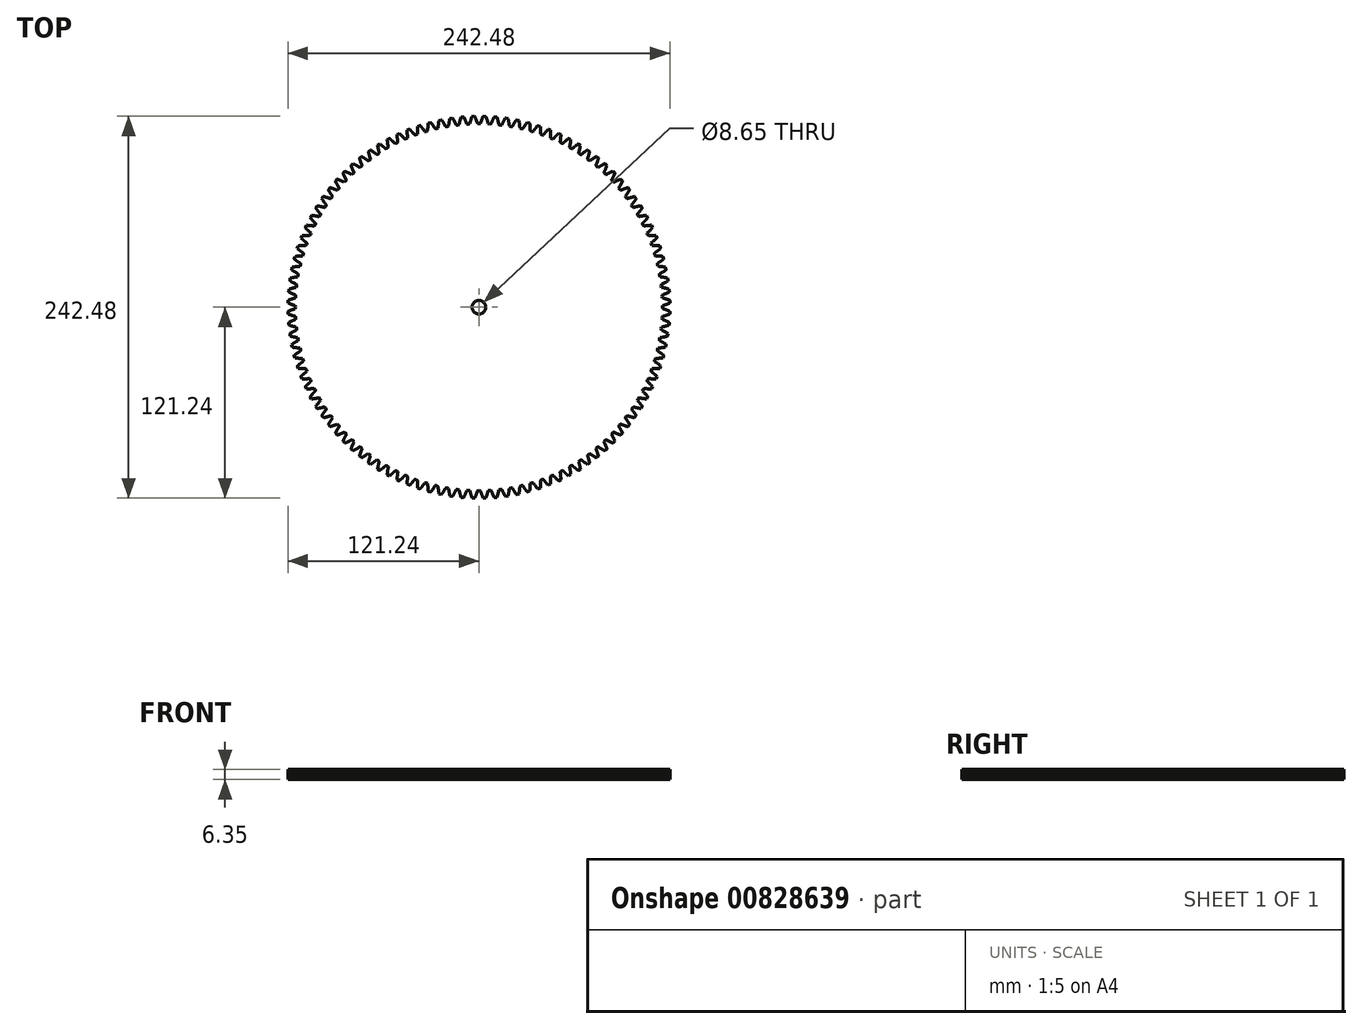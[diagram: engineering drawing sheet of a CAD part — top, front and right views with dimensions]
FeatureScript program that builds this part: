
annotation { "Feature Type Name" : "Feature", "Feature Type Description" : "" }
export const myFeature = defineFeature(function(context is Context, id is Id, definition is map)
    precondition{}
    {
        {
            var Q0;
            Q0=qCreatedBy(makeId("Top.planeOp"),FACE);
            var sketch = newSketch(context, id + "F0", { "sketchPlane" : qUnion([Q0])});
            skLineSegment(sketch, "E0", {"start": v(116.53, 0) * mm, "end": v(116.7, 0.97) * mm});
            skLineSegment(sketch, "E1", {"start": v(116.7, 0.97) * mm, "end": v(116.9, 1.03) * mm});
            skLineSegment(sketch, "E2", {"start": v(116.9, 1.03) * mm, "end": v(117.01, 1.06) * mm});
            skLineSegment(sketch, "E3", {"start": v(117.01, 1.06) * mm, "end": v(117.22, 1.13) * mm});
            skLineSegment(sketch, "E4", {"start": v(117.22, 1.13) * mm, "end": v(117.33, 1.17) * mm});
            skLineSegment(sketch, "E5", {"start": v(117.33, 1.17) * mm, "end": v(117.44, 1.2) * mm});
            skLineSegment(sketch, "E6", {"start": v(117.44, 1.2) * mm, "end": v(117.55, 1.24) * mm});
            skLineSegment(sketch, "E7", {"start": v(117.55, 1.24) * mm, "end": v(117.66, 1.28) * mm});
            skLineSegment(sketch, "E8", {"start": v(117.66, 1.28) * mm, "end": v(117.78, 1.31) * mm});
            skLineSegment(sketch, "E9", {"start": v(117.78, 1.31) * mm, "end": v(117.89, 1.35) * mm});
            skLineSegment(sketch, "E10", {"start": v(117.89, 1.35) * mm, "end": v(118, 1.4) * mm});
            skLineSegment(sketch, "E11", {"start": v(118, 1.4) * mm, "end": v(118.12, 1.43) * mm});
            skLineSegment(sketch, "E12", {"start": v(118.12, 1.43) * mm, "end": v(118.23, 1.47) * mm});
            skLineSegment(sketch, "E13", {"start": v(118.23, 1.47) * mm, "end": v(118.35, 1.52) * mm});
            skLineSegment(sketch, "E14", {"start": v(118.35, 1.52) * mm, "end": v(118.59, 1.6) * mm});
            skLineSegment(sketch, "E15", {"start": v(118.59, 1.6) * mm, "end": v(118.7, 1.65) * mm});
            skLineSegment(sketch, "E16", {"start": v(118.7, 1.65) * mm, "end": v(118.95, 1.74) * mm});
            skLineSegment(sketch, "E17", {"start": v(118.95, 1.74) * mm, "end": v(119.07, 1.78) * mm});
            skLineSegment(sketch, "E18", {"start": v(119.07, 1.78) * mm, "end": v(119.32, 1.88) * mm});
            skLineSegment(sketch, "E19", {"start": v(119.32, 1.88) * mm, "end": v(119.45, 1.93) * mm});
            skLineSegment(sketch, "E20", {"start": v(119.45, 1.93) * mm, "end": v(119.57, 1.98) * mm});
            skLineSegment(sketch, "E21", {"start": v(119.57, 1.98) * mm, "end": v(119.7, 2.03) * mm});
            skLineSegment(sketch, "E22", {"start": v(119.7, 2.03) * mm, "end": v(119.96, 2.13) * mm});
            skLineSegment(sketch, "E23", {"start": v(119.96, 2.13) * mm, "end": v(120.09, 2.19) * mm});
            skLineSegment(sketch, "E24", {"start": v(120.09, 2.19) * mm, "end": v(120.22, 2.24) * mm});
            skLineSegment(sketch, "E25", {"start": v(120.22, 2.24) * mm, "end": v(120.48, 2.35) * mm});
            skLineSegment(sketch, "E26", {"start": v(120.48, 2.35) * mm, "end": v(120.62, 2.4) * mm});
            skLineSegment(sketch, "E27", {"start": v(120.62, 2.4) * mm, "end": v(120.75, 2.47) * mm});
            skLineSegment(sketch, "E28", {"start": v(120.75, 2.47) * mm, "end": v(120.89, 2.52) * mm});
            skLineSegment(sketch, "E29", {"start": v(120.89, 2.52) * mm, "end": v(121.02, 2.58) * mm});
            skLineSegment(sketch, "E30", {"start": v(121.02, 2.58) * mm, "end": v(121.16, 2.64) * mm});
            skLineSegment(sketch, "E31", {"start": v(121.16, 2.64) * mm, "end": v(121.24, 2.7) * mm});
            skLineSegment(sketch, "E32", {"start": v(121.24, 2.7) * mm, "end": v(121.19, 4.36) * mm});
            skLineSegment(sketch, "E33", {"start": v(121.19, 4.36) * mm, "end": v(121.1, 4.42) * mm});
            skLineSegment(sketch, "E34", {"start": v(121.1, 4.42) * mm, "end": v(120.97, 4.47) * mm});
            skLineSegment(sketch, "E35", {"start": v(120.97, 4.47) * mm, "end": v(120.83, 4.52) * mm});
            skLineSegment(sketch, "E36", {"start": v(120.83, 4.52) * mm, "end": v(120.69, 4.57) * mm});
            skLineSegment(sketch, "E37", {"start": v(120.69, 4.57) * mm, "end": v(120.55, 4.62) * mm});
            skLineSegment(sketch, "E38", {"start": v(120.55, 4.62) * mm, "end": v(120.28, 4.72) * mm});
            skLineSegment(sketch, "E39", {"start": v(120.28, 4.72) * mm, "end": v(120.15, 4.77) * mm});
            skLineSegment(sketch, "E40", {"start": v(120.15, 4.77) * mm, "end": v(120.01, 4.81) * mm});
            skLineSegment(sketch, "E41", {"start": v(120.01, 4.81) * mm, "end": v(119.75, 4.9) * mm});
            skLineSegment(sketch, "E42", {"start": v(119.75, 4.9) * mm, "end": v(119.61, 4.95) * mm});
            skLineSegment(sketch, "E43", {"start": v(119.61, 4.95) * mm, "end": v(119.48, 5) * mm});
            skLineSegment(sketch, "E44", {"start": v(119.48, 5) * mm, "end": v(119.36, 5.03) * mm});
            skLineSegment(sketch, "E45", {"start": v(119.36, 5.03) * mm, "end": v(119.1, 5.12) * mm});
            skLineSegment(sketch, "E46", {"start": v(119.1, 5.12) * mm, "end": v(118.97, 5.16) * mm});
            skLineSegment(sketch, "E47", {"start": v(118.97, 5.16) * mm, "end": v(118.85, 5.2) * mm});
            skLineSegment(sketch, "E48", {"start": v(118.85, 5.2) * mm, "end": v(118.6, 5.27) * mm});
            skLineSegment(sketch, "E49", {"start": v(118.6, 5.27) * mm, "end": v(118.48, 5.3) * mm});
            skLineSegment(sketch, "E50", {"start": v(118.48, 5.3) * mm, "end": v(118.36, 5.35) * mm});
            skLineSegment(sketch, "E51", {"start": v(118.36, 5.35) * mm, "end": v(118.24, 5.38) * mm});
            skLineSegment(sketch, "E52", {"start": v(118.24, 5.38) * mm, "end": v(118.12, 5.42) * mm});
            skLineSegment(sketch, "E53", {"start": v(118.12, 5.42) * mm, "end": v(118, 5.45) * mm});
            skLineSegment(sketch, "E54", {"start": v(118, 5.45) * mm, "end": v(117.88, 5.48) * mm});
            skLineSegment(sketch, "E55", {"start": v(117.88, 5.48) * mm, "end": v(117.77, 5.52) * mm});
            skLineSegment(sketch, "E56", {"start": v(117.77, 5.52) * mm, "end": v(117.65, 5.55) * mm});
            skLineSegment(sketch, "E57", {"start": v(117.65, 5.55) * mm, "end": v(117.54, 5.58) * mm});
            skLineSegment(sketch, "E58", {"start": v(117.54, 5.58) * mm, "end": v(117.42, 5.61) * mm});
            skLineSegment(sketch, "E59", {"start": v(117.42, 5.61) * mm, "end": v(117.31, 5.64) * mm});
            skLineSegment(sketch, "E60", {"start": v(117.31, 5.64) * mm, "end": v(117.1, 5.7) * mm});
            skLineSegment(sketch, "E61", {"start": v(117.1, 5.7) * mm, "end": v(116.98, 5.73) * mm});
            skLineSegment(sketch, "E62", {"start": v(116.98, 5.73) * mm, "end": v(116.87, 5.76) * mm});
            skLineSegment(sketch, "E63", {"start": v(116.87, 5.76) * mm, "end": v(116.66, 5.8) * mm});
            skLineSegment(sketch, "E64", {"start": v(116.66, 5.8) * mm, "end": v(116.56, 5.83) * mm});
            skLineSegment(sketch, "E65", {"start": v(116.56, 5.83) * mm, "end": v(116.33, 6.78) * mm});
            skLineSegment(sketch, "E66", {"start": v(116.33, 6.78) * mm, "end": v(116.45, 7.75) * mm});
            skLineSegment(sketch, "E67", {"start": v(116.45, 7.75) * mm, "end": v(116.55, 7.79) * mm});
            skLineSegment(sketch, "E68", {"start": v(116.55, 7.79) * mm, "end": v(116.65, 7.83) * mm});
            skLineSegment(sketch, "E69", {"start": v(116.65, 7.83) * mm, "end": v(116.75, 7.86) * mm});
            skLineSegment(sketch, "E70", {"start": v(116.75, 7.86) * mm, "end": v(116.86, 7.9) * mm});
            skLineSegment(sketch, "E71", {"start": v(116.86, 7.9) * mm, "end": v(116.96, 7.95) * mm});
            skLineSegment(sketch, "E72", {"start": v(116.96, 7.95) * mm, "end": v(117.17, 8.03) * mm});
            skLineSegment(sketch, "E73", {"start": v(117.17, 8.03) * mm, "end": v(117.28, 8.07) * mm});
            skLineSegment(sketch, "E74", {"start": v(117.28, 8.07) * mm, "end": v(117.39, 8.12) * mm});
            skLineSegment(sketch, "E75", {"start": v(117.39, 8.12) * mm, "end": v(117.5, 8.16) * mm});
            skLineSegment(sketch, "E76", {"start": v(117.5, 8.16) * mm, "end": v(117.61, 8.2) * mm});
            skLineSegment(sketch, "E77", {"start": v(117.61, 8.2) * mm, "end": v(117.72, 8.25) * mm});
            skLineSegment(sketch, "E78", {"start": v(117.72, 8.25) * mm, "end": v(117.95, 8.35) * mm});
            skLineSegment(sketch, "E79", {"start": v(117.95, 8.35) * mm, "end": v(118.06, 8.4) * mm});
            skLineSegment(sketch, "E80", {"start": v(118.06, 8.4) * mm, "end": v(118.3, 8.5) * mm});
            skLineSegment(sketch, "E81", {"start": v(118.3, 8.5) * mm, "end": v(118.41, 8.55) * mm});
            skLineSegment(sketch, "E82", {"start": v(118.41, 8.55) * mm, "end": v(118.65, 8.65) * mm});
            skLineSegment(sketch, "E83", {"start": v(118.65, 8.65) * mm, "end": v(118.77, 8.7) * mm});
            skLineSegment(sketch, "E84", {"start": v(118.77, 8.7) * mm, "end": v(118.89, 8.76) * mm});
            skLineSegment(sketch, "E85", {"start": v(118.89, 8.76) * mm, "end": v(119.01, 8.81) * mm});
            skLineSegment(sketch, "E86", {"start": v(119.01, 8.81) * mm, "end": v(119.13, 8.87) * mm});
            skLineSegment(sketch, "E87", {"start": v(119.13, 8.87) * mm, "end": v(119.26, 8.93) * mm});
            skLineSegment(sketch, "E88", {"start": v(119.26, 8.93) * mm, "end": v(119.38, 8.99) * mm});
            skLineSegment(sketch, "E89", {"start": v(119.38, 8.99) * mm, "end": v(119.5, 9.04) * mm});
            skLineSegment(sketch, "E90", {"start": v(119.5, 9.04) * mm, "end": v(119.63, 9.1) * mm});
            skLineSegment(sketch, "E91", {"start": v(119.63, 9.1) * mm, "end": v(119.76, 9.17) * mm});
            skLineSegment(sketch, "E92", {"start": v(119.76, 9.17) * mm, "end": v(119.89, 9.23) * mm});
            skLineSegment(sketch, "E93", {"start": v(119.89, 9.23) * mm, "end": v(120.01, 9.29) * mm});
            skLineSegment(sketch, "E94", {"start": v(120.01, 9.29) * mm, "end": v(120.14, 9.35) * mm});
            skLineSegment(sketch, "E95", {"start": v(120.14, 9.35) * mm, "end": v(120.27, 9.42) * mm});
            skLineSegment(sketch, "E96", {"start": v(120.27, 9.42) * mm, "end": v(120.4, 9.48) * mm});
            skLineSegment(sketch, "E97", {"start": v(120.4, 9.48) * mm, "end": v(120.54, 9.55) * mm});
            skLineSegment(sketch, "E98", {"start": v(120.54, 9.55) * mm, "end": v(120.67, 9.62) * mm});
            skLineSegment(sketch, "E99", {"start": v(120.67, 9.62) * mm, "end": v(120.8, 9.68) * mm});
            skLineSegment(sketch, "E100", {"start": v(120.8, 9.68) * mm, "end": v(120.87, 9.75) * mm});
            skLineSegment(sketch, "E101", {"start": v(120.87, 9.75) * mm, "end": v(120.73, 11.4) * mm});
            skLineSegment(sketch, "E102", {"start": v(120.73, 11.4) * mm, "end": v(120.65, 11.45) * mm});
            skLineSegment(sketch, "E103", {"start": v(120.65, 11.45) * mm, "end": v(120.5, 11.5) * mm});
            skLineSegment(sketch, "E104", {"start": v(120.5, 11.5) * mm, "end": v(120.22, 11.58) * mm});
            skLineSegment(sketch, "E105", {"start": v(120.22, 11.58) * mm, "end": v(120.08, 11.62) * mm});
            skLineSegment(sketch, "E106", {"start": v(120.08, 11.62) * mm, "end": v(119.94, 11.66) * mm});
            skLineSegment(sketch, "E107", {"start": v(119.94, 11.66) * mm, "end": v(119.66, 11.74) * mm});
            skLineSegment(sketch, "E108", {"start": v(119.66, 11.74) * mm, "end": v(119.53, 11.78) * mm});
            skLineSegment(sketch, "E109", {"start": v(119.53, 11.78) * mm, "end": v(119.26, 11.86) * mm});
            skLineSegment(sketch, "E110", {"start": v(119.26, 11.86) * mm, "end": v(119.12, 11.9) * mm});
            skLineSegment(sketch, "E111", {"start": v(119.12, 11.9) * mm, "end": v(119, 11.93) * mm});
            skLineSegment(sketch, "E112", {"start": v(119, 11.93) * mm, "end": v(118.86, 11.97) * mm});
            skLineSegment(sketch, "E113", {"start": v(118.86, 11.97) * mm, "end": v(118.73, 12) * mm});
            skLineSegment(sketch, "E114", {"start": v(118.73, 12) * mm, "end": v(118.6, 12.03) * mm});
            skLineSegment(sketch, "E115", {"start": v(118.6, 12.03) * mm, "end": v(118.47, 12.06) * mm});
            skLineSegment(sketch, "E116", {"start": v(118.47, 12.06) * mm, "end": v(118.35, 12.1) * mm});
            skLineSegment(sketch, "E117", {"start": v(118.35, 12.1) * mm, "end": v(118.22, 12.13) * mm});
            skLineSegment(sketch, "E118", {"start": v(118.22, 12.13) * mm, "end": v(118.1, 12.16) * mm});
            skLineSegment(sketch, "E119", {"start": v(118.1, 12.16) * mm, "end": v(117.97, 12.19) * mm});
            skLineSegment(sketch, "E120", {"start": v(117.97, 12.19) * mm, "end": v(117.85, 12.22) * mm});
            skLineSegment(sketch, "E121", {"start": v(117.85, 12.22) * mm, "end": v(117.72, 12.25) * mm});
            skLineSegment(sketch, "E122", {"start": v(117.72, 12.25) * mm, "end": v(117.6, 12.28) * mm});
            skLineSegment(sketch, "E123", {"start": v(117.6, 12.28) * mm, "end": v(117.48, 12.3) * mm});
            skLineSegment(sketch, "E124", {"start": v(117.48, 12.3) * mm, "end": v(117.37, 12.33) * mm});
            skLineSegment(sketch, "E125", {"start": v(117.37, 12.33) * mm, "end": v(117.25, 12.36) * mm});
            skLineSegment(sketch, "E126", {"start": v(117.25, 12.36) * mm, "end": v(117.13, 12.38) * mm});
            skLineSegment(sketch, "E127", {"start": v(117.13, 12.38) * mm, "end": v(117.01, 12.4) * mm});
            skLineSegment(sketch, "E128", {"start": v(117.01, 12.4) * mm, "end": v(116.9, 12.43) * mm});
            skLineSegment(sketch, "E129", {"start": v(116.9, 12.43) * mm, "end": v(116.79, 12.45) * mm});
            skLineSegment(sketch, "E130", {"start": v(116.79, 12.45) * mm, "end": v(116.67, 12.48) * mm});
            skLineSegment(sketch, "E131", {"start": v(116.67, 12.48) * mm, "end": v(116.56, 12.5) * mm});
            skLineSegment(sketch, "E132", {"start": v(116.56, 12.5) * mm, "end": v(116.45, 12.52) * mm});
            skLineSegment(sketch, "E133", {"start": v(116.45, 12.52) * mm, "end": v(116.23, 12.56) * mm});
            skLineSegment(sketch, "E134", {"start": v(116.23, 12.56) * mm, "end": v(116.13, 12.58) * mm});
            skLineSegment(sketch, "E135", {"start": v(116.13, 12.58) * mm, "end": v(116.02, 12.6) * mm});
            skLineSegment(sketch, "E136", {"start": v(116.02, 12.6) * mm, "end": v(115.74, 13.53) * mm});
            skLineSegment(sketch, "E137", {"start": v(115.74, 13.53) * mm, "end": v(115.8, 14.5) * mm});
            skLineSegment(sketch, "E138", {"start": v(115.8, 14.5) * mm, "end": v(116, 14.6) * mm});
            skLineSegment(sketch, "E139", {"start": v(116, 14.6) * mm, "end": v(116.1, 14.64) * mm});
            skLineSegment(sketch, "E140", {"start": v(116.1, 14.64) * mm, "end": v(116.2, 14.69) * mm});
            skLineSegment(sketch, "E141", {"start": v(116.2, 14.69) * mm, "end": v(116.3, 14.73) * mm});
            skLineSegment(sketch, "E142", {"start": v(116.3, 14.73) * mm, "end": v(116.4, 14.78) * mm});
            skLineSegment(sketch, "E143", {"start": v(116.4, 14.78) * mm, "end": v(116.5, 14.83) * mm});
            skLineSegment(sketch, "E144", {"start": v(116.5, 14.83) * mm, "end": v(116.61, 14.88) * mm});
            skLineSegment(sketch, "E145", {"start": v(116.61, 14.88) * mm, "end": v(116.72, 14.93) * mm});
            skLineSegment(sketch, "E146", {"start": v(116.72, 14.93) * mm, "end": v(116.83, 14.98) * mm});
            skLineSegment(sketch, "E147", {"start": v(116.83, 14.98) * mm, "end": v(116.94, 15.03) * mm});
            skLineSegment(sketch, "E148", {"start": v(116.94, 15.03) * mm, "end": v(117.04, 15.08) * mm});
            skLineSegment(sketch, "E149", {"start": v(117.04, 15.08) * mm, "end": v(117.26, 15.2) * mm});
            skLineSegment(sketch, "E150", {"start": v(117.26, 15.2) * mm, "end": v(117.37, 15.25) * mm});
            skLineSegment(sketch, "E151", {"start": v(117.37, 15.25) * mm, "end": v(117.49, 15.3) * mm});
            skLineSegment(sketch, "E152", {"start": v(117.49, 15.3) * mm, "end": v(117.6, 15.36) * mm});
            skLineSegment(sketch, "E153", {"start": v(117.6, 15.36) * mm, "end": v(117.83, 15.47) * mm});
            skLineSegment(sketch, "E154", {"start": v(117.83, 15.47) * mm, "end": v(117.94, 15.53) * mm});
            skLineSegment(sketch, "E155", {"start": v(117.94, 15.53) * mm, "end": v(118.18, 15.66) * mm});
            skLineSegment(sketch, "E156", {"start": v(118.18, 15.66) * mm, "end": v(118.3, 15.72) * mm});
            skLineSegment(sketch, "E157", {"start": v(118.3, 15.72) * mm, "end": v(118.41, 15.78) * mm});
            skLineSegment(sketch, "E158", {"start": v(118.41, 15.78) * mm, "end": v(118.65, 15.91) * mm});
            skLineSegment(sketch, "E159", {"start": v(118.65, 15.91) * mm, "end": v(118.78, 15.98) * mm});
            skLineSegment(sketch, "E160", {"start": v(118.78, 15.98) * mm, "end": v(118.9, 16.04) * mm});
            skLineSegment(sketch, "E161", {"start": v(118.9, 16.04) * mm, "end": v(119.02, 16.11) * mm});
            skLineSegment(sketch, "E162", {"start": v(119.02, 16.11) * mm, "end": v(119.15, 16.18) * mm});
            skLineSegment(sketch, "E163", {"start": v(119.15, 16.18) * mm, "end": v(119.27, 16.25) * mm});
            skLineSegment(sketch, "E164", {"start": v(119.27, 16.25) * mm, "end": v(119.52, 16.4) * mm});
            skLineSegment(sketch, "E165", {"start": v(119.52, 16.4) * mm, "end": v(119.65, 16.47) * mm});
            skLineSegment(sketch, "E166", {"start": v(119.65, 16.47) * mm, "end": v(119.78, 16.54) * mm});
            skLineSegment(sketch, "E167", {"start": v(119.78, 16.54) * mm, "end": v(119.9, 16.62) * mm});
            skLineSegment(sketch, "E168", {"start": v(119.9, 16.62) * mm, "end": v(120.03, 16.7) * mm});
            skLineSegment(sketch, "E169", {"start": v(120.03, 16.7) * mm, "end": v(120.1, 16.76) * mm});
            skLineSegment(sketch, "E170", {"start": v(120.1, 16.76) * mm, "end": v(119.86, 18.4) * mm});
            skLineSegment(sketch, "E171", {"start": v(119.86, 18.4) * mm, "end": v(119.78, 18.45) * mm});
            skLineSegment(sketch, "E172", {"start": v(119.78, 18.45) * mm, "end": v(119.63, 18.48) * mm});
            skLineSegment(sketch, "E173", {"start": v(119.63, 18.48) * mm, "end": v(119.49, 18.52) * mm});
            skLineSegment(sketch, "E174", {"start": v(119.49, 18.52) * mm, "end": v(119.34, 18.55) * mm});
            skLineSegment(sketch, "E175", {"start": v(119.34, 18.55) * mm, "end": v(119.2, 18.59) * mm});
            skLineSegment(sketch, "E176", {"start": v(119.2, 18.59) * mm, "end": v(119.06, 18.62) * mm});
            skLineSegment(sketch, "E177", {"start": v(119.06, 18.62) * mm, "end": v(118.92, 18.65) * mm});
            skLineSegment(sketch, "E178", {"start": v(118.92, 18.65) * mm, "end": v(118.78, 18.68) * mm});
            skLineSegment(sketch, "E179", {"start": v(118.78, 18.68) * mm, "end": v(118.64, 18.71) * mm});
            skLineSegment(sketch, "E180", {"start": v(118.64, 18.71) * mm, "end": v(118.5, 18.74) * mm});
            skLineSegment(sketch, "E181", {"start": v(118.5, 18.74) * mm, "end": v(118.37, 18.77) * mm});
            skLineSegment(sketch, "E182", {"start": v(118.37, 18.77) * mm, "end": v(118.23, 18.8) * mm});
            skLineSegment(sketch, "E183", {"start": v(118.23, 18.8) * mm, "end": v(117.96, 18.86) * mm});
            skLineSegment(sketch, "E184", {"start": v(117.96, 18.86) * mm, "end": v(117.83, 18.88) * mm});
            skLineSegment(sketch, "E185", {"start": v(117.83, 18.88) * mm, "end": v(117.7, 18.9) * mm});
            skLineSegment(sketch, "E186", {"start": v(117.7, 18.9) * mm, "end": v(117.44, 18.96) * mm});
            skLineSegment(sketch, "E187", {"start": v(117.44, 18.96) * mm, "end": v(117.31, 18.98) * mm});
            skLineSegment(sketch, "E188", {"start": v(117.31, 18.98) * mm, "end": v(117.19, 19) * mm});
            skLineSegment(sketch, "E189", {"start": v(117.19, 19) * mm, "end": v(117.06, 19.03) * mm});
            skLineSegment(sketch, "E190", {"start": v(117.06, 19.03) * mm, "end": v(116.81, 19.07) * mm});
            skLineSegment(sketch, "E191", {"start": v(116.81, 19.07) * mm, "end": v(116.7, 19.1) * mm});
            skLineSegment(sketch, "E192", {"start": v(116.7, 19.1) * mm, "end": v(116.57, 19.11) * mm});
            skLineSegment(sketch, "E193", {"start": v(116.57, 19.11) * mm, "end": v(116.33, 19.15) * mm});
            skLineSegment(sketch, "E194", {"start": v(116.33, 19.15) * mm, "end": v(116.1, 19.19) * mm});
            skLineSegment(sketch, "E195", {"start": v(116.1, 19.19) * mm, "end": v(115.98, 19.2) * mm});
            skLineSegment(sketch, "E196", {"start": v(115.98, 19.2) * mm, "end": v(115.86, 19.22) * mm});
            skLineSegment(sketch, "E197", {"start": v(115.86, 19.22) * mm, "end": v(115.64, 19.26) * mm});
            skLineSegment(sketch, "E198", {"start": v(115.64, 19.26) * mm, "end": v(115.53, 19.27) * mm});
            skLineSegment(sketch, "E199", {"start": v(115.53, 19.27) * mm, "end": v(115.42, 19.28) * mm});
            skLineSegment(sketch, "E200", {"start": v(115.42, 19.28) * mm, "end": v(115.3, 19.3) * mm});
            skLineSegment(sketch, "E201", {"start": v(115.3, 19.3) * mm, "end": v(115.2, 19.31) * mm});
            skLineSegment(sketch, "E202", {"start": v(115.2, 19.31) * mm, "end": v(115.1, 19.33) * mm});
            skLineSegment(sketch, "E203", {"start": v(115.1, 19.33) * mm, "end": v(114.76, 20.24) * mm});
            skLineSegment(sketch, "E204", {"start": v(114.76, 20.24) * mm, "end": v(114.76, 21.22) * mm});
            skLineSegment(sketch, "E205", {"start": v(114.76, 21.22) * mm, "end": v(114.85, 21.26) * mm});
            skLineSegment(sketch, "E206", {"start": v(114.85, 21.26) * mm, "end": v(114.95, 21.31) * mm});
            skLineSegment(sketch, "E207", {"start": v(114.95, 21.31) * mm, "end": v(115.05, 21.37) * mm});
            skLineSegment(sketch, "E208", {"start": v(115.05, 21.37) * mm, "end": v(115.15, 21.42) * mm});
            skLineSegment(sketch, "E209", {"start": v(115.15, 21.42) * mm, "end": v(115.25, 21.47) * mm});
            skLineSegment(sketch, "E210", {"start": v(115.25, 21.47) * mm, "end": v(115.35, 21.52) * mm});
            skLineSegment(sketch, "E211", {"start": v(115.35, 21.52) * mm, "end": v(115.45, 21.58) * mm});
            skLineSegment(sketch, "E212", {"start": v(115.45, 21.58) * mm, "end": v(115.55, 21.63) * mm});
            skLineSegment(sketch, "E213", {"start": v(115.55, 21.63) * mm, "end": v(115.76, 21.75) * mm});
            skLineSegment(sketch, "E214", {"start": v(115.76, 21.75) * mm, "end": v(115.86, 21.8) * mm});
            skLineSegment(sketch, "E215", {"start": v(115.86, 21.8) * mm, "end": v(115.97, 21.86) * mm});
            skLineSegment(sketch, "E216", {"start": v(115.97, 21.86) * mm, "end": v(116.07, 21.92) * mm});
            skLineSegment(sketch, "E217", {"start": v(116.07, 21.92) * mm, "end": v(116.18, 21.98) * mm});
            skLineSegment(sketch, "E218", {"start": v(116.18, 21.98) * mm, "end": v(116.4, 22.1) * mm});
            skLineSegment(sketch, "E219", {"start": v(116.4, 22.1) * mm, "end": v(116.5, 22.17) * mm});
            skLineSegment(sketch, "E220", {"start": v(116.5, 22.17) * mm, "end": v(116.62, 22.23) * mm});
            skLineSegment(sketch, "E221", {"start": v(116.62, 22.23) * mm, "end": v(116.73, 22.3) * mm});
            skLineSegment(sketch, "E222", {"start": v(116.73, 22.3) * mm, "end": v(116.84, 22.37) * mm});
            skLineSegment(sketch, "E223", {"start": v(116.84, 22.37) * mm, "end": v(117.07, 22.5) * mm});
            skLineSegment(sketch, "E224", {"start": v(117.07, 22.5) * mm, "end": v(117.18, 22.57) * mm});
            skLineSegment(sketch, "E225", {"start": v(117.18, 22.57) * mm, "end": v(117.3, 22.64) * mm});
            skLineSegment(sketch, "E226", {"start": v(117.3, 22.64) * mm, "end": v(117.53, 22.78) * mm});
            skLineSegment(sketch, "E227", {"start": v(117.53, 22.78) * mm, "end": v(117.65, 22.86) * mm});
            skLineSegment(sketch, "E228", {"start": v(117.65, 22.86) * mm, "end": v(117.76, 22.93) * mm});
            skLineSegment(sketch, "E229", {"start": v(117.76, 22.93) * mm, "end": v(117.88, 23) * mm});
            skLineSegment(sketch, "E230", {"start": v(117.88, 23) * mm, "end": v(118, 23.08) * mm});
            skLineSegment(sketch, "E231", {"start": v(118, 23.08) * mm, "end": v(118.25, 23.24) * mm});
            skLineSegment(sketch, "E232", {"start": v(118.25, 23.24) * mm, "end": v(118.37, 23.32) * mm});
            skLineSegment(sketch, "E233", {"start": v(118.37, 23.32) * mm, "end": v(118.49, 23.4) * mm});
            skLineSegment(sketch, "E234", {"start": v(118.49, 23.4) * mm, "end": v(118.61, 23.48) * mm});
            skLineSegment(sketch, "E235", {"start": v(118.61, 23.48) * mm, "end": v(118.74, 23.56) * mm});
            skLineSegment(sketch, "E236", {"start": v(118.74, 23.56) * mm, "end": v(118.86, 23.64) * mm});
            skLineSegment(sketch, "E237", {"start": v(118.86, 23.64) * mm, "end": v(118.93, 23.72) * mm});
            skLineSegment(sketch, "E238", {"start": v(118.93, 23.72) * mm, "end": v(118.59, 25.34) * mm});
            skLineSegment(sketch, "E239", {"start": v(118.59, 25.34) * mm, "end": v(118.5, 25.38) * mm});
            skLineSegment(sketch, "E240", {"start": v(118.5, 25.38) * mm, "end": v(118.35, 25.4) * mm});
            skLineSegment(sketch, "E241", {"start": v(118.35, 25.4) * mm, "end": v(118.2, 25.44) * mm});
            skLineSegment(sketch, "E242", {"start": v(118.2, 25.44) * mm, "end": v(118.06, 25.46) * mm});
            skLineSegment(sketch, "E243", {"start": v(118.06, 25.46) * mm, "end": v(117.92, 25.49) * mm});
            skLineSegment(sketch, "E244", {"start": v(117.92, 25.49) * mm, "end": v(117.78, 25.51) * mm});
            skLineSegment(sketch, "E245", {"start": v(117.78, 25.51) * mm, "end": v(117.5, 25.56) * mm});
            skLineSegment(sketch, "E246", {"start": v(117.5, 25.56) * mm, "end": v(117.35, 25.58) * mm});
            skLineSegment(sketch, "E247", {"start": v(117.35, 25.58) * mm, "end": v(117.21, 25.6) * mm});
            skLineSegment(sketch, "E248", {"start": v(117.21, 25.6) * mm, "end": v(117.08, 25.62) * mm});
            skLineSegment(sketch, "E249", {"start": v(117.08, 25.62) * mm, "end": v(116.94, 25.64) * mm});
            skLineSegment(sketch, "E250", {"start": v(116.94, 25.64) * mm, "end": v(116.8, 25.66) * mm});
            skLineSegment(sketch, "E251", {"start": v(116.8, 25.66) * mm, "end": v(116.54, 25.7) * mm});
            skLineSegment(sketch, "E252", {"start": v(116.54, 25.7) * mm, "end": v(116.4, 25.72) * mm});
            skLineSegment(sketch, "E253", {"start": v(116.4, 25.72) * mm, "end": v(116.27, 25.74) * mm});
            skLineSegment(sketch, "E254", {"start": v(116.27, 25.74) * mm, "end": v(116.14, 25.75) * mm});
            skLineSegment(sketch, "E255", {"start": v(116.14, 25.75) * mm, "end": v(116.01, 25.77) * mm});
            skLineSegment(sketch, "E256", {"start": v(116.01, 25.77) * mm, "end": v(115.88, 25.79) * mm});
            skLineSegment(sketch, "E257", {"start": v(115.88, 25.79) * mm, "end": v(115.63, 25.82) * mm});
            skLineSegment(sketch, "E258", {"start": v(115.63, 25.82) * mm, "end": v(115.38, 25.85) * mm});
            skLineSegment(sketch, "E259", {"start": v(115.38, 25.85) * mm, "end": v(115.26, 25.86) * mm});
            skLineSegment(sketch, "E260", {"start": v(115.26, 25.86) * mm, "end": v(115.02, 25.88) * mm});
            skLineSegment(sketch, "E261", {"start": v(115.02, 25.88) * mm, "end": v(114.9, 25.9) * mm});
            skLineSegment(sketch, "E262", {"start": v(114.9, 25.9) * mm, "end": v(114.67, 25.92) * mm});
            skLineSegment(sketch, "E263", {"start": v(114.67, 25.92) * mm, "end": v(114.55, 25.93) * mm});
            skLineSegment(sketch, "E264", {"start": v(114.55, 25.93) * mm, "end": v(114.44, 25.94) * mm});
            skLineSegment(sketch, "E265", {"start": v(114.44, 25.94) * mm, "end": v(114.21, 25.96) * mm});
            skLineSegment(sketch, "E266", {"start": v(114.21, 25.96) * mm, "end": v(114.1, 25.96) * mm});
            skLineSegment(sketch, "E267", {"start": v(114.1, 25.96) * mm, "end": v(113.99, 25.97) * mm});
            skLineSegment(sketch, "E268", {"start": v(113.99, 25.97) * mm, "end": v(113.88, 25.98) * mm});
            skLineSegment(sketch, "E269", {"start": v(113.88, 25.98) * mm, "end": v(113.77, 25.99) * mm});
            skLineSegment(sketch, "E270", {"start": v(113.77, 25.99) * mm, "end": v(113.38, 26.88) * mm});
            skLineSegment(sketch, "E271", {"start": v(113.38, 26.88) * mm, "end": v(113.33, 27.85) * mm});
            skLineSegment(sketch, "E272", {"start": v(113.33, 27.85) * mm, "end": v(113.42, 27.9) * mm});
            skLineSegment(sketch, "E273", {"start": v(113.42, 27.9) * mm, "end": v(113.52, 27.96) * mm});
            skLineSegment(sketch, "E274", {"start": v(113.52, 27.96) * mm, "end": v(113.61, 28.02) * mm});
            skLineSegment(sketch, "E275", {"start": v(113.61, 28.02) * mm, "end": v(113.7, 28.08) * mm});
            skLineSegment(sketch, "E276", {"start": v(113.7, 28.08) * mm, "end": v(113.8, 28.13) * mm});
            skLineSegment(sketch, "E277", {"start": v(113.8, 28.13) * mm, "end": v(113.9, 28.2) * mm});
            skLineSegment(sketch, "E278", {"start": v(113.9, 28.2) * mm, "end": v(114.1, 28.31) * mm});
            skLineSegment(sketch, "E279", {"start": v(114.1, 28.31) * mm, "end": v(114.2, 28.38) * mm});
            skLineSegment(sketch, "E280", {"start": v(114.2, 28.38) * mm, "end": v(114.3, 28.44) * mm});
            skLineSegment(sketch, "E281", {"start": v(114.3, 28.44) * mm, "end": v(114.4, 28.5) * mm});
            skLineSegment(sketch, "E282", {"start": v(114.4, 28.5) * mm, "end": v(114.5, 28.57) * mm});
            skLineSegment(sketch, "E283", {"start": v(114.5, 28.57) * mm, "end": v(114.6, 28.63) * mm});
            skLineSegment(sketch, "E284", {"start": v(114.6, 28.63) * mm, "end": v(114.7, 28.7) * mm});
            skLineSegment(sketch, "E285", {"start": v(114.7, 28.7) * mm, "end": v(114.81, 28.77) * mm});
            skLineSegment(sketch, "E286", {"start": v(114.81, 28.77) * mm, "end": v(114.92, 28.84) * mm});
            skLineSegment(sketch, "E287", {"start": v(114.92, 28.84) * mm, "end": v(115.13, 28.98) * mm});
            skLineSegment(sketch, "E288", {"start": v(115.13, 28.98) * mm, "end": v(115.24, 29.05) * mm});
            skLineSegment(sketch, "E289", {"start": v(115.24, 29.05) * mm, "end": v(115.34, 29.12) * mm});
            skLineSegment(sketch, "E290", {"start": v(115.34, 29.12) * mm, "end": v(115.45, 29.2) * mm});
            skLineSegment(sketch, "E291", {"start": v(115.45, 29.2) * mm, "end": v(115.56, 29.27) * mm});
            skLineSegment(sketch, "E292", {"start": v(115.56, 29.27) * mm, "end": v(115.67, 29.35) * mm});
            skLineSegment(sketch, "E293", {"start": v(115.67, 29.35) * mm, "end": v(115.78, 29.42) * mm});
            skLineSegment(sketch, "E294", {"start": v(115.78, 29.42) * mm, "end": v(115.9, 29.5) * mm});
            skLineSegment(sketch, "E295", {"start": v(115.9, 29.5) * mm, "end": v(116, 29.58) * mm});
            skLineSegment(sketch, "E296", {"start": v(116, 29.58) * mm, "end": v(116.12, 29.66) * mm});
            skLineSegment(sketch, "E297", {"start": v(116.12, 29.66) * mm, "end": v(116.23, 29.74) * mm});
            skLineSegment(sketch, "E298", {"start": v(116.23, 29.74) * mm, "end": v(116.35, 29.82) * mm});
            skLineSegment(sketch, "E299", {"start": v(116.35, 29.82) * mm, "end": v(116.46, 29.9) * mm});
            skLineSegment(sketch, "E300", {"start": v(116.46, 29.9) * mm, "end": v(116.58, 29.99) * mm});
            skLineSegment(sketch, "E301", {"start": v(116.58, 29.99) * mm, "end": v(116.7, 30.07) * mm});
            skLineSegment(sketch, "E302", {"start": v(116.7, 30.07) * mm, "end": v(116.93, 30.25) * mm});
            skLineSegment(sketch, "E303", {"start": v(116.93, 30.25) * mm, "end": v(117.05, 30.33) * mm});
            skLineSegment(sketch, "E304", {"start": v(117.05, 30.33) * mm, "end": v(117.16, 30.42) * mm});
            skLineSegment(sketch, "E305", {"start": v(117.16, 30.42) * mm, "end": v(117.28, 30.51) * mm});
            skLineSegment(sketch, "E306", {"start": v(117.28, 30.51) * mm, "end": v(117.35, 30.6) * mm});
            skLineSegment(sketch, "E307", {"start": v(117.35, 30.6) * mm, "end": v(116.92, 32.2) * mm});
            skLineSegment(sketch, "E308", {"start": v(116.92, 32.2) * mm, "end": v(116.83, 32.23) * mm});
            skLineSegment(sketch, "E309", {"start": v(116.83, 32.23) * mm, "end": v(116.68, 32.25) * mm});
            skLineSegment(sketch, "E310", {"start": v(116.68, 32.25) * mm, "end": v(116.38, 32.28) * mm});
            skLineSegment(sketch, "E311", {"start": v(116.38, 32.28) * mm, "end": v(116.24, 32.3) * mm});
            skLineSegment(sketch, "E312", {"start": v(116.24, 32.3) * mm, "end": v(116.1, 32.32) * mm});
            skLineSegment(sketch, "E313", {"start": v(116.1, 32.32) * mm, "end": v(115.95, 32.33) * mm});
            skLineSegment(sketch, "E314", {"start": v(115.95, 32.33) * mm, "end": v(115.8, 32.35) * mm});
            skLineSegment(sketch, "E315", {"start": v(115.8, 32.35) * mm, "end": v(115.67, 32.36) * mm});
            skLineSegment(sketch, "E316", {"start": v(115.67, 32.36) * mm, "end": v(115.53, 32.37) * mm});
            skLineSegment(sketch, "E317", {"start": v(115.53, 32.37) * mm, "end": v(115.39, 32.39) * mm});
            skLineSegment(sketch, "E318", {"start": v(115.39, 32.39) * mm, "end": v(115.25, 32.4) * mm});
            skLineSegment(sketch, "E319", {"start": v(115.25, 32.4) * mm, "end": v(115.11, 32.41) * mm});
            skLineSegment(sketch, "E320", {"start": v(115.11, 32.41) * mm, "end": v(114.98, 32.42) * mm});
            skLineSegment(sketch, "E321", {"start": v(114.98, 32.42) * mm, "end": v(114.84, 32.43) * mm});
            skLineSegment(sketch, "E322", {"start": v(114.84, 32.43) * mm, "end": v(114.71, 32.44) * mm});
            skLineSegment(sketch, "E323", {"start": v(114.71, 32.44) * mm, "end": v(114.58, 32.45) * mm});
            skLineSegment(sketch, "E324", {"start": v(114.58, 32.45) * mm, "end": v(114.45, 32.46) * mm});
            skLineSegment(sketch, "E325", {"start": v(114.45, 32.46) * mm, "end": v(114.32, 32.47) * mm});
            skLineSegment(sketch, "E326", {"start": v(114.32, 32.47) * mm, "end": v(114.19, 32.48) * mm});
            skLineSegment(sketch, "E327", {"start": v(114.19, 32.48) * mm, "end": v(114.06, 32.5) * mm});
            skLineSegment(sketch, "E328", {"start": v(114.06, 32.5) * mm, "end": v(113.94, 32.5) * mm});
            skLineSegment(sketch, "E329", {"start": v(113.94, 32.5) * mm, "end": v(113.8, 32.5) * mm});
            skLineSegment(sketch, "E330", {"start": v(113.8, 32.5) * mm, "end": v(113.69, 32.51) * mm});
            skLineSegment(sketch, "E331", {"start": v(113.69, 32.51) * mm, "end": v(113.56, 32.52) * mm});
            skLineSegment(sketch, "E332", {"start": v(113.56, 32.52) * mm, "end": v(113.32, 32.53) * mm});
            skLineSegment(sketch, "E333", {"start": v(113.32, 32.53) * mm, "end": v(113.2, 32.53) * mm});
            skLineSegment(sketch, "E334", {"start": v(113.2, 32.53) * mm, "end": v(113.08, 32.54) * mm});
            skLineSegment(sketch, "E335", {"start": v(113.08, 32.54) * mm, "end": v(112.96, 32.54) * mm});
            skLineSegment(sketch, "E336", {"start": v(112.96, 32.54) * mm, "end": v(112.85, 32.54) * mm});
            skLineSegment(sketch, "E337", {"start": v(112.85, 32.54) * mm, "end": v(112.62, 32.55) * mm});
            skLineSegment(sketch, "E338", {"start": v(112.62, 32.55) * mm, "end": v(112.5, 32.55) * mm});
            skLineSegment(sketch, "E339", {"start": v(112.5, 32.55) * mm, "end": v(112.4, 32.55) * mm});
            skLineSegment(sketch, "E340", {"start": v(112.4, 32.55) * mm, "end": v(112.29, 32.55) * mm});
            skLineSegment(sketch, "E341", {"start": v(112.29, 32.55) * mm, "end": v(112.18, 32.56) * mm});
            skLineSegment(sketch, "E342", {"start": v(112.18, 32.56) * mm, "end": v(112.07, 32.56) * mm});
            skLineSegment(sketch, "E343", {"start": v(112.07, 32.56) * mm, "end": v(111.63, 33.43) * mm});
            skLineSegment(sketch, "E344", {"start": v(111.63, 33.43) * mm, "end": v(111.52, 34.4) * mm});
            skLineSegment(sketch, "E345", {"start": v(111.52, 34.4) * mm, "end": v(111.6, 34.46) * mm});
            skLineSegment(sketch, "E346", {"start": v(111.6, 34.46) * mm, "end": v(111.7, 34.52) * mm});
            skLineSegment(sketch, "E347", {"start": v(111.7, 34.52) * mm, "end": v(111.8, 34.58) * mm});
            skLineSegment(sketch, "E348", {"start": v(111.8, 34.58) * mm, "end": v(111.88, 34.64) * mm});
            skLineSegment(sketch, "E349", {"start": v(111.88, 34.64) * mm, "end": v(111.98, 34.7) * mm});
            skLineSegment(sketch, "E350", {"start": v(111.98, 34.7) * mm, "end": v(112.07, 34.77) * mm});
            skLineSegment(sketch, "E351", {"start": v(112.07, 34.77) * mm, "end": v(112.16, 34.83) * mm});
            skLineSegment(sketch, "E352", {"start": v(112.16, 34.83) * mm, "end": v(112.26, 34.9) * mm});
            skLineSegment(sketch, "E353", {"start": v(112.26, 34.9) * mm, "end": v(112.45, 35.04) * mm});
            skLineSegment(sketch, "E354", {"start": v(112.45, 35.04) * mm, "end": v(112.65, 35.18) * mm});
            skLineSegment(sketch, "E355", {"start": v(112.65, 35.18) * mm, "end": v(112.74, 35.25) * mm});
            skLineSegment(sketch, "E356", {"start": v(112.74, 35.25) * mm, "end": v(112.84, 35.32) * mm});
            skLineSegment(sketch, "E357", {"start": v(112.84, 35.32) * mm, "end": v(112.94, 35.4) * mm});
            skLineSegment(sketch, "E358", {"start": v(112.94, 35.4) * mm, "end": v(113.04, 35.47) * mm});
            skLineSegment(sketch, "E359", {"start": v(113.04, 35.47) * mm, "end": v(113.15, 35.55) * mm});
            skLineSegment(sketch, "E360", {"start": v(113.15, 35.55) * mm, "end": v(113.25, 35.62) * mm});
            skLineSegment(sketch, "E361", {"start": v(113.25, 35.62) * mm, "end": v(113.35, 35.7) * mm});
            skLineSegment(sketch, "E362", {"start": v(113.35, 35.7) * mm, "end": v(113.45, 35.78) * mm});
            skLineSegment(sketch, "E363", {"start": v(113.45, 35.78) * mm, "end": v(113.66, 35.94) * mm});
            skLineSegment(sketch, "E364", {"start": v(113.66, 35.94) * mm, "end": v(113.88, 36.1) * mm});
            skLineSegment(sketch, "E365", {"start": v(113.88, 36.1) * mm, "end": v(113.98, 36.19) * mm});
            skLineSegment(sketch, "E366", {"start": v(113.98, 36.19) * mm, "end": v(114.09, 36.27) * mm});
            skLineSegment(sketch, "E367", {"start": v(114.09, 36.27) * mm, "end": v(114.2, 36.36) * mm});
            skLineSegment(sketch, "E368", {"start": v(114.2, 36.36) * mm, "end": v(114.42, 36.54) * mm});
            skLineSegment(sketch, "E369", {"start": v(114.42, 36.54) * mm, "end": v(114.64, 36.71) * mm});
            skLineSegment(sketch, "E370", {"start": v(114.64, 36.71) * mm, "end": v(114.86, 36.9) * mm});
            skLineSegment(sketch, "E371", {"start": v(114.86, 36.9) * mm, "end": v(114.97, 37) * mm});
            skLineSegment(sketch, "E372", {"start": v(114.97, 37) * mm, "end": v(115.08, 37.09) * mm});
            skLineSegment(sketch, "E373", {"start": v(115.08, 37.09) * mm, "end": v(115.2, 37.18) * mm});
            skLineSegment(sketch, "E374", {"start": v(115.2, 37.18) * mm, "end": v(115.31, 37.28) * mm});
            skLineSegment(sketch, "E375", {"start": v(115.31, 37.28) * mm, "end": v(115.37, 37.36) * mm});
            skLineSegment(sketch, "E376", {"start": v(115.37, 37.36) * mm, "end": v(114.85, 38.94) * mm});
            skLineSegment(sketch, "E377", {"start": v(114.85, 38.94) * mm, "end": v(114.75, 38.97) * mm});
            skLineSegment(sketch, "E378", {"start": v(114.75, 38.97) * mm, "end": v(114.6, 38.98) * mm});
            skLineSegment(sketch, "E379", {"start": v(114.6, 38.98) * mm, "end": v(114.46, 38.99) * mm});
            skLineSegment(sketch, "E380", {"start": v(114.46, 38.99) * mm, "end": v(114.3, 39) * mm});
            skLineSegment(sketch, "E381", {"start": v(114.3, 39) * mm, "end": v(114.16, 39) * mm});
            skLineSegment(sketch, "E382", {"start": v(114.16, 39) * mm, "end": v(113.87, 39.02) * mm});
            skLineSegment(sketch, "E383", {"start": v(113.87, 39.02) * mm, "end": v(113.73, 39.02) * mm});
            skLineSegment(sketch, "E384", {"start": v(113.73, 39.02) * mm, "end": v(113.59, 39.03) * mm});
            skLineSegment(sketch, "E385", {"start": v(113.59, 39.03) * mm, "end": v(113.45, 39.04) * mm});
            skLineSegment(sketch, "E386", {"start": v(113.45, 39.04) * mm, "end": v(113.3, 39.04) * mm});
            skLineSegment(sketch, "E387", {"start": v(113.3, 39.04) * mm, "end": v(113.03, 39.05) * mm});
            skLineSegment(sketch, "E388", {"start": v(113.03, 39.05) * mm, "end": v(112.9, 39.05) * mm});
            skLineSegment(sketch, "E389", {"start": v(112.9, 39.05) * mm, "end": v(112.76, 39.06) * mm});
            skLineSegment(sketch, "E390", {"start": v(112.76, 39.06) * mm, "end": v(112.63, 39.06) * mm});
            skLineSegment(sketch, "E391", {"start": v(112.63, 39.06) * mm, "end": v(112.5, 39.06) * mm});
            skLineSegment(sketch, "E392", {"start": v(112.5, 39.06) * mm, "end": v(112.37, 39.06) * mm});
            skLineSegment(sketch, "E393", {"start": v(112.37, 39.06) * mm, "end": v(112.24, 39.06) * mm});
            skLineSegment(sketch, "E394", {"start": v(112.24, 39.06) * mm, "end": v(112.1, 39.07) * mm});
            skLineSegment(sketch, "E395", {"start": v(112.1, 39.07) * mm, "end": v(111.6, 39.07) * mm});
            skLineSegment(sketch, "E396", {"start": v(111.6, 39.07) * mm, "end": v(111.36, 39.06) * mm});
            skLineSegment(sketch, "E397", {"start": v(111.36, 39.06) * mm, "end": v(111.24, 39.06) * mm});
            skLineSegment(sketch, "E398", {"start": v(111.24, 39.06) * mm, "end": v(111.12, 39.06) * mm});
            skLineSegment(sketch, "E399", {"start": v(111.12, 39.06) * mm, "end": v(111, 39.06) * mm});
            skLineSegment(sketch, "E400", {"start": v(111, 39.06) * mm, "end": v(110.88, 39.05) * mm});
            skLineSegment(sketch, "E401", {"start": v(110.88, 39.05) * mm, "end": v(110.77, 39.05) * mm});
            skLineSegment(sketch, "E402", {"start": v(110.77, 39.05) * mm, "end": v(110.65, 39.05) * mm});
            skLineSegment(sketch, "E403", {"start": v(110.65, 39.05) * mm, "end": v(110.43, 39.04) * mm});
            skLineSegment(sketch, "E404", {"start": v(110.43, 39.04) * mm, "end": v(110.31, 39.03) * mm});
            skLineSegment(sketch, "E405", {"start": v(110.31, 39.03) * mm, "end": v(110.2, 39.03) * mm});
            skLineSegment(sketch, "E406", {"start": v(110.2, 39.03) * mm, "end": v(110.1, 39.02) * mm});
            skLineSegment(sketch, "E407", {"start": v(110.1, 39.02) * mm, "end": v(109.99, 39.02) * mm});
            skLineSegment(sketch, "E408", {"start": v(109.99, 39.02) * mm, "end": v(109.5, 39.86) * mm});
            skLineSegment(sketch, "E409", {"start": v(109.5, 39.86) * mm, "end": v(109.33, 40.82) * mm});
            skLineSegment(sketch, "E410", {"start": v(109.33, 40.82) * mm, "end": v(109.6, 41.02) * mm});
            skLineSegment(sketch, "E411", {"start": v(109.6, 41.02) * mm, "end": v(109.68, 41.09) * mm});
            skLineSegment(sketch, "E412", {"start": v(109.68, 41.09) * mm, "end": v(109.86, 41.23) * mm});
            skLineSegment(sketch, "E413", {"start": v(109.86, 41.23) * mm, "end": v(109.95, 41.3) * mm});
            skLineSegment(sketch, "E414", {"start": v(109.95, 41.3) * mm, "end": v(110.04, 41.37) * mm});
            skLineSegment(sketch, "E415", {"start": v(110.04, 41.37) * mm, "end": v(110.13, 41.44) * mm});
            skLineSegment(sketch, "E416", {"start": v(110.13, 41.44) * mm, "end": v(110.22, 41.52) * mm});
            skLineSegment(sketch, "E417", {"start": v(110.22, 41.52) * mm, "end": v(110.32, 41.6) * mm});
            skLineSegment(sketch, "E418", {"start": v(110.32, 41.6) * mm, "end": v(110.41, 41.67) * mm});
            skLineSegment(sketch, "E419", {"start": v(110.41, 41.67) * mm, "end": v(110.5, 41.74) * mm});
            skLineSegment(sketch, "E420", {"start": v(110.5, 41.74) * mm, "end": v(110.6, 41.82) * mm});
            skLineSegment(sketch, "E421", {"start": v(110.6, 41.82) * mm, "end": v(110.7, 41.9) * mm});
            skLineSegment(sketch, "E422", {"start": v(110.7, 41.9) * mm, "end": v(110.89, 42.06) * mm});
            skLineSegment(sketch, "E423", {"start": v(110.89, 42.06) * mm, "end": v(111.08, 42.23) * mm});
            skLineSegment(sketch, "E424", {"start": v(111.08, 42.23) * mm, "end": v(111.28, 42.4) * mm});
            skLineSegment(sketch, "E425", {"start": v(111.28, 42.4) * mm, "end": v(111.38, 42.49) * mm});
            skLineSegment(sketch, "E426", {"start": v(111.38, 42.49) * mm, "end": v(111.48, 42.58) * mm});
            skLineSegment(sketch, "E427", {"start": v(111.48, 42.58) * mm, "end": v(111.58, 42.67) * mm});
            skLineSegment(sketch, "E428", {"start": v(111.58, 42.67) * mm, "end": v(111.68, 42.75) * mm});
            skLineSegment(sketch, "E429", {"start": v(111.68, 42.75) * mm, "end": v(111.79, 42.85) * mm});
            skLineSegment(sketch, "E430", {"start": v(111.79, 42.85) * mm, "end": v(111.89, 42.94) * mm});
            skLineSegment(sketch, "E431", {"start": v(111.89, 42.94) * mm, "end": v(112, 43.03) * mm});
            skLineSegment(sketch, "E432", {"start": v(112, 43.03) * mm, "end": v(112.2, 43.22) * mm});
            skLineSegment(sketch, "E433", {"start": v(112.2, 43.22) * mm, "end": v(112.3, 43.32) * mm});
            skLineSegment(sketch, "E434", {"start": v(112.3, 43.32) * mm, "end": v(112.41, 43.42) * mm});
            skLineSegment(sketch, "E435", {"start": v(112.41, 43.42) * mm, "end": v(112.52, 43.52) * mm});
            skLineSegment(sketch, "E436", {"start": v(112.52, 43.52) * mm, "end": v(112.63, 43.62) * mm});
            skLineSegment(sketch, "E437", {"start": v(112.63, 43.62) * mm, "end": v(112.84, 43.82) * mm});
            skLineSegment(sketch, "E438", {"start": v(112.84, 43.82) * mm, "end": v(112.95, 43.92) * mm});
            skLineSegment(sketch, "E439", {"start": v(112.95, 43.92) * mm, "end": v(113, 44) * mm});
            skLineSegment(sketch, "E440", {"start": v(113, 44) * mm, "end": v(112.39, 45.55) * mm});
            skLineSegment(sketch, "E441", {"start": v(112.39, 45.55) * mm, "end": v(112.3, 45.57) * mm});
            skLineSegment(sketch, "E442", {"start": v(112.3, 45.57) * mm, "end": v(112, 45.58) * mm});
            skLineSegment(sketch, "E443", {"start": v(112, 45.58) * mm, "end": v(111.7, 45.58) * mm});
            skLineSegment(sketch, "E444", {"start": v(111.7, 45.58) * mm, "end": v(111.41, 45.57) * mm});
            skLineSegment(sketch, "E445", {"start": v(111.41, 45.57) * mm, "end": v(111.27, 45.57) * mm});
            skLineSegment(sketch, "E446", {"start": v(111.27, 45.57) * mm, "end": v(110.85, 45.56) * mm});
            skLineSegment(sketch, "E447", {"start": v(110.85, 45.56) * mm, "end": v(110.7, 45.56) * mm});
            skLineSegment(sketch, "E448", {"start": v(110.7, 45.56) * mm, "end": v(110.44, 45.55) * mm});
            skLineSegment(sketch, "E449", {"start": v(110.44, 45.55) * mm, "end": v(110.3, 45.55) * mm});
            skLineSegment(sketch, "E450", {"start": v(110.3, 45.55) * mm, "end": v(110.17, 45.54) * mm});
            skLineSegment(sketch, "E451", {"start": v(110.17, 45.54) * mm, "end": v(110.03, 45.54) * mm});
            skLineSegment(sketch, "E452", {"start": v(110.03, 45.54) * mm, "end": v(109.9, 45.53) * mm});
            skLineSegment(sketch, "E453", {"start": v(109.9, 45.53) * mm, "end": v(109.77, 45.52) * mm});
            skLineSegment(sketch, "E454", {"start": v(109.77, 45.52) * mm, "end": v(109.52, 45.51) * mm});
            skLineSegment(sketch, "E455", {"start": v(109.52, 45.51) * mm, "end": v(109.4, 45.5) * mm});
            skLineSegment(sketch, "E456", {"start": v(109.4, 45.5) * mm, "end": v(109.27, 45.5) * mm});
            skLineSegment(sketch, "E457", {"start": v(109.27, 45.5) * mm, "end": v(109.14, 45.49) * mm});
            skLineSegment(sketch, "E458", {"start": v(109.14, 45.49) * mm, "end": v(109.02, 45.48) * mm});
            skLineSegment(sketch, "E459", {"start": v(109.02, 45.48) * mm, "end": v(108.9, 45.47) * mm});
            skLineSegment(sketch, "E460", {"start": v(108.9, 45.47) * mm, "end": v(108.66, 45.45) * mm});
            skLineSegment(sketch, "E461", {"start": v(108.66, 45.45) * mm, "end": v(108.54, 45.44) * mm});
            skLineSegment(sketch, "E462", {"start": v(108.54, 45.44) * mm, "end": v(108.42, 45.43) * mm});
            skLineSegment(sketch, "E463", {"start": v(108.42, 45.43) * mm, "end": v(108.3, 45.42) * mm});
            skLineSegment(sketch, "E464", {"start": v(108.3, 45.42) * mm, "end": v(108.2, 45.41) * mm});
            skLineSegment(sketch, "E465", {"start": v(108.2, 45.41) * mm, "end": v(107.97, 45.4) * mm});
            skLineSegment(sketch, "E466", {"start": v(107.97, 45.4) * mm, "end": v(107.75, 45.37) * mm});
            skLineSegment(sketch, "E467", {"start": v(107.75, 45.37) * mm, "end": v(107.64, 45.36) * mm});
            skLineSegment(sketch, "E468", {"start": v(107.64, 45.36) * mm, "end": v(107.53, 45.35) * mm});
            skLineSegment(sketch, "E469", {"start": v(107.53, 45.35) * mm, "end": v(107, 46.16) * mm});
            skLineSegment(sketch, "E470", {"start": v(107, 46.16) * mm, "end": v(106.77, 47.1) * mm});
            skLineSegment(sketch, "E471", {"start": v(106.77, 47.1) * mm, "end": v(106.85, 47.18) * mm});
            skLineSegment(sketch, "E472", {"start": v(106.85, 47.18) * mm, "end": v(106.94, 47.25) * mm});
            skLineSegment(sketch, "E473", {"start": v(106.94, 47.25) * mm, "end": v(107.02, 47.32) * mm});
            skLineSegment(sketch, "E474", {"start": v(107.02, 47.32) * mm, "end": v(107.1, 47.4) * mm});
            skLineSegment(sketch, "E475", {"start": v(107.1, 47.4) * mm, "end": v(107.19, 47.47) * mm});
            skLineSegment(sketch, "E476", {"start": v(107.19, 47.47) * mm, "end": v(107.27, 47.54) * mm});
            skLineSegment(sketch, "E477", {"start": v(107.27, 47.54) * mm, "end": v(107.36, 47.62) * mm});
            skLineSegment(sketch, "E478", {"start": v(107.36, 47.62) * mm, "end": v(107.45, 47.7) * mm});
            skLineSegment(sketch, "E479", {"start": v(107.45, 47.7) * mm, "end": v(107.54, 47.78) * mm});
            skLineSegment(sketch, "E480", {"start": v(107.54, 47.78) * mm, "end": v(107.71, 47.94) * mm});
            skLineSegment(sketch, "E481", {"start": v(107.71, 47.94) * mm, "end": v(107.8, 48.02) * mm});
            skLineSegment(sketch, "E482", {"start": v(107.8, 48.02) * mm, "end": v(107.89, 48.1) * mm});
            skLineSegment(sketch, "E483", {"start": v(107.89, 48.1) * mm, "end": v(107.98, 48.18) * mm});
            skLineSegment(sketch, "E484", {"start": v(107.98, 48.18) * mm, "end": v(108.16, 48.35) * mm});
            skLineSegment(sketch, "E485", {"start": v(108.16, 48.35) * mm, "end": v(108.25, 48.44) * mm});
            skLineSegment(sketch, "E486", {"start": v(108.25, 48.44) * mm, "end": v(108.35, 48.53) * mm});
            skLineSegment(sketch, "E487", {"start": v(108.35, 48.53) * mm, "end": v(108.53, 48.7) * mm});
            skLineSegment(sketch, "E488", {"start": v(108.53, 48.7) * mm, "end": v(108.63, 48.8) * mm});
            skLineSegment(sketch, "E489", {"start": v(108.63, 48.8) * mm, "end": v(108.91, 49.08) * mm});
            skLineSegment(sketch, "E490", {"start": v(108.91, 49.08) * mm, "end": v(109, 49.18) * mm});
            skLineSegment(sketch, "E491", {"start": v(109, 49.18) * mm, "end": v(109.1, 49.27) * mm});
            skLineSegment(sketch, "E492", {"start": v(109.1, 49.27) * mm, "end": v(109.2, 49.37) * mm});
            skLineSegment(sketch, "E493", {"start": v(109.2, 49.37) * mm, "end": v(109.3, 49.47) * mm});
            skLineSegment(sketch, "E494", {"start": v(109.3, 49.47) * mm, "end": v(109.4, 49.57) * mm});
            skLineSegment(sketch, "E495", {"start": v(109.4, 49.57) * mm, "end": v(109.5, 49.67) * mm});
            skLineSegment(sketch, "E496", {"start": v(109.5, 49.67) * mm, "end": v(109.6, 49.78) * mm});
            skLineSegment(sketch, "E497", {"start": v(109.6, 49.78) * mm, "end": v(109.7, 49.88) * mm});
            skLineSegment(sketch, "E498", {"start": v(109.7, 49.88) * mm, "end": v(109.9, 50.1) * mm});
            skLineSegment(sketch, "E499", {"start": v(109.9, 50.1) * mm, "end": v(110, 50.2) * mm});
            skLineSegment(sketch, "E500", {"start": v(110, 50.2) * mm, "end": v(110.2, 50.42) * mm});
            skLineSegment(sketch, "E501", {"start": v(110.2, 50.42) * mm, "end": v(110.25, 50.5) * mm});
            skLineSegment(sketch, "E502", {"start": v(110.25, 50.5) * mm, "end": v(109.55, 52) * mm});
            skLineSegment(sketch, "E503", {"start": v(109.55, 52) * mm, "end": v(109.45, 52.03) * mm});
            skLineSegment(sketch, "E504", {"start": v(109.45, 52.03) * mm, "end": v(109.3, 52.02) * mm});
            skLineSegment(sketch, "E505", {"start": v(109.3, 52.02) * mm, "end": v(109.16, 52.01) * mm});
            skLineSegment(sketch, "E506", {"start": v(109.16, 52.01) * mm, "end": v(109, 52) * mm});
            skLineSegment(sketch, "E507", {"start": v(109, 52) * mm, "end": v(108.86, 52) * mm});
            skLineSegment(sketch, "E508", {"start": v(108.86, 52) * mm, "end": v(108.57, 51.97) * mm});
            skLineSegment(sketch, "E509", {"start": v(108.57, 51.97) * mm, "end": v(108.43, 51.96) * mm});
            skLineSegment(sketch, "E510", {"start": v(108.43, 51.96) * mm, "end": v(108.29, 51.95) * mm});
            skLineSegment(sketch, "E511", {"start": v(108.29, 51.95) * mm, "end": v(108.01, 51.93) * mm});
            skLineSegment(sketch, "E512", {"start": v(108.01, 51.93) * mm, "end": v(107.87, 51.92) * mm});
            skLineSegment(sketch, "E513", {"start": v(107.87, 51.92) * mm, "end": v(107.74, 51.9) * mm});
            skLineSegment(sketch, "E514", {"start": v(107.74, 51.9) * mm, "end": v(107.6, 51.9) * mm});
            skLineSegment(sketch, "E515", {"start": v(107.6, 51.9) * mm, "end": v(107.47, 51.88) * mm});
            skLineSegment(sketch, "E516", {"start": v(107.47, 51.88) * mm, "end": v(107.2, 51.86) * mm});
            skLineSegment(sketch, "E517", {"start": v(107.2, 51.86) * mm, "end": v(107.07, 51.84) * mm});
            skLineSegment(sketch, "E518", {"start": v(107.07, 51.84) * mm, "end": v(106.94, 51.83) * mm});
            skLineSegment(sketch, "E519", {"start": v(106.94, 51.83) * mm, "end": v(106.81, 51.82) * mm});
            skLineSegment(sketch, "E520", {"start": v(106.81, 51.82) * mm, "end": v(106.69, 51.8) * mm});
            skLineSegment(sketch, "E521", {"start": v(106.69, 51.8) * mm, "end": v(106.56, 51.79) * mm});
            skLineSegment(sketch, "E522", {"start": v(106.56, 51.79) * mm, "end": v(106.31, 51.76) * mm});
            skLineSegment(sketch, "E523", {"start": v(106.31, 51.76) * mm, "end": v(106.07, 51.73) * mm});
            skLineSegment(sketch, "E524", {"start": v(106.07, 51.73) * mm, "end": v(105.95, 51.71) * mm});
            skLineSegment(sketch, "E525", {"start": v(105.95, 51.71) * mm, "end": v(105.83, 51.7) * mm});
            skLineSegment(sketch, "E526", {"start": v(105.83, 51.7) * mm, "end": v(105.71, 51.68) * mm});
            skLineSegment(sketch, "E527", {"start": v(105.71, 51.68) * mm, "end": v(105.6, 51.66) * mm});
            skLineSegment(sketch, "E528", {"start": v(105.6, 51.66) * mm, "end": v(105.48, 51.64) * mm});
            skLineSegment(sketch, "E529", {"start": v(105.48, 51.64) * mm, "end": v(105.26, 51.61) * mm});
            skLineSegment(sketch, "E530", {"start": v(105.26, 51.61) * mm, "end": v(105.04, 51.58) * mm});
            skLineSegment(sketch, "E531", {"start": v(105.04, 51.58) * mm, "end": v(104.93, 51.56) * mm});
            skLineSegment(sketch, "E532", {"start": v(104.93, 51.56) * mm, "end": v(104.82, 51.54) * mm});
            skLineSegment(sketch, "E533", {"start": v(104.82, 51.54) * mm, "end": v(104.71, 51.52) * mm});
            skLineSegment(sketch, "E534", {"start": v(104.71, 51.52) * mm, "end": v(104.13, 52.3) * mm});
            skLineSegment(sketch, "E535", {"start": v(104.13, 52.3) * mm, "end": v(103.85, 53.24) * mm});
            skLineSegment(sketch, "E536", {"start": v(103.85, 53.24) * mm, "end": v(103.93, 53.31) * mm});
            skLineSegment(sketch, "E537", {"start": v(103.93, 53.31) * mm, "end": v(104, 53.39) * mm});
            skLineSegment(sketch, "E538", {"start": v(104, 53.39) * mm, "end": v(104.09, 53.46) * mm});
            skLineSegment(sketch, "E539", {"start": v(104.09, 53.46) * mm, "end": v(104.17, 53.54) * mm});
            skLineSegment(sketch, "E540", {"start": v(104.17, 53.54) * mm, "end": v(104.25, 53.62) * mm});
            skLineSegment(sketch, "E541", {"start": v(104.25, 53.62) * mm, "end": v(104.33, 53.7) * mm});
            skLineSegment(sketch, "E542", {"start": v(104.33, 53.7) * mm, "end": v(104.41, 53.78) * mm});
            skLineSegment(sketch, "E543", {"start": v(104.41, 53.78) * mm, "end": v(104.5, 53.87) * mm});
            skLineSegment(sketch, "E544", {"start": v(104.5, 53.87) * mm, "end": v(104.58, 53.95) * mm});
            skLineSegment(sketch, "E545", {"start": v(104.58, 53.95) * mm, "end": v(104.66, 54.03) * mm});
            skLineSegment(sketch, "E546", {"start": v(104.66, 54.03) * mm, "end": v(104.74, 54.12) * mm});
            skLineSegment(sketch, "E547", {"start": v(104.74, 54.12) * mm, "end": v(104.83, 54.2) * mm});
            skLineSegment(sketch, "E548", {"start": v(104.83, 54.2) * mm, "end": v(104.91, 54.3) * mm});
            skLineSegment(sketch, "E549", {"start": v(104.91, 54.3) * mm, "end": v(105, 54.38) * mm});
            skLineSegment(sketch, "E550", {"start": v(105, 54.38) * mm, "end": v(105.08, 54.47) * mm});
            skLineSegment(sketch, "E551", {"start": v(105.08, 54.47) * mm, "end": v(105.17, 54.56) * mm});
            skLineSegment(sketch, "E552", {"start": v(105.17, 54.56) * mm, "end": v(105.25, 54.65) * mm});
            skLineSegment(sketch, "E553", {"start": v(105.25, 54.65) * mm, "end": v(105.34, 54.75) * mm});
            skLineSegment(sketch, "E554", {"start": v(105.34, 54.75) * mm, "end": v(105.43, 54.84) * mm});
            skLineSegment(sketch, "E555", {"start": v(105.43, 54.84) * mm, "end": v(105.52, 54.94) * mm});
            skLineSegment(sketch, "E556", {"start": v(105.52, 54.94) * mm, "end": v(105.6, 55.03) * mm});
            skLineSegment(sketch, "E557", {"start": v(105.6, 55.03) * mm, "end": v(105.7, 55.13) * mm});
            skLineSegment(sketch, "E558", {"start": v(105.7, 55.13) * mm, "end": v(105.78, 55.23) * mm});
            skLineSegment(sketch, "E559", {"start": v(105.78, 55.23) * mm, "end": v(105.88, 55.33) * mm});
            skLineSegment(sketch, "E560", {"start": v(105.88, 55.33) * mm, "end": v(105.97, 55.43) * mm});
            skLineSegment(sketch, "E561", {"start": v(105.97, 55.43) * mm, "end": v(106.06, 55.53) * mm});
            skLineSegment(sketch, "E562", {"start": v(106.06, 55.53) * mm, "end": v(106.15, 55.64) * mm});
            skLineSegment(sketch, "E563", {"start": v(106.15, 55.64) * mm, "end": v(106.24, 55.74) * mm});
            skLineSegment(sketch, "E564", {"start": v(106.24, 55.74) * mm, "end": v(106.33, 55.85) * mm});
            skLineSegment(sketch, "E565", {"start": v(106.33, 55.85) * mm, "end": v(106.43, 55.96) * mm});
            skLineSegment(sketch, "E566", {"start": v(106.43, 55.96) * mm, "end": v(106.52, 56.06) * mm});
            skLineSegment(sketch, "E567", {"start": v(106.52, 56.06) * mm, "end": v(106.7, 56.28) * mm});
            skLineSegment(sketch, "E568", {"start": v(106.7, 56.28) * mm, "end": v(106.8, 56.4) * mm});
            skLineSegment(sketch, "E569", {"start": v(106.8, 56.4) * mm, "end": v(106.9, 56.5) * mm});
            skLineSegment(sketch, "E570", {"start": v(106.9, 56.5) * mm, "end": v(107, 56.62) * mm});
            skLineSegment(sketch, "E571", {"start": v(107, 56.62) * mm, "end": v(107.09, 56.74) * mm});
            skLineSegment(sketch, "E572", {"start": v(107.09, 56.74) * mm, "end": v(107.13, 56.83) * mm});
            skLineSegment(sketch, "E573", {"start": v(107.13, 56.83) * mm, "end": v(106.34, 58.29) * mm});
            skLineSegment(sketch, "E574", {"start": v(106.34, 58.29) * mm, "end": v(106.24, 58.3) * mm});
            skLineSegment(sketch, "E575", {"start": v(106.24, 58.3) * mm, "end": v(106.1, 58.29) * mm});
            skLineSegment(sketch, "E576", {"start": v(106.1, 58.29) * mm, "end": v(105.8, 58.25) * mm});
            skLineSegment(sketch, "E577", {"start": v(105.8, 58.25) * mm, "end": v(105.51, 58.22) * mm});
            skLineSegment(sketch, "E578", {"start": v(105.51, 58.22) * mm, "end": v(105.37, 58.2) * mm});
            skLineSegment(sketch, "E579", {"start": v(105.37, 58.2) * mm, "end": v(105.23, 58.18) * mm});
            skLineSegment(sketch, "E580", {"start": v(105.23, 58.18) * mm, "end": v(105.09, 58.16) * mm});
            skLineSegment(sketch, "E581", {"start": v(105.09, 58.16) * mm, "end": v(104.95, 58.14) * mm});
            skLineSegment(sketch, "E582", {"start": v(104.95, 58.14) * mm, "end": v(104.8, 58.12) * mm});
            skLineSegment(sketch, "E583", {"start": v(104.8, 58.12) * mm, "end": v(104.67, 58.1) * mm});
            skLineSegment(sketch, "E584", {"start": v(104.67, 58.1) * mm, "end": v(104.54, 58.08) * mm});
            skLineSegment(sketch, "E585", {"start": v(104.54, 58.08) * mm, "end": v(104.4, 58.07) * mm});
            skLineSegment(sketch, "E586", {"start": v(104.4, 58.07) * mm, "end": v(104.27, 58.04) * mm});
            skLineSegment(sketch, "E587", {"start": v(104.27, 58.04) * mm, "end": v(104.14, 58.02) * mm});
            skLineSegment(sketch, "E588", {"start": v(104.14, 58.02) * mm, "end": v(104, 58) * mm});
            skLineSegment(sketch, "E589", {"start": v(104, 58) * mm, "end": v(103.88, 57.98) * mm});
            skLineSegment(sketch, "E590", {"start": v(103.88, 57.98) * mm, "end": v(103.75, 57.96) * mm});
            skLineSegment(sketch, "E591", {"start": v(103.75, 57.96) * mm, "end": v(103.62, 57.94) * mm});
            skLineSegment(sketch, "E592", {"start": v(103.62, 57.94) * mm, "end": v(103.37, 57.9) * mm});
            skLineSegment(sketch, "E593", {"start": v(103.37, 57.9) * mm, "end": v(103.25, 57.87) * mm});
            skLineSegment(sketch, "E594", {"start": v(103.25, 57.87) * mm, "end": v(103, 57.83) * mm});
            skLineSegment(sketch, "E595", {"start": v(103, 57.83) * mm, "end": v(102.88, 57.8) * mm});
            skLineSegment(sketch, "E596", {"start": v(102.88, 57.8) * mm, "end": v(102.76, 57.78) * mm});
            skLineSegment(sketch, "E597", {"start": v(102.76, 57.78) * mm, "end": v(102.65, 57.76) * mm});
            skLineSegment(sketch, "E598", {"start": v(102.65, 57.76) * mm, "end": v(102.53, 57.74) * mm});
            skLineSegment(sketch, "E599", {"start": v(102.53, 57.74) * mm, "end": v(102.42, 57.72) * mm});
            skLineSegment(sketch, "E600", {"start": v(102.42, 57.72) * mm, "end": v(102.19, 57.67) * mm});
            skLineSegment(sketch, "E601", {"start": v(102.19, 57.67) * mm, "end": v(102.08, 57.64) * mm});
            skLineSegment(sketch, "E602", {"start": v(102.08, 57.64) * mm, "end": v(101.97, 57.62) * mm});
            skLineSegment(sketch, "E603", {"start": v(101.97, 57.62) * mm, "end": v(101.86, 57.6) * mm});
            skLineSegment(sketch, "E604", {"start": v(101.86, 57.6) * mm, "end": v(101.75, 57.57) * mm});
            skLineSegment(sketch, "E605", {"start": v(101.75, 57.57) * mm, "end": v(101.65, 57.55) * mm});
            skLineSegment(sketch, "E606", {"start": v(101.65, 57.55) * mm, "end": v(101.54, 57.52) * mm});
            skLineSegment(sketch, "E607", {"start": v(101.54, 57.52) * mm, "end": v(100.91, 58.27) * mm});
            skLineSegment(sketch, "E608", {"start": v(100.91, 58.27) * mm, "end": v(100.58, 59.19) * mm});
            skLineSegment(sketch, "E609", {"start": v(100.58, 59.19) * mm, "end": v(100.65, 59.27) * mm});
            skLineSegment(sketch, "E610", {"start": v(100.65, 59.27) * mm, "end": v(100.73, 59.35) * mm});
            skLineSegment(sketch, "E611", {"start": v(100.73, 59.35) * mm, "end": v(100.88, 59.5) * mm});
            skLineSegment(sketch, "E612", {"start": v(100.88, 59.5) * mm, "end": v(101.03, 59.68) * mm});
            skLineSegment(sketch, "E613", {"start": v(101.03, 59.68) * mm, "end": v(101.1, 59.76) * mm});
            skLineSegment(sketch, "E614", {"start": v(101.1, 59.76) * mm, "end": v(101.18, 59.85) * mm});
            skLineSegment(sketch, "E615", {"start": v(101.18, 59.85) * mm, "end": v(101.26, 59.94) * mm});
            skLineSegment(sketch, "E616", {"start": v(101.26, 59.94) * mm, "end": v(101.42, 60.12) * mm});
            skLineSegment(sketch, "E617", {"start": v(101.42, 60.12) * mm, "end": v(101.5, 60.2) * mm});
            skLineSegment(sketch, "E618", {"start": v(101.5, 60.2) * mm, "end": v(101.58, 60.3) * mm});
            skLineSegment(sketch, "E619", {"start": v(101.58, 60.3) * mm, "end": v(101.66, 60.4) * mm});
            skLineSegment(sketch, "E620", {"start": v(101.66, 60.4) * mm, "end": v(101.74, 60.49) * mm});
            skLineSegment(sketch, "E621", {"start": v(101.74, 60.49) * mm, "end": v(101.9, 60.68) * mm});
            skLineSegment(sketch, "E622", {"start": v(101.9, 60.68) * mm, "end": v(101.98, 60.78) * mm});
            skLineSegment(sketch, "E623", {"start": v(101.98, 60.78) * mm, "end": v(102.23, 61.08) * mm});
            skLineSegment(sketch, "E624", {"start": v(102.23, 61.08) * mm, "end": v(102.31, 61.18) * mm});
            skLineSegment(sketch, "E625", {"start": v(102.31, 61.18) * mm, "end": v(102.48, 61.4) * mm});
            skLineSegment(sketch, "E626", {"start": v(102.48, 61.4) * mm, "end": v(102.56, 61.5) * mm});
            skLineSegment(sketch, "E627", {"start": v(102.56, 61.5) * mm, "end": v(102.65, 61.6) * mm});
            skLineSegment(sketch, "E628", {"start": v(102.65, 61.6) * mm, "end": v(102.73, 61.72) * mm});
            skLineSegment(sketch, "E629", {"start": v(102.73, 61.72) * mm, "end": v(102.82, 61.83) * mm});
            skLineSegment(sketch, "E630", {"start": v(102.82, 61.83) * mm, "end": v(102.9, 61.94) * mm});
            skLineSegment(sketch, "E631", {"start": v(102.9, 61.94) * mm, "end": v(103, 62.05) * mm});
            skLineSegment(sketch, "E632", {"start": v(103, 62.05) * mm, "end": v(103.17, 62.28) * mm});
            skLineSegment(sketch, "E633", {"start": v(103.17, 62.28) * mm, "end": v(103.25, 62.4) * mm});
            skLineSegment(sketch, "E634", {"start": v(103.25, 62.4) * mm, "end": v(103.34, 62.51) * mm});
            skLineSegment(sketch, "E635", {"start": v(103.34, 62.51) * mm, "end": v(103.43, 62.63) * mm});
            skLineSegment(sketch, "E636", {"start": v(103.43, 62.63) * mm, "end": v(103.52, 62.75) * mm});
            skLineSegment(sketch, "E637", {"start": v(103.52, 62.75) * mm, "end": v(103.6, 62.87) * mm});
            skLineSegment(sketch, "E638", {"start": v(103.6, 62.87) * mm, "end": v(103.64, 62.96) * mm});
            skLineSegment(sketch, "E639", {"start": v(103.64, 62.96) * mm, "end": v(102.77, 64.37) * mm});
            skLineSegment(sketch, "E640", {"start": v(102.77, 64.37) * mm, "end": v(102.67, 64.38) * mm});
            skLineSegment(sketch, "E641", {"start": v(102.67, 64.38) * mm, "end": v(102.53, 64.36) * mm});
            skLineSegment(sketch, "E642", {"start": v(102.53, 64.36) * mm, "end": v(102.38, 64.33) * mm});
            skLineSegment(sketch, "E643", {"start": v(102.38, 64.33) * mm, "end": v(102.23, 64.3) * mm});
            skLineSegment(sketch, "E644", {"start": v(102.23, 64.3) * mm, "end": v(102.1, 64.28) * mm});
            skLineSegment(sketch, "E645", {"start": v(102.1, 64.28) * mm, "end": v(101.95, 64.25) * mm});
            skLineSegment(sketch, "E646", {"start": v(101.95, 64.25) * mm, "end": v(101.8, 64.23) * mm});
            skLineSegment(sketch, "E647", {"start": v(101.8, 64.23) * mm, "end": v(101.67, 64.2) * mm});
            skLineSegment(sketch, "E648", {"start": v(101.67, 64.2) * mm, "end": v(101.53, 64.17) * mm});
            skLineSegment(sketch, "E649", {"start": v(101.53, 64.17) * mm, "end": v(101.39, 64.15) * mm});
            skLineSegment(sketch, "E650", {"start": v(101.39, 64.15) * mm, "end": v(101.25, 64.12) * mm});
            skLineSegment(sketch, "E651", {"start": v(101.25, 64.12) * mm, "end": v(100.98, 64.07) * mm});
            skLineSegment(sketch, "E652", {"start": v(100.98, 64.07) * mm, "end": v(100.85, 64.04) * mm});
            skLineSegment(sketch, "E653", {"start": v(100.85, 64.04) * mm, "end": v(100.72, 64) * mm});
            skLineSegment(sketch, "E654", {"start": v(100.72, 64) * mm, "end": v(100.59, 63.98) * mm});
            skLineSegment(sketch, "E655", {"start": v(100.59, 63.98) * mm, "end": v(100.46, 63.95) * mm});
            skLineSegment(sketch, "E656", {"start": v(100.46, 63.95) * mm, "end": v(100.33, 63.92) * mm});
            skLineSegment(sketch, "E657", {"start": v(100.33, 63.92) * mm, "end": v(100.2, 63.9) * mm});
            skLineSegment(sketch, "E658", {"start": v(100.2, 63.9) * mm, "end": v(100.08, 63.87) * mm});
            skLineSegment(sketch, "E659", {"start": v(100.08, 63.87) * mm, "end": v(99.83, 63.8) * mm});
            skLineSegment(sketch, "E660", {"start": v(99.83, 63.8) * mm, "end": v(99.7, 63.78) * mm});
            skLineSegment(sketch, "E661", {"start": v(99.7, 63.78) * mm, "end": v(99.59, 63.75) * mm});
            skLineSegment(sketch, "E662", {"start": v(99.59, 63.75) * mm, "end": v(99.47, 63.72) * mm});
            skLineSegment(sketch, "E663", {"start": v(99.47, 63.72) * mm, "end": v(99.35, 63.7) * mm});
            skLineSegment(sketch, "E664", {"start": v(99.35, 63.7) * mm, "end": v(99.23, 63.66) * mm});
            skLineSegment(sketch, "E665", {"start": v(99.23, 63.66) * mm, "end": v(99.12, 63.63) * mm});
            skLineSegment(sketch, "E666", {"start": v(99.12, 63.63) * mm, "end": v(98.89, 63.57) * mm});
            skLineSegment(sketch, "E667", {"start": v(98.89, 63.57) * mm, "end": v(98.78, 63.54) * mm});
            skLineSegment(sketch, "E668", {"start": v(98.78, 63.54) * mm, "end": v(98.66, 63.51) * mm});
            skLineSegment(sketch, "E669", {"start": v(98.66, 63.51) * mm, "end": v(98.45, 63.45) * mm});
            skLineSegment(sketch, "E670", {"start": v(98.45, 63.45) * mm, "end": v(98.34, 63.42) * mm});
            skLineSegment(sketch, "E671", {"start": v(98.34, 63.42) * mm, "end": v(98.23, 63.4) * mm});
            skLineSegment(sketch, "E672", {"start": v(98.23, 63.4) * mm, "end": v(98.13, 63.36) * mm});
            skLineSegment(sketch, "E673", {"start": v(98.13, 63.36) * mm, "end": v(98.02, 63.33) * mm});
            skLineSegment(sketch, "E674", {"start": v(98.02, 63.33) * mm, "end": v(97.35, 64.04) * mm});
            skLineSegment(sketch, "E675", {"start": v(97.35, 64.04) * mm, "end": v(96.97, 64.93) * mm});
            skLineSegment(sketch, "E676", {"start": v(96.97, 64.93) * mm, "end": v(97.04, 65.02) * mm});
            skLineSegment(sketch, "E677", {"start": v(97.04, 65.02) * mm, "end": v(97.1, 65.1) * mm});
            skLineSegment(sketch, "E678", {"start": v(97.1, 65.1) * mm, "end": v(97.18, 65.19) * mm});
            skLineSegment(sketch, "E679", {"start": v(97.18, 65.19) * mm, "end": v(97.32, 65.36) * mm});
            skLineSegment(sketch, "E680", {"start": v(97.32, 65.36) * mm, "end": v(97.39, 65.45) * mm});
            skLineSegment(sketch, "E681", {"start": v(97.39, 65.45) * mm, "end": v(97.46, 65.54) * mm});
            skLineSegment(sketch, "E682", {"start": v(97.46, 65.54) * mm, "end": v(97.53, 65.63) * mm});
            skLineSegment(sketch, "E683", {"start": v(97.53, 65.63) * mm, "end": v(97.6, 65.72) * mm});
            skLineSegment(sketch, "E684", {"start": v(97.6, 65.72) * mm, "end": v(97.68, 65.82) * mm});
            skLineSegment(sketch, "E685", {"start": v(97.68, 65.82) * mm, "end": v(97.82, 66) * mm});
            skLineSegment(sketch, "E686", {"start": v(97.82, 66) * mm, "end": v(97.9, 66.1) * mm});
            skLineSegment(sketch, "E687", {"start": v(97.9, 66.1) * mm, "end": v(98.05, 66.3) * mm});
            skLineSegment(sketch, "E688", {"start": v(98.05, 66.3) * mm, "end": v(98.12, 66.4) * mm});
            skLineSegment(sketch, "E689", {"start": v(98.12, 66.4) * mm, "end": v(98.2, 66.5) * mm});
            skLineSegment(sketch, "E690", {"start": v(98.2, 66.5) * mm, "end": v(98.27, 66.6) * mm});
            skLineSegment(sketch, "E691", {"start": v(98.27, 66.6) * mm, "end": v(98.35, 66.7) * mm});
            skLineSegment(sketch, "E692", {"start": v(98.35, 66.7) * mm, "end": v(98.43, 66.82) * mm});
            skLineSegment(sketch, "E693", {"start": v(98.43, 66.82) * mm, "end": v(98.5, 66.92) * mm});
            skLineSegment(sketch, "E694", {"start": v(98.5, 66.92) * mm, "end": v(98.58, 67.03) * mm});
            skLineSegment(sketch, "E695", {"start": v(98.58, 67.03) * mm, "end": v(98.66, 67.14) * mm});
            skLineSegment(sketch, "E696", {"start": v(98.66, 67.14) * mm, "end": v(98.81, 67.36) * mm});
            skLineSegment(sketch, "E697", {"start": v(98.81, 67.36) * mm, "end": v(98.97, 67.58) * mm});
            skLineSegment(sketch, "E698", {"start": v(98.97, 67.58) * mm, "end": v(99.05, 67.7) * mm});
            skLineSegment(sketch, "E699", {"start": v(99.05, 67.7) * mm, "end": v(99.13, 67.82) * mm});
            skLineSegment(sketch, "E700", {"start": v(99.13, 67.82) * mm, "end": v(99.21, 67.93) * mm});
            skLineSegment(sketch, "E701", {"start": v(99.21, 67.93) * mm, "end": v(99.3, 68.05) * mm});
            skLineSegment(sketch, "E702", {"start": v(99.3, 68.05) * mm, "end": v(99.45, 68.3) * mm});
            skLineSegment(sketch, "E703", {"start": v(99.45, 68.3) * mm, "end": v(99.53, 68.41) * mm});
            skLineSegment(sketch, "E704", {"start": v(99.53, 68.41) * mm, "end": v(99.7, 68.66) * mm});
            skLineSegment(sketch, "E705", {"start": v(99.7, 68.66) * mm, "end": v(99.78, 68.79) * mm});
            skLineSegment(sketch, "E706", {"start": v(99.78, 68.79) * mm, "end": v(99.8, 68.88) * mm});
            skLineSegment(sketch, "E707", {"start": v(99.8, 68.88) * mm, "end": v(98.85, 70.24) * mm});
            skLineSegment(sketch, "E708", {"start": v(98.85, 70.24) * mm, "end": v(98.76, 70.24) * mm});
            skLineSegment(sketch, "E709", {"start": v(98.76, 70.24) * mm, "end": v(98.61, 70.2) * mm});
            skLineSegment(sketch, "E710", {"start": v(98.61, 70.2) * mm, "end": v(98.47, 70.18) * mm});
            skLineSegment(sketch, "E711", {"start": v(98.47, 70.18) * mm, "end": v(98.18, 70.1) * mm});
            skLineSegment(sketch, "E712", {"start": v(98.18, 70.1) * mm, "end": v(98.04, 70.07) * mm});
            skLineSegment(sketch, "E713", {"start": v(98.04, 70.07) * mm, "end": v(97.9, 70.04) * mm});
            skLineSegment(sketch, "E714", {"start": v(97.9, 70.04) * mm, "end": v(97.62, 69.97) * mm});
            skLineSegment(sketch, "E715", {"start": v(97.62, 69.97) * mm, "end": v(97.49, 69.93) * mm});
            skLineSegment(sketch, "E716", {"start": v(97.49, 69.93) * mm, "end": v(97.35, 69.9) * mm});
            skLineSegment(sketch, "E717", {"start": v(97.35, 69.9) * mm, "end": v(97.22, 69.86) * mm});
            skLineSegment(sketch, "E718", {"start": v(97.22, 69.86) * mm, "end": v(97.09, 69.83) * mm});
            skLineSegment(sketch, "E719", {"start": v(97.09, 69.83) * mm, "end": v(96.82, 69.76) * mm});
            skLineSegment(sketch, "E720", {"start": v(96.82, 69.76) * mm, "end": v(96.7, 69.72) * mm});
            skLineSegment(sketch, "E721", {"start": v(96.7, 69.72) * mm, "end": v(96.57, 69.69) * mm});
            skLineSegment(sketch, "E722", {"start": v(96.57, 69.69) * mm, "end": v(96.44, 69.65) * mm});
            skLineSegment(sketch, "E723", {"start": v(96.44, 69.65) * mm, "end": v(96.32, 69.61) * mm});
            skLineSegment(sketch, "E724", {"start": v(96.32, 69.61) * mm, "end": v(96.2, 69.58) * mm});
            skLineSegment(sketch, "E725", {"start": v(96.2, 69.58) * mm, "end": v(96.07, 69.54) * mm});
            skLineSegment(sketch, "E726", {"start": v(96.07, 69.54) * mm, "end": v(95.95, 69.5) * mm});
            skLineSegment(sketch, "E727", {"start": v(95.95, 69.5) * mm, "end": v(95.83, 69.47) * mm});
            skLineSegment(sketch, "E728", {"start": v(95.83, 69.47) * mm, "end": v(95.71, 69.43) * mm});
            skLineSegment(sketch, "E729", {"start": v(95.71, 69.43) * mm, "end": v(95.6, 69.4) * mm});
            skLineSegment(sketch, "E730", {"start": v(95.6, 69.4) * mm, "end": v(95.48, 69.36) * mm});
            skLineSegment(sketch, "E731", {"start": v(95.48, 69.36) * mm, "end": v(95.36, 69.32) * mm});
            skLineSegment(sketch, "E732", {"start": v(95.36, 69.32) * mm, "end": v(95.25, 69.29) * mm});
            skLineSegment(sketch, "E733", {"start": v(95.25, 69.29) * mm, "end": v(95.13, 69.25) * mm});
            skLineSegment(sketch, "E734", {"start": v(95.13, 69.25) * mm, "end": v(95.02, 69.21) * mm});
            skLineSegment(sketch, "E735", {"start": v(95.02, 69.21) * mm, "end": v(94.91, 69.18) * mm});
            skLineSegment(sketch, "E736", {"start": v(94.91, 69.18) * mm, "end": v(94.8, 69.14) * mm});
            skLineSegment(sketch, "E737", {"start": v(94.8, 69.14) * mm, "end": v(94.7, 69.1) * mm});
            skLineSegment(sketch, "E738", {"start": v(94.7, 69.1) * mm, "end": v(94.59, 69.07) * mm});
            skLineSegment(sketch, "E739", {"start": v(94.59, 69.07) * mm, "end": v(94.49, 69.03) * mm});
            skLineSegment(sketch, "E740", {"start": v(94.49, 69.03) * mm, "end": v(94.38, 69) * mm});
            skLineSegment(sketch, "E741", {"start": v(94.38, 69) * mm, "end": v(94.28, 68.96) * mm});
            skLineSegment(sketch, "E742", {"start": v(94.28, 68.96) * mm, "end": v(94.18, 68.92) * mm});
            skLineSegment(sketch, "E743", {"start": v(94.18, 68.92) * mm, "end": v(93.47, 69.59) * mm});
            skLineSegment(sketch, "E744", {"start": v(93.47, 69.59) * mm, "end": v(93.03, 70.46) * mm});
            skLineSegment(sketch, "E745", {"start": v(93.03, 70.46) * mm, "end": v(93.1, 70.55) * mm});
            skLineSegment(sketch, "E746", {"start": v(93.1, 70.55) * mm, "end": v(93.16, 70.64) * mm});
            skLineSegment(sketch, "E747", {"start": v(93.16, 70.64) * mm, "end": v(93.22, 70.73) * mm});
            skLineSegment(sketch, "E748", {"start": v(93.22, 70.73) * mm, "end": v(93.29, 70.82) * mm});
            skLineSegment(sketch, "E749", {"start": v(93.29, 70.82) * mm, "end": v(93.35, 70.9) * mm});
            skLineSegment(sketch, "E750", {"start": v(93.35, 70.9) * mm, "end": v(93.42, 71) * mm});
            skLineSegment(sketch, "E751", {"start": v(93.42, 71) * mm, "end": v(93.48, 71.1) * mm});
            skLineSegment(sketch, "E752", {"start": v(93.48, 71.1) * mm, "end": v(93.55, 71.2) * mm});
            skLineSegment(sketch, "E753", {"start": v(93.55, 71.2) * mm, "end": v(93.62, 71.29) * mm});
            skLineSegment(sketch, "E754", {"start": v(93.62, 71.29) * mm, "end": v(93.75, 71.48) * mm});
            skLineSegment(sketch, "E755", {"start": v(93.75, 71.48) * mm, "end": v(93.82, 71.58) * mm});
            skLineSegment(sketch, "E756", {"start": v(93.82, 71.58) * mm, "end": v(93.9, 71.68) * mm});
            skLineSegment(sketch, "E757", {"start": v(93.9, 71.68) * mm, "end": v(93.96, 71.79) * mm});
            skLineSegment(sketch, "E758", {"start": v(93.96, 71.79) * mm, "end": v(94.03, 71.89) * mm});
            skLineSegment(sketch, "E759", {"start": v(94.03, 71.89) * mm, "end": v(94.1, 72) * mm});
            skLineSegment(sketch, "E760", {"start": v(94.1, 72) * mm, "end": v(94.17, 72.1) * mm});
            skLineSegment(sketch, "E761", {"start": v(94.17, 72.1) * mm, "end": v(94.23, 72.2) * mm});
            skLineSegment(sketch, "E762", {"start": v(94.23, 72.2) * mm, "end": v(94.3, 72.32) * mm});
            skLineSegment(sketch, "E763", {"start": v(94.3, 72.32) * mm, "end": v(94.45, 72.54) * mm});
            skLineSegment(sketch, "E764", {"start": v(94.45, 72.54) * mm, "end": v(94.52, 72.65) * mm});
            skLineSegment(sketch, "E765", {"start": v(94.52, 72.65) * mm, "end": v(94.59, 72.76) * mm});
            skLineSegment(sketch, "E766", {"start": v(94.59, 72.76) * mm, "end": v(94.66, 72.87) * mm});
            skLineSegment(sketch, "E767", {"start": v(94.66, 72.87) * mm, "end": v(94.73, 73) * mm});
            skLineSegment(sketch, "E768", {"start": v(94.73, 73) * mm, "end": v(94.8, 73.1) * mm});
            skLineSegment(sketch, "E769", {"start": v(94.8, 73.1) * mm, "end": v(94.88, 73.22) * mm});
            skLineSegment(sketch, "E770", {"start": v(94.88, 73.22) * mm, "end": v(94.95, 73.34) * mm});
            skLineSegment(sketch, "E771", {"start": v(94.95, 73.34) * mm, "end": v(95.02, 73.46) * mm});
            skLineSegment(sketch, "E772", {"start": v(95.02, 73.46) * mm, "end": v(95.1, 73.59) * mm});
            skLineSegment(sketch, "E773", {"start": v(95.1, 73.59) * mm, "end": v(95.24, 73.83) * mm});
            skLineSegment(sketch, "E774", {"start": v(95.24, 73.83) * mm, "end": v(95.31, 73.96) * mm});
            skLineSegment(sketch, "E775", {"start": v(95.31, 73.96) * mm, "end": v(95.39, 74.09) * mm});
            skLineSegment(sketch, "E776", {"start": v(95.39, 74.09) * mm, "end": v(95.46, 74.21) * mm});
            skLineSegment(sketch, "E777", {"start": v(95.46, 74.21) * mm, "end": v(95.53, 74.34) * mm});
            skLineSegment(sketch, "E778", {"start": v(95.53, 74.34) * mm, "end": v(95.6, 74.47) * mm});
            skLineSegment(sketch, "E779", {"start": v(95.6, 74.47) * mm, "end": v(95.63, 74.57) * mm});
            skLineSegment(sketch, "E780", {"start": v(95.63, 74.57) * mm, "end": v(94.6, 75.87) * mm});
            skLineSegment(sketch, "E781", {"start": v(94.6, 75.87) * mm, "end": v(94.5, 75.87) * mm});
            skLineSegment(sketch, "E782", {"start": v(94.5, 75.87) * mm, "end": v(94.36, 75.82) * mm});
            skLineSegment(sketch, "E783", {"start": v(94.36, 75.82) * mm, "end": v(94.22, 75.78) * mm});
            skLineSegment(sketch, "E784", {"start": v(94.22, 75.78) * mm, "end": v(94.08, 75.74) * mm});
            skLineSegment(sketch, "E785", {"start": v(94.08, 75.74) * mm, "end": v(93.8, 75.65) * mm});
            skLineSegment(sketch, "E786", {"start": v(93.8, 75.65) * mm, "end": v(93.66, 75.61) * mm});
            skLineSegment(sketch, "E787", {"start": v(93.66, 75.61) * mm, "end": v(93.52, 75.57) * mm});
            skLineSegment(sketch, "E788", {"start": v(93.52, 75.57) * mm, "end": v(93.39, 75.53) * mm});
            skLineSegment(sketch, "E789", {"start": v(93.39, 75.53) * mm, "end": v(93.12, 75.44) * mm});
            skLineSegment(sketch, "E790", {"start": v(93.12, 75.44) * mm, "end": v(92.86, 75.36) * mm});
            skLineSegment(sketch, "E791", {"start": v(92.86, 75.36) * mm, "end": v(92.73, 75.31) * mm});
            skLineSegment(sketch, "E792", {"start": v(92.73, 75.31) * mm, "end": v(92.6, 75.27) * mm});
            skLineSegment(sketch, "E793", {"start": v(92.6, 75.27) * mm, "end": v(92.48, 75.23) * mm});
            skLineSegment(sketch, "E794", {"start": v(92.48, 75.23) * mm, "end": v(92.35, 75.18) * mm});
            skLineSegment(sketch, "E795", {"start": v(92.35, 75.18) * mm, "end": v(92.23, 75.14) * mm});
            skLineSegment(sketch, "E796", {"start": v(92.23, 75.14) * mm, "end": v(91.98, 75.05) * mm});
            skLineSegment(sketch, "E797", {"start": v(91.98, 75.05) * mm, "end": v(91.86, 75) * mm});
            skLineSegment(sketch, "E798", {"start": v(91.86, 75) * mm, "end": v(91.63, 74.92) * mm});
            skLineSegment(sketch, "E799", {"start": v(91.63, 74.92) * mm, "end": v(91.51, 74.88) * mm});
            skLineSegment(sketch, "E800", {"start": v(91.51, 74.88) * mm, "end": v(91.4, 74.84) * mm});
            skLineSegment(sketch, "E801", {"start": v(91.4, 74.84) * mm, "end": v(91.28, 74.8) * mm});
            skLineSegment(sketch, "E802", {"start": v(91.28, 74.8) * mm, "end": v(91.17, 74.75) * mm});
            skLineSegment(sketch, "E803", {"start": v(91.17, 74.75) * mm, "end": v(91.06, 74.7) * mm});
            skLineSegment(sketch, "E804", {"start": v(91.06, 74.7) * mm, "end": v(90.84, 74.62) * mm});
            skLineSegment(sketch, "E805", {"start": v(90.84, 74.62) * mm, "end": v(90.73, 74.58) * mm});
            skLineSegment(sketch, "E806", {"start": v(90.73, 74.58) * mm, "end": v(90.52, 74.5) * mm});
            skLineSegment(sketch, "E807", {"start": v(90.52, 74.5) * mm, "end": v(90.41, 74.45) * mm});
            skLineSegment(sketch, "E808", {"start": v(90.41, 74.45) * mm, "end": v(90.31, 74.41) * mm});
            skLineSegment(sketch, "E809", {"start": v(90.31, 74.41) * mm, "end": v(90.2, 74.37) * mm});
            skLineSegment(sketch, "E810", {"start": v(90.2, 74.37) * mm, "end": v(90.1, 74.32) * mm});
            skLineSegment(sketch, "E811", {"start": v(90.1, 74.32) * mm, "end": v(90, 74.28) * mm});
            skLineSegment(sketch, "E812", {"start": v(90, 74.28) * mm, "end": v(89.26, 74.9) * mm});
            skLineSegment(sketch, "E813", {"start": v(89.26, 74.9) * mm, "end": v(88.78, 75.75) * mm});
            skLineSegment(sketch, "E814", {"start": v(88.78, 75.75) * mm, "end": v(88.84, 75.84) * mm});
            skLineSegment(sketch, "E815", {"start": v(88.84, 75.84) * mm, "end": v(88.9, 75.93) * mm});
            skLineSegment(sketch, "E816", {"start": v(88.9, 75.93) * mm, "end": v(88.95, 76.03) * mm});
            skLineSegment(sketch, "E817", {"start": v(88.95, 76.03) * mm, "end": v(89.01, 76.12) * mm});
            skLineSegment(sketch, "E818", {"start": v(89.01, 76.12) * mm, "end": v(89.07, 76.22) * mm});
            skLineSegment(sketch, "E819", {"start": v(89.07, 76.22) * mm, "end": v(89.13, 76.31) * mm});
            skLineSegment(sketch, "E820", {"start": v(89.13, 76.31) * mm, "end": v(89.2, 76.41) * mm});
            skLineSegment(sketch, "E821", {"start": v(89.2, 76.41) * mm, "end": v(89.31, 76.6) * mm});
            skLineSegment(sketch, "E822", {"start": v(89.31, 76.6) * mm, "end": v(89.44, 76.81) * mm});
            skLineSegment(sketch, "E823", {"start": v(89.44, 76.81) * mm, "end": v(89.5, 76.92) * mm});
            skLineSegment(sketch, "E824", {"start": v(89.5, 76.92) * mm, "end": v(89.56, 77.02) * mm});
            skLineSegment(sketch, "E825", {"start": v(89.56, 77.02) * mm, "end": v(89.62, 77.13) * mm});
            skLineSegment(sketch, "E826", {"start": v(89.62, 77.13) * mm, "end": v(89.69, 77.24) * mm});
            skLineSegment(sketch, "E827", {"start": v(89.69, 77.24) * mm, "end": v(89.75, 77.34) * mm});
            skLineSegment(sketch, "E828", {"start": v(89.75, 77.34) * mm, "end": v(89.88, 77.56) * mm});
            skLineSegment(sketch, "E829", {"start": v(89.88, 77.56) * mm, "end": v(89.94, 77.68) * mm});
            skLineSegment(sketch, "E830", {"start": v(89.94, 77.68) * mm, "end": v(90, 77.8) * mm});
            skLineSegment(sketch, "E831", {"start": v(90, 77.8) * mm, "end": v(90.07, 77.9) * mm});
            skLineSegment(sketch, "E832", {"start": v(90.07, 77.9) * mm, "end": v(90.13, 78.02) * mm});
            skLineSegment(sketch, "E833", {"start": v(90.13, 78.02) * mm, "end": v(90.2, 78.14) * mm});
            skLineSegment(sketch, "E834", {"start": v(90.2, 78.14) * mm, "end": v(90.33, 78.37) * mm});
            skLineSegment(sketch, "E835", {"start": v(90.33, 78.37) * mm, "end": v(90.4, 78.5) * mm});
            skLineSegment(sketch, "E836", {"start": v(90.4, 78.5) * mm, "end": v(90.46, 78.62) * mm});
            skLineSegment(sketch, "E837", {"start": v(90.46, 78.62) * mm, "end": v(90.59, 78.87) * mm});
            skLineSegment(sketch, "E838", {"start": v(90.59, 78.87) * mm, "end": v(90.65, 79) * mm});
            skLineSegment(sketch, "E839", {"start": v(90.65, 79) * mm, "end": v(90.72, 79.12) * mm});
            skLineSegment(sketch, "E840", {"start": v(90.72, 79.12) * mm, "end": v(90.78, 79.25) * mm});
            skLineSegment(sketch, "E841", {"start": v(90.78, 79.25) * mm, "end": v(90.92, 79.5) * mm});
            skLineSegment(sketch, "E842", {"start": v(90.92, 79.5) * mm, "end": v(90.98, 79.64) * mm});
            skLineSegment(sketch, "E843", {"start": v(90.98, 79.64) * mm, "end": v(91.11, 79.9) * mm});
            skLineSegment(sketch, "E844", {"start": v(91.11, 79.9) * mm, "end": v(91.14, 80) * mm});
            skLineSegment(sketch, "E845", {"start": v(91.14, 80) * mm, "end": v(90.03, 81.24) * mm});
            skLineSegment(sketch, "E846", {"start": v(90.03, 81.24) * mm, "end": v(89.94, 81.23) * mm});
            skLineSegment(sketch, "E847", {"start": v(89.94, 81.23) * mm, "end": v(89.8, 81.18) * mm});
            skLineSegment(sketch, "E848", {"start": v(89.8, 81.18) * mm, "end": v(89.65, 81.13) * mm});
            skLineSegment(sketch, "E849", {"start": v(89.65, 81.13) * mm, "end": v(89.51, 81.08) * mm});
            skLineSegment(sketch, "E850", {"start": v(89.51, 81.08) * mm, "end": v(89.38, 81.03) * mm});
            skLineSegment(sketch, "E851", {"start": v(89.38, 81.03) * mm, "end": v(89.24, 80.98) * mm});
            skLineSegment(sketch, "E852", {"start": v(89.24, 80.98) * mm, "end": v(89.1, 80.93) * mm});
            skLineSegment(sketch, "E853", {"start": v(89.1, 80.93) * mm, "end": v(88.97, 80.88) * mm});
            skLineSegment(sketch, "E854", {"start": v(88.97, 80.88) * mm, "end": v(88.84, 80.83) * mm});
            skLineSegment(sketch, "E855", {"start": v(88.84, 80.83) * mm, "end": v(88.7, 80.78) * mm});
            skLineSegment(sketch, "E856", {"start": v(88.7, 80.78) * mm, "end": v(88.58, 80.73) * mm});
            skLineSegment(sketch, "E857", {"start": v(88.58, 80.73) * mm, "end": v(88.45, 80.68) * mm});
            skLineSegment(sketch, "E858", {"start": v(88.45, 80.68) * mm, "end": v(88.32, 80.63) * mm});
            skLineSegment(sketch, "E859", {"start": v(88.32, 80.63) * mm, "end": v(88.2, 80.58) * mm});
            skLineSegment(sketch, "E860", {"start": v(88.2, 80.58) * mm, "end": v(88.07, 80.53) * mm});
            skLineSegment(sketch, "E861", {"start": v(88.07, 80.53) * mm, "end": v(87.95, 80.48) * mm});
            skLineSegment(sketch, "E862", {"start": v(87.95, 80.48) * mm, "end": v(87.83, 80.43) * mm});
            skLineSegment(sketch, "E863", {"start": v(87.83, 80.43) * mm, "end": v(87.7, 80.37) * mm});
            skLineSegment(sketch, "E864", {"start": v(87.7, 80.37) * mm, "end": v(87.58, 80.32) * mm});
            skLineSegment(sketch, "E865", {"start": v(87.58, 80.32) * mm, "end": v(87.47, 80.27) * mm});
            skLineSegment(sketch, "E866", {"start": v(87.47, 80.27) * mm, "end": v(87.35, 80.22) * mm});
            skLineSegment(sketch, "E867", {"start": v(87.35, 80.22) * mm, "end": v(87.23, 80.17) * mm});
            skLineSegment(sketch, "E868", {"start": v(87.23, 80.17) * mm, "end": v(87.12, 80.12) * mm});
            skLineSegment(sketch, "E869", {"start": v(87.12, 80.12) * mm, "end": v(87, 80.07) * mm});
            skLineSegment(sketch, "E870", {"start": v(87, 80.07) * mm, "end": v(86.89, 80.02) * mm});
            skLineSegment(sketch, "E871", {"start": v(86.89, 80.02) * mm, "end": v(86.67, 79.92) * mm});
            skLineSegment(sketch, "E872", {"start": v(86.67, 79.92) * mm, "end": v(86.56, 79.88) * mm});
            skLineSegment(sketch, "E873", {"start": v(86.56, 79.88) * mm, "end": v(86.35, 79.78) * mm});
            skLineSegment(sketch, "E874", {"start": v(86.35, 79.78) * mm, "end": v(86.24, 79.73) * mm});
            skLineSegment(sketch, "E875", {"start": v(86.24, 79.73) * mm, "end": v(86.14, 79.68) * mm});
            skLineSegment(sketch, "E876", {"start": v(86.14, 79.68) * mm, "end": v(85.93, 79.58) * mm});
            skLineSegment(sketch, "E877", {"start": v(85.93, 79.58) * mm, "end": v(85.83, 79.53) * mm});
            skLineSegment(sketch, "E878", {"start": v(85.83, 79.53) * mm, "end": v(85.73, 79.49) * mm});
            skLineSegment(sketch, "E879", {"start": v(85.73, 79.49) * mm, "end": v(85.63, 79.44) * mm});
            skLineSegment(sketch, "E880", {"start": v(85.63, 79.44) * mm, "end": v(85.54, 79.4) * mm});
            skLineSegment(sketch, "E881", {"start": v(85.54, 79.4) * mm, "end": v(84.75, 79.97) * mm});
            skLineSegment(sketch, "E882", {"start": v(84.75, 79.97) * mm, "end": v(84.22, 80.79) * mm});
            skLineSegment(sketch, "E883", {"start": v(84.22, 80.79) * mm, "end": v(84.27, 80.88) * mm});
            skLineSegment(sketch, "E884", {"start": v(84.27, 80.88) * mm, "end": v(84.33, 80.97) * mm});
            skLineSegment(sketch, "E885", {"start": v(84.33, 80.97) * mm, "end": v(84.38, 81.07) * mm});
            skLineSegment(sketch, "E886", {"start": v(84.38, 81.07) * mm, "end": v(84.44, 81.17) * mm});
            skLineSegment(sketch, "E887", {"start": v(84.44, 81.17) * mm, "end": v(84.5, 81.27) * mm});
            skLineSegment(sketch, "E888", {"start": v(84.5, 81.27) * mm, "end": v(84.54, 81.37) * mm});
            skLineSegment(sketch, "E889", {"start": v(84.54, 81.37) * mm, "end": v(84.65, 81.57) * mm});
            skLineSegment(sketch, "E890", {"start": v(84.65, 81.57) * mm, "end": v(84.7, 81.67) * mm});
            skLineSegment(sketch, "E891", {"start": v(84.7, 81.67) * mm, "end": v(84.76, 81.78) * mm});
            skLineSegment(sketch, "E892", {"start": v(84.76, 81.78) * mm, "end": v(84.82, 81.88) * mm});
            skLineSegment(sketch, "E893", {"start": v(84.82, 81.88) * mm, "end": v(84.88, 82) * mm});
            skLineSegment(sketch, "E894", {"start": v(84.88, 82) * mm, "end": v(84.99, 82.2) * mm});
            skLineSegment(sketch, "E895", {"start": v(84.99, 82.2) * mm, "end": v(85.04, 82.32) * mm});
            skLineSegment(sketch, "E896", {"start": v(85.04, 82.32) * mm, "end": v(85.1, 82.43) * mm});
            skLineSegment(sketch, "E897", {"start": v(85.1, 82.43) * mm, "end": v(85.16, 82.54) * mm});
            skLineSegment(sketch, "E898", {"start": v(85.16, 82.54) * mm, "end": v(85.22, 82.66) * mm});
            skLineSegment(sketch, "E899", {"start": v(85.22, 82.66) * mm, "end": v(85.27, 82.77) * mm});
            skLineSegment(sketch, "E900", {"start": v(85.27, 82.77) * mm, "end": v(85.33, 82.9) * mm});
            skLineSegment(sketch, "E901", {"start": v(85.33, 82.9) * mm, "end": v(85.39, 83.01) * mm});
            skLineSegment(sketch, "E902", {"start": v(85.39, 83.01) * mm, "end": v(85.44, 83.13) * mm});
            skLineSegment(sketch, "E903", {"start": v(85.44, 83.13) * mm, "end": v(85.5, 83.25) * mm});
            skLineSegment(sketch, "E904", {"start": v(85.5, 83.25) * mm, "end": v(85.56, 83.37) * mm});
            skLineSegment(sketch, "E905", {"start": v(85.56, 83.37) * mm, "end": v(85.62, 83.5) * mm});
            skLineSegment(sketch, "E906", {"start": v(85.62, 83.5) * mm, "end": v(85.73, 83.74) * mm});
            skLineSegment(sketch, "E907", {"start": v(85.73, 83.74) * mm, "end": v(85.8, 83.87) * mm});
            skLineSegment(sketch, "E908", {"start": v(85.8, 83.87) * mm, "end": v(85.85, 84) * mm});
            skLineSegment(sketch, "E909", {"start": v(85.85, 84) * mm, "end": v(85.9, 84.13) * mm});
            skLineSegment(sketch, "E910", {"start": v(85.9, 84.13) * mm, "end": v(85.96, 84.26) * mm});
            skLineSegment(sketch, "E911", {"start": v(85.96, 84.26) * mm, "end": v(86.08, 84.52) * mm});
            skLineSegment(sketch, "E912", {"start": v(86.08, 84.52) * mm, "end": v(86.14, 84.66) * mm});
            skLineSegment(sketch, "E913", {"start": v(86.14, 84.66) * mm, "end": v(86.2, 84.8) * mm});
            skLineSegment(sketch, "E914", {"start": v(86.2, 84.8) * mm, "end": v(86.26, 84.93) * mm});
            skLineSegment(sketch, "E915", {"start": v(86.26, 84.93) * mm, "end": v(86.31, 85.07) * mm});
            skLineSegment(sketch, "E916", {"start": v(86.31, 85.07) * mm, "end": v(86.33, 85.17) * mm});
            skLineSegment(sketch, "E917", {"start": v(86.33, 85.17) * mm, "end": v(85.16, 86.34) * mm});
            skLineSegment(sketch, "E918", {"start": v(85.16, 86.34) * mm, "end": v(85.06, 86.32) * mm});
            skLineSegment(sketch, "E919", {"start": v(85.06, 86.32) * mm, "end": v(84.92, 86.27) * mm});
            skLineSegment(sketch, "E920", {"start": v(84.92, 86.27) * mm, "end": v(84.78, 86.2) * mm});
            skLineSegment(sketch, "E921", {"start": v(84.78, 86.2) * mm, "end": v(84.65, 86.15) * mm});
            skLineSegment(sketch, "E922", {"start": v(84.65, 86.15) * mm, "end": v(84.51, 86.1) * mm});
            skLineSegment(sketch, "E923", {"start": v(84.51, 86.1) * mm, "end": v(84.38, 86.03) * mm});
            skLineSegment(sketch, "E924", {"start": v(84.38, 86.03) * mm, "end": v(84.25, 85.97) * mm});
            skLineSegment(sketch, "E925", {"start": v(84.25, 85.97) * mm, "end": v(84.12, 85.92) * mm});
            skLineSegment(sketch, "E926", {"start": v(84.12, 85.92) * mm, "end": v(83.99, 85.86) * mm});
            skLineSegment(sketch, "E927", {"start": v(83.99, 85.86) * mm, "end": v(83.86, 85.8) * mm});
            skLineSegment(sketch, "E928", {"start": v(83.86, 85.8) * mm, "end": v(83.73, 85.74) * mm});
            skLineSegment(sketch, "E929", {"start": v(83.73, 85.74) * mm, "end": v(83.6, 85.68) * mm});
            skLineSegment(sketch, "E930", {"start": v(83.6, 85.68) * mm, "end": v(83.36, 85.57) * mm});
            skLineSegment(sketch, "E931", {"start": v(83.36, 85.57) * mm, "end": v(83.24, 85.51) * mm});
            skLineSegment(sketch, "E932", {"start": v(83.24, 85.51) * mm, "end": v(83.12, 85.45) * mm});
            skLineSegment(sketch, "E933", {"start": v(83.12, 85.45) * mm, "end": v(82.88, 85.34) * mm});
            skLineSegment(sketch, "E934", {"start": v(82.88, 85.34) * mm, "end": v(82.76, 85.28) * mm});
            skLineSegment(sketch, "E935", {"start": v(82.76, 85.28) * mm, "end": v(82.65, 85.22) * mm});
            skLineSegment(sketch, "E936", {"start": v(82.65, 85.22) * mm, "end": v(82.53, 85.17) * mm});
            skLineSegment(sketch, "E937", {"start": v(82.53, 85.17) * mm, "end": v(82.42, 85.11) * mm});
            skLineSegment(sketch, "E938", {"start": v(82.42, 85.11) * mm, "end": v(82.31, 85.05) * mm});
            skLineSegment(sketch, "E939", {"start": v(82.31, 85.05) * mm, "end": v(82.09, 84.94) * mm});
            skLineSegment(sketch, "E940", {"start": v(82.09, 84.94) * mm, "end": v(81.98, 84.89) * mm});
            skLineSegment(sketch, "E941", {"start": v(81.98, 84.89) * mm, "end": v(81.87, 84.83) * mm});
            skLineSegment(sketch, "E942", {"start": v(81.87, 84.83) * mm, "end": v(81.77, 84.77) * mm});
            skLineSegment(sketch, "E943", {"start": v(81.77, 84.77) * mm, "end": v(81.66, 84.72) * mm});
            skLineSegment(sketch, "E944", {"start": v(81.66, 84.72) * mm, "end": v(81.56, 84.66) * mm});
            skLineSegment(sketch, "E945", {"start": v(81.56, 84.66) * mm, "end": v(81.46, 84.6) * mm});
            skLineSegment(sketch, "E946", {"start": v(81.46, 84.6) * mm, "end": v(81.26, 84.5) * mm});
            skLineSegment(sketch, "E947", {"start": v(81.26, 84.5) * mm, "end": v(81.06, 84.4) * mm});
            skLineSegment(sketch, "E948", {"start": v(81.06, 84.4) * mm, "end": v(80.97, 84.34) * mm});
            skLineSegment(sketch, "E949", {"start": v(80.97, 84.34) * mm, "end": v(80.87, 84.28) * mm});
            skLineSegment(sketch, "E950", {"start": v(80.87, 84.28) * mm, "end": v(80.78, 84.23) * mm});
            skLineSegment(sketch, "E951", {"start": v(80.78, 84.23) * mm, "end": v(79.96, 84.76) * mm});
            skLineSegment(sketch, "E952", {"start": v(79.96, 84.76) * mm, "end": v(79.38, 85.55) * mm});
            skLineSegment(sketch, "E953", {"start": v(79.38, 85.55) * mm, "end": v(79.43, 85.64) * mm});
            skLineSegment(sketch, "E954", {"start": v(79.43, 85.64) * mm, "end": v(79.48, 85.74) * mm});
            skLineSegment(sketch, "E955", {"start": v(79.48, 85.74) * mm, "end": v(79.53, 85.84) * mm});
            skLineSegment(sketch, "E956", {"start": v(79.53, 85.84) * mm, "end": v(79.62, 86.04) * mm});
            skLineSegment(sketch, "E957", {"start": v(79.62, 86.04) * mm, "end": v(79.67, 86.15) * mm});
            skLineSegment(sketch, "E958", {"start": v(79.67, 86.15) * mm, "end": v(79.72, 86.25) * mm});
            skLineSegment(sketch, "E959", {"start": v(79.72, 86.25) * mm, "end": v(79.77, 86.35) * mm});
            skLineSegment(sketch, "E960", {"start": v(79.77, 86.35) * mm, "end": v(79.82, 86.46) * mm});
            skLineSegment(sketch, "E961", {"start": v(79.82, 86.46) * mm, "end": v(79.87, 86.57) * mm});
            skLineSegment(sketch, "E962", {"start": v(79.87, 86.57) * mm, "end": v(79.92, 86.68) * mm});
            skLineSegment(sketch, "E963", {"start": v(79.92, 86.68) * mm, "end": v(79.96, 86.79) * mm});
            skLineSegment(sketch, "E964", {"start": v(79.96, 86.79) * mm, "end": v(80.01, 86.9) * mm});
            skLineSegment(sketch, "E965", {"start": v(80.01, 86.9) * mm, "end": v(80.07, 87.01) * mm});
            skLineSegment(sketch, "E966", {"start": v(80.07, 87.01) * mm, "end": v(80.12, 87.13) * mm});
            skLineSegment(sketch, "E967", {"start": v(80.12, 87.13) * mm, "end": v(80.21, 87.36) * mm});
            skLineSegment(sketch, "E968", {"start": v(80.21, 87.36) * mm, "end": v(80.27, 87.47) * mm});
            skLineSegment(sketch, "E969", {"start": v(80.27, 87.47) * mm, "end": v(80.31, 87.6) * mm});
            skLineSegment(sketch, "E970", {"start": v(80.31, 87.6) * mm, "end": v(80.36, 87.71) * mm});
            skLineSegment(sketch, "E971", {"start": v(80.36, 87.71) * mm, "end": v(80.42, 87.83) * mm});
            skLineSegment(sketch, "E972", {"start": v(80.42, 87.83) * mm, "end": v(80.47, 87.96) * mm});
            skLineSegment(sketch, "E973", {"start": v(80.47, 87.96) * mm, "end": v(80.52, 88.08) * mm});
            skLineSegment(sketch, "E974", {"start": v(80.52, 88.08) * mm, "end": v(80.57, 88.2) * mm});
            skLineSegment(sketch, "E975", {"start": v(80.57, 88.2) * mm, "end": v(80.62, 88.33) * mm});
            skLineSegment(sketch, "E976", {"start": v(80.62, 88.33) * mm, "end": v(80.72, 88.59) * mm});
            skLineSegment(sketch, "E977", {"start": v(80.72, 88.59) * mm, "end": v(80.77, 88.72) * mm});
            skLineSegment(sketch, "E978", {"start": v(80.77, 88.72) * mm, "end": v(80.82, 88.85) * mm});
            skLineSegment(sketch, "E979", {"start": v(80.82, 88.85) * mm, "end": v(80.87, 88.98) * mm});
            skLineSegment(sketch, "E980", {"start": v(80.87, 88.98) * mm, "end": v(80.92, 89.11) * mm});
            skLineSegment(sketch, "E981", {"start": v(80.92, 89.11) * mm, "end": v(80.97, 89.25) * mm});
            skLineSegment(sketch, "E982", {"start": v(80.97, 89.25) * mm, "end": v(81.02, 89.39) * mm});
            skLineSegment(sketch, "E983", {"start": v(81.02, 89.39) * mm, "end": v(81.12, 89.66) * mm});
            skLineSegment(sketch, "E984", {"start": v(81.12, 89.66) * mm, "end": v(81.22, 89.94) * mm});
            skLineSegment(sketch, "E985", {"start": v(81.22, 89.94) * mm, "end": v(81.23, 90.04) * mm});
            skLineSegment(sketch, "E986", {"start": v(81.23, 90.04) * mm, "end": v(80, 91.14) * mm});
            skLineSegment(sketch, "E987", {"start": v(80, 91.14) * mm, "end": v(79.9, 91.12) * mm});
            skLineSegment(sketch, "E988", {"start": v(79.9, 91.12) * mm, "end": v(79.76, 91.06) * mm});
            skLineSegment(sketch, "E989", {"start": v(79.76, 91.06) * mm, "end": v(79.63, 91) * mm});
            skLineSegment(sketch, "E990", {"start": v(79.63, 91) * mm, "end": v(79.5, 90.92) * mm});
            skLineSegment(sketch, "E991", {"start": v(79.5, 90.92) * mm, "end": v(79.37, 90.86) * mm});
            skLineSegment(sketch, "E992", {"start": v(79.37, 90.86) * mm, "end": v(79.24, 90.8) * mm});
            skLineSegment(sketch, "E993", {"start": v(79.24, 90.8) * mm, "end": v(79.1, 90.73) * mm});
            skLineSegment(sketch, "E994", {"start": v(79.1, 90.73) * mm, "end": v(78.98, 90.66) * mm});
            skLineSegment(sketch, "E995", {"start": v(78.98, 90.66) * mm, "end": v(78.86, 90.6) * mm});
            skLineSegment(sketch, "E996", {"start": v(78.86, 90.6) * mm, "end": v(78.73, 90.53) * mm});
            skLineSegment(sketch, "E997", {"start": v(78.73, 90.53) * mm, "end": v(78.6, 90.47) * mm});
            skLineSegment(sketch, "E998", {"start": v(78.6, 90.47) * mm, "end": v(78.49, 90.4) * mm});
            skLineSegment(sketch, "E999", {"start": v(78.49, 90.4) * mm, "end": v(78.37, 90.33) * mm});
            skLineSegment(sketch, "E1000", {"start": v(78.37, 90.33) * mm, "end": v(78.24, 90.27) * mm});
            skLineSegment(sketch, "E1001", {"start": v(78.24, 90.27) * mm, "end": v(78.13, 90.2) * mm});
            skLineSegment(sketch, "E1002", {"start": v(78.13, 90.2) * mm, "end": v(78.01, 90.14) * mm});
            skLineSegment(sketch, "E1003", {"start": v(78.01, 90.14) * mm, "end": v(77.9, 90.08) * mm});
            skLineSegment(sketch, "E1004", {"start": v(77.9, 90.08) * mm, "end": v(77.78, 90.01) * mm});
            skLineSegment(sketch, "E1005", {"start": v(77.78, 90.01) * mm, "end": v(77.67, 89.95) * mm});
            skLineSegment(sketch, "E1006", {"start": v(77.67, 89.95) * mm, "end": v(77.44, 89.82) * mm});
            skLineSegment(sketch, "E1007", {"start": v(77.44, 89.82) * mm, "end": v(77.33, 89.76) * mm});
            skLineSegment(sketch, "E1008", {"start": v(77.33, 89.76) * mm, "end": v(77.23, 89.7) * mm});
            skLineSegment(sketch, "E1009", {"start": v(77.23, 89.7) * mm, "end": v(77.12, 89.63) * mm});
            skLineSegment(sketch, "E1010", {"start": v(77.12, 89.63) * mm, "end": v(77.01, 89.57) * mm});
            skLineSegment(sketch, "E1011", {"start": v(77.01, 89.57) * mm, "end": v(76.9, 89.5) * mm});
            skLineSegment(sketch, "E1012", {"start": v(76.9, 89.5) * mm, "end": v(76.8, 89.45) * mm});
            skLineSegment(sketch, "E1013", {"start": v(76.8, 89.45) * mm, "end": v(76.6, 89.32) * mm});
            skLineSegment(sketch, "E1014", {"start": v(76.6, 89.32) * mm, "end": v(76.4, 89.2) * mm});
            skLineSegment(sketch, "E1015", {"start": v(76.4, 89.2) * mm, "end": v(76.3, 89.14) * mm});
            skLineSegment(sketch, "E1016", {"start": v(76.3, 89.14) * mm, "end": v(76.2, 89.08) * mm});
            skLineSegment(sketch, "E1017", {"start": v(76.2, 89.08) * mm, "end": v(76.11, 89.02) * mm});
            skLineSegment(sketch, "E1018", {"start": v(76.11, 89.02) * mm, "end": v(76.02, 88.96) * mm});
            skLineSegment(sketch, "E1019", {"start": v(76.02, 88.96) * mm, "end": v(75.92, 88.9) * mm});
            skLineSegment(sketch, "E1020", {"start": v(75.92, 88.9) * mm, "end": v(75.83, 88.84) * mm});
            skLineSegment(sketch, "E1021", {"start": v(75.83, 88.84) * mm, "end": v(75.74, 88.78) * mm});
            skLineSegment(sketch, "E1022", {"start": v(75.74, 88.78) * mm, "end": v(74.9, 89.27) * mm});
            skLineSegment(sketch, "E1023", {"start": v(74.9, 89.27) * mm, "end": v(74.27, 90.02) * mm});
            skLineSegment(sketch, "E1024", {"start": v(74.27, 90.02) * mm, "end": v(74.31, 90.12) * mm});
            skLineSegment(sketch, "E1025", {"start": v(74.31, 90.12) * mm, "end": v(74.36, 90.22) * mm});
            skLineSegment(sketch, "E1026", {"start": v(74.36, 90.22) * mm, "end": v(74.4, 90.32) * mm});
            skLineSegment(sketch, "E1027", {"start": v(74.4, 90.32) * mm, "end": v(74.48, 90.53) * mm});
            skLineSegment(sketch, "E1028", {"start": v(74.48, 90.53) * mm, "end": v(74.57, 90.74) * mm});
            skLineSegment(sketch, "E1029", {"start": v(74.57, 90.74) * mm, "end": v(74.61, 90.85) * mm});
            skLineSegment(sketch, "E1030", {"start": v(74.61, 90.85) * mm, "end": v(74.7, 91.07) * mm});
            skLineSegment(sketch, "E1031", {"start": v(74.7, 91.07) * mm, "end": v(74.74, 91.18) * mm});
            skLineSegment(sketch, "E1032", {"start": v(74.74, 91.18) * mm, "end": v(74.78, 91.3) * mm});
            skLineSegment(sketch, "E1033", {"start": v(74.78, 91.3) * mm, "end": v(74.83, 91.4) * mm});
            skLineSegment(sketch, "E1034", {"start": v(74.83, 91.4) * mm, "end": v(74.91, 91.64) * mm});
            skLineSegment(sketch, "E1035", {"start": v(74.91, 91.64) * mm, "end": v(74.96, 91.75) * mm});
            skLineSegment(sketch, "E1036", {"start": v(74.96, 91.75) * mm, "end": v(75, 91.87) * mm});
            skLineSegment(sketch, "E1037", {"start": v(75, 91.87) * mm, "end": v(75.04, 92) * mm});
            skLineSegment(sketch, "E1038", {"start": v(75.04, 92) * mm, "end": v(75.09, 92.11) * mm});
            skLineSegment(sketch, "E1039", {"start": v(75.09, 92.11) * mm, "end": v(75.13, 92.24) * mm});
            skLineSegment(sketch, "E1040", {"start": v(75.13, 92.24) * mm, "end": v(75.21, 92.49) * mm});
            skLineSegment(sketch, "E1041", {"start": v(75.21, 92.49) * mm, "end": v(75.26, 92.61) * mm});
            skLineSegment(sketch, "E1042", {"start": v(75.26, 92.61) * mm, "end": v(75.34, 92.87) * mm});
            skLineSegment(sketch, "E1043", {"start": v(75.34, 92.87) * mm, "end": v(75.39, 93) * mm});
            skLineSegment(sketch, "E1044", {"start": v(75.39, 93) * mm, "end": v(75.43, 93.13) * mm});
            skLineSegment(sketch, "E1045", {"start": v(75.43, 93.13) * mm, "end": v(75.52, 93.4) * mm});
            skLineSegment(sketch, "E1046", {"start": v(75.52, 93.4) * mm, "end": v(75.56, 93.53) * mm});
            skLineSegment(sketch, "E1047", {"start": v(75.56, 93.53) * mm, "end": v(75.6, 93.67) * mm});
            skLineSegment(sketch, "E1048", {"start": v(75.6, 93.67) * mm, "end": v(75.64, 93.8) * mm});
            skLineSegment(sketch, "E1049", {"start": v(75.64, 93.8) * mm, "end": v(75.69, 93.95) * mm});
            skLineSegment(sketch, "E1050", {"start": v(75.69, 93.95) * mm, "end": v(75.73, 94.09) * mm});
            skLineSegment(sketch, "E1051", {"start": v(75.73, 94.09) * mm, "end": v(75.77, 94.23) * mm});
            skLineSegment(sketch, "E1052", {"start": v(75.77, 94.23) * mm, "end": v(75.81, 94.37) * mm});
            skLineSegment(sketch, "E1053", {"start": v(75.81, 94.37) * mm, "end": v(75.86, 94.51) * mm});
            skLineSegment(sketch, "E1054", {"start": v(75.86, 94.51) * mm, "end": v(75.86, 94.61) * mm});
            skLineSegment(sketch, "E1055", {"start": v(75.86, 94.61) * mm, "end": v(74.56, 95.64) * mm});
            skLineSegment(sketch, "E1056", {"start": v(74.56, 95.64) * mm, "end": v(74.46, 95.62) * mm});
            skLineSegment(sketch, "E1057", {"start": v(74.46, 95.62) * mm, "end": v(74.33, 95.54) * mm});
            skLineSegment(sketch, "E1058", {"start": v(74.33, 95.54) * mm, "end": v(74.2, 95.47) * mm});
            skLineSegment(sketch, "E1059", {"start": v(74.2, 95.47) * mm, "end": v(74.08, 95.4) * mm});
            skLineSegment(sketch, "E1060", {"start": v(74.08, 95.4) * mm, "end": v(73.95, 95.32) * mm});
            skLineSegment(sketch, "E1061", {"start": v(73.95, 95.32) * mm, "end": v(73.82, 95.25) * mm});
            skLineSegment(sketch, "E1062", {"start": v(73.82, 95.25) * mm, "end": v(73.7, 95.17) * mm});
            skLineSegment(sketch, "E1063", {"start": v(73.7, 95.17) * mm, "end": v(73.58, 95.1) * mm});
            skLineSegment(sketch, "E1064", {"start": v(73.58, 95.1) * mm, "end": v(73.33, 94.96) * mm});
            skLineSegment(sketch, "E1065", {"start": v(73.33, 94.96) * mm, "end": v(73.22, 94.88) * mm});
            skLineSegment(sketch, "E1066", {"start": v(73.22, 94.88) * mm, "end": v(73.1, 94.81) * mm});
            skLineSegment(sketch, "E1067", {"start": v(73.1, 94.81) * mm, "end": v(72.98, 94.74) * mm});
            skLineSegment(sketch, "E1068", {"start": v(72.98, 94.74) * mm, "end": v(72.86, 94.67) * mm});
            skLineSegment(sketch, "E1069", {"start": v(72.86, 94.67) * mm, "end": v(72.75, 94.6) * mm});
            skLineSegment(sketch, "E1070", {"start": v(72.75, 94.6) * mm, "end": v(72.64, 94.53) * mm});
            skLineSegment(sketch, "E1071", {"start": v(72.64, 94.53) * mm, "end": v(72.52, 94.45) * mm});
            skLineSegment(sketch, "E1072", {"start": v(72.52, 94.45) * mm, "end": v(72.41, 94.38) * mm});
            skLineSegment(sketch, "E1073", {"start": v(72.41, 94.38) * mm, "end": v(72.2, 94.24) * mm});
            skLineSegment(sketch, "E1074", {"start": v(72.2, 94.24) * mm, "end": v(72.09, 94.17) * mm});
            skLineSegment(sketch, "E1075", {"start": v(72.09, 94.17) * mm, "end": v(71.98, 94.1) * mm});
            skLineSegment(sketch, "E1076", {"start": v(71.98, 94.1) * mm, "end": v(71.88, 94.03) * mm});
            skLineSegment(sketch, "E1077", {"start": v(71.88, 94.03) * mm, "end": v(71.67, 93.9) * mm});
            skLineSegment(sketch, "E1078", {"start": v(71.67, 93.9) * mm, "end": v(71.57, 93.83) * mm});
            skLineSegment(sketch, "E1079", {"start": v(71.57, 93.83) * mm, "end": v(71.47, 93.76) * mm});
            skLineSegment(sketch, "E1080", {"start": v(71.47, 93.76) * mm, "end": v(71.37, 93.7) * mm});
            skLineSegment(sketch, "E1081", {"start": v(71.37, 93.7) * mm, "end": v(71.28, 93.63) * mm});
            skLineSegment(sketch, "E1082", {"start": v(71.28, 93.63) * mm, "end": v(71.18, 93.56) * mm});
            skLineSegment(sketch, "E1083", {"start": v(71.18, 93.56) * mm, "end": v(71.08, 93.5) * mm});
            skLineSegment(sketch, "E1084", {"start": v(71.08, 93.5) * mm, "end": v(71, 93.43) * mm});
            skLineSegment(sketch, "E1085", {"start": v(71, 93.43) * mm, "end": v(70.9, 93.36) * mm});
            skLineSegment(sketch, "E1086", {"start": v(70.9, 93.36) * mm, "end": v(70.8, 93.3) * mm});
            skLineSegment(sketch, "E1087", {"start": v(70.8, 93.3) * mm, "end": v(70.63, 93.17) * mm});
            skLineSegment(sketch, "E1088", {"start": v(70.63, 93.17) * mm, "end": v(70.54, 93.1) * mm});
            skLineSegment(sketch, "E1089", {"start": v(70.54, 93.1) * mm, "end": v(70.45, 93.04) * mm});
            skLineSegment(sketch, "E1090", {"start": v(70.45, 93.04) * mm, "end": v(69.58, 93.47) * mm});
            skLineSegment(sketch, "E1091", {"start": v(69.58, 93.47) * mm, "end": v(68.91, 94.18) * mm});
            skLineSegment(sketch, "E1092", {"start": v(68.91, 94.18) * mm, "end": v(68.95, 94.29) * mm});
            skLineSegment(sketch, "E1093", {"start": v(68.95, 94.29) * mm, "end": v(69.02, 94.5) * mm});
            skLineSegment(sketch, "E1094", {"start": v(69.02, 94.5) * mm, "end": v(69.06, 94.6) * mm});
            skLineSegment(sketch, "E1095", {"start": v(69.06, 94.6) * mm, "end": v(69.1, 94.7) * mm});
            skLineSegment(sketch, "E1096", {"start": v(69.1, 94.7) * mm, "end": v(69.13, 94.81) * mm});
            skLineSegment(sketch, "E1097", {"start": v(69.13, 94.81) * mm, "end": v(69.17, 94.92) * mm});
            skLineSegment(sketch, "E1098", {"start": v(69.17, 94.92) * mm, "end": v(69.2, 95.03) * mm});
            skLineSegment(sketch, "E1099", {"start": v(69.2, 95.03) * mm, "end": v(69.24, 95.14) * mm});
            skLineSegment(sketch, "E1100", {"start": v(69.24, 95.14) * mm, "end": v(69.28, 95.26) * mm});
            skLineSegment(sketch, "E1101", {"start": v(69.28, 95.26) * mm, "end": v(69.31, 95.37) * mm});
            skLineSegment(sketch, "E1102", {"start": v(69.31, 95.37) * mm, "end": v(69.35, 95.48) * mm});
            skLineSegment(sketch, "E1103", {"start": v(69.35, 95.48) * mm, "end": v(69.39, 95.6) * mm});
            skLineSegment(sketch, "E1104", {"start": v(69.39, 95.6) * mm, "end": v(69.42, 95.72) * mm});
            skLineSegment(sketch, "E1105", {"start": v(69.42, 95.72) * mm, "end": v(69.46, 95.84) * mm});
            skLineSegment(sketch, "E1106", {"start": v(69.46, 95.84) * mm, "end": v(69.5, 95.96) * mm});
            skLineSegment(sketch, "E1107", {"start": v(69.5, 95.96) * mm, "end": v(69.53, 96.08) * mm});
            skLineSegment(sketch, "E1108", {"start": v(69.53, 96.08) * mm, "end": v(69.57, 96.2) * mm});
            skLineSegment(sketch, "E1109", {"start": v(69.57, 96.2) * mm, "end": v(69.6, 96.32) * mm});
            skLineSegment(sketch, "E1110", {"start": v(69.6, 96.32) * mm, "end": v(69.64, 96.45) * mm});
            skLineSegment(sketch, "E1111", {"start": v(69.64, 96.45) * mm, "end": v(69.68, 96.58) * mm});
            skLineSegment(sketch, "E1112", {"start": v(69.68, 96.58) * mm, "end": v(69.75, 96.83) * mm});
            skLineSegment(sketch, "E1113", {"start": v(69.75, 96.83) * mm, "end": v(69.78, 96.96) * mm});
            skLineSegment(sketch, "E1114", {"start": v(69.78, 96.96) * mm, "end": v(69.82, 97.1) * mm});
            skLineSegment(sketch, "E1115", {"start": v(69.82, 97.1) * mm, "end": v(69.85, 97.23) * mm});
            skLineSegment(sketch, "E1116", {"start": v(69.85, 97.23) * mm, "end": v(69.89, 97.36) * mm});
            skLineSegment(sketch, "E1117", {"start": v(69.89, 97.36) * mm, "end": v(69.92, 97.5) * mm});
            skLineSegment(sketch, "E1118", {"start": v(69.92, 97.5) * mm, "end": v(69.96, 97.63) * mm});
            skLineSegment(sketch, "E1119", {"start": v(69.96, 97.63) * mm, "end": v(70, 97.77) * mm});
            skLineSegment(sketch, "E1120", {"start": v(70, 97.77) * mm, "end": v(70.06, 98.05) * mm});
            skLineSegment(sketch, "E1121", {"start": v(70.06, 98.05) * mm, "end": v(70.1, 98.19) * mm});
            skLineSegment(sketch, "E1122", {"start": v(70.1, 98.19) * mm, "end": v(70.13, 98.33) * mm});
            skLineSegment(sketch, "E1123", {"start": v(70.13, 98.33) * mm, "end": v(70.16, 98.47) * mm});
            skLineSegment(sketch, "E1124", {"start": v(70.16, 98.47) * mm, "end": v(70.2, 98.62) * mm});
            skLineSegment(sketch, "E1125", {"start": v(70.2, 98.62) * mm, "end": v(70.23, 98.77) * mm});
            skLineSegment(sketch, "E1126", {"start": v(70.23, 98.77) * mm, "end": v(70.23, 98.86) * mm});
            skLineSegment(sketch, "E1127", {"start": v(70.23, 98.86) * mm, "end": v(68.87, 99.81) * mm});
            skLineSegment(sketch, "E1128", {"start": v(68.87, 99.81) * mm, "end": v(68.78, 99.78) * mm});
            skLineSegment(sketch, "E1129", {"start": v(68.78, 99.78) * mm, "end": v(68.65, 99.7) * mm});
            skLineSegment(sketch, "E1130", {"start": v(68.65, 99.7) * mm, "end": v(68.53, 99.62) * mm});
            skLineSegment(sketch, "E1131", {"start": v(68.53, 99.62) * mm, "end": v(68.4, 99.54) * mm});
            skLineSegment(sketch, "E1132", {"start": v(68.4, 99.54) * mm, "end": v(68.28, 99.46) * mm});
            skLineSegment(sketch, "E1133", {"start": v(68.28, 99.46) * mm, "end": v(68.16, 99.38) * mm});
            skLineSegment(sketch, "E1134", {"start": v(68.16, 99.38) * mm, "end": v(68.04, 99.3) * mm});
            skLineSegment(sketch, "E1135", {"start": v(68.04, 99.3) * mm, "end": v(67.92, 99.22) * mm});
            skLineSegment(sketch, "E1136", {"start": v(67.92, 99.22) * mm, "end": v(67.8, 99.14) * mm});
            skLineSegment(sketch, "E1137", {"start": v(67.8, 99.14) * mm, "end": v(67.69, 99.06) * mm});
            skLineSegment(sketch, "E1138", {"start": v(67.69, 99.06) * mm, "end": v(67.57, 98.98) * mm});
            skLineSegment(sketch, "E1139", {"start": v(67.57, 98.98) * mm, "end": v(67.35, 98.82) * mm});
            skLineSegment(sketch, "E1140", {"start": v(67.35, 98.82) * mm, "end": v(67.24, 98.74) * mm});
            skLineSegment(sketch, "E1141", {"start": v(67.24, 98.74) * mm, "end": v(67.13, 98.67) * mm});
            skLineSegment(sketch, "E1142", {"start": v(67.13, 98.67) * mm, "end": v(67.02, 98.59) * mm});
            skLineSegment(sketch, "E1143", {"start": v(67.02, 98.59) * mm, "end": v(66.91, 98.51) * mm});
            skLineSegment(sketch, "E1144", {"start": v(66.91, 98.51) * mm, "end": v(66.8, 98.43) * mm});
            skLineSegment(sketch, "E1145", {"start": v(66.8, 98.43) * mm, "end": v(66.7, 98.36) * mm});
            skLineSegment(sketch, "E1146", {"start": v(66.7, 98.36) * mm, "end": v(66.5, 98.2) * mm});
            skLineSegment(sketch, "E1147", {"start": v(66.5, 98.2) * mm, "end": v(66.3, 98.05) * mm});
            skLineSegment(sketch, "E1148", {"start": v(66.3, 98.05) * mm, "end": v(66.2, 97.98) * mm});
            skLineSegment(sketch, "E1149", {"start": v(66.2, 97.98) * mm, "end": v(66, 97.83) * mm});
            skLineSegment(sketch, "E1150", {"start": v(66, 97.83) * mm, "end": v(65.8, 97.68) * mm});
            skLineSegment(sketch, "E1151", {"start": v(65.8, 97.68) * mm, "end": v(65.71, 97.61) * mm});
            skLineSegment(sketch, "E1152", {"start": v(65.71, 97.61) * mm, "end": v(65.62, 97.54) * mm});
            skLineSegment(sketch, "E1153", {"start": v(65.62, 97.54) * mm, "end": v(65.53, 97.47) * mm});
            skLineSegment(sketch, "E1154", {"start": v(65.53, 97.47) * mm, "end": v(65.44, 97.4) * mm});
            skLineSegment(sketch, "E1155", {"start": v(65.44, 97.4) * mm, "end": v(65.35, 97.33) * mm});
            skLineSegment(sketch, "E1156", {"start": v(65.35, 97.33) * mm, "end": v(65.26, 97.26) * mm});
            skLineSegment(sketch, "E1157", {"start": v(65.26, 97.26) * mm, "end": v(65.18, 97.18) * mm});
            skLineSegment(sketch, "E1158", {"start": v(65.18, 97.18) * mm, "end": v(65.1, 97.11) * mm});
            skLineSegment(sketch, "E1159", {"start": v(65.1, 97.11) * mm, "end": v(65, 97.05) * mm});
            skLineSegment(sketch, "E1160", {"start": v(65, 97.05) * mm, "end": v(64.92, 96.98) * mm});
            skLineSegment(sketch, "E1161", {"start": v(64.92, 96.98) * mm, "end": v(64.03, 97.36) * mm});
            skLineSegment(sketch, "E1162", {"start": v(64.03, 97.36) * mm, "end": v(63.32, 98.03) * mm});
            skLineSegment(sketch, "E1163", {"start": v(63.32, 98.03) * mm, "end": v(63.35, 98.13) * mm});
            skLineSegment(sketch, "E1164", {"start": v(63.35, 98.13) * mm, "end": v(63.38, 98.24) * mm});
            skLineSegment(sketch, "E1165", {"start": v(63.38, 98.24) * mm, "end": v(63.41, 98.35) * mm});
            skLineSegment(sketch, "E1166", {"start": v(63.41, 98.35) * mm, "end": v(63.44, 98.45) * mm});
            skLineSegment(sketch, "E1167", {"start": v(63.44, 98.45) * mm, "end": v(63.47, 98.56) * mm});
            skLineSegment(sketch, "E1168", {"start": v(63.47, 98.56) * mm, "end": v(63.53, 98.78) * mm});
            skLineSegment(sketch, "E1169", {"start": v(63.53, 98.78) * mm, "end": v(63.56, 98.9) * mm});
            skLineSegment(sketch, "E1170", {"start": v(63.56, 98.9) * mm, "end": v(63.62, 99.12) * mm});
            skLineSegment(sketch, "E1171", {"start": v(63.62, 99.12) * mm, "end": v(63.65, 99.24) * mm});
            skLineSegment(sketch, "E1172", {"start": v(63.65, 99.24) * mm, "end": v(63.68, 99.36) * mm});
            skLineSegment(sketch, "E1173", {"start": v(63.68, 99.36) * mm, "end": v(63.74, 99.6) * mm});
            skLineSegment(sketch, "E1174", {"start": v(63.74, 99.6) * mm, "end": v(63.77, 99.71) * mm});
            skLineSegment(sketch, "E1175", {"start": v(63.77, 99.71) * mm, "end": v(63.8, 99.83) * mm});
            skLineSegment(sketch, "E1176", {"start": v(63.8, 99.83) * mm, "end": v(63.86, 100.08) * mm});
            skLineSegment(sketch, "E1177", {"start": v(63.86, 100.08) * mm, "end": v(63.88, 100.2) * mm});
            skLineSegment(sketch, "E1178", {"start": v(63.88, 100.2) * mm, "end": v(63.91, 100.33) * mm});
            skLineSegment(sketch, "E1179", {"start": v(63.91, 100.33) * mm, "end": v(63.94, 100.46) * mm});
            skLineSegment(sketch, "E1180", {"start": v(63.94, 100.46) * mm, "end": v(63.97, 100.6) * mm});
            skLineSegment(sketch, "E1181", {"start": v(63.97, 100.6) * mm, "end": v(64, 100.72) * mm});
            skLineSegment(sketch, "E1182", {"start": v(64, 100.72) * mm, "end": v(64.03, 100.86) * mm});
            skLineSegment(sketch, "E1183", {"start": v(64.03, 100.86) * mm, "end": v(64.05, 100.99) * mm});
            skLineSegment(sketch, "E1184", {"start": v(64.05, 100.99) * mm, "end": v(64.1, 101.26) * mm});
            skLineSegment(sketch, "E1185", {"start": v(64.1, 101.26) * mm, "end": v(64.14, 101.4) * mm});
            skLineSegment(sketch, "E1186", {"start": v(64.14, 101.4) * mm, "end": v(64.16, 101.53) * mm});
            skLineSegment(sketch, "E1187", {"start": v(64.16, 101.53) * mm, "end": v(64.19, 101.67) * mm});
            skLineSegment(sketch, "E1188", {"start": v(64.19, 101.67) * mm, "end": v(64.22, 101.81) * mm});
            skLineSegment(sketch, "E1189", {"start": v(64.22, 101.81) * mm, "end": v(64.24, 101.95) * mm});
            skLineSegment(sketch, "E1190", {"start": v(64.24, 101.95) * mm, "end": v(64.27, 102.1) * mm});
            skLineSegment(sketch, "E1191", {"start": v(64.27, 102.1) * mm, "end": v(64.3, 102.24) * mm});
            skLineSegment(sketch, "E1192", {"start": v(64.3, 102.24) * mm, "end": v(64.32, 102.39) * mm});
            skLineSegment(sketch, "E1193", {"start": v(64.32, 102.39) * mm, "end": v(64.34, 102.53) * mm});
            skLineSegment(sketch, "E1194", {"start": v(64.34, 102.53) * mm, "end": v(64.37, 102.68) * mm});
            skLineSegment(sketch, "E1195", {"start": v(64.37, 102.68) * mm, "end": v(64.36, 102.78) * mm});
            skLineSegment(sketch, "E1196", {"start": v(64.36, 102.78) * mm, "end": v(62.95, 103.65) * mm});
            skLineSegment(sketch, "E1197", {"start": v(62.95, 103.65) * mm, "end": v(62.86, 103.61) * mm});
            skLineSegment(sketch, "E1198", {"start": v(62.86, 103.61) * mm, "end": v(62.74, 103.53) * mm});
            skLineSegment(sketch, "E1199", {"start": v(62.74, 103.53) * mm, "end": v(62.62, 103.44) * mm});
            skLineSegment(sketch, "E1200", {"start": v(62.62, 103.44) * mm, "end": v(62.5, 103.35) * mm});
            skLineSegment(sketch, "E1201", {"start": v(62.5, 103.35) * mm, "end": v(62.38, 103.26) * mm});
            skLineSegment(sketch, "E1202", {"start": v(62.38, 103.26) * mm, "end": v(62.27, 103.17) * mm});
            skLineSegment(sketch, "E1203", {"start": v(62.27, 103.17) * mm, "end": v(62.04, 103) * mm});
            skLineSegment(sketch, "E1204", {"start": v(62.04, 103) * mm, "end": v(61.93, 102.91) * mm});
            skLineSegment(sketch, "E1205", {"start": v(61.93, 102.91) * mm, "end": v(61.81, 102.83) * mm});
            skLineSegment(sketch, "E1206", {"start": v(61.81, 102.83) * mm, "end": v(61.7, 102.74) * mm});
            skLineSegment(sketch, "E1207", {"start": v(61.7, 102.74) * mm, "end": v(61.6, 102.66) * mm});
            skLineSegment(sketch, "E1208", {"start": v(61.6, 102.66) * mm, "end": v(61.49, 102.57) * mm});
            skLineSegment(sketch, "E1209", {"start": v(61.49, 102.57) * mm, "end": v(61.28, 102.4) * mm});
            skLineSegment(sketch, "E1210", {"start": v(61.28, 102.4) * mm, "end": v(61.17, 102.32) * mm});
            skLineSegment(sketch, "E1211", {"start": v(61.17, 102.32) * mm, "end": v(61.07, 102.24) * mm});
            skLineSegment(sketch, "E1212", {"start": v(61.07, 102.24) * mm, "end": v(60.97, 102.15) * mm});
            skLineSegment(sketch, "E1213", {"start": v(60.97, 102.15) * mm, "end": v(60.87, 102.07) * mm});
            skLineSegment(sketch, "E1214", {"start": v(60.87, 102.07) * mm, "end": v(60.77, 101.99) * mm});
            skLineSegment(sketch, "E1215", {"start": v(60.77, 101.99) * mm, "end": v(60.67, 101.9) * mm});
            skLineSegment(sketch, "E1216", {"start": v(60.67, 101.9) * mm, "end": v(60.48, 101.74) * mm});
            skLineSegment(sketch, "E1217", {"start": v(60.48, 101.74) * mm, "end": v(60.38, 101.66) * mm});
            skLineSegment(sketch, "E1218", {"start": v(60.38, 101.66) * mm, "end": v(60.29, 101.58) * mm});
            skLineSegment(sketch, "E1219", {"start": v(60.29, 101.58) * mm, "end": v(60.2, 101.5) * mm});
            skLineSegment(sketch, "E1220", {"start": v(60.2, 101.5) * mm, "end": v(60.1, 101.43) * mm});
            skLineSegment(sketch, "E1221", {"start": v(60.1, 101.43) * mm, "end": v(59.93, 101.27) * mm});
            skLineSegment(sketch, "E1222", {"start": v(59.93, 101.27) * mm, "end": v(59.84, 101.2) * mm});
            skLineSegment(sketch, "E1223", {"start": v(59.84, 101.2) * mm, "end": v(59.75, 101.11) * mm});
            skLineSegment(sketch, "E1224", {"start": v(59.75, 101.11) * mm, "end": v(59.66, 101.04) * mm});
            skLineSegment(sketch, "E1225", {"start": v(59.66, 101.04) * mm, "end": v(59.5, 100.89) * mm});
            skLineSegment(sketch, "E1226", {"start": v(59.5, 100.89) * mm, "end": v(59.33, 100.74) * mm});
            skLineSegment(sketch, "E1227", {"start": v(59.33, 100.74) * mm, "end": v(59.25, 100.66) * mm});
            skLineSegment(sketch, "E1228", {"start": v(59.25, 100.66) * mm, "end": v(59.17, 100.59) * mm});
            skLineSegment(sketch, "E1229", {"start": v(59.17, 100.59) * mm, "end": v(58.26, 100.92) * mm});
            skLineSegment(sketch, "E1230", {"start": v(58.26, 100.92) * mm, "end": v(57.51, 101.55) * mm});
            skLineSegment(sketch, "E1231", {"start": v(57.51, 101.55) * mm, "end": v(57.54, 101.65) * mm});
            skLineSegment(sketch, "E1232", {"start": v(57.54, 101.65) * mm, "end": v(57.56, 101.76) * mm});
            skLineSegment(sketch, "E1233", {"start": v(57.56, 101.76) * mm, "end": v(57.59, 101.87) * mm});
            skLineSegment(sketch, "E1234", {"start": v(57.59, 101.87) * mm, "end": v(57.6, 101.97) * mm});
            skLineSegment(sketch, "E1235", {"start": v(57.6, 101.97) * mm, "end": v(57.63, 102.09) * mm});
            skLineSegment(sketch, "E1236", {"start": v(57.63, 102.09) * mm, "end": v(57.66, 102.2) * mm});
            skLineSegment(sketch, "E1237", {"start": v(57.66, 102.2) * mm, "end": v(57.68, 102.3) * mm});
            skLineSegment(sketch, "E1238", {"start": v(57.68, 102.3) * mm, "end": v(57.7, 102.42) * mm});
            skLineSegment(sketch, "E1239", {"start": v(57.7, 102.42) * mm, "end": v(57.73, 102.54) * mm});
            skLineSegment(sketch, "E1240", {"start": v(57.73, 102.54) * mm, "end": v(57.75, 102.65) * mm});
            skLineSegment(sketch, "E1241", {"start": v(57.75, 102.65) * mm, "end": v(57.77, 102.77) * mm});
            skLineSegment(sketch, "E1242", {"start": v(57.77, 102.77) * mm, "end": v(57.8, 102.89) * mm});
            skLineSegment(sketch, "E1243", {"start": v(57.8, 102.89) * mm, "end": v(57.82, 103) * mm});
            skLineSegment(sketch, "E1244", {"start": v(57.82, 103) * mm, "end": v(57.84, 103.13) * mm});
            skLineSegment(sketch, "E1245", {"start": v(57.84, 103.13) * mm, "end": v(57.86, 103.25) * mm});
            skLineSegment(sketch, "E1246", {"start": v(57.86, 103.25) * mm, "end": v(57.9, 103.5) * mm});
            skLineSegment(sketch, "E1247", {"start": v(57.9, 103.5) * mm, "end": v(57.93, 103.63) * mm});
            skLineSegment(sketch, "E1248", {"start": v(57.93, 103.63) * mm, "end": v(57.95, 103.75) * mm});
            skLineSegment(sketch, "E1249", {"start": v(57.95, 103.75) * mm, "end": v(57.97, 103.88) * mm});
            skLineSegment(sketch, "E1250", {"start": v(57.97, 103.88) * mm, "end": v(58, 104.01) * mm});
            skLineSegment(sketch, "E1251", {"start": v(58, 104.01) * mm, "end": v(58.01, 104.14) * mm});
            skLineSegment(sketch, "E1252", {"start": v(58.01, 104.14) * mm, "end": v(58.05, 104.4) * mm});
            skLineSegment(sketch, "E1253", {"start": v(58.05, 104.4) * mm, "end": v(58.1, 104.68) * mm});
            skLineSegment(sketch, "E1254", {"start": v(58.1, 104.68) * mm, "end": v(58.11, 104.81) * mm});
            skLineSegment(sketch, "E1255", {"start": v(58.11, 104.81) * mm, "end": v(58.13, 104.95) * mm});
            skLineSegment(sketch, "E1256", {"start": v(58.13, 104.95) * mm, "end": v(58.15, 105.1) * mm});
            skLineSegment(sketch, "E1257", {"start": v(58.15, 105.1) * mm, "end": v(58.17, 105.23) * mm});
            skLineSegment(sketch, "E1258", {"start": v(58.17, 105.23) * mm, "end": v(58.19, 105.37) * mm});
            skLineSegment(sketch, "E1259", {"start": v(58.19, 105.37) * mm, "end": v(58.22, 105.66) * mm});
            skLineSegment(sketch, "E1260", {"start": v(58.22, 105.66) * mm, "end": v(58.24, 105.8) * mm});
            skLineSegment(sketch, "E1261", {"start": v(58.24, 105.8) * mm, "end": v(58.26, 105.95) * mm});
            skLineSegment(sketch, "E1262", {"start": v(58.26, 105.95) * mm, "end": v(58.27, 106.1) * mm});
            skLineSegment(sketch, "E1263", {"start": v(58.27, 106.1) * mm, "end": v(58.3, 106.25) * mm});
            skLineSegment(sketch, "E1264", {"start": v(58.3, 106.25) * mm, "end": v(58.28, 106.35) * mm});
            skLineSegment(sketch, "E1265", {"start": v(58.28, 106.35) * mm, "end": v(56.82, 107.13) * mm});
            skLineSegment(sketch, "E1266", {"start": v(56.82, 107.13) * mm, "end": v(56.73, 107.1) * mm});
            skLineSegment(sketch, "E1267", {"start": v(56.73, 107.1) * mm, "end": v(56.61, 107) * mm});
            skLineSegment(sketch, "E1268", {"start": v(56.61, 107) * mm, "end": v(56.5, 106.9) * mm});
            skLineSegment(sketch, "E1269", {"start": v(56.5, 106.9) * mm, "end": v(56.39, 106.8) * mm});
            skLineSegment(sketch, "E1270", {"start": v(56.39, 106.8) * mm, "end": v(56.27, 106.71) * mm});
            skLineSegment(sketch, "E1271", {"start": v(56.27, 106.71) * mm, "end": v(56.16, 106.62) * mm});
            skLineSegment(sketch, "E1272", {"start": v(56.16, 106.62) * mm, "end": v(55.94, 106.43) * mm});
            skLineSegment(sketch, "E1273", {"start": v(55.94, 106.43) * mm, "end": v(55.84, 106.34) * mm});
            skLineSegment(sketch, "E1274", {"start": v(55.84, 106.34) * mm, "end": v(55.73, 106.25) * mm});
            skLineSegment(sketch, "E1275", {"start": v(55.73, 106.25) * mm, "end": v(55.63, 106.15) * mm});
            skLineSegment(sketch, "E1276", {"start": v(55.63, 106.15) * mm, "end": v(55.52, 106.06) * mm});
            skLineSegment(sketch, "E1277", {"start": v(55.52, 106.06) * mm, "end": v(55.32, 105.88) * mm});
            skLineSegment(sketch, "E1278", {"start": v(55.32, 105.88) * mm, "end": v(55.22, 105.8) * mm});
            skLineSegment(sketch, "E1279", {"start": v(55.22, 105.8) * mm, "end": v(55.02, 105.61) * mm});
            skLineSegment(sketch, "E1280", {"start": v(55.02, 105.61) * mm, "end": v(54.92, 105.52) * mm});
            skLineSegment(sketch, "E1281", {"start": v(54.92, 105.52) * mm, "end": v(54.73, 105.35) * mm});
            skLineSegment(sketch, "E1282", {"start": v(54.73, 105.35) * mm, "end": v(54.64, 105.26) * mm});
            skLineSegment(sketch, "E1283", {"start": v(54.64, 105.26) * mm, "end": v(54.55, 105.17) * mm});
            skLineSegment(sketch, "E1284", {"start": v(54.55, 105.17) * mm, "end": v(54.46, 105.09) * mm});
            skLineSegment(sketch, "E1285", {"start": v(54.46, 105.09) * mm, "end": v(54.28, 104.92) * mm});
            skLineSegment(sketch, "E1286", {"start": v(54.28, 104.92) * mm, "end": v(54.2, 104.83) * mm});
            skLineSegment(sketch, "E1287", {"start": v(54.2, 104.83) * mm, "end": v(54.1, 104.75) * mm});
            skLineSegment(sketch, "E1288", {"start": v(54.1, 104.75) * mm, "end": v(54.02, 104.67) * mm});
            skLineSegment(sketch, "E1289", {"start": v(54.02, 104.67) * mm, "end": v(53.94, 104.58) * mm});
            skLineSegment(sketch, "E1290", {"start": v(53.94, 104.58) * mm, "end": v(53.85, 104.5) * mm});
            skLineSegment(sketch, "E1291", {"start": v(53.85, 104.5) * mm, "end": v(53.69, 104.34) * mm});
            skLineSegment(sketch, "E1292", {"start": v(53.69, 104.34) * mm, "end": v(53.61, 104.25) * mm});
            skLineSegment(sketch, "E1293", {"start": v(53.61, 104.25) * mm, "end": v(53.45, 104.1) * mm});
            skLineSegment(sketch, "E1294", {"start": v(53.45, 104.1) * mm, "end": v(53.38, 104.02) * mm});
            skLineSegment(sketch, "E1295", {"start": v(53.38, 104.02) * mm, "end": v(53.3, 103.94) * mm});
            skLineSegment(sketch, "E1296", {"start": v(53.3, 103.94) * mm, "end": v(53.23, 103.86) * mm});
            skLineSegment(sketch, "E1297", {"start": v(53.23, 103.86) * mm, "end": v(52.3, 104.14) * mm});
            skLineSegment(sketch, "E1298", {"start": v(52.3, 104.14) * mm, "end": v(51.51, 104.72) * mm});
            skLineSegment(sketch, "E1299", {"start": v(51.51, 104.72) * mm, "end": v(51.53, 104.83) * mm});
            skLineSegment(sketch, "E1300", {"start": v(51.53, 104.83) * mm, "end": v(51.55, 104.93) * mm});
            skLineSegment(sketch, "E1301", {"start": v(51.55, 104.93) * mm, "end": v(51.56, 105.04) * mm});
            skLineSegment(sketch, "E1302", {"start": v(51.56, 105.04) * mm, "end": v(51.58, 105.15) * mm});
            skLineSegment(sketch, "E1303", {"start": v(51.58, 105.15) * mm, "end": v(51.6, 105.26) * mm});
            skLineSegment(sketch, "E1304", {"start": v(51.6, 105.26) * mm, "end": v(51.62, 105.38) * mm});
            skLineSegment(sketch, "E1305", {"start": v(51.62, 105.38) * mm, "end": v(51.63, 105.49) * mm});
            skLineSegment(sketch, "E1306", {"start": v(51.63, 105.49) * mm, "end": v(51.67, 105.72) * mm});
            skLineSegment(sketch, "E1307", {"start": v(51.67, 105.72) * mm, "end": v(51.68, 105.84) * mm});
            skLineSegment(sketch, "E1308", {"start": v(51.68, 105.84) * mm, "end": v(51.7, 105.96) * mm});
            skLineSegment(sketch, "E1309", {"start": v(51.7, 105.96) * mm, "end": v(51.72, 106.08) * mm});
            skLineSegment(sketch, "E1310", {"start": v(51.72, 106.08) * mm, "end": v(51.75, 106.32) * mm});
            skLineSegment(sketch, "E1311", {"start": v(51.75, 106.32) * mm, "end": v(51.78, 106.57) * mm});
            skLineSegment(sketch, "E1312", {"start": v(51.78, 106.57) * mm, "end": v(51.8, 106.7) * mm});
            skLineSegment(sketch, "E1313", {"start": v(51.8, 106.7) * mm, "end": v(51.83, 107.08) * mm});
            skLineSegment(sketch, "E1314", {"start": v(51.83, 107.08) * mm, "end": v(51.85, 107.2) * mm});
            skLineSegment(sketch, "E1315", {"start": v(51.85, 107.2) * mm, "end": v(51.86, 107.34) * mm});
            skLineSegment(sketch, "E1316", {"start": v(51.86, 107.34) * mm, "end": v(51.87, 107.47) * mm});
            skLineSegment(sketch, "E1317", {"start": v(51.87, 107.47) * mm, "end": v(51.9, 107.74) * mm});
            skLineSegment(sketch, "E1318", {"start": v(51.9, 107.74) * mm, "end": v(51.9, 107.88) * mm});
            skLineSegment(sketch, "E1319", {"start": v(51.9, 107.88) * mm, "end": v(51.92, 108.02) * mm});
            skLineSegment(sketch, "E1320", {"start": v(51.92, 108.02) * mm, "end": v(51.93, 108.16) * mm});
            skLineSegment(sketch, "E1321", {"start": v(51.93, 108.16) * mm, "end": v(51.94, 108.3) * mm});
            skLineSegment(sketch, "E1322", {"start": v(51.94, 108.3) * mm, "end": v(51.95, 108.44) * mm});
            skLineSegment(sketch, "E1323", {"start": v(51.95, 108.44) * mm, "end": v(51.97, 108.72) * mm});
            skLineSegment(sketch, "E1324", {"start": v(51.97, 108.72) * mm, "end": v(51.98, 108.87) * mm});
            skLineSegment(sketch, "E1325", {"start": v(51.98, 108.87) * mm, "end": v(51.99, 109.01) * mm});
            skLineSegment(sketch, "E1326", {"start": v(51.99, 109.01) * mm, "end": v(52, 109.16) * mm});
            skLineSegment(sketch, "E1327", {"start": v(52, 109.16) * mm, "end": v(52, 109.3) * mm});
            skLineSegment(sketch, "E1328", {"start": v(52, 109.3) * mm, "end": v(52.01, 109.46) * mm});
            skLineSegment(sketch, "E1329", {"start": v(52.01, 109.46) * mm, "end": v(52, 109.56) * mm});
            skLineSegment(sketch, "E1330", {"start": v(52, 109.56) * mm, "end": v(50.49, 110.26) * mm});
            skLineSegment(sketch, "E1331", {"start": v(50.49, 110.26) * mm, "end": v(50.4, 110.2) * mm});
            skLineSegment(sketch, "E1332", {"start": v(50.4, 110.2) * mm, "end": v(50.19, 110) * mm});
            skLineSegment(sketch, "E1333", {"start": v(50.19, 110) * mm, "end": v(50.08, 109.9) * mm});
            skLineSegment(sketch, "E1334", {"start": v(50.08, 109.9) * mm, "end": v(49.97, 109.8) * mm});
            skLineSegment(sketch, "E1335", {"start": v(49.97, 109.8) * mm, "end": v(49.76, 109.6) * mm});
            skLineSegment(sketch, "E1336", {"start": v(49.76, 109.6) * mm, "end": v(49.66, 109.5) * mm});
            skLineSegment(sketch, "E1337", {"start": v(49.66, 109.5) * mm, "end": v(49.56, 109.4) * mm});
            skLineSegment(sketch, "E1338", {"start": v(49.56, 109.4) * mm, "end": v(49.46, 109.3) * mm});
            skLineSegment(sketch, "E1339", {"start": v(49.46, 109.3) * mm, "end": v(49.36, 109.2) * mm});
            skLineSegment(sketch, "E1340", {"start": v(49.36, 109.2) * mm, "end": v(49.26, 109.11) * mm});
            skLineSegment(sketch, "E1341", {"start": v(49.26, 109.11) * mm, "end": v(49.16, 109.02) * mm});
            skLineSegment(sketch, "E1342", {"start": v(49.16, 109.02) * mm, "end": v(49.07, 108.92) * mm});
            skLineSegment(sketch, "E1343", {"start": v(49.07, 108.92) * mm, "end": v(48.97, 108.82) * mm});
            skLineSegment(sketch, "E1344", {"start": v(48.97, 108.82) * mm, "end": v(48.88, 108.73) * mm});
            skLineSegment(sketch, "E1345", {"start": v(48.88, 108.73) * mm, "end": v(48.7, 108.54) * mm});
            skLineSegment(sketch, "E1346", {"start": v(48.7, 108.54) * mm, "end": v(48.6, 108.45) * mm});
            skLineSegment(sketch, "E1347", {"start": v(48.6, 108.45) * mm, "end": v(48.52, 108.35) * mm});
            skLineSegment(sketch, "E1348", {"start": v(48.52, 108.35) * mm, "end": v(48.43, 108.26) * mm});
            skLineSegment(sketch, "E1349", {"start": v(48.43, 108.26) * mm, "end": v(48.34, 108.17) * mm});
            skLineSegment(sketch, "E1350", {"start": v(48.34, 108.17) * mm, "end": v(48.17, 107.99) * mm});
            skLineSegment(sketch, "E1351", {"start": v(48.17, 107.99) * mm, "end": v(48.09, 107.9) * mm});
            skLineSegment(sketch, "E1352", {"start": v(48.09, 107.9) * mm, "end": v(48, 107.8) * mm});
            skLineSegment(sketch, "E1353", {"start": v(48, 107.8) * mm, "end": v(47.92, 107.72) * mm});
            skLineSegment(sketch, "E1354", {"start": v(47.92, 107.72) * mm, "end": v(47.84, 107.63) * mm});
            skLineSegment(sketch, "E1355", {"start": v(47.84, 107.63) * mm, "end": v(47.76, 107.54) * mm});
            skLineSegment(sketch, "E1356", {"start": v(47.76, 107.54) * mm, "end": v(47.69, 107.45) * mm});
            skLineSegment(sketch, "E1357", {"start": v(47.69, 107.45) * mm, "end": v(47.6, 107.37) * mm});
            skLineSegment(sketch, "E1358", {"start": v(47.6, 107.37) * mm, "end": v(47.46, 107.2) * mm});
            skLineSegment(sketch, "E1359", {"start": v(47.46, 107.2) * mm, "end": v(47.38, 107.11) * mm});
            skLineSegment(sketch, "E1360", {"start": v(47.38, 107.11) * mm, "end": v(47.3, 107.03) * mm});
            skLineSegment(sketch, "E1361", {"start": v(47.3, 107.03) * mm, "end": v(47.24, 106.94) * mm});
            skLineSegment(sketch, "E1362", {"start": v(47.24, 106.94) * mm, "end": v(47.1, 106.78) * mm});
            skLineSegment(sketch, "E1363", {"start": v(47.1, 106.78) * mm, "end": v(46.15, 107) * mm});
            skLineSegment(sketch, "E1364", {"start": v(46.15, 107) * mm, "end": v(45.34, 107.54) * mm});
            skLineSegment(sketch, "E1365", {"start": v(45.34, 107.54) * mm, "end": v(45.35, 107.64) * mm});
            skLineSegment(sketch, "E1366", {"start": v(45.35, 107.64) * mm, "end": v(45.36, 107.75) * mm});
            skLineSegment(sketch, "E1367", {"start": v(45.36, 107.75) * mm, "end": v(45.37, 107.86) * mm});
            skLineSegment(sketch, "E1368", {"start": v(45.37, 107.86) * mm, "end": v(45.38, 107.97) * mm});
            skLineSegment(sketch, "E1369", {"start": v(45.38, 107.97) * mm, "end": v(45.4, 108.09) * mm});
            skLineSegment(sketch, "E1370", {"start": v(45.4, 108.09) * mm, "end": v(45.41, 108.31) * mm});
            skLineSegment(sketch, "E1371", {"start": v(45.41, 108.31) * mm, "end": v(45.42, 108.43) * mm});
            skLineSegment(sketch, "E1372", {"start": v(45.42, 108.43) * mm, "end": v(45.43, 108.55) * mm});
            skLineSegment(sketch, "E1373", {"start": v(45.43, 108.55) * mm, "end": v(45.44, 108.66) * mm});
            skLineSegment(sketch, "E1374", {"start": v(45.44, 108.66) * mm, "end": v(45.45, 108.78) * mm});
            skLineSegment(sketch, "E1375", {"start": v(45.45, 108.78) * mm, "end": v(45.46, 108.9) * mm});
            skLineSegment(sketch, "E1376", {"start": v(45.46, 108.9) * mm, "end": v(45.47, 109.02) * mm});
            skLineSegment(sketch, "E1377", {"start": v(45.47, 109.02) * mm, "end": v(45.48, 109.15) * mm});
            skLineSegment(sketch, "E1378", {"start": v(45.48, 109.15) * mm, "end": v(45.49, 109.27) * mm});
            skLineSegment(sketch, "E1379", {"start": v(45.49, 109.27) * mm, "end": v(45.5, 109.4) * mm});
            skLineSegment(sketch, "E1380", {"start": v(45.5, 109.4) * mm, "end": v(45.5, 109.65) * mm});
            skLineSegment(sketch, "E1381", {"start": v(45.5, 109.65) * mm, "end": v(45.52, 109.9) * mm});
            skLineSegment(sketch, "E1382", {"start": v(45.52, 109.9) * mm, "end": v(45.52, 110.04) * mm});
            skLineSegment(sketch, "E1383", {"start": v(45.52, 110.04) * mm, "end": v(45.53, 110.17) * mm});
            skLineSegment(sketch, "E1384", {"start": v(45.53, 110.17) * mm, "end": v(45.53, 110.3) * mm});
            skLineSegment(sketch, "E1385", {"start": v(45.53, 110.3) * mm, "end": v(45.54, 110.44) * mm});
            skLineSegment(sketch, "E1386", {"start": v(45.54, 110.44) * mm, "end": v(45.54, 110.58) * mm});
            skLineSegment(sketch, "E1387", {"start": v(45.54, 110.58) * mm, "end": v(45.55, 110.71) * mm});
            skLineSegment(sketch, "E1388", {"start": v(45.55, 110.71) * mm, "end": v(45.55, 110.85) * mm});
            skLineSegment(sketch, "E1389", {"start": v(45.55, 110.85) * mm, "end": v(45.55, 111) * mm});
            skLineSegment(sketch, "E1390", {"start": v(45.55, 111) * mm, "end": v(45.56, 111.13) * mm});
            skLineSegment(sketch, "E1391", {"start": v(45.56, 111.13) * mm, "end": v(45.56, 111.27) * mm});
            skLineSegment(sketch, "E1392", {"start": v(45.56, 111.27) * mm, "end": v(45.56, 111.56) * mm});
            skLineSegment(sketch, "E1393", {"start": v(45.56, 111.56) * mm, "end": v(45.56, 111.7) * mm});
            skLineSegment(sketch, "E1394", {"start": v(45.56, 111.7) * mm, "end": v(45.56, 112) * mm});
            skLineSegment(sketch, "E1395", {"start": v(45.56, 112) * mm, "end": v(45.56, 112.15) * mm});
            skLineSegment(sketch, "E1396", {"start": v(45.56, 112.15) * mm, "end": v(45.56, 112.3) * mm});
            skLineSegment(sketch, "E1397", {"start": v(45.56, 112.3) * mm, "end": v(45.54, 112.4) * mm});
            skLineSegment(sketch, "E1398", {"start": v(45.54, 112.4) * mm, "end": v(44, 113) * mm});
            skLineSegment(sketch, "E1399", {"start": v(44, 113) * mm, "end": v(43.91, 112.96) * mm});
            skLineSegment(sketch, "E1400", {"start": v(43.91, 112.96) * mm, "end": v(43.8, 112.85) * mm});
            skLineSegment(sketch, "E1401", {"start": v(43.8, 112.85) * mm, "end": v(43.6, 112.63) * mm});
            skLineSegment(sketch, "E1402", {"start": v(43.6, 112.63) * mm, "end": v(43.5, 112.52) * mm});
            skLineSegment(sketch, "E1403", {"start": v(43.5, 112.52) * mm, "end": v(43.4, 112.42) * mm});
            skLineSegment(sketch, "E1404", {"start": v(43.4, 112.42) * mm, "end": v(43.3, 112.31) * mm});
            skLineSegment(sketch, "E1405", {"start": v(43.3, 112.31) * mm, "end": v(43.2, 112.2) * mm});
            skLineSegment(sketch, "E1406", {"start": v(43.2, 112.2) * mm, "end": v(43.11, 112.1) * mm});
            skLineSegment(sketch, "E1407", {"start": v(43.11, 112.1) * mm, "end": v(43.02, 112) * mm});
            skLineSegment(sketch, "E1408", {"start": v(43.02, 112) * mm, "end": v(42.93, 111.9) * mm});
            skLineSegment(sketch, "E1409", {"start": v(42.93, 111.9) * mm, "end": v(42.83, 111.8) * mm});
            skLineSegment(sketch, "E1410", {"start": v(42.83, 111.8) * mm, "end": v(42.74, 111.7) * mm});
            skLineSegment(sketch, "E1411", {"start": v(42.74, 111.7) * mm, "end": v(42.65, 111.59) * mm});
            skLineSegment(sketch, "E1412", {"start": v(42.65, 111.59) * mm, "end": v(42.56, 111.49) * mm});
            skLineSegment(sketch, "E1413", {"start": v(42.56, 111.49) * mm, "end": v(42.48, 111.39) * mm});
            skLineSegment(sketch, "E1414", {"start": v(42.48, 111.39) * mm, "end": v(42.39, 111.29) * mm});
            skLineSegment(sketch, "E1415", {"start": v(42.39, 111.29) * mm, "end": v(42.3, 111.19) * mm});
            skLineSegment(sketch, "E1416", {"start": v(42.3, 111.19) * mm, "end": v(42.22, 111.09) * mm});
            skLineSegment(sketch, "E1417", {"start": v(42.22, 111.09) * mm, "end": v(42.14, 110.99) * mm});
            skLineSegment(sketch, "E1418", {"start": v(42.14, 110.99) * mm, "end": v(42.05, 110.9) * mm});
            skLineSegment(sketch, "E1419", {"start": v(42.05, 110.9) * mm, "end": v(41.97, 110.8) * mm});
            skLineSegment(sketch, "E1420", {"start": v(41.97, 110.8) * mm, "end": v(41.9, 110.7) * mm});
            skLineSegment(sketch, "E1421", {"start": v(41.9, 110.7) * mm, "end": v(41.81, 110.6) * mm});
            skLineSegment(sketch, "E1422", {"start": v(41.81, 110.6) * mm, "end": v(41.73, 110.5) * mm});
            skLineSegment(sketch, "E1423", {"start": v(41.73, 110.5) * mm, "end": v(41.66, 110.41) * mm});
            skLineSegment(sketch, "E1424", {"start": v(41.66, 110.41) * mm, "end": v(41.58, 110.32) * mm});
            skLineSegment(sketch, "E1425", {"start": v(41.58, 110.32) * mm, "end": v(41.5, 110.23) * mm});
            skLineSegment(sketch, "E1426", {"start": v(41.5, 110.23) * mm, "end": v(41.36, 110.04) * mm});
            skLineSegment(sketch, "E1427", {"start": v(41.36, 110.04) * mm, "end": v(41.28, 109.95) * mm});
            skLineSegment(sketch, "E1428", {"start": v(41.28, 109.95) * mm, "end": v(41.14, 109.77) * mm});
            skLineSegment(sketch, "E1429", {"start": v(41.14, 109.77) * mm, "end": v(41.08, 109.68) * mm});
            skLineSegment(sketch, "E1430", {"start": v(41.08, 109.68) * mm, "end": v(41, 109.6) * mm});
            skLineSegment(sketch, "E1431", {"start": v(41, 109.6) * mm, "end": v(40.87, 109.42) * mm});
            skLineSegment(sketch, "E1432", {"start": v(40.87, 109.42) * mm, "end": v(40.8, 109.34) * mm});
            skLineSegment(sketch, "E1433", {"start": v(40.8, 109.34) * mm, "end": v(39.85, 109.5) * mm});
            skLineSegment(sketch, "E1434", {"start": v(39.85, 109.5) * mm, "end": v(39, 110) * mm});
            skLineSegment(sketch, "E1435", {"start": v(39, 110) * mm, "end": v(39.01, 110.1) * mm});
            skLineSegment(sketch, "E1436", {"start": v(39.01, 110.1) * mm, "end": v(39.02, 110.2) * mm});
            skLineSegment(sketch, "E1437", {"start": v(39.02, 110.2) * mm, "end": v(39.02, 110.32) * mm});
            skLineSegment(sketch, "E1438", {"start": v(39.02, 110.32) * mm, "end": v(39.03, 110.43) * mm});
            skLineSegment(sketch, "E1439", {"start": v(39.03, 110.43) * mm, "end": v(39.03, 110.66) * mm});
            skLineSegment(sketch, "E1440", {"start": v(39.03, 110.66) * mm, "end": v(39.04, 110.77) * mm});
            skLineSegment(sketch, "E1441", {"start": v(39.04, 110.77) * mm, "end": v(39.04, 110.89) * mm});
            skLineSegment(sketch, "E1442", {"start": v(39.04, 110.89) * mm, "end": v(39.04, 111) * mm});
            skLineSegment(sketch, "E1443", {"start": v(39.04, 111) * mm, "end": v(39.05, 111.12) * mm});
            skLineSegment(sketch, "E1444", {"start": v(39.05, 111.12) * mm, "end": v(39.05, 111.24) * mm});
            skLineSegment(sketch, "E1445", {"start": v(39.05, 111.24) * mm, "end": v(39.05, 111.36) * mm});
            skLineSegment(sketch, "E1446", {"start": v(39.05, 111.36) * mm, "end": v(39.05, 111.6) * mm});
            skLineSegment(sketch, "E1447", {"start": v(39.05, 111.6) * mm, "end": v(39.05, 112.11) * mm});
            skLineSegment(sketch, "E1448", {"start": v(39.05, 112.11) * mm, "end": v(39.05, 112.24) * mm});
            skLineSegment(sketch, "E1449", {"start": v(39.05, 112.24) * mm, "end": v(39.05, 112.5) * mm});
            skLineSegment(sketch, "E1450", {"start": v(39.05, 112.5) * mm, "end": v(39.05, 112.63) * mm});
            skLineSegment(sketch, "E1451", {"start": v(39.05, 112.63) * mm, "end": v(39.04, 112.77) * mm});
            skLineSegment(sketch, "E1452", {"start": v(39.04, 112.77) * mm, "end": v(39.04, 112.9) * mm});
            skLineSegment(sketch, "E1453", {"start": v(39.04, 112.9) * mm, "end": v(39.04, 113.04) * mm});
            skLineSegment(sketch, "E1454", {"start": v(39.04, 113.04) * mm, "end": v(39.03, 113.31) * mm});
            skLineSegment(sketch, "E1455", {"start": v(39.03, 113.31) * mm, "end": v(39.02, 113.45) * mm});
            skLineSegment(sketch, "E1456", {"start": v(39.02, 113.45) * mm, "end": v(39.02, 113.6) * mm});
            skLineSegment(sketch, "E1457", {"start": v(39.02, 113.6) * mm, "end": v(39.01, 113.73) * mm});
            skLineSegment(sketch, "E1458", {"start": v(39.01, 113.73) * mm, "end": v(39, 113.88) * mm});
            skLineSegment(sketch, "E1459", {"start": v(39, 113.88) * mm, "end": v(39, 114.02) * mm});
            skLineSegment(sketch, "E1460", {"start": v(39, 114.02) * mm, "end": v(39, 114.17) * mm});
            skLineSegment(sketch, "E1461", {"start": v(39, 114.17) * mm, "end": v(38.98, 114.31) * mm});
            skLineSegment(sketch, "E1462", {"start": v(38.98, 114.31) * mm, "end": v(38.97, 114.46) * mm});
            skLineSegment(sketch, "E1463", {"start": v(38.97, 114.46) * mm, "end": v(38.96, 114.6) * mm});
            skLineSegment(sketch, "E1464", {"start": v(38.96, 114.6) * mm, "end": v(38.95, 114.76) * mm});
            skLineSegment(sketch, "E1465", {"start": v(38.95, 114.76) * mm, "end": v(38.92, 114.85) * mm});
            skLineSegment(sketch, "E1466", {"start": v(38.92, 114.85) * mm, "end": v(37.35, 115.37) * mm});
            skLineSegment(sketch, "E1467", {"start": v(37.35, 115.37) * mm, "end": v(37.27, 115.32) * mm});
            skLineSegment(sketch, "E1468", {"start": v(37.27, 115.32) * mm, "end": v(37.08, 115.09) * mm});
            skLineSegment(sketch, "E1469", {"start": v(37.08, 115.09) * mm, "end": v(36.98, 114.98) * mm});
            skLineSegment(sketch, "E1470", {"start": v(36.98, 114.98) * mm, "end": v(36.89, 114.86) * mm});
            skLineSegment(sketch, "E1471", {"start": v(36.89, 114.86) * mm, "end": v(36.7, 114.64) * mm});
            skLineSegment(sketch, "E1472", {"start": v(36.7, 114.64) * mm, "end": v(36.52, 114.42) * mm});
            skLineSegment(sketch, "E1473", {"start": v(36.52, 114.42) * mm, "end": v(36.35, 114.2) * mm});
            skLineSegment(sketch, "E1474", {"start": v(36.35, 114.2) * mm, "end": v(36.26, 114.1) * mm});
            skLineSegment(sketch, "E1475", {"start": v(36.26, 114.1) * mm, "end": v(36.18, 113.99) * mm});
            skLineSegment(sketch, "E1476", {"start": v(36.18, 113.99) * mm, "end": v(36.1, 113.88) * mm});
            skLineSegment(sketch, "E1477", {"start": v(36.1, 113.88) * mm, "end": v(35.93, 113.67) * mm});
            skLineSegment(sketch, "E1478", {"start": v(35.93, 113.67) * mm, "end": v(35.77, 113.46) * mm});
            skLineSegment(sketch, "E1479", {"start": v(35.77, 113.46) * mm, "end": v(35.69, 113.35) * mm});
            skLineSegment(sketch, "E1480", {"start": v(35.69, 113.35) * mm, "end": v(35.6, 113.25) * mm});
            skLineSegment(sketch, "E1481", {"start": v(35.6, 113.25) * mm, "end": v(35.53, 113.15) * mm});
            skLineSegment(sketch, "E1482", {"start": v(35.53, 113.15) * mm, "end": v(35.46, 113.05) * mm});
            skLineSegment(sketch, "E1483", {"start": v(35.46, 113.05) * mm, "end": v(35.38, 112.95) * mm});
            skLineSegment(sketch, "E1484", {"start": v(35.38, 112.95) * mm, "end": v(35.3, 112.85) * mm});
            skLineSegment(sketch, "E1485", {"start": v(35.3, 112.85) * mm, "end": v(35.24, 112.75) * mm});
            skLineSegment(sketch, "E1486", {"start": v(35.24, 112.75) * mm, "end": v(35.16, 112.65) * mm});
            skLineSegment(sketch, "E1487", {"start": v(35.16, 112.65) * mm, "end": v(35.1, 112.55) * mm});
            skLineSegment(sketch, "E1488", {"start": v(35.1, 112.55) * mm, "end": v(35.02, 112.45) * mm});
            skLineSegment(sketch, "E1489", {"start": v(35.02, 112.45) * mm, "end": v(34.89, 112.26) * mm});
            skLineSegment(sketch, "E1490", {"start": v(34.89, 112.26) * mm, "end": v(34.82, 112.17) * mm});
            skLineSegment(sketch, "E1491", {"start": v(34.82, 112.17) * mm, "end": v(34.7, 111.98) * mm});
            skLineSegment(sketch, "E1492", {"start": v(34.7, 111.98) * mm, "end": v(34.63, 111.89) * mm});
            skLineSegment(sketch, "E1493", {"start": v(34.63, 111.89) * mm, "end": v(34.57, 111.8) * mm});
            skLineSegment(sketch, "E1494", {"start": v(34.57, 111.8) * mm, "end": v(34.5, 111.7) * mm});
            skLineSegment(sketch, "E1495", {"start": v(34.5, 111.7) * mm, "end": v(34.44, 111.61) * mm});
            skLineSegment(sketch, "E1496", {"start": v(34.44, 111.61) * mm, "end": v(34.38, 111.52) * mm});
            skLineSegment(sketch, "E1497", {"start": v(34.38, 111.52) * mm, "end": v(33.41, 111.63) * mm});
            skLineSegment(sketch, "E1498", {"start": v(33.41, 111.63) * mm, "end": v(32.55, 112.07) * mm});
            skLineSegment(sketch, "E1499", {"start": v(32.55, 112.07) * mm, "end": v(32.54, 112.3) * mm});
            skLineSegment(sketch, "E1500", {"start": v(32.54, 112.3) * mm, "end": v(32.54, 112.51) * mm});
            skLineSegment(sketch, "E1501", {"start": v(32.54, 112.51) * mm, "end": v(32.54, 112.62) * mm});
            skLineSegment(sketch, "E1502", {"start": v(32.54, 112.62) * mm, "end": v(32.53, 112.85) * mm});
            skLineSegment(sketch, "E1503", {"start": v(32.53, 112.85) * mm, "end": v(32.53, 112.97) * mm});
            skLineSegment(sketch, "E1504", {"start": v(32.53, 112.97) * mm, "end": v(32.52, 113.09) * mm});
            skLineSegment(sketch, "E1505", {"start": v(32.52, 113.09) * mm, "end": v(32.52, 113.2) * mm});
            skLineSegment(sketch, "E1506", {"start": v(32.52, 113.2) * mm, "end": v(32.51, 113.32) * mm});
            skLineSegment(sketch, "E1507", {"start": v(32.51, 113.32) * mm, "end": v(32.5, 113.44) * mm});
            skLineSegment(sketch, "E1508", {"start": v(32.5, 113.44) * mm, "end": v(32.5, 113.69) * mm});
            skLineSegment(sketch, "E1509", {"start": v(32.5, 113.69) * mm, "end": v(32.5, 113.81) * mm});
            skLineSegment(sketch, "E1510", {"start": v(32.5, 113.81) * mm, "end": v(32.48, 113.94) * mm});
            skLineSegment(sketch, "E1511", {"start": v(32.48, 113.94) * mm, "end": v(32.48, 114.06) * mm});
            skLineSegment(sketch, "E1512", {"start": v(32.48, 114.06) * mm, "end": v(32.47, 114.2) * mm});
            skLineSegment(sketch, "E1513", {"start": v(32.47, 114.2) * mm, "end": v(32.46, 114.32) * mm});
            skLineSegment(sketch, "E1514", {"start": v(32.46, 114.32) * mm, "end": v(32.45, 114.45) * mm});
            skLineSegment(sketch, "E1515", {"start": v(32.45, 114.45) * mm, "end": v(32.44, 114.58) * mm});
            skLineSegment(sketch, "E1516", {"start": v(32.44, 114.58) * mm, "end": v(32.43, 114.71) * mm});
            skLineSegment(sketch, "E1517", {"start": v(32.43, 114.71) * mm, "end": v(32.41, 114.98) * mm});
            skLineSegment(sketch, "E1518", {"start": v(32.41, 114.98) * mm, "end": v(32.4, 115.12) * mm});
            skLineSegment(sketch, "E1519", {"start": v(32.4, 115.12) * mm, "end": v(32.39, 115.25) * mm});
            skLineSegment(sketch, "E1520", {"start": v(32.39, 115.25) * mm, "end": v(32.37, 115.4) * mm});
            skLineSegment(sketch, "E1521", {"start": v(32.37, 115.4) * mm, "end": v(32.36, 115.53) * mm});
            skLineSegment(sketch, "E1522", {"start": v(32.36, 115.53) * mm, "end": v(32.33, 115.81) * mm});
            skLineSegment(sketch, "E1523", {"start": v(32.33, 115.81) * mm, "end": v(32.32, 115.95) * mm});
            skLineSegment(sketch, "E1524", {"start": v(32.32, 115.95) * mm, "end": v(32.3, 116.1) * mm});
            skLineSegment(sketch, "E1525", {"start": v(32.3, 116.1) * mm, "end": v(32.29, 116.24) * mm});
            skLineSegment(sketch, "E1526", {"start": v(32.29, 116.24) * mm, "end": v(32.25, 116.53) * mm});
            skLineSegment(sketch, "E1527", {"start": v(32.25, 116.53) * mm, "end": v(32.24, 116.68) * mm});
            skLineSegment(sketch, "E1528", {"start": v(32.24, 116.68) * mm, "end": v(32.22, 116.83) * mm});
            skLineSegment(sketch, "E1529", {"start": v(32.22, 116.83) * mm, "end": v(32.18, 116.92) * mm});
            skLineSegment(sketch, "E1530", {"start": v(32.18, 116.92) * mm, "end": v(30.58, 117.35) * mm});
            skLineSegment(sketch, "E1531", {"start": v(30.58, 117.35) * mm, "end": v(30.5, 117.29) * mm});
            skLineSegment(sketch, "E1532", {"start": v(30.5, 117.29) * mm, "end": v(30.41, 117.17) * mm});
            skLineSegment(sketch, "E1533", {"start": v(30.41, 117.17) * mm, "end": v(30.32, 117.05) * mm});
            skLineSegment(sketch, "E1534", {"start": v(30.32, 117.05) * mm, "end": v(30.23, 116.93) * mm});
            skLineSegment(sketch, "E1535", {"start": v(30.23, 116.93) * mm, "end": v(30.15, 116.81) * mm});
            skLineSegment(sketch, "E1536", {"start": v(30.15, 116.81) * mm, "end": v(30.06, 116.7) * mm});
            skLineSegment(sketch, "E1537", {"start": v(30.06, 116.7) * mm, "end": v(29.98, 116.58) * mm});
            skLineSegment(sketch, "E1538", {"start": v(29.98, 116.58) * mm, "end": v(29.9, 116.47) * mm});
            skLineSegment(sketch, "E1539", {"start": v(29.9, 116.47) * mm, "end": v(29.8, 116.35) * mm});
            skLineSegment(sketch, "E1540", {"start": v(29.8, 116.35) * mm, "end": v(29.73, 116.23) * mm});
            skLineSegment(sketch, "E1541", {"start": v(29.73, 116.23) * mm, "end": v(29.65, 116.12) * mm});
            skLineSegment(sketch, "E1542", {"start": v(29.65, 116.12) * mm, "end": v(29.57, 116) * mm});
            skLineSegment(sketch, "E1543", {"start": v(29.57, 116) * mm, "end": v(29.49, 115.9) * mm});
            skLineSegment(sketch, "E1544", {"start": v(29.49, 115.9) * mm, "end": v(29.33, 115.67) * mm});
            skLineSegment(sketch, "E1545", {"start": v(29.33, 115.67) * mm, "end": v(29.26, 115.56) * mm});
            skLineSegment(sketch, "E1546", {"start": v(29.26, 115.56) * mm, "end": v(29.1, 115.35) * mm});
            skLineSegment(sketch, "E1547", {"start": v(29.1, 115.35) * mm, "end": v(28.96, 115.13) * mm});
            skLineSegment(sketch, "E1548", {"start": v(28.96, 115.13) * mm, "end": v(28.82, 114.92) * mm});
            skLineSegment(sketch, "E1549", {"start": v(28.82, 114.92) * mm, "end": v(28.76, 114.81) * mm});
            skLineSegment(sketch, "E1550", {"start": v(28.76, 114.81) * mm, "end": v(28.69, 114.7) * mm});
            skLineSegment(sketch, "E1551", {"start": v(28.69, 114.7) * mm, "end": v(28.62, 114.6) * mm});
            skLineSegment(sketch, "E1552", {"start": v(28.62, 114.6) * mm, "end": v(28.56, 114.5) * mm});
            skLineSegment(sketch, "E1553", {"start": v(28.56, 114.5) * mm, "end": v(28.5, 114.4) * mm});
            skLineSegment(sketch, "E1554", {"start": v(28.5, 114.4) * mm, "end": v(28.36, 114.2) * mm});
            skLineSegment(sketch, "E1555", {"start": v(28.36, 114.2) * mm, "end": v(28.3, 114.1) * mm});
            skLineSegment(sketch, "E1556", {"start": v(28.3, 114.1) * mm, "end": v(28.24, 114) * mm});
            skLineSegment(sketch, "E1557", {"start": v(28.24, 114) * mm, "end": v(28.18, 113.9) * mm});
            skLineSegment(sketch, "E1558", {"start": v(28.18, 113.9) * mm, "end": v(28.12, 113.8) * mm});
            skLineSegment(sketch, "E1559", {"start": v(28.12, 113.8) * mm, "end": v(28.06, 113.71) * mm});
            skLineSegment(sketch, "E1560", {"start": v(28.06, 113.71) * mm, "end": v(28, 113.62) * mm});
            skLineSegment(sketch, "E1561", {"start": v(28, 113.62) * mm, "end": v(27.95, 113.52) * mm});
            skLineSegment(sketch, "E1562", {"start": v(27.95, 113.52) * mm, "end": v(27.9, 113.43) * mm});
            skLineSegment(sketch, "E1563", {"start": v(27.9, 113.43) * mm, "end": v(27.84, 113.33) * mm});
            skLineSegment(sketch, "E1564", {"start": v(27.84, 113.33) * mm, "end": v(26.87, 113.39) * mm});
            skLineSegment(sketch, "E1565", {"start": v(26.87, 113.39) * mm, "end": v(25.97, 113.78) * mm});
            skLineSegment(sketch, "E1566", {"start": v(25.97, 113.78) * mm, "end": v(25.97, 113.88) * mm});
            skLineSegment(sketch, "E1567", {"start": v(25.97, 113.88) * mm, "end": v(25.96, 114) * mm});
            skLineSegment(sketch, "E1568", {"start": v(25.96, 114) * mm, "end": v(25.95, 114.1) * mm});
            skLineSegment(sketch, "E1569", {"start": v(25.95, 114.1) * mm, "end": v(25.94, 114.21) * mm});
            skLineSegment(sketch, "E1570", {"start": v(25.94, 114.21) * mm, "end": v(25.93, 114.33) * mm});
            skLineSegment(sketch, "E1571", {"start": v(25.93, 114.33) * mm, "end": v(25.92, 114.44) * mm});
            skLineSegment(sketch, "E1572", {"start": v(25.92, 114.44) * mm, "end": v(25.91, 114.55) * mm});
            skLineSegment(sketch, "E1573", {"start": v(25.91, 114.55) * mm, "end": v(25.9, 114.67) * mm});
            skLineSegment(sketch, "E1574", {"start": v(25.9, 114.67) * mm, "end": v(25.88, 114.9) * mm});
            skLineSegment(sketch, "E1575", {"start": v(25.88, 114.9) * mm, "end": v(25.87, 115.02) * mm});
            skLineSegment(sketch, "E1576", {"start": v(25.87, 115.02) * mm, "end": v(25.86, 115.14) * mm});
            skLineSegment(sketch, "E1577", {"start": v(25.86, 115.14) * mm, "end": v(25.85, 115.26) * mm});
            skLineSegment(sketch, "E1578", {"start": v(25.85, 115.26) * mm, "end": v(25.83, 115.39) * mm});
            skLineSegment(sketch, "E1579", {"start": v(25.83, 115.39) * mm, "end": v(25.82, 115.51) * mm});
            skLineSegment(sketch, "E1580", {"start": v(25.82, 115.51) * mm, "end": v(25.8, 115.63) * mm});
            skLineSegment(sketch, "E1581", {"start": v(25.8, 115.63) * mm, "end": v(25.79, 115.76) * mm});
            skLineSegment(sketch, "E1582", {"start": v(25.79, 115.76) * mm, "end": v(25.77, 115.89) * mm});
            skLineSegment(sketch, "E1583", {"start": v(25.77, 115.89) * mm, "end": v(25.74, 116.14) * mm});
            skLineSegment(sketch, "E1584", {"start": v(25.74, 116.14) * mm, "end": v(25.73, 116.27) * mm});
            skLineSegment(sketch, "E1585", {"start": v(25.73, 116.27) * mm, "end": v(25.7, 116.4) * mm});
            skLineSegment(sketch, "E1586", {"start": v(25.7, 116.4) * mm, "end": v(25.69, 116.54) * mm});
            skLineSegment(sketch, "E1587", {"start": v(25.69, 116.54) * mm, "end": v(25.65, 116.8) * mm});
            skLineSegment(sketch, "E1588", {"start": v(25.65, 116.8) * mm, "end": v(25.6, 117.08) * mm});
            skLineSegment(sketch, "E1589", {"start": v(25.6, 117.08) * mm, "end": v(25.59, 117.22) * mm});
            skLineSegment(sketch, "E1590", {"start": v(25.59, 117.22) * mm, "end": v(25.54, 117.5) * mm});
            skLineSegment(sketch, "E1591", {"start": v(25.54, 117.5) * mm, "end": v(25.5, 117.78) * mm});
            skLineSegment(sketch, "E1592", {"start": v(25.5, 117.78) * mm, "end": v(25.45, 118.06) * mm});
            skLineSegment(sketch, "E1593", {"start": v(25.45, 118.06) * mm, "end": v(25.4, 118.36) * mm});
            skLineSegment(sketch, "E1594", {"start": v(25.4, 118.36) * mm, "end": v(25.37, 118.5) * mm});
            skLineSegment(sketch, "E1595", {"start": v(25.37, 118.5) * mm, "end": v(25.33, 118.6) * mm});
            skLineSegment(sketch, "E1596", {"start": v(25.33, 118.6) * mm, "end": v(23.7, 118.93) * mm});
            skLineSegment(sketch, "E1597", {"start": v(23.7, 118.93) * mm, "end": v(23.63, 118.86) * mm});
            skLineSegment(sketch, "E1598", {"start": v(23.63, 118.86) * mm, "end": v(23.55, 118.74) * mm});
            skLineSegment(sketch, "E1599", {"start": v(23.55, 118.74) * mm, "end": v(23.47, 118.61) * mm});
            skLineSegment(sketch, "E1600", {"start": v(23.47, 118.61) * mm, "end": v(23.3, 118.37) * mm});
            skLineSegment(sketch, "E1601", {"start": v(23.3, 118.37) * mm, "end": v(23.22, 118.25) * mm});
            skLineSegment(sketch, "E1602", {"start": v(23.22, 118.25) * mm, "end": v(23.15, 118.13) * mm});
            skLineSegment(sketch, "E1603", {"start": v(23.15, 118.13) * mm, "end": v(23.07, 118) * mm});
            skLineSegment(sketch, "E1604", {"start": v(23.07, 118) * mm, "end": v(23, 117.89) * mm});
            skLineSegment(sketch, "E1605", {"start": v(23, 117.89) * mm, "end": v(22.84, 117.65) * mm});
            skLineSegment(sketch, "E1606", {"start": v(22.84, 117.65) * mm, "end": v(22.77, 117.53) * mm});
            skLineSegment(sketch, "E1607", {"start": v(22.77, 117.53) * mm, "end": v(22.7, 117.42) * mm});
            skLineSegment(sketch, "E1608", {"start": v(22.7, 117.42) * mm, "end": v(22.63, 117.3) * mm});
            skLineSegment(sketch, "E1609", {"start": v(22.63, 117.3) * mm, "end": v(22.56, 117.18) * mm});
            skLineSegment(sketch, "E1610", {"start": v(22.56, 117.18) * mm, "end": v(22.49, 117.07) * mm});
            skLineSegment(sketch, "E1611", {"start": v(22.49, 117.07) * mm, "end": v(22.35, 116.84) * mm});
            skLineSegment(sketch, "E1612", {"start": v(22.35, 116.84) * mm, "end": v(22.22, 116.62) * mm});
            skLineSegment(sketch, "E1613", {"start": v(22.22, 116.62) * mm, "end": v(22.1, 116.4) * mm});
            skLineSegment(sketch, "E1614", {"start": v(22.1, 116.4) * mm, "end": v(22.03, 116.3) * mm});
            skLineSegment(sketch, "E1615", {"start": v(22.03, 116.3) * mm, "end": v(21.9, 116.08) * mm});
            skLineSegment(sketch, "E1616", {"start": v(21.9, 116.08) * mm, "end": v(21.85, 115.97) * mm});
            skLineSegment(sketch, "E1617", {"start": v(21.85, 115.97) * mm, "end": v(21.73, 115.76) * mm});
            skLineSegment(sketch, "E1618", {"start": v(21.73, 115.76) * mm, "end": v(21.68, 115.66) * mm});
            skLineSegment(sketch, "E1619", {"start": v(21.68, 115.66) * mm, "end": v(21.62, 115.55) * mm});
            skLineSegment(sketch, "E1620", {"start": v(21.62, 115.55) * mm, "end": v(21.51, 115.35) * mm});
            skLineSegment(sketch, "E1621", {"start": v(21.51, 115.35) * mm, "end": v(21.46, 115.25) * mm});
            skLineSegment(sketch, "E1622", {"start": v(21.46, 115.25) * mm, "end": v(21.35, 115.05) * mm});
            skLineSegment(sketch, "E1623", {"start": v(21.35, 115.05) * mm, "end": v(21.3, 114.95) * mm});
            skLineSegment(sketch, "E1624", {"start": v(21.3, 114.95) * mm, "end": v(21.2, 114.76) * mm});
            skLineSegment(sketch, "E1625", {"start": v(21.2, 114.76) * mm, "end": v(20.23, 114.76) * mm});
            skLineSegment(sketch, "E1626", {"start": v(20.23, 114.76) * mm, "end": v(19.31, 115.1) * mm});
            skLineSegment(sketch, "E1627", {"start": v(19.31, 115.1) * mm, "end": v(19.3, 115.2) * mm});
            skLineSegment(sketch, "E1628", {"start": v(19.3, 115.2) * mm, "end": v(19.29, 115.3) * mm});
            skLineSegment(sketch, "E1629", {"start": v(19.29, 115.3) * mm, "end": v(19.26, 115.53) * mm});
            skLineSegment(sketch, "E1630", {"start": v(19.26, 115.53) * mm, "end": v(19.23, 115.75) * mm});
            skLineSegment(sketch, "E1631", {"start": v(19.23, 115.75) * mm, "end": v(19.2, 115.98) * mm});
            skLineSegment(sketch, "E1632", {"start": v(19.2, 115.98) * mm, "end": v(19.18, 116.1) * mm});
            skLineSegment(sketch, "E1633", {"start": v(19.18, 116.1) * mm, "end": v(19.16, 116.21) * mm});
            skLineSegment(sketch, "E1634", {"start": v(19.16, 116.21) * mm, "end": v(19.14, 116.33) * mm});
            skLineSegment(sketch, "E1635", {"start": v(19.14, 116.33) * mm, "end": v(19.12, 116.45) * mm});
            skLineSegment(sketch, "E1636", {"start": v(19.12, 116.45) * mm, "end": v(19.08, 116.7) * mm});
            skLineSegment(sketch, "E1637", {"start": v(19.08, 116.7) * mm, "end": v(19.04, 116.94) * mm});
            skLineSegment(sketch, "E1638", {"start": v(19.04, 116.94) * mm, "end": v(19.02, 117.06) * mm});
            skLineSegment(sketch, "E1639", {"start": v(19.02, 117.06) * mm, "end": v(19, 117.19) * mm});
            skLineSegment(sketch, "E1640", {"start": v(19, 117.19) * mm, "end": v(18.97, 117.32) * mm});
            skLineSegment(sketch, "E1641", {"start": v(18.97, 117.32) * mm, "end": v(18.95, 117.44) * mm});
            skLineSegment(sketch, "E1642", {"start": v(18.95, 117.44) * mm, "end": v(18.92, 117.57) * mm});
            skLineSegment(sketch, "E1643", {"start": v(18.92, 117.57) * mm, "end": v(18.9, 117.7) * mm});
            skLineSegment(sketch, "E1644", {"start": v(18.9, 117.7) * mm, "end": v(18.87, 117.83) * mm});
            skLineSegment(sketch, "E1645", {"start": v(18.87, 117.83) * mm, "end": v(18.84, 117.97) * mm});
            skLineSegment(sketch, "E1646", {"start": v(18.84, 117.97) * mm, "end": v(18.82, 118.1) * mm});
            skLineSegment(sketch, "E1647", {"start": v(18.82, 118.1) * mm, "end": v(18.79, 118.23) * mm});
            skLineSegment(sketch, "E1648", {"start": v(18.79, 118.23) * mm, "end": v(18.76, 118.37) * mm});
            skLineSegment(sketch, "E1649", {"start": v(18.76, 118.37) * mm, "end": v(18.73, 118.5) * mm});
            skLineSegment(sketch, "E1650", {"start": v(18.73, 118.5) * mm, "end": v(18.7, 118.64) * mm});
            skLineSegment(sketch, "E1651", {"start": v(18.7, 118.64) * mm, "end": v(18.67, 118.78) * mm});
            skLineSegment(sketch, "E1652", {"start": v(18.67, 118.78) * mm, "end": v(18.64, 118.92) * mm});
            skLineSegment(sketch, "E1653", {"start": v(18.64, 118.92) * mm, "end": v(18.6, 119.06) * mm});
            skLineSegment(sketch, "E1654", {"start": v(18.6, 119.06) * mm, "end": v(18.54, 119.35) * mm});
            skLineSegment(sketch, "E1655", {"start": v(18.54, 119.35) * mm, "end": v(18.5, 119.49) * mm});
            skLineSegment(sketch, "E1656", {"start": v(18.5, 119.49) * mm, "end": v(18.47, 119.63) * mm});
            skLineSegment(sketch, "E1657", {"start": v(18.47, 119.63) * mm, "end": v(18.44, 119.78) * mm});
            skLineSegment(sketch, "E1658", {"start": v(18.44, 119.78) * mm, "end": v(18.39, 119.86) * mm});
            skLineSegment(sketch, "E1659", {"start": v(18.39, 119.86) * mm, "end": v(16.75, 120.1) * mm});
            skLineSegment(sketch, "E1660", {"start": v(16.75, 120.1) * mm, "end": v(16.68, 120.04) * mm});
            skLineSegment(sketch, "E1661", {"start": v(16.68, 120.04) * mm, "end": v(16.6, 119.9) * mm});
            skLineSegment(sketch, "E1662", {"start": v(16.6, 119.9) * mm, "end": v(16.45, 119.65) * mm});
            skLineSegment(sketch, "E1663", {"start": v(16.45, 119.65) * mm, "end": v(16.38, 119.52) * mm});
            skLineSegment(sketch, "E1664", {"start": v(16.38, 119.52) * mm, "end": v(16.3, 119.4) * mm});
            skLineSegment(sketch, "E1665", {"start": v(16.3, 119.4) * mm, "end": v(16.24, 119.27) * mm});
            skLineSegment(sketch, "E1666", {"start": v(16.24, 119.27) * mm, "end": v(16.17, 119.15) * mm});
            skLineSegment(sketch, "E1667", {"start": v(16.17, 119.15) * mm, "end": v(16.03, 118.9) * mm});
            skLineSegment(sketch, "E1668", {"start": v(16.03, 118.9) * mm, "end": v(15.9, 118.66) * mm});
            skLineSegment(sketch, "E1669", {"start": v(15.9, 118.66) * mm, "end": v(15.83, 118.54) * mm});
            skLineSegment(sketch, "E1670", {"start": v(15.83, 118.54) * mm, "end": v(15.77, 118.42) * mm});
            skLineSegment(sketch, "E1671", {"start": v(15.77, 118.42) * mm, "end": v(15.7, 118.3) * mm});
            skLineSegment(sketch, "E1672", {"start": v(15.7, 118.3) * mm, "end": v(15.64, 118.18) * mm});
            skLineSegment(sketch, "E1673", {"start": v(15.64, 118.18) * mm, "end": v(15.58, 118.06) * mm});
            skLineSegment(sketch, "E1674", {"start": v(15.58, 118.06) * mm, "end": v(15.52, 117.94) * mm});
            skLineSegment(sketch, "E1675", {"start": v(15.52, 117.94) * mm, "end": v(15.46, 117.83) * mm});
            skLineSegment(sketch, "E1676", {"start": v(15.46, 117.83) * mm, "end": v(15.4, 117.71) * mm});
            skLineSegment(sketch, "E1677", {"start": v(15.4, 117.71) * mm, "end": v(15.34, 117.6) * mm});
            skLineSegment(sketch, "E1678", {"start": v(15.34, 117.6) * mm, "end": v(15.29, 117.49) * mm});
            skLineSegment(sketch, "E1679", {"start": v(15.29, 117.49) * mm, "end": v(15.23, 117.38) * mm});
            skLineSegment(sketch, "E1680", {"start": v(15.23, 117.38) * mm, "end": v(15.18, 117.26) * mm});
            skLineSegment(sketch, "E1681", {"start": v(15.18, 117.26) * mm, "end": v(15.12, 117.15) * mm});
            skLineSegment(sketch, "E1682", {"start": v(15.12, 117.15) * mm, "end": v(15.07, 117.05) * mm});
            skLineSegment(sketch, "E1683", {"start": v(15.07, 117.05) * mm, "end": v(15.02, 116.94) * mm});
            skLineSegment(sketch, "E1684", {"start": v(15.02, 116.94) * mm, "end": v(14.91, 116.72) * mm});
            skLineSegment(sketch, "E1685", {"start": v(14.91, 116.72) * mm, "end": v(14.87, 116.62) * mm});
            skLineSegment(sketch, "E1686", {"start": v(14.87, 116.62) * mm, "end": v(14.82, 116.51) * mm});
            skLineSegment(sketch, "E1687", {"start": v(14.82, 116.51) * mm, "end": v(14.77, 116.4) * mm});
            skLineSegment(sketch, "E1688", {"start": v(14.77, 116.4) * mm, "end": v(14.72, 116.3) * mm});
            skLineSegment(sketch, "E1689", {"start": v(14.72, 116.3) * mm, "end": v(14.67, 116.2) * mm});
            skLineSegment(sketch, "E1690", {"start": v(14.67, 116.2) * mm, "end": v(14.63, 116.1) * mm});
            skLineSegment(sketch, "E1691", {"start": v(14.63, 116.1) * mm, "end": v(14.58, 116) * mm});
            skLineSegment(sketch, "E1692", {"start": v(14.58, 116) * mm, "end": v(14.5, 115.8) * mm});
            skLineSegment(sketch, "E1693", {"start": v(14.5, 115.8) * mm, "end": v(13.52, 115.74) * mm});
            skLineSegment(sketch, "E1694", {"start": v(13.52, 115.74) * mm, "end": v(12.59, 116.02) * mm});
            skLineSegment(sketch, "E1695", {"start": v(12.59, 116.02) * mm, "end": v(12.55, 116.23) * mm});
            skLineSegment(sketch, "E1696", {"start": v(12.55, 116.23) * mm, "end": v(12.53, 116.34) * mm});
            skLineSegment(sketch, "E1697", {"start": v(12.53, 116.34) * mm, "end": v(12.5, 116.45) * mm});
            skLineSegment(sketch, "E1698", {"start": v(12.5, 116.45) * mm, "end": v(12.49, 116.56) * mm});
            skLineSegment(sketch, "E1699", {"start": v(12.49, 116.56) * mm, "end": v(12.46, 116.67) * mm});
            skLineSegment(sketch, "E1700", {"start": v(12.46, 116.67) * mm, "end": v(12.44, 116.79) * mm});
            skLineSegment(sketch, "E1701", {"start": v(12.44, 116.79) * mm, "end": v(12.42, 116.9) * mm});
            skLineSegment(sketch, "E1702", {"start": v(12.42, 116.9) * mm, "end": v(12.4, 117.02) * mm});
            skLineSegment(sketch, "E1703", {"start": v(12.4, 117.02) * mm, "end": v(12.37, 117.13) * mm});
            skLineSegment(sketch, "E1704", {"start": v(12.37, 117.13) * mm, "end": v(12.32, 117.37) * mm});
            skLineSegment(sketch, "E1705", {"start": v(12.32, 117.37) * mm, "end": v(12.29, 117.48) * mm});
            skLineSegment(sketch, "E1706", {"start": v(12.29, 117.48) * mm, "end": v(12.26, 117.6) * mm});
            skLineSegment(sketch, "E1707", {"start": v(12.26, 117.6) * mm, "end": v(12.23, 117.73) * mm});
            skLineSegment(sketch, "E1708", {"start": v(12.23, 117.73) * mm, "end": v(12.18, 117.97) * mm});
            skLineSegment(sketch, "E1709", {"start": v(12.18, 117.97) * mm, "end": v(12.15, 118.1) * mm});
            skLineSegment(sketch, "E1710", {"start": v(12.15, 118.1) * mm, "end": v(12.12, 118.22) * mm});
            skLineSegment(sketch, "E1711", {"start": v(12.12, 118.22) * mm, "end": v(12.05, 118.47) * mm});
            skLineSegment(sketch, "E1712", {"start": v(12.05, 118.47) * mm, "end": v(12.02, 118.6) * mm});
            skLineSegment(sketch, "E1713", {"start": v(12.02, 118.6) * mm, "end": v(11.99, 118.73) * mm});
            skLineSegment(sketch, "E1714", {"start": v(11.99, 118.73) * mm, "end": v(11.92, 119) * mm});
            skLineSegment(sketch, "E1715", {"start": v(11.92, 119) * mm, "end": v(11.88, 119.13) * mm});
            skLineSegment(sketch, "E1716", {"start": v(11.88, 119.13) * mm, "end": v(11.85, 119.26) * mm});
            skLineSegment(sketch, "E1717", {"start": v(11.85, 119.26) * mm, "end": v(11.8, 119.4) * mm});
            skLineSegment(sketch, "E1718", {"start": v(11.8, 119.4) * mm, "end": v(11.77, 119.53) * mm});
            skLineSegment(sketch, "E1719", {"start": v(11.77, 119.53) * mm, "end": v(11.73, 119.67) * mm});
            skLineSegment(sketch, "E1720", {"start": v(11.73, 119.67) * mm, "end": v(11.7, 119.8) * mm});
            skLineSegment(sketch, "E1721", {"start": v(11.7, 119.8) * mm, "end": v(11.65, 119.94) * mm});
            skLineSegment(sketch, "E1722", {"start": v(11.65, 119.94) * mm, "end": v(11.61, 120.08) * mm});
            skLineSegment(sketch, "E1723", {"start": v(11.61, 120.08) * mm, "end": v(11.57, 120.22) * mm});
            skLineSegment(sketch, "E1724", {"start": v(11.57, 120.22) * mm, "end": v(11.53, 120.36) * mm});
            skLineSegment(sketch, "E1725", {"start": v(11.53, 120.36) * mm, "end": v(11.48, 120.5) * mm});
            skLineSegment(sketch, "E1726", {"start": v(11.48, 120.5) * mm, "end": v(11.44, 120.65) * mm});
            skLineSegment(sketch, "E1727", {"start": v(11.44, 120.65) * mm, "end": v(11.39, 120.73) * mm});
            skLineSegment(sketch, "E1728", {"start": v(11.39, 120.73) * mm, "end": v(9.74, 120.88) * mm});
            skLineSegment(sketch, "E1729", {"start": v(9.74, 120.88) * mm, "end": v(9.67, 120.8) * mm});
            skLineSegment(sketch, "E1730", {"start": v(9.67, 120.8) * mm, "end": v(9.6, 120.67) * mm});
            skLineSegment(sketch, "E1731", {"start": v(9.6, 120.67) * mm, "end": v(9.54, 120.54) * mm});
            skLineSegment(sketch, "E1732", {"start": v(9.54, 120.54) * mm, "end": v(9.47, 120.4) * mm});
            skLineSegment(sketch, "E1733", {"start": v(9.47, 120.4) * mm, "end": v(9.4, 120.27) * mm});
            skLineSegment(sketch, "E1734", {"start": v(9.4, 120.27) * mm, "end": v(9.34, 120.14) * mm});
            skLineSegment(sketch, "E1735", {"start": v(9.34, 120.14) * mm, "end": v(9.28, 120.01) * mm});
            skLineSegment(sketch, "E1736", {"start": v(9.28, 120.01) * mm, "end": v(9.15, 119.76) * mm});
            skLineSegment(sketch, "E1737", {"start": v(9.15, 119.76) * mm, "end": v(9.1, 119.63) * mm});
            skLineSegment(sketch, "E1738", {"start": v(9.1, 119.63) * mm, "end": v(9.03, 119.5) * mm});
            skLineSegment(sketch, "E1739", {"start": v(9.03, 119.5) * mm, "end": v(8.97, 119.38) * mm});
            skLineSegment(sketch, "E1740", {"start": v(8.97, 119.38) * mm, "end": v(8.86, 119.13) * mm});
            skLineSegment(sketch, "E1741", {"start": v(8.86, 119.13) * mm, "end": v(8.8, 119.01) * mm});
            skLineSegment(sketch, "E1742", {"start": v(8.8, 119.01) * mm, "end": v(8.74, 118.89) * mm});
            skLineSegment(sketch, "E1743", {"start": v(8.74, 118.89) * mm, "end": v(8.58, 118.53) * mm});
            skLineSegment(sketch, "E1744", {"start": v(8.58, 118.53) * mm, "end": v(8.43, 118.18) * mm});
            skLineSegment(sketch, "E1745", {"start": v(8.43, 118.18) * mm, "end": v(8.38, 118.06) * mm});
            skLineSegment(sketch, "E1746", {"start": v(8.38, 118.06) * mm, "end": v(8.28, 117.83) * mm});
            skLineSegment(sketch, "E1747", {"start": v(8.28, 117.83) * mm, "end": v(8.24, 117.72) * mm});
            skLineSegment(sketch, "E1748", {"start": v(8.24, 117.72) * mm, "end": v(8.2, 117.61) * mm});
            skLineSegment(sketch, "E1749", {"start": v(8.2, 117.61) * mm, "end": v(8.15, 117.5) * mm});
            skLineSegment(sketch, "E1750", {"start": v(8.15, 117.5) * mm, "end": v(8.1, 117.4) * mm});
            skLineSegment(sketch, "E1751", {"start": v(8.1, 117.4) * mm, "end": v(8.06, 117.28) * mm});
            skLineSegment(sketch, "E1752", {"start": v(8.06, 117.28) * mm, "end": v(7.97, 117.07) * mm});
            skLineSegment(sketch, "E1753", {"start": v(7.97, 117.07) * mm, "end": v(7.93, 116.96) * mm});
            skLineSegment(sketch, "E1754", {"start": v(7.93, 116.96) * mm, "end": v(7.9, 116.86) * mm});
            skLineSegment(sketch, "E1755", {"start": v(7.9, 116.86) * mm, "end": v(7.81, 116.65) * mm});
            skLineSegment(sketch, "E1756", {"start": v(7.81, 116.65) * mm, "end": v(7.77, 116.55) * mm});
            skLineSegment(sketch, "E1757", {"start": v(7.77, 116.55) * mm, "end": v(7.74, 116.45) * mm});
            skLineSegment(sketch, "E1758", {"start": v(7.74, 116.45) * mm, "end": v(6.77, 116.33) * mm});
            skLineSegment(sketch, "E1759", {"start": v(6.77, 116.33) * mm, "end": v(5.82, 116.56) * mm});
            skLineSegment(sketch, "E1760", {"start": v(5.82, 116.56) * mm, "end": v(5.8, 116.66) * mm});
            skLineSegment(sketch, "E1761", {"start": v(5.8, 116.66) * mm, "end": v(5.77, 116.77) * mm});
            skLineSegment(sketch, "E1762", {"start": v(5.77, 116.77) * mm, "end": v(5.71, 116.98) * mm});
            skLineSegment(sketch, "E1763", {"start": v(5.71, 116.98) * mm, "end": v(5.69, 117.1) * mm});
            skLineSegment(sketch, "E1764", {"start": v(5.69, 117.1) * mm, "end": v(5.66, 117.2) * mm});
            skLineSegment(sketch, "E1765", {"start": v(5.66, 117.2) * mm, "end": v(5.63, 117.31) * mm});
            skLineSegment(sketch, "E1766", {"start": v(5.63, 117.31) * mm, "end": v(5.6, 117.43) * mm});
            skLineSegment(sketch, "E1767", {"start": v(5.6, 117.43) * mm, "end": v(5.57, 117.54) * mm});
            skLineSegment(sketch, "E1768", {"start": v(5.57, 117.54) * mm, "end": v(5.5, 117.77) * mm});
            skLineSegment(sketch, "E1769", {"start": v(5.5, 117.77) * mm, "end": v(5.44, 118) * mm});
            skLineSegment(sketch, "E1770", {"start": v(5.44, 118) * mm, "end": v(5.4, 118.12) * mm});
            skLineSegment(sketch, "E1771", {"start": v(5.4, 118.12) * mm, "end": v(5.37, 118.24) * mm});
            skLineSegment(sketch, "E1772", {"start": v(5.37, 118.24) * mm, "end": v(5.33, 118.36) * mm});
            skLineSegment(sketch, "E1773", {"start": v(5.33, 118.36) * mm, "end": v(5.3, 118.48) * mm});
            skLineSegment(sketch, "E1774", {"start": v(5.3, 118.48) * mm, "end": v(5.22, 118.72) * mm});
            skLineSegment(sketch, "E1775", {"start": v(5.22, 118.72) * mm, "end": v(5.18, 118.85) * mm});
            skLineSegment(sketch, "E1776", {"start": v(5.18, 118.85) * mm, "end": v(5.14, 118.97) * mm});
            skLineSegment(sketch, "E1777", {"start": v(5.14, 118.97) * mm, "end": v(5.1, 119.1) * mm});
            skLineSegment(sketch, "E1778", {"start": v(5.1, 119.1) * mm, "end": v(5.06, 119.23) * mm});
            skLineSegment(sketch, "E1779", {"start": v(5.06, 119.23) * mm, "end": v(5.02, 119.36) * mm});
            skLineSegment(sketch, "E1780", {"start": v(5.02, 119.36) * mm, "end": v(4.93, 119.61) * mm});
            skLineSegment(sketch, "E1781", {"start": v(4.93, 119.61) * mm, "end": v(4.9, 119.75) * mm});
            skLineSegment(sketch, "E1782", {"start": v(4.9, 119.75) * mm, "end": v(4.85, 119.88) * mm});
            skLineSegment(sketch, "E1783", {"start": v(4.85, 119.88) * mm, "end": v(4.75, 120.15) * mm});
            skLineSegment(sketch, "E1784", {"start": v(4.75, 120.15) * mm, "end": v(4.66, 120.42) * mm});
            skLineSegment(sketch, "E1785", {"start": v(4.66, 120.42) * mm, "end": v(4.6, 120.55) * mm});
            skLineSegment(sketch, "E1786", {"start": v(4.6, 120.55) * mm, "end": v(4.56, 120.7) * mm});
            skLineSegment(sketch, "E1787", {"start": v(4.56, 120.7) * mm, "end": v(4.5, 120.83) * mm});
            skLineSegment(sketch, "E1788", {"start": v(4.5, 120.83) * mm, "end": v(4.46, 120.97) * mm});
            skLineSegment(sketch, "E1789", {"start": v(4.46, 120.97) * mm, "end": v(4.4, 121.1) * mm});
            skLineSegment(sketch, "E1790", {"start": v(4.4, 121.1) * mm, "end": v(4.35, 121.19) * mm});
            skLineSegment(sketch, "E1791", {"start": v(4.35, 121.19) * mm, "end": v(2.7, 121.24) * mm});
            skLineSegment(sketch, "E1792", {"start": v(2.7, 121.24) * mm, "end": v(2.63, 121.16) * mm});
            skLineSegment(sketch, "E1793", {"start": v(2.63, 121.16) * mm, "end": v(2.57, 121.02) * mm});
            skLineSegment(sketch, "E1794", {"start": v(2.57, 121.02) * mm, "end": v(2.51, 120.89) * mm});
            skLineSegment(sketch, "E1795", {"start": v(2.51, 120.89) * mm, "end": v(2.4, 120.62) * mm});
            skLineSegment(sketch, "E1796", {"start": v(2.4, 120.62) * mm, "end": v(2.34, 120.48) * mm});
            skLineSegment(sketch, "E1797", {"start": v(2.34, 120.48) * mm, "end": v(2.28, 120.35) * mm});
            skLineSegment(sketch, "E1798", {"start": v(2.28, 120.35) * mm, "end": v(2.23, 120.22) * mm});
            skLineSegment(sketch, "E1799", {"start": v(2.23, 120.22) * mm, "end": v(2.17, 120.09) * mm});
            skLineSegment(sketch, "E1800", {"start": v(2.17, 120.09) * mm, "end": v(2.12, 119.96) * mm});
            skLineSegment(sketch, "E1801", {"start": v(2.12, 119.96) * mm, "end": v(2.07, 119.83) * mm});
            skLineSegment(sketch, "E1802", {"start": v(2.07, 119.83) * mm, "end": v(1.96, 119.57) * mm});
            skLineSegment(sketch, "E1803", {"start": v(1.96, 119.57) * mm, "end": v(1.87, 119.32) * mm});
            skLineSegment(sketch, "E1804", {"start": v(1.87, 119.32) * mm, "end": v(1.82, 119.2) * mm});
            skLineSegment(sketch, "E1805", {"start": v(1.82, 119.2) * mm, "end": v(1.77, 119.07) * mm});
            skLineSegment(sketch, "E1806", {"start": v(1.77, 119.07) * mm, "end": v(1.72, 118.95) * mm});
            skLineSegment(sketch, "E1807", {"start": v(1.72, 118.95) * mm, "end": v(1.63, 118.7) * mm});
            skLineSegment(sketch, "E1808", {"start": v(1.63, 118.7) * mm, "end": v(1.59, 118.59) * mm});
            skLineSegment(sketch, "E1809", {"start": v(1.59, 118.59) * mm, "end": v(1.54, 118.47) * mm});
            skLineSegment(sketch, "E1810", {"start": v(1.54, 118.47) * mm, "end": v(1.5, 118.35) * mm});
            skLineSegment(sketch, "E1811", {"start": v(1.5, 118.35) * mm, "end": v(1.46, 118.23) * mm});
            skLineSegment(sketch, "E1812", {"start": v(1.46, 118.23) * mm, "end": v(1.42, 118.12) * mm});
            skLineSegment(sketch, "E1813", {"start": v(1.42, 118.12) * mm, "end": v(1.34, 117.89) * mm});
            skLineSegment(sketch, "E1814", {"start": v(1.34, 117.89) * mm, "end": v(1.3, 117.78) * mm});
            skLineSegment(sketch, "E1815", {"start": v(1.3, 117.78) * mm, "end": v(1.26, 117.66) * mm});
            skLineSegment(sketch, "E1816", {"start": v(1.26, 117.66) * mm, "end": v(1.23, 117.55) * mm});
            skLineSegment(sketch, "E1817", {"start": v(1.23, 117.55) * mm, "end": v(1.19, 117.44) * mm});
            skLineSegment(sketch, "E1818", {"start": v(1.19, 117.44) * mm, "end": v(1.12, 117.22) * mm});
            skLineSegment(sketch, "E1819", {"start": v(1.12, 117.22) * mm, "end": v(1.08, 117.12) * mm});
            skLineSegment(sketch, "E1820", {"start": v(1.08, 117.12) * mm, "end": v(1.02, 116.9) * mm});
            skLineSegment(sketch, "E1821", {"start": v(1.02, 116.9) * mm, "end": v(0.98, 116.8) * mm});
            skLineSegment(sketch, "E1822", {"start": v(0.98, 116.8) * mm, "end": v(0.95, 116.7) * mm});
            skLineSegment(sketch, "E1823", {"start": v(0.95, 116.7) * mm, "end": v(0, 116.53) * mm});
            skLineSegment(sketch, "E1824", {"start": v(0, 116.53) * mm, "end": v(-0.97, 116.7) * mm});
            skLineSegment(sketch, "E1825", {"start": v(-0.97, 116.7) * mm, "end": v(-1.03, 116.9) * mm});
            skLineSegment(sketch, "E1826", {"start": v(-1.03, 116.9) * mm, "end": v(-1.06, 117.01) * mm});
            skLineSegment(sketch, "E1827", {"start": v(-1.06, 117.01) * mm, "end": v(-1.13, 117.22) * mm});
            skLineSegment(sketch, "E1828", {"start": v(-1.13, 117.22) * mm, "end": v(-1.17, 117.33) * mm});
            skLineSegment(sketch, "E1829", {"start": v(-1.17, 117.33) * mm, "end": v(-1.2, 117.44) * mm});
            skLineSegment(sketch, "E1830", {"start": v(-1.2, 117.44) * mm, "end": v(-1.24, 117.55) * mm});
            skLineSegment(sketch, "E1831", {"start": v(-1.24, 117.55) * mm, "end": v(-1.28, 117.66) * mm});
            skLineSegment(sketch, "E1832", {"start": v(-1.28, 117.66) * mm, "end": v(-1.31, 117.78) * mm});
            skLineSegment(sketch, "E1833", {"start": v(-1.31, 117.78) * mm, "end": v(-1.35, 117.89) * mm});
            skLineSegment(sketch, "E1834", {"start": v(-1.35, 117.89) * mm, "end": v(-1.4, 118) * mm});
            skLineSegment(sketch, "E1835", {"start": v(-1.4, 118) * mm, "end": v(-1.43, 118.12) * mm});
            skLineSegment(sketch, "E1836", {"start": v(-1.43, 118.12) * mm, "end": v(-1.47, 118.23) * mm});
            skLineSegment(sketch, "E1837", {"start": v(-1.47, 118.23) * mm, "end": v(-1.52, 118.35) * mm});
            skLineSegment(sketch, "E1838", {"start": v(-1.52, 118.35) * mm, "end": v(-1.6, 118.59) * mm});
            skLineSegment(sketch, "E1839", {"start": v(-1.6, 118.59) * mm, "end": v(-1.65, 118.7) * mm});
            skLineSegment(sketch, "E1840", {"start": v(-1.65, 118.7) * mm, "end": v(-1.74, 118.95) * mm});
            skLineSegment(sketch, "E1841", {"start": v(-1.74, 118.95) * mm, "end": v(-1.78, 119.07) * mm});
            skLineSegment(sketch, "E1842", {"start": v(-1.78, 119.07) * mm, "end": v(-1.88, 119.32) * mm});
            skLineSegment(sketch, "E1843", {"start": v(-1.88, 119.32) * mm, "end": v(-1.93, 119.45) * mm});
            skLineSegment(sketch, "E1844", {"start": v(-1.93, 119.45) * mm, "end": v(-1.98, 119.57) * mm});
            skLineSegment(sketch, "E1845", {"start": v(-1.98, 119.57) * mm, "end": v(-2.03, 119.7) * mm});
            skLineSegment(sketch, "E1846", {"start": v(-2.03, 119.7) * mm, "end": v(-2.13, 119.96) * mm});
            skLineSegment(sketch, "E1847", {"start": v(-2.13, 119.96) * mm, "end": v(-2.19, 120.09) * mm});
            skLineSegment(sketch, "E1848", {"start": v(-2.19, 120.09) * mm, "end": v(-2.24, 120.22) * mm});
            skLineSegment(sketch, "E1849", {"start": v(-2.24, 120.22) * mm, "end": v(-2.35, 120.48) * mm});
            skLineSegment(sketch, "E1850", {"start": v(-2.35, 120.48) * mm, "end": v(-2.4, 120.62) * mm});
            skLineSegment(sketch, "E1851", {"start": v(-2.4, 120.62) * mm, "end": v(-2.47, 120.75) * mm});
            skLineSegment(sketch, "E1852", {"start": v(-2.47, 120.75) * mm, "end": v(-2.52, 120.89) * mm});
            skLineSegment(sketch, "E1853", {"start": v(-2.52, 120.89) * mm, "end": v(-2.58, 121.02) * mm});
            skLineSegment(sketch, "E1854", {"start": v(-2.58, 121.02) * mm, "end": v(-2.64, 121.16) * mm});
            skLineSegment(sketch, "E1855", {"start": v(-2.64, 121.16) * mm, "end": v(-2.7, 121.24) * mm});
            skLineSegment(sketch, "E1856", {"start": v(-2.7, 121.24) * mm, "end": v(-4.36, 121.19) * mm});
            skLineSegment(sketch, "E1857", {"start": v(-4.36, 121.19) * mm, "end": v(-4.42, 121.1) * mm});
            skLineSegment(sketch, "E1858", {"start": v(-4.42, 121.1) * mm, "end": v(-4.47, 120.97) * mm});
            skLineSegment(sketch, "E1859", {"start": v(-4.47, 120.97) * mm, "end": v(-4.52, 120.83) * mm});
            skLineSegment(sketch, "E1860", {"start": v(-4.52, 120.83) * mm, "end": v(-4.57, 120.69) * mm});
            skLineSegment(sketch, "E1861", {"start": v(-4.57, 120.69) * mm, "end": v(-4.62, 120.55) * mm});
            skLineSegment(sketch, "E1862", {"start": v(-4.62, 120.55) * mm, "end": v(-4.72, 120.28) * mm});
            skLineSegment(sketch, "E1863", {"start": v(-4.72, 120.28) * mm, "end": v(-4.77, 120.15) * mm});
            skLineSegment(sketch, "E1864", {"start": v(-4.77, 120.15) * mm, "end": v(-4.81, 120.01) * mm});
            skLineSegment(sketch, "E1865", {"start": v(-4.81, 120.01) * mm, "end": v(-4.9, 119.75) * mm});
            skLineSegment(sketch, "E1866", {"start": v(-4.9, 119.75) * mm, "end": v(-4.95, 119.61) * mm});
            skLineSegment(sketch, "E1867", {"start": v(-4.95, 119.61) * mm, "end": v(-5, 119.48) * mm});
            skLineSegment(sketch, "E1868", {"start": v(-5, 119.48) * mm, "end": v(-5.03, 119.36) * mm});
            skLineSegment(sketch, "E1869", {"start": v(-5.03, 119.36) * mm, "end": v(-5.12, 119.1) * mm});
            skLineSegment(sketch, "E1870", {"start": v(-5.12, 119.1) * mm, "end": v(-5.16, 118.97) * mm});
            skLineSegment(sketch, "E1871", {"start": v(-5.16, 118.97) * mm, "end": v(-5.2, 118.85) * mm});
            skLineSegment(sketch, "E1872", {"start": v(-5.2, 118.85) * mm, "end": v(-5.27, 118.6) * mm});
            skLineSegment(sketch, "E1873", {"start": v(-5.27, 118.6) * mm, "end": v(-5.3, 118.48) * mm});
            skLineSegment(sketch, "E1874", {"start": v(-5.3, 118.48) * mm, "end": v(-5.35, 118.36) * mm});
            skLineSegment(sketch, "E1875", {"start": v(-5.35, 118.36) * mm, "end": v(-5.38, 118.24) * mm});
            skLineSegment(sketch, "E1876", {"start": v(-5.38, 118.24) * mm, "end": v(-5.42, 118.12) * mm});
            skLineSegment(sketch, "E1877", {"start": v(-5.42, 118.12) * mm, "end": v(-5.45, 118) * mm});
            skLineSegment(sketch, "E1878", {"start": v(-5.45, 118) * mm, "end": v(-5.48, 117.88) * mm});
            skLineSegment(sketch, "E1879", {"start": v(-5.48, 117.88) * mm, "end": v(-5.52, 117.77) * mm});
            skLineSegment(sketch, "E1880", {"start": v(-5.52, 117.77) * mm, "end": v(-5.55, 117.65) * mm});
            skLineSegment(sketch, "E1881", {"start": v(-5.55, 117.65) * mm, "end": v(-5.58, 117.54) * mm});
            skLineSegment(sketch, "E1882", {"start": v(-5.58, 117.54) * mm, "end": v(-5.61, 117.42) * mm});
            skLineSegment(sketch, "E1883", {"start": v(-5.61, 117.42) * mm, "end": v(-5.64, 117.31) * mm});
            skLineSegment(sketch, "E1884", {"start": v(-5.64, 117.31) * mm, "end": v(-5.7, 117.1) * mm});
            skLineSegment(sketch, "E1885", {"start": v(-5.7, 117.1) * mm, "end": v(-5.73, 116.98) * mm});
            skLineSegment(sketch, "E1886", {"start": v(-5.73, 116.98) * mm, "end": v(-5.76, 116.87) * mm});
            skLineSegment(sketch, "E1887", {"start": v(-5.76, 116.87) * mm, "end": v(-5.8, 116.66) * mm});
            skLineSegment(sketch, "E1888", {"start": v(-5.8, 116.66) * mm, "end": v(-5.83, 116.56) * mm});
            skLineSegment(sketch, "E1889", {"start": v(-5.83, 116.56) * mm, "end": v(-6.78, 116.33) * mm});
            skLineSegment(sketch, "E1890", {"start": v(-6.78, 116.33) * mm, "end": v(-7.75, 116.45) * mm});
            skLineSegment(sketch, "E1891", {"start": v(-7.75, 116.45) * mm, "end": v(-7.79, 116.55) * mm});
            skLineSegment(sketch, "E1892", {"start": v(-7.79, 116.55) * mm, "end": v(-7.83, 116.65) * mm});
            skLineSegment(sketch, "E1893", {"start": v(-7.83, 116.65) * mm, "end": v(-7.86, 116.75) * mm});
            skLineSegment(sketch, "E1894", {"start": v(-7.86, 116.75) * mm, "end": v(-7.9, 116.86) * mm});
            skLineSegment(sketch, "E1895", {"start": v(-7.9, 116.86) * mm, "end": v(-7.95, 116.96) * mm});
            skLineSegment(sketch, "E1896", {"start": v(-7.95, 116.96) * mm, "end": v(-8.03, 117.17) * mm});
            skLineSegment(sketch, "E1897", {"start": v(-8.03, 117.17) * mm, "end": v(-8.07, 117.28) * mm});
            skLineSegment(sketch, "E1898", {"start": v(-8.07, 117.28) * mm, "end": v(-8.12, 117.39) * mm});
            skLineSegment(sketch, "E1899", {"start": v(-8.12, 117.39) * mm, "end": v(-8.16, 117.5) * mm});
            skLineSegment(sketch, "E1900", {"start": v(-8.16, 117.5) * mm, "end": v(-8.2, 117.61) * mm});
            skLineSegment(sketch, "E1901", {"start": v(-8.2, 117.61) * mm, "end": v(-8.25, 117.72) * mm});
            skLineSegment(sketch, "E1902", {"start": v(-8.25, 117.72) * mm, "end": v(-8.35, 117.95) * mm});
            skLineSegment(sketch, "E1903", {"start": v(-8.35, 117.95) * mm, "end": v(-8.4, 118.06) * mm});
            skLineSegment(sketch, "E1904", {"start": v(-8.4, 118.06) * mm, "end": v(-8.5, 118.3) * mm});
            skLineSegment(sketch, "E1905", {"start": v(-8.5, 118.3) * mm, "end": v(-8.55, 118.41) * mm});
            skLineSegment(sketch, "E1906", {"start": v(-8.55, 118.41) * mm, "end": v(-8.65, 118.65) * mm});
            skLineSegment(sketch, "E1907", {"start": v(-8.65, 118.65) * mm, "end": v(-8.7, 118.77) * mm});
            skLineSegment(sketch, "E1908", {"start": v(-8.7, 118.77) * mm, "end": v(-8.76, 118.89) * mm});
            skLineSegment(sketch, "E1909", {"start": v(-8.76, 118.89) * mm, "end": v(-8.81, 119.01) * mm});
            skLineSegment(sketch, "E1910", {"start": v(-8.81, 119.01) * mm, "end": v(-8.87, 119.13) * mm});
            skLineSegment(sketch, "E1911", {"start": v(-8.87, 119.13) * mm, "end": v(-8.93, 119.26) * mm});
            skLineSegment(sketch, "E1912", {"start": v(-8.93, 119.26) * mm, "end": v(-8.98, 119.38) * mm});
            skLineSegment(sketch, "E1913", {"start": v(-8.98, 119.38) * mm, "end": v(-9.04, 119.5) * mm});
            skLineSegment(sketch, "E1914", {"start": v(-9.04, 119.5) * mm, "end": v(-9.1, 119.63) * mm});
            skLineSegment(sketch, "E1915", {"start": v(-9.1, 119.63) * mm, "end": v(-9.17, 119.76) * mm});
            skLineSegment(sketch, "E1916", {"start": v(-9.17, 119.76) * mm, "end": v(-9.23, 119.89) * mm});
            skLineSegment(sketch, "E1917", {"start": v(-9.23, 119.89) * mm, "end": v(-9.29, 120.01) * mm});
            skLineSegment(sketch, "E1918", {"start": v(-9.29, 120.01) * mm, "end": v(-9.35, 120.14) * mm});
            skLineSegment(sketch, "E1919", {"start": v(-9.35, 120.14) * mm, "end": v(-9.42, 120.27) * mm});
            skLineSegment(sketch, "E1920", {"start": v(-9.42, 120.27) * mm, "end": v(-9.48, 120.4) * mm});
            skLineSegment(sketch, "E1921", {"start": v(-9.48, 120.4) * mm, "end": v(-9.55, 120.54) * mm});
            skLineSegment(sketch, "E1922", {"start": v(-9.55, 120.54) * mm, "end": v(-9.62, 120.67) * mm});
            skLineSegment(sketch, "E1923", {"start": v(-9.62, 120.67) * mm, "end": v(-9.68, 120.8) * mm});
            skLineSegment(sketch, "E1924", {"start": v(-9.68, 120.8) * mm, "end": v(-9.75, 120.87) * mm});
            skLineSegment(sketch, "E1925", {"start": v(-9.75, 120.87) * mm, "end": v(-11.4, 120.73) * mm});
            skLineSegment(sketch, "E1926", {"start": v(-11.4, 120.73) * mm, "end": v(-11.45, 120.65) * mm});
            skLineSegment(sketch, "E1927", {"start": v(-11.45, 120.65) * mm, "end": v(-11.5, 120.5) * mm});
            skLineSegment(sketch, "E1928", {"start": v(-11.5, 120.5) * mm, "end": v(-11.58, 120.22) * mm});
            skLineSegment(sketch, "E1929", {"start": v(-11.58, 120.22) * mm, "end": v(-11.62, 120.08) * mm});
            skLineSegment(sketch, "E1930", {"start": v(-11.62, 120.08) * mm, "end": v(-11.66, 119.94) * mm});
            skLineSegment(sketch, "E1931", {"start": v(-11.66, 119.94) * mm, "end": v(-11.74, 119.66) * mm});
            skLineSegment(sketch, "E1932", {"start": v(-11.74, 119.66) * mm, "end": v(-11.78, 119.53) * mm});
            skLineSegment(sketch, "E1933", {"start": v(-11.78, 119.53) * mm, "end": v(-11.86, 119.26) * mm});
            skLineSegment(sketch, "E1934", {"start": v(-11.86, 119.26) * mm, "end": v(-11.9, 119.12) * mm});
            skLineSegment(sketch, "E1935", {"start": v(-11.9, 119.12) * mm, "end": v(-11.93, 119) * mm});
            skLineSegment(sketch, "E1936", {"start": v(-11.93, 119) * mm, "end": v(-11.97, 118.86) * mm});
            skLineSegment(sketch, "E1937", {"start": v(-11.97, 118.86) * mm, "end": v(-12, 118.73) * mm});
            skLineSegment(sketch, "E1938", {"start": v(-12, 118.73) * mm, "end": v(-12.03, 118.6) * mm});
            skLineSegment(sketch, "E1939", {"start": v(-12.03, 118.6) * mm, "end": v(-12.06, 118.47) * mm});
            skLineSegment(sketch, "E1940", {"start": v(-12.06, 118.47) * mm, "end": v(-12.1, 118.35) * mm});
            skLineSegment(sketch, "E1941", {"start": v(-12.1, 118.35) * mm, "end": v(-12.13, 118.22) * mm});
            skLineSegment(sketch, "E1942", {"start": v(-12.13, 118.22) * mm, "end": v(-12.16, 118.1) * mm});
            skLineSegment(sketch, "E1943", {"start": v(-12.16, 118.1) * mm, "end": v(-12.19, 117.97) * mm});
            skLineSegment(sketch, "E1944", {"start": v(-12.19, 117.97) * mm, "end": v(-12.22, 117.85) * mm});
            skLineSegment(sketch, "E1945", {"start": v(-12.22, 117.85) * mm, "end": v(-12.25, 117.72) * mm});
            skLineSegment(sketch, "E1946", {"start": v(-12.25, 117.72) * mm, "end": v(-12.28, 117.6) * mm});
            skLineSegment(sketch, "E1947", {"start": v(-12.28, 117.6) * mm, "end": v(-12.3, 117.48) * mm});
            skLineSegment(sketch, "E1948", {"start": v(-12.3, 117.48) * mm, "end": v(-12.33, 117.37) * mm});
            skLineSegment(sketch, "E1949", {"start": v(-12.33, 117.37) * mm, "end": v(-12.36, 117.25) * mm});
            skLineSegment(sketch, "E1950", {"start": v(-12.36, 117.25) * mm, "end": v(-12.38, 117.13) * mm});
            skLineSegment(sketch, "E1951", {"start": v(-12.38, 117.13) * mm, "end": v(-12.4, 117.01) * mm});
            skLineSegment(sketch, "E1952", {"start": v(-12.4, 117.01) * mm, "end": v(-12.43, 116.9) * mm});
            skLineSegment(sketch, "E1953", {"start": v(-12.43, 116.9) * mm, "end": v(-12.45, 116.79) * mm});
            skLineSegment(sketch, "E1954", {"start": v(-12.45, 116.79) * mm, "end": v(-12.48, 116.67) * mm});
            skLineSegment(sketch, "E1955", {"start": v(-12.48, 116.67) * mm, "end": v(-12.5, 116.56) * mm});
            skLineSegment(sketch, "E1956", {"start": v(-12.5, 116.56) * mm, "end": v(-12.52, 116.45) * mm});
            skLineSegment(sketch, "E1957", {"start": v(-12.52, 116.45) * mm, "end": v(-12.56, 116.23) * mm});
            skLineSegment(sketch, "E1958", {"start": v(-12.56, 116.23) * mm, "end": v(-12.58, 116.13) * mm});
            skLineSegment(sketch, "E1959", {"start": v(-12.58, 116.13) * mm, "end": v(-12.6, 116.02) * mm});
            skLineSegment(sketch, "E1960", {"start": v(-12.6, 116.02) * mm, "end": v(-13.53, 115.74) * mm});
            skLineSegment(sketch, "E1961", {"start": v(-13.53, 115.74) * mm, "end": v(-14.5, 115.8) * mm});
            skLineSegment(sketch, "E1962", {"start": v(-14.5, 115.8) * mm, "end": v(-14.6, 116) * mm});
            skLineSegment(sketch, "E1963", {"start": v(-14.6, 116) * mm, "end": v(-14.64, 116.1) * mm});
            skLineSegment(sketch, "E1964", {"start": v(-14.64, 116.1) * mm, "end": v(-14.69, 116.2) * mm});
            skLineSegment(sketch, "E1965", {"start": v(-14.69, 116.2) * mm, "end": v(-14.73, 116.3) * mm});
            skLineSegment(sketch, "E1966", {"start": v(-14.73, 116.3) * mm, "end": v(-14.78, 116.4) * mm});
            skLineSegment(sketch, "E1967", {"start": v(-14.78, 116.4) * mm, "end": v(-14.83, 116.5) * mm});
            skLineSegment(sketch, "E1968", {"start": v(-14.83, 116.5) * mm, "end": v(-14.88, 116.61) * mm});
            skLineSegment(sketch, "E1969", {"start": v(-14.88, 116.61) * mm, "end": v(-14.93, 116.72) * mm});
            skLineSegment(sketch, "E1970", {"start": v(-14.93, 116.72) * mm, "end": v(-14.98, 116.83) * mm});
            skLineSegment(sketch, "E1971", {"start": v(-14.98, 116.83) * mm, "end": v(-15.03, 116.94) * mm});
            skLineSegment(sketch, "E1972", {"start": v(-15.03, 116.94) * mm, "end": v(-15.08, 117.04) * mm});
            skLineSegment(sketch, "E1973", {"start": v(-15.08, 117.04) * mm, "end": v(-15.2, 117.26) * mm});
            skLineSegment(sketch, "E1974", {"start": v(-15.2, 117.26) * mm, "end": v(-15.25, 117.37) * mm});
            skLineSegment(sketch, "E1975", {"start": v(-15.25, 117.37) * mm, "end": v(-15.3, 117.49) * mm});
            skLineSegment(sketch, "E1976", {"start": v(-15.3, 117.49) * mm, "end": v(-15.36, 117.6) * mm});
            skLineSegment(sketch, "E1977", {"start": v(-15.36, 117.6) * mm, "end": v(-15.47, 117.83) * mm});
            skLineSegment(sketch, "E1978", {"start": v(-15.47, 117.83) * mm, "end": v(-15.53, 117.94) * mm});
            skLineSegment(sketch, "E1979", {"start": v(-15.53, 117.94) * mm, "end": v(-15.66, 118.18) * mm});
            skLineSegment(sketch, "E1980", {"start": v(-15.66, 118.18) * mm, "end": v(-15.72, 118.3) * mm});
            skLineSegment(sketch, "E1981", {"start": v(-15.72, 118.3) * mm, "end": v(-15.78, 118.41) * mm});
            skLineSegment(sketch, "E1982", {"start": v(-15.78, 118.41) * mm, "end": v(-15.91, 118.65) * mm});
            skLineSegment(sketch, "E1983", {"start": v(-15.91, 118.65) * mm, "end": v(-15.98, 118.78) * mm});
            skLineSegment(sketch, "E1984", {"start": v(-15.98, 118.78) * mm, "end": v(-16.04, 118.9) * mm});
            skLineSegment(sketch, "E1985", {"start": v(-16.04, 118.9) * mm, "end": v(-16.11, 119.02) * mm});
            skLineSegment(sketch, "E1986", {"start": v(-16.11, 119.02) * mm, "end": v(-16.18, 119.15) * mm});
            skLineSegment(sketch, "E1987", {"start": v(-16.18, 119.15) * mm, "end": v(-16.25, 119.27) * mm});
            skLineSegment(sketch, "E1988", {"start": v(-16.25, 119.27) * mm, "end": v(-16.4, 119.52) * mm});
            skLineSegment(sketch, "E1989", {"start": v(-16.4, 119.52) * mm, "end": v(-16.47, 119.65) * mm});
            skLineSegment(sketch, "E1990", {"start": v(-16.47, 119.65) * mm, "end": v(-16.54, 119.78) * mm});
            skLineSegment(sketch, "E1991", {"start": v(-16.54, 119.78) * mm, "end": v(-16.62, 119.9) * mm});
            skLineSegment(sketch, "E1992", {"start": v(-16.62, 119.9) * mm, "end": v(-16.7, 120.03) * mm});
            skLineSegment(sketch, "E1993", {"start": v(-16.7, 120.03) * mm, "end": v(-16.76, 120.1) * mm});
            skLineSegment(sketch, "E1994", {"start": v(-16.76, 120.1) * mm, "end": v(-18.4, 119.86) * mm});
            skLineSegment(sketch, "E1995", {"start": v(-18.4, 119.86) * mm, "end": v(-18.45, 119.78) * mm});
            skLineSegment(sketch, "E1996", {"start": v(-18.45, 119.78) * mm, "end": v(-18.48, 119.63) * mm});
            skLineSegment(sketch, "E1997", {"start": v(-18.48, 119.63) * mm, "end": v(-18.52, 119.49) * mm});
            skLineSegment(sketch, "E1998", {"start": v(-18.52, 119.49) * mm, "end": v(-18.55, 119.34) * mm});
            skLineSegment(sketch, "E1999", {"start": v(-18.55, 119.34) * mm, "end": v(-18.59, 119.2) * mm});
            skLineSegment(sketch, "E2000", {"start": v(-18.59, 119.2) * mm, "end": v(-18.62, 119.06) * mm});
            skLineSegment(sketch, "E2001", {"start": v(-18.62, 119.06) * mm, "end": v(-18.65, 118.92) * mm});
            skLineSegment(sketch, "E2002", {"start": v(-18.65, 118.92) * mm, "end": v(-18.68, 118.78) * mm});
            skLineSegment(sketch, "E2003", {"start": v(-18.68, 118.78) * mm, "end": v(-18.71, 118.64) * mm});
            skLineSegment(sketch, "E2004", {"start": v(-18.71, 118.64) * mm, "end": v(-18.74, 118.5) * mm});
            skLineSegment(sketch, "E2005", {"start": v(-18.74, 118.5) * mm, "end": v(-18.77, 118.37) * mm});
            skLineSegment(sketch, "E2006", {"start": v(-18.77, 118.37) * mm, "end": v(-18.8, 118.23) * mm});
            skLineSegment(sketch, "E2007", {"start": v(-18.8, 118.23) * mm, "end": v(-18.86, 117.96) * mm});
            skLineSegment(sketch, "E2008", {"start": v(-18.86, 117.96) * mm, "end": v(-18.88, 117.83) * mm});
            skLineSegment(sketch, "E2009", {"start": v(-18.88, 117.83) * mm, "end": v(-18.9, 117.7) * mm});
            skLineSegment(sketch, "E2010", {"start": v(-18.9, 117.7) * mm, "end": v(-18.96, 117.44) * mm});
            skLineSegment(sketch, "E2011", {"start": v(-18.96, 117.44) * mm, "end": v(-18.98, 117.31) * mm});
            skLineSegment(sketch, "E2012", {"start": v(-18.98, 117.31) * mm, "end": v(-19, 117.19) * mm});
            skLineSegment(sketch, "E2013", {"start": v(-19, 117.19) * mm, "end": v(-19.03, 117.06) * mm});
            skLineSegment(sketch, "E2014", {"start": v(-19.03, 117.06) * mm, "end": v(-19.07, 116.81) * mm});
            skLineSegment(sketch, "E2015", {"start": v(-19.07, 116.81) * mm, "end": v(-19.1, 116.7) * mm});
            skLineSegment(sketch, "E2016", {"start": v(-19.1, 116.7) * mm, "end": v(-19.11, 116.57) * mm});
            skLineSegment(sketch, "E2017", {"start": v(-19.11, 116.57) * mm, "end": v(-19.15, 116.33) * mm});
            skLineSegment(sketch, "E2018", {"start": v(-19.15, 116.33) * mm, "end": v(-19.19, 116.1) * mm});
            skLineSegment(sketch, "E2019", {"start": v(-19.19, 116.1) * mm, "end": v(-19.2, 115.98) * mm});
            skLineSegment(sketch, "E2020", {"start": v(-19.2, 115.98) * mm, "end": v(-19.22, 115.86) * mm});
            skLineSegment(sketch, "E2021", {"start": v(-19.22, 115.86) * mm, "end": v(-19.26, 115.64) * mm});
            skLineSegment(sketch, "E2022", {"start": v(-19.26, 115.64) * mm, "end": v(-19.27, 115.53) * mm});
            skLineSegment(sketch, "E2023", {"start": v(-19.27, 115.53) * mm, "end": v(-19.28, 115.42) * mm});
            skLineSegment(sketch, "E2024", {"start": v(-19.28, 115.42) * mm, "end": v(-19.3, 115.3) * mm});
            skLineSegment(sketch, "E2025", {"start": v(-19.3, 115.3) * mm, "end": v(-19.31, 115.2) * mm});
            skLineSegment(sketch, "E2026", {"start": v(-19.31, 115.2) * mm, "end": v(-19.33, 115.1) * mm});
            skLineSegment(sketch, "E2027", {"start": v(-19.33, 115.1) * mm, "end": v(-20.24, 114.76) * mm});
            skLineSegment(sketch, "E2028", {"start": v(-20.24, 114.76) * mm, "end": v(-21.22, 114.76) * mm});
            skLineSegment(sketch, "E2029", {"start": v(-21.22, 114.76) * mm, "end": v(-21.26, 114.85) * mm});
            skLineSegment(sketch, "E2030", {"start": v(-21.26, 114.85) * mm, "end": v(-21.31, 114.95) * mm});
            skLineSegment(sketch, "E2031", {"start": v(-21.31, 114.95) * mm, "end": v(-21.36, 115.05) * mm});
            skLineSegment(sketch, "E2032", {"start": v(-21.36, 115.05) * mm, "end": v(-21.42, 115.15) * mm});
            skLineSegment(sketch, "E2033", {"start": v(-21.42, 115.15) * mm, "end": v(-21.47, 115.25) * mm});
            skLineSegment(sketch, "E2034", {"start": v(-21.47, 115.25) * mm, "end": v(-21.52, 115.35) * mm});
            skLineSegment(sketch, "E2035", {"start": v(-21.52, 115.35) * mm, "end": v(-21.58, 115.45) * mm});
            skLineSegment(sketch, "E2036", {"start": v(-21.58, 115.45) * mm, "end": v(-21.63, 115.55) * mm});
            skLineSegment(sketch, "E2037", {"start": v(-21.63, 115.55) * mm, "end": v(-21.75, 115.76) * mm});
            skLineSegment(sketch, "E2038", {"start": v(-21.75, 115.76) * mm, "end": v(-21.8, 115.86) * mm});
            skLineSegment(sketch, "E2039", {"start": v(-21.8, 115.86) * mm, "end": v(-21.86, 115.97) * mm});
            skLineSegment(sketch, "E2040", {"start": v(-21.86, 115.97) * mm, "end": v(-21.92, 116.07) * mm});
            skLineSegment(sketch, "E2041", {"start": v(-21.92, 116.07) * mm, "end": v(-21.98, 116.18) * mm});
            skLineSegment(sketch, "E2042", {"start": v(-21.98, 116.18) * mm, "end": v(-22.1, 116.4) * mm});
            skLineSegment(sketch, "E2043", {"start": v(-22.1, 116.4) * mm, "end": v(-22.17, 116.5) * mm});
            skLineSegment(sketch, "E2044", {"start": v(-22.17, 116.5) * mm, "end": v(-22.23, 116.62) * mm});
            skLineSegment(sketch, "E2045", {"start": v(-22.23, 116.62) * mm, "end": v(-22.3, 116.73) * mm});
            skLineSegment(sketch, "E2046", {"start": v(-22.3, 116.73) * mm, "end": v(-22.37, 116.84) * mm});
            skLineSegment(sketch, "E2047", {"start": v(-22.37, 116.84) * mm, "end": v(-22.5, 117.07) * mm});
            skLineSegment(sketch, "E2048", {"start": v(-22.5, 117.07) * mm, "end": v(-22.57, 117.18) * mm});
            skLineSegment(sketch, "E2049", {"start": v(-22.57, 117.18) * mm, "end": v(-22.64, 117.3) * mm});
            skLineSegment(sketch, "E2050", {"start": v(-22.64, 117.3) * mm, "end": v(-22.78, 117.53) * mm});
            skLineSegment(sketch, "E2051", {"start": v(-22.78, 117.53) * mm, "end": v(-22.86, 117.65) * mm});
            skLineSegment(sketch, "E2052", {"start": v(-22.86, 117.65) * mm, "end": v(-22.93, 117.76) * mm});
            skLineSegment(sketch, "E2053", {"start": v(-22.93, 117.76) * mm, "end": v(-23, 117.88) * mm});
            skLineSegment(sketch, "E2054", {"start": v(-23, 117.88) * mm, "end": v(-23.08, 118) * mm});
            skLineSegment(sketch, "E2055", {"start": v(-23.08, 118) * mm, "end": v(-23.24, 118.25) * mm});
            skLineSegment(sketch, "E2056", {"start": v(-23.24, 118.25) * mm, "end": v(-23.32, 118.37) * mm});
            skLineSegment(sketch, "E2057", {"start": v(-23.32, 118.37) * mm, "end": v(-23.4, 118.49) * mm});
            skLineSegment(sketch, "E2058", {"start": v(-23.4, 118.49) * mm, "end": v(-23.48, 118.61) * mm});
            skLineSegment(sketch, "E2059", {"start": v(-23.48, 118.61) * mm, "end": v(-23.56, 118.74) * mm});
            skLineSegment(sketch, "E2060", {"start": v(-23.56, 118.74) * mm, "end": v(-23.64, 118.86) * mm});
            skLineSegment(sketch, "E2061", {"start": v(-23.64, 118.86) * mm, "end": v(-23.72, 118.93) * mm});
            skLineSegment(sketch, "E2062", {"start": v(-23.72, 118.93) * mm, "end": v(-25.34, 118.59) * mm});
            skLineSegment(sketch, "E2063", {"start": v(-25.34, 118.59) * mm, "end": v(-25.38, 118.5) * mm});
            skLineSegment(sketch, "E2064", {"start": v(-25.38, 118.5) * mm, "end": v(-25.4, 118.35) * mm});
            skLineSegment(sketch, "E2065", {"start": v(-25.4, 118.35) * mm, "end": v(-25.44, 118.2) * mm});
            skLineSegment(sketch, "E2066", {"start": v(-25.44, 118.2) * mm, "end": v(-25.46, 118.06) * mm});
            skLineSegment(sketch, "E2067", {"start": v(-25.46, 118.06) * mm, "end": v(-25.49, 117.92) * mm});
            skLineSegment(sketch, "E2068", {"start": v(-25.49, 117.92) * mm, "end": v(-25.5, 117.78) * mm});
            skLineSegment(sketch, "E2069", {"start": v(-25.5, 117.78) * mm, "end": v(-25.56, 117.5) * mm});
            skLineSegment(sketch, "E2070", {"start": v(-25.56, 117.5) * mm, "end": v(-25.58, 117.35) * mm});
            skLineSegment(sketch, "E2071", {"start": v(-25.58, 117.35) * mm, "end": v(-25.6, 117.21) * mm});
            skLineSegment(sketch, "E2072", {"start": v(-25.6, 117.21) * mm, "end": v(-25.62, 117.08) * mm});
            skLineSegment(sketch, "E2073", {"start": v(-25.62, 117.08) * mm, "end": v(-25.64, 116.94) * mm});
            skLineSegment(sketch, "E2074", {"start": v(-25.64, 116.94) * mm, "end": v(-25.66, 116.8) * mm});
            skLineSegment(sketch, "E2075", {"start": v(-25.66, 116.8) * mm, "end": v(-25.7, 116.54) * mm});
            skLineSegment(sketch, "E2076", {"start": v(-25.7, 116.54) * mm, "end": v(-25.72, 116.4) * mm});
            skLineSegment(sketch, "E2077", {"start": v(-25.72, 116.4) * mm, "end": v(-25.74, 116.27) * mm});
            skLineSegment(sketch, "E2078", {"start": v(-25.74, 116.27) * mm, "end": v(-25.75, 116.14) * mm});
            skLineSegment(sketch, "E2079", {"start": v(-25.75, 116.14) * mm, "end": v(-25.77, 116.01) * mm});
            skLineSegment(sketch, "E2080", {"start": v(-25.77, 116.01) * mm, "end": v(-25.79, 115.88) * mm});
            skLineSegment(sketch, "E2081", {"start": v(-25.79, 115.88) * mm, "end": v(-25.82, 115.63) * mm});
            skLineSegment(sketch, "E2082", {"start": v(-25.82, 115.63) * mm, "end": v(-25.85, 115.38) * mm});
            skLineSegment(sketch, "E2083", {"start": v(-25.85, 115.38) * mm, "end": v(-25.86, 115.26) * mm});
            skLineSegment(sketch, "E2084", {"start": v(-25.86, 115.26) * mm, "end": v(-25.88, 115.02) * mm});
            skLineSegment(sketch, "E2085", {"start": v(-25.88, 115.02) * mm, "end": v(-25.9, 114.9) * mm});
            skLineSegment(sketch, "E2086", {"start": v(-25.9, 114.9) * mm, "end": v(-25.92, 114.67) * mm});
            skLineSegment(sketch, "E2087", {"start": v(-25.92, 114.67) * mm, "end": v(-25.93, 114.55) * mm});
            skLineSegment(sketch, "E2088", {"start": v(-25.93, 114.55) * mm, "end": v(-25.94, 114.44) * mm});
            skLineSegment(sketch, "E2089", {"start": v(-25.94, 114.44) * mm, "end": v(-25.96, 114.21) * mm});
            skLineSegment(sketch, "E2090", {"start": v(-25.96, 114.21) * mm, "end": v(-25.96, 114.1) * mm});
            skLineSegment(sketch, "E2091", {"start": v(-25.96, 114.1) * mm, "end": v(-25.97, 113.99) * mm});
            skLineSegment(sketch, "E2092", {"start": v(-25.97, 113.99) * mm, "end": v(-25.98, 113.88) * mm});
            skLineSegment(sketch, "E2093", {"start": v(-25.98, 113.88) * mm, "end": v(-25.99, 113.77) * mm});
            skLineSegment(sketch, "E2094", {"start": v(-25.99, 113.77) * mm, "end": v(-26.88, 113.38) * mm});
            skLineSegment(sketch, "E2095", {"start": v(-26.88, 113.38) * mm, "end": v(-27.85, 113.33) * mm});
            skLineSegment(sketch, "E2096", {"start": v(-27.85, 113.33) * mm, "end": v(-27.9, 113.42) * mm});
            skLineSegment(sketch, "E2097", {"start": v(-27.9, 113.42) * mm, "end": v(-27.96, 113.52) * mm});
            skLineSegment(sketch, "E2098", {"start": v(-27.96, 113.52) * mm, "end": v(-28.02, 113.61) * mm});
            skLineSegment(sketch, "E2099", {"start": v(-28.02, 113.61) * mm, "end": v(-28.08, 113.7) * mm});
            skLineSegment(sketch, "E2100", {"start": v(-28.08, 113.7) * mm, "end": v(-28.13, 113.8) * mm});
            skLineSegment(sketch, "E2101", {"start": v(-28.13, 113.8) * mm, "end": v(-28.2, 113.9) * mm});
            skLineSegment(sketch, "E2102", {"start": v(-28.2, 113.9) * mm, "end": v(-28.31, 114.1) * mm});
            skLineSegment(sketch, "E2103", {"start": v(-28.31, 114.1) * mm, "end": v(-28.38, 114.2) * mm});
            skLineSegment(sketch, "E2104", {"start": v(-28.38, 114.2) * mm, "end": v(-28.44, 114.3) * mm});
            skLineSegment(sketch, "E2105", {"start": v(-28.44, 114.3) * mm, "end": v(-28.5, 114.4) * mm});
            skLineSegment(sketch, "E2106", {"start": v(-28.5, 114.4) * mm, "end": v(-28.57, 114.5) * mm});
            skLineSegment(sketch, "E2107", {"start": v(-28.57, 114.5) * mm, "end": v(-28.63, 114.6) * mm});
            skLineSegment(sketch, "E2108", {"start": v(-28.63, 114.6) * mm, "end": v(-28.7, 114.7) * mm});
            skLineSegment(sketch, "E2109", {"start": v(-28.7, 114.7) * mm, "end": v(-28.77, 114.81) * mm});
            skLineSegment(sketch, "E2110", {"start": v(-28.77, 114.81) * mm, "end": v(-28.84, 114.92) * mm});
            skLineSegment(sketch, "E2111", {"start": v(-28.84, 114.92) * mm, "end": v(-28.98, 115.13) * mm});
            skLineSegment(sketch, "E2112", {"start": v(-28.98, 115.13) * mm, "end": v(-29.05, 115.24) * mm});
            skLineSegment(sketch, "E2113", {"start": v(-29.05, 115.24) * mm, "end": v(-29.12, 115.34) * mm});
            skLineSegment(sketch, "E2114", {"start": v(-29.12, 115.34) * mm, "end": v(-29.2, 115.45) * mm});
            skLineSegment(sketch, "E2115", {"start": v(-29.2, 115.45) * mm, "end": v(-29.27, 115.56) * mm});
            skLineSegment(sketch, "E2116", {"start": v(-29.27, 115.56) * mm, "end": v(-29.35, 115.67) * mm});
            skLineSegment(sketch, "E2117", {"start": v(-29.35, 115.67) * mm, "end": v(-29.42, 115.78) * mm});
            skLineSegment(sketch, "E2118", {"start": v(-29.42, 115.78) * mm, "end": v(-29.5, 115.9) * mm});
            skLineSegment(sketch, "E2119", {"start": v(-29.5, 115.9) * mm, "end": v(-29.58, 116) * mm});
            skLineSegment(sketch, "E2120", {"start": v(-29.58, 116) * mm, "end": v(-29.66, 116.12) * mm});
            skLineSegment(sketch, "E2121", {"start": v(-29.66, 116.12) * mm, "end": v(-29.74, 116.23) * mm});
            skLineSegment(sketch, "E2122", {"start": v(-29.74, 116.23) * mm, "end": v(-29.82, 116.35) * mm});
            skLineSegment(sketch, "E2123", {"start": v(-29.82, 116.35) * mm, "end": v(-29.9, 116.46) * mm});
            skLineSegment(sketch, "E2124", {"start": v(-29.9, 116.46) * mm, "end": v(-29.99, 116.58) * mm});
            skLineSegment(sketch, "E2125", {"start": v(-29.99, 116.58) * mm, "end": v(-30.07, 116.7) * mm});
            skLineSegment(sketch, "E2126", {"start": v(-30.07, 116.7) * mm, "end": v(-30.25, 116.93) * mm});
            skLineSegment(sketch, "E2127", {"start": v(-30.25, 116.93) * mm, "end": v(-30.33, 117.05) * mm});
            skLineSegment(sketch, "E2128", {"start": v(-30.33, 117.05) * mm, "end": v(-30.42, 117.16) * mm});
            skLineSegment(sketch, "E2129", {"start": v(-30.42, 117.16) * mm, "end": v(-30.51, 117.28) * mm});
            skLineSegment(sketch, "E2130", {"start": v(-30.51, 117.28) * mm, "end": v(-30.6, 117.35) * mm});
            skLineSegment(sketch, "E2131", {"start": v(-30.6, 117.35) * mm, "end": v(-32.2, 116.92) * mm});
            skLineSegment(sketch, "E2132", {"start": v(-32.2, 116.92) * mm, "end": v(-32.23, 116.83) * mm});
            skLineSegment(sketch, "E2133", {"start": v(-32.23, 116.83) * mm, "end": v(-32.25, 116.68) * mm});
            skLineSegment(sketch, "E2134", {"start": v(-32.25, 116.68) * mm, "end": v(-32.28, 116.38) * mm});
            skLineSegment(sketch, "E2135", {"start": v(-32.28, 116.38) * mm, "end": v(-32.3, 116.24) * mm});
            skLineSegment(sketch, "E2136", {"start": v(-32.3, 116.24) * mm, "end": v(-32.32, 116.1) * mm});
            skLineSegment(sketch, "E2137", {"start": v(-32.32, 116.1) * mm, "end": v(-32.33, 115.95) * mm});
            skLineSegment(sketch, "E2138", {"start": v(-32.33, 115.95) * mm, "end": v(-32.35, 115.8) * mm});
            skLineSegment(sketch, "E2139", {"start": v(-32.35, 115.8) * mm, "end": v(-32.36, 115.67) * mm});
            skLineSegment(sketch, "E2140", {"start": v(-32.36, 115.67) * mm, "end": v(-32.37, 115.53) * mm});
            skLineSegment(sketch, "E2141", {"start": v(-32.37, 115.53) * mm, "end": v(-32.39, 115.39) * mm});
            skLineSegment(sketch, "E2142", {"start": v(-32.39, 115.39) * mm, "end": v(-32.4, 115.25) * mm});
            skLineSegment(sketch, "E2143", {"start": v(-32.4, 115.25) * mm, "end": v(-32.41, 115.11) * mm});
            skLineSegment(sketch, "E2144", {"start": v(-32.41, 115.11) * mm, "end": v(-32.42, 114.98) * mm});
            skLineSegment(sketch, "E2145", {"start": v(-32.42, 114.98) * mm, "end": v(-32.43, 114.84) * mm});
            skLineSegment(sketch, "E2146", {"start": v(-32.43, 114.84) * mm, "end": v(-32.44, 114.71) * mm});
            skLineSegment(sketch, "E2147", {"start": v(-32.44, 114.71) * mm, "end": v(-32.45, 114.58) * mm});
            skLineSegment(sketch, "E2148", {"start": v(-32.45, 114.58) * mm, "end": v(-32.46, 114.45) * mm});
            skLineSegment(sketch, "E2149", {"start": v(-32.46, 114.45) * mm, "end": v(-32.47, 114.32) * mm});
            skLineSegment(sketch, "E2150", {"start": v(-32.47, 114.32) * mm, "end": v(-32.48, 114.19) * mm});
            skLineSegment(sketch, "E2151", {"start": v(-32.48, 114.19) * mm, "end": v(-32.5, 114.06) * mm});
            skLineSegment(sketch, "E2152", {"start": v(-32.5, 114.06) * mm, "end": v(-32.5, 113.94) * mm});
            skLineSegment(sketch, "E2153", {"start": v(-32.5, 113.94) * mm, "end": v(-32.5, 113.8) * mm});
            skLineSegment(sketch, "E2154", {"start": v(-32.5, 113.8) * mm, "end": v(-32.51, 113.69) * mm});
            skLineSegment(sketch, "E2155", {"start": v(-32.51, 113.69) * mm, "end": v(-32.52, 113.56) * mm});
            skLineSegment(sketch, "E2156", {"start": v(-32.52, 113.56) * mm, "end": v(-32.53, 113.32) * mm});
            skLineSegment(sketch, "E2157", {"start": v(-32.53, 113.32) * mm, "end": v(-32.53, 113.2) * mm});
            skLineSegment(sketch, "E2158", {"start": v(-32.53, 113.2) * mm, "end": v(-32.54, 113.08) * mm});
            skLineSegment(sketch, "E2159", {"start": v(-32.54, 113.08) * mm, "end": v(-32.54, 112.96) * mm});
            skLineSegment(sketch, "E2160", {"start": v(-32.54, 112.96) * mm, "end": v(-32.54, 112.85) * mm});
            skLineSegment(sketch, "E2161", {"start": v(-32.54, 112.85) * mm, "end": v(-32.55, 112.62) * mm});
            skLineSegment(sketch, "E2162", {"start": v(-32.55, 112.62) * mm, "end": v(-32.55, 112.5) * mm});
            skLineSegment(sketch, "E2163", {"start": v(-32.55, 112.5) * mm, "end": v(-32.55, 112.4) * mm});
            skLineSegment(sketch, "E2164", {"start": v(-32.55, 112.4) * mm, "end": v(-32.55, 112.29) * mm});
            skLineSegment(sketch, "E2165", {"start": v(-32.55, 112.29) * mm, "end": v(-32.56, 112.18) * mm});
            skLineSegment(sketch, "E2166", {"start": v(-32.56, 112.18) * mm, "end": v(-32.56, 112.07) * mm});
            skLineSegment(sketch, "E2167", {"start": v(-32.56, 112.07) * mm, "end": v(-33.43, 111.63) * mm});
            skLineSegment(sketch, "E2168", {"start": v(-33.43, 111.63) * mm, "end": v(-34.4, 111.52) * mm});
            skLineSegment(sketch, "E2169", {"start": v(-34.4, 111.52) * mm, "end": v(-34.46, 111.6) * mm});
            skLineSegment(sketch, "E2170", {"start": v(-34.46, 111.6) * mm, "end": v(-34.52, 111.7) * mm});
            skLineSegment(sketch, "E2171", {"start": v(-34.52, 111.7) * mm, "end": v(-34.58, 111.8) * mm});
            skLineSegment(sketch, "E2172", {"start": v(-34.58, 111.8) * mm, "end": v(-34.64, 111.88) * mm});
            skLineSegment(sketch, "E2173", {"start": v(-34.64, 111.88) * mm, "end": v(-34.7, 111.98) * mm});
            skLineSegment(sketch, "E2174", {"start": v(-34.7, 111.98) * mm, "end": v(-34.77, 112.07) * mm});
            skLineSegment(sketch, "E2175", {"start": v(-34.77, 112.07) * mm, "end": v(-34.83, 112.16) * mm});
            skLineSegment(sketch, "E2176", {"start": v(-34.83, 112.16) * mm, "end": v(-34.9, 112.26) * mm});
            skLineSegment(sketch, "E2177", {"start": v(-34.9, 112.26) * mm, "end": v(-35.04, 112.45) * mm});
            skLineSegment(sketch, "E2178", {"start": v(-35.04, 112.45) * mm, "end": v(-35.18, 112.65) * mm});
            skLineSegment(sketch, "E2179", {"start": v(-35.18, 112.65) * mm, "end": v(-35.25, 112.74) * mm});
            skLineSegment(sketch, "E2180", {"start": v(-35.25, 112.74) * mm, "end": v(-35.32, 112.84) * mm});
            skLineSegment(sketch, "E2181", {"start": v(-35.32, 112.84) * mm, "end": v(-35.4, 112.94) * mm});
            skLineSegment(sketch, "E2182", {"start": v(-35.4, 112.94) * mm, "end": v(-35.47, 113.04) * mm});
            skLineSegment(sketch, "E2183", {"start": v(-35.47, 113.04) * mm, "end": v(-35.55, 113.15) * mm});
            skLineSegment(sketch, "E2184", {"start": v(-35.55, 113.15) * mm, "end": v(-35.62, 113.25) * mm});
            skLineSegment(sketch, "E2185", {"start": v(-35.62, 113.25) * mm, "end": v(-35.7, 113.35) * mm});
            skLineSegment(sketch, "E2186", {"start": v(-35.7, 113.35) * mm, "end": v(-35.78, 113.45) * mm});
            skLineSegment(sketch, "E2187", {"start": v(-35.78, 113.45) * mm, "end": v(-35.94, 113.66) * mm});
            skLineSegment(sketch, "E2188", {"start": v(-35.94, 113.66) * mm, "end": v(-36.1, 113.88) * mm});
            skLineSegment(sketch, "E2189", {"start": v(-36.1, 113.88) * mm, "end": v(-36.19, 113.98) * mm});
            skLineSegment(sketch, "E2190", {"start": v(-36.19, 113.98) * mm, "end": v(-36.27, 114.09) * mm});
            skLineSegment(sketch, "E2191", {"start": v(-36.27, 114.09) * mm, "end": v(-36.36, 114.2) * mm});
            skLineSegment(sketch, "E2192", {"start": v(-36.36, 114.2) * mm, "end": v(-36.54, 114.42) * mm});
            skLineSegment(sketch, "E2193", {"start": v(-36.54, 114.42) * mm, "end": v(-36.71, 114.64) * mm});
            skLineSegment(sketch, "E2194", {"start": v(-36.71, 114.64) * mm, "end": v(-36.9, 114.86) * mm});
            skLineSegment(sketch, "E2195", {"start": v(-36.9, 114.86) * mm, "end": v(-37, 114.97) * mm});
            skLineSegment(sketch, "E2196", {"start": v(-37, 114.97) * mm, "end": v(-37.09, 115.08) * mm});
            skLineSegment(sketch, "E2197", {"start": v(-37.09, 115.08) * mm, "end": v(-37.18, 115.2) * mm});
            skLineSegment(sketch, "E2198", {"start": v(-37.18, 115.2) * mm, "end": v(-37.28, 115.31) * mm});
            skLineSegment(sketch, "E2199", {"start": v(-37.28, 115.31) * mm, "end": v(-37.36, 115.37) * mm});
            skLineSegment(sketch, "E2200", {"start": v(-37.36, 115.37) * mm, "end": v(-38.94, 114.85) * mm});
            skLineSegment(sketch, "E2201", {"start": v(-38.94, 114.85) * mm, "end": v(-38.97, 114.75) * mm});
            skLineSegment(sketch, "E2202", {"start": v(-38.97, 114.75) * mm, "end": v(-38.98, 114.6) * mm});
            skLineSegment(sketch, "E2203", {"start": v(-38.98, 114.6) * mm, "end": v(-38.99, 114.46) * mm});
            skLineSegment(sketch, "E2204", {"start": v(-38.99, 114.46) * mm, "end": v(-39, 114.3) * mm});
            skLineSegment(sketch, "E2205", {"start": v(-39, 114.3) * mm, "end": v(-39, 114.16) * mm});
            skLineSegment(sketch, "E2206", {"start": v(-39, 114.16) * mm, "end": v(-39.02, 113.87) * mm});
            skLineSegment(sketch, "E2207", {"start": v(-39.02, 113.87) * mm, "end": v(-39.02, 113.73) * mm});
            skLineSegment(sketch, "E2208", {"start": v(-39.02, 113.73) * mm, "end": v(-39.03, 113.59) * mm});
            skLineSegment(sketch, "E2209", {"start": v(-39.03, 113.59) * mm, "end": v(-39.04, 113.45) * mm});
            skLineSegment(sketch, "E2210", {"start": v(-39.04, 113.45) * mm, "end": v(-39.04, 113.3) * mm});
            skLineSegment(sketch, "E2211", {"start": v(-39.04, 113.3) * mm, "end": v(-39.05, 113.03) * mm});
            skLineSegment(sketch, "E2212", {"start": v(-39.05, 113.03) * mm, "end": v(-39.05, 112.9) * mm});
            skLineSegment(sketch, "E2213", {"start": v(-39.05, 112.9) * mm, "end": v(-39.06, 112.76) * mm});
            skLineSegment(sketch, "E2214", {"start": v(-39.06, 112.76) * mm, "end": v(-39.06, 112.63) * mm});
            skLineSegment(sketch, "E2215", {"start": v(-39.06, 112.63) * mm, "end": v(-39.06, 112.5) * mm});
            skLineSegment(sketch, "E2216", {"start": v(-39.06, 112.5) * mm, "end": v(-39.06, 112.37) * mm});
            skLineSegment(sketch, "E2217", {"start": v(-39.06, 112.37) * mm, "end": v(-39.06, 112.24) * mm});
            skLineSegment(sketch, "E2218", {"start": v(-39.06, 112.24) * mm, "end": v(-39.07, 112.1) * mm});
            skLineSegment(sketch, "E2219", {"start": v(-39.07, 112.1) * mm, "end": v(-39.07, 111.6) * mm});
            skLineSegment(sketch, "E2220", {"start": v(-39.07, 111.6) * mm, "end": v(-39.06, 111.36) * mm});
            skLineSegment(sketch, "E2221", {"start": v(-39.06, 111.36) * mm, "end": v(-39.06, 111.24) * mm});
            skLineSegment(sketch, "E2222", {"start": v(-39.06, 111.24) * mm, "end": v(-39.06, 111.12) * mm});
            skLineSegment(sketch, "E2223", {"start": v(-39.06, 111.12) * mm, "end": v(-39.06, 111) * mm});
            skLineSegment(sketch, "E2224", {"start": v(-39.06, 111) * mm, "end": v(-39.05, 110.88) * mm});
            skLineSegment(sketch, "E2225", {"start": v(-39.05, 110.88) * mm, "end": v(-39.05, 110.77) * mm});
            skLineSegment(sketch, "E2226", {"start": v(-39.05, 110.77) * mm, "end": v(-39.05, 110.65) * mm});
            skLineSegment(sketch, "E2227", {"start": v(-39.05, 110.65) * mm, "end": v(-39.04, 110.43) * mm});
            skLineSegment(sketch, "E2228", {"start": v(-39.04, 110.43) * mm, "end": v(-39.03, 110.31) * mm});
            skLineSegment(sketch, "E2229", {"start": v(-39.03, 110.31) * mm, "end": v(-39.03, 110.2) * mm});
            skLineSegment(sketch, "E2230", {"start": v(-39.03, 110.2) * mm, "end": v(-39.02, 110.1) * mm});
            skLineSegment(sketch, "E2231", {"start": v(-39.02, 110.1) * mm, "end": v(-39.02, 109.99) * mm});
            skLineSegment(sketch, "E2232", {"start": v(-39.02, 109.99) * mm, "end": v(-39.86, 109.5) * mm});
            skLineSegment(sketch, "E2233", {"start": v(-39.86, 109.5) * mm, "end": v(-40.82, 109.33) * mm});
            skLineSegment(sketch, "E2234", {"start": v(-40.82, 109.33) * mm, "end": v(-41.02, 109.6) * mm});
            skLineSegment(sketch, "E2235", {"start": v(-41.02, 109.6) * mm, "end": v(-41.09, 109.68) * mm});
            skLineSegment(sketch, "E2236", {"start": v(-41.09, 109.68) * mm, "end": v(-41.23, 109.86) * mm});
            skLineSegment(sketch, "E2237", {"start": v(-41.23, 109.86) * mm, "end": v(-41.3, 109.95) * mm});
            skLineSegment(sketch, "E2238", {"start": v(-41.3, 109.95) * mm, "end": v(-41.37, 110.04) * mm});
            skLineSegment(sketch, "E2239", {"start": v(-41.37, 110.04) * mm, "end": v(-41.44, 110.13) * mm});
            skLineSegment(sketch, "E2240", {"start": v(-41.44, 110.13) * mm, "end": v(-41.52, 110.22) * mm});
            skLineSegment(sketch, "E2241", {"start": v(-41.52, 110.22) * mm, "end": v(-41.6, 110.32) * mm});
            skLineSegment(sketch, "E2242", {"start": v(-41.6, 110.32) * mm, "end": v(-41.67, 110.41) * mm});
            skLineSegment(sketch, "E2243", {"start": v(-41.67, 110.41) * mm, "end": v(-41.74, 110.5) * mm});
            skLineSegment(sketch, "E2244", {"start": v(-41.74, 110.5) * mm, "end": v(-41.82, 110.6) * mm});
            skLineSegment(sketch, "E2245", {"start": v(-41.82, 110.6) * mm, "end": v(-41.9, 110.7) * mm});
            skLineSegment(sketch, "E2246", {"start": v(-41.9, 110.7) * mm, "end": v(-42.06, 110.89) * mm});
            skLineSegment(sketch, "E2247", {"start": v(-42.06, 110.89) * mm, "end": v(-42.23, 111.08) * mm});
            skLineSegment(sketch, "E2248", {"start": v(-42.23, 111.08) * mm, "end": v(-42.4, 111.28) * mm});
            skLineSegment(sketch, "E2249", {"start": v(-42.4, 111.28) * mm, "end": v(-42.49, 111.38) * mm});
            skLineSegment(sketch, "E2250", {"start": v(-42.49, 111.38) * mm, "end": v(-42.58, 111.48) * mm});
            skLineSegment(sketch, "E2251", {"start": v(-42.58, 111.48) * mm, "end": v(-42.67, 111.58) * mm});
            skLineSegment(sketch, "E2252", {"start": v(-42.67, 111.58) * mm, "end": v(-42.75, 111.68) * mm});
            skLineSegment(sketch, "E2253", {"start": v(-42.75, 111.68) * mm, "end": v(-42.85, 111.79) * mm});
            skLineSegment(sketch, "E2254", {"start": v(-42.85, 111.79) * mm, "end": v(-42.94, 111.89) * mm});
            skLineSegment(sketch, "E2255", {"start": v(-42.94, 111.89) * mm, "end": v(-43.03, 112) * mm});
            skLineSegment(sketch, "E2256", {"start": v(-43.03, 112) * mm, "end": v(-43.22, 112.2) * mm});
            skLineSegment(sketch, "E2257", {"start": v(-43.22, 112.2) * mm, "end": v(-43.32, 112.3) * mm});
            skLineSegment(sketch, "E2258", {"start": v(-43.32, 112.3) * mm, "end": v(-43.42, 112.41) * mm});
            skLineSegment(sketch, "E2259", {"start": v(-43.42, 112.41) * mm, "end": v(-43.52, 112.52) * mm});
            skLineSegment(sketch, "E2260", {"start": v(-43.52, 112.52) * mm, "end": v(-43.62, 112.63) * mm});
            skLineSegment(sketch, "E2261", {"start": v(-43.62, 112.63) * mm, "end": v(-43.82, 112.84) * mm});
            skLineSegment(sketch, "E2262", {"start": v(-43.82, 112.84) * mm, "end": v(-43.92, 112.95) * mm});
            skLineSegment(sketch, "E2263", {"start": v(-43.92, 112.95) * mm, "end": v(-44, 113) * mm});
            skLineSegment(sketch, "E2264", {"start": v(-44, 113) * mm, "end": v(-45.55, 112.39) * mm});
            skLineSegment(sketch, "E2265", {"start": v(-45.55, 112.39) * mm, "end": v(-45.57, 112.3) * mm});
            skLineSegment(sketch, "E2266", {"start": v(-45.57, 112.3) * mm, "end": v(-45.58, 112) * mm});
            skLineSegment(sketch, "E2267", {"start": v(-45.58, 112) * mm, "end": v(-45.58, 111.7) * mm});
            skLineSegment(sketch, "E2268", {"start": v(-45.58, 111.7) * mm, "end": v(-45.57, 111.41) * mm});
            skLineSegment(sketch, "E2269", {"start": v(-45.57, 111.41) * mm, "end": v(-45.57, 111.27) * mm});
            skLineSegment(sketch, "E2270", {"start": v(-45.57, 111.27) * mm, "end": v(-45.56, 110.85) * mm});
            skLineSegment(sketch, "E2271", {"start": v(-45.56, 110.85) * mm, "end": v(-45.56, 110.7) * mm});
            skLineSegment(sketch, "E2272", {"start": v(-45.56, 110.7) * mm, "end": v(-45.55, 110.44) * mm});
            skLineSegment(sketch, "E2273", {"start": v(-45.55, 110.44) * mm, "end": v(-45.55, 110.3) * mm});
            skLineSegment(sketch, "E2274", {"start": v(-45.55, 110.3) * mm, "end": v(-45.54, 110.17) * mm});
            skLineSegment(sketch, "E2275", {"start": v(-45.54, 110.17) * mm, "end": v(-45.54, 110.03) * mm});
            skLineSegment(sketch, "E2276", {"start": v(-45.54, 110.03) * mm, "end": v(-45.53, 109.9) * mm});
            skLineSegment(sketch, "E2277", {"start": v(-45.53, 109.9) * mm, "end": v(-45.52, 109.77) * mm});
            skLineSegment(sketch, "E2278", {"start": v(-45.52, 109.77) * mm, "end": v(-45.51, 109.52) * mm});
            skLineSegment(sketch, "E2279", {"start": v(-45.51, 109.52) * mm, "end": v(-45.5, 109.4) * mm});
            skLineSegment(sketch, "E2280", {"start": v(-45.5, 109.4) * mm, "end": v(-45.5, 109.27) * mm});
            skLineSegment(sketch, "E2281", {"start": v(-45.5, 109.27) * mm, "end": v(-45.49, 109.14) * mm});
            skLineSegment(sketch, "E2282", {"start": v(-45.49, 109.14) * mm, "end": v(-45.48, 109.02) * mm});
            skLineSegment(sketch, "E2283", {"start": v(-45.48, 109.02) * mm, "end": v(-45.47, 108.9) * mm});
            skLineSegment(sketch, "E2284", {"start": v(-45.47, 108.9) * mm, "end": v(-45.45, 108.66) * mm});
            skLineSegment(sketch, "E2285", {"start": v(-45.45, 108.66) * mm, "end": v(-45.44, 108.54) * mm});
            skLineSegment(sketch, "E2286", {"start": v(-45.44, 108.54) * mm, "end": v(-45.43, 108.42) * mm});
            skLineSegment(sketch, "E2287", {"start": v(-45.43, 108.42) * mm, "end": v(-45.42, 108.3) * mm});
            skLineSegment(sketch, "E2288", {"start": v(-45.42, 108.3) * mm, "end": v(-45.41, 108.2) * mm});
            skLineSegment(sketch, "E2289", {"start": v(-45.41, 108.2) * mm, "end": v(-45.4, 107.97) * mm});
            skLineSegment(sketch, "E2290", {"start": v(-45.4, 107.97) * mm, "end": v(-45.37, 107.75) * mm});
            skLineSegment(sketch, "E2291", {"start": v(-45.37, 107.75) * mm, "end": v(-45.36, 107.64) * mm});
            skLineSegment(sketch, "E2292", {"start": v(-45.36, 107.64) * mm, "end": v(-45.35, 107.53) * mm});
            skLineSegment(sketch, "E2293", {"start": v(-45.35, 107.53) * mm, "end": v(-46.16, 107) * mm});
            skLineSegment(sketch, "E2294", {"start": v(-46.16, 107) * mm, "end": v(-47.1, 106.77) * mm});
            skLineSegment(sketch, "E2295", {"start": v(-47.1, 106.77) * mm, "end": v(-47.18, 106.85) * mm});
            skLineSegment(sketch, "E2296", {"start": v(-47.18, 106.85) * mm, "end": v(-47.25, 106.94) * mm});
            skLineSegment(sketch, "E2297", {"start": v(-47.25, 106.94) * mm, "end": v(-47.32, 107.02) * mm});
            skLineSegment(sketch, "E2298", {"start": v(-47.32, 107.02) * mm, "end": v(-47.4, 107.1) * mm});
            skLineSegment(sketch, "E2299", {"start": v(-47.4, 107.1) * mm, "end": v(-47.47, 107.19) * mm});
            skLineSegment(sketch, "E2300", {"start": v(-47.47, 107.19) * mm, "end": v(-47.54, 107.27) * mm});
            skLineSegment(sketch, "E2301", {"start": v(-47.54, 107.27) * mm, "end": v(-47.62, 107.36) * mm});
            skLineSegment(sketch, "E2302", {"start": v(-47.62, 107.36) * mm, "end": v(-47.7, 107.45) * mm});
            skLineSegment(sketch, "E2303", {"start": v(-47.7, 107.45) * mm, "end": v(-47.78, 107.54) * mm});
            skLineSegment(sketch, "E2304", {"start": v(-47.78, 107.54) * mm, "end": v(-47.94, 107.71) * mm});
            skLineSegment(sketch, "E2305", {"start": v(-47.94, 107.71) * mm, "end": v(-48.02, 107.8) * mm});
            skLineSegment(sketch, "E2306", {"start": v(-48.02, 107.8) * mm, "end": v(-48.1, 107.89) * mm});
            skLineSegment(sketch, "E2307", {"start": v(-48.1, 107.89) * mm, "end": v(-48.18, 107.98) * mm});
            skLineSegment(sketch, "E2308", {"start": v(-48.18, 107.98) * mm, "end": v(-48.35, 108.16) * mm});
            skLineSegment(sketch, "E2309", {"start": v(-48.35, 108.16) * mm, "end": v(-48.44, 108.25) * mm});
            skLineSegment(sketch, "E2310", {"start": v(-48.44, 108.25) * mm, "end": v(-48.53, 108.35) * mm});
            skLineSegment(sketch, "E2311", {"start": v(-48.53, 108.35) * mm, "end": v(-48.7, 108.53) * mm});
            skLineSegment(sketch, "E2312", {"start": v(-48.7, 108.53) * mm, "end": v(-48.8, 108.63) * mm});
            skLineSegment(sketch, "E2313", {"start": v(-48.8, 108.63) * mm, "end": v(-49.08, 108.91) * mm});
            skLineSegment(sketch, "E2314", {"start": v(-49.08, 108.91) * mm, "end": v(-49.18, 109) * mm});
            skLineSegment(sketch, "E2315", {"start": v(-49.18, 109) * mm, "end": v(-49.27, 109.1) * mm});
            skLineSegment(sketch, "E2316", {"start": v(-49.27, 109.1) * mm, "end": v(-49.37, 109.2) * mm});
            skLineSegment(sketch, "E2317", {"start": v(-49.37, 109.2) * mm, "end": v(-49.47, 109.3) * mm});
            skLineSegment(sketch, "E2318", {"start": v(-49.47, 109.3) * mm, "end": v(-49.57, 109.4) * mm});
            skLineSegment(sketch, "E2319", {"start": v(-49.57, 109.4) * mm, "end": v(-49.67, 109.5) * mm});
            skLineSegment(sketch, "E2320", {"start": v(-49.67, 109.5) * mm, "end": v(-49.78, 109.6) * mm});
            skLineSegment(sketch, "E2321", {"start": v(-49.78, 109.6) * mm, "end": v(-49.88, 109.7) * mm});
            skLineSegment(sketch, "E2322", {"start": v(-49.88, 109.7) * mm, "end": v(-50.1, 109.9) * mm});
            skLineSegment(sketch, "E2323", {"start": v(-50.1, 109.9) * mm, "end": v(-50.2, 110) * mm});
            skLineSegment(sketch, "E2324", {"start": v(-50.2, 110) * mm, "end": v(-50.42, 110.2) * mm});
            skLineSegment(sketch, "E2325", {"start": v(-50.42, 110.2) * mm, "end": v(-50.5, 110.25) * mm});
            skLineSegment(sketch, "E2326", {"start": v(-50.5, 110.25) * mm, "end": v(-52, 109.55) * mm});
            skLineSegment(sketch, "E2327", {"start": v(-52, 109.55) * mm, "end": v(-52.03, 109.45) * mm});
            skLineSegment(sketch, "E2328", {"start": v(-52.03, 109.45) * mm, "end": v(-52.02, 109.3) * mm});
            skLineSegment(sketch, "E2329", {"start": v(-52.02, 109.3) * mm, "end": v(-52.01, 109.16) * mm});
            skLineSegment(sketch, "E2330", {"start": v(-52.01, 109.16) * mm, "end": v(-52, 109) * mm});
            skLineSegment(sketch, "E2331", {"start": v(-52, 109) * mm, "end": v(-52, 108.86) * mm});
            skLineSegment(sketch, "E2332", {"start": v(-52, 108.86) * mm, "end": v(-51.97, 108.57) * mm});
            skLineSegment(sketch, "E2333", {"start": v(-51.97, 108.57) * mm, "end": v(-51.96, 108.43) * mm});
            skLineSegment(sketch, "E2334", {"start": v(-51.96, 108.43) * mm, "end": v(-51.95, 108.29) * mm});
            skLineSegment(sketch, "E2335", {"start": v(-51.95, 108.29) * mm, "end": v(-51.93, 108.01) * mm});
            skLineSegment(sketch, "E2336", {"start": v(-51.93, 108.01) * mm, "end": v(-51.92, 107.87) * mm});
            skLineSegment(sketch, "E2337", {"start": v(-51.92, 107.87) * mm, "end": v(-51.9, 107.74) * mm});
            skLineSegment(sketch, "E2338", {"start": v(-51.9, 107.74) * mm, "end": v(-51.9, 107.6) * mm});
            skLineSegment(sketch, "E2339", {"start": v(-51.9, 107.6) * mm, "end": v(-51.88, 107.47) * mm});
            skLineSegment(sketch, "E2340", {"start": v(-51.88, 107.47) * mm, "end": v(-51.86, 107.2) * mm});
            skLineSegment(sketch, "E2341", {"start": v(-51.86, 107.2) * mm, "end": v(-51.84, 107.07) * mm});
            skLineSegment(sketch, "E2342", {"start": v(-51.84, 107.07) * mm, "end": v(-51.83, 106.94) * mm});
            skLineSegment(sketch, "E2343", {"start": v(-51.83, 106.94) * mm, "end": v(-51.82, 106.81) * mm});
            skLineSegment(sketch, "E2344", {"start": v(-51.82, 106.81) * mm, "end": v(-51.8, 106.69) * mm});
            skLineSegment(sketch, "E2345", {"start": v(-51.8, 106.69) * mm, "end": v(-51.79, 106.56) * mm});
            skLineSegment(sketch, "E2346", {"start": v(-51.79, 106.56) * mm, "end": v(-51.76, 106.31) * mm});
            skLineSegment(sketch, "E2347", {"start": v(-51.76, 106.31) * mm, "end": v(-51.73, 106.07) * mm});
            skLineSegment(sketch, "E2348", {"start": v(-51.73, 106.07) * mm, "end": v(-51.71, 105.95) * mm});
            skLineSegment(sketch, "E2349", {"start": v(-51.71, 105.95) * mm, "end": v(-51.7, 105.83) * mm});
            skLineSegment(sketch, "E2350", {"start": v(-51.7, 105.83) * mm, "end": v(-51.68, 105.71) * mm});
            skLineSegment(sketch, "E2351", {"start": v(-51.68, 105.71) * mm, "end": v(-51.66, 105.6) * mm});
            skLineSegment(sketch, "E2352", {"start": v(-51.66, 105.6) * mm, "end": v(-51.64, 105.48) * mm});
            skLineSegment(sketch, "E2353", {"start": v(-51.64, 105.48) * mm, "end": v(-51.61, 105.26) * mm});
            skLineSegment(sketch, "E2354", {"start": v(-51.61, 105.26) * mm, "end": v(-51.58, 105.04) * mm});
            skLineSegment(sketch, "E2355", {"start": v(-51.58, 105.04) * mm, "end": v(-51.56, 104.93) * mm});
            skLineSegment(sketch, "E2356", {"start": v(-51.56, 104.93) * mm, "end": v(-51.54, 104.82) * mm});
            skLineSegment(sketch, "E2357", {"start": v(-51.54, 104.82) * mm, "end": v(-51.52, 104.71) * mm});
            skLineSegment(sketch, "E2358", {"start": v(-51.52, 104.71) * mm, "end": v(-52.3, 104.13) * mm});
            skLineSegment(sketch, "E2359", {"start": v(-52.3, 104.13) * mm, "end": v(-53.24, 103.85) * mm});
            skLineSegment(sketch, "E2360", {"start": v(-53.24, 103.85) * mm, "end": v(-53.31, 103.93) * mm});
            skLineSegment(sketch, "E2361", {"start": v(-53.31, 103.93) * mm, "end": v(-53.39, 104) * mm});
            skLineSegment(sketch, "E2362", {"start": v(-53.39, 104) * mm, "end": v(-53.46, 104.09) * mm});
            skLineSegment(sketch, "E2363", {"start": v(-53.46, 104.09) * mm, "end": v(-53.54, 104.17) * mm});
            skLineSegment(sketch, "E2364", {"start": v(-53.54, 104.17) * mm, "end": v(-53.62, 104.25) * mm});
            skLineSegment(sketch, "E2365", {"start": v(-53.62, 104.25) * mm, "end": v(-53.7, 104.33) * mm});
            skLineSegment(sketch, "E2366", {"start": v(-53.7, 104.33) * mm, "end": v(-53.78, 104.41) * mm});
            skLineSegment(sketch, "E2367", {"start": v(-53.78, 104.41) * mm, "end": v(-53.86, 104.5) * mm});
            skLineSegment(sketch, "E2368", {"start": v(-53.86, 104.5) * mm, "end": v(-53.95, 104.58) * mm});
            skLineSegment(sketch, "E2369", {"start": v(-53.95, 104.58) * mm, "end": v(-54.03, 104.66) * mm});
            skLineSegment(sketch, "E2370", {"start": v(-54.03, 104.66) * mm, "end": v(-54.12, 104.74) * mm});
            skLineSegment(sketch, "E2371", {"start": v(-54.12, 104.74) * mm, "end": v(-54.2, 104.83) * mm});
            skLineSegment(sketch, "E2372", {"start": v(-54.2, 104.83) * mm, "end": v(-54.3, 104.91) * mm});
            skLineSegment(sketch, "E2373", {"start": v(-54.3, 104.91) * mm, "end": v(-54.38, 105) * mm});
            skLineSegment(sketch, "E2374", {"start": v(-54.38, 105) * mm, "end": v(-54.47, 105.08) * mm});
            skLineSegment(sketch, "E2375", {"start": v(-54.47, 105.08) * mm, "end": v(-54.56, 105.17) * mm});
            skLineSegment(sketch, "E2376", {"start": v(-54.56, 105.17) * mm, "end": v(-54.65, 105.25) * mm});
            skLineSegment(sketch, "E2377", {"start": v(-54.65, 105.25) * mm, "end": v(-54.75, 105.34) * mm});
            skLineSegment(sketch, "E2378", {"start": v(-54.75, 105.34) * mm, "end": v(-54.84, 105.43) * mm});
            skLineSegment(sketch, "E2379", {"start": v(-54.84, 105.43) * mm, "end": v(-54.94, 105.52) * mm});
            skLineSegment(sketch, "E2380", {"start": v(-54.94, 105.52) * mm, "end": v(-55.03, 105.6) * mm});
            skLineSegment(sketch, "E2381", {"start": v(-55.03, 105.6) * mm, "end": v(-55.13, 105.7) * mm});
            skLineSegment(sketch, "E2382", {"start": v(-55.13, 105.7) * mm, "end": v(-55.23, 105.78) * mm});
            skLineSegment(sketch, "E2383", {"start": v(-55.23, 105.78) * mm, "end": v(-55.33, 105.88) * mm});
            skLineSegment(sketch, "E2384", {"start": v(-55.33, 105.88) * mm, "end": v(-55.43, 105.97) * mm});
            skLineSegment(sketch, "E2385", {"start": v(-55.43, 105.97) * mm, "end": v(-55.53, 106.06) * mm});
            skLineSegment(sketch, "E2386", {"start": v(-55.53, 106.06) * mm, "end": v(-55.64, 106.15) * mm});
            skLineSegment(sketch, "E2387", {"start": v(-55.64, 106.15) * mm, "end": v(-55.74, 106.24) * mm});
            skLineSegment(sketch, "E2388", {"start": v(-55.74, 106.24) * mm, "end": v(-55.85, 106.33) * mm});
            skLineSegment(sketch, "E2389", {"start": v(-55.85, 106.33) * mm, "end": v(-55.96, 106.43) * mm});
            skLineSegment(sketch, "E2390", {"start": v(-55.96, 106.43) * mm, "end": v(-56.06, 106.52) * mm});
            skLineSegment(sketch, "E2391", {"start": v(-56.06, 106.52) * mm, "end": v(-56.28, 106.7) * mm});
            skLineSegment(sketch, "E2392", {"start": v(-56.28, 106.7) * mm, "end": v(-56.4, 106.8) * mm});
            skLineSegment(sketch, "E2393", {"start": v(-56.4, 106.8) * mm, "end": v(-56.5, 106.9) * mm});
            skLineSegment(sketch, "E2394", {"start": v(-56.5, 106.9) * mm, "end": v(-56.62, 107) * mm});
            skLineSegment(sketch, "E2395", {"start": v(-56.62, 107) * mm, "end": v(-56.74, 107.09) * mm});
            skLineSegment(sketch, "E2396", {"start": v(-56.74, 107.09) * mm, "end": v(-56.83, 107.13) * mm});
            skLineSegment(sketch, "E2397", {"start": v(-56.83, 107.13) * mm, "end": v(-58.29, 106.34) * mm});
            skLineSegment(sketch, "E2398", {"start": v(-58.29, 106.34) * mm, "end": v(-58.3, 106.24) * mm});
            skLineSegment(sketch, "E2399", {"start": v(-58.3, 106.24) * mm, "end": v(-58.29, 106.1) * mm});
            skLineSegment(sketch, "E2400", {"start": v(-58.29, 106.1) * mm, "end": v(-58.25, 105.8) * mm});
            skLineSegment(sketch, "E2401", {"start": v(-58.25, 105.8) * mm, "end": v(-58.22, 105.51) * mm});
            skLineSegment(sketch, "E2402", {"start": v(-58.22, 105.51) * mm, "end": v(-58.2, 105.37) * mm});
            skLineSegment(sketch, "E2403", {"start": v(-58.2, 105.37) * mm, "end": v(-58.18, 105.23) * mm});
            skLineSegment(sketch, "E2404", {"start": v(-58.18, 105.23) * mm, "end": v(-58.16, 105.09) * mm});
            skLineSegment(sketch, "E2405", {"start": v(-58.16, 105.09) * mm, "end": v(-58.14, 104.95) * mm});
            skLineSegment(sketch, "E2406", {"start": v(-58.14, 104.95) * mm, "end": v(-58.12, 104.8) * mm});
            skLineSegment(sketch, "E2407", {"start": v(-58.12, 104.8) * mm, "end": v(-58.1, 104.67) * mm});
            skLineSegment(sketch, "E2408", {"start": v(-58.1, 104.67) * mm, "end": v(-58.08, 104.54) * mm});
            skLineSegment(sketch, "E2409", {"start": v(-58.08, 104.54) * mm, "end": v(-58.07, 104.4) * mm});
            skLineSegment(sketch, "E2410", {"start": v(-58.07, 104.4) * mm, "end": v(-58.04, 104.27) * mm});
            skLineSegment(sketch, "E2411", {"start": v(-58.04, 104.27) * mm, "end": v(-58.02, 104.14) * mm});
            skLineSegment(sketch, "E2412", {"start": v(-58.02, 104.14) * mm, "end": v(-58, 104) * mm});
            skLineSegment(sketch, "E2413", {"start": v(-58, 104) * mm, "end": v(-57.98, 103.88) * mm});
            skLineSegment(sketch, "E2414", {"start": v(-57.98, 103.88) * mm, "end": v(-57.96, 103.75) * mm});
            skLineSegment(sketch, "E2415", {"start": v(-57.96, 103.75) * mm, "end": v(-57.94, 103.62) * mm});
            skLineSegment(sketch, "E2416", {"start": v(-57.94, 103.62) * mm, "end": v(-57.9, 103.37) * mm});
            skLineSegment(sketch, "E2417", {"start": v(-57.9, 103.37) * mm, "end": v(-57.87, 103.25) * mm});
            skLineSegment(sketch, "E2418", {"start": v(-57.87, 103.25) * mm, "end": v(-57.83, 103) * mm});
            skLineSegment(sketch, "E2419", {"start": v(-57.83, 103) * mm, "end": v(-57.8, 102.88) * mm});
            skLineSegment(sketch, "E2420", {"start": v(-57.8, 102.88) * mm, "end": v(-57.78, 102.76) * mm});
            skLineSegment(sketch, "E2421", {"start": v(-57.78, 102.76) * mm, "end": v(-57.76, 102.65) * mm});
            skLineSegment(sketch, "E2422", {"start": v(-57.76, 102.65) * mm, "end": v(-57.74, 102.53) * mm});
            skLineSegment(sketch, "E2423", {"start": v(-57.74, 102.53) * mm, "end": v(-57.72, 102.42) * mm});
            skLineSegment(sketch, "E2424", {"start": v(-57.72, 102.42) * mm, "end": v(-57.67, 102.19) * mm});
            skLineSegment(sketch, "E2425", {"start": v(-57.67, 102.19) * mm, "end": v(-57.64, 102.08) * mm});
            skLineSegment(sketch, "E2426", {"start": v(-57.64, 102.08) * mm, "end": v(-57.62, 101.97) * mm});
            skLineSegment(sketch, "E2427", {"start": v(-57.62, 101.97) * mm, "end": v(-57.6, 101.86) * mm});
            skLineSegment(sketch, "E2428", {"start": v(-57.6, 101.86) * mm, "end": v(-57.57, 101.75) * mm});
            skLineSegment(sketch, "E2429", {"start": v(-57.57, 101.75) * mm, "end": v(-57.55, 101.65) * mm});
            skLineSegment(sketch, "E2430", {"start": v(-57.55, 101.65) * mm, "end": v(-57.52, 101.54) * mm});
            skLineSegment(sketch, "E2431", {"start": v(-57.52, 101.54) * mm, "end": v(-58.27, 100.91) * mm});
            skLineSegment(sketch, "E2432", {"start": v(-58.27, 100.91) * mm, "end": v(-59.19, 100.58) * mm});
            skLineSegment(sketch, "E2433", {"start": v(-59.19, 100.58) * mm, "end": v(-59.27, 100.65) * mm});
            skLineSegment(sketch, "E2434", {"start": v(-59.27, 100.65) * mm, "end": v(-59.35, 100.73) * mm});
            skLineSegment(sketch, "E2435", {"start": v(-59.35, 100.73) * mm, "end": v(-59.5, 100.88) * mm});
            skLineSegment(sketch, "E2436", {"start": v(-59.5, 100.88) * mm, "end": v(-59.68, 101.03) * mm});
            skLineSegment(sketch, "E2437", {"start": v(-59.68, 101.03) * mm, "end": v(-59.76, 101.1) * mm});
            skLineSegment(sketch, "E2438", {"start": v(-59.76, 101.1) * mm, "end": v(-59.85, 101.18) * mm});
            skLineSegment(sketch, "E2439", {"start": v(-59.85, 101.18) * mm, "end": v(-59.94, 101.26) * mm});
            skLineSegment(sketch, "E2440", {"start": v(-59.94, 101.26) * mm, "end": v(-60.12, 101.42) * mm});
            skLineSegment(sketch, "E2441", {"start": v(-60.12, 101.42) * mm, "end": v(-60.2, 101.5) * mm});
            skLineSegment(sketch, "E2442", {"start": v(-60.2, 101.5) * mm, "end": v(-60.3, 101.58) * mm});
            skLineSegment(sketch, "E2443", {"start": v(-60.3, 101.58) * mm, "end": v(-60.4, 101.66) * mm});
            skLineSegment(sketch, "E2444", {"start": v(-60.4, 101.66) * mm, "end": v(-60.49, 101.74) * mm});
            skLineSegment(sketch, "E2445", {"start": v(-60.49, 101.74) * mm, "end": v(-60.68, 101.9) * mm});
            skLineSegment(sketch, "E2446", {"start": v(-60.68, 101.9) * mm, "end": v(-60.78, 101.98) * mm});
            skLineSegment(sketch, "E2447", {"start": v(-60.78, 101.98) * mm, "end": v(-61.08, 102.23) * mm});
            skLineSegment(sketch, "E2448", {"start": v(-61.08, 102.23) * mm, "end": v(-61.18, 102.31) * mm});
            skLineSegment(sketch, "E2449", {"start": v(-61.18, 102.31) * mm, "end": v(-61.4, 102.48) * mm});
            skLineSegment(sketch, "E2450", {"start": v(-61.4, 102.48) * mm, "end": v(-61.5, 102.56) * mm});
            skLineSegment(sketch, "E2451", {"start": v(-61.5, 102.56) * mm, "end": v(-61.6, 102.65) * mm});
            skLineSegment(sketch, "E2452", {"start": v(-61.6, 102.65) * mm, "end": v(-61.72, 102.73) * mm});
            skLineSegment(sketch, "E2453", {"start": v(-61.72, 102.73) * mm, "end": v(-61.83, 102.82) * mm});
            skLineSegment(sketch, "E2454", {"start": v(-61.83, 102.82) * mm, "end": v(-61.94, 102.9) * mm});
            skLineSegment(sketch, "E2455", {"start": v(-61.94, 102.9) * mm, "end": v(-62.05, 103) * mm});
            skLineSegment(sketch, "E2456", {"start": v(-62.05, 103) * mm, "end": v(-62.28, 103.17) * mm});
            skLineSegment(sketch, "E2457", {"start": v(-62.28, 103.17) * mm, "end": v(-62.4, 103.25) * mm});
            skLineSegment(sketch, "E2458", {"start": v(-62.4, 103.25) * mm, "end": v(-62.51, 103.34) * mm});
            skLineSegment(sketch, "E2459", {"start": v(-62.51, 103.34) * mm, "end": v(-62.63, 103.43) * mm});
            skLineSegment(sketch, "E2460", {"start": v(-62.63, 103.43) * mm, "end": v(-62.75, 103.52) * mm});
            skLineSegment(sketch, "E2461", {"start": v(-62.75, 103.52) * mm, "end": v(-62.87, 103.6) * mm});
            skLineSegment(sketch, "E2462", {"start": v(-62.87, 103.6) * mm, "end": v(-62.96, 103.64) * mm});
            skLineSegment(sketch, "E2463", {"start": v(-62.96, 103.64) * mm, "end": v(-64.37, 102.77) * mm});
            skLineSegment(sketch, "E2464", {"start": v(-64.37, 102.77) * mm, "end": v(-64.38, 102.67) * mm});
            skLineSegment(sketch, "E2465", {"start": v(-64.38, 102.67) * mm, "end": v(-64.36, 102.53) * mm});
            skLineSegment(sketch, "E2466", {"start": v(-64.36, 102.53) * mm, "end": v(-64.33, 102.38) * mm});
            skLineSegment(sketch, "E2467", {"start": v(-64.33, 102.38) * mm, "end": v(-64.3, 102.23) * mm});
            skLineSegment(sketch, "E2468", {"start": v(-64.3, 102.23) * mm, "end": v(-64.28, 102.1) * mm});
            skLineSegment(sketch, "E2469", {"start": v(-64.28, 102.1) * mm, "end": v(-64.25, 101.95) * mm});
            skLineSegment(sketch, "E2470", {"start": v(-64.25, 101.95) * mm, "end": v(-64.23, 101.8) * mm});
            skLineSegment(sketch, "E2471", {"start": v(-64.23, 101.8) * mm, "end": v(-64.2, 101.67) * mm});
            skLineSegment(sketch, "E2472", {"start": v(-64.2, 101.67) * mm, "end": v(-64.17, 101.53) * mm});
            skLineSegment(sketch, "E2473", {"start": v(-64.17, 101.53) * mm, "end": v(-64.15, 101.39) * mm});
            skLineSegment(sketch, "E2474", {"start": v(-64.15, 101.39) * mm, "end": v(-64.12, 101.25) * mm});
            skLineSegment(sketch, "E2475", {"start": v(-64.12, 101.25) * mm, "end": v(-64.07, 100.98) * mm});
            skLineSegment(sketch, "E2476", {"start": v(-64.07, 100.98) * mm, "end": v(-64.04, 100.85) * mm});
            skLineSegment(sketch, "E2477", {"start": v(-64.04, 100.85) * mm, "end": v(-64, 100.72) * mm});
            skLineSegment(sketch, "E2478", {"start": v(-64, 100.72) * mm, "end": v(-63.98, 100.59) * mm});
            skLineSegment(sketch, "E2479", {"start": v(-63.98, 100.59) * mm, "end": v(-63.95, 100.46) * mm});
            skLineSegment(sketch, "E2480", {"start": v(-63.95, 100.46) * mm, "end": v(-63.92, 100.33) * mm});
            skLineSegment(sketch, "E2481", {"start": v(-63.92, 100.33) * mm, "end": v(-63.9, 100.2) * mm});
            skLineSegment(sketch, "E2482", {"start": v(-63.9, 100.2) * mm, "end": v(-63.87, 100.08) * mm});
            skLineSegment(sketch, "E2483", {"start": v(-63.87, 100.08) * mm, "end": v(-63.8, 99.83) * mm});
            skLineSegment(sketch, "E2484", {"start": v(-63.8, 99.83) * mm, "end": v(-63.78, 99.7) * mm});
            skLineSegment(sketch, "E2485", {"start": v(-63.78, 99.7) * mm, "end": v(-63.75, 99.59) * mm});
            skLineSegment(sketch, "E2486", {"start": v(-63.75, 99.59) * mm, "end": v(-63.72, 99.47) * mm});
            skLineSegment(sketch, "E2487", {"start": v(-63.72, 99.47) * mm, "end": v(-63.7, 99.35) * mm});
            skLineSegment(sketch, "E2488", {"start": v(-63.7, 99.35) * mm, "end": v(-63.66, 99.23) * mm});
            skLineSegment(sketch, "E2489", {"start": v(-63.66, 99.23) * mm, "end": v(-63.63, 99.12) * mm});
            skLineSegment(sketch, "E2490", {"start": v(-63.63, 99.12) * mm, "end": v(-63.57, 98.89) * mm});
            skLineSegment(sketch, "E2491", {"start": v(-63.57, 98.89) * mm, "end": v(-63.54, 98.78) * mm});
            skLineSegment(sketch, "E2492", {"start": v(-63.54, 98.78) * mm, "end": v(-63.51, 98.66) * mm});
            skLineSegment(sketch, "E2493", {"start": v(-63.51, 98.66) * mm, "end": v(-63.45, 98.45) * mm});
            skLineSegment(sketch, "E2494", {"start": v(-63.45, 98.45) * mm, "end": v(-63.42, 98.34) * mm});
            skLineSegment(sketch, "E2495", {"start": v(-63.42, 98.34) * mm, "end": v(-63.4, 98.23) * mm});
            skLineSegment(sketch, "E2496", {"start": v(-63.4, 98.23) * mm, "end": v(-63.36, 98.13) * mm});
            skLineSegment(sketch, "E2497", {"start": v(-63.36, 98.13) * mm, "end": v(-63.33, 98.02) * mm});
            skLineSegment(sketch, "E2498", {"start": v(-63.33, 98.02) * mm, "end": v(-64.04, 97.35) * mm});
            skLineSegment(sketch, "E2499", {"start": v(-64.04, 97.35) * mm, "end": v(-64.93, 96.97) * mm});
            skLineSegment(sketch, "E2500", {"start": v(-64.93, 96.97) * mm, "end": v(-65.02, 97.04) * mm});
            skLineSegment(sketch, "E2501", {"start": v(-65.02, 97.04) * mm, "end": v(-65.1, 97.1) * mm});
            skLineSegment(sketch, "E2502", {"start": v(-65.1, 97.1) * mm, "end": v(-65.19, 97.18) * mm});
            skLineSegment(sketch, "E2503", {"start": v(-65.19, 97.18) * mm, "end": v(-65.36, 97.32) * mm});
            skLineSegment(sketch, "E2504", {"start": v(-65.36, 97.32) * mm, "end": v(-65.45, 97.39) * mm});
            skLineSegment(sketch, "E2505", {"start": v(-65.45, 97.39) * mm, "end": v(-65.54, 97.46) * mm});
            skLineSegment(sketch, "E2506", {"start": v(-65.54, 97.46) * mm, "end": v(-65.63, 97.53) * mm});
            skLineSegment(sketch, "E2507", {"start": v(-65.63, 97.53) * mm, "end": v(-65.72, 97.6) * mm});
            skLineSegment(sketch, "E2508", {"start": v(-65.72, 97.6) * mm, "end": v(-65.82, 97.68) * mm});
            skLineSegment(sketch, "E2509", {"start": v(-65.82, 97.68) * mm, "end": v(-66, 97.82) * mm});
            skLineSegment(sketch, "E2510", {"start": v(-66, 97.82) * mm, "end": v(-66.1, 97.9) * mm});
            skLineSegment(sketch, "E2511", {"start": v(-66.1, 97.9) * mm, "end": v(-66.3, 98.05) * mm});
            skLineSegment(sketch, "E2512", {"start": v(-66.3, 98.05) * mm, "end": v(-66.4, 98.12) * mm});
            skLineSegment(sketch, "E2513", {"start": v(-66.4, 98.12) * mm, "end": v(-66.5, 98.2) * mm});
            skLineSegment(sketch, "E2514", {"start": v(-66.5, 98.2) * mm, "end": v(-66.6, 98.27) * mm});
            skLineSegment(sketch, "E2515", {"start": v(-66.6, 98.27) * mm, "end": v(-66.7, 98.35) * mm});
            skLineSegment(sketch, "E2516", {"start": v(-66.7, 98.35) * mm, "end": v(-66.82, 98.43) * mm});
            skLineSegment(sketch, "E2517", {"start": v(-66.82, 98.43) * mm, "end": v(-66.92, 98.5) * mm});
            skLineSegment(sketch, "E2518", {"start": v(-66.92, 98.5) * mm, "end": v(-67.03, 98.58) * mm});
            skLineSegment(sketch, "E2519", {"start": v(-67.03, 98.58) * mm, "end": v(-67.14, 98.66) * mm});
            skLineSegment(sketch, "E2520", {"start": v(-67.14, 98.66) * mm, "end": v(-67.36, 98.81) * mm});
            skLineSegment(sketch, "E2521", {"start": v(-67.36, 98.81) * mm, "end": v(-67.58, 98.97) * mm});
            skLineSegment(sketch, "E2522", {"start": v(-67.58, 98.97) * mm, "end": v(-67.7, 99.05) * mm});
            skLineSegment(sketch, "E2523", {"start": v(-67.7, 99.05) * mm, "end": v(-67.82, 99.13) * mm});
            skLineSegment(sketch, "E2524", {"start": v(-67.82, 99.13) * mm, "end": v(-67.93, 99.21) * mm});
            skLineSegment(sketch, "E2525", {"start": v(-67.93, 99.21) * mm, "end": v(-68.05, 99.3) * mm});
            skLineSegment(sketch, "E2526", {"start": v(-68.05, 99.3) * mm, "end": v(-68.3, 99.45) * mm});
            skLineSegment(sketch, "E2527", {"start": v(-68.3, 99.45) * mm, "end": v(-68.41, 99.53) * mm});
            skLineSegment(sketch, "E2528", {"start": v(-68.41, 99.53) * mm, "end": v(-68.66, 99.7) * mm});
            skLineSegment(sketch, "E2529", {"start": v(-68.66, 99.7) * mm, "end": v(-68.79, 99.78) * mm});
            skLineSegment(sketch, "E2530", {"start": v(-68.79, 99.78) * mm, "end": v(-68.88, 99.8) * mm});
            skLineSegment(sketch, "E2531", {"start": v(-68.88, 99.8) * mm, "end": v(-70.24, 98.85) * mm});
            skLineSegment(sketch, "E2532", {"start": v(-70.24, 98.85) * mm, "end": v(-70.24, 98.76) * mm});
            skLineSegment(sketch, "E2533", {"start": v(-70.24, 98.76) * mm, "end": v(-70.2, 98.61) * mm});
            skLineSegment(sketch, "E2534", {"start": v(-70.2, 98.61) * mm, "end": v(-70.18, 98.47) * mm});
            skLineSegment(sketch, "E2535", {"start": v(-70.18, 98.47) * mm, "end": v(-70.1, 98.18) * mm});
            skLineSegment(sketch, "E2536", {"start": v(-70.1, 98.18) * mm, "end": v(-70.07, 98.04) * mm});
            skLineSegment(sketch, "E2537", {"start": v(-70.07, 98.04) * mm, "end": v(-70.04, 97.9) * mm});
            skLineSegment(sketch, "E2538", {"start": v(-70.04, 97.9) * mm, "end": v(-69.97, 97.62) * mm});
            skLineSegment(sketch, "E2539", {"start": v(-69.97, 97.62) * mm, "end": v(-69.93, 97.49) * mm});
            skLineSegment(sketch, "E2540", {"start": v(-69.93, 97.49) * mm, "end": v(-69.9, 97.35) * mm});
            skLineSegment(sketch, "E2541", {"start": v(-69.9, 97.35) * mm, "end": v(-69.86, 97.22) * mm});
            skLineSegment(sketch, "E2542", {"start": v(-69.86, 97.22) * mm, "end": v(-69.83, 97.09) * mm});
            skLineSegment(sketch, "E2543", {"start": v(-69.83, 97.09) * mm, "end": v(-69.76, 96.82) * mm});
            skLineSegment(sketch, "E2544", {"start": v(-69.76, 96.82) * mm, "end": v(-69.72, 96.7) * mm});
            skLineSegment(sketch, "E2545", {"start": v(-69.72, 96.7) * mm, "end": v(-69.69, 96.57) * mm});
            skLineSegment(sketch, "E2546", {"start": v(-69.69, 96.57) * mm, "end": v(-69.65, 96.44) * mm});
            skLineSegment(sketch, "E2547", {"start": v(-69.65, 96.44) * mm, "end": v(-69.61, 96.32) * mm});
            skLineSegment(sketch, "E2548", {"start": v(-69.61, 96.32) * mm, "end": v(-69.58, 96.2) * mm});
            skLineSegment(sketch, "E2549", {"start": v(-69.58, 96.2) * mm, "end": v(-69.54, 96.07) * mm});
            skLineSegment(sketch, "E2550", {"start": v(-69.54, 96.07) * mm, "end": v(-69.5, 95.95) * mm});
            skLineSegment(sketch, "E2551", {"start": v(-69.5, 95.95) * mm, "end": v(-69.47, 95.83) * mm});
            skLineSegment(sketch, "E2552", {"start": v(-69.47, 95.83) * mm, "end": v(-69.43, 95.71) * mm});
            skLineSegment(sketch, "E2553", {"start": v(-69.43, 95.71) * mm, "end": v(-69.4, 95.6) * mm});
            skLineSegment(sketch, "E2554", {"start": v(-69.4, 95.6) * mm, "end": v(-69.36, 95.48) * mm});
            skLineSegment(sketch, "E2555", {"start": v(-69.36, 95.48) * mm, "end": v(-69.32, 95.36) * mm});
            skLineSegment(sketch, "E2556", {"start": v(-69.32, 95.36) * mm, "end": v(-69.29, 95.25) * mm});
            skLineSegment(sketch, "E2557", {"start": v(-69.29, 95.25) * mm, "end": v(-69.25, 95.13) * mm});
            skLineSegment(sketch, "E2558", {"start": v(-69.25, 95.13) * mm, "end": v(-69.21, 95.02) * mm});
            skLineSegment(sketch, "E2559", {"start": v(-69.21, 95.02) * mm, "end": v(-69.18, 94.91) * mm});
            skLineSegment(sketch, "E2560", {"start": v(-69.18, 94.91) * mm, "end": v(-69.14, 94.8) * mm});
            skLineSegment(sketch, "E2561", {"start": v(-69.14, 94.8) * mm, "end": v(-69.1, 94.7) * mm});
            skLineSegment(sketch, "E2562", {"start": v(-69.1, 94.7) * mm, "end": v(-69.07, 94.59) * mm});
            skLineSegment(sketch, "E2563", {"start": v(-69.07, 94.59) * mm, "end": v(-69.03, 94.49) * mm});
            skLineSegment(sketch, "E2564", {"start": v(-69.03, 94.49) * mm, "end": v(-69, 94.38) * mm});
            skLineSegment(sketch, "E2565", {"start": v(-69, 94.38) * mm, "end": v(-68.96, 94.28) * mm});
            skLineSegment(sketch, "E2566", {"start": v(-68.96, 94.28) * mm, "end": v(-68.92, 94.18) * mm});
            skLineSegment(sketch, "E2567", {"start": v(-68.92, 94.18) * mm, "end": v(-69.59, 93.47) * mm});
            skLineSegment(sketch, "E2568", {"start": v(-69.59, 93.47) * mm, "end": v(-70.46, 93.03) * mm});
            skLineSegment(sketch, "E2569", {"start": v(-70.46, 93.03) * mm, "end": v(-70.55, 93.1) * mm});
            skLineSegment(sketch, "E2570", {"start": v(-70.55, 93.1) * mm, "end": v(-70.64, 93.16) * mm});
            skLineSegment(sketch, "E2571", {"start": v(-70.64, 93.16) * mm, "end": v(-70.73, 93.22) * mm});
            skLineSegment(sketch, "E2572", {"start": v(-70.73, 93.22) * mm, "end": v(-70.82, 93.29) * mm});
            skLineSegment(sketch, "E2573", {"start": v(-70.82, 93.29) * mm, "end": v(-70.9, 93.35) * mm});
            skLineSegment(sketch, "E2574", {"start": v(-70.9, 93.35) * mm, "end": v(-71, 93.42) * mm});
            skLineSegment(sketch, "E2575", {"start": v(-71, 93.42) * mm, "end": v(-71.1, 93.48) * mm});
            skLineSegment(sketch, "E2576", {"start": v(-71.1, 93.48) * mm, "end": v(-71.2, 93.55) * mm});
            skLineSegment(sketch, "E2577", {"start": v(-71.2, 93.55) * mm, "end": v(-71.29, 93.62) * mm});
            skLineSegment(sketch, "E2578", {"start": v(-71.29, 93.62) * mm, "end": v(-71.48, 93.75) * mm});
            skLineSegment(sketch, "E2579", {"start": v(-71.48, 93.75) * mm, "end": v(-71.58, 93.82) * mm});
            skLineSegment(sketch, "E2580", {"start": v(-71.58, 93.82) * mm, "end": v(-71.68, 93.9) * mm});
            skLineSegment(sketch, "E2581", {"start": v(-71.68, 93.9) * mm, "end": v(-71.79, 93.96) * mm});
            skLineSegment(sketch, "E2582", {"start": v(-71.79, 93.96) * mm, "end": v(-71.89, 94.03) * mm});
            skLineSegment(sketch, "E2583", {"start": v(-71.89, 94.03) * mm, "end": v(-72, 94.1) * mm});
            skLineSegment(sketch, "E2584", {"start": v(-72, 94.1) * mm, "end": v(-72.1, 94.17) * mm});
            skLineSegment(sketch, "E2585", {"start": v(-72.1, 94.17) * mm, "end": v(-72.2, 94.23) * mm});
            skLineSegment(sketch, "E2586", {"start": v(-72.2, 94.23) * mm, "end": v(-72.32, 94.3) * mm});
            skLineSegment(sketch, "E2587", {"start": v(-72.32, 94.3) * mm, "end": v(-72.54, 94.45) * mm});
            skLineSegment(sketch, "E2588", {"start": v(-72.54, 94.45) * mm, "end": v(-72.65, 94.52) * mm});
            skLineSegment(sketch, "E2589", {"start": v(-72.65, 94.52) * mm, "end": v(-72.76, 94.59) * mm});
            skLineSegment(sketch, "E2590", {"start": v(-72.76, 94.59) * mm, "end": v(-72.87, 94.66) * mm});
            skLineSegment(sketch, "E2591", {"start": v(-72.87, 94.66) * mm, "end": v(-73, 94.73) * mm});
            skLineSegment(sketch, "E2592", {"start": v(-73, 94.73) * mm, "end": v(-73.1, 94.8) * mm});
            skLineSegment(sketch, "E2593", {"start": v(-73.1, 94.8) * mm, "end": v(-73.22, 94.88) * mm});
            skLineSegment(sketch, "E2594", {"start": v(-73.22, 94.88) * mm, "end": v(-73.34, 94.95) * mm});
            skLineSegment(sketch, "E2595", {"start": v(-73.34, 94.95) * mm, "end": v(-73.46, 95.02) * mm});
            skLineSegment(sketch, "E2596", {"start": v(-73.46, 95.02) * mm, "end": v(-73.59, 95.1) * mm});
            skLineSegment(sketch, "E2597", {"start": v(-73.59, 95.1) * mm, "end": v(-73.83, 95.24) * mm});
            skLineSegment(sketch, "E2598", {"start": v(-73.83, 95.24) * mm, "end": v(-73.96, 95.31) * mm});
            skLineSegment(sketch, "E2599", {"start": v(-73.96, 95.31) * mm, "end": v(-74.09, 95.39) * mm});
            skLineSegment(sketch, "E2600", {"start": v(-74.09, 95.39) * mm, "end": v(-74.21, 95.46) * mm});
            skLineSegment(sketch, "E2601", {"start": v(-74.21, 95.46) * mm, "end": v(-74.34, 95.53) * mm});
            skLineSegment(sketch, "E2602", {"start": v(-74.34, 95.53) * mm, "end": v(-74.47, 95.6) * mm});
            skLineSegment(sketch, "E2603", {"start": v(-74.47, 95.6) * mm, "end": v(-74.57, 95.63) * mm});
            skLineSegment(sketch, "E2604", {"start": v(-74.57, 95.63) * mm, "end": v(-75.87, 94.6) * mm});
            skLineSegment(sketch, "E2605", {"start": v(-75.87, 94.6) * mm, "end": v(-75.87, 94.5) * mm});
            skLineSegment(sketch, "E2606", {"start": v(-75.87, 94.5) * mm, "end": v(-75.82, 94.36) * mm});
            skLineSegment(sketch, "E2607", {"start": v(-75.82, 94.36) * mm, "end": v(-75.78, 94.22) * mm});
            skLineSegment(sketch, "E2608", {"start": v(-75.78, 94.22) * mm, "end": v(-75.74, 94.08) * mm});
            skLineSegment(sketch, "E2609", {"start": v(-75.74, 94.08) * mm, "end": v(-75.65, 93.8) * mm});
            skLineSegment(sketch, "E2610", {"start": v(-75.65, 93.8) * mm, "end": v(-75.61, 93.66) * mm});
            skLineSegment(sketch, "E2611", {"start": v(-75.61, 93.66) * mm, "end": v(-75.57, 93.52) * mm});
            skLineSegment(sketch, "E2612", {"start": v(-75.57, 93.52) * mm, "end": v(-75.53, 93.39) * mm});
            skLineSegment(sketch, "E2613", {"start": v(-75.53, 93.39) * mm, "end": v(-75.44, 93.12) * mm});
            skLineSegment(sketch, "E2614", {"start": v(-75.44, 93.12) * mm, "end": v(-75.36, 92.86) * mm});
            skLineSegment(sketch, "E2615", {"start": v(-75.36, 92.86) * mm, "end": v(-75.31, 92.73) * mm});
            skLineSegment(sketch, "E2616", {"start": v(-75.31, 92.73) * mm, "end": v(-75.27, 92.6) * mm});
            skLineSegment(sketch, "E2617", {"start": v(-75.27, 92.6) * mm, "end": v(-75.23, 92.48) * mm});
            skLineSegment(sketch, "E2618", {"start": v(-75.23, 92.48) * mm, "end": v(-75.18, 92.35) * mm});
            skLineSegment(sketch, "E2619", {"start": v(-75.18, 92.35) * mm, "end": v(-75.14, 92.23) * mm});
            skLineSegment(sketch, "E2620", {"start": v(-75.14, 92.23) * mm, "end": v(-75.05, 91.98) * mm});
            skLineSegment(sketch, "E2621", {"start": v(-75.05, 91.98) * mm, "end": v(-75, 91.86) * mm});
            skLineSegment(sketch, "E2622", {"start": v(-75, 91.86) * mm, "end": v(-74.92, 91.63) * mm});
            skLineSegment(sketch, "E2623", {"start": v(-74.92, 91.63) * mm, "end": v(-74.88, 91.51) * mm});
            skLineSegment(sketch, "E2624", {"start": v(-74.88, 91.51) * mm, "end": v(-74.84, 91.4) * mm});
            skLineSegment(sketch, "E2625", {"start": v(-74.84, 91.4) * mm, "end": v(-74.8, 91.28) * mm});
            skLineSegment(sketch, "E2626", {"start": v(-74.8, 91.28) * mm, "end": v(-74.75, 91.17) * mm});
            skLineSegment(sketch, "E2627", {"start": v(-74.75, 91.17) * mm, "end": v(-74.7, 91.06) * mm});
            skLineSegment(sketch, "E2628", {"start": v(-74.7, 91.06) * mm, "end": v(-74.62, 90.84) * mm});
            skLineSegment(sketch, "E2629", {"start": v(-74.62, 90.84) * mm, "end": v(-74.58, 90.73) * mm});
            skLineSegment(sketch, "E2630", {"start": v(-74.58, 90.73) * mm, "end": v(-74.5, 90.52) * mm});
            skLineSegment(sketch, "E2631", {"start": v(-74.5, 90.52) * mm, "end": v(-74.45, 90.41) * mm});
            skLineSegment(sketch, "E2632", {"start": v(-74.45, 90.41) * mm, "end": v(-74.41, 90.31) * mm});
            skLineSegment(sketch, "E2633", {"start": v(-74.41, 90.31) * mm, "end": v(-74.37, 90.2) * mm});
            skLineSegment(sketch, "E2634", {"start": v(-74.37, 90.2) * mm, "end": v(-74.32, 90.1) * mm});
            skLineSegment(sketch, "E2635", {"start": v(-74.32, 90.1) * mm, "end": v(-74.28, 90) * mm});
            skLineSegment(sketch, "E2636", {"start": v(-74.28, 90) * mm, "end": v(-74.9, 89.26) * mm});
            skLineSegment(sketch, "E2637", {"start": v(-74.9, 89.26) * mm, "end": v(-75.75, 88.78) * mm});
            skLineSegment(sketch, "E2638", {"start": v(-75.75, 88.78) * mm, "end": v(-75.84, 88.84) * mm});
            skLineSegment(sketch, "E2639", {"start": v(-75.84, 88.84) * mm, "end": v(-75.93, 88.9) * mm});
            skLineSegment(sketch, "E2640", {"start": v(-75.93, 88.9) * mm, "end": v(-76.03, 88.95) * mm});
            skLineSegment(sketch, "E2641", {"start": v(-76.03, 88.95) * mm, "end": v(-76.12, 89.01) * mm});
            skLineSegment(sketch, "E2642", {"start": v(-76.12, 89.01) * mm, "end": v(-76.22, 89.07) * mm});
            skLineSegment(sketch, "E2643", {"start": v(-76.22, 89.07) * mm, "end": v(-76.31, 89.13) * mm});
            skLineSegment(sketch, "E2644", {"start": v(-76.31, 89.13) * mm, "end": v(-76.41, 89.2) * mm});
            skLineSegment(sketch, "E2645", {"start": v(-76.41, 89.2) * mm, "end": v(-76.6, 89.31) * mm});
            skLineSegment(sketch, "E2646", {"start": v(-76.6, 89.31) * mm, "end": v(-76.81, 89.44) * mm});
            skLineSegment(sketch, "E2647", {"start": v(-76.81, 89.44) * mm, "end": v(-76.92, 89.5) * mm});
            skLineSegment(sketch, "E2648", {"start": v(-76.92, 89.5) * mm, "end": v(-77.02, 89.56) * mm});
            skLineSegment(sketch, "E2649", {"start": v(-77.02, 89.56) * mm, "end": v(-77.13, 89.62) * mm});
            skLineSegment(sketch, "E2650", {"start": v(-77.13, 89.62) * mm, "end": v(-77.24, 89.69) * mm});
            skLineSegment(sketch, "E2651", {"start": v(-77.24, 89.69) * mm, "end": v(-77.34, 89.75) * mm});
            skLineSegment(sketch, "E2652", {"start": v(-77.34, 89.75) * mm, "end": v(-77.56, 89.88) * mm});
            skLineSegment(sketch, "E2653", {"start": v(-77.56, 89.88) * mm, "end": v(-77.68, 89.94) * mm});
            skLineSegment(sketch, "E2654", {"start": v(-77.68, 89.94) * mm, "end": v(-77.8, 90) * mm});
            skLineSegment(sketch, "E2655", {"start": v(-77.8, 90) * mm, "end": v(-77.9, 90.07) * mm});
            skLineSegment(sketch, "E2656", {"start": v(-77.9, 90.07) * mm, "end": v(-78.02, 90.13) * mm});
            skLineSegment(sketch, "E2657", {"start": v(-78.02, 90.13) * mm, "end": v(-78.14, 90.2) * mm});
            skLineSegment(sketch, "E2658", {"start": v(-78.14, 90.2) * mm, "end": v(-78.37, 90.33) * mm});
            skLineSegment(sketch, "E2659", {"start": v(-78.37, 90.33) * mm, "end": v(-78.5, 90.4) * mm});
            skLineSegment(sketch, "E2660", {"start": v(-78.5, 90.4) * mm, "end": v(-78.62, 90.46) * mm});
            skLineSegment(sketch, "E2661", {"start": v(-78.62, 90.46) * mm, "end": v(-78.87, 90.59) * mm});
            skLineSegment(sketch, "E2662", {"start": v(-78.87, 90.59) * mm, "end": v(-79, 90.65) * mm});
            skLineSegment(sketch, "E2663", {"start": v(-79, 90.65) * mm, "end": v(-79.12, 90.72) * mm});
            skLineSegment(sketch, "E2664", {"start": v(-79.12, 90.72) * mm, "end": v(-79.25, 90.78) * mm});
            skLineSegment(sketch, "E2665", {"start": v(-79.25, 90.78) * mm, "end": v(-79.5, 90.92) * mm});
            skLineSegment(sketch, "E2666", {"start": v(-79.5, 90.92) * mm, "end": v(-79.64, 90.98) * mm});
            skLineSegment(sketch, "E2667", {"start": v(-79.64, 90.98) * mm, "end": v(-79.9, 91.11) * mm});
            skLineSegment(sketch, "E2668", {"start": v(-79.9, 91.11) * mm, "end": v(-80, 91.14) * mm});
            skLineSegment(sketch, "E2669", {"start": v(-80, 91.14) * mm, "end": v(-81.24, 90.03) * mm});
            skLineSegment(sketch, "E2670", {"start": v(-81.24, 90.03) * mm, "end": v(-81.23, 89.94) * mm});
            skLineSegment(sketch, "E2671", {"start": v(-81.23, 89.94) * mm, "end": v(-81.18, 89.8) * mm});
            skLineSegment(sketch, "E2672", {"start": v(-81.18, 89.8) * mm, "end": v(-81.13, 89.65) * mm});
            skLineSegment(sketch, "E2673", {"start": v(-81.13, 89.65) * mm, "end": v(-81.08, 89.51) * mm});
            skLineSegment(sketch, "E2674", {"start": v(-81.08, 89.51) * mm, "end": v(-81.03, 89.38) * mm});
            skLineSegment(sketch, "E2675", {"start": v(-81.03, 89.38) * mm, "end": v(-80.98, 89.24) * mm});
            skLineSegment(sketch, "E2676", {"start": v(-80.98, 89.24) * mm, "end": v(-80.93, 89.1) * mm});
            skLineSegment(sketch, "E2677", {"start": v(-80.93, 89.1) * mm, "end": v(-80.88, 88.97) * mm});
            skLineSegment(sketch, "E2678", {"start": v(-80.88, 88.97) * mm, "end": v(-80.83, 88.84) * mm});
            skLineSegment(sketch, "E2679", {"start": v(-80.83, 88.84) * mm, "end": v(-80.78, 88.7) * mm});
            skLineSegment(sketch, "E2680", {"start": v(-80.78, 88.7) * mm, "end": v(-80.73, 88.58) * mm});
            skLineSegment(sketch, "E2681", {"start": v(-80.73, 88.58) * mm, "end": v(-80.68, 88.45) * mm});
            skLineSegment(sketch, "E2682", {"start": v(-80.68, 88.45) * mm, "end": v(-80.63, 88.32) * mm});
            skLineSegment(sketch, "E2683", {"start": v(-80.63, 88.32) * mm, "end": v(-80.58, 88.2) * mm});
            skLineSegment(sketch, "E2684", {"start": v(-80.58, 88.2) * mm, "end": v(-80.53, 88.07) * mm});
            skLineSegment(sketch, "E2685", {"start": v(-80.53, 88.07) * mm, "end": v(-80.48, 87.95) * mm});
            skLineSegment(sketch, "E2686", {"start": v(-80.48, 87.95) * mm, "end": v(-80.43, 87.83) * mm});
            skLineSegment(sketch, "E2687", {"start": v(-80.43, 87.83) * mm, "end": v(-80.37, 87.7) * mm});
            skLineSegment(sketch, "E2688", {"start": v(-80.37, 87.7) * mm, "end": v(-80.32, 87.58) * mm});
            skLineSegment(sketch, "E2689", {"start": v(-80.32, 87.58) * mm, "end": v(-80.27, 87.47) * mm});
            skLineSegment(sketch, "E2690", {"start": v(-80.27, 87.47) * mm, "end": v(-80.22, 87.35) * mm});
            skLineSegment(sketch, "E2691", {"start": v(-80.22, 87.35) * mm, "end": v(-80.17, 87.23) * mm});
            skLineSegment(sketch, "E2692", {"start": v(-80.17, 87.23) * mm, "end": v(-80.12, 87.12) * mm});
            skLineSegment(sketch, "E2693", {"start": v(-80.12, 87.12) * mm, "end": v(-80.07, 87) * mm});
            skLineSegment(sketch, "E2694", {"start": v(-80.07, 87) * mm, "end": v(-80.02, 86.89) * mm});
            skLineSegment(sketch, "E2695", {"start": v(-80.02, 86.89) * mm, "end": v(-79.92, 86.67) * mm});
            skLineSegment(sketch, "E2696", {"start": v(-79.92, 86.67) * mm, "end": v(-79.88, 86.56) * mm});
            skLineSegment(sketch, "E2697", {"start": v(-79.88, 86.56) * mm, "end": v(-79.78, 86.35) * mm});
            skLineSegment(sketch, "E2698", {"start": v(-79.78, 86.35) * mm, "end": v(-79.73, 86.24) * mm});
            skLineSegment(sketch, "E2699", {"start": v(-79.73, 86.24) * mm, "end": v(-79.68, 86.14) * mm});
            skLineSegment(sketch, "E2700", {"start": v(-79.68, 86.14) * mm, "end": v(-79.58, 85.93) * mm});
            skLineSegment(sketch, "E2701", {"start": v(-79.58, 85.93) * mm, "end": v(-79.53, 85.83) * mm});
            skLineSegment(sketch, "E2702", {"start": v(-79.53, 85.83) * mm, "end": v(-79.49, 85.73) * mm});
            skLineSegment(sketch, "E2703", {"start": v(-79.49, 85.73) * mm, "end": v(-79.44, 85.63) * mm});
            skLineSegment(sketch, "E2704", {"start": v(-79.44, 85.63) * mm, "end": v(-79.4, 85.54) * mm});
            skLineSegment(sketch, "E2705", {"start": v(-79.4, 85.54) * mm, "end": v(-79.97, 84.75) * mm});
            skLineSegment(sketch, "E2706", {"start": v(-79.97, 84.75) * mm, "end": v(-80.79, 84.22) * mm});
            skLineSegment(sketch, "E2707", {"start": v(-80.79, 84.22) * mm, "end": v(-80.88, 84.27) * mm});
            skLineSegment(sketch, "E2708", {"start": v(-80.88, 84.27) * mm, "end": v(-80.97, 84.33) * mm});
            skLineSegment(sketch, "E2709", {"start": v(-80.97, 84.33) * mm, "end": v(-81.07, 84.38) * mm});
            skLineSegment(sketch, "E2710", {"start": v(-81.07, 84.38) * mm, "end": v(-81.17, 84.44) * mm});
            skLineSegment(sketch, "E2711", {"start": v(-81.17, 84.44) * mm, "end": v(-81.27, 84.5) * mm});
            skLineSegment(sketch, "E2712", {"start": v(-81.27, 84.5) * mm, "end": v(-81.37, 84.54) * mm});
            skLineSegment(sketch, "E2713", {"start": v(-81.37, 84.54) * mm, "end": v(-81.57, 84.65) * mm});
            skLineSegment(sketch, "E2714", {"start": v(-81.57, 84.65) * mm, "end": v(-81.67, 84.7) * mm});
            skLineSegment(sketch, "E2715", {"start": v(-81.67, 84.7) * mm, "end": v(-81.78, 84.76) * mm});
            skLineSegment(sketch, "E2716", {"start": v(-81.78, 84.76) * mm, "end": v(-81.88, 84.82) * mm});
            skLineSegment(sketch, "E2717", {"start": v(-81.88, 84.82) * mm, "end": v(-82, 84.88) * mm});
            skLineSegment(sketch, "E2718", {"start": v(-82, 84.88) * mm, "end": v(-82.2, 84.99) * mm});
            skLineSegment(sketch, "E2719", {"start": v(-82.2, 84.99) * mm, "end": v(-82.32, 85.04) * mm});
            skLineSegment(sketch, "E2720", {"start": v(-82.32, 85.04) * mm, "end": v(-82.43, 85.1) * mm});
            skLineSegment(sketch, "E2721", {"start": v(-82.43, 85.1) * mm, "end": v(-82.54, 85.16) * mm});
            skLineSegment(sketch, "E2722", {"start": v(-82.54, 85.16) * mm, "end": v(-82.66, 85.22) * mm});
            skLineSegment(sketch, "E2723", {"start": v(-82.66, 85.22) * mm, "end": v(-82.77, 85.27) * mm});
            skLineSegment(sketch, "E2724", {"start": v(-82.77, 85.27) * mm, "end": v(-82.9, 85.33) * mm});
            skLineSegment(sketch, "E2725", {"start": v(-82.9, 85.33) * mm, "end": v(-83.01, 85.39) * mm});
            skLineSegment(sketch, "E2726", {"start": v(-83.01, 85.39) * mm, "end": v(-83.13, 85.44) * mm});
            skLineSegment(sketch, "E2727", {"start": v(-83.13, 85.44) * mm, "end": v(-83.25, 85.5) * mm});
            skLineSegment(sketch, "E2728", {"start": v(-83.25, 85.5) * mm, "end": v(-83.37, 85.56) * mm});
            skLineSegment(sketch, "E2729", {"start": v(-83.37, 85.56) * mm, "end": v(-83.5, 85.62) * mm});
            skLineSegment(sketch, "E2730", {"start": v(-83.5, 85.62) * mm, "end": v(-83.74, 85.73) * mm});
            skLineSegment(sketch, "E2731", {"start": v(-83.74, 85.73) * mm, "end": v(-83.87, 85.8) * mm});
            skLineSegment(sketch, "E2732", {"start": v(-83.87, 85.8) * mm, "end": v(-84, 85.85) * mm});
            skLineSegment(sketch, "E2733", {"start": v(-84, 85.85) * mm, "end": v(-84.13, 85.9) * mm});
            skLineSegment(sketch, "E2734", {"start": v(-84.13, 85.9) * mm, "end": v(-84.26, 85.96) * mm});
            skLineSegment(sketch, "E2735", {"start": v(-84.26, 85.96) * mm, "end": v(-84.52, 86.08) * mm});
            skLineSegment(sketch, "E2736", {"start": v(-84.52, 86.08) * mm, "end": v(-84.66, 86.14) * mm});
            skLineSegment(sketch, "E2737", {"start": v(-84.66, 86.14) * mm, "end": v(-84.8, 86.2) * mm});
            skLineSegment(sketch, "E2738", {"start": v(-84.8, 86.2) * mm, "end": v(-84.93, 86.26) * mm});
            skLineSegment(sketch, "E2739", {"start": v(-84.93, 86.26) * mm, "end": v(-85.07, 86.31) * mm});
            skLineSegment(sketch, "E2740", {"start": v(-85.07, 86.31) * mm, "end": v(-85.17, 86.33) * mm});
            skLineSegment(sketch, "E2741", {"start": v(-85.17, 86.33) * mm, "end": v(-86.34, 85.16) * mm});
            skLineSegment(sketch, "E2742", {"start": v(-86.34, 85.16) * mm, "end": v(-86.32, 85.06) * mm});
            skLineSegment(sketch, "E2743", {"start": v(-86.32, 85.06) * mm, "end": v(-86.27, 84.92) * mm});
            skLineSegment(sketch, "E2744", {"start": v(-86.27, 84.92) * mm, "end": v(-86.2, 84.78) * mm});
            skLineSegment(sketch, "E2745", {"start": v(-86.2, 84.78) * mm, "end": v(-86.15, 84.65) * mm});
            skLineSegment(sketch, "E2746", {"start": v(-86.15, 84.65) * mm, "end": v(-86.1, 84.51) * mm});
            skLineSegment(sketch, "E2747", {"start": v(-86.1, 84.51) * mm, "end": v(-86.03, 84.38) * mm});
            skLineSegment(sketch, "E2748", {"start": v(-86.03, 84.38) * mm, "end": v(-85.97, 84.25) * mm});
            skLineSegment(sketch, "E2749", {"start": v(-85.97, 84.25) * mm, "end": v(-85.92, 84.12) * mm});
            skLineSegment(sketch, "E2750", {"start": v(-85.92, 84.12) * mm, "end": v(-85.86, 83.99) * mm});
            skLineSegment(sketch, "E2751", {"start": v(-85.86, 83.99) * mm, "end": v(-85.8, 83.86) * mm});
            skLineSegment(sketch, "E2752", {"start": v(-85.8, 83.86) * mm, "end": v(-85.74, 83.73) * mm});
            skLineSegment(sketch, "E2753", {"start": v(-85.74, 83.73) * mm, "end": v(-85.68, 83.6) * mm});
            skLineSegment(sketch, "E2754", {"start": v(-85.68, 83.6) * mm, "end": v(-85.57, 83.36) * mm});
            skLineSegment(sketch, "E2755", {"start": v(-85.57, 83.36) * mm, "end": v(-85.51, 83.24) * mm});
            skLineSegment(sketch, "E2756", {"start": v(-85.51, 83.24) * mm, "end": v(-85.45, 83.12) * mm});
            skLineSegment(sketch, "E2757", {"start": v(-85.45, 83.12) * mm, "end": v(-85.34, 82.88) * mm});
            skLineSegment(sketch, "E2758", {"start": v(-85.34, 82.88) * mm, "end": v(-85.28, 82.76) * mm});
            skLineSegment(sketch, "E2759", {"start": v(-85.28, 82.76) * mm, "end": v(-85.22, 82.65) * mm});
            skLineSegment(sketch, "E2760", {"start": v(-85.22, 82.65) * mm, "end": v(-85.17, 82.53) * mm});
            skLineSegment(sketch, "E2761", {"start": v(-85.17, 82.53) * mm, "end": v(-85.11, 82.42) * mm});
            skLineSegment(sketch, "E2762", {"start": v(-85.11, 82.42) * mm, "end": v(-85.05, 82.31) * mm});
            skLineSegment(sketch, "E2763", {"start": v(-85.05, 82.31) * mm, "end": v(-84.94, 82.09) * mm});
            skLineSegment(sketch, "E2764", {"start": v(-84.94, 82.09) * mm, "end": v(-84.89, 81.98) * mm});
            skLineSegment(sketch, "E2765", {"start": v(-84.89, 81.98) * mm, "end": v(-84.83, 81.87) * mm});
            skLineSegment(sketch, "E2766", {"start": v(-84.83, 81.87) * mm, "end": v(-84.77, 81.77) * mm});
            skLineSegment(sketch, "E2767", {"start": v(-84.77, 81.77) * mm, "end": v(-84.72, 81.66) * mm});
            skLineSegment(sketch, "E2768", {"start": v(-84.72, 81.66) * mm, "end": v(-84.66, 81.56) * mm});
            skLineSegment(sketch, "E2769", {"start": v(-84.66, 81.56) * mm, "end": v(-84.6, 81.46) * mm});
            skLineSegment(sketch, "E2770", {"start": v(-84.6, 81.46) * mm, "end": v(-84.5, 81.26) * mm});
            skLineSegment(sketch, "E2771", {"start": v(-84.5, 81.26) * mm, "end": v(-84.4, 81.06) * mm});
            skLineSegment(sketch, "E2772", {"start": v(-84.4, 81.06) * mm, "end": v(-84.34, 80.97) * mm});
            skLineSegment(sketch, "E2773", {"start": v(-84.34, 80.97) * mm, "end": v(-84.28, 80.87) * mm});
            skLineSegment(sketch, "E2774", {"start": v(-84.28, 80.87) * mm, "end": v(-84.23, 80.78) * mm});
            skLineSegment(sketch, "E2775", {"start": v(-84.23, 80.78) * mm, "end": v(-84.76, 79.96) * mm});
            skLineSegment(sketch, "E2776", {"start": v(-84.76, 79.96) * mm, "end": v(-85.55, 79.38) * mm});
            skLineSegment(sketch, "E2777", {"start": v(-85.55, 79.38) * mm, "end": v(-85.64, 79.43) * mm});
            skLineSegment(sketch, "E2778", {"start": v(-85.64, 79.43) * mm, "end": v(-85.74, 79.48) * mm});
            skLineSegment(sketch, "E2779", {"start": v(-85.74, 79.48) * mm, "end": v(-85.84, 79.53) * mm});
            skLineSegment(sketch, "E2780", {"start": v(-85.84, 79.53) * mm, "end": v(-86.04, 79.62) * mm});
            skLineSegment(sketch, "E2781", {"start": v(-86.04, 79.62) * mm, "end": v(-86.15, 79.67) * mm});
            skLineSegment(sketch, "E2782", {"start": v(-86.15, 79.67) * mm, "end": v(-86.25, 79.72) * mm});
            skLineSegment(sketch, "E2783", {"start": v(-86.25, 79.72) * mm, "end": v(-86.35, 79.77) * mm});
            skLineSegment(sketch, "E2784", {"start": v(-86.35, 79.77) * mm, "end": v(-86.46, 79.82) * mm});
            skLineSegment(sketch, "E2785", {"start": v(-86.46, 79.82) * mm, "end": v(-86.57, 79.87) * mm});
            skLineSegment(sketch, "E2786", {"start": v(-86.57, 79.87) * mm, "end": v(-86.68, 79.92) * mm});
            skLineSegment(sketch, "E2787", {"start": v(-86.68, 79.92) * mm, "end": v(-86.79, 79.96) * mm});
            skLineSegment(sketch, "E2788", {"start": v(-86.79, 79.96) * mm, "end": v(-86.9, 80.01) * mm});
            skLineSegment(sketch, "E2789", {"start": v(-86.9, 80.01) * mm, "end": v(-87.01, 80.07) * mm});
            skLineSegment(sketch, "E2790", {"start": v(-87.01, 80.07) * mm, "end": v(-87.13, 80.12) * mm});
            skLineSegment(sketch, "E2791", {"start": v(-87.13, 80.12) * mm, "end": v(-87.36, 80.21) * mm});
            skLineSegment(sketch, "E2792", {"start": v(-87.36, 80.21) * mm, "end": v(-87.47, 80.27) * mm});
            skLineSegment(sketch, "E2793", {"start": v(-87.47, 80.27) * mm, "end": v(-87.6, 80.31) * mm});
            skLineSegment(sketch, "E2794", {"start": v(-87.6, 80.31) * mm, "end": v(-87.71, 80.36) * mm});
            skLineSegment(sketch, "E2795", {"start": v(-87.71, 80.36) * mm, "end": v(-87.83, 80.42) * mm});
            skLineSegment(sketch, "E2796", {"start": v(-87.83, 80.42) * mm, "end": v(-87.96, 80.47) * mm});
            skLineSegment(sketch, "E2797", {"start": v(-87.96, 80.47) * mm, "end": v(-88.08, 80.52) * mm});
            skLineSegment(sketch, "E2798", {"start": v(-88.08, 80.52) * mm, "end": v(-88.2, 80.57) * mm});
            skLineSegment(sketch, "E2799", {"start": v(-88.2, 80.57) * mm, "end": v(-88.33, 80.62) * mm});
            skLineSegment(sketch, "E2800", {"start": v(-88.33, 80.62) * mm, "end": v(-88.59, 80.72) * mm});
            skLineSegment(sketch, "E2801", {"start": v(-88.59, 80.72) * mm, "end": v(-88.72, 80.77) * mm});
            skLineSegment(sketch, "E2802", {"start": v(-88.72, 80.77) * mm, "end": v(-88.85, 80.82) * mm});
            skLineSegment(sketch, "E2803", {"start": v(-88.85, 80.82) * mm, "end": v(-88.98, 80.87) * mm});
            skLineSegment(sketch, "E2804", {"start": v(-88.98, 80.87) * mm, "end": v(-89.11, 80.92) * mm});
            skLineSegment(sketch, "E2805", {"start": v(-89.11, 80.92) * mm, "end": v(-89.25, 80.97) * mm});
            skLineSegment(sketch, "E2806", {"start": v(-89.25, 80.97) * mm, "end": v(-89.39, 81.02) * mm});
            skLineSegment(sketch, "E2807", {"start": v(-89.39, 81.02) * mm, "end": v(-89.66, 81.12) * mm});
            skLineSegment(sketch, "E2808", {"start": v(-89.66, 81.12) * mm, "end": v(-89.94, 81.22) * mm});
            skLineSegment(sketch, "E2809", {"start": v(-89.94, 81.22) * mm, "end": v(-90.04, 81.23) * mm});
            skLineSegment(sketch, "E2810", {"start": v(-90.04, 81.23) * mm, "end": v(-91.14, 80) * mm});
            skLineSegment(sketch, "E2811", {"start": v(-91.14, 80) * mm, "end": v(-91.12, 79.9) * mm});
            skLineSegment(sketch, "E2812", {"start": v(-91.12, 79.9) * mm, "end": v(-91.06, 79.76) * mm});
            skLineSegment(sketch, "E2813", {"start": v(-91.06, 79.76) * mm, "end": v(-91, 79.63) * mm});
            skLineSegment(sketch, "E2814", {"start": v(-91, 79.63) * mm, "end": v(-90.92, 79.5) * mm});
            skLineSegment(sketch, "E2815", {"start": v(-90.92, 79.5) * mm, "end": v(-90.86, 79.37) * mm});
            skLineSegment(sketch, "E2816", {"start": v(-90.86, 79.37) * mm, "end": v(-90.8, 79.24) * mm});
            skLineSegment(sketch, "E2817", {"start": v(-90.8, 79.24) * mm, "end": v(-90.73, 79.1) * mm});
            skLineSegment(sketch, "E2818", {"start": v(-90.73, 79.1) * mm, "end": v(-90.66, 78.98) * mm});
            skLineSegment(sketch, "E2819", {"start": v(-90.66, 78.98) * mm, "end": v(-90.6, 78.86) * mm});
            skLineSegment(sketch, "E2820", {"start": v(-90.6, 78.86) * mm, "end": v(-90.53, 78.73) * mm});
            skLineSegment(sketch, "E2821", {"start": v(-90.53, 78.73) * mm, "end": v(-90.47, 78.6) * mm});
            skLineSegment(sketch, "E2822", {"start": v(-90.47, 78.6) * mm, "end": v(-90.4, 78.49) * mm});
            skLineSegment(sketch, "E2823", {"start": v(-90.4, 78.49) * mm, "end": v(-90.33, 78.37) * mm});
            skLineSegment(sketch, "E2824", {"start": v(-90.33, 78.37) * mm, "end": v(-90.27, 78.24) * mm});
            skLineSegment(sketch, "E2825", {"start": v(-90.27, 78.24) * mm, "end": v(-90.2, 78.13) * mm});
            skLineSegment(sketch, "E2826", {"start": v(-90.2, 78.13) * mm, "end": v(-90.14, 78.01) * mm});
            skLineSegment(sketch, "E2827", {"start": v(-90.14, 78.01) * mm, "end": v(-90.08, 77.9) * mm});
            skLineSegment(sketch, "E2828", {"start": v(-90.08, 77.9) * mm, "end": v(-90.01, 77.78) * mm});
            skLineSegment(sketch, "E2829", {"start": v(-90.01, 77.78) * mm, "end": v(-89.95, 77.67) * mm});
            skLineSegment(sketch, "E2830", {"start": v(-89.95, 77.67) * mm, "end": v(-89.82, 77.44) * mm});
            skLineSegment(sketch, "E2831", {"start": v(-89.82, 77.44) * mm, "end": v(-89.76, 77.33) * mm});
            skLineSegment(sketch, "E2832", {"start": v(-89.76, 77.33) * mm, "end": v(-89.7, 77.23) * mm});
            skLineSegment(sketch, "E2833", {"start": v(-89.7, 77.23) * mm, "end": v(-89.63, 77.12) * mm});
            skLineSegment(sketch, "E2834", {"start": v(-89.63, 77.12) * mm, "end": v(-89.57, 77.01) * mm});
            skLineSegment(sketch, "E2835", {"start": v(-89.57, 77.01) * mm, "end": v(-89.5, 76.9) * mm});
            skLineSegment(sketch, "E2836", {"start": v(-89.5, 76.9) * mm, "end": v(-89.45, 76.8) * mm});
            skLineSegment(sketch, "E2837", {"start": v(-89.45, 76.8) * mm, "end": v(-89.32, 76.6) * mm});
            skLineSegment(sketch, "E2838", {"start": v(-89.32, 76.6) * mm, "end": v(-89.2, 76.4) * mm});
            skLineSegment(sketch, "E2839", {"start": v(-89.2, 76.4) * mm, "end": v(-89.14, 76.3) * mm});
            skLineSegment(sketch, "E2840", {"start": v(-89.14, 76.3) * mm, "end": v(-89.08, 76.2) * mm});
            skLineSegment(sketch, "E2841", {"start": v(-89.08, 76.2) * mm, "end": v(-89.02, 76.11) * mm});
            skLineSegment(sketch, "E2842", {"start": v(-89.02, 76.11) * mm, "end": v(-88.96, 76.02) * mm});
            skLineSegment(sketch, "E2843", {"start": v(-88.96, 76.02) * mm, "end": v(-88.9, 75.92) * mm});
            skLineSegment(sketch, "E2844", {"start": v(-88.9, 75.92) * mm, "end": v(-88.84, 75.83) * mm});
            skLineSegment(sketch, "E2845", {"start": v(-88.84, 75.83) * mm, "end": v(-88.78, 75.74) * mm});
            skLineSegment(sketch, "E2846", {"start": v(-88.78, 75.74) * mm, "end": v(-89.27, 74.9) * mm});
            skLineSegment(sketch, "E2847", {"start": v(-89.27, 74.9) * mm, "end": v(-90.02, 74.27) * mm});
            skLineSegment(sketch, "E2848", {"start": v(-90.02, 74.27) * mm, "end": v(-90.12, 74.31) * mm});
            skLineSegment(sketch, "E2849", {"start": v(-90.12, 74.31) * mm, "end": v(-90.22, 74.36) * mm});
            skLineSegment(sketch, "E2850", {"start": v(-90.22, 74.36) * mm, "end": v(-90.32, 74.4) * mm});
            skLineSegment(sketch, "E2851", {"start": v(-90.32, 74.4) * mm, "end": v(-90.53, 74.48) * mm});
            skLineSegment(sketch, "E2852", {"start": v(-90.53, 74.48) * mm, "end": v(-90.74, 74.57) * mm});
            skLineSegment(sketch, "E2853", {"start": v(-90.74, 74.57) * mm, "end": v(-90.85, 74.61) * mm});
            skLineSegment(sketch, "E2854", {"start": v(-90.85, 74.61) * mm, "end": v(-91.07, 74.7) * mm});
            skLineSegment(sketch, "E2855", {"start": v(-91.07, 74.7) * mm, "end": v(-91.18, 74.74) * mm});
            skLineSegment(sketch, "E2856", {"start": v(-91.18, 74.74) * mm, "end": v(-91.3, 74.78) * mm});
            skLineSegment(sketch, "E2857", {"start": v(-91.3, 74.78) * mm, "end": v(-91.4, 74.83) * mm});
            skLineSegment(sketch, "E2858", {"start": v(-91.4, 74.83) * mm, "end": v(-91.64, 74.91) * mm});
            skLineSegment(sketch, "E2859", {"start": v(-91.64, 74.91) * mm, "end": v(-91.75, 74.96) * mm});
            skLineSegment(sketch, "E2860", {"start": v(-91.75, 74.96) * mm, "end": v(-91.87, 75) * mm});
            skLineSegment(sketch, "E2861", {"start": v(-91.87, 75) * mm, "end": v(-92, 75.04) * mm});
            skLineSegment(sketch, "E2862", {"start": v(-92, 75.04) * mm, "end": v(-92.11, 75.09) * mm});
            skLineSegment(sketch, "E2863", {"start": v(-92.11, 75.09) * mm, "end": v(-92.24, 75.13) * mm});
            skLineSegment(sketch, "E2864", {"start": v(-92.24, 75.13) * mm, "end": v(-92.49, 75.21) * mm});
            skLineSegment(sketch, "E2865", {"start": v(-92.49, 75.21) * mm, "end": v(-92.61, 75.26) * mm});
            skLineSegment(sketch, "E2866", {"start": v(-92.61, 75.26) * mm, "end": v(-92.87, 75.34) * mm});
            skLineSegment(sketch, "E2867", {"start": v(-92.87, 75.34) * mm, "end": v(-93, 75.39) * mm});
            skLineSegment(sketch, "E2868", {"start": v(-93, 75.39) * mm, "end": v(-93.13, 75.43) * mm});
            skLineSegment(sketch, "E2869", {"start": v(-93.13, 75.43) * mm, "end": v(-93.4, 75.52) * mm});
            skLineSegment(sketch, "E2870", {"start": v(-93.4, 75.52) * mm, "end": v(-93.53, 75.56) * mm});
            skLineSegment(sketch, "E2871", {"start": v(-93.53, 75.56) * mm, "end": v(-93.67, 75.6) * mm});
            skLineSegment(sketch, "E2872", {"start": v(-93.67, 75.6) * mm, "end": v(-93.8, 75.64) * mm});
            skLineSegment(sketch, "E2873", {"start": v(-93.8, 75.64) * mm, "end": v(-93.95, 75.69) * mm});
            skLineSegment(sketch, "E2874", {"start": v(-93.95, 75.69) * mm, "end": v(-94.09, 75.73) * mm});
            skLineSegment(sketch, "E2875", {"start": v(-94.09, 75.73) * mm, "end": v(-94.23, 75.77) * mm});
            skLineSegment(sketch, "E2876", {"start": v(-94.23, 75.77) * mm, "end": v(-94.37, 75.81) * mm});
            skLineSegment(sketch, "E2877", {"start": v(-94.37, 75.81) * mm, "end": v(-94.51, 75.86) * mm});
            skLineSegment(sketch, "E2878", {"start": v(-94.51, 75.86) * mm, "end": v(-94.61, 75.86) * mm});
            skLineSegment(sketch, "E2879", {"start": v(-94.61, 75.86) * mm, "end": v(-95.64, 74.56) * mm});
            skLineSegment(sketch, "E2880", {"start": v(-95.64, 74.56) * mm, "end": v(-95.62, 74.46) * mm});
            skLineSegment(sketch, "E2881", {"start": v(-95.62, 74.46) * mm, "end": v(-95.54, 74.33) * mm});
            skLineSegment(sketch, "E2882", {"start": v(-95.54, 74.33) * mm, "end": v(-95.47, 74.2) * mm});
            skLineSegment(sketch, "E2883", {"start": v(-95.47, 74.2) * mm, "end": v(-95.4, 74.08) * mm});
            skLineSegment(sketch, "E2884", {"start": v(-95.4, 74.08) * mm, "end": v(-95.32, 73.95) * mm});
            skLineSegment(sketch, "E2885", {"start": v(-95.32, 73.95) * mm, "end": v(-95.25, 73.82) * mm});
            skLineSegment(sketch, "E2886", {"start": v(-95.25, 73.82) * mm, "end": v(-95.17, 73.7) * mm});
            skLineSegment(sketch, "E2887", {"start": v(-95.17, 73.7) * mm, "end": v(-95.1, 73.58) * mm});
            skLineSegment(sketch, "E2888", {"start": v(-95.1, 73.58) * mm, "end": v(-94.96, 73.33) * mm});
            skLineSegment(sketch, "E2889", {"start": v(-94.96, 73.33) * mm, "end": v(-94.88, 73.22) * mm});
            skLineSegment(sketch, "E2890", {"start": v(-94.88, 73.22) * mm, "end": v(-94.81, 73.1) * mm});
            skLineSegment(sketch, "E2891", {"start": v(-94.81, 73.1) * mm, "end": v(-94.74, 72.98) * mm});
            skLineSegment(sketch, "E2892", {"start": v(-94.74, 72.98) * mm, "end": v(-94.67, 72.86) * mm});
            skLineSegment(sketch, "E2893", {"start": v(-94.67, 72.86) * mm, "end": v(-94.6, 72.75) * mm});
            skLineSegment(sketch, "E2894", {"start": v(-94.6, 72.75) * mm, "end": v(-94.53, 72.64) * mm});
            skLineSegment(sketch, "E2895", {"start": v(-94.53, 72.64) * mm, "end": v(-94.45, 72.52) * mm});
            skLineSegment(sketch, "E2896", {"start": v(-94.45, 72.52) * mm, "end": v(-94.38, 72.41) * mm});
            skLineSegment(sketch, "E2897", {"start": v(-94.38, 72.41) * mm, "end": v(-94.24, 72.2) * mm});
            skLineSegment(sketch, "E2898", {"start": v(-94.24, 72.2) * mm, "end": v(-94.17, 72.09) * mm});
            skLineSegment(sketch, "E2899", {"start": v(-94.17, 72.09) * mm, "end": v(-94.1, 71.98) * mm});
            skLineSegment(sketch, "E2900", {"start": v(-94.1, 71.98) * mm, "end": v(-94.03, 71.88) * mm});
            skLineSegment(sketch, "E2901", {"start": v(-94.03, 71.88) * mm, "end": v(-93.9, 71.67) * mm});
            skLineSegment(sketch, "E2902", {"start": v(-93.9, 71.67) * mm, "end": v(-93.83, 71.57) * mm});
            skLineSegment(sketch, "E2903", {"start": v(-93.83, 71.57) * mm, "end": v(-93.76, 71.47) * mm});
            skLineSegment(sketch, "E2904", {"start": v(-93.76, 71.47) * mm, "end": v(-93.7, 71.37) * mm});
            skLineSegment(sketch, "E2905", {"start": v(-93.7, 71.37) * mm, "end": v(-93.63, 71.28) * mm});
            skLineSegment(sketch, "E2906", {"start": v(-93.63, 71.28) * mm, "end": v(-93.56, 71.18) * mm});
            skLineSegment(sketch, "E2907", {"start": v(-93.56, 71.18) * mm, "end": v(-93.5, 71.08) * mm});
            skLineSegment(sketch, "E2908", {"start": v(-93.5, 71.08) * mm, "end": v(-93.43, 71) * mm});
            skLineSegment(sketch, "E2909", {"start": v(-93.43, 71) * mm, "end": v(-93.36, 70.9) * mm});
            skLineSegment(sketch, "E2910", {"start": v(-93.36, 70.9) * mm, "end": v(-93.3, 70.8) * mm});
            skLineSegment(sketch, "E2911", {"start": v(-93.3, 70.8) * mm, "end": v(-93.17, 70.63) * mm});
            skLineSegment(sketch, "E2912", {"start": v(-93.17, 70.63) * mm, "end": v(-93.1, 70.54) * mm});
            skLineSegment(sketch, "E2913", {"start": v(-93.1, 70.54) * mm, "end": v(-93.04, 70.45) * mm});
            skLineSegment(sketch, "E2914", {"start": v(-93.04, 70.45) * mm, "end": v(-93.47, 69.58) * mm});
            skLineSegment(sketch, "E2915", {"start": v(-93.47, 69.58) * mm, "end": v(-94.18, 68.91) * mm});
            skLineSegment(sketch, "E2916", {"start": v(-94.18, 68.91) * mm, "end": v(-94.29, 68.95) * mm});
            skLineSegment(sketch, "E2917", {"start": v(-94.29, 68.95) * mm, "end": v(-94.5, 69.02) * mm});
            skLineSegment(sketch, "E2918", {"start": v(-94.5, 69.02) * mm, "end": v(-94.6, 69.06) * mm});
            skLineSegment(sketch, "E2919", {"start": v(-94.6, 69.06) * mm, "end": v(-94.7, 69.1) * mm});
            skLineSegment(sketch, "E2920", {"start": v(-94.7, 69.1) * mm, "end": v(-94.81, 69.13) * mm});
            skLineSegment(sketch, "E2921", {"start": v(-94.81, 69.13) * mm, "end": v(-94.92, 69.17) * mm});
            skLineSegment(sketch, "E2922", {"start": v(-94.92, 69.17) * mm, "end": v(-95.03, 69.2) * mm});
            skLineSegment(sketch, "E2923", {"start": v(-95.03, 69.2) * mm, "end": v(-95.14, 69.24) * mm});
            skLineSegment(sketch, "E2924", {"start": v(-95.14, 69.24) * mm, "end": v(-95.26, 69.28) * mm});
            skLineSegment(sketch, "E2925", {"start": v(-95.26, 69.28) * mm, "end": v(-95.37, 69.31) * mm});
            skLineSegment(sketch, "E2926", {"start": v(-95.37, 69.31) * mm, "end": v(-95.48, 69.35) * mm});
            skLineSegment(sketch, "E2927", {"start": v(-95.48, 69.35) * mm, "end": v(-95.6, 69.39) * mm});
            skLineSegment(sketch, "E2928", {"start": v(-95.6, 69.39) * mm, "end": v(-95.72, 69.42) * mm});
            skLineSegment(sketch, "E2929", {"start": v(-95.72, 69.42) * mm, "end": v(-95.84, 69.46) * mm});
            skLineSegment(sketch, "E2930", {"start": v(-95.84, 69.46) * mm, "end": v(-95.96, 69.5) * mm});
            skLineSegment(sketch, "E2931", {"start": v(-95.96, 69.5) * mm, "end": v(-96.08, 69.53) * mm});
            skLineSegment(sketch, "E2932", {"start": v(-96.08, 69.53) * mm, "end": v(-96.2, 69.57) * mm});
            skLineSegment(sketch, "E2933", {"start": v(-96.2, 69.57) * mm, "end": v(-96.32, 69.6) * mm});
            skLineSegment(sketch, "E2934", {"start": v(-96.32, 69.6) * mm, "end": v(-96.45, 69.64) * mm});
            skLineSegment(sketch, "E2935", {"start": v(-96.45, 69.64) * mm, "end": v(-96.58, 69.68) * mm});
            skLineSegment(sketch, "E2936", {"start": v(-96.58, 69.68) * mm, "end": v(-96.83, 69.75) * mm});
            skLineSegment(sketch, "E2937", {"start": v(-96.83, 69.75) * mm, "end": v(-96.96, 69.78) * mm});
            skLineSegment(sketch, "E2938", {"start": v(-96.96, 69.78) * mm, "end": v(-97.1, 69.82) * mm});
            skLineSegment(sketch, "E2939", {"start": v(-97.1, 69.82) * mm, "end": v(-97.23, 69.85) * mm});
            skLineSegment(sketch, "E2940", {"start": v(-97.23, 69.85) * mm, "end": v(-97.36, 69.89) * mm});
            skLineSegment(sketch, "E2941", {"start": v(-97.36, 69.89) * mm, "end": v(-97.5, 69.92) * mm});
            skLineSegment(sketch, "E2942", {"start": v(-97.5, 69.92) * mm, "end": v(-97.63, 69.96) * mm});
            skLineSegment(sketch, "E2943", {"start": v(-97.63, 69.96) * mm, "end": v(-97.77, 70) * mm});
            skLineSegment(sketch, "E2944", {"start": v(-97.77, 70) * mm, "end": v(-98.05, 70.06) * mm});
            skLineSegment(sketch, "E2945", {"start": v(-98.05, 70.06) * mm, "end": v(-98.19, 70.1) * mm});
            skLineSegment(sketch, "E2946", {"start": v(-98.19, 70.1) * mm, "end": v(-98.33, 70.13) * mm});
            skLineSegment(sketch, "E2947", {"start": v(-98.33, 70.13) * mm, "end": v(-98.47, 70.16) * mm});
            skLineSegment(sketch, "E2948", {"start": v(-98.47, 70.16) * mm, "end": v(-98.62, 70.2) * mm});
            skLineSegment(sketch, "E2949", {"start": v(-98.62, 70.2) * mm, "end": v(-98.77, 70.23) * mm});
            skLineSegment(sketch, "E2950", {"start": v(-98.77, 70.23) * mm, "end": v(-98.86, 70.23) * mm});
            skLineSegment(sketch, "E2951", {"start": v(-98.86, 70.23) * mm, "end": v(-99.81, 68.87) * mm});
            skLineSegment(sketch, "E2952", {"start": v(-99.81, 68.87) * mm, "end": v(-99.78, 68.78) * mm});
            skLineSegment(sketch, "E2953", {"start": v(-99.78, 68.78) * mm, "end": v(-99.7, 68.65) * mm});
            skLineSegment(sketch, "E2954", {"start": v(-99.7, 68.65) * mm, "end": v(-99.62, 68.53) * mm});
            skLineSegment(sketch, "E2955", {"start": v(-99.62, 68.53) * mm, "end": v(-99.54, 68.4) * mm});
            skLineSegment(sketch, "E2956", {"start": v(-99.54, 68.4) * mm, "end": v(-99.46, 68.28) * mm});
            skLineSegment(sketch, "E2957", {"start": v(-99.46, 68.28) * mm, "end": v(-99.38, 68.16) * mm});
            skLineSegment(sketch, "E2958", {"start": v(-99.38, 68.16) * mm, "end": v(-99.3, 68.04) * mm});
            skLineSegment(sketch, "E2959", {"start": v(-99.3, 68.04) * mm, "end": v(-99.22, 67.92) * mm});
            skLineSegment(sketch, "E2960", {"start": v(-99.22, 67.92) * mm, "end": v(-99.14, 67.8) * mm});
            skLineSegment(sketch, "E2961", {"start": v(-99.14, 67.8) * mm, "end": v(-99.06, 67.69) * mm});
            skLineSegment(sketch, "E2962", {"start": v(-99.06, 67.69) * mm, "end": v(-98.98, 67.57) * mm});
            skLineSegment(sketch, "E2963", {"start": v(-98.98, 67.57) * mm, "end": v(-98.82, 67.35) * mm});
            skLineSegment(sketch, "E2964", {"start": v(-98.82, 67.35) * mm, "end": v(-98.74, 67.24) * mm});
            skLineSegment(sketch, "E2965", {"start": v(-98.74, 67.24) * mm, "end": v(-98.67, 67.13) * mm});
            skLineSegment(sketch, "E2966", {"start": v(-98.67, 67.13) * mm, "end": v(-98.59, 67.02) * mm});
            skLineSegment(sketch, "E2967", {"start": v(-98.59, 67.02) * mm, "end": v(-98.51, 66.91) * mm});
            skLineSegment(sketch, "E2968", {"start": v(-98.51, 66.91) * mm, "end": v(-98.43, 66.8) * mm});
            skLineSegment(sketch, "E2969", {"start": v(-98.43, 66.8) * mm, "end": v(-98.36, 66.7) * mm});
            skLineSegment(sketch, "E2970", {"start": v(-98.36, 66.7) * mm, "end": v(-98.2, 66.5) * mm});
            skLineSegment(sketch, "E2971", {"start": v(-98.2, 66.5) * mm, "end": v(-98.05, 66.3) * mm});
            skLineSegment(sketch, "E2972", {"start": v(-98.05, 66.3) * mm, "end": v(-97.98, 66.2) * mm});
            skLineSegment(sketch, "E2973", {"start": v(-97.98, 66.2) * mm, "end": v(-97.83, 66) * mm});
            skLineSegment(sketch, "E2974", {"start": v(-97.83, 66) * mm, "end": v(-97.68, 65.8) * mm});
            skLineSegment(sketch, "E2975", {"start": v(-97.68, 65.8) * mm, "end": v(-97.61, 65.71) * mm});
            skLineSegment(sketch, "E2976", {"start": v(-97.61, 65.71) * mm, "end": v(-97.54, 65.62) * mm});
            skLineSegment(sketch, "E2977", {"start": v(-97.54, 65.62) * mm, "end": v(-97.47, 65.53) * mm});
            skLineSegment(sketch, "E2978", {"start": v(-97.47, 65.53) * mm, "end": v(-97.4, 65.44) * mm});
            skLineSegment(sketch, "E2979", {"start": v(-97.4, 65.44) * mm, "end": v(-97.33, 65.35) * mm});
            skLineSegment(sketch, "E2980", {"start": v(-97.33, 65.35) * mm, "end": v(-97.26, 65.26) * mm});
            skLineSegment(sketch, "E2981", {"start": v(-97.26, 65.26) * mm, "end": v(-97.18, 65.18) * mm});
            skLineSegment(sketch, "E2982", {"start": v(-97.18, 65.18) * mm, "end": v(-97.11, 65.1) * mm});
            skLineSegment(sketch, "E2983", {"start": v(-97.11, 65.1) * mm, "end": v(-97.05, 65) * mm});
            skLineSegment(sketch, "E2984", {"start": v(-97.05, 65) * mm, "end": v(-96.98, 64.92) * mm});
            skLineSegment(sketch, "E2985", {"start": v(-96.98, 64.92) * mm, "end": v(-97.36, 64.03) * mm});
            skLineSegment(sketch, "E2986", {"start": v(-97.36, 64.03) * mm, "end": v(-98.03, 63.32) * mm});
            skLineSegment(sketch, "E2987", {"start": v(-98.03, 63.32) * mm, "end": v(-98.13, 63.35) * mm});
            skLineSegment(sketch, "E2988", {"start": v(-98.13, 63.35) * mm, "end": v(-98.24, 63.38) * mm});
            skLineSegment(sketch, "E2989", {"start": v(-98.24, 63.38) * mm, "end": v(-98.35, 63.41) * mm});
            skLineSegment(sketch, "E2990", {"start": v(-98.35, 63.41) * mm, "end": v(-98.45, 63.44) * mm});
            skLineSegment(sketch, "E2991", {"start": v(-98.45, 63.44) * mm, "end": v(-98.56, 63.47) * mm});
            skLineSegment(sketch, "E2992", {"start": v(-98.56, 63.47) * mm, "end": v(-98.78, 63.53) * mm});
            skLineSegment(sketch, "E2993", {"start": v(-98.78, 63.53) * mm, "end": v(-98.9, 63.56) * mm});
            skLineSegment(sketch, "E2994", {"start": v(-98.9, 63.56) * mm, "end": v(-99.12, 63.62) * mm});
            skLineSegment(sketch, "E2995", {"start": v(-99.12, 63.62) * mm, "end": v(-99.24, 63.65) * mm});
            skLineSegment(sketch, "E2996", {"start": v(-99.24, 63.65) * mm, "end": v(-99.36, 63.68) * mm});
            skLineSegment(sketch, "E2997", {"start": v(-99.36, 63.68) * mm, "end": v(-99.6, 63.74) * mm});
            skLineSegment(sketch, "E2998", {"start": v(-99.6, 63.74) * mm, "end": v(-99.71, 63.77) * mm});
            skLineSegment(sketch, "E2999", {"start": v(-99.71, 63.77) * mm, "end": v(-99.83, 63.8) * mm});
            skLineSegment(sketch, "E3000", {"start": v(-99.83, 63.8) * mm, "end": v(-100.08, 63.86) * mm});
            skLineSegment(sketch, "E3001", {"start": v(-100.08, 63.86) * mm, "end": v(-100.2, 63.88) * mm});
            skLineSegment(sketch, "E3002", {"start": v(-100.2, 63.88) * mm, "end": v(-100.33, 63.91) * mm});
            skLineSegment(sketch, "E3003", {"start": v(-100.33, 63.91) * mm, "end": v(-100.46, 63.94) * mm});
            skLineSegment(sketch, "E3004", {"start": v(-100.46, 63.94) * mm, "end": v(-100.6, 63.97) * mm});
            skLineSegment(sketch, "E3005", {"start": v(-100.6, 63.97) * mm, "end": v(-100.72, 64) * mm});
            skLineSegment(sketch, "E3006", {"start": v(-100.72, 64) * mm, "end": v(-100.86, 64.03) * mm});
            skLineSegment(sketch, "E3007", {"start": v(-100.86, 64.03) * mm, "end": v(-100.99, 64.05) * mm});
            skLineSegment(sketch, "E3008", {"start": v(-100.99, 64.05) * mm, "end": v(-101.26, 64.1) * mm});
            skLineSegment(sketch, "E3009", {"start": v(-101.26, 64.1) * mm, "end": v(-101.4, 64.14) * mm});
            skLineSegment(sketch, "E3010", {"start": v(-101.4, 64.14) * mm, "end": v(-101.53, 64.16) * mm});
            skLineSegment(sketch, "E3011", {"start": v(-101.53, 64.16) * mm, "end": v(-101.67, 64.19) * mm});
            skLineSegment(sketch, "E3012", {"start": v(-101.67, 64.19) * mm, "end": v(-101.81, 64.22) * mm});
            skLineSegment(sketch, "E3013", {"start": v(-101.81, 64.22) * mm, "end": v(-101.95, 64.24) * mm});
            skLineSegment(sketch, "E3014", {"start": v(-101.95, 64.24) * mm, "end": v(-102.1, 64.27) * mm});
            skLineSegment(sketch, "E3015", {"start": v(-102.1, 64.27) * mm, "end": v(-102.24, 64.3) * mm});
            skLineSegment(sketch, "E3016", {"start": v(-102.24, 64.3) * mm, "end": v(-102.39, 64.32) * mm});
            skLineSegment(sketch, "E3017", {"start": v(-102.39, 64.32) * mm, "end": v(-102.53, 64.34) * mm});
            skLineSegment(sketch, "E3018", {"start": v(-102.53, 64.34) * mm, "end": v(-102.68, 64.37) * mm});
            skLineSegment(sketch, "E3019", {"start": v(-102.68, 64.37) * mm, "end": v(-102.78, 64.36) * mm});
            skLineSegment(sketch, "E3020", {"start": v(-102.78, 64.36) * mm, "end": v(-103.65, 62.95) * mm});
            skLineSegment(sketch, "E3021", {"start": v(-103.65, 62.95) * mm, "end": v(-103.61, 62.86) * mm});
            skLineSegment(sketch, "E3022", {"start": v(-103.61, 62.86) * mm, "end": v(-103.53, 62.74) * mm});
            skLineSegment(sketch, "E3023", {"start": v(-103.53, 62.74) * mm, "end": v(-103.44, 62.62) * mm});
            skLineSegment(sketch, "E3024", {"start": v(-103.44, 62.62) * mm, "end": v(-103.35, 62.5) * mm});
            skLineSegment(sketch, "E3025", {"start": v(-103.35, 62.5) * mm, "end": v(-103.26, 62.38) * mm});
            skLineSegment(sketch, "E3026", {"start": v(-103.26, 62.38) * mm, "end": v(-103.17, 62.27) * mm});
            skLineSegment(sketch, "E3027", {"start": v(-103.17, 62.27) * mm, "end": v(-103, 62.04) * mm});
            skLineSegment(sketch, "E3028", {"start": v(-103, 62.04) * mm, "end": v(-102.91, 61.93) * mm});
            skLineSegment(sketch, "E3029", {"start": v(-102.91, 61.93) * mm, "end": v(-102.83, 61.81) * mm});
            skLineSegment(sketch, "E3030", {"start": v(-102.83, 61.81) * mm, "end": v(-102.74, 61.7) * mm});
            skLineSegment(sketch, "E3031", {"start": v(-102.74, 61.7) * mm, "end": v(-102.66, 61.6) * mm});
            skLineSegment(sketch, "E3032", {"start": v(-102.66, 61.6) * mm, "end": v(-102.57, 61.49) * mm});
            skLineSegment(sketch, "E3033", {"start": v(-102.57, 61.49) * mm, "end": v(-102.4, 61.28) * mm});
            skLineSegment(sketch, "E3034", {"start": v(-102.4, 61.28) * mm, "end": v(-102.32, 61.17) * mm});
            skLineSegment(sketch, "E3035", {"start": v(-102.32, 61.17) * mm, "end": v(-102.24, 61.07) * mm});
            skLineSegment(sketch, "E3036", {"start": v(-102.24, 61.07) * mm, "end": v(-102.15, 60.97) * mm});
            skLineSegment(sketch, "E3037", {"start": v(-102.15, 60.97) * mm, "end": v(-102.07, 60.87) * mm});
            skLineSegment(sketch, "E3038", {"start": v(-102.07, 60.87) * mm, "end": v(-101.99, 60.77) * mm});
            skLineSegment(sketch, "E3039", {"start": v(-101.99, 60.77) * mm, "end": v(-101.9, 60.67) * mm});
            skLineSegment(sketch, "E3040", {"start": v(-101.9, 60.67) * mm, "end": v(-101.74, 60.48) * mm});
            skLineSegment(sketch, "E3041", {"start": v(-101.74, 60.48) * mm, "end": v(-101.66, 60.38) * mm});
            skLineSegment(sketch, "E3042", {"start": v(-101.66, 60.38) * mm, "end": v(-101.58, 60.29) * mm});
            skLineSegment(sketch, "E3043", {"start": v(-101.58, 60.29) * mm, "end": v(-101.5, 60.2) * mm});
            skLineSegment(sketch, "E3044", {"start": v(-101.5, 60.2) * mm, "end": v(-101.42, 60.1) * mm});
            skLineSegment(sketch, "E3045", {"start": v(-101.42, 60.1) * mm, "end": v(-101.27, 59.93) * mm});
            skLineSegment(sketch, "E3046", {"start": v(-101.27, 59.93) * mm, "end": v(-101.2, 59.84) * mm});
            skLineSegment(sketch, "E3047", {"start": v(-101.2, 59.84) * mm, "end": v(-101.11, 59.75) * mm});
            skLineSegment(sketch, "E3048", {"start": v(-101.11, 59.75) * mm, "end": v(-101.04, 59.66) * mm});
            skLineSegment(sketch, "E3049", {"start": v(-101.04, 59.66) * mm, "end": v(-100.88, 59.5) * mm});
            skLineSegment(sketch, "E3050", {"start": v(-100.88, 59.5) * mm, "end": v(-100.74, 59.33) * mm});
            skLineSegment(sketch, "E3051", {"start": v(-100.74, 59.33) * mm, "end": v(-100.66, 59.25) * mm});
            skLineSegment(sketch, "E3052", {"start": v(-100.66, 59.25) * mm, "end": v(-100.59, 59.17) * mm});
            skLineSegment(sketch, "E3053", {"start": v(-100.59, 59.17) * mm, "end": v(-100.92, 58.26) * mm});
            skLineSegment(sketch, "E3054", {"start": v(-100.92, 58.26) * mm, "end": v(-101.55, 57.51) * mm});
            skLineSegment(sketch, "E3055", {"start": v(-101.55, 57.51) * mm, "end": v(-101.65, 57.54) * mm});
            skLineSegment(sketch, "E3056", {"start": v(-101.65, 57.54) * mm, "end": v(-101.76, 57.56) * mm});
            skLineSegment(sketch, "E3057", {"start": v(-101.76, 57.56) * mm, "end": v(-101.87, 57.59) * mm});
            skLineSegment(sketch, "E3058", {"start": v(-101.87, 57.59) * mm, "end": v(-101.97, 57.6) * mm});
            skLineSegment(sketch, "E3059", {"start": v(-101.97, 57.6) * mm, "end": v(-102.09, 57.63) * mm});
            skLineSegment(sketch, "E3060", {"start": v(-102.09, 57.63) * mm, "end": v(-102.2, 57.66) * mm});
            skLineSegment(sketch, "E3061", {"start": v(-102.2, 57.66) * mm, "end": v(-102.3, 57.68) * mm});
            skLineSegment(sketch, "E3062", {"start": v(-102.3, 57.68) * mm, "end": v(-102.42, 57.7) * mm});
            skLineSegment(sketch, "E3063", {"start": v(-102.42, 57.7) * mm, "end": v(-102.54, 57.73) * mm});
            skLineSegment(sketch, "E3064", {"start": v(-102.54, 57.73) * mm, "end": v(-102.65, 57.75) * mm});
            skLineSegment(sketch, "E3065", {"start": v(-102.65, 57.75) * mm, "end": v(-102.77, 57.77) * mm});
            skLineSegment(sketch, "E3066", {"start": v(-102.77, 57.77) * mm, "end": v(-102.89, 57.8) * mm});
            skLineSegment(sketch, "E3067", {"start": v(-102.89, 57.8) * mm, "end": v(-103, 57.82) * mm});
            skLineSegment(sketch, "E3068", {"start": v(-103, 57.82) * mm, "end": v(-103.13, 57.84) * mm});
            skLineSegment(sketch, "E3069", {"start": v(-103.13, 57.84) * mm, "end": v(-103.25, 57.86) * mm});
            skLineSegment(sketch, "E3070", {"start": v(-103.25, 57.86) * mm, "end": v(-103.5, 57.9) * mm});
            skLineSegment(sketch, "E3071", {"start": v(-103.5, 57.9) * mm, "end": v(-103.63, 57.93) * mm});
            skLineSegment(sketch, "E3072", {"start": v(-103.63, 57.93) * mm, "end": v(-103.75, 57.95) * mm});
            skLineSegment(sketch, "E3073", {"start": v(-103.75, 57.95) * mm, "end": v(-103.88, 57.97) * mm});
            skLineSegment(sketch, "E3074", {"start": v(-103.88, 57.97) * mm, "end": v(-104.01, 58) * mm});
            skLineSegment(sketch, "E3075", {"start": v(-104.01, 58) * mm, "end": v(-104.14, 58.01) * mm});
            skLineSegment(sketch, "E3076", {"start": v(-104.14, 58.01) * mm, "end": v(-104.4, 58.05) * mm});
            skLineSegment(sketch, "E3077", {"start": v(-104.4, 58.05) * mm, "end": v(-104.68, 58.1) * mm});
            skLineSegment(sketch, "E3078", {"start": v(-104.68, 58.1) * mm, "end": v(-104.81, 58.11) * mm});
            skLineSegment(sketch, "E3079", {"start": v(-104.81, 58.11) * mm, "end": v(-104.95, 58.13) * mm});
            skLineSegment(sketch, "E3080", {"start": v(-104.95, 58.13) * mm, "end": v(-105.1, 58.15) * mm});
            skLineSegment(sketch, "E3081", {"start": v(-105.1, 58.15) * mm, "end": v(-105.23, 58.17) * mm});
            skLineSegment(sketch, "E3082", {"start": v(-105.23, 58.17) * mm, "end": v(-105.37, 58.19) * mm});
            skLineSegment(sketch, "E3083", {"start": v(-105.37, 58.19) * mm, "end": v(-105.66, 58.22) * mm});
            skLineSegment(sketch, "E3084", {"start": v(-105.66, 58.22) * mm, "end": v(-105.8, 58.24) * mm});
            skLineSegment(sketch, "E3085", {"start": v(-105.8, 58.24) * mm, "end": v(-105.95, 58.26) * mm});
            skLineSegment(sketch, "E3086", {"start": v(-105.95, 58.26) * mm, "end": v(-106.1, 58.27) * mm});
            skLineSegment(sketch, "E3087", {"start": v(-106.1, 58.27) * mm, "end": v(-106.25, 58.3) * mm});
            skLineSegment(sketch, "E3088", {"start": v(-106.25, 58.3) * mm, "end": v(-106.35, 58.28) * mm});
            skLineSegment(sketch, "E3089", {"start": v(-106.35, 58.28) * mm, "end": v(-107.13, 56.82) * mm});
            skLineSegment(sketch, "E3090", {"start": v(-107.13, 56.82) * mm, "end": v(-107.1, 56.73) * mm});
            skLineSegment(sketch, "E3091", {"start": v(-107.1, 56.73) * mm, "end": v(-107, 56.61) * mm});
            skLineSegment(sketch, "E3092", {"start": v(-107, 56.61) * mm, "end": v(-106.9, 56.5) * mm});
            skLineSegment(sketch, "E3093", {"start": v(-106.9, 56.5) * mm, "end": v(-106.8, 56.39) * mm});
            skLineSegment(sketch, "E3094", {"start": v(-106.8, 56.39) * mm, "end": v(-106.71, 56.27) * mm});
            skLineSegment(sketch, "E3095", {"start": v(-106.71, 56.27) * mm, "end": v(-106.62, 56.16) * mm});
            skLineSegment(sketch, "E3096", {"start": v(-106.62, 56.16) * mm, "end": v(-106.43, 55.94) * mm});
            skLineSegment(sketch, "E3097", {"start": v(-106.43, 55.94) * mm, "end": v(-106.34, 55.84) * mm});
            skLineSegment(sketch, "E3098", {"start": v(-106.34, 55.84) * mm, "end": v(-106.25, 55.73) * mm});
            skLineSegment(sketch, "E3099", {"start": v(-106.25, 55.73) * mm, "end": v(-106.15, 55.63) * mm});
            skLineSegment(sketch, "E3100", {"start": v(-106.15, 55.63) * mm, "end": v(-106.06, 55.52) * mm});
            skLineSegment(sketch, "E3101", {"start": v(-106.06, 55.52) * mm, "end": v(-105.88, 55.32) * mm});
            skLineSegment(sketch, "E3102", {"start": v(-105.88, 55.32) * mm, "end": v(-105.8, 55.22) * mm});
            skLineSegment(sketch, "E3103", {"start": v(-105.8, 55.22) * mm, "end": v(-105.61, 55.02) * mm});
            skLineSegment(sketch, "E3104", {"start": v(-105.61, 55.02) * mm, "end": v(-105.52, 54.92) * mm});
            skLineSegment(sketch, "E3105", {"start": v(-105.52, 54.92) * mm, "end": v(-105.35, 54.73) * mm});
            skLineSegment(sketch, "E3106", {"start": v(-105.35, 54.73) * mm, "end": v(-105.26, 54.64) * mm});
            skLineSegment(sketch, "E3107", {"start": v(-105.26, 54.64) * mm, "end": v(-105.17, 54.55) * mm});
            skLineSegment(sketch, "E3108", {"start": v(-105.17, 54.55) * mm, "end": v(-105.09, 54.46) * mm});
            skLineSegment(sketch, "E3109", {"start": v(-105.09, 54.46) * mm, "end": v(-104.92, 54.28) * mm});
            skLineSegment(sketch, "E3110", {"start": v(-104.92, 54.28) * mm, "end": v(-104.83, 54.2) * mm});
            skLineSegment(sketch, "E3111", {"start": v(-104.83, 54.2) * mm, "end": v(-104.75, 54.1) * mm});
            skLineSegment(sketch, "E3112", {"start": v(-104.75, 54.1) * mm, "end": v(-104.66, 54.02) * mm});
            skLineSegment(sketch, "E3113", {"start": v(-104.66, 54.02) * mm, "end": v(-104.58, 53.94) * mm});
            skLineSegment(sketch, "E3114", {"start": v(-104.58, 53.94) * mm, "end": v(-104.5, 53.85) * mm});
            skLineSegment(sketch, "E3115", {"start": v(-104.5, 53.85) * mm, "end": v(-104.34, 53.69) * mm});
            skLineSegment(sketch, "E3116", {"start": v(-104.34, 53.69) * mm, "end": v(-104.25, 53.61) * mm});
            skLineSegment(sketch, "E3117", {"start": v(-104.25, 53.61) * mm, "end": v(-104.1, 53.45) * mm});
            skLineSegment(sketch, "E3118", {"start": v(-104.1, 53.45) * mm, "end": v(-104.02, 53.38) * mm});
            skLineSegment(sketch, "E3119", {"start": v(-104.02, 53.38) * mm, "end": v(-103.94, 53.3) * mm});
            skLineSegment(sketch, "E3120", {"start": v(-103.94, 53.3) * mm, "end": v(-103.86, 53.23) * mm});
            skLineSegment(sketch, "E3121", {"start": v(-103.86, 53.23) * mm, "end": v(-104.14, 52.3) * mm});
            skLineSegment(sketch, "E3122", {"start": v(-104.14, 52.3) * mm, "end": v(-104.72, 51.51) * mm});
            skLineSegment(sketch, "E3123", {"start": v(-104.72, 51.51) * mm, "end": v(-104.83, 51.53) * mm});
            skLineSegment(sketch, "E3124", {"start": v(-104.83, 51.53) * mm, "end": v(-104.93, 51.55) * mm});
            skLineSegment(sketch, "E3125", {"start": v(-104.93, 51.55) * mm, "end": v(-105.04, 51.56) * mm});
            skLineSegment(sketch, "E3126", {"start": v(-105.04, 51.56) * mm, "end": v(-105.15, 51.58) * mm});
            skLineSegment(sketch, "E3127", {"start": v(-105.15, 51.58) * mm, "end": v(-105.26, 51.6) * mm});
            skLineSegment(sketch, "E3128", {"start": v(-105.26, 51.6) * mm, "end": v(-105.38, 51.62) * mm});
            skLineSegment(sketch, "E3129", {"start": v(-105.38, 51.62) * mm, "end": v(-105.49, 51.63) * mm});
            skLineSegment(sketch, "E3130", {"start": v(-105.49, 51.63) * mm, "end": v(-105.72, 51.67) * mm});
            skLineSegment(sketch, "E3131", {"start": v(-105.72, 51.67) * mm, "end": v(-105.84, 51.68) * mm});
            skLineSegment(sketch, "E3132", {"start": v(-105.84, 51.68) * mm, "end": v(-105.96, 51.7) * mm});
            skLineSegment(sketch, "E3133", {"start": v(-105.96, 51.7) * mm, "end": v(-106.08, 51.72) * mm});
            skLineSegment(sketch, "E3134", {"start": v(-106.08, 51.72) * mm, "end": v(-106.32, 51.75) * mm});
            skLineSegment(sketch, "E3135", {"start": v(-106.32, 51.75) * mm, "end": v(-106.57, 51.78) * mm});
            skLineSegment(sketch, "E3136", {"start": v(-106.57, 51.78) * mm, "end": v(-106.7, 51.8) * mm});
            skLineSegment(sketch, "E3137", {"start": v(-106.7, 51.8) * mm, "end": v(-107.08, 51.83) * mm});
            skLineSegment(sketch, "E3138", {"start": v(-107.08, 51.83) * mm, "end": v(-107.2, 51.85) * mm});
            skLineSegment(sketch, "E3139", {"start": v(-107.2, 51.85) * mm, "end": v(-107.34, 51.86) * mm});
            skLineSegment(sketch, "E3140", {"start": v(-107.34, 51.86) * mm, "end": v(-107.47, 51.87) * mm});
            skLineSegment(sketch, "E3141", {"start": v(-107.47, 51.87) * mm, "end": v(-107.74, 51.9) * mm});
            skLineSegment(sketch, "E3142", {"start": v(-107.74, 51.9) * mm, "end": v(-107.88, 51.9) * mm});
            skLineSegment(sketch, "E3143", {"start": v(-107.88, 51.9) * mm, "end": v(-108.02, 51.92) * mm});
            skLineSegment(sketch, "E3144", {"start": v(-108.02, 51.92) * mm, "end": v(-108.16, 51.93) * mm});
            skLineSegment(sketch, "E3145", {"start": v(-108.16, 51.93) * mm, "end": v(-108.3, 51.94) * mm});
            skLineSegment(sketch, "E3146", {"start": v(-108.3, 51.94) * mm, "end": v(-108.44, 51.95) * mm});
            skLineSegment(sketch, "E3147", {"start": v(-108.44, 51.95) * mm, "end": v(-108.72, 51.97) * mm});
            skLineSegment(sketch, "E3148", {"start": v(-108.72, 51.97) * mm, "end": v(-108.87, 51.98) * mm});
            skLineSegment(sketch, "E3149", {"start": v(-108.87, 51.98) * mm, "end": v(-109.01, 51.99) * mm});
            skLineSegment(sketch, "E3150", {"start": v(-109.01, 51.99) * mm, "end": v(-109.16, 52) * mm});
            skLineSegment(sketch, "E3151", {"start": v(-109.16, 52) * mm, "end": v(-109.31, 52) * mm});
            skLineSegment(sketch, "E3152", {"start": v(-109.31, 52) * mm, "end": v(-109.46, 52.01) * mm});
            skLineSegment(sketch, "E3153", {"start": v(-109.46, 52.01) * mm, "end": v(-109.56, 52) * mm});
            skLineSegment(sketch, "E3154", {"start": v(-109.56, 52) * mm, "end": v(-110.26, 50.49) * mm});
            skLineSegment(sketch, "E3155", {"start": v(-110.26, 50.49) * mm, "end": v(-110.2, 50.4) * mm});
            skLineSegment(sketch, "E3156", {"start": v(-110.2, 50.4) * mm, "end": v(-110, 50.19) * mm});
            skLineSegment(sketch, "E3157", {"start": v(-110, 50.19) * mm, "end": v(-109.9, 50.08) * mm});
            skLineSegment(sketch, "E3158", {"start": v(-109.9, 50.08) * mm, "end": v(-109.8, 49.97) * mm});
            skLineSegment(sketch, "E3159", {"start": v(-109.8, 49.97) * mm, "end": v(-109.6, 49.76) * mm});
            skLineSegment(sketch, "E3160", {"start": v(-109.6, 49.76) * mm, "end": v(-109.5, 49.66) * mm});
            skLineSegment(sketch, "E3161", {"start": v(-109.5, 49.66) * mm, "end": v(-109.4, 49.56) * mm});
            skLineSegment(sketch, "E3162", {"start": v(-109.4, 49.56) * mm, "end": v(-109.3, 49.46) * mm});
            skLineSegment(sketch, "E3163", {"start": v(-109.3, 49.46) * mm, "end": v(-109.2, 49.36) * mm});
            skLineSegment(sketch, "E3164", {"start": v(-109.2, 49.36) * mm, "end": v(-109.11, 49.26) * mm});
            skLineSegment(sketch, "E3165", {"start": v(-109.11, 49.26) * mm, "end": v(-109.02, 49.16) * mm});
            skLineSegment(sketch, "E3166", {"start": v(-109.02, 49.16) * mm, "end": v(-108.92, 49.07) * mm});
            skLineSegment(sketch, "E3167", {"start": v(-108.92, 49.07) * mm, "end": v(-108.82, 48.97) * mm});
            skLineSegment(sketch, "E3168", {"start": v(-108.82, 48.97) * mm, "end": v(-108.73, 48.88) * mm});
            skLineSegment(sketch, "E3169", {"start": v(-108.73, 48.88) * mm, "end": v(-108.54, 48.7) * mm});
            skLineSegment(sketch, "E3170", {"start": v(-108.54, 48.7) * mm, "end": v(-108.45, 48.6) * mm});
            skLineSegment(sketch, "E3171", {"start": v(-108.45, 48.6) * mm, "end": v(-108.35, 48.52) * mm});
            skLineSegment(sketch, "E3172", {"start": v(-108.35, 48.52) * mm, "end": v(-108.26, 48.43) * mm});
            skLineSegment(sketch, "E3173", {"start": v(-108.26, 48.43) * mm, "end": v(-108.17, 48.34) * mm});
            skLineSegment(sketch, "E3174", {"start": v(-108.17, 48.34) * mm, "end": v(-107.99, 48.17) * mm});
            skLineSegment(sketch, "E3175", {"start": v(-107.99, 48.17) * mm, "end": v(-107.9, 48.09) * mm});
            skLineSegment(sketch, "E3176", {"start": v(-107.9, 48.09) * mm, "end": v(-107.8, 48) * mm});
            skLineSegment(sketch, "E3177", {"start": v(-107.8, 48) * mm, "end": v(-107.72, 47.92) * mm});
            skLineSegment(sketch, "E3178", {"start": v(-107.72, 47.92) * mm, "end": v(-107.63, 47.84) * mm});
            skLineSegment(sketch, "E3179", {"start": v(-107.63, 47.84) * mm, "end": v(-107.54, 47.76) * mm});
            skLineSegment(sketch, "E3180", {"start": v(-107.54, 47.76) * mm, "end": v(-107.45, 47.69) * mm});
            skLineSegment(sketch, "E3181", {"start": v(-107.45, 47.69) * mm, "end": v(-107.37, 47.6) * mm});
            skLineSegment(sketch, "E3182", {"start": v(-107.37, 47.6) * mm, "end": v(-107.2, 47.46) * mm});
            skLineSegment(sketch, "E3183", {"start": v(-107.2, 47.46) * mm, "end": v(-107.11, 47.38) * mm});
            skLineSegment(sketch, "E3184", {"start": v(-107.11, 47.38) * mm, "end": v(-107.03, 47.3) * mm});
            skLineSegment(sketch, "E3185", {"start": v(-107.03, 47.3) * mm, "end": v(-106.94, 47.24) * mm});
            skLineSegment(sketch, "E3186", {"start": v(-106.94, 47.24) * mm, "end": v(-106.78, 47.1) * mm});
            skLineSegment(sketch, "E3187", {"start": v(-106.78, 47.1) * mm, "end": v(-107, 46.15) * mm});
            skLineSegment(sketch, "E3188", {"start": v(-107, 46.15) * mm, "end": v(-107.54, 45.34) * mm});
            skLineSegment(sketch, "E3189", {"start": v(-107.54, 45.34) * mm, "end": v(-107.64, 45.35) * mm});
            skLineSegment(sketch, "E3190", {"start": v(-107.64, 45.35) * mm, "end": v(-107.75, 45.36) * mm});
            skLineSegment(sketch, "E3191", {"start": v(-107.75, 45.36) * mm, "end": v(-107.86, 45.37) * mm});
            skLineSegment(sketch, "E3192", {"start": v(-107.86, 45.37) * mm, "end": v(-107.97, 45.38) * mm});
            skLineSegment(sketch, "E3193", {"start": v(-107.97, 45.38) * mm, "end": v(-108.09, 45.4) * mm});
            skLineSegment(sketch, "E3194", {"start": v(-108.09, 45.4) * mm, "end": v(-108.31, 45.41) * mm});
            skLineSegment(sketch, "E3195", {"start": v(-108.31, 45.41) * mm, "end": v(-108.43, 45.42) * mm});
            skLineSegment(sketch, "E3196", {"start": v(-108.43, 45.42) * mm, "end": v(-108.55, 45.43) * mm});
            skLineSegment(sketch, "E3197", {"start": v(-108.55, 45.43) * mm, "end": v(-108.66, 45.44) * mm});
            skLineSegment(sketch, "E3198", {"start": v(-108.66, 45.44) * mm, "end": v(-108.78, 45.45) * mm});
            skLineSegment(sketch, "E3199", {"start": v(-108.78, 45.45) * mm, "end": v(-108.9, 45.46) * mm});
            skLineSegment(sketch, "E3200", {"start": v(-108.9, 45.46) * mm, "end": v(-109.02, 45.47) * mm});
            skLineSegment(sketch, "E3201", {"start": v(-109.02, 45.47) * mm, "end": v(-109.15, 45.48) * mm});
            skLineSegment(sketch, "E3202", {"start": v(-109.15, 45.48) * mm, "end": v(-109.27, 45.49) * mm});
            skLineSegment(sketch, "E3203", {"start": v(-109.27, 45.49) * mm, "end": v(-109.4, 45.5) * mm});
            skLineSegment(sketch, "E3204", {"start": v(-109.4, 45.5) * mm, "end": v(-109.65, 45.5) * mm});
            skLineSegment(sketch, "E3205", {"start": v(-109.65, 45.5) * mm, "end": v(-109.9, 45.52) * mm});
            skLineSegment(sketch, "E3206", {"start": v(-109.9, 45.52) * mm, "end": v(-110.04, 45.52) * mm});
            skLineSegment(sketch, "E3207", {"start": v(-110.04, 45.52) * mm, "end": v(-110.17, 45.53) * mm});
            skLineSegment(sketch, "E3208", {"start": v(-110.17, 45.53) * mm, "end": v(-110.3, 45.53) * mm});
            skLineSegment(sketch, "E3209", {"start": v(-110.3, 45.53) * mm, "end": v(-110.44, 45.54) * mm});
            skLineSegment(sketch, "E3210", {"start": v(-110.44, 45.54) * mm, "end": v(-110.58, 45.54) * mm});
            skLineSegment(sketch, "E3211", {"start": v(-110.58, 45.54) * mm, "end": v(-110.71, 45.55) * mm});
            skLineSegment(sketch, "E3212", {"start": v(-110.71, 45.55) * mm, "end": v(-110.85, 45.55) * mm});
            skLineSegment(sketch, "E3213", {"start": v(-110.85, 45.55) * mm, "end": v(-111, 45.55) * mm});
            skLineSegment(sketch, "E3214", {"start": v(-111, 45.55) * mm, "end": v(-111.13, 45.56) * mm});
            skLineSegment(sketch, "E3215", {"start": v(-111.13, 45.56) * mm, "end": v(-111.27, 45.56) * mm});
            skLineSegment(sketch, "E3216", {"start": v(-111.27, 45.56) * mm, "end": v(-111.56, 45.56) * mm});
            skLineSegment(sketch, "E3217", {"start": v(-111.56, 45.56) * mm, "end": v(-111.7, 45.56) * mm});
            skLineSegment(sketch, "E3218", {"start": v(-111.7, 45.56) * mm, "end": v(-112, 45.56) * mm});
            skLineSegment(sketch, "E3219", {"start": v(-112, 45.56) * mm, "end": v(-112.15, 45.56) * mm});
            skLineSegment(sketch, "E3220", {"start": v(-112.15, 45.56) * mm, "end": v(-112.3, 45.56) * mm});
            skLineSegment(sketch, "E3221", {"start": v(-112.3, 45.56) * mm, "end": v(-112.4, 45.54) * mm});
            skLineSegment(sketch, "E3222", {"start": v(-112.4, 45.54) * mm, "end": v(-113, 44) * mm});
            skLineSegment(sketch, "E3223", {"start": v(-113, 44) * mm, "end": v(-112.96, 43.91) * mm});
            skLineSegment(sketch, "E3224", {"start": v(-112.96, 43.91) * mm, "end": v(-112.85, 43.8) * mm});
            skLineSegment(sketch, "E3225", {"start": v(-112.85, 43.8) * mm, "end": v(-112.63, 43.6) * mm});
            skLineSegment(sketch, "E3226", {"start": v(-112.63, 43.6) * mm, "end": v(-112.52, 43.5) * mm});
            skLineSegment(sketch, "E3227", {"start": v(-112.52, 43.5) * mm, "end": v(-112.42, 43.4) * mm});
            skLineSegment(sketch, "E3228", {"start": v(-112.42, 43.4) * mm, "end": v(-112.31, 43.3) * mm});
            skLineSegment(sketch, "E3229", {"start": v(-112.31, 43.3) * mm, "end": v(-112.2, 43.2) * mm});
            skLineSegment(sketch, "E3230", {"start": v(-112.2, 43.2) * mm, "end": v(-112.1, 43.11) * mm});
            skLineSegment(sketch, "E3231", {"start": v(-112.1, 43.11) * mm, "end": v(-112, 43.02) * mm});
            skLineSegment(sketch, "E3232", {"start": v(-112, 43.02) * mm, "end": v(-111.9, 42.93) * mm});
            skLineSegment(sketch, "E3233", {"start": v(-111.9, 42.93) * mm, "end": v(-111.8, 42.83) * mm});
            skLineSegment(sketch, "E3234", {"start": v(-111.8, 42.83) * mm, "end": v(-111.69, 42.74) * mm});
            skLineSegment(sketch, "E3235", {"start": v(-111.69, 42.74) * mm, "end": v(-111.59, 42.65) * mm});
            skLineSegment(sketch, "E3236", {"start": v(-111.59, 42.65) * mm, "end": v(-111.49, 42.56) * mm});
            skLineSegment(sketch, "E3237", {"start": v(-111.49, 42.56) * mm, "end": v(-111.39, 42.48) * mm});
            skLineSegment(sketch, "E3238", {"start": v(-111.39, 42.48) * mm, "end": v(-111.29, 42.39) * mm});
            skLineSegment(sketch, "E3239", {"start": v(-111.29, 42.39) * mm, "end": v(-111.19, 42.3) * mm});
            skLineSegment(sketch, "E3240", {"start": v(-111.19, 42.3) * mm, "end": v(-111.09, 42.22) * mm});
            skLineSegment(sketch, "E3241", {"start": v(-111.09, 42.22) * mm, "end": v(-110.99, 42.14) * mm});
            skLineSegment(sketch, "E3242", {"start": v(-110.99, 42.14) * mm, "end": v(-110.9, 42.05) * mm});
            skLineSegment(sketch, "E3243", {"start": v(-110.9, 42.05) * mm, "end": v(-110.8, 41.97) * mm});
            skLineSegment(sketch, "E3244", {"start": v(-110.8, 41.97) * mm, "end": v(-110.7, 41.9) * mm});
            skLineSegment(sketch, "E3245", {"start": v(-110.7, 41.9) * mm, "end": v(-110.6, 41.81) * mm});
            skLineSegment(sketch, "E3246", {"start": v(-110.6, 41.81) * mm, "end": v(-110.5, 41.73) * mm});
            skLineSegment(sketch, "E3247", {"start": v(-110.5, 41.73) * mm, "end": v(-110.41, 41.66) * mm});
            skLineSegment(sketch, "E3248", {"start": v(-110.41, 41.66) * mm, "end": v(-110.32, 41.58) * mm});
            skLineSegment(sketch, "E3249", {"start": v(-110.32, 41.58) * mm, "end": v(-110.23, 41.5) * mm});
            skLineSegment(sketch, "E3250", {"start": v(-110.23, 41.5) * mm, "end": v(-110.04, 41.36) * mm});
            skLineSegment(sketch, "E3251", {"start": v(-110.04, 41.36) * mm, "end": v(-109.95, 41.28) * mm});
            skLineSegment(sketch, "E3252", {"start": v(-109.95, 41.28) * mm, "end": v(-109.77, 41.14) * mm});
            skLineSegment(sketch, "E3253", {"start": v(-109.77, 41.14) * mm, "end": v(-109.68, 41.08) * mm});
            skLineSegment(sketch, "E3254", {"start": v(-109.68, 41.08) * mm, "end": v(-109.6, 41) * mm});
            skLineSegment(sketch, "E3255", {"start": v(-109.6, 41) * mm, "end": v(-109.42, 40.87) * mm});
            skLineSegment(sketch, "E3256", {"start": v(-109.42, 40.87) * mm, "end": v(-109.33, 40.8) * mm});
            skLineSegment(sketch, "E3257", {"start": v(-109.33, 40.8) * mm, "end": v(-109.5, 39.85) * mm});
            skLineSegment(sketch, "E3258", {"start": v(-109.5, 39.85) * mm, "end": v(-110, 39) * mm});
            skLineSegment(sketch, "E3259", {"start": v(-110, 39) * mm, "end": v(-110.1, 39.01) * mm});
            skLineSegment(sketch, "E3260", {"start": v(-110.1, 39.01) * mm, "end": v(-110.2, 39.02) * mm});
            skLineSegment(sketch, "E3261", {"start": v(-110.2, 39.02) * mm, "end": v(-110.32, 39.02) * mm});
            skLineSegment(sketch, "E3262", {"start": v(-110.32, 39.02) * mm, "end": v(-110.43, 39.03) * mm});
            skLineSegment(sketch, "E3263", {"start": v(-110.43, 39.03) * mm, "end": v(-110.66, 39.03) * mm});
            skLineSegment(sketch, "E3264", {"start": v(-110.66, 39.03) * mm, "end": v(-110.77, 39.04) * mm});
            skLineSegment(sketch, "E3265", {"start": v(-110.77, 39.04) * mm, "end": v(-110.89, 39.04) * mm});
            skLineSegment(sketch, "E3266", {"start": v(-110.89, 39.04) * mm, "end": v(-111, 39.04) * mm});
            skLineSegment(sketch, "E3267", {"start": v(-111, 39.04) * mm, "end": v(-111.12, 39.05) * mm});
            skLineSegment(sketch, "E3268", {"start": v(-111.12, 39.05) * mm, "end": v(-111.24, 39.05) * mm});
            skLineSegment(sketch, "E3269", {"start": v(-111.24, 39.05) * mm, "end": v(-111.36, 39.05) * mm});
            skLineSegment(sketch, "E3270", {"start": v(-111.36, 39.05) * mm, "end": v(-111.6, 39.05) * mm});
            skLineSegment(sketch, "E3271", {"start": v(-111.6, 39.05) * mm, "end": v(-112.11, 39.05) * mm});
            skLineSegment(sketch, "E3272", {"start": v(-112.11, 39.05) * mm, "end": v(-112.24, 39.05) * mm});
            skLineSegment(sketch, "E3273", {"start": v(-112.24, 39.05) * mm, "end": v(-112.5, 39.05) * mm});
            skLineSegment(sketch, "E3274", {"start": v(-112.5, 39.05) * mm, "end": v(-112.63, 39.05) * mm});
            skLineSegment(sketch, "E3275", {"start": v(-112.63, 39.05) * mm, "end": v(-112.77, 39.04) * mm});
            skLineSegment(sketch, "E3276", {"start": v(-112.77, 39.04) * mm, "end": v(-112.9, 39.04) * mm});
            skLineSegment(sketch, "E3277", {"start": v(-112.9, 39.04) * mm, "end": v(-113.04, 39.04) * mm});
            skLineSegment(sketch, "E3278", {"start": v(-113.04, 39.04) * mm, "end": v(-113.31, 39.03) * mm});
            skLineSegment(sketch, "E3279", {"start": v(-113.31, 39.03) * mm, "end": v(-113.45, 39.02) * mm});
            skLineSegment(sketch, "E3280", {"start": v(-113.45, 39.02) * mm, "end": v(-113.6, 39.02) * mm});
            skLineSegment(sketch, "E3281", {"start": v(-113.6, 39.02) * mm, "end": v(-113.73, 39.01) * mm});
            skLineSegment(sketch, "E3282", {"start": v(-113.73, 39.01) * mm, "end": v(-113.88, 39) * mm});
            skLineSegment(sketch, "E3283", {"start": v(-113.88, 39) * mm, "end": v(-114.02, 39) * mm});
            skLineSegment(sketch, "E3284", {"start": v(-114.02, 39) * mm, "end": v(-114.17, 39) * mm});
            skLineSegment(sketch, "E3285", {"start": v(-114.17, 39) * mm, "end": v(-114.31, 38.98) * mm});
            skLineSegment(sketch, "E3286", {"start": v(-114.31, 38.98) * mm, "end": v(-114.46, 38.97) * mm});
            skLineSegment(sketch, "E3287", {"start": v(-114.46, 38.97) * mm, "end": v(-114.6, 38.96) * mm});
            skLineSegment(sketch, "E3288", {"start": v(-114.6, 38.96) * mm, "end": v(-114.76, 38.95) * mm});
            skLineSegment(sketch, "E3289", {"start": v(-114.76, 38.95) * mm, "end": v(-114.85, 38.92) * mm});
            skLineSegment(sketch, "E3290", {"start": v(-114.85, 38.92) * mm, "end": v(-115.37, 37.35) * mm});
            skLineSegment(sketch, "E3291", {"start": v(-115.37, 37.35) * mm, "end": v(-115.32, 37.27) * mm});
            skLineSegment(sketch, "E3292", {"start": v(-115.32, 37.27) * mm, "end": v(-115.09, 37.08) * mm});
            skLineSegment(sketch, "E3293", {"start": v(-115.09, 37.08) * mm, "end": v(-114.98, 36.98) * mm});
            skLineSegment(sketch, "E3294", {"start": v(-114.98, 36.98) * mm, "end": v(-114.86, 36.89) * mm});
            skLineSegment(sketch, "E3295", {"start": v(-114.86, 36.89) * mm, "end": v(-114.64, 36.7) * mm});
            skLineSegment(sketch, "E3296", {"start": v(-114.64, 36.7) * mm, "end": v(-114.42, 36.52) * mm});
            skLineSegment(sketch, "E3297", {"start": v(-114.42, 36.52) * mm, "end": v(-114.2, 36.35) * mm});
            skLineSegment(sketch, "E3298", {"start": v(-114.2, 36.35) * mm, "end": v(-114.1, 36.26) * mm});
            skLineSegment(sketch, "E3299", {"start": v(-114.1, 36.26) * mm, "end": v(-113.99, 36.18) * mm});
            skLineSegment(sketch, "E3300", {"start": v(-113.99, 36.18) * mm, "end": v(-113.88, 36.1) * mm});
            skLineSegment(sketch, "E3301", {"start": v(-113.88, 36.1) * mm, "end": v(-113.67, 35.93) * mm});
            skLineSegment(sketch, "E3302", {"start": v(-113.67, 35.93) * mm, "end": v(-113.46, 35.77) * mm});
            skLineSegment(sketch, "E3303", {"start": v(-113.46, 35.77) * mm, "end": v(-113.35, 35.69) * mm});
            skLineSegment(sketch, "E3304", {"start": v(-113.35, 35.69) * mm, "end": v(-113.25, 35.6) * mm});
            skLineSegment(sketch, "E3305", {"start": v(-113.25, 35.6) * mm, "end": v(-113.15, 35.53) * mm});
            skLineSegment(sketch, "E3306", {"start": v(-113.15, 35.53) * mm, "end": v(-113.05, 35.46) * mm});
            skLineSegment(sketch, "E3307", {"start": v(-113.05, 35.46) * mm, "end": v(-112.95, 35.38) * mm});
            skLineSegment(sketch, "E3308", {"start": v(-112.95, 35.38) * mm, "end": v(-112.85, 35.3) * mm});
            skLineSegment(sketch, "E3309", {"start": v(-112.85, 35.3) * mm, "end": v(-112.75, 35.24) * mm});
            skLineSegment(sketch, "E3310", {"start": v(-112.75, 35.24) * mm, "end": v(-112.65, 35.16) * mm});
            skLineSegment(sketch, "E3311", {"start": v(-112.65, 35.16) * mm, "end": v(-112.55, 35.1) * mm});
            skLineSegment(sketch, "E3312", {"start": v(-112.55, 35.1) * mm, "end": v(-112.45, 35.02) * mm});
            skLineSegment(sketch, "E3313", {"start": v(-112.45, 35.02) * mm, "end": v(-112.26, 34.89) * mm});
            skLineSegment(sketch, "E3314", {"start": v(-112.26, 34.89) * mm, "end": v(-112.17, 34.82) * mm});
            skLineSegment(sketch, "E3315", {"start": v(-112.17, 34.82) * mm, "end": v(-111.98, 34.7) * mm});
            skLineSegment(sketch, "E3316", {"start": v(-111.98, 34.7) * mm, "end": v(-111.89, 34.63) * mm});
            skLineSegment(sketch, "E3317", {"start": v(-111.89, 34.63) * mm, "end": v(-111.8, 34.57) * mm});
            skLineSegment(sketch, "E3318", {"start": v(-111.8, 34.57) * mm, "end": v(-111.7, 34.5) * mm});
            skLineSegment(sketch, "E3319", {"start": v(-111.7, 34.5) * mm, "end": v(-111.61, 34.44) * mm});
            skLineSegment(sketch, "E3320", {"start": v(-111.61, 34.44) * mm, "end": v(-111.52, 34.38) * mm});
            skLineSegment(sketch, "E3321", {"start": v(-111.52, 34.38) * mm, "end": v(-111.63, 33.41) * mm});
            skLineSegment(sketch, "E3322", {"start": v(-111.63, 33.41) * mm, "end": v(-112.07, 32.55) * mm});
            skLineSegment(sketch, "E3323", {"start": v(-112.07, 32.55) * mm, "end": v(-112.3, 32.54) * mm});
            skLineSegment(sketch, "E3324", {"start": v(-112.3, 32.54) * mm, "end": v(-112.51, 32.54) * mm});
            skLineSegment(sketch, "E3325", {"start": v(-112.51, 32.54) * mm, "end": v(-112.62, 32.54) * mm});
            skLineSegment(sketch, "E3326", {"start": v(-112.62, 32.54) * mm, "end": v(-112.85, 32.53) * mm});
            skLineSegment(sketch, "E3327", {"start": v(-112.85, 32.53) * mm, "end": v(-112.97, 32.53) * mm});
            skLineSegment(sketch, "E3328", {"start": v(-112.97, 32.53) * mm, "end": v(-113.09, 32.52) * mm});
            skLineSegment(sketch, "E3329", {"start": v(-113.09, 32.52) * mm, "end": v(-113.2, 32.52) * mm});
            skLineSegment(sketch, "E3330", {"start": v(-113.2, 32.52) * mm, "end": v(-113.32, 32.51) * mm});
            skLineSegment(sketch, "E3331", {"start": v(-113.32, 32.51) * mm, "end": v(-113.44, 32.5) * mm});
            skLineSegment(sketch, "E3332", {"start": v(-113.44, 32.5) * mm, "end": v(-113.69, 32.5) * mm});
            skLineSegment(sketch, "E3333", {"start": v(-113.69, 32.5) * mm, "end": v(-113.81, 32.5) * mm});
            skLineSegment(sketch, "E3334", {"start": v(-113.81, 32.5) * mm, "end": v(-113.94, 32.48) * mm});
            skLineSegment(sketch, "E3335", {"start": v(-113.94, 32.48) * mm, "end": v(-114.06, 32.48) * mm});
            skLineSegment(sketch, "E3336", {"start": v(-114.06, 32.48) * mm, "end": v(-114.2, 32.47) * mm});
            skLineSegment(sketch, "E3337", {"start": v(-114.2, 32.47) * mm, "end": v(-114.32, 32.46) * mm});
            skLineSegment(sketch, "E3338", {"start": v(-114.32, 32.46) * mm, "end": v(-114.45, 32.45) * mm});
            skLineSegment(sketch, "E3339", {"start": v(-114.45, 32.45) * mm, "end": v(-114.58, 32.44) * mm});
            skLineSegment(sketch, "E3340", {"start": v(-114.58, 32.44) * mm, "end": v(-114.71, 32.43) * mm});
            skLineSegment(sketch, "E3341", {"start": v(-114.71, 32.43) * mm, "end": v(-114.98, 32.41) * mm});
            skLineSegment(sketch, "E3342", {"start": v(-114.98, 32.41) * mm, "end": v(-115.12, 32.4) * mm});
            skLineSegment(sketch, "E3343", {"start": v(-115.12, 32.4) * mm, "end": v(-115.25, 32.39) * mm});
            skLineSegment(sketch, "E3344", {"start": v(-115.25, 32.39) * mm, "end": v(-115.4, 32.37) * mm});
            skLineSegment(sketch, "E3345", {"start": v(-115.4, 32.37) * mm, "end": v(-115.53, 32.36) * mm});
            skLineSegment(sketch, "E3346", {"start": v(-115.53, 32.36) * mm, "end": v(-115.81, 32.33) * mm});
            skLineSegment(sketch, "E3347", {"start": v(-115.81, 32.33) * mm, "end": v(-115.95, 32.32) * mm});
            skLineSegment(sketch, "E3348", {"start": v(-115.95, 32.32) * mm, "end": v(-116.1, 32.3) * mm});
            skLineSegment(sketch, "E3349", {"start": v(-116.1, 32.3) * mm, "end": v(-116.24, 32.29) * mm});
            skLineSegment(sketch, "E3350", {"start": v(-116.24, 32.29) * mm, "end": v(-116.53, 32.25) * mm});
            skLineSegment(sketch, "E3351", {"start": v(-116.53, 32.25) * mm, "end": v(-116.68, 32.24) * mm});
            skLineSegment(sketch, "E3352", {"start": v(-116.68, 32.24) * mm, "end": v(-116.83, 32.22) * mm});
            skLineSegment(sketch, "E3353", {"start": v(-116.83, 32.22) * mm, "end": v(-116.92, 32.18) * mm});
            skLineSegment(sketch, "E3354", {"start": v(-116.92, 32.18) * mm, "end": v(-117.35, 30.58) * mm});
            skLineSegment(sketch, "E3355", {"start": v(-117.35, 30.58) * mm, "end": v(-117.29, 30.5) * mm});
            skLineSegment(sketch, "E3356", {"start": v(-117.29, 30.5) * mm, "end": v(-117.17, 30.41) * mm});
            skLineSegment(sketch, "E3357", {"start": v(-117.17, 30.41) * mm, "end": v(-117.05, 30.32) * mm});
            skLineSegment(sketch, "E3358", {"start": v(-117.05, 30.32) * mm, "end": v(-116.93, 30.23) * mm});
            skLineSegment(sketch, "E3359", {"start": v(-116.93, 30.23) * mm, "end": v(-116.81, 30.15) * mm});
            skLineSegment(sketch, "E3360", {"start": v(-116.81, 30.15) * mm, "end": v(-116.7, 30.06) * mm});
            skLineSegment(sketch, "E3361", {"start": v(-116.7, 30.06) * mm, "end": v(-116.58, 29.98) * mm});
            skLineSegment(sketch, "E3362", {"start": v(-116.58, 29.98) * mm, "end": v(-116.46, 29.9) * mm});
            skLineSegment(sketch, "E3363", {"start": v(-116.46, 29.9) * mm, "end": v(-116.35, 29.8) * mm});
            skLineSegment(sketch, "E3364", {"start": v(-116.35, 29.8) * mm, "end": v(-116.23, 29.73) * mm});
            skLineSegment(sketch, "E3365", {"start": v(-116.23, 29.73) * mm, "end": v(-116.12, 29.65) * mm});
            skLineSegment(sketch, "E3366", {"start": v(-116.12, 29.65) * mm, "end": v(-116, 29.57) * mm});
            skLineSegment(sketch, "E3367", {"start": v(-116, 29.57) * mm, "end": v(-115.9, 29.49) * mm});
            skLineSegment(sketch, "E3368", {"start": v(-115.9, 29.49) * mm, "end": v(-115.67, 29.33) * mm});
            skLineSegment(sketch, "E3369", {"start": v(-115.67, 29.33) * mm, "end": v(-115.56, 29.26) * mm});
            skLineSegment(sketch, "E3370", {"start": v(-115.56, 29.26) * mm, "end": v(-115.35, 29.1) * mm});
            skLineSegment(sketch, "E3371", {"start": v(-115.35, 29.1) * mm, "end": v(-115.13, 28.96) * mm});
            skLineSegment(sketch, "E3372", {"start": v(-115.13, 28.96) * mm, "end": v(-114.92, 28.82) * mm});
            skLineSegment(sketch, "E3373", {"start": v(-114.92, 28.82) * mm, "end": v(-114.81, 28.76) * mm});
            skLineSegment(sketch, "E3374", {"start": v(-114.81, 28.76) * mm, "end": v(-114.7, 28.69) * mm});
            skLineSegment(sketch, "E3375", {"start": v(-114.7, 28.69) * mm, "end": v(-114.6, 28.62) * mm});
            skLineSegment(sketch, "E3376", {"start": v(-114.6, 28.62) * mm, "end": v(-114.5, 28.56) * mm});
            skLineSegment(sketch, "E3377", {"start": v(-114.5, 28.56) * mm, "end": v(-114.4, 28.5) * mm});
            skLineSegment(sketch, "E3378", {"start": v(-114.4, 28.5) * mm, "end": v(-114.2, 28.36) * mm});
            skLineSegment(sketch, "E3379", {"start": v(-114.2, 28.36) * mm, "end": v(-114.1, 28.3) * mm});
            skLineSegment(sketch, "E3380", {"start": v(-114.1, 28.3) * mm, "end": v(-114, 28.24) * mm});
            skLineSegment(sketch, "E3381", {"start": v(-114, 28.24) * mm, "end": v(-113.9, 28.18) * mm});
            skLineSegment(sketch, "E3382", {"start": v(-113.9, 28.18) * mm, "end": v(-113.8, 28.12) * mm});
            skLineSegment(sketch, "E3383", {"start": v(-113.8, 28.12) * mm, "end": v(-113.71, 28.06) * mm});
            skLineSegment(sketch, "E3384", {"start": v(-113.71, 28.06) * mm, "end": v(-113.62, 28) * mm});
            skLineSegment(sketch, "E3385", {"start": v(-113.62, 28) * mm, "end": v(-113.52, 27.95) * mm});
            skLineSegment(sketch, "E3386", {"start": v(-113.52, 27.95) * mm, "end": v(-113.43, 27.9) * mm});
            skLineSegment(sketch, "E3387", {"start": v(-113.43, 27.9) * mm, "end": v(-113.33, 27.84) * mm});
            skLineSegment(sketch, "E3388", {"start": v(-113.33, 27.84) * mm, "end": v(-113.39, 26.87) * mm});
            skLineSegment(sketch, "E3389", {"start": v(-113.39, 26.87) * mm, "end": v(-113.78, 25.97) * mm});
            skLineSegment(sketch, "E3390", {"start": v(-113.78, 25.97) * mm, "end": v(-113.88, 25.97) * mm});
            skLineSegment(sketch, "E3391", {"start": v(-113.88, 25.97) * mm, "end": v(-114, 25.96) * mm});
            skLineSegment(sketch, "E3392", {"start": v(-114, 25.96) * mm, "end": v(-114.1, 25.95) * mm});
            skLineSegment(sketch, "E3393", {"start": v(-114.1, 25.95) * mm, "end": v(-114.21, 25.94) * mm});
            skLineSegment(sketch, "E3394", {"start": v(-114.21, 25.94) * mm, "end": v(-114.33, 25.93) * mm});
            skLineSegment(sketch, "E3395", {"start": v(-114.33, 25.93) * mm, "end": v(-114.44, 25.92) * mm});
            skLineSegment(sketch, "E3396", {"start": v(-114.44, 25.92) * mm, "end": v(-114.55, 25.91) * mm});
            skLineSegment(sketch, "E3397", {"start": v(-114.55, 25.91) * mm, "end": v(-114.67, 25.9) * mm});
            skLineSegment(sketch, "E3398", {"start": v(-114.67, 25.9) * mm, "end": v(-114.9, 25.88) * mm});
            skLineSegment(sketch, "E3399", {"start": v(-114.9, 25.88) * mm, "end": v(-115.02, 25.87) * mm});
            skLineSegment(sketch, "E3400", {"start": v(-115.02, 25.87) * mm, "end": v(-115.14, 25.86) * mm});
            skLineSegment(sketch, "E3401", {"start": v(-115.14, 25.86) * mm, "end": v(-115.26, 25.85) * mm});
            skLineSegment(sketch, "E3402", {"start": v(-115.26, 25.85) * mm, "end": v(-115.39, 25.83) * mm});
            skLineSegment(sketch, "E3403", {"start": v(-115.39, 25.83) * mm, "end": v(-115.5, 25.82) * mm});
            skLineSegment(sketch, "E3404", {"start": v(-115.5, 25.82) * mm, "end": v(-115.63, 25.8) * mm});
            skLineSegment(sketch, "E3405", {"start": v(-115.63, 25.8) * mm, "end": v(-115.76, 25.79) * mm});
            skLineSegment(sketch, "E3406", {"start": v(-115.76, 25.79) * mm, "end": v(-115.89, 25.77) * mm});
            skLineSegment(sketch, "E3407", {"start": v(-115.89, 25.77) * mm, "end": v(-116.14, 25.74) * mm});
            skLineSegment(sketch, "E3408", {"start": v(-116.14, 25.74) * mm, "end": v(-116.27, 25.73) * mm});
            skLineSegment(sketch, "E3409", {"start": v(-116.27, 25.73) * mm, "end": v(-116.4, 25.7) * mm});
            skLineSegment(sketch, "E3410", {"start": v(-116.4, 25.7) * mm, "end": v(-116.54, 25.69) * mm});
            skLineSegment(sketch, "E3411", {"start": v(-116.54, 25.69) * mm, "end": v(-116.8, 25.65) * mm});
            skLineSegment(sketch, "E3412", {"start": v(-116.8, 25.65) * mm, "end": v(-117.08, 25.6) * mm});
            skLineSegment(sketch, "E3413", {"start": v(-117.08, 25.6) * mm, "end": v(-117.22, 25.59) * mm});
            skLineSegment(sketch, "E3414", {"start": v(-117.22, 25.59) * mm, "end": v(-117.5, 25.54) * mm});
            skLineSegment(sketch, "E3415", {"start": v(-117.5, 25.54) * mm, "end": v(-117.78, 25.5) * mm});
            skLineSegment(sketch, "E3416", {"start": v(-117.78, 25.5) * mm, "end": v(-118.06, 25.45) * mm});
            skLineSegment(sketch, "E3417", {"start": v(-118.06, 25.45) * mm, "end": v(-118.36, 25.4) * mm});
            skLineSegment(sketch, "E3418", {"start": v(-118.36, 25.4) * mm, "end": v(-118.5, 25.37) * mm});
            skLineSegment(sketch, "E3419", {"start": v(-118.5, 25.37) * mm, "end": v(-118.6, 25.33) * mm});
            skLineSegment(sketch, "E3420", {"start": v(-118.6, 25.33) * mm, "end": v(-118.93, 23.7) * mm});
            skLineSegment(sketch, "E3421", {"start": v(-118.93, 23.7) * mm, "end": v(-118.86, 23.63) * mm});
            skLineSegment(sketch, "E3422", {"start": v(-118.86, 23.63) * mm, "end": v(-118.74, 23.55) * mm});
            skLineSegment(sketch, "E3423", {"start": v(-118.74, 23.55) * mm, "end": v(-118.61, 23.47) * mm});
            skLineSegment(sketch, "E3424", {"start": v(-118.61, 23.47) * mm, "end": v(-118.37, 23.3) * mm});
            skLineSegment(sketch, "E3425", {"start": v(-118.37, 23.3) * mm, "end": v(-118.25, 23.22) * mm});
            skLineSegment(sketch, "E3426", {"start": v(-118.25, 23.22) * mm, "end": v(-118.13, 23.15) * mm});
            skLineSegment(sketch, "E3427", {"start": v(-118.13, 23.15) * mm, "end": v(-118, 23.07) * mm});
            skLineSegment(sketch, "E3428", {"start": v(-118, 23.07) * mm, "end": v(-117.89, 23) * mm});
            skLineSegment(sketch, "E3429", {"start": v(-117.89, 23) * mm, "end": v(-117.65, 22.84) * mm});
            skLineSegment(sketch, "E3430", {"start": v(-117.65, 22.84) * mm, "end": v(-117.53, 22.77) * mm});
            skLineSegment(sketch, "E3431", {"start": v(-117.53, 22.77) * mm, "end": v(-117.42, 22.7) * mm});
            skLineSegment(sketch, "E3432", {"start": v(-117.42, 22.7) * mm, "end": v(-117.3, 22.63) * mm});
            skLineSegment(sketch, "E3433", {"start": v(-117.3, 22.63) * mm, "end": v(-117.18, 22.56) * mm});
            skLineSegment(sketch, "E3434", {"start": v(-117.18, 22.56) * mm, "end": v(-117.07, 22.49) * mm});
            skLineSegment(sketch, "E3435", {"start": v(-117.07, 22.49) * mm, "end": v(-116.84, 22.35) * mm});
            skLineSegment(sketch, "E3436", {"start": v(-116.84, 22.35) * mm, "end": v(-116.62, 22.22) * mm});
            skLineSegment(sketch, "E3437", {"start": v(-116.62, 22.22) * mm, "end": v(-116.4, 22.1) * mm});
            skLineSegment(sketch, "E3438", {"start": v(-116.4, 22.1) * mm, "end": v(-116.3, 22.03) * mm});
            skLineSegment(sketch, "E3439", {"start": v(-116.3, 22.03) * mm, "end": v(-116.08, 21.9) * mm});
            skLineSegment(sketch, "E3440", {"start": v(-116.08, 21.9) * mm, "end": v(-115.97, 21.85) * mm});
            skLineSegment(sketch, "E3441", {"start": v(-115.97, 21.85) * mm, "end": v(-115.76, 21.73) * mm});
            skLineSegment(sketch, "E3442", {"start": v(-115.76, 21.73) * mm, "end": v(-115.66, 21.68) * mm});
            skLineSegment(sketch, "E3443", {"start": v(-115.66, 21.68) * mm, "end": v(-115.55, 21.62) * mm});
            skLineSegment(sketch, "E3444", {"start": v(-115.55, 21.62) * mm, "end": v(-115.35, 21.51) * mm});
            skLineSegment(sketch, "E3445", {"start": v(-115.35, 21.51) * mm, "end": v(-115.25, 21.46) * mm});
            skLineSegment(sketch, "E3446", {"start": v(-115.25, 21.46) * mm, "end": v(-115.05, 21.35) * mm});
            skLineSegment(sketch, "E3447", {"start": v(-115.05, 21.35) * mm, "end": v(-114.95, 21.3) * mm});
            skLineSegment(sketch, "E3448", {"start": v(-114.95, 21.3) * mm, "end": v(-114.76, 21.2) * mm});
            skLineSegment(sketch, "E3449", {"start": v(-114.76, 21.2) * mm, "end": v(-114.76, 20.23) * mm});
            skLineSegment(sketch, "E3450", {"start": v(-114.76, 20.23) * mm, "end": v(-115.1, 19.31) * mm});
            skLineSegment(sketch, "E3451", {"start": v(-115.1, 19.31) * mm, "end": v(-115.2, 19.3) * mm});
            skLineSegment(sketch, "E3452", {"start": v(-115.2, 19.3) * mm, "end": v(-115.3, 19.29) * mm});
            skLineSegment(sketch, "E3453", {"start": v(-115.3, 19.29) * mm, "end": v(-115.53, 19.26) * mm});
            skLineSegment(sketch, "E3454", {"start": v(-115.53, 19.26) * mm, "end": v(-115.75, 19.23) * mm});
            skLineSegment(sketch, "E3455", {"start": v(-115.75, 19.23) * mm, "end": v(-115.98, 19.2) * mm});
            skLineSegment(sketch, "E3456", {"start": v(-115.98, 19.2) * mm, "end": v(-116.1, 19.18) * mm});
            skLineSegment(sketch, "E3457", {"start": v(-116.1, 19.18) * mm, "end": v(-116.21, 19.16) * mm});
            skLineSegment(sketch, "E3458", {"start": v(-116.21, 19.16) * mm, "end": v(-116.33, 19.14) * mm});
            skLineSegment(sketch, "E3459", {"start": v(-116.33, 19.14) * mm, "end": v(-116.45, 19.12) * mm});
            skLineSegment(sketch, "E3460", {"start": v(-116.45, 19.12) * mm, "end": v(-116.7, 19.08) * mm});
            skLineSegment(sketch, "E3461", {"start": v(-116.7, 19.08) * mm, "end": v(-116.94, 19.04) * mm});
            skLineSegment(sketch, "E3462", {"start": v(-116.94, 19.04) * mm, "end": v(-117.06, 19.02) * mm});
            skLineSegment(sketch, "E3463", {"start": v(-117.06, 19.02) * mm, "end": v(-117.19, 19) * mm});
            skLineSegment(sketch, "E3464", {"start": v(-117.19, 19) * mm, "end": v(-117.32, 18.97) * mm});
            skLineSegment(sketch, "E3465", {"start": v(-117.32, 18.97) * mm, "end": v(-117.44, 18.95) * mm});
            skLineSegment(sketch, "E3466", {"start": v(-117.44, 18.95) * mm, "end": v(-117.57, 18.92) * mm});
            skLineSegment(sketch, "E3467", {"start": v(-117.57, 18.92) * mm, "end": v(-117.7, 18.9) * mm});
            skLineSegment(sketch, "E3468", {"start": v(-117.7, 18.9) * mm, "end": v(-117.83, 18.87) * mm});
            skLineSegment(sketch, "E3469", {"start": v(-117.83, 18.87) * mm, "end": v(-117.97, 18.84) * mm});
            skLineSegment(sketch, "E3470", {"start": v(-117.97, 18.84) * mm, "end": v(-118.1, 18.82) * mm});
            skLineSegment(sketch, "E3471", {"start": v(-118.1, 18.82) * mm, "end": v(-118.23, 18.79) * mm});
            skLineSegment(sketch, "E3472", {"start": v(-118.23, 18.79) * mm, "end": v(-118.37, 18.76) * mm});
            skLineSegment(sketch, "E3473", {"start": v(-118.37, 18.76) * mm, "end": v(-118.5, 18.73) * mm});
            skLineSegment(sketch, "E3474", {"start": v(-118.5, 18.73) * mm, "end": v(-118.64, 18.7) * mm});
            skLineSegment(sketch, "E3475", {"start": v(-118.64, 18.7) * mm, "end": v(-118.78, 18.67) * mm});
            skLineSegment(sketch, "E3476", {"start": v(-118.78, 18.67) * mm, "end": v(-118.92, 18.64) * mm});
            skLineSegment(sketch, "E3477", {"start": v(-118.92, 18.64) * mm, "end": v(-119.06, 18.6) * mm});
            skLineSegment(sketch, "E3478", {"start": v(-119.06, 18.6) * mm, "end": v(-119.34, 18.54) * mm});
            skLineSegment(sketch, "E3479", {"start": v(-119.34, 18.54) * mm, "end": v(-119.49, 18.5) * mm});
            skLineSegment(sketch, "E3480", {"start": v(-119.49, 18.5) * mm, "end": v(-119.63, 18.47) * mm});
            skLineSegment(sketch, "E3481", {"start": v(-119.63, 18.47) * mm, "end": v(-119.78, 18.44) * mm});
            skLineSegment(sketch, "E3482", {"start": v(-119.78, 18.44) * mm, "end": v(-119.86, 18.39) * mm});
            skLineSegment(sketch, "E3483", {"start": v(-119.86, 18.39) * mm, "end": v(-120.1, 16.75) * mm});
            skLineSegment(sketch, "E3484", {"start": v(-120.1, 16.75) * mm, "end": v(-120.04, 16.68) * mm});
            skLineSegment(sketch, "E3485", {"start": v(-120.04, 16.68) * mm, "end": v(-119.9, 16.6) * mm});
            skLineSegment(sketch, "E3486", {"start": v(-119.9, 16.6) * mm, "end": v(-119.65, 16.45) * mm});
            skLineSegment(sketch, "E3487", {"start": v(-119.65, 16.45) * mm, "end": v(-119.52, 16.38) * mm});
            skLineSegment(sketch, "E3488", {"start": v(-119.52, 16.38) * mm, "end": v(-119.4, 16.3) * mm});
            skLineSegment(sketch, "E3489", {"start": v(-119.4, 16.3) * mm, "end": v(-119.27, 16.24) * mm});
            skLineSegment(sketch, "E3490", {"start": v(-119.27, 16.24) * mm, "end": v(-119.15, 16.17) * mm});
            skLineSegment(sketch, "E3491", {"start": v(-119.15, 16.17) * mm, "end": v(-118.9, 16.03) * mm});
            skLineSegment(sketch, "E3492", {"start": v(-118.9, 16.03) * mm, "end": v(-118.66, 15.9) * mm});
            skLineSegment(sketch, "E3493", {"start": v(-118.66, 15.9) * mm, "end": v(-118.54, 15.83) * mm});
            skLineSegment(sketch, "E3494", {"start": v(-118.54, 15.83) * mm, "end": v(-118.42, 15.77) * mm});
            skLineSegment(sketch, "E3495", {"start": v(-118.42, 15.77) * mm, "end": v(-118.3, 15.7) * mm});
            skLineSegment(sketch, "E3496", {"start": v(-118.3, 15.7) * mm, "end": v(-118.18, 15.64) * mm});
            skLineSegment(sketch, "E3497", {"start": v(-118.18, 15.64) * mm, "end": v(-118.06, 15.58) * mm});
            skLineSegment(sketch, "E3498", {"start": v(-118.06, 15.58) * mm, "end": v(-117.94, 15.52) * mm});
            skLineSegment(sketch, "E3499", {"start": v(-117.94, 15.52) * mm, "end": v(-117.83, 15.46) * mm});
            skLineSegment(sketch, "E3500", {"start": v(-117.83, 15.46) * mm, "end": v(-117.71, 15.4) * mm});
            skLineSegment(sketch, "E3501", {"start": v(-117.71, 15.4) * mm, "end": v(-117.6, 15.34) * mm});
            skLineSegment(sketch, "E3502", {"start": v(-117.6, 15.34) * mm, "end": v(-117.49, 15.29) * mm});
            skLineSegment(sketch, "E3503", {"start": v(-117.49, 15.29) * mm, "end": v(-117.38, 15.23) * mm});
            skLineSegment(sketch, "E3504", {"start": v(-117.38, 15.23) * mm, "end": v(-117.26, 15.18) * mm});
            skLineSegment(sketch, "E3505", {"start": v(-117.26, 15.18) * mm, "end": v(-117.15, 15.12) * mm});
            skLineSegment(sketch, "E3506", {"start": v(-117.15, 15.12) * mm, "end": v(-117.05, 15.07) * mm});
            skLineSegment(sketch, "E3507", {"start": v(-117.05, 15.07) * mm, "end": v(-116.94, 15.02) * mm});
            skLineSegment(sketch, "E3508", {"start": v(-116.94, 15.02) * mm, "end": v(-116.72, 14.91) * mm});
            skLineSegment(sketch, "E3509", {"start": v(-116.72, 14.91) * mm, "end": v(-116.62, 14.87) * mm});
            skLineSegment(sketch, "E3510", {"start": v(-116.62, 14.87) * mm, "end": v(-116.51, 14.82) * mm});
            skLineSegment(sketch, "E3511", {"start": v(-116.51, 14.82) * mm, "end": v(-116.4, 14.77) * mm});
            skLineSegment(sketch, "E3512", {"start": v(-116.4, 14.77) * mm, "end": v(-116.3, 14.72) * mm});
            skLineSegment(sketch, "E3513", {"start": v(-116.3, 14.72) * mm, "end": v(-116.2, 14.67) * mm});
            skLineSegment(sketch, "E3514", {"start": v(-116.2, 14.67) * mm, "end": v(-116.1, 14.63) * mm});
            skLineSegment(sketch, "E3515", {"start": v(-116.1, 14.63) * mm, "end": v(-116, 14.58) * mm});
            skLineSegment(sketch, "E3516", {"start": v(-116, 14.58) * mm, "end": v(-115.8, 14.5) * mm});
            skLineSegment(sketch, "E3517", {"start": v(-115.8, 14.5) * mm, "end": v(-115.74, 13.52) * mm});
            skLineSegment(sketch, "E3518", {"start": v(-115.74, 13.52) * mm, "end": v(-116.02, 12.59) * mm});
            skLineSegment(sketch, "E3519", {"start": v(-116.02, 12.59) * mm, "end": v(-116.23, 12.55) * mm});
            skLineSegment(sketch, "E3520", {"start": v(-116.23, 12.55) * mm, "end": v(-116.34, 12.53) * mm});
            skLineSegment(sketch, "E3521", {"start": v(-116.34, 12.53) * mm, "end": v(-116.45, 12.5) * mm});
            skLineSegment(sketch, "E3522", {"start": v(-116.45, 12.5) * mm, "end": v(-116.56, 12.49) * mm});
            skLineSegment(sketch, "E3523", {"start": v(-116.56, 12.49) * mm, "end": v(-116.67, 12.46) * mm});
            skLineSegment(sketch, "E3524", {"start": v(-116.67, 12.46) * mm, "end": v(-116.79, 12.44) * mm});
            skLineSegment(sketch, "E3525", {"start": v(-116.79, 12.44) * mm, "end": v(-116.9, 12.42) * mm});
            skLineSegment(sketch, "E3526", {"start": v(-116.9, 12.42) * mm, "end": v(-117.02, 12.4) * mm});
            skLineSegment(sketch, "E3527", {"start": v(-117.02, 12.4) * mm, "end": v(-117.13, 12.37) * mm});
            skLineSegment(sketch, "E3528", {"start": v(-117.13, 12.37) * mm, "end": v(-117.37, 12.32) * mm});
            skLineSegment(sketch, "E3529", {"start": v(-117.37, 12.32) * mm, "end": v(-117.48, 12.29) * mm});
            skLineSegment(sketch, "E3530", {"start": v(-117.48, 12.29) * mm, "end": v(-117.6, 12.26) * mm});
            skLineSegment(sketch, "E3531", {"start": v(-117.6, 12.26) * mm, "end": v(-117.73, 12.23) * mm});
            skLineSegment(sketch, "E3532", {"start": v(-117.73, 12.23) * mm, "end": v(-117.97, 12.18) * mm});
            skLineSegment(sketch, "E3533", {"start": v(-117.97, 12.18) * mm, "end": v(-118.1, 12.15) * mm});
            skLineSegment(sketch, "E3534", {"start": v(-118.1, 12.15) * mm, "end": v(-118.22, 12.12) * mm});
            skLineSegment(sketch, "E3535", {"start": v(-118.22, 12.12) * mm, "end": v(-118.47, 12.05) * mm});
            skLineSegment(sketch, "E3536", {"start": v(-118.47, 12.05) * mm, "end": v(-118.6, 12.02) * mm});
            skLineSegment(sketch, "E3537", {"start": v(-118.6, 12.02) * mm, "end": v(-118.73, 11.99) * mm});
            skLineSegment(sketch, "E3538", {"start": v(-118.73, 11.99) * mm, "end": v(-119, 11.92) * mm});
            skLineSegment(sketch, "E3539", {"start": v(-119, 11.92) * mm, "end": v(-119.13, 11.88) * mm});
            skLineSegment(sketch, "E3540", {"start": v(-119.13, 11.88) * mm, "end": v(-119.26, 11.85) * mm});
            skLineSegment(sketch, "E3541", {"start": v(-119.26, 11.85) * mm, "end": v(-119.4, 11.8) * mm});
            skLineSegment(sketch, "E3542", {"start": v(-119.4, 11.8) * mm, "end": v(-119.53, 11.77) * mm});
            skLineSegment(sketch, "E3543", {"start": v(-119.53, 11.77) * mm, "end": v(-119.67, 11.73) * mm});
            skLineSegment(sketch, "E3544", {"start": v(-119.67, 11.73) * mm, "end": v(-119.8, 11.7) * mm});
            skLineSegment(sketch, "E3545", {"start": v(-119.8, 11.7) * mm, "end": v(-119.94, 11.65) * mm});
            skLineSegment(sketch, "E3546", {"start": v(-119.94, 11.65) * mm, "end": v(-120.08, 11.61) * mm});
            skLineSegment(sketch, "E3547", {"start": v(-120.08, 11.61) * mm, "end": v(-120.22, 11.57) * mm});
            skLineSegment(sketch, "E3548", {"start": v(-120.22, 11.57) * mm, "end": v(-120.36, 11.53) * mm});
            skLineSegment(sketch, "E3549", {"start": v(-120.36, 11.53) * mm, "end": v(-120.5, 11.48) * mm});
            skLineSegment(sketch, "E3550", {"start": v(-120.5, 11.48) * mm, "end": v(-120.65, 11.44) * mm});
            skLineSegment(sketch, "E3551", {"start": v(-120.65, 11.44) * mm, "end": v(-120.73, 11.39) * mm});
            skLineSegment(sketch, "E3552", {"start": v(-120.73, 11.39) * mm, "end": v(-120.88, 9.74) * mm});
            skLineSegment(sketch, "E3553", {"start": v(-120.88, 9.74) * mm, "end": v(-120.8, 9.67) * mm});
            skLineSegment(sketch, "E3554", {"start": v(-120.8, 9.67) * mm, "end": v(-120.67, 9.6) * mm});
            skLineSegment(sketch, "E3555", {"start": v(-120.67, 9.6) * mm, "end": v(-120.54, 9.54) * mm});
            skLineSegment(sketch, "E3556", {"start": v(-120.54, 9.54) * mm, "end": v(-120.4, 9.47) * mm});
            skLineSegment(sketch, "E3557", {"start": v(-120.4, 9.47) * mm, "end": v(-120.27, 9.4) * mm});
            skLineSegment(sketch, "E3558", {"start": v(-120.27, 9.4) * mm, "end": v(-120.14, 9.34) * mm});
            skLineSegment(sketch, "E3559", {"start": v(-120.14, 9.34) * mm, "end": v(-120.01, 9.28) * mm});
            skLineSegment(sketch, "E3560", {"start": v(-120.01, 9.28) * mm, "end": v(-119.76, 9.15) * mm});
            skLineSegment(sketch, "E3561", {"start": v(-119.76, 9.15) * mm, "end": v(-119.63, 9.1) * mm});
            skLineSegment(sketch, "E3562", {"start": v(-119.63, 9.1) * mm, "end": v(-119.5, 9.03) * mm});
            skLineSegment(sketch, "E3563", {"start": v(-119.5, 9.03) * mm, "end": v(-119.38, 8.97) * mm});
            skLineSegment(sketch, "E3564", {"start": v(-119.38, 8.97) * mm, "end": v(-119.13, 8.86) * mm});
            skLineSegment(sketch, "E3565", {"start": v(-119.13, 8.86) * mm, "end": v(-119.01, 8.8) * mm});
            skLineSegment(sketch, "E3566", {"start": v(-119.01, 8.8) * mm, "end": v(-118.89, 8.74) * mm});
            skLineSegment(sketch, "E3567", {"start": v(-118.89, 8.74) * mm, "end": v(-118.53, 8.58) * mm});
            skLineSegment(sketch, "E3568", {"start": v(-118.53, 8.58) * mm, "end": v(-118.18, 8.43) * mm});
            skLineSegment(sketch, "E3569", {"start": v(-118.18, 8.43) * mm, "end": v(-118.06, 8.38) * mm});
            skLineSegment(sketch, "E3570", {"start": v(-118.06, 8.38) * mm, "end": v(-117.83, 8.28) * mm});
            skLineSegment(sketch, "E3571", {"start": v(-117.83, 8.28) * mm, "end": v(-117.72, 8.24) * mm});
            skLineSegment(sketch, "E3572", {"start": v(-117.72, 8.24) * mm, "end": v(-117.61, 8.2) * mm});
            skLineSegment(sketch, "E3573", {"start": v(-117.61, 8.2) * mm, "end": v(-117.5, 8.15) * mm});
            skLineSegment(sketch, "E3574", {"start": v(-117.5, 8.15) * mm, "end": v(-117.4, 8.1) * mm});
            skLineSegment(sketch, "E3575", {"start": v(-117.4, 8.1) * mm, "end": v(-117.28, 8.06) * mm});
            skLineSegment(sketch, "E3576", {"start": v(-117.28, 8.06) * mm, "end": v(-117.07, 7.97) * mm});
            skLineSegment(sketch, "E3577", {"start": v(-117.07, 7.97) * mm, "end": v(-116.96, 7.93) * mm});
            skLineSegment(sketch, "E3578", {"start": v(-116.96, 7.93) * mm, "end": v(-116.86, 7.9) * mm});
            skLineSegment(sketch, "E3579", {"start": v(-116.86, 7.9) * mm, "end": v(-116.65, 7.81) * mm});
            skLineSegment(sketch, "E3580", {"start": v(-116.65, 7.81) * mm, "end": v(-116.55, 7.77) * mm});
            skLineSegment(sketch, "E3581", {"start": v(-116.55, 7.77) * mm, "end": v(-116.45, 7.74) * mm});
            skLineSegment(sketch, "E3582", {"start": v(-116.45, 7.74) * mm, "end": v(-116.33, 6.77) * mm});
            skLineSegment(sketch, "E3583", {"start": v(-116.33, 6.77) * mm, "end": v(-116.56, 5.82) * mm});
            skLineSegment(sketch, "E3584", {"start": v(-116.56, 5.82) * mm, "end": v(-116.66, 5.8) * mm});
            skLineSegment(sketch, "E3585", {"start": v(-116.66, 5.8) * mm, "end": v(-116.77, 5.77) * mm});
            skLineSegment(sketch, "E3586", {"start": v(-116.77, 5.77) * mm, "end": v(-116.98, 5.71) * mm});
            skLineSegment(sketch, "E3587", {"start": v(-116.98, 5.71) * mm, "end": v(-117.1, 5.69) * mm});
            skLineSegment(sketch, "E3588", {"start": v(-117.1, 5.69) * mm, "end": v(-117.2, 5.66) * mm});
            skLineSegment(sketch, "E3589", {"start": v(-117.2, 5.66) * mm, "end": v(-117.31, 5.63) * mm});
            skLineSegment(sketch, "E3590", {"start": v(-117.31, 5.63) * mm, "end": v(-117.43, 5.6) * mm});
            skLineSegment(sketch, "E3591", {"start": v(-117.43, 5.6) * mm, "end": v(-117.54, 5.57) * mm});
            skLineSegment(sketch, "E3592", {"start": v(-117.54, 5.57) * mm, "end": v(-117.77, 5.5) * mm});
            skLineSegment(sketch, "E3593", {"start": v(-117.77, 5.5) * mm, "end": v(-118, 5.44) * mm});
            skLineSegment(sketch, "E3594", {"start": v(-118, 5.44) * mm, "end": v(-118.12, 5.4) * mm});
            skLineSegment(sketch, "E3595", {"start": v(-118.12, 5.4) * mm, "end": v(-118.24, 5.37) * mm});
            skLineSegment(sketch, "E3596", {"start": v(-118.24, 5.37) * mm, "end": v(-118.36, 5.33) * mm});
            skLineSegment(sketch, "E3597", {"start": v(-118.36, 5.33) * mm, "end": v(-118.48, 5.3) * mm});
            skLineSegment(sketch, "E3598", {"start": v(-118.48, 5.3) * mm, "end": v(-118.72, 5.22) * mm});
            skLineSegment(sketch, "E3599", {"start": v(-118.72, 5.22) * mm, "end": v(-118.85, 5.18) * mm});
            skLineSegment(sketch, "E3600", {"start": v(-118.85, 5.18) * mm, "end": v(-118.97, 5.14) * mm});
            skLineSegment(sketch, "E3601", {"start": v(-118.97, 5.14) * mm, "end": v(-119.1, 5.1) * mm});
            skLineSegment(sketch, "E3602", {"start": v(-119.1, 5.1) * mm, "end": v(-119.23, 5.06) * mm});
            skLineSegment(sketch, "E3603", {"start": v(-119.23, 5.06) * mm, "end": v(-119.36, 5.02) * mm});
            skLineSegment(sketch, "E3604", {"start": v(-119.36, 5.02) * mm, "end": v(-119.62, 4.93) * mm});
            skLineSegment(sketch, "E3605", {"start": v(-119.62, 4.93) * mm, "end": v(-119.75, 4.9) * mm});
            skLineSegment(sketch, "E3606", {"start": v(-119.75, 4.9) * mm, "end": v(-119.88, 4.85) * mm});
            skLineSegment(sketch, "E3607", {"start": v(-119.88, 4.85) * mm, "end": v(-120.15, 4.75) * mm});
            skLineSegment(sketch, "E3608", {"start": v(-120.15, 4.75) * mm, "end": v(-120.42, 4.66) * mm});
            skLineSegment(sketch, "E3609", {"start": v(-120.42, 4.66) * mm, "end": v(-120.55, 4.6) * mm});
            skLineSegment(sketch, "E3610", {"start": v(-120.55, 4.6) * mm, "end": v(-120.7, 4.56) * mm});
            skLineSegment(sketch, "E3611", {"start": v(-120.7, 4.56) * mm, "end": v(-120.83, 4.5) * mm});
            skLineSegment(sketch, "E3612", {"start": v(-120.83, 4.5) * mm, "end": v(-120.97, 4.46) * mm});
            skLineSegment(sketch, "E3613", {"start": v(-120.97, 4.46) * mm, "end": v(-121.1, 4.4) * mm});
            skLineSegment(sketch, "E3614", {"start": v(-121.1, 4.4) * mm, "end": v(-121.19, 4.35) * mm});
            skLineSegment(sketch, "E3615", {"start": v(-121.19, 4.35) * mm, "end": v(-121.24, 2.7) * mm});
            skLineSegment(sketch, "E3616", {"start": v(-121.24, 2.7) * mm, "end": v(-121.16, 2.63) * mm});
            skLineSegment(sketch, "E3617", {"start": v(-121.16, 2.63) * mm, "end": v(-121.02, 2.57) * mm});
            skLineSegment(sketch, "E3618", {"start": v(-121.02, 2.57) * mm, "end": v(-120.89, 2.51) * mm});
            skLineSegment(sketch, "E3619", {"start": v(-120.89, 2.51) * mm, "end": v(-120.62, 2.4) * mm});
            skLineSegment(sketch, "E3620", {"start": v(-120.62, 2.4) * mm, "end": v(-120.48, 2.34) * mm});
            skLineSegment(sketch, "E3621", {"start": v(-120.48, 2.34) * mm, "end": v(-120.35, 2.28) * mm});
            skLineSegment(sketch, "E3622", {"start": v(-120.35, 2.28) * mm, "end": v(-120.22, 2.23) * mm});
            skLineSegment(sketch, "E3623", {"start": v(-120.22, 2.23) * mm, "end": v(-120.09, 2.17) * mm});
            skLineSegment(sketch, "E3624", {"start": v(-120.09, 2.17) * mm, "end": v(-119.96, 2.12) * mm});
            skLineSegment(sketch, "E3625", {"start": v(-119.96, 2.12) * mm, "end": v(-119.83, 2.07) * mm});
            skLineSegment(sketch, "E3626", {"start": v(-119.83, 2.07) * mm, "end": v(-119.57, 1.96) * mm});
            skLineSegment(sketch, "E3627", {"start": v(-119.57, 1.96) * mm, "end": v(-119.32, 1.87) * mm});
            skLineSegment(sketch, "E3628", {"start": v(-119.32, 1.87) * mm, "end": v(-119.2, 1.82) * mm});
            skLineSegment(sketch, "E3629", {"start": v(-119.2, 1.82) * mm, "end": v(-119.07, 1.77) * mm});
            skLineSegment(sketch, "E3630", {"start": v(-119.07, 1.77) * mm, "end": v(-118.95, 1.72) * mm});
            skLineSegment(sketch, "E3631", {"start": v(-118.95, 1.72) * mm, "end": v(-118.7, 1.63) * mm});
            skLineSegment(sketch, "E3632", {"start": v(-118.7, 1.63) * mm, "end": v(-118.59, 1.59) * mm});
            skLineSegment(sketch, "E3633", {"start": v(-118.59, 1.59) * mm, "end": v(-118.47, 1.54) * mm});
            skLineSegment(sketch, "E3634", {"start": v(-118.47, 1.54) * mm, "end": v(-118.35, 1.5) * mm});
            skLineSegment(sketch, "E3635", {"start": v(-118.35, 1.5) * mm, "end": v(-118.23, 1.46) * mm});
            skLineSegment(sketch, "E3636", {"start": v(-118.23, 1.46) * mm, "end": v(-118.12, 1.42) * mm});
            skLineSegment(sketch, "E3637", {"start": v(-118.12, 1.42) * mm, "end": v(-117.89, 1.34) * mm});
            skLineSegment(sketch, "E3638", {"start": v(-117.89, 1.34) * mm, "end": v(-117.78, 1.3) * mm});
            skLineSegment(sketch, "E3639", {"start": v(-117.78, 1.3) * mm, "end": v(-117.66, 1.26) * mm});
            skLineSegment(sketch, "E3640", {"start": v(-117.66, 1.26) * mm, "end": v(-117.55, 1.23) * mm});
            skLineSegment(sketch, "E3641", {"start": v(-117.55, 1.23) * mm, "end": v(-117.44, 1.19) * mm});
            skLineSegment(sketch, "E3642", {"start": v(-117.44, 1.19) * mm, "end": v(-117.22, 1.12) * mm});
            skLineSegment(sketch, "E3643", {"start": v(-117.22, 1.12) * mm, "end": v(-117.12, 1.08) * mm});
            skLineSegment(sketch, "E3644", {"start": v(-117.12, 1.08) * mm, "end": v(-116.9, 1.02) * mm});
            skLineSegment(sketch, "E3645", {"start": v(-116.9, 1.02) * mm, "end": v(-116.8, 0.98) * mm});
            skLineSegment(sketch, "E3646", {"start": v(-116.8, 0.98) * mm, "end": v(-116.7, 0.95) * mm});
            skLineSegment(sketch, "E3647", {"start": v(-116.7, 0.95) * mm, "end": v(-116.53, 0) * mm});
            skLineSegment(sketch, "E3648", {"start": v(-116.53, 0) * mm, "end": v(-116.7, -0.97) * mm});
            skLineSegment(sketch, "E3649", {"start": v(-116.7, -0.97) * mm, "end": v(-116.9, -1.03) * mm});
            skLineSegment(sketch, "E3650", {"start": v(-116.9, -1.03) * mm, "end": v(-117.01, -1.06) * mm});
            skLineSegment(sketch, "E3651", {"start": v(-117.01, -1.06) * mm, "end": v(-117.22, -1.13) * mm});
            skLineSegment(sketch, "E3652", {"start": v(-117.22, -1.13) * mm, "end": v(-117.33, -1.17) * mm});
            skLineSegment(sketch, "E3653", {"start": v(-117.33, -1.17) * mm, "end": v(-117.44, -1.2) * mm});
            skLineSegment(sketch, "E3654", {"start": v(-117.44, -1.2) * mm, "end": v(-117.55, -1.24) * mm});
            skLineSegment(sketch, "E3655", {"start": v(-117.55, -1.24) * mm, "end": v(-117.66, -1.28) * mm});
            skLineSegment(sketch, "E3656", {"start": v(-117.66, -1.28) * mm, "end": v(-117.78, -1.31) * mm});
            skLineSegment(sketch, "E3657", {"start": v(-117.78, -1.31) * mm, "end": v(-117.89, -1.35) * mm});
            skLineSegment(sketch, "E3658", {"start": v(-117.89, -1.35) * mm, "end": v(-118, -1.4) * mm});
            skLineSegment(sketch, "E3659", {"start": v(-118, -1.4) * mm, "end": v(-118.12, -1.43) * mm});
            skLineSegment(sketch, "E3660", {"start": v(-118.12, -1.43) * mm, "end": v(-118.23, -1.47) * mm});
            skLineSegment(sketch, "E3661", {"start": v(-118.23, -1.47) * mm, "end": v(-118.35, -1.52) * mm});
            skLineSegment(sketch, "E3662", {"start": v(-118.35, -1.52) * mm, "end": v(-118.59, -1.6) * mm});
            skLineSegment(sketch, "E3663", {"start": v(-118.59, -1.6) * mm, "end": v(-118.7, -1.65) * mm});
            skLineSegment(sketch, "E3664", {"start": v(-118.7, -1.65) * mm, "end": v(-118.95, -1.74) * mm});
            skLineSegment(sketch, "E3665", {"start": v(-118.95, -1.74) * mm, "end": v(-119.07, -1.78) * mm});
            skLineSegment(sketch, "E3666", {"start": v(-119.07, -1.78) * mm, "end": v(-119.32, -1.88) * mm});
            skLineSegment(sketch, "E3667", {"start": v(-119.32, -1.88) * mm, "end": v(-119.45, -1.93) * mm});
            skLineSegment(sketch, "E3668", {"start": v(-119.45, -1.93) * mm, "end": v(-119.57, -1.98) * mm});
            skLineSegment(sketch, "E3669", {"start": v(-119.57, -1.98) * mm, "end": v(-119.7, -2.03) * mm});
            skLineSegment(sketch, "E3670", {"start": v(-119.7, -2.03) * mm, "end": v(-119.96, -2.13) * mm});
            skLineSegment(sketch, "E3671", {"start": v(-119.96, -2.13) * mm, "end": v(-120.09, -2.19) * mm});
            skLineSegment(sketch, "E3672", {"start": v(-120.09, -2.19) * mm, "end": v(-120.22, -2.24) * mm});
            skLineSegment(sketch, "E3673", {"start": v(-120.22, -2.24) * mm, "end": v(-120.48, -2.35) * mm});
            skLineSegment(sketch, "E3674", {"start": v(-120.48, -2.35) * mm, "end": v(-120.62, -2.4) * mm});
            skLineSegment(sketch, "E3675", {"start": v(-120.62, -2.4) * mm, "end": v(-120.75, -2.47) * mm});
            skLineSegment(sketch, "E3676", {"start": v(-120.75, -2.47) * mm, "end": v(-120.89, -2.52) * mm});
            skLineSegment(sketch, "E3677", {"start": v(-120.89, -2.52) * mm, "end": v(-121.02, -2.58) * mm});
            skLineSegment(sketch, "E3678", {"start": v(-121.02, -2.58) * mm, "end": v(-121.16, -2.64) * mm});
            skLineSegment(sketch, "E3679", {"start": v(-121.16, -2.64) * mm, "end": v(-121.24, -2.7) * mm});
            skLineSegment(sketch, "E3680", {"start": v(-121.24, -2.7) * mm, "end": v(-121.19, -4.36) * mm});
            skLineSegment(sketch, "E3681", {"start": v(-121.19, -4.36) * mm, "end": v(-121.1, -4.42) * mm});
            skLineSegment(sketch, "E3682", {"start": v(-121.1, -4.42) * mm, "end": v(-120.97, -4.47) * mm});
            skLineSegment(sketch, "E3683", {"start": v(-120.97, -4.47) * mm, "end": v(-120.83, -4.52) * mm});
            skLineSegment(sketch, "E3684", {"start": v(-120.83, -4.52) * mm, "end": v(-120.69, -4.57) * mm});
            skLineSegment(sketch, "E3685", {"start": v(-120.69, -4.57) * mm, "end": v(-120.55, -4.62) * mm});
            skLineSegment(sketch, "E3686", {"start": v(-120.55, -4.62) * mm, "end": v(-120.28, -4.72) * mm});
            skLineSegment(sketch, "E3687", {"start": v(-120.28, -4.72) * mm, "end": v(-120.15, -4.77) * mm});
            skLineSegment(sketch, "E3688", {"start": v(-120.15, -4.77) * mm, "end": v(-120.01, -4.81) * mm});
            skLineSegment(sketch, "E3689", {"start": v(-120.01, -4.81) * mm, "end": v(-119.75, -4.9) * mm});
            skLineSegment(sketch, "E3690", {"start": v(-119.75, -4.9) * mm, "end": v(-119.62, -4.95) * mm});
            skLineSegment(sketch, "E3691", {"start": v(-119.62, -4.95) * mm, "end": v(-119.48, -5) * mm});
            skLineSegment(sketch, "E3692", {"start": v(-119.48, -5) * mm, "end": v(-119.36, -5.03) * mm});
            skLineSegment(sketch, "E3693", {"start": v(-119.36, -5.03) * mm, "end": v(-119.1, -5.12) * mm});
            skLineSegment(sketch, "E3694", {"start": v(-119.1, -5.12) * mm, "end": v(-118.97, -5.16) * mm});
            skLineSegment(sketch, "E3695", {"start": v(-118.97, -5.16) * mm, "end": v(-118.85, -5.2) * mm});
            skLineSegment(sketch, "E3696", {"start": v(-118.85, -5.2) * mm, "end": v(-118.6, -5.27) * mm});
            skLineSegment(sketch, "E3697", {"start": v(-118.6, -5.27) * mm, "end": v(-118.48, -5.3) * mm});
            skLineSegment(sketch, "E3698", {"start": v(-118.48, -5.3) * mm, "end": v(-118.36, -5.35) * mm});
            skLineSegment(sketch, "E3699", {"start": v(-118.36, -5.35) * mm, "end": v(-118.24, -5.38) * mm});
            skLineSegment(sketch, "E3700", {"start": v(-118.24, -5.38) * mm, "end": v(-118.12, -5.42) * mm});
            skLineSegment(sketch, "E3701", {"start": v(-118.12, -5.42) * mm, "end": v(-118, -5.45) * mm});
            skLineSegment(sketch, "E3702", {"start": v(-118, -5.45) * mm, "end": v(-117.88, -5.48) * mm});
            skLineSegment(sketch, "E3703", {"start": v(-117.88, -5.48) * mm, "end": v(-117.77, -5.52) * mm});
            skLineSegment(sketch, "E3704", {"start": v(-117.77, -5.52) * mm, "end": v(-117.65, -5.55) * mm});
            skLineSegment(sketch, "E3705", {"start": v(-117.65, -5.55) * mm, "end": v(-117.54, -5.58) * mm});
            skLineSegment(sketch, "E3706", {"start": v(-117.54, -5.58) * mm, "end": v(-117.42, -5.61) * mm});
            skLineSegment(sketch, "E3707", {"start": v(-117.42, -5.61) * mm, "end": v(-117.31, -5.64) * mm});
            skLineSegment(sketch, "E3708", {"start": v(-117.31, -5.64) * mm, "end": v(-117.1, -5.7) * mm});
            skLineSegment(sketch, "E3709", {"start": v(-117.1, -5.7) * mm, "end": v(-116.98, -5.73) * mm});
            skLineSegment(sketch, "E3710", {"start": v(-116.98, -5.73) * mm, "end": v(-116.87, -5.76) * mm});
            skLineSegment(sketch, "E3711", {"start": v(-116.87, -5.76) * mm, "end": v(-116.66, -5.8) * mm});
            skLineSegment(sketch, "E3712", {"start": v(-116.66, -5.8) * mm, "end": v(-116.56, -5.83) * mm});
            skLineSegment(sketch, "E3713", {"start": v(-116.56, -5.83) * mm, "end": v(-116.33, -6.78) * mm});
            skLineSegment(sketch, "E3714", {"start": v(-116.33, -6.78) * mm, "end": v(-116.45, -7.75) * mm});
            skLineSegment(sketch, "E3715", {"start": v(-116.45, -7.75) * mm, "end": v(-116.55, -7.79) * mm});
            skLineSegment(sketch, "E3716", {"start": v(-116.55, -7.79) * mm, "end": v(-116.65, -7.83) * mm});
            skLineSegment(sketch, "E3717", {"start": v(-116.65, -7.83) * mm, "end": v(-116.75, -7.86) * mm});
            skLineSegment(sketch, "E3718", {"start": v(-116.75, -7.86) * mm, "end": v(-116.86, -7.9) * mm});
            skLineSegment(sketch, "E3719", {"start": v(-116.86, -7.9) * mm, "end": v(-116.96, -7.95) * mm});
            skLineSegment(sketch, "E3720", {"start": v(-116.96, -7.95) * mm, "end": v(-117.17, -8.03) * mm});
            skLineSegment(sketch, "E3721", {"start": v(-117.17, -8.03) * mm, "end": v(-117.28, -8.07) * mm});
            skLineSegment(sketch, "E3722", {"start": v(-117.28, -8.07) * mm, "end": v(-117.39, -8.12) * mm});
            skLineSegment(sketch, "E3723", {"start": v(-117.39, -8.12) * mm, "end": v(-117.5, -8.16) * mm});
            skLineSegment(sketch, "E3724", {"start": v(-117.5, -8.16) * mm, "end": v(-117.61, -8.2) * mm});
            skLineSegment(sketch, "E3725", {"start": v(-117.61, -8.2) * mm, "end": v(-117.72, -8.25) * mm});
            skLineSegment(sketch, "E3726", {"start": v(-117.72, -8.25) * mm, "end": v(-117.95, -8.35) * mm});
            skLineSegment(sketch, "E3727", {"start": v(-117.95, -8.35) * mm, "end": v(-118.06, -8.4) * mm});
            skLineSegment(sketch, "E3728", {"start": v(-118.06, -8.4) * mm, "end": v(-118.3, -8.5) * mm});
            skLineSegment(sketch, "E3729", {"start": v(-118.3, -8.5) * mm, "end": v(-118.41, -8.55) * mm});
            skLineSegment(sketch, "E3730", {"start": v(-118.41, -8.55) * mm, "end": v(-118.65, -8.65) * mm});
            skLineSegment(sketch, "E3731", {"start": v(-118.65, -8.65) * mm, "end": v(-118.77, -8.7) * mm});
            skLineSegment(sketch, "E3732", {"start": v(-118.77, -8.7) * mm, "end": v(-118.89, -8.76) * mm});
            skLineSegment(sketch, "E3733", {"start": v(-118.89, -8.76) * mm, "end": v(-119.01, -8.81) * mm});
            skLineSegment(sketch, "E3734", {"start": v(-119.01, -8.81) * mm, "end": v(-119.13, -8.87) * mm});
            skLineSegment(sketch, "E3735", {"start": v(-119.13, -8.87) * mm, "end": v(-119.26, -8.93) * mm});
            skLineSegment(sketch, "E3736", {"start": v(-119.26, -8.93) * mm, "end": v(-119.38, -8.98) * mm});
            skLineSegment(sketch, "E3737", {"start": v(-119.38, -8.98) * mm, "end": v(-119.5, -9.04) * mm});
            skLineSegment(sketch, "E3738", {"start": v(-119.5, -9.04) * mm, "end": v(-119.63, -9.1) * mm});
            skLineSegment(sketch, "E3739", {"start": v(-119.63, -9.1) * mm, "end": v(-119.76, -9.17) * mm});
            skLineSegment(sketch, "E3740", {"start": v(-119.76, -9.17) * mm, "end": v(-119.89, -9.23) * mm});
            skLineSegment(sketch, "E3741", {"start": v(-119.89, -9.23) * mm, "end": v(-120.01, -9.29) * mm});
            skLineSegment(sketch, "E3742", {"start": v(-120.01, -9.29) * mm, "end": v(-120.14, -9.35) * mm});
            skLineSegment(sketch, "E3743", {"start": v(-120.14, -9.35) * mm, "end": v(-120.27, -9.42) * mm});
            skLineSegment(sketch, "E3744", {"start": v(-120.27, -9.42) * mm, "end": v(-120.4, -9.48) * mm});
            skLineSegment(sketch, "E3745", {"start": v(-120.4, -9.48) * mm, "end": v(-120.54, -9.55) * mm});
            skLineSegment(sketch, "E3746", {"start": v(-120.54, -9.55) * mm, "end": v(-120.67, -9.62) * mm});
            skLineSegment(sketch, "E3747", {"start": v(-120.67, -9.62) * mm, "end": v(-120.8, -9.68) * mm});
            skLineSegment(sketch, "E3748", {"start": v(-120.8, -9.68) * mm, "end": v(-120.87, -9.75) * mm});
            skLineSegment(sketch, "E3749", {"start": v(-120.87, -9.75) * mm, "end": v(-120.73, -11.4) * mm});
            skLineSegment(sketch, "E3750", {"start": v(-120.73, -11.4) * mm, "end": v(-120.65, -11.45) * mm});
            skLineSegment(sketch, "E3751", {"start": v(-120.65, -11.45) * mm, "end": v(-120.5, -11.5) * mm});
            skLineSegment(sketch, "E3752", {"start": v(-120.5, -11.5) * mm, "end": v(-120.22, -11.58) * mm});
            skLineSegment(sketch, "E3753", {"start": v(-120.22, -11.58) * mm, "end": v(-120.08, -11.62) * mm});
            skLineSegment(sketch, "E3754", {"start": v(-120.08, -11.62) * mm, "end": v(-119.94, -11.66) * mm});
            skLineSegment(sketch, "E3755", {"start": v(-119.94, -11.66) * mm, "end": v(-119.66, -11.74) * mm});
            skLineSegment(sketch, "E3756", {"start": v(-119.66, -11.74) * mm, "end": v(-119.53, -11.78) * mm});
            skLineSegment(sketch, "E3757", {"start": v(-119.53, -11.78) * mm, "end": v(-119.26, -11.86) * mm});
            skLineSegment(sketch, "E3758", {"start": v(-119.26, -11.86) * mm, "end": v(-119.12, -11.9) * mm});
            skLineSegment(sketch, "E3759", {"start": v(-119.12, -11.9) * mm, "end": v(-119, -11.93) * mm});
            skLineSegment(sketch, "E3760", {"start": v(-119, -11.93) * mm, "end": v(-118.86, -11.97) * mm});
            skLineSegment(sketch, "E3761", {"start": v(-118.86, -11.97) * mm, "end": v(-118.73, -12) * mm});
            skLineSegment(sketch, "E3762", {"start": v(-118.73, -12) * mm, "end": v(-118.6, -12.03) * mm});
            skLineSegment(sketch, "E3763", {"start": v(-118.6, -12.03) * mm, "end": v(-118.47, -12.06) * mm});
            skLineSegment(sketch, "E3764", {"start": v(-118.47, -12.06) * mm, "end": v(-118.35, -12.1) * mm});
            skLineSegment(sketch, "E3765", {"start": v(-118.35, -12.1) * mm, "end": v(-118.22, -12.13) * mm});
            skLineSegment(sketch, "E3766", {"start": v(-118.22, -12.13) * mm, "end": v(-118.1, -12.16) * mm});
            skLineSegment(sketch, "E3767", {"start": v(-118.1, -12.16) * mm, "end": v(-117.97, -12.19) * mm});
            skLineSegment(sketch, "E3768", {"start": v(-117.97, -12.19) * mm, "end": v(-117.85, -12.22) * mm});
            skLineSegment(sketch, "E3769", {"start": v(-117.85, -12.22) * mm, "end": v(-117.72, -12.25) * mm});
            skLineSegment(sketch, "E3770", {"start": v(-117.72, -12.25) * mm, "end": v(-117.6, -12.28) * mm});
            skLineSegment(sketch, "E3771", {"start": v(-117.6, -12.28) * mm, "end": v(-117.48, -12.3) * mm});
            skLineSegment(sketch, "E3772", {"start": v(-117.48, -12.3) * mm, "end": v(-117.36, -12.33) * mm});
            skLineSegment(sketch, "E3773", {"start": v(-117.36, -12.33) * mm, "end": v(-117.25, -12.36) * mm});
            skLineSegment(sketch, "E3774", {"start": v(-117.25, -12.36) * mm, "end": v(-117.13, -12.38) * mm});
            skLineSegment(sketch, "E3775", {"start": v(-117.13, -12.38) * mm, "end": v(-117.01, -12.4) * mm});
            skLineSegment(sketch, "E3776", {"start": v(-117.01, -12.4) * mm, "end": v(-116.9, -12.43) * mm});
            skLineSegment(sketch, "E3777", {"start": v(-116.9, -12.43) * mm, "end": v(-116.79, -12.45) * mm});
            skLineSegment(sketch, "E3778", {"start": v(-116.79, -12.45) * mm, "end": v(-116.67, -12.48) * mm});
            skLineSegment(sketch, "E3779", {"start": v(-116.67, -12.48) * mm, "end": v(-116.56, -12.5) * mm});
            skLineSegment(sketch, "E3780", {"start": v(-116.56, -12.5) * mm, "end": v(-116.45, -12.52) * mm});
            skLineSegment(sketch, "E3781", {"start": v(-116.45, -12.52) * mm, "end": v(-116.23, -12.56) * mm});
            skLineSegment(sketch, "E3782", {"start": v(-116.23, -12.56) * mm, "end": v(-116.13, -12.58) * mm});
            skLineSegment(sketch, "E3783", {"start": v(-116.13, -12.58) * mm, "end": v(-116.02, -12.6) * mm});
            skLineSegment(sketch, "E3784", {"start": v(-116.02, -12.6) * mm, "end": v(-115.74, -13.53) * mm});
            skLineSegment(sketch, "E3785", {"start": v(-115.74, -13.53) * mm, "end": v(-115.8, -14.5) * mm});
            skLineSegment(sketch, "E3786", {"start": v(-115.8, -14.5) * mm, "end": v(-116, -14.6) * mm});
            skLineSegment(sketch, "E3787", {"start": v(-116, -14.6) * mm, "end": v(-116.1, -14.64) * mm});
            skLineSegment(sketch, "E3788", {"start": v(-116.1, -14.64) * mm, "end": v(-116.2, -14.69) * mm});
            skLineSegment(sketch, "E3789", {"start": v(-116.2, -14.69) * mm, "end": v(-116.3, -14.73) * mm});
            skLineSegment(sketch, "E3790", {"start": v(-116.3, -14.73) * mm, "end": v(-116.4, -14.78) * mm});
            skLineSegment(sketch, "E3791", {"start": v(-116.4, -14.78) * mm, "end": v(-116.5, -14.83) * mm});
            skLineSegment(sketch, "E3792", {"start": v(-116.5, -14.83) * mm, "end": v(-116.61, -14.88) * mm});
            skLineSegment(sketch, "E3793", {"start": v(-116.61, -14.88) * mm, "end": v(-116.72, -14.93) * mm});
            skLineSegment(sketch, "E3794", {"start": v(-116.72, -14.93) * mm, "end": v(-116.83, -14.98) * mm});
            skLineSegment(sketch, "E3795", {"start": v(-116.83, -14.98) * mm, "end": v(-116.93, -15.03) * mm});
            skLineSegment(sketch, "E3796", {"start": v(-116.93, -15.03) * mm, "end": v(-117.04, -15.08) * mm});
            skLineSegment(sketch, "E3797", {"start": v(-117.04, -15.08) * mm, "end": v(-117.26, -15.2) * mm});
            skLineSegment(sketch, "E3798", {"start": v(-117.26, -15.2) * mm, "end": v(-117.37, -15.25) * mm});
            skLineSegment(sketch, "E3799", {"start": v(-117.37, -15.25) * mm, "end": v(-117.49, -15.3) * mm});
            skLineSegment(sketch, "E3800", {"start": v(-117.49, -15.3) * mm, "end": v(-117.6, -15.36) * mm});
            skLineSegment(sketch, "E3801", {"start": v(-117.6, -15.36) * mm, "end": v(-117.83, -15.47) * mm});
            skLineSegment(sketch, "E3802", {"start": v(-117.83, -15.47) * mm, "end": v(-117.94, -15.53) * mm});
            skLineSegment(sketch, "E3803", {"start": v(-117.94, -15.53) * mm, "end": v(-118.18, -15.66) * mm});
            skLineSegment(sketch, "E3804", {"start": v(-118.18, -15.66) * mm, "end": v(-118.3, -15.72) * mm});
            skLineSegment(sketch, "E3805", {"start": v(-118.3, -15.72) * mm, "end": v(-118.41, -15.78) * mm});
            skLineSegment(sketch, "E3806", {"start": v(-118.41, -15.78) * mm, "end": v(-118.65, -15.91) * mm});
            skLineSegment(sketch, "E3807", {"start": v(-118.65, -15.91) * mm, "end": v(-118.78, -15.98) * mm});
            skLineSegment(sketch, "E3808", {"start": v(-118.78, -15.98) * mm, "end": v(-118.9, -16.04) * mm});
            skLineSegment(sketch, "E3809", {"start": v(-118.9, -16.04) * mm, "end": v(-119.02, -16.11) * mm});
            skLineSegment(sketch, "E3810", {"start": v(-119.02, -16.11) * mm, "end": v(-119.15, -16.18) * mm});
            skLineSegment(sketch, "E3811", {"start": v(-119.15, -16.18) * mm, "end": v(-119.27, -16.25) * mm});
            skLineSegment(sketch, "E3812", {"start": v(-119.27, -16.25) * mm, "end": v(-119.52, -16.4) * mm});
            skLineSegment(sketch, "E3813", {"start": v(-119.52, -16.4) * mm, "end": v(-119.65, -16.47) * mm});
            skLineSegment(sketch, "E3814", {"start": v(-119.65, -16.47) * mm, "end": v(-119.78, -16.54) * mm});
            skLineSegment(sketch, "E3815", {"start": v(-119.78, -16.54) * mm, "end": v(-119.9, -16.62) * mm});
            skLineSegment(sketch, "E3816", {"start": v(-119.9, -16.62) * mm, "end": v(-120.03, -16.7) * mm});
            skLineSegment(sketch, "E3817", {"start": v(-120.03, -16.7) * mm, "end": v(-120.1, -16.76) * mm});
            skLineSegment(sketch, "E3818", {"start": v(-120.1, -16.76) * mm, "end": v(-119.86, -18.4) * mm});
            skLineSegment(sketch, "E3819", {"start": v(-119.86, -18.4) * mm, "end": v(-119.78, -18.45) * mm});
            skLineSegment(sketch, "E3820", {"start": v(-119.78, -18.45) * mm, "end": v(-119.63, -18.48) * mm});
            skLineSegment(sketch, "E3821", {"start": v(-119.63, -18.48) * mm, "end": v(-119.49, -18.52) * mm});
            skLineSegment(sketch, "E3822", {"start": v(-119.49, -18.52) * mm, "end": v(-119.34, -18.55) * mm});
            skLineSegment(sketch, "E3823", {"start": v(-119.34, -18.55) * mm, "end": v(-119.2, -18.59) * mm});
            skLineSegment(sketch, "E3824", {"start": v(-119.2, -18.59) * mm, "end": v(-119.06, -18.62) * mm});
            skLineSegment(sketch, "E3825", {"start": v(-119.06, -18.62) * mm, "end": v(-118.92, -18.65) * mm});
            skLineSegment(sketch, "E3826", {"start": v(-118.92, -18.65) * mm, "end": v(-118.78, -18.68) * mm});
            skLineSegment(sketch, "E3827", {"start": v(-118.78, -18.68) * mm, "end": v(-118.64, -18.71) * mm});
            skLineSegment(sketch, "E3828", {"start": v(-118.64, -18.71) * mm, "end": v(-118.5, -18.74) * mm});
            skLineSegment(sketch, "E3829", {"start": v(-118.5, -18.74) * mm, "end": v(-118.37, -18.77) * mm});
            skLineSegment(sketch, "E3830", {"start": v(-118.37, -18.77) * mm, "end": v(-118.23, -18.8) * mm});
            skLineSegment(sketch, "E3831", {"start": v(-118.23, -18.8) * mm, "end": v(-117.96, -18.86) * mm});
            skLineSegment(sketch, "E3832", {"start": v(-117.96, -18.86) * mm, "end": v(-117.83, -18.88) * mm});
            skLineSegment(sketch, "E3833", {"start": v(-117.83, -18.88) * mm, "end": v(-117.7, -18.9) * mm});
            skLineSegment(sketch, "E3834", {"start": v(-117.7, -18.9) * mm, "end": v(-117.44, -18.96) * mm});
            skLineSegment(sketch, "E3835", {"start": v(-117.44, -18.96) * mm, "end": v(-117.31, -18.98) * mm});
            skLineSegment(sketch, "E3836", {"start": v(-117.31, -18.98) * mm, "end": v(-117.19, -19) * mm});
            skLineSegment(sketch, "E3837", {"start": v(-117.19, -19) * mm, "end": v(-117.06, -19.03) * mm});
            skLineSegment(sketch, "E3838", {"start": v(-117.06, -19.03) * mm, "end": v(-116.81, -19.07) * mm});
            skLineSegment(sketch, "E3839", {"start": v(-116.81, -19.07) * mm, "end": v(-116.7, -19.1) * mm});
            skLineSegment(sketch, "E3840", {"start": v(-116.7, -19.1) * mm, "end": v(-116.57, -19.11) * mm});
            skLineSegment(sketch, "E3841", {"start": v(-116.57, -19.11) * mm, "end": v(-116.33, -19.15) * mm});
            skLineSegment(sketch, "E3842", {"start": v(-116.33, -19.15) * mm, "end": v(-116.1, -19.19) * mm});
            skLineSegment(sketch, "E3843", {"start": v(-116.1, -19.19) * mm, "end": v(-115.98, -19.2) * mm});
            skLineSegment(sketch, "E3844", {"start": v(-115.98, -19.2) * mm, "end": v(-115.86, -19.22) * mm});
            skLineSegment(sketch, "E3845", {"start": v(-115.86, -19.22) * mm, "end": v(-115.64, -19.26) * mm});
            skLineSegment(sketch, "E3846", {"start": v(-115.64, -19.26) * mm, "end": v(-115.53, -19.27) * mm});
            skLineSegment(sketch, "E3847", {"start": v(-115.53, -19.27) * mm, "end": v(-115.42, -19.28) * mm});
            skLineSegment(sketch, "E3848", {"start": v(-115.42, -19.28) * mm, "end": v(-115.3, -19.3) * mm});
            skLineSegment(sketch, "E3849", {"start": v(-115.3, -19.3) * mm, "end": v(-115.2, -19.31) * mm});
            skLineSegment(sketch, "E3850", {"start": v(-115.2, -19.31) * mm, "end": v(-115.1, -19.33) * mm});
            skLineSegment(sketch, "E3851", {"start": v(-115.1, -19.33) * mm, "end": v(-114.76, -20.24) * mm});
            skLineSegment(sketch, "E3852", {"start": v(-114.76, -20.24) * mm, "end": v(-114.76, -21.22) * mm});
            skLineSegment(sketch, "E3853", {"start": v(-114.76, -21.22) * mm, "end": v(-114.85, -21.26) * mm});
            skLineSegment(sketch, "E3854", {"start": v(-114.85, -21.26) * mm, "end": v(-114.95, -21.31) * mm});
            skLineSegment(sketch, "E3855", {"start": v(-114.95, -21.31) * mm, "end": v(-115.05, -21.36) * mm});
            skLineSegment(sketch, "E3856", {"start": v(-115.05, -21.36) * mm, "end": v(-115.15, -21.42) * mm});
            skLineSegment(sketch, "E3857", {"start": v(-115.15, -21.42) * mm, "end": v(-115.25, -21.47) * mm});
            skLineSegment(sketch, "E3858", {"start": v(-115.25, -21.47) * mm, "end": v(-115.35, -21.52) * mm});
            skLineSegment(sketch, "E3859", {"start": v(-115.35, -21.52) * mm, "end": v(-115.45, -21.58) * mm});
            skLineSegment(sketch, "E3860", {"start": v(-115.45, -21.58) * mm, "end": v(-115.55, -21.63) * mm});
            skLineSegment(sketch, "E3861", {"start": v(-115.55, -21.63) * mm, "end": v(-115.76, -21.75) * mm});
            skLineSegment(sketch, "E3862", {"start": v(-115.76, -21.75) * mm, "end": v(-115.86, -21.8) * mm});
            skLineSegment(sketch, "E3863", {"start": v(-115.86, -21.8) * mm, "end": v(-115.97, -21.86) * mm});
            skLineSegment(sketch, "E3864", {"start": v(-115.97, -21.86) * mm, "end": v(-116.07, -21.92) * mm});
            skLineSegment(sketch, "E3865", {"start": v(-116.07, -21.92) * mm, "end": v(-116.18, -21.98) * mm});
            skLineSegment(sketch, "E3866", {"start": v(-116.18, -21.98) * mm, "end": v(-116.4, -22.1) * mm});
            skLineSegment(sketch, "E3867", {"start": v(-116.4, -22.1) * mm, "end": v(-116.5, -22.17) * mm});
            skLineSegment(sketch, "E3868", {"start": v(-116.5, -22.17) * mm, "end": v(-116.62, -22.23) * mm});
            skLineSegment(sketch, "E3869", {"start": v(-116.62, -22.23) * mm, "end": v(-116.73, -22.3) * mm});
            skLineSegment(sketch, "E3870", {"start": v(-116.73, -22.3) * mm, "end": v(-116.84, -22.37) * mm});
            skLineSegment(sketch, "E3871", {"start": v(-116.84, -22.37) * mm, "end": v(-117.07, -22.5) * mm});
            skLineSegment(sketch, "E3872", {"start": v(-117.07, -22.5) * mm, "end": v(-117.18, -22.57) * mm});
            skLineSegment(sketch, "E3873", {"start": v(-117.18, -22.57) * mm, "end": v(-117.3, -22.64) * mm});
            skLineSegment(sketch, "E3874", {"start": v(-117.3, -22.64) * mm, "end": v(-117.53, -22.78) * mm});
            skLineSegment(sketch, "E3875", {"start": v(-117.53, -22.78) * mm, "end": v(-117.65, -22.86) * mm});
            skLineSegment(sketch, "E3876", {"start": v(-117.65, -22.86) * mm, "end": v(-117.76, -22.93) * mm});
            skLineSegment(sketch, "E3877", {"start": v(-117.76, -22.93) * mm, "end": v(-117.88, -23) * mm});
            skLineSegment(sketch, "E3878", {"start": v(-117.88, -23) * mm, "end": v(-118, -23.08) * mm});
            skLineSegment(sketch, "E3879", {"start": v(-118, -23.08) * mm, "end": v(-118.25, -23.24) * mm});
            skLineSegment(sketch, "E3880", {"start": v(-118.25, -23.24) * mm, "end": v(-118.37, -23.32) * mm});
            skLineSegment(sketch, "E3881", {"start": v(-118.37, -23.32) * mm, "end": v(-118.49, -23.4) * mm});
            skLineSegment(sketch, "E3882", {"start": v(-118.49, -23.4) * mm, "end": v(-118.61, -23.48) * mm});
            skLineSegment(sketch, "E3883", {"start": v(-118.61, -23.48) * mm, "end": v(-118.74, -23.56) * mm});
            skLineSegment(sketch, "E3884", {"start": v(-118.74, -23.56) * mm, "end": v(-118.86, -23.64) * mm});
            skLineSegment(sketch, "E3885", {"start": v(-118.86, -23.64) * mm, "end": v(-118.93, -23.72) * mm});
            skLineSegment(sketch, "E3886", {"start": v(-118.93, -23.72) * mm, "end": v(-118.59, -25.34) * mm});
            skLineSegment(sketch, "E3887", {"start": v(-118.59, -25.34) * mm, "end": v(-118.5, -25.38) * mm});
            skLineSegment(sketch, "E3888", {"start": v(-118.5, -25.38) * mm, "end": v(-118.35, -25.4) * mm});
            skLineSegment(sketch, "E3889", {"start": v(-118.35, -25.4) * mm, "end": v(-118.2, -25.44) * mm});
            skLineSegment(sketch, "E3890", {"start": v(-118.2, -25.44) * mm, "end": v(-118.06, -25.46) * mm});
            skLineSegment(sketch, "E3891", {"start": v(-118.06, -25.46) * mm, "end": v(-117.92, -25.49) * mm});
            skLineSegment(sketch, "E3892", {"start": v(-117.92, -25.49) * mm, "end": v(-117.78, -25.5) * mm});
            skLineSegment(sketch, "E3893", {"start": v(-117.78, -25.5) * mm, "end": v(-117.5, -25.56) * mm});
            skLineSegment(sketch, "E3894", {"start": v(-117.5, -25.56) * mm, "end": v(-117.35, -25.58) * mm});
            skLineSegment(sketch, "E3895", {"start": v(-117.35, -25.58) * mm, "end": v(-117.21, -25.6) * mm});
            skLineSegment(sketch, "E3896", {"start": v(-117.21, -25.6) * mm, "end": v(-117.08, -25.62) * mm});
            skLineSegment(sketch, "E3897", {"start": v(-117.08, -25.62) * mm, "end": v(-116.94, -25.64) * mm});
            skLineSegment(sketch, "E3898", {"start": v(-116.94, -25.64) * mm, "end": v(-116.8, -25.66) * mm});
            skLineSegment(sketch, "E3899", {"start": v(-116.8, -25.66) * mm, "end": v(-116.54, -25.7) * mm});
            skLineSegment(sketch, "E3900", {"start": v(-116.54, -25.7) * mm, "end": v(-116.4, -25.72) * mm});
            skLineSegment(sketch, "E3901", {"start": v(-116.4, -25.72) * mm, "end": v(-116.27, -25.74) * mm});
            skLineSegment(sketch, "E3902", {"start": v(-116.27, -25.74) * mm, "end": v(-116.14, -25.75) * mm});
            skLineSegment(sketch, "E3903", {"start": v(-116.14, -25.75) * mm, "end": v(-116.01, -25.77) * mm});
            skLineSegment(sketch, "E3904", {"start": v(-116.01, -25.77) * mm, "end": v(-115.88, -25.79) * mm});
            skLineSegment(sketch, "E3905", {"start": v(-115.88, -25.79) * mm, "end": v(-115.63, -25.82) * mm});
            skLineSegment(sketch, "E3906", {"start": v(-115.63, -25.82) * mm, "end": v(-115.38, -25.85) * mm});
            skLineSegment(sketch, "E3907", {"start": v(-115.38, -25.85) * mm, "end": v(-115.26, -25.86) * mm});
            skLineSegment(sketch, "E3908", {"start": v(-115.26, -25.86) * mm, "end": v(-115.02, -25.88) * mm});
            skLineSegment(sketch, "E3909", {"start": v(-115.02, -25.88) * mm, "end": v(-114.9, -25.9) * mm});
            skLineSegment(sketch, "E3910", {"start": v(-114.9, -25.9) * mm, "end": v(-114.67, -25.92) * mm});
            skLineSegment(sketch, "E3911", {"start": v(-114.67, -25.92) * mm, "end": v(-114.55, -25.93) * mm});
            skLineSegment(sketch, "E3912", {"start": v(-114.55, -25.93) * mm, "end": v(-114.44, -25.94) * mm});
            skLineSegment(sketch, "E3913", {"start": v(-114.44, -25.94) * mm, "end": v(-114.21, -25.96) * mm});
            skLineSegment(sketch, "E3914", {"start": v(-114.21, -25.96) * mm, "end": v(-114.1, -25.96) * mm});
            skLineSegment(sketch, "E3915", {"start": v(-114.1, -25.96) * mm, "end": v(-113.99, -25.97) * mm});
            skLineSegment(sketch, "E3916", {"start": v(-113.99, -25.97) * mm, "end": v(-113.88, -25.98) * mm});
            skLineSegment(sketch, "E3917", {"start": v(-113.88, -25.98) * mm, "end": v(-113.77, -25.99) * mm});
            skLineSegment(sketch, "E3918", {"start": v(-113.77, -25.99) * mm, "end": v(-113.38, -26.88) * mm});
            skLineSegment(sketch, "E3919", {"start": v(-113.38, -26.88) * mm, "end": v(-113.33, -27.85) * mm});
            skLineSegment(sketch, "E3920", {"start": v(-113.33, -27.85) * mm, "end": v(-113.42, -27.9) * mm});
            skLineSegment(sketch, "E3921", {"start": v(-113.42, -27.9) * mm, "end": v(-113.52, -27.96) * mm});
            skLineSegment(sketch, "E3922", {"start": v(-113.52, -27.96) * mm, "end": v(-113.61, -28.02) * mm});
            skLineSegment(sketch, "E3923", {"start": v(-113.61, -28.02) * mm, "end": v(-113.7, -28.08) * mm});
            skLineSegment(sketch, "E3924", {"start": v(-113.7, -28.08) * mm, "end": v(-113.8, -28.13) * mm});
            skLineSegment(sketch, "E3925", {"start": v(-113.8, -28.13) * mm, "end": v(-113.9, -28.2) * mm});
            skLineSegment(sketch, "E3926", {"start": v(-113.9, -28.2) * mm, "end": v(-114.1, -28.31) * mm});
            skLineSegment(sketch, "E3927", {"start": v(-114.1, -28.31) * mm, "end": v(-114.2, -28.38) * mm});
            skLineSegment(sketch, "E3928", {"start": v(-114.2, -28.38) * mm, "end": v(-114.3, -28.44) * mm});
            skLineSegment(sketch, "E3929", {"start": v(-114.3, -28.44) * mm, "end": v(-114.4, -28.5) * mm});
            skLineSegment(sketch, "E3930", {"start": v(-114.4, -28.5) * mm, "end": v(-114.5, -28.57) * mm});
            skLineSegment(sketch, "E3931", {"start": v(-114.5, -28.57) * mm, "end": v(-114.6, -28.63) * mm});
            skLineSegment(sketch, "E3932", {"start": v(-114.6, -28.63) * mm, "end": v(-114.7, -28.7) * mm});
            skLineSegment(sketch, "E3933", {"start": v(-114.7, -28.7) * mm, "end": v(-114.81, -28.77) * mm});
            skLineSegment(sketch, "E3934", {"start": v(-114.81, -28.77) * mm, "end": v(-114.92, -28.84) * mm});
            skLineSegment(sketch, "E3935", {"start": v(-114.92, -28.84) * mm, "end": v(-115.13, -28.98) * mm});
            skLineSegment(sketch, "E3936", {"start": v(-115.13, -28.98) * mm, "end": v(-115.24, -29.05) * mm});
            skLineSegment(sketch, "E3937", {"start": v(-115.24, -29.05) * mm, "end": v(-115.34, -29.12) * mm});
            skLineSegment(sketch, "E3938", {"start": v(-115.34, -29.12) * mm, "end": v(-115.45, -29.2) * mm});
            skLineSegment(sketch, "E3939", {"start": v(-115.45, -29.2) * mm, "end": v(-115.56, -29.27) * mm});
            skLineSegment(sketch, "E3940", {"start": v(-115.56, -29.27) * mm, "end": v(-115.67, -29.35) * mm});
            skLineSegment(sketch, "E3941", {"start": v(-115.67, -29.35) * mm, "end": v(-115.78, -29.42) * mm});
            skLineSegment(sketch, "E3942", {"start": v(-115.78, -29.42) * mm, "end": v(-115.9, -29.5) * mm});
            skLineSegment(sketch, "E3943", {"start": v(-115.9, -29.5) * mm, "end": v(-116, -29.58) * mm});
            skLineSegment(sketch, "E3944", {"start": v(-116, -29.58) * mm, "end": v(-116.12, -29.66) * mm});
            skLineSegment(sketch, "E3945", {"start": v(-116.12, -29.66) * mm, "end": v(-116.23, -29.74) * mm});
            skLineSegment(sketch, "E3946", {"start": v(-116.23, -29.74) * mm, "end": v(-116.35, -29.82) * mm});
            skLineSegment(sketch, "E3947", {"start": v(-116.35, -29.82) * mm, "end": v(-116.46, -29.9) * mm});
            skLineSegment(sketch, "E3948", {"start": v(-116.46, -29.9) * mm, "end": v(-116.58, -29.99) * mm});
            skLineSegment(sketch, "E3949", {"start": v(-116.58, -29.99) * mm, "end": v(-116.7, -30.07) * mm});
            skLineSegment(sketch, "E3950", {"start": v(-116.7, -30.07) * mm, "end": v(-116.93, -30.25) * mm});
            skLineSegment(sketch, "E3951", {"start": v(-116.93, -30.25) * mm, "end": v(-117.05, -30.33) * mm});
            skLineSegment(sketch, "E3952", {"start": v(-117.05, -30.33) * mm, "end": v(-117.16, -30.42) * mm});
            skLineSegment(sketch, "E3953", {"start": v(-117.16, -30.42) * mm, "end": v(-117.28, -30.51) * mm});
            skLineSegment(sketch, "E3954", {"start": v(-117.28, -30.51) * mm, "end": v(-117.35, -30.6) * mm});
            skLineSegment(sketch, "E3955", {"start": v(-117.35, -30.6) * mm, "end": v(-116.92, -32.2) * mm});
            skLineSegment(sketch, "E3956", {"start": v(-116.92, -32.2) * mm, "end": v(-116.83, -32.23) * mm});
            skLineSegment(sketch, "E3957", {"start": v(-116.83, -32.23) * mm, "end": v(-116.68, -32.25) * mm});
            skLineSegment(sketch, "E3958", {"start": v(-116.68, -32.25) * mm, "end": v(-116.38, -32.28) * mm});
            skLineSegment(sketch, "E3959", {"start": v(-116.38, -32.28) * mm, "end": v(-116.24, -32.3) * mm});
            skLineSegment(sketch, "E3960", {"start": v(-116.24, -32.3) * mm, "end": v(-116.1, -32.32) * mm});
            skLineSegment(sketch, "E3961", {"start": v(-116.1, -32.32) * mm, "end": v(-115.95, -32.33) * mm});
            skLineSegment(sketch, "E3962", {"start": v(-115.95, -32.33) * mm, "end": v(-115.8, -32.35) * mm});
            skLineSegment(sketch, "E3963", {"start": v(-115.8, -32.35) * mm, "end": v(-115.67, -32.36) * mm});
            skLineSegment(sketch, "E3964", {"start": v(-115.67, -32.36) * mm, "end": v(-115.53, -32.37) * mm});
            skLineSegment(sketch, "E3965", {"start": v(-115.53, -32.37) * mm, "end": v(-115.39, -32.39) * mm});
            skLineSegment(sketch, "E3966", {"start": v(-115.39, -32.39) * mm, "end": v(-115.25, -32.4) * mm});
            skLineSegment(sketch, "E3967", {"start": v(-115.25, -32.4) * mm, "end": v(-115.11, -32.41) * mm});
            skLineSegment(sketch, "E3968", {"start": v(-115.11, -32.41) * mm, "end": v(-114.98, -32.42) * mm});
            skLineSegment(sketch, "E3969", {"start": v(-114.98, -32.42) * mm, "end": v(-114.84, -32.43) * mm});
            skLineSegment(sketch, "E3970", {"start": v(-114.84, -32.43) * mm, "end": v(-114.71, -32.44) * mm});
            skLineSegment(sketch, "E3971", {"start": v(-114.71, -32.44) * mm, "end": v(-114.58, -32.45) * mm});
            skLineSegment(sketch, "E3972", {"start": v(-114.58, -32.45) * mm, "end": v(-114.45, -32.46) * mm});
            skLineSegment(sketch, "E3973", {"start": v(-114.45, -32.46) * mm, "end": v(-114.32, -32.47) * mm});
            skLineSegment(sketch, "E3974", {"start": v(-114.32, -32.47) * mm, "end": v(-114.19, -32.48) * mm});
            skLineSegment(sketch, "E3975", {"start": v(-114.19, -32.48) * mm, "end": v(-114.06, -32.5) * mm});
            skLineSegment(sketch, "E3976", {"start": v(-114.06, -32.5) * mm, "end": v(-113.93, -32.5) * mm});
            skLineSegment(sketch, "E3977", {"start": v(-113.93, -32.5) * mm, "end": v(-113.8, -32.5) * mm});
            skLineSegment(sketch, "E3978", {"start": v(-113.8, -32.5) * mm, "end": v(-113.69, -32.51) * mm});
            skLineSegment(sketch, "E3979", {"start": v(-113.69, -32.51) * mm, "end": v(-113.56, -32.52) * mm});
            skLineSegment(sketch, "E3980", {"start": v(-113.56, -32.52) * mm, "end": v(-113.32, -32.53) * mm});
            skLineSegment(sketch, "E3981", {"start": v(-113.32, -32.53) * mm, "end": v(-113.2, -32.53) * mm});
            skLineSegment(sketch, "E3982", {"start": v(-113.2, -32.53) * mm, "end": v(-113.08, -32.54) * mm});
            skLineSegment(sketch, "E3983", {"start": v(-113.08, -32.54) * mm, "end": v(-112.96, -32.54) * mm});
            skLineSegment(sketch, "E3984", {"start": v(-112.96, -32.54) * mm, "end": v(-112.85, -32.54) * mm});
            skLineSegment(sketch, "E3985", {"start": v(-112.85, -32.54) * mm, "end": v(-112.62, -32.55) * mm});
            skLineSegment(sketch, "E3986", {"start": v(-112.62, -32.55) * mm, "end": v(-112.5, -32.55) * mm});
            skLineSegment(sketch, "E3987", {"start": v(-112.5, -32.55) * mm, "end": v(-112.4, -32.55) * mm});
            skLineSegment(sketch, "E3988", {"start": v(-112.4, -32.55) * mm, "end": v(-112.29, -32.55) * mm});
            skLineSegment(sketch, "E3989", {"start": v(-112.29, -32.55) * mm, "end": v(-112.18, -32.56) * mm});
            skLineSegment(sketch, "E3990", {"start": v(-112.18, -32.56) * mm, "end": v(-112.07, -32.56) * mm});
            skLineSegment(sketch, "E3991", {"start": v(-112.07, -32.56) * mm, "end": v(-111.63, -33.43) * mm});
            skLineSegment(sketch, "E3992", {"start": v(-111.63, -33.43) * mm, "end": v(-111.52, -34.4) * mm});
            skLineSegment(sketch, "E3993", {"start": v(-111.52, -34.4) * mm, "end": v(-111.6, -34.46) * mm});
            skLineSegment(sketch, "E3994", {"start": v(-111.6, -34.46) * mm, "end": v(-111.7, -34.52) * mm});
            skLineSegment(sketch, "E3995", {"start": v(-111.7, -34.52) * mm, "end": v(-111.8, -34.58) * mm});
            skLineSegment(sketch, "E3996", {"start": v(-111.8, -34.58) * mm, "end": v(-111.88, -34.64) * mm});
            skLineSegment(sketch, "E3997", {"start": v(-111.88, -34.64) * mm, "end": v(-111.98, -34.7) * mm});
            skLineSegment(sketch, "E3998", {"start": v(-111.98, -34.7) * mm, "end": v(-112.07, -34.77) * mm});
            skLineSegment(sketch, "E3999", {"start": v(-112.07, -34.77) * mm, "end": v(-112.16, -34.83) * mm});
            skLineSegment(sketch, "E4000", {"start": v(-112.16, -34.83) * mm, "end": v(-112.26, -34.9) * mm});
            skLineSegment(sketch, "E4001", {"start": v(-112.26, -34.9) * mm, "end": v(-112.45, -35.04) * mm});
            skLineSegment(sketch, "E4002", {"start": v(-112.45, -35.04) * mm, "end": v(-112.65, -35.18) * mm});
            skLineSegment(sketch, "E4003", {"start": v(-112.65, -35.18) * mm, "end": v(-112.74, -35.25) * mm});
            skLineSegment(sketch, "E4004", {"start": v(-112.74, -35.25) * mm, "end": v(-112.84, -35.32) * mm});
            skLineSegment(sketch, "E4005", {"start": v(-112.84, -35.32) * mm, "end": v(-112.94, -35.4) * mm});
            skLineSegment(sketch, "E4006", {"start": v(-112.94, -35.4) * mm, "end": v(-113.04, -35.47) * mm});
            skLineSegment(sketch, "E4007", {"start": v(-113.04, -35.47) * mm, "end": v(-113.15, -35.55) * mm});
            skLineSegment(sketch, "E4008", {"start": v(-113.15, -35.55) * mm, "end": v(-113.25, -35.62) * mm});
            skLineSegment(sketch, "E4009", {"start": v(-113.25, -35.62) * mm, "end": v(-113.35, -35.7) * mm});
            skLineSegment(sketch, "E4010", {"start": v(-113.35, -35.7) * mm, "end": v(-113.45, -35.78) * mm});
            skLineSegment(sketch, "E4011", {"start": v(-113.45, -35.78) * mm, "end": v(-113.66, -35.94) * mm});
            skLineSegment(sketch, "E4012", {"start": v(-113.66, -35.94) * mm, "end": v(-113.88, -36.1) * mm});
            skLineSegment(sketch, "E4013", {"start": v(-113.88, -36.1) * mm, "end": v(-113.98, -36.19) * mm});
            skLineSegment(sketch, "E4014", {"start": v(-113.98, -36.19) * mm, "end": v(-114.09, -36.27) * mm});
            skLineSegment(sketch, "E4015", {"start": v(-114.09, -36.27) * mm, "end": v(-114.2, -36.36) * mm});
            skLineSegment(sketch, "E4016", {"start": v(-114.2, -36.36) * mm, "end": v(-114.42, -36.54) * mm});
            skLineSegment(sketch, "E4017", {"start": v(-114.42, -36.54) * mm, "end": v(-114.64, -36.71) * mm});
            skLineSegment(sketch, "E4018", {"start": v(-114.64, -36.71) * mm, "end": v(-114.86, -36.9) * mm});
            skLineSegment(sketch, "E4019", {"start": v(-114.86, -36.9) * mm, "end": v(-114.97, -37) * mm});
            skLineSegment(sketch, "E4020", {"start": v(-114.97, -37) * mm, "end": v(-115.08, -37.09) * mm});
            skLineSegment(sketch, "E4021", {"start": v(-115.08, -37.09) * mm, "end": v(-115.2, -37.18) * mm});
            skLineSegment(sketch, "E4022", {"start": v(-115.2, -37.18) * mm, "end": v(-115.31, -37.28) * mm});
            skLineSegment(sketch, "E4023", {"start": v(-115.31, -37.28) * mm, "end": v(-115.37, -37.36) * mm});
            skLineSegment(sketch, "E4024", {"start": v(-115.37, -37.36) * mm, "end": v(-114.85, -38.94) * mm});
            skLineSegment(sketch, "E4025", {"start": v(-114.85, -38.94) * mm, "end": v(-114.75, -38.97) * mm});
            skLineSegment(sketch, "E4026", {"start": v(-114.75, -38.97) * mm, "end": v(-114.6, -38.98) * mm});
            skLineSegment(sketch, "E4027", {"start": v(-114.6, -38.98) * mm, "end": v(-114.46, -38.99) * mm});
            skLineSegment(sketch, "E4028", {"start": v(-114.46, -38.99) * mm, "end": v(-114.3, -39) * mm});
            skLineSegment(sketch, "E4029", {"start": v(-114.3, -39) * mm, "end": v(-114.16, -39) * mm});
            skLineSegment(sketch, "E4030", {"start": v(-114.16, -39) * mm, "end": v(-113.87, -39.02) * mm});
            skLineSegment(sketch, "E4031", {"start": v(-113.87, -39.02) * mm, "end": v(-113.73, -39.02) * mm});
            skLineSegment(sketch, "E4032", {"start": v(-113.73, -39.02) * mm, "end": v(-113.59, -39.03) * mm});
            skLineSegment(sketch, "E4033", {"start": v(-113.59, -39.03) * mm, "end": v(-113.45, -39.04) * mm});
            skLineSegment(sketch, "E4034", {"start": v(-113.45, -39.04) * mm, "end": v(-113.3, -39.04) * mm});
            skLineSegment(sketch, "E4035", {"start": v(-113.3, -39.04) * mm, "end": v(-113.03, -39.05) * mm});
            skLineSegment(sketch, "E4036", {"start": v(-113.03, -39.05) * mm, "end": v(-112.9, -39.05) * mm});
            skLineSegment(sketch, "E4037", {"start": v(-112.9, -39.05) * mm, "end": v(-112.76, -39.06) * mm});
            skLineSegment(sketch, "E4038", {"start": v(-112.76, -39.06) * mm, "end": v(-112.63, -39.06) * mm});
            skLineSegment(sketch, "E4039", {"start": v(-112.63, -39.06) * mm, "end": v(-112.5, -39.06) * mm});
            skLineSegment(sketch, "E4040", {"start": v(-112.5, -39.06) * mm, "end": v(-112.37, -39.06) * mm});
            skLineSegment(sketch, "E4041", {"start": v(-112.37, -39.06) * mm, "end": v(-112.24, -39.06) * mm});
            skLineSegment(sketch, "E4042", {"start": v(-112.24, -39.06) * mm, "end": v(-112.1, -39.07) * mm});
            skLineSegment(sketch, "E4043", {"start": v(-112.1, -39.07) * mm, "end": v(-111.6, -39.07) * mm});
            skLineSegment(sketch, "E4044", {"start": v(-111.6, -39.07) * mm, "end": v(-111.36, -39.06) * mm});
            skLineSegment(sketch, "E4045", {"start": v(-111.36, -39.06) * mm, "end": v(-111.24, -39.06) * mm});
            skLineSegment(sketch, "E4046", {"start": v(-111.24, -39.06) * mm, "end": v(-111.12, -39.06) * mm});
            skLineSegment(sketch, "E4047", {"start": v(-111.12, -39.06) * mm, "end": v(-111, -39.06) * mm});
            skLineSegment(sketch, "E4048", {"start": v(-111, -39.06) * mm, "end": v(-110.88, -39.05) * mm});
            skLineSegment(sketch, "E4049", {"start": v(-110.88, -39.05) * mm, "end": v(-110.77, -39.05) * mm});
            skLineSegment(sketch, "E4050", {"start": v(-110.77, -39.05) * mm, "end": v(-110.65, -39.05) * mm});
            skLineSegment(sketch, "E4051", {"start": v(-110.65, -39.05) * mm, "end": v(-110.42, -39.04) * mm});
            skLineSegment(sketch, "E4052", {"start": v(-110.42, -39.04) * mm, "end": v(-110.31, -39.03) * mm});
            skLineSegment(sketch, "E4053", {"start": v(-110.31, -39.03) * mm, "end": v(-110.2, -39.03) * mm});
            skLineSegment(sketch, "E4054", {"start": v(-110.2, -39.03) * mm, "end": v(-110.1, -39.02) * mm});
            skLineSegment(sketch, "E4055", {"start": v(-110.1, -39.02) * mm, "end": v(-109.99, -39.02) * mm});
            skLineSegment(sketch, "E4056", {"start": v(-109.99, -39.02) * mm, "end": v(-109.5, -39.86) * mm});
            skLineSegment(sketch, "E4057", {"start": v(-109.5, -39.86) * mm, "end": v(-109.33, -40.82) * mm});
            skLineSegment(sketch, "E4058", {"start": v(-109.33, -40.82) * mm, "end": v(-109.6, -41.02) * mm});
            skLineSegment(sketch, "E4059", {"start": v(-109.6, -41.02) * mm, "end": v(-109.68, -41.09) * mm});
            skLineSegment(sketch, "E4060", {"start": v(-109.68, -41.09) * mm, "end": v(-109.86, -41.23) * mm});
            skLineSegment(sketch, "E4061", {"start": v(-109.86, -41.23) * mm, "end": v(-109.95, -41.3) * mm});
            skLineSegment(sketch, "E4062", {"start": v(-109.95, -41.3) * mm, "end": v(-110.04, -41.37) * mm});
            skLineSegment(sketch, "E4063", {"start": v(-110.04, -41.37) * mm, "end": v(-110.13, -41.44) * mm});
            skLineSegment(sketch, "E4064", {"start": v(-110.13, -41.44) * mm, "end": v(-110.22, -41.52) * mm});
            skLineSegment(sketch, "E4065", {"start": v(-110.22, -41.52) * mm, "end": v(-110.32, -41.6) * mm});
            skLineSegment(sketch, "E4066", {"start": v(-110.32, -41.6) * mm, "end": v(-110.4, -41.67) * mm});
            skLineSegment(sketch, "E4067", {"start": v(-110.4, -41.67) * mm, "end": v(-110.5, -41.74) * mm});
            skLineSegment(sketch, "E4068", {"start": v(-110.5, -41.74) * mm, "end": v(-110.6, -41.82) * mm});
            skLineSegment(sketch, "E4069", {"start": v(-110.6, -41.82) * mm, "end": v(-110.7, -41.9) * mm});
            skLineSegment(sketch, "E4070", {"start": v(-110.7, -41.9) * mm, "end": v(-110.89, -42.06) * mm});
            skLineSegment(sketch, "E4071", {"start": v(-110.89, -42.06) * mm, "end": v(-111.08, -42.23) * mm});
            skLineSegment(sketch, "E4072", {"start": v(-111.08, -42.23) * mm, "end": v(-111.28, -42.4) * mm});
            skLineSegment(sketch, "E4073", {"start": v(-111.28, -42.4) * mm, "end": v(-111.38, -42.49) * mm});
            skLineSegment(sketch, "E4074", {"start": v(-111.38, -42.49) * mm, "end": v(-111.48, -42.58) * mm});
            skLineSegment(sketch, "E4075", {"start": v(-111.48, -42.58) * mm, "end": v(-111.58, -42.67) * mm});
            skLineSegment(sketch, "E4076", {"start": v(-111.58, -42.67) * mm, "end": v(-111.68, -42.75) * mm});
            skLineSegment(sketch, "E4077", {"start": v(-111.68, -42.75) * mm, "end": v(-111.79, -42.85) * mm});
            skLineSegment(sketch, "E4078", {"start": v(-111.79, -42.85) * mm, "end": v(-111.89, -42.94) * mm});
            skLineSegment(sketch, "E4079", {"start": v(-111.89, -42.94) * mm, "end": v(-112, -43.03) * mm});
            skLineSegment(sketch, "E4080", {"start": v(-112, -43.03) * mm, "end": v(-112.2, -43.22) * mm});
            skLineSegment(sketch, "E4081", {"start": v(-112.2, -43.22) * mm, "end": v(-112.3, -43.32) * mm});
            skLineSegment(sketch, "E4082", {"start": v(-112.3, -43.32) * mm, "end": v(-112.41, -43.42) * mm});
            skLineSegment(sketch, "E4083", {"start": v(-112.41, -43.42) * mm, "end": v(-112.52, -43.52) * mm});
            skLineSegment(sketch, "E4084", {"start": v(-112.52, -43.52) * mm, "end": v(-112.63, -43.62) * mm});
            skLineSegment(sketch, "E4085", {"start": v(-112.63, -43.62) * mm, "end": v(-112.84, -43.82) * mm});
            skLineSegment(sketch, "E4086", {"start": v(-112.84, -43.82) * mm, "end": v(-112.95, -43.92) * mm});
            skLineSegment(sketch, "E4087", {"start": v(-112.95, -43.92) * mm, "end": v(-113, -44) * mm});
            skLineSegment(sketch, "E4088", {"start": v(-113, -44) * mm, "end": v(-112.39, -45.55) * mm});
            skLineSegment(sketch, "E4089", {"start": v(-112.39, -45.55) * mm, "end": v(-112.3, -45.57) * mm});
            skLineSegment(sketch, "E4090", {"start": v(-112.3, -45.57) * mm, "end": v(-112, -45.58) * mm});
            skLineSegment(sketch, "E4091", {"start": v(-112, -45.58) * mm, "end": v(-111.7, -45.58) * mm});
            skLineSegment(sketch, "E4092", {"start": v(-111.7, -45.58) * mm, "end": v(-111.41, -45.57) * mm});
            skLineSegment(sketch, "E4093", {"start": v(-111.41, -45.57) * mm, "end": v(-111.27, -45.57) * mm});
            skLineSegment(sketch, "E4094", {"start": v(-111.27, -45.57) * mm, "end": v(-110.85, -45.56) * mm});
            skLineSegment(sketch, "E4095", {"start": v(-110.85, -45.56) * mm, "end": v(-110.7, -45.56) * mm});
            skLineSegment(sketch, "E4096", {"start": v(-110.7, -45.56) * mm, "end": v(-110.44, -45.55) * mm});
            skLineSegment(sketch, "E4097", {"start": v(-110.44, -45.55) * mm, "end": v(-110.3, -45.55) * mm});
            skLineSegment(sketch, "E4098", {"start": v(-110.3, -45.55) * mm, "end": v(-110.17, -45.54) * mm});
            skLineSegment(sketch, "E4099", {"start": v(-110.17, -45.54) * mm, "end": v(-110.03, -45.54) * mm});
            skLineSegment(sketch, "E4100", {"start": v(-110.03, -45.54) * mm, "end": v(-109.9, -45.53) * mm});
            skLineSegment(sketch, "E4101", {"start": v(-109.9, -45.53) * mm, "end": v(-109.77, -45.52) * mm});
            skLineSegment(sketch, "E4102", {"start": v(-109.77, -45.52) * mm, "end": v(-109.52, -45.51) * mm});
            skLineSegment(sketch, "E4103", {"start": v(-109.52, -45.51) * mm, "end": v(-109.4, -45.5) * mm});
            skLineSegment(sketch, "E4104", {"start": v(-109.4, -45.5) * mm, "end": v(-109.27, -45.5) * mm});
            skLineSegment(sketch, "E4105", {"start": v(-109.27, -45.5) * mm, "end": v(-109.14, -45.49) * mm});
            skLineSegment(sketch, "E4106", {"start": v(-109.14, -45.49) * mm, "end": v(-109.02, -45.48) * mm});
            skLineSegment(sketch, "E4107", {"start": v(-109.02, -45.48) * mm, "end": v(-108.9, -45.47) * mm});
            skLineSegment(sketch, "E4108", {"start": v(-108.9, -45.47) * mm, "end": v(-108.66, -45.45) * mm});
            skLineSegment(sketch, "E4109", {"start": v(-108.66, -45.45) * mm, "end": v(-108.54, -45.44) * mm});
            skLineSegment(sketch, "E4110", {"start": v(-108.54, -45.44) * mm, "end": v(-108.42, -45.43) * mm});
            skLineSegment(sketch, "E4111", {"start": v(-108.42, -45.43) * mm, "end": v(-108.3, -45.42) * mm});
            skLineSegment(sketch, "E4112", {"start": v(-108.3, -45.42) * mm, "end": v(-108.2, -45.41) * mm});
            skLineSegment(sketch, "E4113", {"start": v(-108.2, -45.41) * mm, "end": v(-107.97, -45.4) * mm});
            skLineSegment(sketch, "E4114", {"start": v(-107.97, -45.4) * mm, "end": v(-107.75, -45.37) * mm});
            skLineSegment(sketch, "E4115", {"start": v(-107.75, -45.37) * mm, "end": v(-107.64, -45.36) * mm});
            skLineSegment(sketch, "E4116", {"start": v(-107.64, -45.36) * mm, "end": v(-107.53, -45.35) * mm});
            skLineSegment(sketch, "E4117", {"start": v(-107.53, -45.35) * mm, "end": v(-107, -46.16) * mm});
            skLineSegment(sketch, "E4118", {"start": v(-107, -46.16) * mm, "end": v(-106.77, -47.1) * mm});
            skLineSegment(sketch, "E4119", {"start": v(-106.77, -47.1) * mm, "end": v(-106.85, -47.18) * mm});
            skLineSegment(sketch, "E4120", {"start": v(-106.85, -47.18) * mm, "end": v(-106.94, -47.25) * mm});
            skLineSegment(sketch, "E4121", {"start": v(-106.94, -47.25) * mm, "end": v(-107.02, -47.32) * mm});
            skLineSegment(sketch, "E4122", {"start": v(-107.02, -47.32) * mm, "end": v(-107.1, -47.4) * mm});
            skLineSegment(sketch, "E4123", {"start": v(-107.1, -47.4) * mm, "end": v(-107.19, -47.47) * mm});
            skLineSegment(sketch, "E4124", {"start": v(-107.19, -47.47) * mm, "end": v(-107.27, -47.54) * mm});
            skLineSegment(sketch, "E4125", {"start": v(-107.27, -47.54) * mm, "end": v(-107.36, -47.62) * mm});
            skLineSegment(sketch, "E4126", {"start": v(-107.36, -47.62) * mm, "end": v(-107.45, -47.7) * mm});
            skLineSegment(sketch, "E4127", {"start": v(-107.45, -47.7) * mm, "end": v(-107.54, -47.78) * mm});
            skLineSegment(sketch, "E4128", {"start": v(-107.54, -47.78) * mm, "end": v(-107.71, -47.94) * mm});
            skLineSegment(sketch, "E4129", {"start": v(-107.71, -47.94) * mm, "end": v(-107.8, -48.02) * mm});
            skLineSegment(sketch, "E4130", {"start": v(-107.8, -48.02) * mm, "end": v(-107.89, -48.1) * mm});
            skLineSegment(sketch, "E4131", {"start": v(-107.89, -48.1) * mm, "end": v(-107.98, -48.18) * mm});
            skLineSegment(sketch, "E4132", {"start": v(-107.98, -48.18) * mm, "end": v(-108.16, -48.35) * mm});
            skLineSegment(sketch, "E4133", {"start": v(-108.16, -48.35) * mm, "end": v(-108.25, -48.44) * mm});
            skLineSegment(sketch, "E4134", {"start": v(-108.25, -48.44) * mm, "end": v(-108.35, -48.53) * mm});
            skLineSegment(sketch, "E4135", {"start": v(-108.35, -48.53) * mm, "end": v(-108.53, -48.7) * mm});
            skLineSegment(sketch, "E4136", {"start": v(-108.53, -48.7) * mm, "end": v(-108.63, -48.8) * mm});
            skLineSegment(sketch, "E4137", {"start": v(-108.63, -48.8) * mm, "end": v(-108.91, -49.08) * mm});
            skLineSegment(sketch, "E4138", {"start": v(-108.91, -49.08) * mm, "end": v(-109, -49.18) * mm});
            skLineSegment(sketch, "E4139", {"start": v(-109, -49.18) * mm, "end": v(-109.1, -49.27) * mm});
            skLineSegment(sketch, "E4140", {"start": v(-109.1, -49.27) * mm, "end": v(-109.2, -49.37) * mm});
            skLineSegment(sketch, "E4141", {"start": v(-109.2, -49.37) * mm, "end": v(-109.3, -49.47) * mm});
            skLineSegment(sketch, "E4142", {"start": v(-109.3, -49.47) * mm, "end": v(-109.4, -49.57) * mm});
            skLineSegment(sketch, "E4143", {"start": v(-109.4, -49.57) * mm, "end": v(-109.5, -49.67) * mm});
            skLineSegment(sketch, "E4144", {"start": v(-109.5, -49.67) * mm, "end": v(-109.6, -49.78) * mm});
            skLineSegment(sketch, "E4145", {"start": v(-109.6, -49.78) * mm, "end": v(-109.7, -49.88) * mm});
            skLineSegment(sketch, "E4146", {"start": v(-109.7, -49.88) * mm, "end": v(-109.9, -50.1) * mm});
            skLineSegment(sketch, "E4147", {"start": v(-109.9, -50.1) * mm, "end": v(-110, -50.2) * mm});
            skLineSegment(sketch, "E4148", {"start": v(-110, -50.2) * mm, "end": v(-110.2, -50.42) * mm});
            skLineSegment(sketch, "E4149", {"start": v(-110.2, -50.42) * mm, "end": v(-110.25, -50.5) * mm});
            skLineSegment(sketch, "E4150", {"start": v(-110.25, -50.5) * mm, "end": v(-109.55, -52) * mm});
            skLineSegment(sketch, "E4151", {"start": v(-109.55, -52) * mm, "end": v(-109.45, -52.03) * mm});
            skLineSegment(sketch, "E4152", {"start": v(-109.45, -52.03) * mm, "end": v(-109.3, -52.02) * mm});
            skLineSegment(sketch, "E4153", {"start": v(-109.3, -52.02) * mm, "end": v(-109.16, -52.01) * mm});
            skLineSegment(sketch, "E4154", {"start": v(-109.16, -52.01) * mm, "end": v(-109, -52) * mm});
            skLineSegment(sketch, "E4155", {"start": v(-109, -52) * mm, "end": v(-108.86, -52) * mm});
            skLineSegment(sketch, "E4156", {"start": v(-108.86, -52) * mm, "end": v(-108.57, -51.97) * mm});
            skLineSegment(sketch, "E4157", {"start": v(-108.57, -51.97) * mm, "end": v(-108.43, -51.96) * mm});
            skLineSegment(sketch, "E4158", {"start": v(-108.43, -51.96) * mm, "end": v(-108.29, -51.95) * mm});
            skLineSegment(sketch, "E4159", {"start": v(-108.29, -51.95) * mm, "end": v(-108.01, -51.93) * mm});
            skLineSegment(sketch, "E4160", {"start": v(-108.01, -51.93) * mm, "end": v(-107.87, -51.92) * mm});
            skLineSegment(sketch, "E4161", {"start": v(-107.87, -51.92) * mm, "end": v(-107.74, -51.9) * mm});
            skLineSegment(sketch, "E4162", {"start": v(-107.74, -51.9) * mm, "end": v(-107.6, -51.9) * mm});
            skLineSegment(sketch, "E4163", {"start": v(-107.6, -51.9) * mm, "end": v(-107.47, -51.88) * mm});
            skLineSegment(sketch, "E4164", {"start": v(-107.47, -51.88) * mm, "end": v(-107.2, -51.86) * mm});
            skLineSegment(sketch, "E4165", {"start": v(-107.2, -51.86) * mm, "end": v(-107.07, -51.84) * mm});
            skLineSegment(sketch, "E4166", {"start": v(-107.07, -51.84) * mm, "end": v(-106.94, -51.83) * mm});
            skLineSegment(sketch, "E4167", {"start": v(-106.94, -51.83) * mm, "end": v(-106.81, -51.82) * mm});
            skLineSegment(sketch, "E4168", {"start": v(-106.81, -51.82) * mm, "end": v(-106.69, -51.8) * mm});
            skLineSegment(sketch, "E4169", {"start": v(-106.69, -51.8) * mm, "end": v(-106.56, -51.79) * mm});
            skLineSegment(sketch, "E4170", {"start": v(-106.56, -51.79) * mm, "end": v(-106.31, -51.76) * mm});
            skLineSegment(sketch, "E4171", {"start": v(-106.31, -51.76) * mm, "end": v(-106.07, -51.73) * mm});
            skLineSegment(sketch, "E4172", {"start": v(-106.07, -51.73) * mm, "end": v(-105.95, -51.71) * mm});
            skLineSegment(sketch, "E4173", {"start": v(-105.95, -51.71) * mm, "end": v(-105.83, -51.7) * mm});
            skLineSegment(sketch, "E4174", {"start": v(-105.83, -51.7) * mm, "end": v(-105.71, -51.68) * mm});
            skLineSegment(sketch, "E4175", {"start": v(-105.71, -51.68) * mm, "end": v(-105.6, -51.66) * mm});
            skLineSegment(sketch, "E4176", {"start": v(-105.6, -51.66) * mm, "end": v(-105.48, -51.64) * mm});
            skLineSegment(sketch, "E4177", {"start": v(-105.48, -51.64) * mm, "end": v(-105.26, -51.61) * mm});
            skLineSegment(sketch, "E4178", {"start": v(-105.26, -51.61) * mm, "end": v(-105.04, -51.58) * mm});
            skLineSegment(sketch, "E4179", {"start": v(-105.04, -51.58) * mm, "end": v(-104.93, -51.56) * mm});
            skLineSegment(sketch, "E4180", {"start": v(-104.93, -51.56) * mm, "end": v(-104.82, -51.54) * mm});
            skLineSegment(sketch, "E4181", {"start": v(-104.82, -51.54) * mm, "end": v(-104.71, -51.52) * mm});
            skLineSegment(sketch, "E4182", {"start": v(-104.71, -51.52) * mm, "end": v(-104.13, -52.3) * mm});
            skLineSegment(sketch, "E4183", {"start": v(-104.13, -52.3) * mm, "end": v(-103.85, -53.24) * mm});
            skLineSegment(sketch, "E4184", {"start": v(-103.85, -53.24) * mm, "end": v(-103.93, -53.31) * mm});
            skLineSegment(sketch, "E4185", {"start": v(-103.93, -53.31) * mm, "end": v(-104, -53.39) * mm});
            skLineSegment(sketch, "E4186", {"start": v(-104, -53.39) * mm, "end": v(-104.09, -53.46) * mm});
            skLineSegment(sketch, "E4187", {"start": v(-104.09, -53.46) * mm, "end": v(-104.17, -53.54) * mm});
            skLineSegment(sketch, "E4188", {"start": v(-104.17, -53.54) * mm, "end": v(-104.25, -53.62) * mm});
            skLineSegment(sketch, "E4189", {"start": v(-104.25, -53.62) * mm, "end": v(-104.33, -53.7) * mm});
            skLineSegment(sketch, "E4190", {"start": v(-104.33, -53.7) * mm, "end": v(-104.41, -53.78) * mm});
            skLineSegment(sketch, "E4191", {"start": v(-104.41, -53.78) * mm, "end": v(-104.5, -53.86) * mm});
            skLineSegment(sketch, "E4192", {"start": v(-104.5, -53.86) * mm, "end": v(-104.58, -53.95) * mm});
            skLineSegment(sketch, "E4193", {"start": v(-104.58, -53.95) * mm, "end": v(-104.66, -54.03) * mm});
            skLineSegment(sketch, "E4194", {"start": v(-104.66, -54.03) * mm, "end": v(-104.74, -54.12) * mm});
            skLineSegment(sketch, "E4195", {"start": v(-104.74, -54.12) * mm, "end": v(-104.83, -54.2) * mm});
            skLineSegment(sketch, "E4196", {"start": v(-104.83, -54.2) * mm, "end": v(-104.91, -54.3) * mm});
            skLineSegment(sketch, "E4197", {"start": v(-104.91, -54.3) * mm, "end": v(-105, -54.38) * mm});
            skLineSegment(sketch, "E4198", {"start": v(-105, -54.38) * mm, "end": v(-105.08, -54.47) * mm});
            skLineSegment(sketch, "E4199", {"start": v(-105.08, -54.47) * mm, "end": v(-105.17, -54.56) * mm});
            skLineSegment(sketch, "E4200", {"start": v(-105.17, -54.56) * mm, "end": v(-105.25, -54.65) * mm});
            skLineSegment(sketch, "E4201", {"start": v(-105.25, -54.65) * mm, "end": v(-105.34, -54.75) * mm});
            skLineSegment(sketch, "E4202", {"start": v(-105.34, -54.75) * mm, "end": v(-105.43, -54.84) * mm});
            skLineSegment(sketch, "E4203", {"start": v(-105.43, -54.84) * mm, "end": v(-105.52, -54.94) * mm});
            skLineSegment(sketch, "E4204", {"start": v(-105.52, -54.94) * mm, "end": v(-105.6, -55.03) * mm});
            skLineSegment(sketch, "E4205", {"start": v(-105.6, -55.03) * mm, "end": v(-105.7, -55.13) * mm});
            skLineSegment(sketch, "E4206", {"start": v(-105.7, -55.13) * mm, "end": v(-105.79, -55.23) * mm});
            skLineSegment(sketch, "E4207", {"start": v(-105.79, -55.23) * mm, "end": v(-105.88, -55.33) * mm});
            skLineSegment(sketch, "E4208", {"start": v(-105.88, -55.33) * mm, "end": v(-105.97, -55.43) * mm});
            skLineSegment(sketch, "E4209", {"start": v(-105.97, -55.43) * mm, "end": v(-106.06, -55.53) * mm});
            skLineSegment(sketch, "E4210", {"start": v(-106.06, -55.53) * mm, "end": v(-106.15, -55.64) * mm});
            skLineSegment(sketch, "E4211", {"start": v(-106.15, -55.64) * mm, "end": v(-106.24, -55.74) * mm});
            skLineSegment(sketch, "E4212", {"start": v(-106.24, -55.74) * mm, "end": v(-106.33, -55.85) * mm});
            skLineSegment(sketch, "E4213", {"start": v(-106.33, -55.85) * mm, "end": v(-106.43, -55.96) * mm});
            skLineSegment(sketch, "E4214", {"start": v(-106.43, -55.96) * mm, "end": v(-106.52, -56.06) * mm});
            skLineSegment(sketch, "E4215", {"start": v(-106.52, -56.06) * mm, "end": v(-106.7, -56.28) * mm});
            skLineSegment(sketch, "E4216", {"start": v(-106.7, -56.28) * mm, "end": v(-106.8, -56.4) * mm});
            skLineSegment(sketch, "E4217", {"start": v(-106.8, -56.4) * mm, "end": v(-106.9, -56.5) * mm});
            skLineSegment(sketch, "E4218", {"start": v(-106.9, -56.5) * mm, "end": v(-107, -56.62) * mm});
            skLineSegment(sketch, "E4219", {"start": v(-107, -56.62) * mm, "end": v(-107.09, -56.74) * mm});
            skLineSegment(sketch, "E4220", {"start": v(-107.09, -56.74) * mm, "end": v(-107.13, -56.83) * mm});
            skLineSegment(sketch, "E4221", {"start": v(-107.13, -56.83) * mm, "end": v(-106.34, -58.29) * mm});
            skLineSegment(sketch, "E4222", {"start": v(-106.34, -58.29) * mm, "end": v(-106.24, -58.3) * mm});
            skLineSegment(sketch, "E4223", {"start": v(-106.24, -58.3) * mm, "end": v(-106.1, -58.29) * mm});
            skLineSegment(sketch, "E4224", {"start": v(-106.1, -58.29) * mm, "end": v(-105.8, -58.25) * mm});
            skLineSegment(sketch, "E4225", {"start": v(-105.8, -58.25) * mm, "end": v(-105.51, -58.22) * mm});
            skLineSegment(sketch, "E4226", {"start": v(-105.51, -58.22) * mm, "end": v(-105.37, -58.2) * mm});
            skLineSegment(sketch, "E4227", {"start": v(-105.37, -58.2) * mm, "end": v(-105.23, -58.18) * mm});
            skLineSegment(sketch, "E4228", {"start": v(-105.23, -58.18) * mm, "end": v(-105.09, -58.16) * mm});
            skLineSegment(sketch, "E4229", {"start": v(-105.09, -58.16) * mm, "end": v(-104.95, -58.14) * mm});
            skLineSegment(sketch, "E4230", {"start": v(-104.95, -58.14) * mm, "end": v(-104.8, -58.12) * mm});
            skLineSegment(sketch, "E4231", {"start": v(-104.8, -58.12) * mm, "end": v(-104.67, -58.1) * mm});
            skLineSegment(sketch, "E4232", {"start": v(-104.67, -58.1) * mm, "end": v(-104.54, -58.08) * mm});
            skLineSegment(sketch, "E4233", {"start": v(-104.54, -58.08) * mm, "end": v(-104.4, -58.07) * mm});
            skLineSegment(sketch, "E4234", {"start": v(-104.4, -58.07) * mm, "end": v(-104.27, -58.04) * mm});
            skLineSegment(sketch, "E4235", {"start": v(-104.27, -58.04) * mm, "end": v(-104.14, -58.02) * mm});
            skLineSegment(sketch, "E4236", {"start": v(-104.14, -58.02) * mm, "end": v(-104, -58) * mm});
            skLineSegment(sketch, "E4237", {"start": v(-104, -58) * mm, "end": v(-103.88, -57.98) * mm});
            skLineSegment(sketch, "E4238", {"start": v(-103.88, -57.98) * mm, "end": v(-103.75, -57.96) * mm});
            skLineSegment(sketch, "E4239", {"start": v(-103.75, -57.96) * mm, "end": v(-103.62, -57.94) * mm});
            skLineSegment(sketch, "E4240", {"start": v(-103.62, -57.94) * mm, "end": v(-103.37, -57.9) * mm});
            skLineSegment(sketch, "E4241", {"start": v(-103.37, -57.9) * mm, "end": v(-103.25, -57.87) * mm});
            skLineSegment(sketch, "E4242", {"start": v(-103.25, -57.87) * mm, "end": v(-103, -57.83) * mm});
            skLineSegment(sketch, "E4243", {"start": v(-103, -57.83) * mm, "end": v(-102.88, -57.8) * mm});
            skLineSegment(sketch, "E4244", {"start": v(-102.88, -57.8) * mm, "end": v(-102.76, -57.78) * mm});
            skLineSegment(sketch, "E4245", {"start": v(-102.76, -57.78) * mm, "end": v(-102.65, -57.76) * mm});
            skLineSegment(sketch, "E4246", {"start": v(-102.65, -57.76) * mm, "end": v(-102.53, -57.74) * mm});
            skLineSegment(sketch, "E4247", {"start": v(-102.53, -57.74) * mm, "end": v(-102.42, -57.72) * mm});
            skLineSegment(sketch, "E4248", {"start": v(-102.42, -57.72) * mm, "end": v(-102.19, -57.67) * mm});
            skLineSegment(sketch, "E4249", {"start": v(-102.19, -57.67) * mm, "end": v(-102.08, -57.64) * mm});
            skLineSegment(sketch, "E4250", {"start": v(-102.08, -57.64) * mm, "end": v(-101.97, -57.62) * mm});
            skLineSegment(sketch, "E4251", {"start": v(-101.97, -57.62) * mm, "end": v(-101.86, -57.6) * mm});
            skLineSegment(sketch, "E4252", {"start": v(-101.86, -57.6) * mm, "end": v(-101.75, -57.57) * mm});
            skLineSegment(sketch, "E4253", {"start": v(-101.75, -57.57) * mm, "end": v(-101.65, -57.55) * mm});
            skLineSegment(sketch, "E4254", {"start": v(-101.65, -57.55) * mm, "end": v(-101.54, -57.52) * mm});
            skLineSegment(sketch, "E4255", {"start": v(-101.54, -57.52) * mm, "end": v(-100.91, -58.27) * mm});
            skLineSegment(sketch, "E4256", {"start": v(-100.91, -58.27) * mm, "end": v(-100.58, -59.19) * mm});
            skLineSegment(sketch, "E4257", {"start": v(-100.58, -59.19) * mm, "end": v(-100.65, -59.27) * mm});
            skLineSegment(sketch, "E4258", {"start": v(-100.65, -59.27) * mm, "end": v(-100.73, -59.35) * mm});
            skLineSegment(sketch, "E4259", {"start": v(-100.73, -59.35) * mm, "end": v(-100.88, -59.5) * mm});
            skLineSegment(sketch, "E4260", {"start": v(-100.88, -59.5) * mm, "end": v(-101.03, -59.68) * mm});
            skLineSegment(sketch, "E4261", {"start": v(-101.03, -59.68) * mm, "end": v(-101.1, -59.76) * mm});
            skLineSegment(sketch, "E4262", {"start": v(-101.1, -59.76) * mm, "end": v(-101.18, -59.85) * mm});
            skLineSegment(sketch, "E4263", {"start": v(-101.18, -59.85) * mm, "end": v(-101.26, -59.94) * mm});
            skLineSegment(sketch, "E4264", {"start": v(-101.26, -59.94) * mm, "end": v(-101.42, -60.12) * mm});
            skLineSegment(sketch, "E4265", {"start": v(-101.42, -60.12) * mm, "end": v(-101.5, -60.2) * mm});
            skLineSegment(sketch, "E4266", {"start": v(-101.5, -60.2) * mm, "end": v(-101.58, -60.3) * mm});
            skLineSegment(sketch, "E4267", {"start": v(-101.58, -60.3) * mm, "end": v(-101.66, -60.4) * mm});
            skLineSegment(sketch, "E4268", {"start": v(-101.66, -60.4) * mm, "end": v(-101.74, -60.49) * mm});
            skLineSegment(sketch, "E4269", {"start": v(-101.74, -60.49) * mm, "end": v(-101.9, -60.68) * mm});
            skLineSegment(sketch, "E4270", {"start": v(-101.9, -60.68) * mm, "end": v(-101.98, -60.78) * mm});
            skLineSegment(sketch, "E4271", {"start": v(-101.98, -60.78) * mm, "end": v(-102.23, -61.08) * mm});
            skLineSegment(sketch, "E4272", {"start": v(-102.23, -61.08) * mm, "end": v(-102.31, -61.18) * mm});
            skLineSegment(sketch, "E4273", {"start": v(-102.31, -61.18) * mm, "end": v(-102.48, -61.4) * mm});
            skLineSegment(sketch, "E4274", {"start": v(-102.48, -61.4) * mm, "end": v(-102.56, -61.5) * mm});
            skLineSegment(sketch, "E4275", {"start": v(-102.56, -61.5) * mm, "end": v(-102.65, -61.6) * mm});
            skLineSegment(sketch, "E4276", {"start": v(-102.65, -61.6) * mm, "end": v(-102.73, -61.72) * mm});
            skLineSegment(sketch, "E4277", {"start": v(-102.73, -61.72) * mm, "end": v(-102.82, -61.83) * mm});
            skLineSegment(sketch, "E4278", {"start": v(-102.82, -61.83) * mm, "end": v(-102.9, -61.94) * mm});
            skLineSegment(sketch, "E4279", {"start": v(-102.9, -61.94) * mm, "end": v(-103, -62.05) * mm});
            skLineSegment(sketch, "E4280", {"start": v(-103, -62.05) * mm, "end": v(-103.17, -62.28) * mm});
            skLineSegment(sketch, "E4281", {"start": v(-103.17, -62.28) * mm, "end": v(-103.25, -62.4) * mm});
            skLineSegment(sketch, "E4282", {"start": v(-103.25, -62.4) * mm, "end": v(-103.34, -62.51) * mm});
            skLineSegment(sketch, "E4283", {"start": v(-103.34, -62.51) * mm, "end": v(-103.43, -62.63) * mm});
            skLineSegment(sketch, "E4284", {"start": v(-103.43, -62.63) * mm, "end": v(-103.52, -62.75) * mm});
            skLineSegment(sketch, "E4285", {"start": v(-103.52, -62.75) * mm, "end": v(-103.6, -62.87) * mm});
            skLineSegment(sketch, "E4286", {"start": v(-103.6, -62.87) * mm, "end": v(-103.64, -62.96) * mm});
            skLineSegment(sketch, "E4287", {"start": v(-103.64, -62.96) * mm, "end": v(-102.77, -64.37) * mm});
            skLineSegment(sketch, "E4288", {"start": v(-102.77, -64.37) * mm, "end": v(-102.67, -64.38) * mm});
            skLineSegment(sketch, "E4289", {"start": v(-102.67, -64.38) * mm, "end": v(-102.53, -64.36) * mm});
            skLineSegment(sketch, "E4290", {"start": v(-102.53, -64.36) * mm, "end": v(-102.38, -64.33) * mm});
            skLineSegment(sketch, "E4291", {"start": v(-102.38, -64.33) * mm, "end": v(-102.23, -64.3) * mm});
            skLineSegment(sketch, "E4292", {"start": v(-102.23, -64.3) * mm, "end": v(-102.1, -64.28) * mm});
            skLineSegment(sketch, "E4293", {"start": v(-102.1, -64.28) * mm, "end": v(-101.95, -64.25) * mm});
            skLineSegment(sketch, "E4294", {"start": v(-101.95, -64.25) * mm, "end": v(-101.8, -64.23) * mm});
            skLineSegment(sketch, "E4295", {"start": v(-101.8, -64.23) * mm, "end": v(-101.66, -64.2) * mm});
            skLineSegment(sketch, "E4296", {"start": v(-101.66, -64.2) * mm, "end": v(-101.53, -64.17) * mm});
            skLineSegment(sketch, "E4297", {"start": v(-101.53, -64.17) * mm, "end": v(-101.39, -64.15) * mm});
            skLineSegment(sketch, "E4298", {"start": v(-101.39, -64.15) * mm, "end": v(-101.25, -64.12) * mm});
            skLineSegment(sketch, "E4299", {"start": v(-101.25, -64.12) * mm, "end": v(-100.98, -64.07) * mm});
            skLineSegment(sketch, "E4300", {"start": v(-100.98, -64.07) * mm, "end": v(-100.85, -64.04) * mm});
            skLineSegment(sketch, "E4301", {"start": v(-100.85, -64.04) * mm, "end": v(-100.72, -64) * mm});
            skLineSegment(sketch, "E4302", {"start": v(-100.72, -64) * mm, "end": v(-100.59, -63.98) * mm});
            skLineSegment(sketch, "E4303", {"start": v(-100.59, -63.98) * mm, "end": v(-100.46, -63.95) * mm});
            skLineSegment(sketch, "E4304", {"start": v(-100.46, -63.95) * mm, "end": v(-100.33, -63.92) * mm});
            skLineSegment(sketch, "E4305", {"start": v(-100.33, -63.92) * mm, "end": v(-100.2, -63.9) * mm});
            skLineSegment(sketch, "E4306", {"start": v(-100.2, -63.9) * mm, "end": v(-100.08, -63.87) * mm});
            skLineSegment(sketch, "E4307", {"start": v(-100.08, -63.87) * mm, "end": v(-99.83, -63.8) * mm});
            skLineSegment(sketch, "E4308", {"start": v(-99.83, -63.8) * mm, "end": v(-99.7, -63.78) * mm});
            skLineSegment(sketch, "E4309", {"start": v(-99.7, -63.78) * mm, "end": v(-99.59, -63.75) * mm});
            skLineSegment(sketch, "E4310", {"start": v(-99.59, -63.75) * mm, "end": v(-99.47, -63.72) * mm});
            skLineSegment(sketch, "E4311", {"start": v(-99.47, -63.72) * mm, "end": v(-99.35, -63.7) * mm});
            skLineSegment(sketch, "E4312", {"start": v(-99.35, -63.7) * mm, "end": v(-99.23, -63.66) * mm});
            skLineSegment(sketch, "E4313", {"start": v(-99.23, -63.66) * mm, "end": v(-99.12, -63.63) * mm});
            skLineSegment(sketch, "E4314", {"start": v(-99.12, -63.63) * mm, "end": v(-98.89, -63.57) * mm});
            skLineSegment(sketch, "E4315", {"start": v(-98.89, -63.57) * mm, "end": v(-98.78, -63.54) * mm});
            skLineSegment(sketch, "E4316", {"start": v(-98.78, -63.54) * mm, "end": v(-98.66, -63.51) * mm});
            skLineSegment(sketch, "E4317", {"start": v(-98.66, -63.51) * mm, "end": v(-98.45, -63.45) * mm});
            skLineSegment(sketch, "E4318", {"start": v(-98.45, -63.45) * mm, "end": v(-98.34, -63.42) * mm});
            skLineSegment(sketch, "E4319", {"start": v(-98.34, -63.42) * mm, "end": v(-98.23, -63.4) * mm});
            skLineSegment(sketch, "E4320", {"start": v(-98.23, -63.4) * mm, "end": v(-98.13, -63.36) * mm});
            skLineSegment(sketch, "E4321", {"start": v(-98.13, -63.36) * mm, "end": v(-98.02, -63.33) * mm});
            skLineSegment(sketch, "E4322", {"start": v(-98.02, -63.33) * mm, "end": v(-97.35, -64.04) * mm});
            skLineSegment(sketch, "E4323", {"start": v(-97.35, -64.04) * mm, "end": v(-96.97, -64.93) * mm});
            skLineSegment(sketch, "E4324", {"start": v(-96.97, -64.93) * mm, "end": v(-97.04, -65.02) * mm});
            skLineSegment(sketch, "E4325", {"start": v(-97.04, -65.02) * mm, "end": v(-97.1, -65.1) * mm});
            skLineSegment(sketch, "E4326", {"start": v(-97.1, -65.1) * mm, "end": v(-97.18, -65.19) * mm});
            skLineSegment(sketch, "E4327", {"start": v(-97.18, -65.19) * mm, "end": v(-97.32, -65.36) * mm});
            skLineSegment(sketch, "E4328", {"start": v(-97.32, -65.36) * mm, "end": v(-97.39, -65.45) * mm});
            skLineSegment(sketch, "E4329", {"start": v(-97.39, -65.45) * mm, "end": v(-97.46, -65.54) * mm});
            skLineSegment(sketch, "E4330", {"start": v(-97.46, -65.54) * mm, "end": v(-97.53, -65.63) * mm});
            skLineSegment(sketch, "E4331", {"start": v(-97.53, -65.63) * mm, "end": v(-97.6, -65.72) * mm});
            skLineSegment(sketch, "E4332", {"start": v(-97.6, -65.72) * mm, "end": v(-97.68, -65.82) * mm});
            skLineSegment(sketch, "E4333", {"start": v(-97.68, -65.82) * mm, "end": v(-97.82, -66) * mm});
            skLineSegment(sketch, "E4334", {"start": v(-97.82, -66) * mm, "end": v(-97.9, -66.1) * mm});
            skLineSegment(sketch, "E4335", {"start": v(-97.9, -66.1) * mm, "end": v(-98.05, -66.3) * mm});
            skLineSegment(sketch, "E4336", {"start": v(-98.05, -66.3) * mm, "end": v(-98.12, -66.4) * mm});
            skLineSegment(sketch, "E4337", {"start": v(-98.12, -66.4) * mm, "end": v(-98.2, -66.5) * mm});
            skLineSegment(sketch, "E4338", {"start": v(-98.2, -66.5) * mm, "end": v(-98.27, -66.6) * mm});
            skLineSegment(sketch, "E4339", {"start": v(-98.27, -66.6) * mm, "end": v(-98.35, -66.7) * mm});
            skLineSegment(sketch, "E4340", {"start": v(-98.35, -66.7) * mm, "end": v(-98.43, -66.82) * mm});
            skLineSegment(sketch, "E4341", {"start": v(-98.43, -66.82) * mm, "end": v(-98.5, -66.92) * mm});
            skLineSegment(sketch, "E4342", {"start": v(-98.5, -66.92) * mm, "end": v(-98.58, -67.03) * mm});
            skLineSegment(sketch, "E4343", {"start": v(-98.58, -67.03) * mm, "end": v(-98.66, -67.14) * mm});
            skLineSegment(sketch, "E4344", {"start": v(-98.66, -67.14) * mm, "end": v(-98.81, -67.36) * mm});
            skLineSegment(sketch, "E4345", {"start": v(-98.81, -67.36) * mm, "end": v(-98.97, -67.58) * mm});
            skLineSegment(sketch, "E4346", {"start": v(-98.97, -67.58) * mm, "end": v(-99.05, -67.7) * mm});
            skLineSegment(sketch, "E4347", {"start": v(-99.05, -67.7) * mm, "end": v(-99.13, -67.82) * mm});
            skLineSegment(sketch, "E4348", {"start": v(-99.13, -67.82) * mm, "end": v(-99.21, -67.93) * mm});
            skLineSegment(sketch, "E4349", {"start": v(-99.21, -67.93) * mm, "end": v(-99.3, -68.05) * mm});
            skLineSegment(sketch, "E4350", {"start": v(-99.3, -68.05) * mm, "end": v(-99.45, -68.3) * mm});
            skLineSegment(sketch, "E4351", {"start": v(-99.45, -68.3) * mm, "end": v(-99.53, -68.41) * mm});
            skLineSegment(sketch, "E4352", {"start": v(-99.53, -68.41) * mm, "end": v(-99.7, -68.66) * mm});
            skLineSegment(sketch, "E4353", {"start": v(-99.7, -68.66) * mm, "end": v(-99.78, -68.79) * mm});
            skLineSegment(sketch, "E4354", {"start": v(-99.78, -68.79) * mm, "end": v(-99.8, -68.88) * mm});
            skLineSegment(sketch, "E4355", {"start": v(-99.8, -68.88) * mm, "end": v(-98.85, -70.24) * mm});
            skLineSegment(sketch, "E4356", {"start": v(-98.85, -70.24) * mm, "end": v(-98.76, -70.24) * mm});
            skLineSegment(sketch, "E4357", {"start": v(-98.76, -70.24) * mm, "end": v(-98.61, -70.2) * mm});
            skLineSegment(sketch, "E4358", {"start": v(-98.61, -70.2) * mm, "end": v(-98.47, -70.18) * mm});
            skLineSegment(sketch, "E4359", {"start": v(-98.47, -70.18) * mm, "end": v(-98.18, -70.1) * mm});
            skLineSegment(sketch, "E4360", {"start": v(-98.18, -70.1) * mm, "end": v(-98.04, -70.07) * mm});
            skLineSegment(sketch, "E4361", {"start": v(-98.04, -70.07) * mm, "end": v(-97.9, -70.04) * mm});
            skLineSegment(sketch, "E4362", {"start": v(-97.9, -70.04) * mm, "end": v(-97.62, -69.97) * mm});
            skLineSegment(sketch, "E4363", {"start": v(-97.62, -69.97) * mm, "end": v(-97.49, -69.93) * mm});
            skLineSegment(sketch, "E4364", {"start": v(-97.49, -69.93) * mm, "end": v(-97.35, -69.9) * mm});
            skLineSegment(sketch, "E4365", {"start": v(-97.35, -69.9) * mm, "end": v(-97.22, -69.86) * mm});
            skLineSegment(sketch, "E4366", {"start": v(-97.22, -69.86) * mm, "end": v(-97.09, -69.83) * mm});
            skLineSegment(sketch, "E4367", {"start": v(-97.09, -69.83) * mm, "end": v(-96.82, -69.76) * mm});
            skLineSegment(sketch, "E4368", {"start": v(-96.82, -69.76) * mm, "end": v(-96.7, -69.72) * mm});
            skLineSegment(sketch, "E4369", {"start": v(-96.7, -69.72) * mm, "end": v(-96.57, -69.69) * mm});
            skLineSegment(sketch, "E4370", {"start": v(-96.57, -69.69) * mm, "end": v(-96.44, -69.65) * mm});
            skLineSegment(sketch, "E4371", {"start": v(-96.44, -69.65) * mm, "end": v(-96.32, -69.61) * mm});
            skLineSegment(sketch, "E4372", {"start": v(-96.32, -69.61) * mm, "end": v(-96.2, -69.58) * mm});
            skLineSegment(sketch, "E4373", {"start": v(-96.2, -69.58) * mm, "end": v(-96.07, -69.54) * mm});
            skLineSegment(sketch, "E4374", {"start": v(-96.07, -69.54) * mm, "end": v(-95.95, -69.5) * mm});
            skLineSegment(sketch, "E4375", {"start": v(-95.95, -69.5) * mm, "end": v(-95.83, -69.47) * mm});
            skLineSegment(sketch, "E4376", {"start": v(-95.83, -69.47) * mm, "end": v(-95.71, -69.43) * mm});
            skLineSegment(sketch, "E4377", {"start": v(-95.71, -69.43) * mm, "end": v(-95.6, -69.4) * mm});
            skLineSegment(sketch, "E4378", {"start": v(-95.6, -69.4) * mm, "end": v(-95.48, -69.36) * mm});
            skLineSegment(sketch, "E4379", {"start": v(-95.48, -69.36) * mm, "end": v(-95.36, -69.32) * mm});
            skLineSegment(sketch, "E4380", {"start": v(-95.36, -69.32) * mm, "end": v(-95.25, -69.29) * mm});
            skLineSegment(sketch, "E4381", {"start": v(-95.25, -69.29) * mm, "end": v(-95.13, -69.25) * mm});
            skLineSegment(sketch, "E4382", {"start": v(-95.13, -69.25) * mm, "end": v(-95.02, -69.21) * mm});
            skLineSegment(sketch, "E4383", {"start": v(-95.02, -69.21) * mm, "end": v(-94.91, -69.18) * mm});
            skLineSegment(sketch, "E4384", {"start": v(-94.91, -69.18) * mm, "end": v(-94.8, -69.14) * mm});
            skLineSegment(sketch, "E4385", {"start": v(-94.8, -69.14) * mm, "end": v(-94.7, -69.1) * mm});
            skLineSegment(sketch, "E4386", {"start": v(-94.7, -69.1) * mm, "end": v(-94.59, -69.07) * mm});
            skLineSegment(sketch, "E4387", {"start": v(-94.59, -69.07) * mm, "end": v(-94.49, -69.03) * mm});
            skLineSegment(sketch, "E4388", {"start": v(-94.49, -69.03) * mm, "end": v(-94.38, -69) * mm});
            skLineSegment(sketch, "E4389", {"start": v(-94.38, -69) * mm, "end": v(-94.28, -68.96) * mm});
            skLineSegment(sketch, "E4390", {"start": v(-94.28, -68.96) * mm, "end": v(-94.18, -68.92) * mm});
            skLineSegment(sketch, "E4391", {"start": v(-94.18, -68.92) * mm, "end": v(-93.47, -69.59) * mm});
            skLineSegment(sketch, "E4392", {"start": v(-93.47, -69.59) * mm, "end": v(-93.03, -70.46) * mm});
            skLineSegment(sketch, "E4393", {"start": v(-93.03, -70.46) * mm, "end": v(-93.1, -70.55) * mm});
            skLineSegment(sketch, "E4394", {"start": v(-93.1, -70.55) * mm, "end": v(-93.16, -70.64) * mm});
            skLineSegment(sketch, "E4395", {"start": v(-93.16, -70.64) * mm, "end": v(-93.22, -70.73) * mm});
            skLineSegment(sketch, "E4396", {"start": v(-93.22, -70.73) * mm, "end": v(-93.29, -70.82) * mm});
            skLineSegment(sketch, "E4397", {"start": v(-93.29, -70.82) * mm, "end": v(-93.35, -70.9) * mm});
            skLineSegment(sketch, "E4398", {"start": v(-93.35, -70.9) * mm, "end": v(-93.42, -71) * mm});
            skLineSegment(sketch, "E4399", {"start": v(-93.42, -71) * mm, "end": v(-93.48, -71.1) * mm});
            skLineSegment(sketch, "E4400", {"start": v(-93.48, -71.1) * mm, "end": v(-93.55, -71.2) * mm});
            skLineSegment(sketch, "E4401", {"start": v(-93.55, -71.2) * mm, "end": v(-93.62, -71.29) * mm});
            skLineSegment(sketch, "E4402", {"start": v(-93.62, -71.29) * mm, "end": v(-93.75, -71.48) * mm});
            skLineSegment(sketch, "E4403", {"start": v(-93.75, -71.48) * mm, "end": v(-93.82, -71.58) * mm});
            skLineSegment(sketch, "E4404", {"start": v(-93.82, -71.58) * mm, "end": v(-93.89, -71.68) * mm});
            skLineSegment(sketch, "E4405", {"start": v(-93.89, -71.68) * mm, "end": v(-93.96, -71.79) * mm});
            skLineSegment(sketch, "E4406", {"start": v(-93.96, -71.79) * mm, "end": v(-94.03, -71.89) * mm});
            skLineSegment(sketch, "E4407", {"start": v(-94.03, -71.89) * mm, "end": v(-94.1, -72) * mm});
            skLineSegment(sketch, "E4408", {"start": v(-94.1, -72) * mm, "end": v(-94.17, -72.1) * mm});
            skLineSegment(sketch, "E4409", {"start": v(-94.17, -72.1) * mm, "end": v(-94.23, -72.2) * mm});
            skLineSegment(sketch, "E4410", {"start": v(-94.23, -72.2) * mm, "end": v(-94.3, -72.32) * mm});
            skLineSegment(sketch, "E4411", {"start": v(-94.3, -72.32) * mm, "end": v(-94.45, -72.54) * mm});
            skLineSegment(sketch, "E4412", {"start": v(-94.45, -72.54) * mm, "end": v(-94.52, -72.65) * mm});
            skLineSegment(sketch, "E4413", {"start": v(-94.52, -72.65) * mm, "end": v(-94.59, -72.76) * mm});
            skLineSegment(sketch, "E4414", {"start": v(-94.59, -72.76) * mm, "end": v(-94.66, -72.87) * mm});
            skLineSegment(sketch, "E4415", {"start": v(-94.66, -72.87) * mm, "end": v(-94.73, -73) * mm});
            skLineSegment(sketch, "E4416", {"start": v(-94.73, -73) * mm, "end": v(-94.8, -73.1) * mm});
            skLineSegment(sketch, "E4417", {"start": v(-94.8, -73.1) * mm, "end": v(-94.88, -73.22) * mm});
            skLineSegment(sketch, "E4418", {"start": v(-94.88, -73.22) * mm, "end": v(-94.95, -73.34) * mm});
            skLineSegment(sketch, "E4419", {"start": v(-94.95, -73.34) * mm, "end": v(-95.02, -73.46) * mm});
            skLineSegment(sketch, "E4420", {"start": v(-95.02, -73.46) * mm, "end": v(-95.1, -73.59) * mm});
            skLineSegment(sketch, "E4421", {"start": v(-95.1, -73.59) * mm, "end": v(-95.24, -73.83) * mm});
            skLineSegment(sketch, "E4422", {"start": v(-95.24, -73.83) * mm, "end": v(-95.31, -73.96) * mm});
            skLineSegment(sketch, "E4423", {"start": v(-95.31, -73.96) * mm, "end": v(-95.39, -74.09) * mm});
            skLineSegment(sketch, "E4424", {"start": v(-95.39, -74.09) * mm, "end": v(-95.46, -74.21) * mm});
            skLineSegment(sketch, "E4425", {"start": v(-95.46, -74.21) * mm, "end": v(-95.53, -74.34) * mm});
            skLineSegment(sketch, "E4426", {"start": v(-95.53, -74.34) * mm, "end": v(-95.6, -74.47) * mm});
            skLineSegment(sketch, "E4427", {"start": v(-95.6, -74.47) * mm, "end": v(-95.63, -74.57) * mm});
            skLineSegment(sketch, "E4428", {"start": v(-95.63, -74.57) * mm, "end": v(-94.6, -75.87) * mm});
            skLineSegment(sketch, "E4429", {"start": v(-94.6, -75.87) * mm, "end": v(-94.5, -75.87) * mm});
            skLineSegment(sketch, "E4430", {"start": v(-94.5, -75.87) * mm, "end": v(-94.36, -75.82) * mm});
            skLineSegment(sketch, "E4431", {"start": v(-94.36, -75.82) * mm, "end": v(-94.22, -75.78) * mm});
            skLineSegment(sketch, "E4432", {"start": v(-94.22, -75.78) * mm, "end": v(-94.08, -75.74) * mm});
            skLineSegment(sketch, "E4433", {"start": v(-94.08, -75.74) * mm, "end": v(-93.8, -75.65) * mm});
            skLineSegment(sketch, "E4434", {"start": v(-93.8, -75.65) * mm, "end": v(-93.66, -75.61) * mm});
            skLineSegment(sketch, "E4435", {"start": v(-93.66, -75.61) * mm, "end": v(-93.52, -75.57) * mm});
            skLineSegment(sketch, "E4436", {"start": v(-93.52, -75.57) * mm, "end": v(-93.39, -75.53) * mm});
            skLineSegment(sketch, "E4437", {"start": v(-93.39, -75.53) * mm, "end": v(-93.12, -75.44) * mm});
            skLineSegment(sketch, "E4438", {"start": v(-93.12, -75.44) * mm, "end": v(-92.86, -75.36) * mm});
            skLineSegment(sketch, "E4439", {"start": v(-92.86, -75.36) * mm, "end": v(-92.73, -75.31) * mm});
            skLineSegment(sketch, "E4440", {"start": v(-92.73, -75.31) * mm, "end": v(-92.6, -75.27) * mm});
            skLineSegment(sketch, "E4441", {"start": v(-92.6, -75.27) * mm, "end": v(-92.48, -75.23) * mm});
            skLineSegment(sketch, "E4442", {"start": v(-92.48, -75.23) * mm, "end": v(-92.35, -75.18) * mm});
            skLineSegment(sketch, "E4443", {"start": v(-92.35, -75.18) * mm, "end": v(-92.23, -75.14) * mm});
            skLineSegment(sketch, "E4444", {"start": v(-92.23, -75.14) * mm, "end": v(-91.98, -75.05) * mm});
            skLineSegment(sketch, "E4445", {"start": v(-91.98, -75.05) * mm, "end": v(-91.86, -75) * mm});
            skLineSegment(sketch, "E4446", {"start": v(-91.86, -75) * mm, "end": v(-91.63, -74.92) * mm});
            skLineSegment(sketch, "E4447", {"start": v(-91.63, -74.92) * mm, "end": v(-91.51, -74.88) * mm});
            skLineSegment(sketch, "E4448", {"start": v(-91.51, -74.88) * mm, "end": v(-91.4, -74.84) * mm});
            skLineSegment(sketch, "E4449", {"start": v(-91.4, -74.84) * mm, "end": v(-91.28, -74.8) * mm});
            skLineSegment(sketch, "E4450", {"start": v(-91.28, -74.8) * mm, "end": v(-91.17, -74.75) * mm});
            skLineSegment(sketch, "E4451", {"start": v(-91.17, -74.75) * mm, "end": v(-91.06, -74.7) * mm});
            skLineSegment(sketch, "E4452", {"start": v(-91.06, -74.7) * mm, "end": v(-90.84, -74.62) * mm});
            skLineSegment(sketch, "E4453", {"start": v(-90.84, -74.62) * mm, "end": v(-90.73, -74.58) * mm});
            skLineSegment(sketch, "E4454", {"start": v(-90.73, -74.58) * mm, "end": v(-90.52, -74.5) * mm});
            skLineSegment(sketch, "E4455", {"start": v(-90.52, -74.5) * mm, "end": v(-90.41, -74.45) * mm});
            skLineSegment(sketch, "E4456", {"start": v(-90.41, -74.45) * mm, "end": v(-90.31, -74.41) * mm});
            skLineSegment(sketch, "E4457", {"start": v(-90.31, -74.41) * mm, "end": v(-90.2, -74.37) * mm});
            skLineSegment(sketch, "E4458", {"start": v(-90.2, -74.37) * mm, "end": v(-90.1, -74.32) * mm});
            skLineSegment(sketch, "E4459", {"start": v(-90.1, -74.32) * mm, "end": v(-90, -74.28) * mm});
            skLineSegment(sketch, "E4460", {"start": v(-90, -74.28) * mm, "end": v(-89.26, -74.9) * mm});
            skLineSegment(sketch, "E4461", {"start": v(-89.26, -74.9) * mm, "end": v(-88.78, -75.75) * mm});
            skLineSegment(sketch, "E4462", {"start": v(-88.78, -75.75) * mm, "end": v(-88.84, -75.84) * mm});
            skLineSegment(sketch, "E4463", {"start": v(-88.84, -75.84) * mm, "end": v(-88.9, -75.93) * mm});
            skLineSegment(sketch, "E4464", {"start": v(-88.9, -75.93) * mm, "end": v(-88.95, -76.03) * mm});
            skLineSegment(sketch, "E4465", {"start": v(-88.95, -76.03) * mm, "end": v(-89.01, -76.12) * mm});
            skLineSegment(sketch, "E4466", {"start": v(-89.01, -76.12) * mm, "end": v(-89.07, -76.22) * mm});
            skLineSegment(sketch, "E4467", {"start": v(-89.07, -76.22) * mm, "end": v(-89.13, -76.31) * mm});
            skLineSegment(sketch, "E4468", {"start": v(-89.13, -76.31) * mm, "end": v(-89.2, -76.41) * mm});
            skLineSegment(sketch, "E4469", {"start": v(-89.2, -76.41) * mm, "end": v(-89.31, -76.6) * mm});
            skLineSegment(sketch, "E4470", {"start": v(-89.31, -76.6) * mm, "end": v(-89.44, -76.81) * mm});
            skLineSegment(sketch, "E4471", {"start": v(-89.44, -76.81) * mm, "end": v(-89.5, -76.92) * mm});
            skLineSegment(sketch, "E4472", {"start": v(-89.5, -76.92) * mm, "end": v(-89.56, -77.02) * mm});
            skLineSegment(sketch, "E4473", {"start": v(-89.56, -77.02) * mm, "end": v(-89.62, -77.13) * mm});
            skLineSegment(sketch, "E4474", {"start": v(-89.62, -77.13) * mm, "end": v(-89.69, -77.24) * mm});
            skLineSegment(sketch, "E4475", {"start": v(-89.69, -77.24) * mm, "end": v(-89.75, -77.34) * mm});
            skLineSegment(sketch, "E4476", {"start": v(-89.75, -77.34) * mm, "end": v(-89.88, -77.56) * mm});
            skLineSegment(sketch, "E4477", {"start": v(-89.88, -77.56) * mm, "end": v(-89.94, -77.68) * mm});
            skLineSegment(sketch, "E4478", {"start": v(-89.94, -77.68) * mm, "end": v(-90, -77.8) * mm});
            skLineSegment(sketch, "E4479", {"start": v(-90, -77.8) * mm, "end": v(-90.07, -77.9) * mm});
            skLineSegment(sketch, "E4480", {"start": v(-90.07, -77.9) * mm, "end": v(-90.13, -78.02) * mm});
            skLineSegment(sketch, "E4481", {"start": v(-90.13, -78.02) * mm, "end": v(-90.2, -78.14) * mm});
            skLineSegment(sketch, "E4482", {"start": v(-90.2, -78.14) * mm, "end": v(-90.33, -78.37) * mm});
            skLineSegment(sketch, "E4483", {"start": v(-90.33, -78.37) * mm, "end": v(-90.4, -78.5) * mm});
            skLineSegment(sketch, "E4484", {"start": v(-90.4, -78.5) * mm, "end": v(-90.46, -78.62) * mm});
            skLineSegment(sketch, "E4485", {"start": v(-90.46, -78.62) * mm, "end": v(-90.59, -78.87) * mm});
            skLineSegment(sketch, "E4486", {"start": v(-90.59, -78.87) * mm, "end": v(-90.65, -79) * mm});
            skLineSegment(sketch, "E4487", {"start": v(-90.65, -79) * mm, "end": v(-90.72, -79.12) * mm});
            skLineSegment(sketch, "E4488", {"start": v(-90.72, -79.12) * mm, "end": v(-90.78, -79.25) * mm});
            skLineSegment(sketch, "E4489", {"start": v(-90.78, -79.25) * mm, "end": v(-90.92, -79.5) * mm});
            skLineSegment(sketch, "E4490", {"start": v(-90.92, -79.5) * mm, "end": v(-90.98, -79.64) * mm});
            skLineSegment(sketch, "E4491", {"start": v(-90.98, -79.64) * mm, "end": v(-91.11, -79.9) * mm});
            skLineSegment(sketch, "E4492", {"start": v(-91.11, -79.9) * mm, "end": v(-91.14, -80) * mm});
            skLineSegment(sketch, "E4493", {"start": v(-91.14, -80) * mm, "end": v(-90.03, -81.24) * mm});
            skLineSegment(sketch, "E4494", {"start": v(-90.03, -81.24) * mm, "end": v(-89.93, -81.23) * mm});
            skLineSegment(sketch, "E4495", {"start": v(-89.93, -81.23) * mm, "end": v(-89.8, -81.18) * mm});
            skLineSegment(sketch, "E4496", {"start": v(-89.8, -81.18) * mm, "end": v(-89.65, -81.13) * mm});
            skLineSegment(sketch, "E4497", {"start": v(-89.65, -81.13) * mm, "end": v(-89.51, -81.08) * mm});
            skLineSegment(sketch, "E4498", {"start": v(-89.51, -81.08) * mm, "end": v(-89.38, -81.03) * mm});
            skLineSegment(sketch, "E4499", {"start": v(-89.38, -81.03) * mm, "end": v(-89.24, -80.98) * mm});
            skLineSegment(sketch, "E4500", {"start": v(-89.24, -80.98) * mm, "end": v(-89.1, -80.93) * mm});
            skLineSegment(sketch, "E4501", {"start": v(-89.1, -80.93) * mm, "end": v(-88.97, -80.88) * mm});
            skLineSegment(sketch, "E4502", {"start": v(-88.97, -80.88) * mm, "end": v(-88.84, -80.83) * mm});
            skLineSegment(sketch, "E4503", {"start": v(-88.84, -80.83) * mm, "end": v(-88.7, -80.78) * mm});
            skLineSegment(sketch, "E4504", {"start": v(-88.7, -80.78) * mm, "end": v(-88.58, -80.73) * mm});
            skLineSegment(sketch, "E4505", {"start": v(-88.58, -80.73) * mm, "end": v(-88.45, -80.68) * mm});
            skLineSegment(sketch, "E4506", {"start": v(-88.45, -80.68) * mm, "end": v(-88.32, -80.63) * mm});
            skLineSegment(sketch, "E4507", {"start": v(-88.32, -80.63) * mm, "end": v(-88.2, -80.58) * mm});
            skLineSegment(sketch, "E4508", {"start": v(-88.2, -80.58) * mm, "end": v(-88.07, -80.53) * mm});
            skLineSegment(sketch, "E4509", {"start": v(-88.07, -80.53) * mm, "end": v(-87.95, -80.48) * mm});
            skLineSegment(sketch, "E4510", {"start": v(-87.95, -80.48) * mm, "end": v(-87.83, -80.43) * mm});
            skLineSegment(sketch, "E4511", {"start": v(-87.83, -80.43) * mm, "end": v(-87.7, -80.37) * mm});
            skLineSegment(sketch, "E4512", {"start": v(-87.7, -80.37) * mm, "end": v(-87.58, -80.32) * mm});
            skLineSegment(sketch, "E4513", {"start": v(-87.58, -80.32) * mm, "end": v(-87.47, -80.27) * mm});
            skLineSegment(sketch, "E4514", {"start": v(-87.47, -80.27) * mm, "end": v(-87.35, -80.22) * mm});
            skLineSegment(sketch, "E4515", {"start": v(-87.35, -80.22) * mm, "end": v(-87.23, -80.17) * mm});
            skLineSegment(sketch, "E4516", {"start": v(-87.23, -80.17) * mm, "end": v(-87.12, -80.12) * mm});
            skLineSegment(sketch, "E4517", {"start": v(-87.12, -80.12) * mm, "end": v(-87, -80.07) * mm});
            skLineSegment(sketch, "E4518", {"start": v(-87, -80.07) * mm, "end": v(-86.89, -80.02) * mm});
            skLineSegment(sketch, "E4519", {"start": v(-86.89, -80.02) * mm, "end": v(-86.67, -79.92) * mm});
            skLineSegment(sketch, "E4520", {"start": v(-86.67, -79.92) * mm, "end": v(-86.56, -79.88) * mm});
            skLineSegment(sketch, "E4521", {"start": v(-86.56, -79.88) * mm, "end": v(-86.34, -79.78) * mm});
            skLineSegment(sketch, "E4522", {"start": v(-86.34, -79.78) * mm, "end": v(-86.24, -79.73) * mm});
            skLineSegment(sketch, "E4523", {"start": v(-86.24, -79.73) * mm, "end": v(-86.14, -79.68) * mm});
            skLineSegment(sketch, "E4524", {"start": v(-86.14, -79.68) * mm, "end": v(-85.93, -79.58) * mm});
            skLineSegment(sketch, "E4525", {"start": v(-85.93, -79.58) * mm, "end": v(-85.83, -79.53) * mm});
            skLineSegment(sketch, "E4526", {"start": v(-85.83, -79.53) * mm, "end": v(-85.73, -79.49) * mm});
            skLineSegment(sketch, "E4527", {"start": v(-85.73, -79.49) * mm, "end": v(-85.63, -79.44) * mm});
            skLineSegment(sketch, "E4528", {"start": v(-85.63, -79.44) * mm, "end": v(-85.54, -79.4) * mm});
            skLineSegment(sketch, "E4529", {"start": v(-85.54, -79.4) * mm, "end": v(-84.75, -79.97) * mm});
            skLineSegment(sketch, "E4530", {"start": v(-84.75, -79.97) * mm, "end": v(-84.22, -80.79) * mm});
            skLineSegment(sketch, "E4531", {"start": v(-84.22, -80.79) * mm, "end": v(-84.27, -80.88) * mm});
            skLineSegment(sketch, "E4532", {"start": v(-84.27, -80.88) * mm, "end": v(-84.33, -80.97) * mm});
            skLineSegment(sketch, "E4533", {"start": v(-84.33, -80.97) * mm, "end": v(-84.38, -81.07) * mm});
            skLineSegment(sketch, "E4534", {"start": v(-84.38, -81.07) * mm, "end": v(-84.44, -81.17) * mm});
            skLineSegment(sketch, "E4535", {"start": v(-84.44, -81.17) * mm, "end": v(-84.5, -81.27) * mm});
            skLineSegment(sketch, "E4536", {"start": v(-84.5, -81.27) * mm, "end": v(-84.54, -81.37) * mm});
            skLineSegment(sketch, "E4537", {"start": v(-84.54, -81.37) * mm, "end": v(-84.65, -81.57) * mm});
            skLineSegment(sketch, "E4538", {"start": v(-84.65, -81.57) * mm, "end": v(-84.7, -81.67) * mm});
            skLineSegment(sketch, "E4539", {"start": v(-84.7, -81.67) * mm, "end": v(-84.76, -81.78) * mm});
            skLineSegment(sketch, "E4540", {"start": v(-84.76, -81.78) * mm, "end": v(-84.82, -81.88) * mm});
            skLineSegment(sketch, "E4541", {"start": v(-84.82, -81.88) * mm, "end": v(-84.88, -82) * mm});
            skLineSegment(sketch, "E4542", {"start": v(-84.88, -82) * mm, "end": v(-84.99, -82.2) * mm});
            skLineSegment(sketch, "E4543", {"start": v(-84.99, -82.2) * mm, "end": v(-85.04, -82.32) * mm});
            skLineSegment(sketch, "E4544", {"start": v(-85.04, -82.32) * mm, "end": v(-85.1, -82.43) * mm});
            skLineSegment(sketch, "E4545", {"start": v(-85.1, -82.43) * mm, "end": v(-85.16, -82.54) * mm});
            skLineSegment(sketch, "E4546", {"start": v(-85.16, -82.54) * mm, "end": v(-85.22, -82.66) * mm});
            skLineSegment(sketch, "E4547", {"start": v(-85.22, -82.66) * mm, "end": v(-85.27, -82.77) * mm});
            skLineSegment(sketch, "E4548", {"start": v(-85.27, -82.77) * mm, "end": v(-85.33, -82.9) * mm});
            skLineSegment(sketch, "E4549", {"start": v(-85.33, -82.9) * mm, "end": v(-85.39, -83.01) * mm});
            skLineSegment(sketch, "E4550", {"start": v(-85.39, -83.01) * mm, "end": v(-85.44, -83.13) * mm});
            skLineSegment(sketch, "E4551", {"start": v(-85.44, -83.13) * mm, "end": v(-85.5, -83.25) * mm});
            skLineSegment(sketch, "E4552", {"start": v(-85.5, -83.25) * mm, "end": v(-85.56, -83.37) * mm});
            skLineSegment(sketch, "E4553", {"start": v(-85.56, -83.37) * mm, "end": v(-85.62, -83.5) * mm});
            skLineSegment(sketch, "E4554", {"start": v(-85.62, -83.5) * mm, "end": v(-85.73, -83.74) * mm});
            skLineSegment(sketch, "E4555", {"start": v(-85.73, -83.74) * mm, "end": v(-85.79, -83.87) * mm});
            skLineSegment(sketch, "E4556", {"start": v(-85.79, -83.87) * mm, "end": v(-85.85, -84) * mm});
            skLineSegment(sketch, "E4557", {"start": v(-85.85, -84) * mm, "end": v(-85.9, -84.13) * mm});
            skLineSegment(sketch, "E4558", {"start": v(-85.9, -84.13) * mm, "end": v(-85.96, -84.26) * mm});
            skLineSegment(sketch, "E4559", {"start": v(-85.96, -84.26) * mm, "end": v(-86.08, -84.52) * mm});
            skLineSegment(sketch, "E4560", {"start": v(-86.08, -84.52) * mm, "end": v(-86.14, -84.66) * mm});
            skLineSegment(sketch, "E4561", {"start": v(-86.14, -84.66) * mm, "end": v(-86.2, -84.8) * mm});
            skLineSegment(sketch, "E4562", {"start": v(-86.2, -84.8) * mm, "end": v(-86.26, -84.93) * mm});
            skLineSegment(sketch, "E4563", {"start": v(-86.26, -84.93) * mm, "end": v(-86.31, -85.07) * mm});
            skLineSegment(sketch, "E4564", {"start": v(-86.31, -85.07) * mm, "end": v(-86.33, -85.17) * mm});
            skLineSegment(sketch, "E4565", {"start": v(-86.33, -85.17) * mm, "end": v(-85.16, -86.34) * mm});
            skLineSegment(sketch, "E4566", {"start": v(-85.16, -86.34) * mm, "end": v(-85.06, -86.32) * mm});
            skLineSegment(sketch, "E4567", {"start": v(-85.06, -86.32) * mm, "end": v(-84.92, -86.27) * mm});
            skLineSegment(sketch, "E4568", {"start": v(-84.92, -86.27) * mm, "end": v(-84.78, -86.2) * mm});
            skLineSegment(sketch, "E4569", {"start": v(-84.78, -86.2) * mm, "end": v(-84.65, -86.15) * mm});
            skLineSegment(sketch, "E4570", {"start": v(-84.65, -86.15) * mm, "end": v(-84.51, -86.1) * mm});
            skLineSegment(sketch, "E4571", {"start": v(-84.51, -86.1) * mm, "end": v(-84.38, -86.03) * mm});
            skLineSegment(sketch, "E4572", {"start": v(-84.38, -86.03) * mm, "end": v(-84.25, -85.97) * mm});
            skLineSegment(sketch, "E4573", {"start": v(-84.25, -85.97) * mm, "end": v(-84.12, -85.92) * mm});
            skLineSegment(sketch, "E4574", {"start": v(-84.12, -85.92) * mm, "end": v(-83.99, -85.86) * mm});
            skLineSegment(sketch, "E4575", {"start": v(-83.99, -85.86) * mm, "end": v(-83.86, -85.8) * mm});
            skLineSegment(sketch, "E4576", {"start": v(-83.86, -85.8) * mm, "end": v(-83.73, -85.74) * mm});
            skLineSegment(sketch, "E4577", {"start": v(-83.73, -85.74) * mm, "end": v(-83.6, -85.68) * mm});
            skLineSegment(sketch, "E4578", {"start": v(-83.6, -85.68) * mm, "end": v(-83.36, -85.57) * mm});
            skLineSegment(sketch, "E4579", {"start": v(-83.36, -85.57) * mm, "end": v(-83.24, -85.51) * mm});
            skLineSegment(sketch, "E4580", {"start": v(-83.24, -85.51) * mm, "end": v(-83.12, -85.45) * mm});
            skLineSegment(sketch, "E4581", {"start": v(-83.12, -85.45) * mm, "end": v(-82.88, -85.34) * mm});
            skLineSegment(sketch, "E4582", {"start": v(-82.88, -85.34) * mm, "end": v(-82.76, -85.28) * mm});
            skLineSegment(sketch, "E4583", {"start": v(-82.76, -85.28) * mm, "end": v(-82.65, -85.22) * mm});
            skLineSegment(sketch, "E4584", {"start": v(-82.65, -85.22) * mm, "end": v(-82.53, -85.17) * mm});
            skLineSegment(sketch, "E4585", {"start": v(-82.53, -85.17) * mm, "end": v(-82.42, -85.11) * mm});
            skLineSegment(sketch, "E4586", {"start": v(-82.42, -85.11) * mm, "end": v(-82.31, -85.05) * mm});
            skLineSegment(sketch, "E4587", {"start": v(-82.31, -85.05) * mm, "end": v(-82.09, -84.94) * mm});
            skLineSegment(sketch, "E4588", {"start": v(-82.09, -84.94) * mm, "end": v(-81.98, -84.89) * mm});
            skLineSegment(sketch, "E4589", {"start": v(-81.98, -84.89) * mm, "end": v(-81.87, -84.83) * mm});
            skLineSegment(sketch, "E4590", {"start": v(-81.87, -84.83) * mm, "end": v(-81.77, -84.77) * mm});
            skLineSegment(sketch, "E4591", {"start": v(-81.77, -84.77) * mm, "end": v(-81.66, -84.72) * mm});
            skLineSegment(sketch, "E4592", {"start": v(-81.66, -84.72) * mm, "end": v(-81.56, -84.66) * mm});
            skLineSegment(sketch, "E4593", {"start": v(-81.56, -84.66) * mm, "end": v(-81.46, -84.6) * mm});
            skLineSegment(sketch, "E4594", {"start": v(-81.46, -84.6) * mm, "end": v(-81.26, -84.5) * mm});
            skLineSegment(sketch, "E4595", {"start": v(-81.26, -84.5) * mm, "end": v(-81.06, -84.4) * mm});
            skLineSegment(sketch, "E4596", {"start": v(-81.06, -84.4) * mm, "end": v(-80.97, -84.34) * mm});
            skLineSegment(sketch, "E4597", {"start": v(-80.97, -84.34) * mm, "end": v(-80.87, -84.28) * mm});
            skLineSegment(sketch, "E4598", {"start": v(-80.87, -84.28) * mm, "end": v(-80.78, -84.23) * mm});
            skLineSegment(sketch, "E4599", {"start": v(-80.78, -84.23) * mm, "end": v(-79.96, -84.76) * mm});
            skLineSegment(sketch, "E4600", {"start": v(-79.96, -84.76) * mm, "end": v(-79.38, -85.55) * mm});
            skLineSegment(sketch, "E4601", {"start": v(-79.38, -85.55) * mm, "end": v(-79.43, -85.64) * mm});
            skLineSegment(sketch, "E4602", {"start": v(-79.43, -85.64) * mm, "end": v(-79.48, -85.74) * mm});
            skLineSegment(sketch, "E4603", {"start": v(-79.48, -85.74) * mm, "end": v(-79.53, -85.84) * mm});
            skLineSegment(sketch, "E4604", {"start": v(-79.53, -85.84) * mm, "end": v(-79.62, -86.04) * mm});
            skLineSegment(sketch, "E4605", {"start": v(-79.62, -86.04) * mm, "end": v(-79.67, -86.15) * mm});
            skLineSegment(sketch, "E4606", {"start": v(-79.67, -86.15) * mm, "end": v(-79.72, -86.25) * mm});
            skLineSegment(sketch, "E4607", {"start": v(-79.72, -86.25) * mm, "end": v(-79.77, -86.35) * mm});
            skLineSegment(sketch, "E4608", {"start": v(-79.77, -86.35) * mm, "end": v(-79.82, -86.46) * mm});
            skLineSegment(sketch, "E4609", {"start": v(-79.82, -86.46) * mm, "end": v(-79.87, -86.57) * mm});
            skLineSegment(sketch, "E4610", {"start": v(-79.87, -86.57) * mm, "end": v(-79.92, -86.68) * mm});
            skLineSegment(sketch, "E4611", {"start": v(-79.92, -86.68) * mm, "end": v(-79.96, -86.79) * mm});
            skLineSegment(sketch, "E4612", {"start": v(-79.96, -86.79) * mm, "end": v(-80.01, -86.9) * mm});
            skLineSegment(sketch, "E4613", {"start": v(-80.01, -86.9) * mm, "end": v(-80.07, -87.01) * mm});
            skLineSegment(sketch, "E4614", {"start": v(-80.07, -87.01) * mm, "end": v(-80.12, -87.13) * mm});
            skLineSegment(sketch, "E4615", {"start": v(-80.12, -87.13) * mm, "end": v(-80.21, -87.36) * mm});
            skLineSegment(sketch, "E4616", {"start": v(-80.21, -87.36) * mm, "end": v(-80.26, -87.47) * mm});
            skLineSegment(sketch, "E4617", {"start": v(-80.26, -87.47) * mm, "end": v(-80.31, -87.6) * mm});
            skLineSegment(sketch, "E4618", {"start": v(-80.31, -87.6) * mm, "end": v(-80.36, -87.71) * mm});
            skLineSegment(sketch, "E4619", {"start": v(-80.36, -87.71) * mm, "end": v(-80.42, -87.83) * mm});
            skLineSegment(sketch, "E4620", {"start": v(-80.42, -87.83) * mm, "end": v(-80.47, -87.96) * mm});
            skLineSegment(sketch, "E4621", {"start": v(-80.47, -87.96) * mm, "end": v(-80.52, -88.08) * mm});
            skLineSegment(sketch, "E4622", {"start": v(-80.52, -88.08) * mm, "end": v(-80.57, -88.2) * mm});
            skLineSegment(sketch, "E4623", {"start": v(-80.57, -88.2) * mm, "end": v(-80.62, -88.33) * mm});
            skLineSegment(sketch, "E4624", {"start": v(-80.62, -88.33) * mm, "end": v(-80.72, -88.59) * mm});
            skLineSegment(sketch, "E4625", {"start": v(-80.72, -88.59) * mm, "end": v(-80.77, -88.72) * mm});
            skLineSegment(sketch, "E4626", {"start": v(-80.77, -88.72) * mm, "end": v(-80.82, -88.85) * mm});
            skLineSegment(sketch, "E4627", {"start": v(-80.82, -88.85) * mm, "end": v(-80.87, -88.98) * mm});
            skLineSegment(sketch, "E4628", {"start": v(-80.87, -88.98) * mm, "end": v(-80.92, -89.11) * mm});
            skLineSegment(sketch, "E4629", {"start": v(-80.92, -89.11) * mm, "end": v(-80.97, -89.25) * mm});
            skLineSegment(sketch, "E4630", {"start": v(-80.97, -89.25) * mm, "end": v(-81.02, -89.39) * mm});
            skLineSegment(sketch, "E4631", {"start": v(-81.02, -89.39) * mm, "end": v(-81.12, -89.66) * mm});
            skLineSegment(sketch, "E4632", {"start": v(-81.12, -89.66) * mm, "end": v(-81.22, -89.94) * mm});
            skLineSegment(sketch, "E4633", {"start": v(-81.22, -89.94) * mm, "end": v(-81.23, -90.04) * mm});
            skLineSegment(sketch, "E4634", {"start": v(-81.23, -90.04) * mm, "end": v(-80, -91.14) * mm});
            skLineSegment(sketch, "E4635", {"start": v(-80, -91.14) * mm, "end": v(-79.9, -91.12) * mm});
            skLineSegment(sketch, "E4636", {"start": v(-79.9, -91.12) * mm, "end": v(-79.76, -91.06) * mm});
            skLineSegment(sketch, "E4637", {"start": v(-79.76, -91.06) * mm, "end": v(-79.63, -91) * mm});
            skLineSegment(sketch, "E4638", {"start": v(-79.63, -91) * mm, "end": v(-79.5, -90.92) * mm});
            skLineSegment(sketch, "E4639", {"start": v(-79.5, -90.92) * mm, "end": v(-79.37, -90.86) * mm});
            skLineSegment(sketch, "E4640", {"start": v(-79.37, -90.86) * mm, "end": v(-79.24, -90.8) * mm});
            skLineSegment(sketch, "E4641", {"start": v(-79.24, -90.8) * mm, "end": v(-79.1, -90.73) * mm});
            skLineSegment(sketch, "E4642", {"start": v(-79.1, -90.73) * mm, "end": v(-78.98, -90.66) * mm});
            skLineSegment(sketch, "E4643", {"start": v(-78.98, -90.66) * mm, "end": v(-78.86, -90.6) * mm});
            skLineSegment(sketch, "E4644", {"start": v(-78.86, -90.6) * mm, "end": v(-78.73, -90.53) * mm});
            skLineSegment(sketch, "E4645", {"start": v(-78.73, -90.53) * mm, "end": v(-78.6, -90.47) * mm});
            skLineSegment(sketch, "E4646", {"start": v(-78.6, -90.47) * mm, "end": v(-78.49, -90.4) * mm});
            skLineSegment(sketch, "E4647", {"start": v(-78.49, -90.4) * mm, "end": v(-78.37, -90.33) * mm});
            skLineSegment(sketch, "E4648", {"start": v(-78.37, -90.33) * mm, "end": v(-78.24, -90.27) * mm});
            skLineSegment(sketch, "E4649", {"start": v(-78.24, -90.27) * mm, "end": v(-78.13, -90.2) * mm});
            skLineSegment(sketch, "E4650", {"start": v(-78.13, -90.2) * mm, "end": v(-78.01, -90.14) * mm});
            skLineSegment(sketch, "E4651", {"start": v(-78.01, -90.14) * mm, "end": v(-77.9, -90.08) * mm});
            skLineSegment(sketch, "E4652", {"start": v(-77.9, -90.08) * mm, "end": v(-77.78, -90.01) * mm});
            skLineSegment(sketch, "E4653", {"start": v(-77.78, -90.01) * mm, "end": v(-77.67, -89.95) * mm});
            skLineSegment(sketch, "E4654", {"start": v(-77.67, -89.95) * mm, "end": v(-77.44, -89.82) * mm});
            skLineSegment(sketch, "E4655", {"start": v(-77.44, -89.82) * mm, "end": v(-77.33, -89.76) * mm});
            skLineSegment(sketch, "E4656", {"start": v(-77.33, -89.76) * mm, "end": v(-77.23, -89.7) * mm});
            skLineSegment(sketch, "E4657", {"start": v(-77.23, -89.7) * mm, "end": v(-77.12, -89.63) * mm});
            skLineSegment(sketch, "E4658", {"start": v(-77.12, -89.63) * mm, "end": v(-77.01, -89.57) * mm});
            skLineSegment(sketch, "E4659", {"start": v(-77.01, -89.57) * mm, "end": v(-76.9, -89.5) * mm});
            skLineSegment(sketch, "E4660", {"start": v(-76.9, -89.5) * mm, "end": v(-76.8, -89.45) * mm});
            skLineSegment(sketch, "E4661", {"start": v(-76.8, -89.45) * mm, "end": v(-76.6, -89.32) * mm});
            skLineSegment(sketch, "E4662", {"start": v(-76.6, -89.32) * mm, "end": v(-76.4, -89.2) * mm});
            skLineSegment(sketch, "E4663", {"start": v(-76.4, -89.2) * mm, "end": v(-76.3, -89.14) * mm});
            skLineSegment(sketch, "E4664", {"start": v(-76.3, -89.14) * mm, "end": v(-76.2, -89.08) * mm});
            skLineSegment(sketch, "E4665", {"start": v(-76.2, -89.08) * mm, "end": v(-76.11, -89.02) * mm});
            skLineSegment(sketch, "E4666", {"start": v(-76.11, -89.02) * mm, "end": v(-76.02, -88.96) * mm});
            skLineSegment(sketch, "E4667", {"start": v(-76.02, -88.96) * mm, "end": v(-75.92, -88.9) * mm});
            skLineSegment(sketch, "E4668", {"start": v(-75.92, -88.9) * mm, "end": v(-75.83, -88.84) * mm});
            skLineSegment(sketch, "E4669", {"start": v(-75.83, -88.84) * mm, "end": v(-75.74, -88.78) * mm});
            skLineSegment(sketch, "E4670", {"start": v(-75.74, -88.78) * mm, "end": v(-74.9, -89.27) * mm});
            skLineSegment(sketch, "E4671", {"start": v(-74.9, -89.27) * mm, "end": v(-74.27, -90.02) * mm});
            skLineSegment(sketch, "E4672", {"start": v(-74.27, -90.02) * mm, "end": v(-74.31, -90.12) * mm});
            skLineSegment(sketch, "E4673", {"start": v(-74.31, -90.12) * mm, "end": v(-74.36, -90.22) * mm});
            skLineSegment(sketch, "E4674", {"start": v(-74.36, -90.22) * mm, "end": v(-74.4, -90.32) * mm});
            skLineSegment(sketch, "E4675", {"start": v(-74.4, -90.32) * mm, "end": v(-74.48, -90.53) * mm});
            skLineSegment(sketch, "E4676", {"start": v(-74.48, -90.53) * mm, "end": v(-74.57, -90.74) * mm});
            skLineSegment(sketch, "E4677", {"start": v(-74.57, -90.74) * mm, "end": v(-74.61, -90.85) * mm});
            skLineSegment(sketch, "E4678", {"start": v(-74.61, -90.85) * mm, "end": v(-74.7, -91.07) * mm});
            skLineSegment(sketch, "E4679", {"start": v(-74.7, -91.07) * mm, "end": v(-74.74, -91.18) * mm});
            skLineSegment(sketch, "E4680", {"start": v(-74.74, -91.18) * mm, "end": v(-74.78, -91.3) * mm});
            skLineSegment(sketch, "E4681", {"start": v(-74.78, -91.3) * mm, "end": v(-74.83, -91.4) * mm});
            skLineSegment(sketch, "E4682", {"start": v(-74.83, -91.4) * mm, "end": v(-74.91, -91.64) * mm});
            skLineSegment(sketch, "E4683", {"start": v(-74.91, -91.64) * mm, "end": v(-74.96, -91.75) * mm});
            skLineSegment(sketch, "E4684", {"start": v(-74.96, -91.75) * mm, "end": v(-75, -91.87) * mm});
            skLineSegment(sketch, "E4685", {"start": v(-75, -91.87) * mm, "end": v(-75.04, -92) * mm});
            skLineSegment(sketch, "E4686", {"start": v(-75.04, -92) * mm, "end": v(-75.09, -92.11) * mm});
            skLineSegment(sketch, "E4687", {"start": v(-75.09, -92.11) * mm, "end": v(-75.13, -92.24) * mm});
            skLineSegment(sketch, "E4688", {"start": v(-75.13, -92.24) * mm, "end": v(-75.21, -92.49) * mm});
            skLineSegment(sketch, "E4689", {"start": v(-75.21, -92.49) * mm, "end": v(-75.26, -92.61) * mm});
            skLineSegment(sketch, "E4690", {"start": v(-75.26, -92.61) * mm, "end": v(-75.34, -92.87) * mm});
            skLineSegment(sketch, "E4691", {"start": v(-75.34, -92.87) * mm, "end": v(-75.39, -93) * mm});
            skLineSegment(sketch, "E4692", {"start": v(-75.39, -93) * mm, "end": v(-75.43, -93.13) * mm});
            skLineSegment(sketch, "E4693", {"start": v(-75.43, -93.13) * mm, "end": v(-75.52, -93.4) * mm});
            skLineSegment(sketch, "E4694", {"start": v(-75.52, -93.4) * mm, "end": v(-75.56, -93.53) * mm});
            skLineSegment(sketch, "E4695", {"start": v(-75.56, -93.53) * mm, "end": v(-75.6, -93.67) * mm});
            skLineSegment(sketch, "E4696", {"start": v(-75.6, -93.67) * mm, "end": v(-75.64, -93.8) * mm});
            skLineSegment(sketch, "E4697", {"start": v(-75.64, -93.8) * mm, "end": v(-75.69, -93.95) * mm});
            skLineSegment(sketch, "E4698", {"start": v(-75.69, -93.95) * mm, "end": v(-75.73, -94.09) * mm});
            skLineSegment(sketch, "E4699", {"start": v(-75.73, -94.09) * mm, "end": v(-75.77, -94.23) * mm});
            skLineSegment(sketch, "E4700", {"start": v(-75.77, -94.23) * mm, "end": v(-75.81, -94.37) * mm});
            skLineSegment(sketch, "E4701", {"start": v(-75.81, -94.37) * mm, "end": v(-75.86, -94.51) * mm});
            skLineSegment(sketch, "E4702", {"start": v(-75.86, -94.51) * mm, "end": v(-75.86, -94.61) * mm});
            skLineSegment(sketch, "E4703", {"start": v(-75.86, -94.61) * mm, "end": v(-74.56, -95.64) * mm});
            skLineSegment(sketch, "E4704", {"start": v(-74.56, -95.64) * mm, "end": v(-74.46, -95.62) * mm});
            skLineSegment(sketch, "E4705", {"start": v(-74.46, -95.62) * mm, "end": v(-74.33, -95.54) * mm});
            skLineSegment(sketch, "E4706", {"start": v(-74.33, -95.54) * mm, "end": v(-74.2, -95.47) * mm});
            skLineSegment(sketch, "E4707", {"start": v(-74.2, -95.47) * mm, "end": v(-74.08, -95.4) * mm});
            skLineSegment(sketch, "E4708", {"start": v(-74.08, -95.4) * mm, "end": v(-73.95, -95.32) * mm});
            skLineSegment(sketch, "E4709", {"start": v(-73.95, -95.32) * mm, "end": v(-73.82, -95.25) * mm});
            skLineSegment(sketch, "E4710", {"start": v(-73.82, -95.25) * mm, "end": v(-73.7, -95.17) * mm});
            skLineSegment(sketch, "E4711", {"start": v(-73.7, -95.17) * mm, "end": v(-73.58, -95.1) * mm});
            skLineSegment(sketch, "E4712", {"start": v(-73.58, -95.1) * mm, "end": v(-73.33, -94.96) * mm});
            skLineSegment(sketch, "E4713", {"start": v(-73.33, -94.96) * mm, "end": v(-73.22, -94.88) * mm});
            skLineSegment(sketch, "E4714", {"start": v(-73.22, -94.88) * mm, "end": v(-73.1, -94.81) * mm});
            skLineSegment(sketch, "E4715", {"start": v(-73.1, -94.81) * mm, "end": v(-72.98, -94.74) * mm});
            skLineSegment(sketch, "E4716", {"start": v(-72.98, -94.74) * mm, "end": v(-72.86, -94.67) * mm});
            skLineSegment(sketch, "E4717", {"start": v(-72.86, -94.67) * mm, "end": v(-72.75, -94.6) * mm});
            skLineSegment(sketch, "E4718", {"start": v(-72.75, -94.6) * mm, "end": v(-72.64, -94.53) * mm});
            skLineSegment(sketch, "E4719", {"start": v(-72.64, -94.53) * mm, "end": v(-72.52, -94.45) * mm});
            skLineSegment(sketch, "E4720", {"start": v(-72.52, -94.45) * mm, "end": v(-72.41, -94.38) * mm});
            skLineSegment(sketch, "E4721", {"start": v(-72.41, -94.38) * mm, "end": v(-72.2, -94.24) * mm});
            skLineSegment(sketch, "E4722", {"start": v(-72.2, -94.24) * mm, "end": v(-72.09, -94.17) * mm});
            skLineSegment(sketch, "E4723", {"start": v(-72.09, -94.17) * mm, "end": v(-71.98, -94.1) * mm});
            skLineSegment(sketch, "E4724", {"start": v(-71.98, -94.1) * mm, "end": v(-71.88, -94.03) * mm});
            skLineSegment(sketch, "E4725", {"start": v(-71.88, -94.03) * mm, "end": v(-71.67, -93.9) * mm});
            skLineSegment(sketch, "E4726", {"start": v(-71.67, -93.9) * mm, "end": v(-71.57, -93.83) * mm});
            skLineSegment(sketch, "E4727", {"start": v(-71.57, -93.83) * mm, "end": v(-71.47, -93.76) * mm});
            skLineSegment(sketch, "E4728", {"start": v(-71.47, -93.76) * mm, "end": v(-71.37, -93.7) * mm});
            skLineSegment(sketch, "E4729", {"start": v(-71.37, -93.7) * mm, "end": v(-71.28, -93.63) * mm});
            skLineSegment(sketch, "E4730", {"start": v(-71.28, -93.63) * mm, "end": v(-71.18, -93.56) * mm});
            skLineSegment(sketch, "E4731", {"start": v(-71.18, -93.56) * mm, "end": v(-71.08, -93.5) * mm});
            skLineSegment(sketch, "E4732", {"start": v(-71.08, -93.5) * mm, "end": v(-71, -93.43) * mm});
            skLineSegment(sketch, "E4733", {"start": v(-71, -93.43) * mm, "end": v(-70.9, -93.36) * mm});
            skLineSegment(sketch, "E4734", {"start": v(-70.9, -93.36) * mm, "end": v(-70.8, -93.3) * mm});
            skLineSegment(sketch, "E4735", {"start": v(-70.8, -93.3) * mm, "end": v(-70.63, -93.17) * mm});
            skLineSegment(sketch, "E4736", {"start": v(-70.63, -93.17) * mm, "end": v(-70.54, -93.1) * mm});
            skLineSegment(sketch, "E4737", {"start": v(-70.54, -93.1) * mm, "end": v(-70.45, -93.04) * mm});
            skLineSegment(sketch, "E4738", {"start": v(-70.45, -93.04) * mm, "end": v(-69.58, -93.47) * mm});
            skLineSegment(sketch, "E4739", {"start": v(-69.58, -93.47) * mm, "end": v(-68.91, -94.18) * mm});
            skLineSegment(sketch, "E4740", {"start": v(-68.91, -94.18) * mm, "end": v(-68.95, -94.29) * mm});
            skLineSegment(sketch, "E4741", {"start": v(-68.95, -94.29) * mm, "end": v(-69.02, -94.5) * mm});
            skLineSegment(sketch, "E4742", {"start": v(-69.02, -94.5) * mm, "end": v(-69.06, -94.6) * mm});
            skLineSegment(sketch, "E4743", {"start": v(-69.06, -94.6) * mm, "end": v(-69.1, -94.7) * mm});
            skLineSegment(sketch, "E4744", {"start": v(-69.1, -94.7) * mm, "end": v(-69.13, -94.81) * mm});
            skLineSegment(sketch, "E4745", {"start": v(-69.13, -94.81) * mm, "end": v(-69.17, -94.92) * mm});
            skLineSegment(sketch, "E4746", {"start": v(-69.17, -94.92) * mm, "end": v(-69.2, -95.03) * mm});
            skLineSegment(sketch, "E4747", {"start": v(-69.2, -95.03) * mm, "end": v(-69.24, -95.14) * mm});
            skLineSegment(sketch, "E4748", {"start": v(-69.24, -95.14) * mm, "end": v(-69.28, -95.26) * mm});
            skLineSegment(sketch, "E4749", {"start": v(-69.28, -95.26) * mm, "end": v(-69.31, -95.37) * mm});
            skLineSegment(sketch, "E4750", {"start": v(-69.31, -95.37) * mm, "end": v(-69.35, -95.48) * mm});
            skLineSegment(sketch, "E4751", {"start": v(-69.35, -95.48) * mm, "end": v(-69.39, -95.6) * mm});
            skLineSegment(sketch, "E4752", {"start": v(-69.39, -95.6) * mm, "end": v(-69.42, -95.72) * mm});
            skLineSegment(sketch, "E4753", {"start": v(-69.42, -95.72) * mm, "end": v(-69.46, -95.84) * mm});
            skLineSegment(sketch, "E4754", {"start": v(-69.46, -95.84) * mm, "end": v(-69.5, -95.96) * mm});
            skLineSegment(sketch, "E4755", {"start": v(-69.5, -95.96) * mm, "end": v(-69.53, -96.08) * mm});
            skLineSegment(sketch, "E4756", {"start": v(-69.53, -96.08) * mm, "end": v(-69.57, -96.2) * mm});
            skLineSegment(sketch, "E4757", {"start": v(-69.57, -96.2) * mm, "end": v(-69.6, -96.32) * mm});
            skLineSegment(sketch, "E4758", {"start": v(-69.6, -96.32) * mm, "end": v(-69.64, -96.45) * mm});
            skLineSegment(sketch, "E4759", {"start": v(-69.64, -96.45) * mm, "end": v(-69.67, -96.58) * mm});
            skLineSegment(sketch, "E4760", {"start": v(-69.67, -96.58) * mm, "end": v(-69.75, -96.83) * mm});
            skLineSegment(sketch, "E4761", {"start": v(-69.75, -96.83) * mm, "end": v(-69.78, -96.96) * mm});
            skLineSegment(sketch, "E4762", {"start": v(-69.78, -96.96) * mm, "end": v(-69.82, -97.1) * mm});
            skLineSegment(sketch, "E4763", {"start": v(-69.82, -97.1) * mm, "end": v(-69.85, -97.23) * mm});
            skLineSegment(sketch, "E4764", {"start": v(-69.85, -97.23) * mm, "end": v(-69.89, -97.36) * mm});
            skLineSegment(sketch, "E4765", {"start": v(-69.89, -97.36) * mm, "end": v(-69.92, -97.5) * mm});
            skLineSegment(sketch, "E4766", {"start": v(-69.92, -97.5) * mm, "end": v(-69.96, -97.63) * mm});
            skLineSegment(sketch, "E4767", {"start": v(-69.96, -97.63) * mm, "end": v(-70, -97.77) * mm});
            skLineSegment(sketch, "E4768", {"start": v(-70, -97.77) * mm, "end": v(-70.06, -98.05) * mm});
            skLineSegment(sketch, "E4769", {"start": v(-70.06, -98.05) * mm, "end": v(-70.1, -98.19) * mm});
            skLineSegment(sketch, "E4770", {"start": v(-70.1, -98.19) * mm, "end": v(-70.13, -98.33) * mm});
            skLineSegment(sketch, "E4771", {"start": v(-70.13, -98.33) * mm, "end": v(-70.16, -98.47) * mm});
            skLineSegment(sketch, "E4772", {"start": v(-70.16, -98.47) * mm, "end": v(-70.2, -98.62) * mm});
            skLineSegment(sketch, "E4773", {"start": v(-70.2, -98.62) * mm, "end": v(-70.23, -98.77) * mm});
            skLineSegment(sketch, "E4774", {"start": v(-70.23, -98.77) * mm, "end": v(-70.23, -98.86) * mm});
            skLineSegment(sketch, "E4775", {"start": v(-70.23, -98.86) * mm, "end": v(-68.87, -99.81) * mm});
            skLineSegment(sketch, "E4776", {"start": v(-68.87, -99.81) * mm, "end": v(-68.78, -99.78) * mm});
            skLineSegment(sketch, "E4777", {"start": v(-68.78, -99.78) * mm, "end": v(-68.65, -99.7) * mm});
            skLineSegment(sketch, "E4778", {"start": v(-68.65, -99.7) * mm, "end": v(-68.53, -99.62) * mm});
            skLineSegment(sketch, "E4779", {"start": v(-68.53, -99.62) * mm, "end": v(-68.4, -99.54) * mm});
            skLineSegment(sketch, "E4780", {"start": v(-68.4, -99.54) * mm, "end": v(-68.28, -99.46) * mm});
            skLineSegment(sketch, "E4781", {"start": v(-68.28, -99.46) * mm, "end": v(-68.16, -99.38) * mm});
            skLineSegment(sketch, "E4782", {"start": v(-68.16, -99.38) * mm, "end": v(-68.04, -99.3) * mm});
            skLineSegment(sketch, "E4783", {"start": v(-68.04, -99.3) * mm, "end": v(-67.92, -99.22) * mm});
            skLineSegment(sketch, "E4784", {"start": v(-67.92, -99.22) * mm, "end": v(-67.8, -99.14) * mm});
            skLineSegment(sketch, "E4785", {"start": v(-67.8, -99.14) * mm, "end": v(-67.69, -99.06) * mm});
            skLineSegment(sketch, "E4786", {"start": v(-67.69, -99.06) * mm, "end": v(-67.57, -98.98) * mm});
            skLineSegment(sketch, "E4787", {"start": v(-67.57, -98.98) * mm, "end": v(-67.35, -98.82) * mm});
            skLineSegment(sketch, "E4788", {"start": v(-67.35, -98.82) * mm, "end": v(-67.24, -98.74) * mm});
            skLineSegment(sketch, "E4789", {"start": v(-67.24, -98.74) * mm, "end": v(-67.13, -98.67) * mm});
            skLineSegment(sketch, "E4790", {"start": v(-67.13, -98.67) * mm, "end": v(-67.02, -98.59) * mm});
            skLineSegment(sketch, "E4791", {"start": v(-67.02, -98.59) * mm, "end": v(-66.91, -98.51) * mm});
            skLineSegment(sketch, "E4792", {"start": v(-66.91, -98.51) * mm, "end": v(-66.8, -98.43) * mm});
            skLineSegment(sketch, "E4793", {"start": v(-66.8, -98.43) * mm, "end": v(-66.7, -98.36) * mm});
            skLineSegment(sketch, "E4794", {"start": v(-66.7, -98.36) * mm, "end": v(-66.5, -98.2) * mm});
            skLineSegment(sketch, "E4795", {"start": v(-66.5, -98.2) * mm, "end": v(-66.3, -98.05) * mm});
            skLineSegment(sketch, "E4796", {"start": v(-66.3, -98.05) * mm, "end": v(-66.2, -97.98) * mm});
            skLineSegment(sketch, "E4797", {"start": v(-66.2, -97.98) * mm, "end": v(-66, -97.83) * mm});
            skLineSegment(sketch, "E4798", {"start": v(-66, -97.83) * mm, "end": v(-65.8, -97.68) * mm});
            skLineSegment(sketch, "E4799", {"start": v(-65.8, -97.68) * mm, "end": v(-65.71, -97.61) * mm});
            skLineSegment(sketch, "E4800", {"start": v(-65.71, -97.61) * mm, "end": v(-65.62, -97.54) * mm});
            skLineSegment(sketch, "E4801", {"start": v(-65.62, -97.54) * mm, "end": v(-65.53, -97.47) * mm});
            skLineSegment(sketch, "E4802", {"start": v(-65.53, -97.47) * mm, "end": v(-65.44, -97.4) * mm});
            skLineSegment(sketch, "E4803", {"start": v(-65.44, -97.4) * mm, "end": v(-65.35, -97.33) * mm});
            skLineSegment(sketch, "E4804", {"start": v(-65.35, -97.33) * mm, "end": v(-65.26, -97.26) * mm});
            skLineSegment(sketch, "E4805", {"start": v(-65.26, -97.26) * mm, "end": v(-65.18, -97.18) * mm});
            skLineSegment(sketch, "E4806", {"start": v(-65.18, -97.18) * mm, "end": v(-65.1, -97.11) * mm});
            skLineSegment(sketch, "E4807", {"start": v(-65.1, -97.11) * mm, "end": v(-65, -97.05) * mm});
            skLineSegment(sketch, "E4808", {"start": v(-65, -97.05) * mm, "end": v(-64.92, -96.98) * mm});
            skLineSegment(sketch, "E4809", {"start": v(-64.92, -96.98) * mm, "end": v(-64.03, -97.36) * mm});
            skLineSegment(sketch, "E4810", {"start": v(-64.03, -97.36) * mm, "end": v(-63.32, -98.03) * mm});
            skLineSegment(sketch, "E4811", {"start": v(-63.32, -98.03) * mm, "end": v(-63.35, -98.13) * mm});
            skLineSegment(sketch, "E4812", {"start": v(-63.35, -98.13) * mm, "end": v(-63.38, -98.24) * mm});
            skLineSegment(sketch, "E4813", {"start": v(-63.38, -98.24) * mm, "end": v(-63.41, -98.35) * mm});
            skLineSegment(sketch, "E4814", {"start": v(-63.41, -98.35) * mm, "end": v(-63.44, -98.45) * mm});
            skLineSegment(sketch, "E4815", {"start": v(-63.44, -98.45) * mm, "end": v(-63.47, -98.56) * mm});
            skLineSegment(sketch, "E4816", {"start": v(-63.47, -98.56) * mm, "end": v(-63.53, -98.78) * mm});
            skLineSegment(sketch, "E4817", {"start": v(-63.53, -98.78) * mm, "end": v(-63.56, -98.9) * mm});
            skLineSegment(sketch, "E4818", {"start": v(-63.56, -98.9) * mm, "end": v(-63.62, -99.12) * mm});
            skLineSegment(sketch, "E4819", {"start": v(-63.62, -99.12) * mm, "end": v(-63.65, -99.24) * mm});
            skLineSegment(sketch, "E4820", {"start": v(-63.65, -99.24) * mm, "end": v(-63.68, -99.36) * mm});
            skLineSegment(sketch, "E4821", {"start": v(-63.68, -99.36) * mm, "end": v(-63.74, -99.6) * mm});
            skLineSegment(sketch, "E4822", {"start": v(-63.74, -99.6) * mm, "end": v(-63.77, -99.71) * mm});
            skLineSegment(sketch, "E4823", {"start": v(-63.77, -99.71) * mm, "end": v(-63.8, -99.83) * mm});
            skLineSegment(sketch, "E4824", {"start": v(-63.8, -99.83) * mm, "end": v(-63.86, -100.08) * mm});
            skLineSegment(sketch, "E4825", {"start": v(-63.86, -100.08) * mm, "end": v(-63.88, -100.2) * mm});
            skLineSegment(sketch, "E4826", {"start": v(-63.88, -100.2) * mm, "end": v(-63.91, -100.33) * mm});
            skLineSegment(sketch, "E4827", {"start": v(-63.91, -100.33) * mm, "end": v(-63.94, -100.46) * mm});
            skLineSegment(sketch, "E4828", {"start": v(-63.94, -100.46) * mm, "end": v(-63.97, -100.6) * mm});
            skLineSegment(sketch, "E4829", {"start": v(-63.97, -100.6) * mm, "end": v(-64, -100.72) * mm});
            skLineSegment(sketch, "E4830", {"start": v(-64, -100.72) * mm, "end": v(-64.03, -100.86) * mm});
            skLineSegment(sketch, "E4831", {"start": v(-64.03, -100.86) * mm, "end": v(-64.05, -100.99) * mm});
            skLineSegment(sketch, "E4832", {"start": v(-64.05, -100.99) * mm, "end": v(-64.1, -101.26) * mm});
            skLineSegment(sketch, "E4833", {"start": v(-64.1, -101.26) * mm, "end": v(-64.14, -101.4) * mm});
            skLineSegment(sketch, "E4834", {"start": v(-64.14, -101.4) * mm, "end": v(-64.16, -101.53) * mm});
            skLineSegment(sketch, "E4835", {"start": v(-64.16, -101.53) * mm, "end": v(-64.19, -101.67) * mm});
            skLineSegment(sketch, "E4836", {"start": v(-64.19, -101.67) * mm, "end": v(-64.22, -101.81) * mm});
            skLineSegment(sketch, "E4837", {"start": v(-64.22, -101.81) * mm, "end": v(-64.24, -101.95) * mm});
            skLineSegment(sketch, "E4838", {"start": v(-64.24, -101.95) * mm, "end": v(-64.27, -102.1) * mm});
            skLineSegment(sketch, "E4839", {"start": v(-64.27, -102.1) * mm, "end": v(-64.3, -102.24) * mm});
            skLineSegment(sketch, "E4840", {"start": v(-64.3, -102.24) * mm, "end": v(-64.32, -102.39) * mm});
            skLineSegment(sketch, "E4841", {"start": v(-64.32, -102.39) * mm, "end": v(-64.34, -102.53) * mm});
            skLineSegment(sketch, "E4842", {"start": v(-64.34, -102.53) * mm, "end": v(-64.37, -102.68) * mm});
            skLineSegment(sketch, "E4843", {"start": v(-64.37, -102.68) * mm, "end": v(-64.36, -102.78) * mm});
            skLineSegment(sketch, "E4844", {"start": v(-64.36, -102.78) * mm, "end": v(-62.95, -103.65) * mm});
            skLineSegment(sketch, "E4845", {"start": v(-62.95, -103.65) * mm, "end": v(-62.86, -103.61) * mm});
            skLineSegment(sketch, "E4846", {"start": v(-62.86, -103.61) * mm, "end": v(-62.74, -103.53) * mm});
            skLineSegment(sketch, "E4847", {"start": v(-62.74, -103.53) * mm, "end": v(-62.62, -103.44) * mm});
            skLineSegment(sketch, "E4848", {"start": v(-62.62, -103.44) * mm, "end": v(-62.5, -103.35) * mm});
            skLineSegment(sketch, "E4849", {"start": v(-62.5, -103.35) * mm, "end": v(-62.38, -103.26) * mm});
            skLineSegment(sketch, "E4850", {"start": v(-62.38, -103.26) * mm, "end": v(-62.27, -103.17) * mm});
            skLineSegment(sketch, "E4851", {"start": v(-62.27, -103.17) * mm, "end": v(-62.04, -103) * mm});
            skLineSegment(sketch, "E4852", {"start": v(-62.04, -103) * mm, "end": v(-61.93, -102.91) * mm});
            skLineSegment(sketch, "E4853", {"start": v(-61.93, -102.91) * mm, "end": v(-61.81, -102.83) * mm});
            skLineSegment(sketch, "E4854", {"start": v(-61.81, -102.83) * mm, "end": v(-61.7, -102.74) * mm});
            skLineSegment(sketch, "E4855", {"start": v(-61.7, -102.74) * mm, "end": v(-61.6, -102.66) * mm});
            skLineSegment(sketch, "E4856", {"start": v(-61.6, -102.66) * mm, "end": v(-61.49, -102.57) * mm});
            skLineSegment(sketch, "E4857", {"start": v(-61.49, -102.57) * mm, "end": v(-61.28, -102.4) * mm});
            skLineSegment(sketch, "E4858", {"start": v(-61.28, -102.4) * mm, "end": v(-61.17, -102.32) * mm});
            skLineSegment(sketch, "E4859", {"start": v(-61.17, -102.32) * mm, "end": v(-61.07, -102.24) * mm});
            skLineSegment(sketch, "E4860", {"start": v(-61.07, -102.24) * mm, "end": v(-60.97, -102.15) * mm});
            skLineSegment(sketch, "E4861", {"start": v(-60.97, -102.15) * mm, "end": v(-60.87, -102.07) * mm});
            skLineSegment(sketch, "E4862", {"start": v(-60.87, -102.07) * mm, "end": v(-60.77, -101.99) * mm});
            skLineSegment(sketch, "E4863", {"start": v(-60.77, -101.99) * mm, "end": v(-60.67, -101.9) * mm});
            skLineSegment(sketch, "E4864", {"start": v(-60.67, -101.9) * mm, "end": v(-60.48, -101.74) * mm});
            skLineSegment(sketch, "E4865", {"start": v(-60.48, -101.74) * mm, "end": v(-60.38, -101.66) * mm});
            skLineSegment(sketch, "E4866", {"start": v(-60.38, -101.66) * mm, "end": v(-60.29, -101.58) * mm});
            skLineSegment(sketch, "E4867", {"start": v(-60.29, -101.58) * mm, "end": v(-60.2, -101.5) * mm});
            skLineSegment(sketch, "E4868", {"start": v(-60.2, -101.5) * mm, "end": v(-60.1, -101.42) * mm});
            skLineSegment(sketch, "E4869", {"start": v(-60.1, -101.42) * mm, "end": v(-59.93, -101.27) * mm});
            skLineSegment(sketch, "E4870", {"start": v(-59.93, -101.27) * mm, "end": v(-59.84, -101.2) * mm});
            skLineSegment(sketch, "E4871", {"start": v(-59.84, -101.2) * mm, "end": v(-59.75, -101.11) * mm});
            skLineSegment(sketch, "E4872", {"start": v(-59.75, -101.11) * mm, "end": v(-59.66, -101.04) * mm});
            skLineSegment(sketch, "E4873", {"start": v(-59.66, -101.04) * mm, "end": v(-59.5, -100.88) * mm});
            skLineSegment(sketch, "E4874", {"start": v(-59.5, -100.88) * mm, "end": v(-59.33, -100.74) * mm});
            skLineSegment(sketch, "E4875", {"start": v(-59.33, -100.74) * mm, "end": v(-59.25, -100.66) * mm});
            skLineSegment(sketch, "E4876", {"start": v(-59.25, -100.66) * mm, "end": v(-59.17, -100.59) * mm});
            skLineSegment(sketch, "E4877", {"start": v(-59.17, -100.59) * mm, "end": v(-58.26, -100.92) * mm});
            skLineSegment(sketch, "E4878", {"start": v(-58.26, -100.92) * mm, "end": v(-57.51, -101.55) * mm});
            skLineSegment(sketch, "E4879", {"start": v(-57.51, -101.55) * mm, "end": v(-57.54, -101.65) * mm});
            skLineSegment(sketch, "E4880", {"start": v(-57.54, -101.65) * mm, "end": v(-57.56, -101.76) * mm});
            skLineSegment(sketch, "E4881", {"start": v(-57.56, -101.76) * mm, "end": v(-57.59, -101.87) * mm});
            skLineSegment(sketch, "E4882", {"start": v(-57.59, -101.87) * mm, "end": v(-57.6, -101.97) * mm});
            skLineSegment(sketch, "E4883", {"start": v(-57.6, -101.97) * mm, "end": v(-57.63, -102.09) * mm});
            skLineSegment(sketch, "E4884", {"start": v(-57.63, -102.09) * mm, "end": v(-57.66, -102.2) * mm});
            skLineSegment(sketch, "E4885", {"start": v(-57.66, -102.2) * mm, "end": v(-57.68, -102.3) * mm});
            skLineSegment(sketch, "E4886", {"start": v(-57.68, -102.3) * mm, "end": v(-57.7, -102.42) * mm});
            skLineSegment(sketch, "E4887", {"start": v(-57.7, -102.42) * mm, "end": v(-57.73, -102.54) * mm});
            skLineSegment(sketch, "E4888", {"start": v(-57.73, -102.54) * mm, "end": v(-57.75, -102.65) * mm});
            skLineSegment(sketch, "E4889", {"start": v(-57.75, -102.65) * mm, "end": v(-57.77, -102.77) * mm});
            skLineSegment(sketch, "E4890", {"start": v(-57.77, -102.77) * mm, "end": v(-57.8, -102.89) * mm});
            skLineSegment(sketch, "E4891", {"start": v(-57.8, -102.89) * mm, "end": v(-57.82, -103) * mm});
            skLineSegment(sketch, "E4892", {"start": v(-57.82, -103) * mm, "end": v(-57.84, -103.13) * mm});
            skLineSegment(sketch, "E4893", {"start": v(-57.84, -103.13) * mm, "end": v(-57.86, -103.25) * mm});
            skLineSegment(sketch, "E4894", {"start": v(-57.86, -103.25) * mm, "end": v(-57.9, -103.5) * mm});
            skLineSegment(sketch, "E4895", {"start": v(-57.9, -103.5) * mm, "end": v(-57.93, -103.63) * mm});
            skLineSegment(sketch, "E4896", {"start": v(-57.93, -103.63) * mm, "end": v(-57.95, -103.75) * mm});
            skLineSegment(sketch, "E4897", {"start": v(-57.95, -103.75) * mm, "end": v(-57.97, -103.88) * mm});
            skLineSegment(sketch, "E4898", {"start": v(-57.97, -103.88) * mm, "end": v(-58, -104.01) * mm});
            skLineSegment(sketch, "E4899", {"start": v(-58, -104.01) * mm, "end": v(-58.01, -104.14) * mm});
            skLineSegment(sketch, "E4900", {"start": v(-58.01, -104.14) * mm, "end": v(-58.05, -104.4) * mm});
            skLineSegment(sketch, "E4901", {"start": v(-58.05, -104.4) * mm, "end": v(-58.1, -104.68) * mm});
            skLineSegment(sketch, "E4902", {"start": v(-58.1, -104.68) * mm, "end": v(-58.11, -104.81) * mm});
            skLineSegment(sketch, "E4903", {"start": v(-58.11, -104.81) * mm, "end": v(-58.13, -104.95) * mm});
            skLineSegment(sketch, "E4904", {"start": v(-58.13, -104.95) * mm, "end": v(-58.15, -105.1) * mm});
            skLineSegment(sketch, "E4905", {"start": v(-58.15, -105.1) * mm, "end": v(-58.17, -105.23) * mm});
            skLineSegment(sketch, "E4906", {"start": v(-58.17, -105.23) * mm, "end": v(-58.19, -105.37) * mm});
            skLineSegment(sketch, "E4907", {"start": v(-58.19, -105.37) * mm, "end": v(-58.22, -105.66) * mm});
            skLineSegment(sketch, "E4908", {"start": v(-58.22, -105.66) * mm, "end": v(-58.24, -105.8) * mm});
            skLineSegment(sketch, "E4909", {"start": v(-58.24, -105.8) * mm, "end": v(-58.26, -105.95) * mm});
            skLineSegment(sketch, "E4910", {"start": v(-58.26, -105.95) * mm, "end": v(-58.27, -106.1) * mm});
            skLineSegment(sketch, "E4911", {"start": v(-58.27, -106.1) * mm, "end": v(-58.3, -106.25) * mm});
            skLineSegment(sketch, "E4912", {"start": v(-58.3, -106.25) * mm, "end": v(-58.28, -106.35) * mm});
            skLineSegment(sketch, "E4913", {"start": v(-58.28, -106.35) * mm, "end": v(-56.82, -107.13) * mm});
            skLineSegment(sketch, "E4914", {"start": v(-56.82, -107.13) * mm, "end": v(-56.73, -107.1) * mm});
            skLineSegment(sketch, "E4915", {"start": v(-56.73, -107.1) * mm, "end": v(-56.61, -107) * mm});
            skLineSegment(sketch, "E4916", {"start": v(-56.61, -107) * mm, "end": v(-56.5, -106.9) * mm});
            skLineSegment(sketch, "E4917", {"start": v(-56.5, -106.9) * mm, "end": v(-56.39, -106.8) * mm});
            skLineSegment(sketch, "E4918", {"start": v(-56.39, -106.8) * mm, "end": v(-56.27, -106.71) * mm});
            skLineSegment(sketch, "E4919", {"start": v(-56.27, -106.71) * mm, "end": v(-56.16, -106.62) * mm});
            skLineSegment(sketch, "E4920", {"start": v(-56.16, -106.62) * mm, "end": v(-55.94, -106.43) * mm});
            skLineSegment(sketch, "E4921", {"start": v(-55.94, -106.43) * mm, "end": v(-55.84, -106.34) * mm});
            skLineSegment(sketch, "E4922", {"start": v(-55.84, -106.34) * mm, "end": v(-55.73, -106.25) * mm});
            skLineSegment(sketch, "E4923", {"start": v(-55.73, -106.25) * mm, "end": v(-55.63, -106.15) * mm});
            skLineSegment(sketch, "E4924", {"start": v(-55.63, -106.15) * mm, "end": v(-55.52, -106.06) * mm});
            skLineSegment(sketch, "E4925", {"start": v(-55.52, -106.06) * mm, "end": v(-55.32, -105.88) * mm});
            skLineSegment(sketch, "E4926", {"start": v(-55.32, -105.88) * mm, "end": v(-55.22, -105.8) * mm});
            skLineSegment(sketch, "E4927", {"start": v(-55.22, -105.8) * mm, "end": v(-55.02, -105.61) * mm});
            skLineSegment(sketch, "E4928", {"start": v(-55.02, -105.61) * mm, "end": v(-54.92, -105.52) * mm});
            skLineSegment(sketch, "E4929", {"start": v(-54.92, -105.52) * mm, "end": v(-54.73, -105.35) * mm});
            skLineSegment(sketch, "E4930", {"start": v(-54.73, -105.35) * mm, "end": v(-54.64, -105.26) * mm});
            skLineSegment(sketch, "E4931", {"start": v(-54.64, -105.26) * mm, "end": v(-54.55, -105.17) * mm});
            skLineSegment(sketch, "E4932", {"start": v(-54.55, -105.17) * mm, "end": v(-54.46, -105.09) * mm});
            skLineSegment(sketch, "E4933", {"start": v(-54.46, -105.09) * mm, "end": v(-54.28, -104.92) * mm});
            skLineSegment(sketch, "E4934", {"start": v(-54.28, -104.92) * mm, "end": v(-54.2, -104.83) * mm});
            skLineSegment(sketch, "E4935", {"start": v(-54.2, -104.83) * mm, "end": v(-54.1, -104.75) * mm});
            skLineSegment(sketch, "E4936", {"start": v(-54.1, -104.75) * mm, "end": v(-54.02, -104.66) * mm});
            skLineSegment(sketch, "E4937", {"start": v(-54.02, -104.66) * mm, "end": v(-53.94, -104.58) * mm});
            skLineSegment(sketch, "E4938", {"start": v(-53.94, -104.58) * mm, "end": v(-53.85, -104.5) * mm});
            skLineSegment(sketch, "E4939", {"start": v(-53.85, -104.5) * mm, "end": v(-53.69, -104.34) * mm});
            skLineSegment(sketch, "E4940", {"start": v(-53.69, -104.34) * mm, "end": v(-53.6, -104.25) * mm});
            skLineSegment(sketch, "E4941", {"start": v(-53.6, -104.25) * mm, "end": v(-53.45, -104.1) * mm});
            skLineSegment(sketch, "E4942", {"start": v(-53.45, -104.1) * mm, "end": v(-53.38, -104.02) * mm});
            skLineSegment(sketch, "E4943", {"start": v(-53.38, -104.02) * mm, "end": v(-53.3, -103.94) * mm});
            skLineSegment(sketch, "E4944", {"start": v(-53.3, -103.94) * mm, "end": v(-53.23, -103.86) * mm});
            skLineSegment(sketch, "E4945", {"start": v(-53.23, -103.86) * mm, "end": v(-52.3, -104.14) * mm});
            skLineSegment(sketch, "E4946", {"start": v(-52.3, -104.14) * mm, "end": v(-51.51, -104.72) * mm});
            skLineSegment(sketch, "E4947", {"start": v(-51.51, -104.72) * mm, "end": v(-51.53, -104.83) * mm});
            skLineSegment(sketch, "E4948", {"start": v(-51.53, -104.83) * mm, "end": v(-51.55, -104.93) * mm});
            skLineSegment(sketch, "E4949", {"start": v(-51.55, -104.93) * mm, "end": v(-51.56, -105.04) * mm});
            skLineSegment(sketch, "E4950", {"start": v(-51.56, -105.04) * mm, "end": v(-51.58, -105.15) * mm});
            skLineSegment(sketch, "E4951", {"start": v(-51.58, -105.15) * mm, "end": v(-51.6, -105.26) * mm});
            skLineSegment(sketch, "E4952", {"start": v(-51.6, -105.26) * mm, "end": v(-51.62, -105.38) * mm});
            skLineSegment(sketch, "E4953", {"start": v(-51.62, -105.38) * mm, "end": v(-51.63, -105.49) * mm});
            skLineSegment(sketch, "E4954", {"start": v(-51.63, -105.49) * mm, "end": v(-51.67, -105.72) * mm});
            skLineSegment(sketch, "E4955", {"start": v(-51.67, -105.72) * mm, "end": v(-51.68, -105.84) * mm});
            skLineSegment(sketch, "E4956", {"start": v(-51.68, -105.84) * mm, "end": v(-51.7, -105.96) * mm});
            skLineSegment(sketch, "E4957", {"start": v(-51.7, -105.96) * mm, "end": v(-51.72, -106.08) * mm});
            skLineSegment(sketch, "E4958", {"start": v(-51.72, -106.08) * mm, "end": v(-51.75, -106.32) * mm});
            skLineSegment(sketch, "E4959", {"start": v(-51.75, -106.32) * mm, "end": v(-51.78, -106.57) * mm});
            skLineSegment(sketch, "E4960", {"start": v(-51.78, -106.57) * mm, "end": v(-51.8, -106.7) * mm});
            skLineSegment(sketch, "E4961", {"start": v(-51.8, -106.7) * mm, "end": v(-51.83, -107.08) * mm});
            skLineSegment(sketch, "E4962", {"start": v(-51.83, -107.08) * mm, "end": v(-51.85, -107.2) * mm});
            skLineSegment(sketch, "E4963", {"start": v(-51.85, -107.2) * mm, "end": v(-51.86, -107.34) * mm});
            skLineSegment(sketch, "E4964", {"start": v(-51.86, -107.34) * mm, "end": v(-51.87, -107.47) * mm});
            skLineSegment(sketch, "E4965", {"start": v(-51.87, -107.47) * mm, "end": v(-51.9, -107.74) * mm});
            skLineSegment(sketch, "E4966", {"start": v(-51.9, -107.74) * mm, "end": v(-51.9, -107.88) * mm});
            skLineSegment(sketch, "E4967", {"start": v(-51.9, -107.88) * mm, "end": v(-51.92, -108.02) * mm});
            skLineSegment(sketch, "E4968", {"start": v(-51.92, -108.02) * mm, "end": v(-51.93, -108.16) * mm});
            skLineSegment(sketch, "E4969", {"start": v(-51.93, -108.16) * mm, "end": v(-51.94, -108.3) * mm});
            skLineSegment(sketch, "E4970", {"start": v(-51.94, -108.3) * mm, "end": v(-51.95, -108.44) * mm});
            skLineSegment(sketch, "E4971", {"start": v(-51.95, -108.44) * mm, "end": v(-51.97, -108.72) * mm});
            skLineSegment(sketch, "E4972", {"start": v(-51.97, -108.72) * mm, "end": v(-51.98, -108.87) * mm});
            skLineSegment(sketch, "E4973", {"start": v(-51.98, -108.87) * mm, "end": v(-51.99, -109.01) * mm});
            skLineSegment(sketch, "E4974", {"start": v(-51.99, -109.01) * mm, "end": v(-52, -109.16) * mm});
            skLineSegment(sketch, "E4975", {"start": v(-52, -109.16) * mm, "end": v(-52, -109.31) * mm});
            skLineSegment(sketch, "E4976", {"start": v(-52, -109.31) * mm, "end": v(-52.01, -109.46) * mm});
            skLineSegment(sketch, "E4977", {"start": v(-52.01, -109.46) * mm, "end": v(-52, -109.56) * mm});
            skLineSegment(sketch, "E4978", {"start": v(-52, -109.56) * mm, "end": v(-50.49, -110.26) * mm});
            skLineSegment(sketch, "E4979", {"start": v(-50.49, -110.26) * mm, "end": v(-50.4, -110.2) * mm});
            skLineSegment(sketch, "E4980", {"start": v(-50.4, -110.2) * mm, "end": v(-50.19, -110) * mm});
            skLineSegment(sketch, "E4981", {"start": v(-50.19, -110) * mm, "end": v(-50.08, -109.9) * mm});
            skLineSegment(sketch, "E4982", {"start": v(-50.08, -109.9) * mm, "end": v(-49.97, -109.8) * mm});
            skLineSegment(sketch, "E4983", {"start": v(-49.97, -109.8) * mm, "end": v(-49.76, -109.6) * mm});
            skLineSegment(sketch, "E4984", {"start": v(-49.76, -109.6) * mm, "end": v(-49.66, -109.5) * mm});
            skLineSegment(sketch, "E4985", {"start": v(-49.66, -109.5) * mm, "end": v(-49.56, -109.4) * mm});
            skLineSegment(sketch, "E4986", {"start": v(-49.56, -109.4) * mm, "end": v(-49.46, -109.3) * mm});
            skLineSegment(sketch, "E4987", {"start": v(-49.46, -109.3) * mm, "end": v(-49.36, -109.2) * mm});
            skLineSegment(sketch, "E4988", {"start": v(-49.36, -109.2) * mm, "end": v(-49.26, -109.11) * mm});
            skLineSegment(sketch, "E4989", {"start": v(-49.26, -109.11) * mm, "end": v(-49.16, -109.02) * mm});
            skLineSegment(sketch, "E4990", {"start": v(-49.16, -109.02) * mm, "end": v(-49.07, -108.92) * mm});
            skLineSegment(sketch, "E4991", {"start": v(-49.07, -108.92) * mm, "end": v(-48.97, -108.82) * mm});
            skLineSegment(sketch, "E4992", {"start": v(-48.97, -108.82) * mm, "end": v(-48.88, -108.73) * mm});
            skLineSegment(sketch, "E4993", {"start": v(-48.88, -108.73) * mm, "end": v(-48.7, -108.54) * mm});
            skLineSegment(sketch, "E4994", {"start": v(-48.7, -108.54) * mm, "end": v(-48.6, -108.45) * mm});
            skLineSegment(sketch, "E4995", {"start": v(-48.6, -108.45) * mm, "end": v(-48.52, -108.35) * mm});
            skLineSegment(sketch, "E4996", {"start": v(-48.52, -108.35) * mm, "end": v(-48.43, -108.26) * mm});
            skLineSegment(sketch, "E4997", {"start": v(-48.43, -108.26) * mm, "end": v(-48.34, -108.17) * mm});
            skLineSegment(sketch, "E4998", {"start": v(-48.34, -108.17) * mm, "end": v(-48.17, -107.99) * mm});
            skLineSegment(sketch, "E4999", {"start": v(-48.17, -107.99) * mm, "end": v(-48.09, -107.9) * mm});
            skLineSegment(sketch, "E5000", {"start": v(-48.09, -107.9) * mm, "end": v(-48, -107.8) * mm});
            skLineSegment(sketch, "E5001", {"start": v(-48, -107.8) * mm, "end": v(-47.92, -107.72) * mm});
            skLineSegment(sketch, "E5002", {"start": v(-47.92, -107.72) * mm, "end": v(-47.84, -107.63) * mm});
            skLineSegment(sketch, "E5003", {"start": v(-47.84, -107.63) * mm, "end": v(-47.76, -107.54) * mm});
            skLineSegment(sketch, "E5004", {"start": v(-47.76, -107.54) * mm, "end": v(-47.69, -107.45) * mm});
            skLineSegment(sketch, "E5005", {"start": v(-47.69, -107.45) * mm, "end": v(-47.6, -107.37) * mm});
            skLineSegment(sketch, "E5006", {"start": v(-47.6, -107.37) * mm, "end": v(-47.46, -107.2) * mm});
            skLineSegment(sketch, "E5007", {"start": v(-47.46, -107.2) * mm, "end": v(-47.38, -107.11) * mm});
            skLineSegment(sketch, "E5008", {"start": v(-47.38, -107.11) * mm, "end": v(-47.3, -107.03) * mm});
            skLineSegment(sketch, "E5009", {"start": v(-47.3, -107.03) * mm, "end": v(-47.24, -106.94) * mm});
            skLineSegment(sketch, "E5010", {"start": v(-47.24, -106.94) * mm, "end": v(-47.1, -106.78) * mm});
            skLineSegment(sketch, "E5011", {"start": v(-47.1, -106.78) * mm, "end": v(-46.15, -107) * mm});
            skLineSegment(sketch, "E5012", {"start": v(-46.15, -107) * mm, "end": v(-45.34, -107.54) * mm});
            skLineSegment(sketch, "E5013", {"start": v(-45.34, -107.54) * mm, "end": v(-45.35, -107.64) * mm});
            skLineSegment(sketch, "E5014", {"start": v(-45.35, -107.64) * mm, "end": v(-45.36, -107.75) * mm});
            skLineSegment(sketch, "E5015", {"start": v(-45.36, -107.75) * mm, "end": v(-45.37, -107.86) * mm});
            skLineSegment(sketch, "E5016", {"start": v(-45.37, -107.86) * mm, "end": v(-45.38, -107.97) * mm});
            skLineSegment(sketch, "E5017", {"start": v(-45.38, -107.97) * mm, "end": v(-45.4, -108.09) * mm});
            skLineSegment(sketch, "E5018", {"start": v(-45.4, -108.09) * mm, "end": v(-45.41, -108.31) * mm});
            skLineSegment(sketch, "E5019", {"start": v(-45.41, -108.31) * mm, "end": v(-45.42, -108.43) * mm});
            skLineSegment(sketch, "E5020", {"start": v(-45.42, -108.43) * mm, "end": v(-45.43, -108.55) * mm});
            skLineSegment(sketch, "E5021", {"start": v(-45.43, -108.55) * mm, "end": v(-45.44, -108.66) * mm});
            skLineSegment(sketch, "E5022", {"start": v(-45.44, -108.66) * mm, "end": v(-45.45, -108.78) * mm});
            skLineSegment(sketch, "E5023", {"start": v(-45.45, -108.78) * mm, "end": v(-45.46, -108.9) * mm});
            skLineSegment(sketch, "E5024", {"start": v(-45.46, -108.9) * mm, "end": v(-45.47, -109.02) * mm});
            skLineSegment(sketch, "E5025", {"start": v(-45.47, -109.02) * mm, "end": v(-45.48, -109.15) * mm});
            skLineSegment(sketch, "E5026", {"start": v(-45.48, -109.15) * mm, "end": v(-45.49, -109.27) * mm});
            skLineSegment(sketch, "E5027", {"start": v(-45.49, -109.27) * mm, "end": v(-45.5, -109.4) * mm});
            skLineSegment(sketch, "E5028", {"start": v(-45.5, -109.4) * mm, "end": v(-45.5, -109.65) * mm});
            skLineSegment(sketch, "E5029", {"start": v(-45.5, -109.65) * mm, "end": v(-45.52, -109.9) * mm});
            skLineSegment(sketch, "E5030", {"start": v(-45.52, -109.9) * mm, "end": v(-45.52, -110.04) * mm});
            skLineSegment(sketch, "E5031", {"start": v(-45.52, -110.04) * mm, "end": v(-45.53, -110.17) * mm});
            skLineSegment(sketch, "E5032", {"start": v(-45.53, -110.17) * mm, "end": v(-45.53, -110.3) * mm});
            skLineSegment(sketch, "E5033", {"start": v(-45.53, -110.3) * mm, "end": v(-45.54, -110.44) * mm});
            skLineSegment(sketch, "E5034", {"start": v(-45.54, -110.44) * mm, "end": v(-45.54, -110.58) * mm});
            skLineSegment(sketch, "E5035", {"start": v(-45.54, -110.58) * mm, "end": v(-45.55, -110.71) * mm});
            skLineSegment(sketch, "E5036", {"start": v(-45.55, -110.71) * mm, "end": v(-45.55, -110.85) * mm});
            skLineSegment(sketch, "E5037", {"start": v(-45.55, -110.85) * mm, "end": v(-45.55, -111) * mm});
            skLineSegment(sketch, "E5038", {"start": v(-45.55, -111) * mm, "end": v(-45.56, -111.13) * mm});
            skLineSegment(sketch, "E5039", {"start": v(-45.56, -111.13) * mm, "end": v(-45.56, -111.27) * mm});
            skLineSegment(sketch, "E5040", {"start": v(-45.56, -111.27) * mm, "end": v(-45.56, -111.56) * mm});
            skLineSegment(sketch, "E5041", {"start": v(-45.56, -111.56) * mm, "end": v(-45.56, -111.7) * mm});
            skLineSegment(sketch, "E5042", {"start": v(-45.56, -111.7) * mm, "end": v(-45.56, -112) * mm});
            skLineSegment(sketch, "E5043", {"start": v(-45.56, -112) * mm, "end": v(-45.56, -112.15) * mm});
            skLineSegment(sketch, "E5044", {"start": v(-45.56, -112.15) * mm, "end": v(-45.56, -112.3) * mm});
            skLineSegment(sketch, "E5045", {"start": v(-45.56, -112.3) * mm, "end": v(-45.54, -112.4) * mm});
            skLineSegment(sketch, "E5046", {"start": v(-45.54, -112.4) * mm, "end": v(-44, -113) * mm});
            skLineSegment(sketch, "E5047", {"start": v(-44, -113) * mm, "end": v(-43.91, -112.96) * mm});
            skLineSegment(sketch, "E5048", {"start": v(-43.91, -112.96) * mm, "end": v(-43.8, -112.85) * mm});
            skLineSegment(sketch, "E5049", {"start": v(-43.8, -112.85) * mm, "end": v(-43.6, -112.63) * mm});
            skLineSegment(sketch, "E5050", {"start": v(-43.6, -112.63) * mm, "end": v(-43.5, -112.52) * mm});
            skLineSegment(sketch, "E5051", {"start": v(-43.5, -112.52) * mm, "end": v(-43.4, -112.42) * mm});
            skLineSegment(sketch, "E5052", {"start": v(-43.4, -112.42) * mm, "end": v(-43.3, -112.31) * mm});
            skLineSegment(sketch, "E5053", {"start": v(-43.3, -112.31) * mm, "end": v(-43.2, -112.2) * mm});
            skLineSegment(sketch, "E5054", {"start": v(-43.2, -112.2) * mm, "end": v(-43.11, -112.1) * mm});
            skLineSegment(sketch, "E5055", {"start": v(-43.11, -112.1) * mm, "end": v(-43.02, -112) * mm});
            skLineSegment(sketch, "E5056", {"start": v(-43.02, -112) * mm, "end": v(-42.93, -111.9) * mm});
            skLineSegment(sketch, "E5057", {"start": v(-42.93, -111.9) * mm, "end": v(-42.83, -111.8) * mm});
            skLineSegment(sketch, "E5058", {"start": v(-42.83, -111.8) * mm, "end": v(-42.74, -111.69) * mm});
            skLineSegment(sketch, "E5059", {"start": v(-42.74, -111.69) * mm, "end": v(-42.65, -111.59) * mm});
            skLineSegment(sketch, "E5060", {"start": v(-42.65, -111.59) * mm, "end": v(-42.56, -111.49) * mm});
            skLineSegment(sketch, "E5061", {"start": v(-42.56, -111.49) * mm, "end": v(-42.48, -111.39) * mm});
            skLineSegment(sketch, "E5062", {"start": v(-42.48, -111.39) * mm, "end": v(-42.39, -111.29) * mm});
            skLineSegment(sketch, "E5063", {"start": v(-42.39, -111.29) * mm, "end": v(-42.3, -111.19) * mm});
            skLineSegment(sketch, "E5064", {"start": v(-42.3, -111.19) * mm, "end": v(-42.22, -111.09) * mm});
            skLineSegment(sketch, "E5065", {"start": v(-42.22, -111.09) * mm, "end": v(-42.13, -110.99) * mm});
            skLineSegment(sketch, "E5066", {"start": v(-42.13, -110.99) * mm, "end": v(-42.05, -110.9) * mm});
            skLineSegment(sketch, "E5067", {"start": v(-42.05, -110.9) * mm, "end": v(-41.97, -110.8) * mm});
            skLineSegment(sketch, "E5068", {"start": v(-41.97, -110.8) * mm, "end": v(-41.9, -110.7) * mm});
            skLineSegment(sketch, "E5069", {"start": v(-41.9, -110.7) * mm, "end": v(-41.81, -110.6) * mm});
            skLineSegment(sketch, "E5070", {"start": v(-41.81, -110.6) * mm, "end": v(-41.73, -110.5) * mm});
            skLineSegment(sketch, "E5071", {"start": v(-41.73, -110.5) * mm, "end": v(-41.66, -110.41) * mm});
            skLineSegment(sketch, "E5072", {"start": v(-41.66, -110.41) * mm, "end": v(-41.58, -110.32) * mm});
            skLineSegment(sketch, "E5073", {"start": v(-41.58, -110.32) * mm, "end": v(-41.5, -110.23) * mm});
            skLineSegment(sketch, "E5074", {"start": v(-41.5, -110.23) * mm, "end": v(-41.36, -110.04) * mm});
            skLineSegment(sketch, "E5075", {"start": v(-41.36, -110.04) * mm, "end": v(-41.28, -109.95) * mm});
            skLineSegment(sketch, "E5076", {"start": v(-41.28, -109.95) * mm, "end": v(-41.14, -109.77) * mm});
            skLineSegment(sketch, "E5077", {"start": v(-41.14, -109.77) * mm, "end": v(-41.08, -109.68) * mm});
            skLineSegment(sketch, "E5078", {"start": v(-41.08, -109.68) * mm, "end": v(-41, -109.6) * mm});
            skLineSegment(sketch, "E5079", {"start": v(-41, -109.6) * mm, "end": v(-40.87, -109.42) * mm});
            skLineSegment(sketch, "E5080", {"start": v(-40.87, -109.42) * mm, "end": v(-40.8, -109.33) * mm});
            skLineSegment(sketch, "E5081", {"start": v(-40.8, -109.33) * mm, "end": v(-39.85, -109.5) * mm});
            skLineSegment(sketch, "E5082", {"start": v(-39.85, -109.5) * mm, "end": v(-39, -110) * mm});
            skLineSegment(sketch, "E5083", {"start": v(-39, -110) * mm, "end": v(-39.01, -110.1) * mm});
            skLineSegment(sketch, "E5084", {"start": v(-39.01, -110.1) * mm, "end": v(-39.02, -110.2) * mm});
            skLineSegment(sketch, "E5085", {"start": v(-39.02, -110.2) * mm, "end": v(-39.02, -110.32) * mm});
            skLineSegment(sketch, "E5086", {"start": v(-39.02, -110.32) * mm, "end": v(-39.03, -110.43) * mm});
            skLineSegment(sketch, "E5087", {"start": v(-39.03, -110.43) * mm, "end": v(-39.03, -110.66) * mm});
            skLineSegment(sketch, "E5088", {"start": v(-39.03, -110.66) * mm, "end": v(-39.04, -110.77) * mm});
            skLineSegment(sketch, "E5089", {"start": v(-39.04, -110.77) * mm, "end": v(-39.04, -110.89) * mm});
            skLineSegment(sketch, "E5090", {"start": v(-39.04, -110.89) * mm, "end": v(-39.04, -111) * mm});
            skLineSegment(sketch, "E5091", {"start": v(-39.04, -111) * mm, "end": v(-39.05, -111.12) * mm});
            skLineSegment(sketch, "E5092", {"start": v(-39.05, -111.12) * mm, "end": v(-39.05, -111.24) * mm});
            skLineSegment(sketch, "E5093", {"start": v(-39.05, -111.24) * mm, "end": v(-39.05, -111.36) * mm});
            skLineSegment(sketch, "E5094", {"start": v(-39.05, -111.36) * mm, "end": v(-39.05, -111.6) * mm});
            skLineSegment(sketch, "E5095", {"start": v(-39.05, -111.6) * mm, "end": v(-39.05, -112.11) * mm});
            skLineSegment(sketch, "E5096", {"start": v(-39.05, -112.11) * mm, "end": v(-39.05, -112.24) * mm});
            skLineSegment(sketch, "E5097", {"start": v(-39.05, -112.24) * mm, "end": v(-39.05, -112.5) * mm});
            skLineSegment(sketch, "E5098", {"start": v(-39.05, -112.5) * mm, "end": v(-39.05, -112.63) * mm});
            skLineSegment(sketch, "E5099", {"start": v(-39.05, -112.63) * mm, "end": v(-39.04, -112.77) * mm});
            skLineSegment(sketch, "E5100", {"start": v(-39.04, -112.77) * mm, "end": v(-39.04, -112.9) * mm});
            skLineSegment(sketch, "E5101", {"start": v(-39.04, -112.9) * mm, "end": v(-39.04, -113.04) * mm});
            skLineSegment(sketch, "E5102", {"start": v(-39.04, -113.04) * mm, "end": v(-39.03, -113.31) * mm});
            skLineSegment(sketch, "E5103", {"start": v(-39.03, -113.31) * mm, "end": v(-39.02, -113.45) * mm});
            skLineSegment(sketch, "E5104", {"start": v(-39.02, -113.45) * mm, "end": v(-39.02, -113.6) * mm});
            skLineSegment(sketch, "E5105", {"start": v(-39.02, -113.6) * mm, "end": v(-39.01, -113.73) * mm});
            skLineSegment(sketch, "E5106", {"start": v(-39.01, -113.73) * mm, "end": v(-39, -113.88) * mm});
            skLineSegment(sketch, "E5107", {"start": v(-39, -113.88) * mm, "end": v(-39, -114.02) * mm});
            skLineSegment(sketch, "E5108", {"start": v(-39, -114.02) * mm, "end": v(-38.99, -114.17) * mm});
            skLineSegment(sketch, "E5109", {"start": v(-38.99, -114.17) * mm, "end": v(-38.98, -114.31) * mm});
            skLineSegment(sketch, "E5110", {"start": v(-38.98, -114.31) * mm, "end": v(-38.97, -114.46) * mm});
            skLineSegment(sketch, "E5111", {"start": v(-38.97, -114.46) * mm, "end": v(-38.96, -114.6) * mm});
            skLineSegment(sketch, "E5112", {"start": v(-38.96, -114.6) * mm, "end": v(-38.95, -114.76) * mm});
            skLineSegment(sketch, "E5113", {"start": v(-38.95, -114.76) * mm, "end": v(-38.92, -114.85) * mm});
            skLineSegment(sketch, "E5114", {"start": v(-38.92, -114.85) * mm, "end": v(-37.35, -115.37) * mm});
            skLineSegment(sketch, "E5115", {"start": v(-37.35, -115.37) * mm, "end": v(-37.27, -115.32) * mm});
            skLineSegment(sketch, "E5116", {"start": v(-37.27, -115.32) * mm, "end": v(-37.08, -115.09) * mm});
            skLineSegment(sketch, "E5117", {"start": v(-37.08, -115.09) * mm, "end": v(-36.98, -114.98) * mm});
            skLineSegment(sketch, "E5118", {"start": v(-36.98, -114.98) * mm, "end": v(-36.89, -114.86) * mm});
            skLineSegment(sketch, "E5119", {"start": v(-36.89, -114.86) * mm, "end": v(-36.7, -114.64) * mm});
            skLineSegment(sketch, "E5120", {"start": v(-36.7, -114.64) * mm, "end": v(-36.52, -114.42) * mm});
            skLineSegment(sketch, "E5121", {"start": v(-36.52, -114.42) * mm, "end": v(-36.35, -114.2) * mm});
            skLineSegment(sketch, "E5122", {"start": v(-36.35, -114.2) * mm, "end": v(-36.26, -114.1) * mm});
            skLineSegment(sketch, "E5123", {"start": v(-36.26, -114.1) * mm, "end": v(-36.18, -113.99) * mm});
            skLineSegment(sketch, "E5124", {"start": v(-36.18, -113.99) * mm, "end": v(-36.1, -113.88) * mm});
            skLineSegment(sketch, "E5125", {"start": v(-36.1, -113.88) * mm, "end": v(-35.93, -113.67) * mm});
            skLineSegment(sketch, "E5126", {"start": v(-35.93, -113.67) * mm, "end": v(-35.77, -113.46) * mm});
            skLineSegment(sketch, "E5127", {"start": v(-35.77, -113.46) * mm, "end": v(-35.69, -113.35) * mm});
            skLineSegment(sketch, "E5128", {"start": v(-35.69, -113.35) * mm, "end": v(-35.6, -113.25) * mm});
            skLineSegment(sketch, "E5129", {"start": v(-35.6, -113.25) * mm, "end": v(-35.53, -113.15) * mm});
            skLineSegment(sketch, "E5130", {"start": v(-35.53, -113.15) * mm, "end": v(-35.46, -113.05) * mm});
            skLineSegment(sketch, "E5131", {"start": v(-35.46, -113.05) * mm, "end": v(-35.38, -112.95) * mm});
            skLineSegment(sketch, "E5132", {"start": v(-35.38, -112.95) * mm, "end": v(-35.3, -112.85) * mm});
            skLineSegment(sketch, "E5133", {"start": v(-35.3, -112.85) * mm, "end": v(-35.24, -112.75) * mm});
            skLineSegment(sketch, "E5134", {"start": v(-35.24, -112.75) * mm, "end": v(-35.16, -112.65) * mm});
            skLineSegment(sketch, "E5135", {"start": v(-35.16, -112.65) * mm, "end": v(-35.1, -112.55) * mm});
            skLineSegment(sketch, "E5136", {"start": v(-35.1, -112.55) * mm, "end": v(-35.02, -112.45) * mm});
            skLineSegment(sketch, "E5137", {"start": v(-35.02, -112.45) * mm, "end": v(-34.89, -112.26) * mm});
            skLineSegment(sketch, "E5138", {"start": v(-34.89, -112.26) * mm, "end": v(-34.82, -112.17) * mm});
            skLineSegment(sketch, "E5139", {"start": v(-34.82, -112.17) * mm, "end": v(-34.7, -111.98) * mm});
            skLineSegment(sketch, "E5140", {"start": v(-34.7, -111.98) * mm, "end": v(-34.63, -111.89) * mm});
            skLineSegment(sketch, "E5141", {"start": v(-34.63, -111.89) * mm, "end": v(-34.57, -111.8) * mm});
            skLineSegment(sketch, "E5142", {"start": v(-34.57, -111.8) * mm, "end": v(-34.5, -111.7) * mm});
            skLineSegment(sketch, "E5143", {"start": v(-34.5, -111.7) * mm, "end": v(-34.44, -111.61) * mm});
            skLineSegment(sketch, "E5144", {"start": v(-34.44, -111.61) * mm, "end": v(-34.38, -111.52) * mm});
            skLineSegment(sketch, "E5145", {"start": v(-34.38, -111.52) * mm, "end": v(-33.41, -111.63) * mm});
            skLineSegment(sketch, "E5146", {"start": v(-33.41, -111.63) * mm, "end": v(-32.55, -112.07) * mm});
            skLineSegment(sketch, "E5147", {"start": v(-32.55, -112.07) * mm, "end": v(-32.54, -112.3) * mm});
            skLineSegment(sketch, "E5148", {"start": v(-32.54, -112.3) * mm, "end": v(-32.54, -112.51) * mm});
            skLineSegment(sketch, "E5149", {"start": v(-32.54, -112.51) * mm, "end": v(-32.54, -112.62) * mm});
            skLineSegment(sketch, "E5150", {"start": v(-32.54, -112.62) * mm, "end": v(-32.53, -112.85) * mm});
            skLineSegment(sketch, "E5151", {"start": v(-32.53, -112.85) * mm, "end": v(-32.53, -112.97) * mm});
            skLineSegment(sketch, "E5152", {"start": v(-32.53, -112.97) * mm, "end": v(-32.52, -113.09) * mm});
            skLineSegment(sketch, "E5153", {"start": v(-32.52, -113.09) * mm, "end": v(-32.52, -113.2) * mm});
            skLineSegment(sketch, "E5154", {"start": v(-32.52, -113.2) * mm, "end": v(-32.51, -113.32) * mm});
            skLineSegment(sketch, "E5155", {"start": v(-32.51, -113.32) * mm, "end": v(-32.5, -113.44) * mm});
            skLineSegment(sketch, "E5156", {"start": v(-32.5, -113.44) * mm, "end": v(-32.5, -113.69) * mm});
            skLineSegment(sketch, "E5157", {"start": v(-32.5, -113.69) * mm, "end": v(-32.5, -113.81) * mm});
            skLineSegment(sketch, "E5158", {"start": v(-32.5, -113.81) * mm, "end": v(-32.48, -113.94) * mm});
            skLineSegment(sketch, "E5159", {"start": v(-32.48, -113.94) * mm, "end": v(-32.48, -114.06) * mm});
            skLineSegment(sketch, "E5160", {"start": v(-32.48, -114.06) * mm, "end": v(-32.47, -114.2) * mm});
            skLineSegment(sketch, "E5161", {"start": v(-32.47, -114.2) * mm, "end": v(-32.46, -114.32) * mm});
            skLineSegment(sketch, "E5162", {"start": v(-32.46, -114.32) * mm, "end": v(-32.45, -114.45) * mm});
            skLineSegment(sketch, "E5163", {"start": v(-32.45, -114.45) * mm, "end": v(-32.44, -114.58) * mm});
            skLineSegment(sketch, "E5164", {"start": v(-32.44, -114.58) * mm, "end": v(-32.43, -114.71) * mm});
            skLineSegment(sketch, "E5165", {"start": v(-32.43, -114.71) * mm, "end": v(-32.41, -114.98) * mm});
            skLineSegment(sketch, "E5166", {"start": v(-32.41, -114.98) * mm, "end": v(-32.4, -115.12) * mm});
            skLineSegment(sketch, "E5167", {"start": v(-32.4, -115.12) * mm, "end": v(-32.39, -115.25) * mm});
            skLineSegment(sketch, "E5168", {"start": v(-32.39, -115.25) * mm, "end": v(-32.37, -115.4) * mm});
            skLineSegment(sketch, "E5169", {"start": v(-32.37, -115.4) * mm, "end": v(-32.36, -115.53) * mm});
            skLineSegment(sketch, "E5170", {"start": v(-32.36, -115.53) * mm, "end": v(-32.33, -115.81) * mm});
            skLineSegment(sketch, "E5171", {"start": v(-32.33, -115.81) * mm, "end": v(-32.32, -115.95) * mm});
            skLineSegment(sketch, "E5172", {"start": v(-32.32, -115.95) * mm, "end": v(-32.3, -116.1) * mm});
            skLineSegment(sketch, "E5173", {"start": v(-32.3, -116.1) * mm, "end": v(-32.29, -116.24) * mm});
            skLineSegment(sketch, "E5174", {"start": v(-32.29, -116.24) * mm, "end": v(-32.25, -116.53) * mm});
            skLineSegment(sketch, "E5175", {"start": v(-32.25, -116.53) * mm, "end": v(-32.24, -116.68) * mm});
            skLineSegment(sketch, "E5176", {"start": v(-32.24, -116.68) * mm, "end": v(-32.22, -116.83) * mm});
            skLineSegment(sketch, "E5177", {"start": v(-32.22, -116.83) * mm, "end": v(-32.18, -116.92) * mm});
            skLineSegment(sketch, "E5178", {"start": v(-32.18, -116.92) * mm, "end": v(-30.58, -117.35) * mm});
            skLineSegment(sketch, "E5179", {"start": v(-30.58, -117.35) * mm, "end": v(-30.5, -117.29) * mm});
            skLineSegment(sketch, "E5180", {"start": v(-30.5, -117.29) * mm, "end": v(-30.41, -117.17) * mm});
            skLineSegment(sketch, "E5181", {"start": v(-30.41, -117.17) * mm, "end": v(-30.32, -117.05) * mm});
            skLineSegment(sketch, "E5182", {"start": v(-30.32, -117.05) * mm, "end": v(-30.23, -116.93) * mm});
            skLineSegment(sketch, "E5183", {"start": v(-30.23, -116.93) * mm, "end": v(-30.15, -116.81) * mm});
            skLineSegment(sketch, "E5184", {"start": v(-30.15, -116.81) * mm, "end": v(-30.06, -116.7) * mm});
            skLineSegment(sketch, "E5185", {"start": v(-30.06, -116.7) * mm, "end": v(-29.98, -116.58) * mm});
            skLineSegment(sketch, "E5186", {"start": v(-29.98, -116.58) * mm, "end": v(-29.9, -116.46) * mm});
            skLineSegment(sketch, "E5187", {"start": v(-29.9, -116.46) * mm, "end": v(-29.8, -116.35) * mm});
            skLineSegment(sketch, "E5188", {"start": v(-29.8, -116.35) * mm, "end": v(-29.73, -116.23) * mm});
            skLineSegment(sketch, "E5189", {"start": v(-29.73, -116.23) * mm, "end": v(-29.65, -116.12) * mm});
            skLineSegment(sketch, "E5190", {"start": v(-29.65, -116.12) * mm, "end": v(-29.57, -116) * mm});
            skLineSegment(sketch, "E5191", {"start": v(-29.57, -116) * mm, "end": v(-29.49, -115.9) * mm});
            skLineSegment(sketch, "E5192", {"start": v(-29.49, -115.9) * mm, "end": v(-29.33, -115.67) * mm});
            skLineSegment(sketch, "E5193", {"start": v(-29.33, -115.67) * mm, "end": v(-29.26, -115.56) * mm});
            skLineSegment(sketch, "E5194", {"start": v(-29.26, -115.56) * mm, "end": v(-29.1, -115.35) * mm});
            skLineSegment(sketch, "E5195", {"start": v(-29.1, -115.35) * mm, "end": v(-28.96, -115.13) * mm});
            skLineSegment(sketch, "E5196", {"start": v(-28.96, -115.13) * mm, "end": v(-28.82, -114.92) * mm});
            skLineSegment(sketch, "E5197", {"start": v(-28.82, -114.92) * mm, "end": v(-28.76, -114.81) * mm});
            skLineSegment(sketch, "E5198", {"start": v(-28.76, -114.81) * mm, "end": v(-28.69, -114.7) * mm});
            skLineSegment(sketch, "E5199", {"start": v(-28.69, -114.7) * mm, "end": v(-28.62, -114.6) * mm});
            skLineSegment(sketch, "E5200", {"start": v(-28.62, -114.6) * mm, "end": v(-28.56, -114.5) * mm});
            skLineSegment(sketch, "E5201", {"start": v(-28.56, -114.5) * mm, "end": v(-28.5, -114.4) * mm});
            skLineSegment(sketch, "E5202", {"start": v(-28.5, -114.4) * mm, "end": v(-28.36, -114.2) * mm});
            skLineSegment(sketch, "E5203", {"start": v(-28.36, -114.2) * mm, "end": v(-28.3, -114.1) * mm});
            skLineSegment(sketch, "E5204", {"start": v(-28.3, -114.1) * mm, "end": v(-28.24, -114) * mm});
            skLineSegment(sketch, "E5205", {"start": v(-28.24, -114) * mm, "end": v(-28.18, -113.9) * mm});
            skLineSegment(sketch, "E5206", {"start": v(-28.18, -113.9) * mm, "end": v(-28.12, -113.8) * mm});
            skLineSegment(sketch, "E5207", {"start": v(-28.12, -113.8) * mm, "end": v(-28.06, -113.71) * mm});
            skLineSegment(sketch, "E5208", {"start": v(-28.06, -113.71) * mm, "end": v(-28, -113.62) * mm});
            skLineSegment(sketch, "E5209", {"start": v(-28, -113.62) * mm, "end": v(-27.95, -113.52) * mm});
            skLineSegment(sketch, "E5210", {"start": v(-27.95, -113.52) * mm, "end": v(-27.9, -113.43) * mm});
            skLineSegment(sketch, "E5211", {"start": v(-27.9, -113.43) * mm, "end": v(-27.84, -113.33) * mm});
            skLineSegment(sketch, "E5212", {"start": v(-27.84, -113.33) * mm, "end": v(-26.87, -113.39) * mm});
            skLineSegment(sketch, "E5213", {"start": v(-26.87, -113.39) * mm, "end": v(-25.97, -113.78) * mm});
            skLineSegment(sketch, "E5214", {"start": v(-25.97, -113.78) * mm, "end": v(-25.97, -113.88) * mm});
            skLineSegment(sketch, "E5215", {"start": v(-25.97, -113.88) * mm, "end": v(-25.96, -114) * mm});
            skLineSegment(sketch, "E5216", {"start": v(-25.96, -114) * mm, "end": v(-25.95, -114.1) * mm});
            skLineSegment(sketch, "E5217", {"start": v(-25.95, -114.1) * mm, "end": v(-25.94, -114.21) * mm});
            skLineSegment(sketch, "E5218", {"start": v(-25.94, -114.21) * mm, "end": v(-25.93, -114.33) * mm});
            skLineSegment(sketch, "E5219", {"start": v(-25.93, -114.33) * mm, "end": v(-25.92, -114.44) * mm});
            skLineSegment(sketch, "E5220", {"start": v(-25.92, -114.44) * mm, "end": v(-25.91, -114.55) * mm});
            skLineSegment(sketch, "E5221", {"start": v(-25.91, -114.55) * mm, "end": v(-25.9, -114.67) * mm});
            skLineSegment(sketch, "E5222", {"start": v(-25.9, -114.67) * mm, "end": v(-25.88, -114.9) * mm});
            skLineSegment(sketch, "E5223", {"start": v(-25.88, -114.9) * mm, "end": v(-25.87, -115.02) * mm});
            skLineSegment(sketch, "E5224", {"start": v(-25.87, -115.02) * mm, "end": v(-25.86, -115.14) * mm});
            skLineSegment(sketch, "E5225", {"start": v(-25.86, -115.14) * mm, "end": v(-25.85, -115.26) * mm});
            skLineSegment(sketch, "E5226", {"start": v(-25.85, -115.26) * mm, "end": v(-25.83, -115.39) * mm});
            skLineSegment(sketch, "E5227", {"start": v(-25.83, -115.39) * mm, "end": v(-25.82, -115.5) * mm});
            skLineSegment(sketch, "E5228", {"start": v(-25.82, -115.5) * mm, "end": v(-25.8, -115.63) * mm});
            skLineSegment(sketch, "E5229", {"start": v(-25.8, -115.63) * mm, "end": v(-25.79, -115.76) * mm});
            skLineSegment(sketch, "E5230", {"start": v(-25.79, -115.76) * mm, "end": v(-25.77, -115.89) * mm});
            skLineSegment(sketch, "E5231", {"start": v(-25.77, -115.89) * mm, "end": v(-25.74, -116.14) * mm});
            skLineSegment(sketch, "E5232", {"start": v(-25.74, -116.14) * mm, "end": v(-25.73, -116.27) * mm});
            skLineSegment(sketch, "E5233", {"start": v(-25.73, -116.27) * mm, "end": v(-25.7, -116.4) * mm});
            skLineSegment(sketch, "E5234", {"start": v(-25.7, -116.4) * mm, "end": v(-25.69, -116.54) * mm});
            skLineSegment(sketch, "E5235", {"start": v(-25.69, -116.54) * mm, "end": v(-25.65, -116.8) * mm});
            skLineSegment(sketch, "E5236", {"start": v(-25.65, -116.8) * mm, "end": v(-25.6, -117.08) * mm});
            skLineSegment(sketch, "E5237", {"start": v(-25.6, -117.08) * mm, "end": v(-25.59, -117.22) * mm});
            skLineSegment(sketch, "E5238", {"start": v(-25.59, -117.22) * mm, "end": v(-25.54, -117.5) * mm});
            skLineSegment(sketch, "E5239", {"start": v(-25.54, -117.5) * mm, "end": v(-25.5, -117.78) * mm});
            skLineSegment(sketch, "E5240", {"start": v(-25.5, -117.78) * mm, "end": v(-25.45, -118.06) * mm});
            skLineSegment(sketch, "E5241", {"start": v(-25.45, -118.06) * mm, "end": v(-25.4, -118.36) * mm});
            skLineSegment(sketch, "E5242", {"start": v(-25.4, -118.36) * mm, "end": v(-25.37, -118.5) * mm});
            skLineSegment(sketch, "E5243", {"start": v(-25.37, -118.5) * mm, "end": v(-25.33, -118.6) * mm});
            skLineSegment(sketch, "E5244", {"start": v(-25.33, -118.6) * mm, "end": v(-23.7, -118.93) * mm});
            skLineSegment(sketch, "E5245", {"start": v(-23.7, -118.93) * mm, "end": v(-23.63, -118.86) * mm});
            skLineSegment(sketch, "E5246", {"start": v(-23.63, -118.86) * mm, "end": v(-23.55, -118.74) * mm});
            skLineSegment(sketch, "E5247", {"start": v(-23.55, -118.74) * mm, "end": v(-23.47, -118.61) * mm});
            skLineSegment(sketch, "E5248", {"start": v(-23.47, -118.61) * mm, "end": v(-23.3, -118.37) * mm});
            skLineSegment(sketch, "E5249", {"start": v(-23.3, -118.37) * mm, "end": v(-23.22, -118.25) * mm});
            skLineSegment(sketch, "E5250", {"start": v(-23.22, -118.25) * mm, "end": v(-23.15, -118.13) * mm});
            skLineSegment(sketch, "E5251", {"start": v(-23.15, -118.13) * mm, "end": v(-23.07, -118) * mm});
            skLineSegment(sketch, "E5252", {"start": v(-23.07, -118) * mm, "end": v(-23, -117.89) * mm});
            skLineSegment(sketch, "E5253", {"start": v(-23, -117.89) * mm, "end": v(-22.84, -117.65) * mm});
            skLineSegment(sketch, "E5254", {"start": v(-22.84, -117.65) * mm, "end": v(-22.77, -117.53) * mm});
            skLineSegment(sketch, "E5255", {"start": v(-22.77, -117.53) * mm, "end": v(-22.7, -117.42) * mm});
            skLineSegment(sketch, "E5256", {"start": v(-22.7, -117.42) * mm, "end": v(-22.63, -117.3) * mm});
            skLineSegment(sketch, "E5257", {"start": v(-22.63, -117.3) * mm, "end": v(-22.56, -117.18) * mm});
            skLineSegment(sketch, "E5258", {"start": v(-22.56, -117.18) * mm, "end": v(-22.49, -117.07) * mm});
            skLineSegment(sketch, "E5259", {"start": v(-22.49, -117.07) * mm, "end": v(-22.35, -116.84) * mm});
            skLineSegment(sketch, "E5260", {"start": v(-22.35, -116.84) * mm, "end": v(-22.22, -116.62) * mm});
            skLineSegment(sketch, "E5261", {"start": v(-22.22, -116.62) * mm, "end": v(-22.1, -116.4) * mm});
            skLineSegment(sketch, "E5262", {"start": v(-22.1, -116.4) * mm, "end": v(-22.03, -116.3) * mm});
            skLineSegment(sketch, "E5263", {"start": v(-22.03, -116.3) * mm, "end": v(-21.9, -116.08) * mm});
            skLineSegment(sketch, "E5264", {"start": v(-21.9, -116.08) * mm, "end": v(-21.85, -115.97) * mm});
            skLineSegment(sketch, "E5265", {"start": v(-21.85, -115.97) * mm, "end": v(-21.73, -115.76) * mm});
            skLineSegment(sketch, "E5266", {"start": v(-21.73, -115.76) * mm, "end": v(-21.68, -115.66) * mm});
            skLineSegment(sketch, "E5267", {"start": v(-21.68, -115.66) * mm, "end": v(-21.62, -115.55) * mm});
            skLineSegment(sketch, "E5268", {"start": v(-21.62, -115.55) * mm, "end": v(-21.5, -115.35) * mm});
            skLineSegment(sketch, "E5269", {"start": v(-21.5, -115.35) * mm, "end": v(-21.46, -115.25) * mm});
            skLineSegment(sketch, "E5270", {"start": v(-21.46, -115.25) * mm, "end": v(-21.35, -115.05) * mm});
            skLineSegment(sketch, "E5271", {"start": v(-21.35, -115.05) * mm, "end": v(-21.3, -114.95) * mm});
            skLineSegment(sketch, "E5272", {"start": v(-21.3, -114.95) * mm, "end": v(-21.2, -114.76) * mm});
            skLineSegment(sketch, "E5273", {"start": v(-21.2, -114.76) * mm, "end": v(-20.23, -114.76) * mm});
            skLineSegment(sketch, "E5274", {"start": v(-20.23, -114.76) * mm, "end": v(-19.31, -115.1) * mm});
            skLineSegment(sketch, "E5275", {"start": v(-19.31, -115.1) * mm, "end": v(-19.3, -115.2) * mm});
            skLineSegment(sketch, "E5276", {"start": v(-19.3, -115.2) * mm, "end": v(-19.29, -115.3) * mm});
            skLineSegment(sketch, "E5277", {"start": v(-19.29, -115.3) * mm, "end": v(-19.26, -115.53) * mm});
            skLineSegment(sketch, "E5278", {"start": v(-19.26, -115.53) * mm, "end": v(-19.23, -115.75) * mm});
            skLineSegment(sketch, "E5279", {"start": v(-19.23, -115.75) * mm, "end": v(-19.2, -115.98) * mm});
            skLineSegment(sketch, "E5280", {"start": v(-19.2, -115.98) * mm, "end": v(-19.18, -116.1) * mm});
            skLineSegment(sketch, "E5281", {"start": v(-19.18, -116.1) * mm, "end": v(-19.16, -116.21) * mm});
            skLineSegment(sketch, "E5282", {"start": v(-19.16, -116.21) * mm, "end": v(-19.14, -116.33) * mm});
            skLineSegment(sketch, "E5283", {"start": v(-19.14, -116.33) * mm, "end": v(-19.12, -116.45) * mm});
            skLineSegment(sketch, "E5284", {"start": v(-19.12, -116.45) * mm, "end": v(-19.08, -116.7) * mm});
            skLineSegment(sketch, "E5285", {"start": v(-19.08, -116.7) * mm, "end": v(-19.04, -116.94) * mm});
            skLineSegment(sketch, "E5286", {"start": v(-19.04, -116.94) * mm, "end": v(-19.02, -117.06) * mm});
            skLineSegment(sketch, "E5287", {"start": v(-19.02, -117.06) * mm, "end": v(-19, -117.19) * mm});
            skLineSegment(sketch, "E5288", {"start": v(-19, -117.19) * mm, "end": v(-18.97, -117.32) * mm});
            skLineSegment(sketch, "E5289", {"start": v(-18.97, -117.32) * mm, "end": v(-18.95, -117.44) * mm});
            skLineSegment(sketch, "E5290", {"start": v(-18.95, -117.44) * mm, "end": v(-18.92, -117.57) * mm});
            skLineSegment(sketch, "E5291", {"start": v(-18.92, -117.57) * mm, "end": v(-18.9, -117.7) * mm});
            skLineSegment(sketch, "E5292", {"start": v(-18.9, -117.7) * mm, "end": v(-18.87, -117.83) * mm});
            skLineSegment(sketch, "E5293", {"start": v(-18.87, -117.83) * mm, "end": v(-18.84, -117.97) * mm});
            skLineSegment(sketch, "E5294", {"start": v(-18.84, -117.97) * mm, "end": v(-18.82, -118.1) * mm});
            skLineSegment(sketch, "E5295", {"start": v(-18.82, -118.1) * mm, "end": v(-18.79, -118.23) * mm});
            skLineSegment(sketch, "E5296", {"start": v(-18.79, -118.23) * mm, "end": v(-18.76, -118.37) * mm});
            skLineSegment(sketch, "E5297", {"start": v(-18.76, -118.37) * mm, "end": v(-18.73, -118.5) * mm});
            skLineSegment(sketch, "E5298", {"start": v(-18.73, -118.5) * mm, "end": v(-18.7, -118.64) * mm});
            skLineSegment(sketch, "E5299", {"start": v(-18.7, -118.64) * mm, "end": v(-18.67, -118.78) * mm});
            skLineSegment(sketch, "E5300", {"start": v(-18.67, -118.78) * mm, "end": v(-18.64, -118.92) * mm});
            skLineSegment(sketch, "E5301", {"start": v(-18.64, -118.92) * mm, "end": v(-18.6, -119.06) * mm});
            skLineSegment(sketch, "E5302", {"start": v(-18.6, -119.06) * mm, "end": v(-18.54, -119.34) * mm});
            skLineSegment(sketch, "E5303", {"start": v(-18.54, -119.34) * mm, "end": v(-18.5, -119.49) * mm});
            skLineSegment(sketch, "E5304", {"start": v(-18.5, -119.49) * mm, "end": v(-18.47, -119.63) * mm});
            skLineSegment(sketch, "E5305", {"start": v(-18.47, -119.63) * mm, "end": v(-18.44, -119.78) * mm});
            skLineSegment(sketch, "E5306", {"start": v(-18.44, -119.78) * mm, "end": v(-18.39, -119.86) * mm});
            skLineSegment(sketch, "E5307", {"start": v(-18.39, -119.86) * mm, "end": v(-16.75, -120.1) * mm});
            skLineSegment(sketch, "E5308", {"start": v(-16.75, -120.1) * mm, "end": v(-16.68, -120.04) * mm});
            skLineSegment(sketch, "E5309", {"start": v(-16.68, -120.04) * mm, "end": v(-16.6, -119.9) * mm});
            skLineSegment(sketch, "E5310", {"start": v(-16.6, -119.9) * mm, "end": v(-16.45, -119.65) * mm});
            skLineSegment(sketch, "E5311", {"start": v(-16.45, -119.65) * mm, "end": v(-16.38, -119.52) * mm});
            skLineSegment(sketch, "E5312", {"start": v(-16.38, -119.52) * mm, "end": v(-16.3, -119.4) * mm});
            skLineSegment(sketch, "E5313", {"start": v(-16.3, -119.4) * mm, "end": v(-16.24, -119.27) * mm});
            skLineSegment(sketch, "E5314", {"start": v(-16.24, -119.27) * mm, "end": v(-16.17, -119.15) * mm});
            skLineSegment(sketch, "E5315", {"start": v(-16.17, -119.15) * mm, "end": v(-16.03, -118.9) * mm});
            skLineSegment(sketch, "E5316", {"start": v(-16.03, -118.9) * mm, "end": v(-15.9, -118.66) * mm});
            skLineSegment(sketch, "E5317", {"start": v(-15.9, -118.66) * mm, "end": v(-15.83, -118.54) * mm});
            skLineSegment(sketch, "E5318", {"start": v(-15.83, -118.54) * mm, "end": v(-15.77, -118.42) * mm});
            skLineSegment(sketch, "E5319", {"start": v(-15.77, -118.42) * mm, "end": v(-15.7, -118.3) * mm});
            skLineSegment(sketch, "E5320", {"start": v(-15.7, -118.3) * mm, "end": v(-15.64, -118.18) * mm});
            skLineSegment(sketch, "E5321", {"start": v(-15.64, -118.18) * mm, "end": v(-15.58, -118.06) * mm});
            skLineSegment(sketch, "E5322", {"start": v(-15.58, -118.06) * mm, "end": v(-15.52, -117.94) * mm});
            skLineSegment(sketch, "E5323", {"start": v(-15.52, -117.94) * mm, "end": v(-15.46, -117.83) * mm});
            skLineSegment(sketch, "E5324", {"start": v(-15.46, -117.83) * mm, "end": v(-15.4, -117.71) * mm});
            skLineSegment(sketch, "E5325", {"start": v(-15.4, -117.71) * mm, "end": v(-15.34, -117.6) * mm});
            skLineSegment(sketch, "E5326", {"start": v(-15.34, -117.6) * mm, "end": v(-15.29, -117.49) * mm});
            skLineSegment(sketch, "E5327", {"start": v(-15.29, -117.49) * mm, "end": v(-15.23, -117.38) * mm});
            skLineSegment(sketch, "E5328", {"start": v(-15.23, -117.38) * mm, "end": v(-15.18, -117.26) * mm});
            skLineSegment(sketch, "E5329", {"start": v(-15.18, -117.26) * mm, "end": v(-15.12, -117.15) * mm});
            skLineSegment(sketch, "E5330", {"start": v(-15.12, -117.15) * mm, "end": v(-15.07, -117.05) * mm});
            skLineSegment(sketch, "E5331", {"start": v(-15.07, -117.05) * mm, "end": v(-15.02, -116.94) * mm});
            skLineSegment(sketch, "E5332", {"start": v(-15.02, -116.94) * mm, "end": v(-14.91, -116.72) * mm});
            skLineSegment(sketch, "E5333", {"start": v(-14.91, -116.72) * mm, "end": v(-14.87, -116.62) * mm});
            skLineSegment(sketch, "E5334", {"start": v(-14.87, -116.62) * mm, "end": v(-14.82, -116.51) * mm});
            skLineSegment(sketch, "E5335", {"start": v(-14.82, -116.51) * mm, "end": v(-14.77, -116.4) * mm});
            skLineSegment(sketch, "E5336", {"start": v(-14.77, -116.4) * mm, "end": v(-14.72, -116.3) * mm});
            skLineSegment(sketch, "E5337", {"start": v(-14.72, -116.3) * mm, "end": v(-14.67, -116.2) * mm});
            skLineSegment(sketch, "E5338", {"start": v(-14.67, -116.2) * mm, "end": v(-14.63, -116.1) * mm});
            skLineSegment(sketch, "E5339", {"start": v(-14.63, -116.1) * mm, "end": v(-14.58, -116) * mm});
            skLineSegment(sketch, "E5340", {"start": v(-14.58, -116) * mm, "end": v(-14.5, -115.8) * mm});
            skLineSegment(sketch, "E5341", {"start": v(-14.5, -115.8) * mm, "end": v(-13.52, -115.74) * mm});
            skLineSegment(sketch, "E5342", {"start": v(-13.52, -115.74) * mm, "end": v(-12.59, -116.02) * mm});
            skLineSegment(sketch, "E5343", {"start": v(-12.59, -116.02) * mm, "end": v(-12.55, -116.23) * mm});
            skLineSegment(sketch, "E5344", {"start": v(-12.55, -116.23) * mm, "end": v(-12.53, -116.34) * mm});
            skLineSegment(sketch, "E5345", {"start": v(-12.53, -116.34) * mm, "end": v(-12.5, -116.45) * mm});
            skLineSegment(sketch, "E5346", {"start": v(-12.5, -116.45) * mm, "end": v(-12.49, -116.56) * mm});
            skLineSegment(sketch, "E5347", {"start": v(-12.49, -116.56) * mm, "end": v(-12.46, -116.67) * mm});
            skLineSegment(sketch, "E5348", {"start": v(-12.46, -116.67) * mm, "end": v(-12.44, -116.79) * mm});
            skLineSegment(sketch, "E5349", {"start": v(-12.44, -116.79) * mm, "end": v(-12.42, -116.9) * mm});
            skLineSegment(sketch, "E5350", {"start": v(-12.42, -116.9) * mm, "end": v(-12.4, -117.02) * mm});
            skLineSegment(sketch, "E5351", {"start": v(-12.4, -117.02) * mm, "end": v(-12.37, -117.13) * mm});
            skLineSegment(sketch, "E5352", {"start": v(-12.37, -117.13) * mm, "end": v(-12.32, -117.37) * mm});
            skLineSegment(sketch, "E5353", {"start": v(-12.32, -117.37) * mm, "end": v(-12.29, -117.48) * mm});
            skLineSegment(sketch, "E5354", {"start": v(-12.29, -117.48) * mm, "end": v(-12.26, -117.6) * mm});
            skLineSegment(sketch, "E5355", {"start": v(-12.26, -117.6) * mm, "end": v(-12.23, -117.73) * mm});
            skLineSegment(sketch, "E5356", {"start": v(-12.23, -117.73) * mm, "end": v(-12.18, -117.97) * mm});
            skLineSegment(sketch, "E5357", {"start": v(-12.18, -117.97) * mm, "end": v(-12.15, -118.1) * mm});
            skLineSegment(sketch, "E5358", {"start": v(-12.15, -118.1) * mm, "end": v(-12.12, -118.22) * mm});
            skLineSegment(sketch, "E5359", {"start": v(-12.12, -118.22) * mm, "end": v(-12.05, -118.47) * mm});
            skLineSegment(sketch, "E5360", {"start": v(-12.05, -118.47) * mm, "end": v(-12.02, -118.6) * mm});
            skLineSegment(sketch, "E5361", {"start": v(-12.02, -118.6) * mm, "end": v(-11.99, -118.73) * mm});
            skLineSegment(sketch, "E5362", {"start": v(-11.99, -118.73) * mm, "end": v(-11.92, -119) * mm});
            skLineSegment(sketch, "E5363", {"start": v(-11.92, -119) * mm, "end": v(-11.88, -119.13) * mm});
            skLineSegment(sketch, "E5364", {"start": v(-11.88, -119.13) * mm, "end": v(-11.85, -119.26) * mm});
            skLineSegment(sketch, "E5365", {"start": v(-11.85, -119.26) * mm, "end": v(-11.8, -119.4) * mm});
            skLineSegment(sketch, "E5366", {"start": v(-11.8, -119.4) * mm, "end": v(-11.77, -119.53) * mm});
            skLineSegment(sketch, "E5367", {"start": v(-11.77, -119.53) * mm, "end": v(-11.73, -119.67) * mm});
            skLineSegment(sketch, "E5368", {"start": v(-11.73, -119.67) * mm, "end": v(-11.7, -119.8) * mm});
            skLineSegment(sketch, "E5369", {"start": v(-11.7, -119.8) * mm, "end": v(-11.65, -119.94) * mm});
            skLineSegment(sketch, "E5370", {"start": v(-11.65, -119.94) * mm, "end": v(-11.61, -120.08) * mm});
            skLineSegment(sketch, "E5371", {"start": v(-11.61, -120.08) * mm, "end": v(-11.57, -120.22) * mm});
            skLineSegment(sketch, "E5372", {"start": v(-11.57, -120.22) * mm, "end": v(-11.53, -120.36) * mm});
            skLineSegment(sketch, "E5373", {"start": v(-11.53, -120.36) * mm, "end": v(-11.48, -120.5) * mm});
            skLineSegment(sketch, "E5374", {"start": v(-11.48, -120.5) * mm, "end": v(-11.44, -120.65) * mm});
            skLineSegment(sketch, "E5375", {"start": v(-11.44, -120.65) * mm, "end": v(-11.39, -120.73) * mm});
            skLineSegment(sketch, "E5376", {"start": v(-11.39, -120.73) * mm, "end": v(-9.74, -120.88) * mm});
            skLineSegment(sketch, "E5377", {"start": v(-9.74, -120.88) * mm, "end": v(-9.67, -120.8) * mm});
            skLineSegment(sketch, "E5378", {"start": v(-9.67, -120.8) * mm, "end": v(-9.6, -120.67) * mm});
            skLineSegment(sketch, "E5379", {"start": v(-9.6, -120.67) * mm, "end": v(-9.54, -120.54) * mm});
            skLineSegment(sketch, "E5380", {"start": v(-9.54, -120.54) * mm, "end": v(-9.47, -120.4) * mm});
            skLineSegment(sketch, "E5381", {"start": v(-9.47, -120.4) * mm, "end": v(-9.4, -120.27) * mm});
            skLineSegment(sketch, "E5382", {"start": v(-9.4, -120.27) * mm, "end": v(-9.34, -120.14) * mm});
            skLineSegment(sketch, "E5383", {"start": v(-9.34, -120.14) * mm, "end": v(-9.28, -120.01) * mm});
            skLineSegment(sketch, "E5384", {"start": v(-9.28, -120.01) * mm, "end": v(-9.15, -119.76) * mm});
            skLineSegment(sketch, "E5385", {"start": v(-9.15, -119.76) * mm, "end": v(-9.1, -119.63) * mm});
            skLineSegment(sketch, "E5386", {"start": v(-9.1, -119.63) * mm, "end": v(-9.03, -119.5) * mm});
            skLineSegment(sketch, "E5387", {"start": v(-9.03, -119.5) * mm, "end": v(-8.97, -119.38) * mm});
            skLineSegment(sketch, "E5388", {"start": v(-8.97, -119.38) * mm, "end": v(-8.86, -119.13) * mm});
            skLineSegment(sketch, "E5389", {"start": v(-8.86, -119.13) * mm, "end": v(-8.8, -119.01) * mm});
            skLineSegment(sketch, "E5390", {"start": v(-8.8, -119.01) * mm, "end": v(-8.74, -118.89) * mm});
            skLineSegment(sketch, "E5391", {"start": v(-8.74, -118.89) * mm, "end": v(-8.58, -118.53) * mm});
            skLineSegment(sketch, "E5392", {"start": v(-8.58, -118.53) * mm, "end": v(-8.43, -118.18) * mm});
            skLineSegment(sketch, "E5393", {"start": v(-8.43, -118.18) * mm, "end": v(-8.38, -118.06) * mm});
            skLineSegment(sketch, "E5394", {"start": v(-8.38, -118.06) * mm, "end": v(-8.28, -117.83) * mm});
            skLineSegment(sketch, "E5395", {"start": v(-8.28, -117.83) * mm, "end": v(-8.24, -117.72) * mm});
            skLineSegment(sketch, "E5396", {"start": v(-8.24, -117.72) * mm, "end": v(-8.2, -117.61) * mm});
            skLineSegment(sketch, "E5397", {"start": v(-8.2, -117.61) * mm, "end": v(-8.15, -117.5) * mm});
            skLineSegment(sketch, "E5398", {"start": v(-8.15, -117.5) * mm, "end": v(-8.1, -117.4) * mm});
            skLineSegment(sketch, "E5399", {"start": v(-8.1, -117.4) * mm, "end": v(-8.06, -117.28) * mm});
            skLineSegment(sketch, "E5400", {"start": v(-8.06, -117.28) * mm, "end": v(-7.97, -117.07) * mm});
            skLineSegment(sketch, "E5401", {"start": v(-7.97, -117.07) * mm, "end": v(-7.93, -116.96) * mm});
            skLineSegment(sketch, "E5402", {"start": v(-7.93, -116.96) * mm, "end": v(-7.9, -116.86) * mm});
            skLineSegment(sketch, "E5403", {"start": v(-7.9, -116.86) * mm, "end": v(-7.81, -116.65) * mm});
            skLineSegment(sketch, "E5404", {"start": v(-7.81, -116.65) * mm, "end": v(-7.77, -116.55) * mm});
            skLineSegment(sketch, "E5405", {"start": v(-7.77, -116.55) * mm, "end": v(-7.74, -116.45) * mm});
            skLineSegment(sketch, "E5406", {"start": v(-7.74, -116.45) * mm, "end": v(-6.77, -116.33) * mm});
            skLineSegment(sketch, "E5407", {"start": v(-6.77, -116.33) * mm, "end": v(-5.82, -116.56) * mm});
            skLineSegment(sketch, "E5408", {"start": v(-5.82, -116.56) * mm, "end": v(-5.8, -116.66) * mm});
            skLineSegment(sketch, "E5409", {"start": v(-5.8, -116.66) * mm, "end": v(-5.77, -116.77) * mm});
            skLineSegment(sketch, "E5410", {"start": v(-5.77, -116.77) * mm, "end": v(-5.71, -116.98) * mm});
            skLineSegment(sketch, "E5411", {"start": v(-5.71, -116.98) * mm, "end": v(-5.69, -117.1) * mm});
            skLineSegment(sketch, "E5412", {"start": v(-5.69, -117.1) * mm, "end": v(-5.66, -117.2) * mm});
            skLineSegment(sketch, "E5413", {"start": v(-5.66, -117.2) * mm, "end": v(-5.63, -117.31) * mm});
            skLineSegment(sketch, "E5414", {"start": v(-5.63, -117.31) * mm, "end": v(-5.6, -117.43) * mm});
            skLineSegment(sketch, "E5415", {"start": v(-5.6, -117.43) * mm, "end": v(-5.57, -117.54) * mm});
            skLineSegment(sketch, "E5416", {"start": v(-5.57, -117.54) * mm, "end": v(-5.5, -117.77) * mm});
            skLineSegment(sketch, "E5417", {"start": v(-5.5, -117.77) * mm, "end": v(-5.44, -118) * mm});
            skLineSegment(sketch, "E5418", {"start": v(-5.44, -118) * mm, "end": v(-5.4, -118.12) * mm});
            skLineSegment(sketch, "E5419", {"start": v(-5.4, -118.12) * mm, "end": v(-5.37, -118.24) * mm});
            skLineSegment(sketch, "E5420", {"start": v(-5.37, -118.24) * mm, "end": v(-5.33, -118.36) * mm});
            skLineSegment(sketch, "E5421", {"start": v(-5.33, -118.36) * mm, "end": v(-5.3, -118.48) * mm});
            skLineSegment(sketch, "E5422", {"start": v(-5.3, -118.48) * mm, "end": v(-5.22, -118.72) * mm});
            skLineSegment(sketch, "E5423", {"start": v(-5.22, -118.72) * mm, "end": v(-5.18, -118.85) * mm});
            skLineSegment(sketch, "E5424", {"start": v(-5.18, -118.85) * mm, "end": v(-5.14, -118.97) * mm});
            skLineSegment(sketch, "E5425", {"start": v(-5.14, -118.97) * mm, "end": v(-5.1, -119.1) * mm});
            skLineSegment(sketch, "E5426", {"start": v(-5.1, -119.1) * mm, "end": v(-5.06, -119.23) * mm});
            skLineSegment(sketch, "E5427", {"start": v(-5.06, -119.23) * mm, "end": v(-5.02, -119.36) * mm});
            skLineSegment(sketch, "E5428", {"start": v(-5.02, -119.36) * mm, "end": v(-4.93, -119.62) * mm});
            skLineSegment(sketch, "E5429", {"start": v(-4.93, -119.62) * mm, "end": v(-4.9, -119.75) * mm});
            skLineSegment(sketch, "E5430", {"start": v(-4.9, -119.75) * mm, "end": v(-4.85, -119.88) * mm});
            skLineSegment(sketch, "E5431", {"start": v(-4.85, -119.88) * mm, "end": v(-4.75, -120.15) * mm});
            skLineSegment(sketch, "E5432", {"start": v(-4.75, -120.15) * mm, "end": v(-4.66, -120.42) * mm});
            skLineSegment(sketch, "E5433", {"start": v(-4.66, -120.42) * mm, "end": v(-4.6, -120.55) * mm});
            skLineSegment(sketch, "E5434", {"start": v(-4.6, -120.55) * mm, "end": v(-4.56, -120.7) * mm});
            skLineSegment(sketch, "E5435", {"start": v(-4.56, -120.7) * mm, "end": v(-4.5, -120.83) * mm});
            skLineSegment(sketch, "E5436", {"start": v(-4.5, -120.83) * mm, "end": v(-4.46, -120.97) * mm});
            skLineSegment(sketch, "E5437", {"start": v(-4.46, -120.97) * mm, "end": v(-4.4, -121.1) * mm});
            skLineSegment(sketch, "E5438", {"start": v(-4.4, -121.1) * mm, "end": v(-4.35, -121.19) * mm});
            skLineSegment(sketch, "E5439", {"start": v(-4.35, -121.19) * mm, "end": v(-2.7, -121.24) * mm});
            skLineSegment(sketch, "E5440", {"start": v(-2.7, -121.24) * mm, "end": v(-2.63, -121.16) * mm});
            skLineSegment(sketch, "E5441", {"start": v(-2.63, -121.16) * mm, "end": v(-2.57, -121.02) * mm});
            skLineSegment(sketch, "E5442", {"start": v(-2.57, -121.02) * mm, "end": v(-2.51, -120.89) * mm});
            skLineSegment(sketch, "E5443", {"start": v(-2.51, -120.89) * mm, "end": v(-2.4, -120.62) * mm});
            skLineSegment(sketch, "E5444", {"start": v(-2.4, -120.62) * mm, "end": v(-2.34, -120.48) * mm});
            skLineSegment(sketch, "E5445", {"start": v(-2.34, -120.48) * mm, "end": v(-2.28, -120.35) * mm});
            skLineSegment(sketch, "E5446", {"start": v(-2.28, -120.35) * mm, "end": v(-2.23, -120.22) * mm});
            skLineSegment(sketch, "E5447", {"start": v(-2.23, -120.22) * mm, "end": v(-2.17, -120.09) * mm});
            skLineSegment(sketch, "E5448", {"start": v(-2.17, -120.09) * mm, "end": v(-2.12, -119.96) * mm});
            skLineSegment(sketch, "E5449", {"start": v(-2.12, -119.96) * mm, "end": v(-2.07, -119.83) * mm});
            skLineSegment(sketch, "E5450", {"start": v(-2.07, -119.83) * mm, "end": v(-1.96, -119.57) * mm});
            skLineSegment(sketch, "E5451", {"start": v(-1.96, -119.57) * mm, "end": v(-1.87, -119.32) * mm});
            skLineSegment(sketch, "E5452", {"start": v(-1.87, -119.32) * mm, "end": v(-1.82, -119.2) * mm});
            skLineSegment(sketch, "E5453", {"start": v(-1.82, -119.2) * mm, "end": v(-1.77, -119.07) * mm});
            skLineSegment(sketch, "E5454", {"start": v(-1.77, -119.07) * mm, "end": v(-1.72, -118.95) * mm});
            skLineSegment(sketch, "E5455", {"start": v(-1.72, -118.95) * mm, "end": v(-1.63, -118.7) * mm});
            skLineSegment(sketch, "E5456", {"start": v(-1.63, -118.7) * mm, "end": v(-1.59, -118.59) * mm});
            skLineSegment(sketch, "E5457", {"start": v(-1.59, -118.59) * mm, "end": v(-1.54, -118.47) * mm});
            skLineSegment(sketch, "E5458", {"start": v(-1.54, -118.47) * mm, "end": v(-1.5, -118.35) * mm});
            skLineSegment(sketch, "E5459", {"start": v(-1.5, -118.35) * mm, "end": v(-1.46, -118.23) * mm});
            skLineSegment(sketch, "E5460", {"start": v(-1.46, -118.23) * mm, "end": v(-1.42, -118.12) * mm});
            skLineSegment(sketch, "E5461", {"start": v(-1.42, -118.12) * mm, "end": v(-1.34, -117.89) * mm});
            skLineSegment(sketch, "E5462", {"start": v(-1.34, -117.89) * mm, "end": v(-1.3, -117.78) * mm});
            skLineSegment(sketch, "E5463", {"start": v(-1.3, -117.78) * mm, "end": v(-1.26, -117.66) * mm});
            skLineSegment(sketch, "E5464", {"start": v(-1.26, -117.66) * mm, "end": v(-1.23, -117.55) * mm});
            skLineSegment(sketch, "E5465", {"start": v(-1.23, -117.55) * mm, "end": v(-1.19, -117.44) * mm});
            skLineSegment(sketch, "E5466", {"start": v(-1.19, -117.44) * mm, "end": v(-1.12, -117.22) * mm});
            skLineSegment(sketch, "E5467", {"start": v(-1.12, -117.22) * mm, "end": v(-1.08, -117.12) * mm});
            skLineSegment(sketch, "E5468", {"start": v(-1.08, -117.12) * mm, "end": v(-1.02, -116.9) * mm});
            skLineSegment(sketch, "E5469", {"start": v(-1.02, -116.9) * mm, "end": v(-0.98, -116.8) * mm});
            skLineSegment(sketch, "E5470", {"start": v(-0.98, -116.8) * mm, "end": v(-0.95, -116.7) * mm});
            skLineSegment(sketch, "E5471", {"start": v(-0.95, -116.7) * mm, "end": v(0, -116.53) * mm});
            skLineSegment(sketch, "E5472", {"start": v(0, -116.53) * mm, "end": v(0.97, -116.7) * mm});
            skLineSegment(sketch, "E5473", {"start": v(0.97, -116.7) * mm, "end": v(1.03, -116.9) * mm});
            skLineSegment(sketch, "E5474", {"start": v(1.03, -116.9) * mm, "end": v(1.06, -117.01) * mm});
            skLineSegment(sketch, "E5475", {"start": v(1.06, -117.01) * mm, "end": v(1.13, -117.22) * mm});
            skLineSegment(sketch, "E5476", {"start": v(1.13, -117.22) * mm, "end": v(1.17, -117.33) * mm});
            skLineSegment(sketch, "E5477", {"start": v(1.17, -117.33) * mm, "end": v(1.2, -117.44) * mm});
            skLineSegment(sketch, "E5478", {"start": v(1.2, -117.44) * mm, "end": v(1.24, -117.55) * mm});
            skLineSegment(sketch, "E5479", {"start": v(1.24, -117.55) * mm, "end": v(1.28, -117.66) * mm});
            skLineSegment(sketch, "E5480", {"start": v(1.28, -117.66) * mm, "end": v(1.31, -117.78) * mm});
            skLineSegment(sketch, "E5481", {"start": v(1.31, -117.78) * mm, "end": v(1.35, -117.89) * mm});
            skLineSegment(sketch, "E5482", {"start": v(1.35, -117.89) * mm, "end": v(1.4, -118) * mm});
            skLineSegment(sketch, "E5483", {"start": v(1.4, -118) * mm, "end": v(1.43, -118.12) * mm});
            skLineSegment(sketch, "E5484", {"start": v(1.43, -118.12) * mm, "end": v(1.47, -118.23) * mm});
            skLineSegment(sketch, "E5485", {"start": v(1.47, -118.23) * mm, "end": v(1.52, -118.35) * mm});
            skLineSegment(sketch, "E5486", {"start": v(1.52, -118.35) * mm, "end": v(1.6, -118.59) * mm});
            skLineSegment(sketch, "E5487", {"start": v(1.6, -118.59) * mm, "end": v(1.65, -118.7) * mm});
            skLineSegment(sketch, "E5488", {"start": v(1.65, -118.7) * mm, "end": v(1.74, -118.95) * mm});
            skLineSegment(sketch, "E5489", {"start": v(1.74, -118.95) * mm, "end": v(1.78, -119.07) * mm});
            skLineSegment(sketch, "E5490", {"start": v(1.78, -119.07) * mm, "end": v(1.88, -119.32) * mm});
            skLineSegment(sketch, "E5491", {"start": v(1.88, -119.32) * mm, "end": v(1.93, -119.45) * mm});
            skLineSegment(sketch, "E5492", {"start": v(1.93, -119.45) * mm, "end": v(1.98, -119.57) * mm});
            skLineSegment(sketch, "E5493", {"start": v(1.98, -119.57) * mm, "end": v(2.03, -119.7) * mm});
            skLineSegment(sketch, "E5494", {"start": v(2.03, -119.7) * mm, "end": v(2.13, -119.96) * mm});
            skLineSegment(sketch, "E5495", {"start": v(2.13, -119.96) * mm, "end": v(2.19, -120.09) * mm});
            skLineSegment(sketch, "E5496", {"start": v(2.19, -120.09) * mm, "end": v(2.24, -120.22) * mm});
            skLineSegment(sketch, "E5497", {"start": v(2.24, -120.22) * mm, "end": v(2.35, -120.48) * mm});
            skLineSegment(sketch, "E5498", {"start": v(2.35, -120.48) * mm, "end": v(2.4, -120.62) * mm});
            skLineSegment(sketch, "E5499", {"start": v(2.4, -120.62) * mm, "end": v(2.47, -120.75) * mm});
            skLineSegment(sketch, "E5500", {"start": v(2.47, -120.75) * mm, "end": v(2.52, -120.89) * mm});
            skLineSegment(sketch, "E5501", {"start": v(2.52, -120.89) * mm, "end": v(2.58, -121.02) * mm});
            skLineSegment(sketch, "E5502", {"start": v(2.58, -121.02) * mm, "end": v(2.64, -121.16) * mm});
            skLineSegment(sketch, "E5503", {"start": v(2.64, -121.16) * mm, "end": v(2.7, -121.24) * mm});
            skLineSegment(sketch, "E5504", {"start": v(2.7, -121.24) * mm, "end": v(4.36, -121.19) * mm});
            skLineSegment(sketch, "E5505", {"start": v(4.36, -121.19) * mm, "end": v(4.42, -121.1) * mm});
            skLineSegment(sketch, "E5506", {"start": v(4.42, -121.1) * mm, "end": v(4.47, -120.97) * mm});
            skLineSegment(sketch, "E5507", {"start": v(4.47, -120.97) * mm, "end": v(4.52, -120.83) * mm});
            skLineSegment(sketch, "E5508", {"start": v(4.52, -120.83) * mm, "end": v(4.57, -120.69) * mm});
            skLineSegment(sketch, "E5509", {"start": v(4.57, -120.69) * mm, "end": v(4.62, -120.55) * mm});
            skLineSegment(sketch, "E5510", {"start": v(4.62, -120.55) * mm, "end": v(4.72, -120.28) * mm});
            skLineSegment(sketch, "E5511", {"start": v(4.72, -120.28) * mm, "end": v(4.77, -120.15) * mm});
            skLineSegment(sketch, "E5512", {"start": v(4.77, -120.15) * mm, "end": v(4.81, -120.01) * mm});
            skLineSegment(sketch, "E5513", {"start": v(4.81, -120.01) * mm, "end": v(4.9, -119.75) * mm});
            skLineSegment(sketch, "E5514", {"start": v(4.9, -119.75) * mm, "end": v(4.95, -119.62) * mm});
            skLineSegment(sketch, "E5515", {"start": v(4.95, -119.62) * mm, "end": v(5, -119.48) * mm});
            skLineSegment(sketch, "E5516", {"start": v(5, -119.48) * mm, "end": v(5.03, -119.36) * mm});
            skLineSegment(sketch, "E5517", {"start": v(5.03, -119.36) * mm, "end": v(5.12, -119.1) * mm});
            skLineSegment(sketch, "E5518", {"start": v(5.12, -119.1) * mm, "end": v(5.16, -118.97) * mm});
            skLineSegment(sketch, "E5519", {"start": v(5.16, -118.97) * mm, "end": v(5.2, -118.85) * mm});
            skLineSegment(sketch, "E5520", {"start": v(5.2, -118.85) * mm, "end": v(5.27, -118.6) * mm});
            skLineSegment(sketch, "E5521", {"start": v(5.27, -118.6) * mm, "end": v(5.3, -118.48) * mm});
            skLineSegment(sketch, "E5522", {"start": v(5.3, -118.48) * mm, "end": v(5.35, -118.36) * mm});
            skLineSegment(sketch, "E5523", {"start": v(5.35, -118.36) * mm, "end": v(5.38, -118.24) * mm});
            skLineSegment(sketch, "E5524", {"start": v(5.38, -118.24) * mm, "end": v(5.42, -118.12) * mm});
            skLineSegment(sketch, "E5525", {"start": v(5.42, -118.12) * mm, "end": v(5.45, -118) * mm});
            skLineSegment(sketch, "E5526", {"start": v(5.45, -118) * mm, "end": v(5.48, -117.88) * mm});
            skLineSegment(sketch, "E5527", {"start": v(5.48, -117.88) * mm, "end": v(5.52, -117.77) * mm});
            skLineSegment(sketch, "E5528", {"start": v(5.52, -117.77) * mm, "end": v(5.55, -117.65) * mm});
            skLineSegment(sketch, "E5529", {"start": v(5.55, -117.65) * mm, "end": v(5.58, -117.54) * mm});
            skLineSegment(sketch, "E5530", {"start": v(5.58, -117.54) * mm, "end": v(5.61, -117.42) * mm});
            skLineSegment(sketch, "E5531", {"start": v(5.61, -117.42) * mm, "end": v(5.64, -117.31) * mm});
            skLineSegment(sketch, "E5532", {"start": v(5.64, -117.31) * mm, "end": v(5.7, -117.1) * mm});
            skLineSegment(sketch, "E5533", {"start": v(5.7, -117.1) * mm, "end": v(5.73, -116.98) * mm});
            skLineSegment(sketch, "E5534", {"start": v(5.73, -116.98) * mm, "end": v(5.76, -116.87) * mm});
            skLineSegment(sketch, "E5535", {"start": v(5.76, -116.87) * mm, "end": v(5.8, -116.66) * mm});
            skLineSegment(sketch, "E5536", {"start": v(5.8, -116.66) * mm, "end": v(5.83, -116.56) * mm});
            skLineSegment(sketch, "E5537", {"start": v(5.83, -116.56) * mm, "end": v(6.78, -116.33) * mm});
            skLineSegment(sketch, "E5538", {"start": v(6.78, -116.33) * mm, "end": v(7.75, -116.45) * mm});
            skLineSegment(sketch, "E5539", {"start": v(7.75, -116.45) * mm, "end": v(7.79, -116.55) * mm});
            skLineSegment(sketch, "E5540", {"start": v(7.79, -116.55) * mm, "end": v(7.83, -116.65) * mm});
            skLineSegment(sketch, "E5541", {"start": v(7.83, -116.65) * mm, "end": v(7.86, -116.75) * mm});
            skLineSegment(sketch, "E5542", {"start": v(7.86, -116.75) * mm, "end": v(7.9, -116.86) * mm});
            skLineSegment(sketch, "E5543", {"start": v(7.9, -116.86) * mm, "end": v(7.95, -116.96) * mm});
            skLineSegment(sketch, "E5544", {"start": v(7.95, -116.96) * mm, "end": v(8.03, -117.17) * mm});
            skLineSegment(sketch, "E5545", {"start": v(8.03, -117.17) * mm, "end": v(8.07, -117.28) * mm});
            skLineSegment(sketch, "E5546", {"start": v(8.07, -117.28) * mm, "end": v(8.12, -117.39) * mm});
            skLineSegment(sketch, "E5547", {"start": v(8.12, -117.39) * mm, "end": v(8.16, -117.5) * mm});
            skLineSegment(sketch, "E5548", {"start": v(8.16, -117.5) * mm, "end": v(8.2, -117.61) * mm});
            skLineSegment(sketch, "E5549", {"start": v(8.2, -117.61) * mm, "end": v(8.25, -117.72) * mm});
            skLineSegment(sketch, "E5550", {"start": v(8.25, -117.72) * mm, "end": v(8.35, -117.95) * mm});
            skLineSegment(sketch, "E5551", {"start": v(8.35, -117.95) * mm, "end": v(8.4, -118.06) * mm});
            skLineSegment(sketch, "E5552", {"start": v(8.4, -118.06) * mm, "end": v(8.5, -118.3) * mm});
            skLineSegment(sketch, "E5553", {"start": v(8.5, -118.3) * mm, "end": v(8.55, -118.41) * mm});
            skLineSegment(sketch, "E5554", {"start": v(8.55, -118.41) * mm, "end": v(8.65, -118.65) * mm});
            skLineSegment(sketch, "E5555", {"start": v(8.65, -118.65) * mm, "end": v(8.7, -118.77) * mm});
            skLineSegment(sketch, "E5556", {"start": v(8.7, -118.77) * mm, "end": v(8.76, -118.89) * mm});
            skLineSegment(sketch, "E5557", {"start": v(8.76, -118.89) * mm, "end": v(8.81, -119.01) * mm});
            skLineSegment(sketch, "E5558", {"start": v(8.81, -119.01) * mm, "end": v(8.87, -119.13) * mm});
            skLineSegment(sketch, "E5559", {"start": v(8.87, -119.13) * mm, "end": v(8.93, -119.26) * mm});
            skLineSegment(sketch, "E5560", {"start": v(8.93, -119.26) * mm, "end": v(8.99, -119.38) * mm});
            skLineSegment(sketch, "E5561", {"start": v(8.99, -119.38) * mm, "end": v(9.04, -119.5) * mm});
            skLineSegment(sketch, "E5562", {"start": v(9.04, -119.5) * mm, "end": v(9.1, -119.63) * mm});
            skLineSegment(sketch, "E5563", {"start": v(9.1, -119.63) * mm, "end": v(9.17, -119.76) * mm});
            skLineSegment(sketch, "E5564", {"start": v(9.17, -119.76) * mm, "end": v(9.23, -119.89) * mm});
            skLineSegment(sketch, "E5565", {"start": v(9.23, -119.89) * mm, "end": v(9.29, -120.01) * mm});
            skLineSegment(sketch, "E5566", {"start": v(9.29, -120.01) * mm, "end": v(9.35, -120.14) * mm});
            skLineSegment(sketch, "E5567", {"start": v(9.35, -120.14) * mm, "end": v(9.42, -120.27) * mm});
            skLineSegment(sketch, "E5568", {"start": v(9.42, -120.27) * mm, "end": v(9.48, -120.4) * mm});
            skLineSegment(sketch, "E5569", {"start": v(9.48, -120.4) * mm, "end": v(9.55, -120.54) * mm});
            skLineSegment(sketch, "E5570", {"start": v(9.55, -120.54) * mm, "end": v(9.62, -120.67) * mm});
            skLineSegment(sketch, "E5571", {"start": v(9.62, -120.67) * mm, "end": v(9.68, -120.8) * mm});
            skLineSegment(sketch, "E5572", {"start": v(9.68, -120.8) * mm, "end": v(9.75, -120.87) * mm});
            skLineSegment(sketch, "E5573", {"start": v(9.75, -120.87) * mm, "end": v(11.4, -120.73) * mm});
            skLineSegment(sketch, "E5574", {"start": v(11.4, -120.73) * mm, "end": v(11.45, -120.65) * mm});
            skLineSegment(sketch, "E5575", {"start": v(11.45, -120.65) * mm, "end": v(11.5, -120.5) * mm});
            skLineSegment(sketch, "E5576", {"start": v(11.5, -120.5) * mm, "end": v(11.58, -120.22) * mm});
            skLineSegment(sketch, "E5577", {"start": v(11.58, -120.22) * mm, "end": v(11.62, -120.08) * mm});
            skLineSegment(sketch, "E5578", {"start": v(11.62, -120.08) * mm, "end": v(11.66, -119.94) * mm});
            skLineSegment(sketch, "E5579", {"start": v(11.66, -119.94) * mm, "end": v(11.74, -119.66) * mm});
            skLineSegment(sketch, "E5580", {"start": v(11.74, -119.66) * mm, "end": v(11.78, -119.53) * mm});
            skLineSegment(sketch, "E5581", {"start": v(11.78, -119.53) * mm, "end": v(11.86, -119.26) * mm});
            skLineSegment(sketch, "E5582", {"start": v(11.86, -119.26) * mm, "end": v(11.9, -119.12) * mm});
            skLineSegment(sketch, "E5583", {"start": v(11.9, -119.12) * mm, "end": v(11.93, -119) * mm});
            skLineSegment(sketch, "E5584", {"start": v(11.93, -119) * mm, "end": v(11.97, -118.86) * mm});
            skLineSegment(sketch, "E5585", {"start": v(11.97, -118.86) * mm, "end": v(12, -118.73) * mm});
            skLineSegment(sketch, "E5586", {"start": v(12, -118.73) * mm, "end": v(12.03, -118.6) * mm});
            skLineSegment(sketch, "E5587", {"start": v(12.03, -118.6) * mm, "end": v(12.06, -118.47) * mm});
            skLineSegment(sketch, "E5588", {"start": v(12.06, -118.47) * mm, "end": v(12.1, -118.35) * mm});
            skLineSegment(sketch, "E5589", {"start": v(12.1, -118.35) * mm, "end": v(12.13, -118.22) * mm});
            skLineSegment(sketch, "E5590", {"start": v(12.13, -118.22) * mm, "end": v(12.16, -118.1) * mm});
            skLineSegment(sketch, "E5591", {"start": v(12.16, -118.1) * mm, "end": v(12.19, -117.97) * mm});
            skLineSegment(sketch, "E5592", {"start": v(12.19, -117.97) * mm, "end": v(12.22, -117.85) * mm});
            skLineSegment(sketch, "E5593", {"start": v(12.22, -117.85) * mm, "end": v(12.25, -117.72) * mm});
            skLineSegment(sketch, "E5594", {"start": v(12.25, -117.72) * mm, "end": v(12.28, -117.6) * mm});
            skLineSegment(sketch, "E5595", {"start": v(12.28, -117.6) * mm, "end": v(12.3, -117.48) * mm});
            skLineSegment(sketch, "E5596", {"start": v(12.3, -117.48) * mm, "end": v(12.33, -117.36) * mm});
            skLineSegment(sketch, "E5597", {"start": v(12.33, -117.36) * mm, "end": v(12.36, -117.25) * mm});
            skLineSegment(sketch, "E5598", {"start": v(12.36, -117.25) * mm, "end": v(12.38, -117.13) * mm});
            skLineSegment(sketch, "E5599", {"start": v(12.38, -117.13) * mm, "end": v(12.4, -117.01) * mm});
            skLineSegment(sketch, "E5600", {"start": v(12.4, -117.01) * mm, "end": v(12.43, -116.9) * mm});
            skLineSegment(sketch, "E5601", {"start": v(12.43, -116.9) * mm, "end": v(12.45, -116.79) * mm});
            skLineSegment(sketch, "E5602", {"start": v(12.45, -116.79) * mm, "end": v(12.48, -116.67) * mm});
            skLineSegment(sketch, "E5603", {"start": v(12.48, -116.67) * mm, "end": v(12.5, -116.56) * mm});
            skLineSegment(sketch, "E5604", {"start": v(12.5, -116.56) * mm, "end": v(12.52, -116.45) * mm});
            skLineSegment(sketch, "E5605", {"start": v(12.52, -116.45) * mm, "end": v(12.56, -116.23) * mm});
            skLineSegment(sketch, "E5606", {"start": v(12.56, -116.23) * mm, "end": v(12.58, -116.13) * mm});
            skLineSegment(sketch, "E5607", {"start": v(12.58, -116.13) * mm, "end": v(12.6, -116.02) * mm});
            skLineSegment(sketch, "E5608", {"start": v(12.6, -116.02) * mm, "end": v(13.53, -115.74) * mm});
            skLineSegment(sketch, "E5609", {"start": v(13.53, -115.74) * mm, "end": v(14.5, -115.8) * mm});
            skLineSegment(sketch, "E5610", {"start": v(14.5, -115.8) * mm, "end": v(14.6, -116) * mm});
            skLineSegment(sketch, "E5611", {"start": v(14.6, -116) * mm, "end": v(14.64, -116.1) * mm});
            skLineSegment(sketch, "E5612", {"start": v(14.64, -116.1) * mm, "end": v(14.69, -116.2) * mm});
            skLineSegment(sketch, "E5613", {"start": v(14.69, -116.2) * mm, "end": v(14.73, -116.3) * mm});
            skLineSegment(sketch, "E5614", {"start": v(14.73, -116.3) * mm, "end": v(14.78, -116.4) * mm});
            skLineSegment(sketch, "E5615", {"start": v(14.78, -116.4) * mm, "end": v(14.83, -116.5) * mm});
            skLineSegment(sketch, "E5616", {"start": v(14.83, -116.5) * mm, "end": v(14.88, -116.61) * mm});
            skLineSegment(sketch, "E5617", {"start": v(14.88, -116.61) * mm, "end": v(14.93, -116.72) * mm});
            skLineSegment(sketch, "E5618", {"start": v(14.93, -116.72) * mm, "end": v(14.98, -116.83) * mm});
            skLineSegment(sketch, "E5619", {"start": v(14.98, -116.83) * mm, "end": v(15.03, -116.93) * mm});
            skLineSegment(sketch, "E5620", {"start": v(15.03, -116.93) * mm, "end": v(15.08, -117.04) * mm});
            skLineSegment(sketch, "E5621", {"start": v(15.08, -117.04) * mm, "end": v(15.2, -117.26) * mm});
            skLineSegment(sketch, "E5622", {"start": v(15.2, -117.26) * mm, "end": v(15.25, -117.37) * mm});
            skLineSegment(sketch, "E5623", {"start": v(15.25, -117.37) * mm, "end": v(15.3, -117.49) * mm});
            skLineSegment(sketch, "E5624", {"start": v(15.3, -117.49) * mm, "end": v(15.36, -117.6) * mm});
            skLineSegment(sketch, "E5625", {"start": v(15.36, -117.6) * mm, "end": v(15.47, -117.83) * mm});
            skLineSegment(sketch, "E5626", {"start": v(15.47, -117.83) * mm, "end": v(15.53, -117.94) * mm});
            skLineSegment(sketch, "E5627", {"start": v(15.53, -117.94) * mm, "end": v(15.66, -118.18) * mm});
            skLineSegment(sketch, "E5628", {"start": v(15.66, -118.18) * mm, "end": v(15.72, -118.3) * mm});
            skLineSegment(sketch, "E5629", {"start": v(15.72, -118.3) * mm, "end": v(15.78, -118.41) * mm});
            skLineSegment(sketch, "E5630", {"start": v(15.78, -118.41) * mm, "end": v(15.91, -118.65) * mm});
            skLineSegment(sketch, "E5631", {"start": v(15.91, -118.65) * mm, "end": v(15.98, -118.78) * mm});
            skLineSegment(sketch, "E5632", {"start": v(15.98, -118.78) * mm, "end": v(16.04, -118.9) * mm});
            skLineSegment(sketch, "E5633", {"start": v(16.04, -118.9) * mm, "end": v(16.11, -119.02) * mm});
            skLineSegment(sketch, "E5634", {"start": v(16.11, -119.02) * mm, "end": v(16.18, -119.15) * mm});
            skLineSegment(sketch, "E5635", {"start": v(16.18, -119.15) * mm, "end": v(16.25, -119.27) * mm});
            skLineSegment(sketch, "E5636", {"start": v(16.25, -119.27) * mm, "end": v(16.4, -119.52) * mm});
            skLineSegment(sketch, "E5637", {"start": v(16.4, -119.52) * mm, "end": v(16.47, -119.65) * mm});
            skLineSegment(sketch, "E5638", {"start": v(16.47, -119.65) * mm, "end": v(16.54, -119.78) * mm});
            skLineSegment(sketch, "E5639", {"start": v(16.54, -119.78) * mm, "end": v(16.62, -119.9) * mm});
            skLineSegment(sketch, "E5640", {"start": v(16.62, -119.9) * mm, "end": v(16.7, -120.03) * mm});
            skLineSegment(sketch, "E5641", {"start": v(16.7, -120.03) * mm, "end": v(16.76, -120.1) * mm});
            skLineSegment(sketch, "E5642", {"start": v(16.76, -120.1) * mm, "end": v(18.4, -119.86) * mm});
            skLineSegment(sketch, "E5643", {"start": v(18.4, -119.86) * mm, "end": v(18.45, -119.78) * mm});
            skLineSegment(sketch, "E5644", {"start": v(18.45, -119.78) * mm, "end": v(18.48, -119.63) * mm});
            skLineSegment(sketch, "E5645", {"start": v(18.48, -119.63) * mm, "end": v(18.52, -119.49) * mm});
            skLineSegment(sketch, "E5646", {"start": v(18.52, -119.49) * mm, "end": v(18.55, -119.34) * mm});
            skLineSegment(sketch, "E5647", {"start": v(18.55, -119.34) * mm, "end": v(18.59, -119.2) * mm});
            skLineSegment(sketch, "E5648", {"start": v(18.59, -119.2) * mm, "end": v(18.62, -119.06) * mm});
            skLineSegment(sketch, "E5649", {"start": v(18.62, -119.06) * mm, "end": v(18.65, -118.92) * mm});
            skLineSegment(sketch, "E5650", {"start": v(18.65, -118.92) * mm, "end": v(18.68, -118.78) * mm});
            skLineSegment(sketch, "E5651", {"start": v(18.68, -118.78) * mm, "end": v(18.71, -118.64) * mm});
            skLineSegment(sketch, "E5652", {"start": v(18.71, -118.64) * mm, "end": v(18.74, -118.5) * mm});
            skLineSegment(sketch, "E5653", {"start": v(18.74, -118.5) * mm, "end": v(18.77, -118.37) * mm});
            skLineSegment(sketch, "E5654", {"start": v(18.77, -118.37) * mm, "end": v(18.8, -118.23) * mm});
            skLineSegment(sketch, "E5655", {"start": v(18.8, -118.23) * mm, "end": v(18.86, -117.96) * mm});
            skLineSegment(sketch, "E5656", {"start": v(18.86, -117.96) * mm, "end": v(18.88, -117.83) * mm});
            skLineSegment(sketch, "E5657", {"start": v(18.88, -117.83) * mm, "end": v(18.9, -117.7) * mm});
            skLineSegment(sketch, "E5658", {"start": v(18.9, -117.7) * mm, "end": v(18.96, -117.44) * mm});
            skLineSegment(sketch, "E5659", {"start": v(18.96, -117.44) * mm, "end": v(18.98, -117.31) * mm});
            skLineSegment(sketch, "E5660", {"start": v(18.98, -117.31) * mm, "end": v(19, -117.19) * mm});
            skLineSegment(sketch, "E5661", {"start": v(19, -117.19) * mm, "end": v(19.03, -117.06) * mm});
            skLineSegment(sketch, "E5662", {"start": v(19.03, -117.06) * mm, "end": v(19.07, -116.81) * mm});
            skLineSegment(sketch, "E5663", {"start": v(19.07, -116.81) * mm, "end": v(19.1, -116.7) * mm});
            skLineSegment(sketch, "E5664", {"start": v(19.1, -116.7) * mm, "end": v(19.11, -116.57) * mm});
            skLineSegment(sketch, "E5665", {"start": v(19.11, -116.57) * mm, "end": v(19.15, -116.33) * mm});
            skLineSegment(sketch, "E5666", {"start": v(19.15, -116.33) * mm, "end": v(19.19, -116.1) * mm});
            skLineSegment(sketch, "E5667", {"start": v(19.19, -116.1) * mm, "end": v(19.2, -115.98) * mm});
            skLineSegment(sketch, "E5668", {"start": v(19.2, -115.98) * mm, "end": v(19.22, -115.86) * mm});
            skLineSegment(sketch, "E5669", {"start": v(19.22, -115.86) * mm, "end": v(19.26, -115.64) * mm});
            skLineSegment(sketch, "E5670", {"start": v(19.26, -115.64) * mm, "end": v(19.27, -115.53) * mm});
            skLineSegment(sketch, "E5671", {"start": v(19.27, -115.53) * mm, "end": v(19.28, -115.42) * mm});
            skLineSegment(sketch, "E5672", {"start": v(19.28, -115.42) * mm, "end": v(19.3, -115.3) * mm});
            skLineSegment(sketch, "E5673", {"start": v(19.3, -115.3) * mm, "end": v(19.31, -115.2) * mm});
            skLineSegment(sketch, "E5674", {"start": v(19.31, -115.2) * mm, "end": v(19.33, -115.1) * mm});
            skLineSegment(sketch, "E5675", {"start": v(19.33, -115.1) * mm, "end": v(20.24, -114.76) * mm});
            skLineSegment(sketch, "E5676", {"start": v(20.24, -114.76) * mm, "end": v(21.22, -114.76) * mm});
            skLineSegment(sketch, "E5677", {"start": v(21.22, -114.76) * mm, "end": v(21.26, -114.85) * mm});
            skLineSegment(sketch, "E5678", {"start": v(21.26, -114.85) * mm, "end": v(21.31, -114.95) * mm});
            skLineSegment(sketch, "E5679", {"start": v(21.31, -114.95) * mm, "end": v(21.37, -115.05) * mm});
            skLineSegment(sketch, "E5680", {"start": v(21.37, -115.05) * mm, "end": v(21.42, -115.15) * mm});
            skLineSegment(sketch, "E5681", {"start": v(21.42, -115.15) * mm, "end": v(21.47, -115.25) * mm});
            skLineSegment(sketch, "E5682", {"start": v(21.47, -115.25) * mm, "end": v(21.52, -115.35) * mm});
            skLineSegment(sketch, "E5683", {"start": v(21.52, -115.35) * mm, "end": v(21.58, -115.45) * mm});
            skLineSegment(sketch, "E5684", {"start": v(21.58, -115.45) * mm, "end": v(21.63, -115.55) * mm});
            skLineSegment(sketch, "E5685", {"start": v(21.63, -115.55) * mm, "end": v(21.75, -115.76) * mm});
            skLineSegment(sketch, "E5686", {"start": v(21.75, -115.76) * mm, "end": v(21.8, -115.86) * mm});
            skLineSegment(sketch, "E5687", {"start": v(21.8, -115.86) * mm, "end": v(21.86, -115.97) * mm});
            skLineSegment(sketch, "E5688", {"start": v(21.86, -115.97) * mm, "end": v(21.92, -116.07) * mm});
            skLineSegment(sketch, "E5689", {"start": v(21.92, -116.07) * mm, "end": v(21.98, -116.18) * mm});
            skLineSegment(sketch, "E5690", {"start": v(21.98, -116.18) * mm, "end": v(22.1, -116.4) * mm});
            skLineSegment(sketch, "E5691", {"start": v(22.1, -116.4) * mm, "end": v(22.17, -116.5) * mm});
            skLineSegment(sketch, "E5692", {"start": v(22.17, -116.5) * mm, "end": v(22.23, -116.62) * mm});
            skLineSegment(sketch, "E5693", {"start": v(22.23, -116.62) * mm, "end": v(22.3, -116.73) * mm});
            skLineSegment(sketch, "E5694", {"start": v(22.3, -116.73) * mm, "end": v(22.37, -116.84) * mm});
            skLineSegment(sketch, "E5695", {"start": v(22.37, -116.84) * mm, "end": v(22.5, -117.07) * mm});
            skLineSegment(sketch, "E5696", {"start": v(22.5, -117.07) * mm, "end": v(22.57, -117.18) * mm});
            skLineSegment(sketch, "E5697", {"start": v(22.57, -117.18) * mm, "end": v(22.64, -117.3) * mm});
            skLineSegment(sketch, "E5698", {"start": v(22.64, -117.3) * mm, "end": v(22.78, -117.53) * mm});
            skLineSegment(sketch, "E5699", {"start": v(22.78, -117.53) * mm, "end": v(22.86, -117.65) * mm});
            skLineSegment(sketch, "E5700", {"start": v(22.86, -117.65) * mm, "end": v(22.93, -117.76) * mm});
            skLineSegment(sketch, "E5701", {"start": v(22.93, -117.76) * mm, "end": v(23, -117.88) * mm});
            skLineSegment(sketch, "E5702", {"start": v(23, -117.88) * mm, "end": v(23.08, -118) * mm});
            skLineSegment(sketch, "E5703", {"start": v(23.08, -118) * mm, "end": v(23.24, -118.25) * mm});
            skLineSegment(sketch, "E5704", {"start": v(23.24, -118.25) * mm, "end": v(23.32, -118.37) * mm});
            skLineSegment(sketch, "E5705", {"start": v(23.32, -118.37) * mm, "end": v(23.4, -118.49) * mm});
            skLineSegment(sketch, "E5706", {"start": v(23.4, -118.49) * mm, "end": v(23.48, -118.61) * mm});
            skLineSegment(sketch, "E5707", {"start": v(23.48, -118.61) * mm, "end": v(23.56, -118.74) * mm});
            skLineSegment(sketch, "E5708", {"start": v(23.56, -118.74) * mm, "end": v(23.64, -118.86) * mm});
            skLineSegment(sketch, "E5709", {"start": v(23.64, -118.86) * mm, "end": v(23.72, -118.93) * mm});
            skLineSegment(sketch, "E5710", {"start": v(23.72, -118.93) * mm, "end": v(25.34, -118.59) * mm});
            skLineSegment(sketch, "E5711", {"start": v(25.34, -118.59) * mm, "end": v(25.38, -118.5) * mm});
            skLineSegment(sketch, "E5712", {"start": v(25.38, -118.5) * mm, "end": v(25.4, -118.35) * mm});
            skLineSegment(sketch, "E5713", {"start": v(25.4, -118.35) * mm, "end": v(25.44, -118.2) * mm});
            skLineSegment(sketch, "E5714", {"start": v(25.44, -118.2) * mm, "end": v(25.46, -118.06) * mm});
            skLineSegment(sketch, "E5715", {"start": v(25.46, -118.06) * mm, "end": v(25.49, -117.92) * mm});
            skLineSegment(sketch, "E5716", {"start": v(25.49, -117.92) * mm, "end": v(25.51, -117.78) * mm});
            skLineSegment(sketch, "E5717", {"start": v(25.51, -117.78) * mm, "end": v(25.56, -117.5) * mm});
            skLineSegment(sketch, "E5718", {"start": v(25.56, -117.5) * mm, "end": v(25.58, -117.35) * mm});
            skLineSegment(sketch, "E5719", {"start": v(25.58, -117.35) * mm, "end": v(25.6, -117.21) * mm});
            skLineSegment(sketch, "E5720", {"start": v(25.6, -117.21) * mm, "end": v(25.62, -117.08) * mm});
            skLineSegment(sketch, "E5721", {"start": v(25.62, -117.08) * mm, "end": v(25.64, -116.94) * mm});
            skLineSegment(sketch, "E5722", {"start": v(25.64, -116.94) * mm, "end": v(25.66, -116.8) * mm});
            skLineSegment(sketch, "E5723", {"start": v(25.66, -116.8) * mm, "end": v(25.7, -116.54) * mm});
            skLineSegment(sketch, "E5724", {"start": v(25.7, -116.54) * mm, "end": v(25.72, -116.4) * mm});
            skLineSegment(sketch, "E5725", {"start": v(25.72, -116.4) * mm, "end": v(25.74, -116.27) * mm});
            skLineSegment(sketch, "E5726", {"start": v(25.74, -116.27) * mm, "end": v(25.75, -116.14) * mm});
            skLineSegment(sketch, "E5727", {"start": v(25.75, -116.14) * mm, "end": v(25.77, -116.01) * mm});
            skLineSegment(sketch, "E5728", {"start": v(25.77, -116.01) * mm, "end": v(25.79, -115.88) * mm});
            skLineSegment(sketch, "E5729", {"start": v(25.79, -115.88) * mm, "end": v(25.82, -115.63) * mm});
            skLineSegment(sketch, "E5730", {"start": v(25.82, -115.63) * mm, "end": v(25.85, -115.38) * mm});
            skLineSegment(sketch, "E5731", {"start": v(25.85, -115.38) * mm, "end": v(25.86, -115.26) * mm});
            skLineSegment(sketch, "E5732", {"start": v(25.86, -115.26) * mm, "end": v(25.88, -115.02) * mm});
            skLineSegment(sketch, "E5733", {"start": v(25.88, -115.02) * mm, "end": v(25.9, -114.9) * mm});
            skLineSegment(sketch, "E5734", {"start": v(25.9, -114.9) * mm, "end": v(25.92, -114.67) * mm});
            skLineSegment(sketch, "E5735", {"start": v(25.92, -114.67) * mm, "end": v(25.93, -114.55) * mm});
            skLineSegment(sketch, "E5736", {"start": v(25.93, -114.55) * mm, "end": v(25.94, -114.44) * mm});
            skLineSegment(sketch, "E5737", {"start": v(25.94, -114.44) * mm, "end": v(25.96, -114.21) * mm});
            skLineSegment(sketch, "E5738", {"start": v(25.96, -114.21) * mm, "end": v(25.96, -114.1) * mm});
            skLineSegment(sketch, "E5739", {"start": v(25.96, -114.1) * mm, "end": v(25.97, -113.99) * mm});
            skLineSegment(sketch, "E5740", {"start": v(25.97, -113.99) * mm, "end": v(25.98, -113.88) * mm});
            skLineSegment(sketch, "E5741", {"start": v(25.98, -113.88) * mm, "end": v(25.99, -113.77) * mm});
            skLineSegment(sketch, "E5742", {"start": v(25.99, -113.77) * mm, "end": v(26.88, -113.38) * mm});
            skLineSegment(sketch, "E5743", {"start": v(26.88, -113.38) * mm, "end": v(27.85, -113.33) * mm});
            skLineSegment(sketch, "E5744", {"start": v(27.85, -113.33) * mm, "end": v(27.9, -113.42) * mm});
            skLineSegment(sketch, "E5745", {"start": v(27.9, -113.42) * mm, "end": v(27.96, -113.52) * mm});
            skLineSegment(sketch, "E5746", {"start": v(27.96, -113.52) * mm, "end": v(28.02, -113.61) * mm});
            skLineSegment(sketch, "E5747", {"start": v(28.02, -113.61) * mm, "end": v(28.08, -113.7) * mm});
            skLineSegment(sketch, "E5748", {"start": v(28.08, -113.7) * mm, "end": v(28.13, -113.8) * mm});
            skLineSegment(sketch, "E5749", {"start": v(28.13, -113.8) * mm, "end": v(28.2, -113.9) * mm});
            skLineSegment(sketch, "E5750", {"start": v(28.2, -113.9) * mm, "end": v(28.31, -114.1) * mm});
            skLineSegment(sketch, "E5751", {"start": v(28.31, -114.1) * mm, "end": v(28.38, -114.2) * mm});
            skLineSegment(sketch, "E5752", {"start": v(28.38, -114.2) * mm, "end": v(28.44, -114.3) * mm});
            skLineSegment(sketch, "E5753", {"start": v(28.44, -114.3) * mm, "end": v(28.5, -114.4) * mm});
            skLineSegment(sketch, "E5754", {"start": v(28.5, -114.4) * mm, "end": v(28.57, -114.5) * mm});
            skLineSegment(sketch, "E5755", {"start": v(28.57, -114.5) * mm, "end": v(28.63, -114.6) * mm});
            skLineSegment(sketch, "E5756", {"start": v(28.63, -114.6) * mm, "end": v(28.7, -114.7) * mm});
            skLineSegment(sketch, "E5757", {"start": v(28.7, -114.7) * mm, "end": v(28.77, -114.81) * mm});
            skLineSegment(sketch, "E5758", {"start": v(28.77, -114.81) * mm, "end": v(28.84, -114.92) * mm});
            skLineSegment(sketch, "E5759", {"start": v(28.84, -114.92) * mm, "end": v(28.98, -115.13) * mm});
            skLineSegment(sketch, "E5760", {"start": v(28.98, -115.13) * mm, "end": v(29.05, -115.24) * mm});
            skLineSegment(sketch, "E5761", {"start": v(29.05, -115.24) * mm, "end": v(29.12, -115.34) * mm});
            skLineSegment(sketch, "E5762", {"start": v(29.12, -115.34) * mm, "end": v(29.2, -115.45) * mm});
            skLineSegment(sketch, "E5763", {"start": v(29.2, -115.45) * mm, "end": v(29.27, -115.56) * mm});
            skLineSegment(sketch, "E5764", {"start": v(29.27, -115.56) * mm, "end": v(29.35, -115.67) * mm});
            skLineSegment(sketch, "E5765", {"start": v(29.35, -115.67) * mm, "end": v(29.42, -115.78) * mm});
            skLineSegment(sketch, "E5766", {"start": v(29.42, -115.78) * mm, "end": v(29.5, -115.9) * mm});
            skLineSegment(sketch, "E5767", {"start": v(29.5, -115.9) * mm, "end": v(29.58, -116) * mm});
            skLineSegment(sketch, "E5768", {"start": v(29.58, -116) * mm, "end": v(29.66, -116.12) * mm});
            skLineSegment(sketch, "E5769", {"start": v(29.66, -116.12) * mm, "end": v(29.74, -116.23) * mm});
            skLineSegment(sketch, "E5770", {"start": v(29.74, -116.23) * mm, "end": v(29.82, -116.35) * mm});
            skLineSegment(sketch, "E5771", {"start": v(29.82, -116.35) * mm, "end": v(29.9, -116.46) * mm});
            skLineSegment(sketch, "E5772", {"start": v(29.9, -116.46) * mm, "end": v(29.99, -116.58) * mm});
            skLineSegment(sketch, "E5773", {"start": v(29.99, -116.58) * mm, "end": v(30.07, -116.7) * mm});
            skLineSegment(sketch, "E5774", {"start": v(30.07, -116.7) * mm, "end": v(30.25, -116.93) * mm});
            skLineSegment(sketch, "E5775", {"start": v(30.25, -116.93) * mm, "end": v(30.33, -117.05) * mm});
            skLineSegment(sketch, "E5776", {"start": v(30.33, -117.05) * mm, "end": v(30.42, -117.16) * mm});
            skLineSegment(sketch, "E5777", {"start": v(30.42, -117.16) * mm, "end": v(30.51, -117.28) * mm});
            skLineSegment(sketch, "E5778", {"start": v(30.51, -117.28) * mm, "end": v(30.6, -117.35) * mm});
            skLineSegment(sketch, "E5779", {"start": v(30.6, -117.35) * mm, "end": v(32.2, -116.92) * mm});
            skLineSegment(sketch, "E5780", {"start": v(32.2, -116.92) * mm, "end": v(32.23, -116.83) * mm});
            skLineSegment(sketch, "E5781", {"start": v(32.23, -116.83) * mm, "end": v(32.25, -116.68) * mm});
            skLineSegment(sketch, "E5782", {"start": v(32.25, -116.68) * mm, "end": v(32.28, -116.38) * mm});
            skLineSegment(sketch, "E5783", {"start": v(32.28, -116.38) * mm, "end": v(32.3, -116.24) * mm});
            skLineSegment(sketch, "E5784", {"start": v(32.3, -116.24) * mm, "end": v(32.32, -116.1) * mm});
            skLineSegment(sketch, "E5785", {"start": v(32.32, -116.1) * mm, "end": v(32.33, -115.95) * mm});
            skLineSegment(sketch, "E5786", {"start": v(32.33, -115.95) * mm, "end": v(32.35, -115.8) * mm});
            skLineSegment(sketch, "E5787", {"start": v(32.35, -115.8) * mm, "end": v(32.36, -115.67) * mm});
            skLineSegment(sketch, "E5788", {"start": v(32.36, -115.67) * mm, "end": v(32.37, -115.53) * mm});
            skLineSegment(sketch, "E5789", {"start": v(32.37, -115.53) * mm, "end": v(32.39, -115.39) * mm});
            skLineSegment(sketch, "E5790", {"start": v(32.39, -115.39) * mm, "end": v(32.4, -115.25) * mm});
            skLineSegment(sketch, "E5791", {"start": v(32.4, -115.25) * mm, "end": v(32.41, -115.11) * mm});
            skLineSegment(sketch, "E5792", {"start": v(32.41, -115.11) * mm, "end": v(32.42, -114.98) * mm});
            skLineSegment(sketch, "E5793", {"start": v(32.42, -114.98) * mm, "end": v(32.43, -114.84) * mm});
            skLineSegment(sketch, "E5794", {"start": v(32.43, -114.84) * mm, "end": v(32.44, -114.71) * mm});
            skLineSegment(sketch, "E5795", {"start": v(32.44, -114.71) * mm, "end": v(32.45, -114.58) * mm});
            skLineSegment(sketch, "E5796", {"start": v(32.45, -114.58) * mm, "end": v(32.46, -114.45) * mm});
            skLineSegment(sketch, "E5797", {"start": v(32.46, -114.45) * mm, "end": v(32.47, -114.32) * mm});
            skLineSegment(sketch, "E5798", {"start": v(32.47, -114.32) * mm, "end": v(32.48, -114.19) * mm});
            skLineSegment(sketch, "E5799", {"start": v(32.48, -114.19) * mm, "end": v(32.5, -114.06) * mm});
            skLineSegment(sketch, "E5800", {"start": v(32.5, -114.06) * mm, "end": v(32.5, -113.93) * mm});
            skLineSegment(sketch, "E5801", {"start": v(32.5, -113.93) * mm, "end": v(32.5, -113.8) * mm});
            skLineSegment(sketch, "E5802", {"start": v(32.5, -113.8) * mm, "end": v(32.51, -113.69) * mm});
            skLineSegment(sketch, "E5803", {"start": v(32.51, -113.69) * mm, "end": v(32.52, -113.56) * mm});
            skLineSegment(sketch, "E5804", {"start": v(32.52, -113.56) * mm, "end": v(32.53, -113.32) * mm});
            skLineSegment(sketch, "E5805", {"start": v(32.53, -113.32) * mm, "end": v(32.53, -113.2) * mm});
            skLineSegment(sketch, "E5806", {"start": v(32.53, -113.2) * mm, "end": v(32.54, -113.08) * mm});
            skLineSegment(sketch, "E5807", {"start": v(32.54, -113.08) * mm, "end": v(32.54, -112.96) * mm});
            skLineSegment(sketch, "E5808", {"start": v(32.54, -112.96) * mm, "end": v(32.54, -112.85) * mm});
            skLineSegment(sketch, "E5809", {"start": v(32.54, -112.85) * mm, "end": v(32.55, -112.62) * mm});
            skLineSegment(sketch, "E5810", {"start": v(32.55, -112.62) * mm, "end": v(32.55, -112.5) * mm});
            skLineSegment(sketch, "E5811", {"start": v(32.55, -112.5) * mm, "end": v(32.55, -112.4) * mm});
            skLineSegment(sketch, "E5812", {"start": v(32.55, -112.4) * mm, "end": v(32.55, -112.29) * mm});
            skLineSegment(sketch, "E5813", {"start": v(32.55, -112.29) * mm, "end": v(32.56, -112.18) * mm});
            skLineSegment(sketch, "E5814", {"start": v(32.56, -112.18) * mm, "end": v(32.56, -112.07) * mm});
            skLineSegment(sketch, "E5815", {"start": v(32.56, -112.07) * mm, "end": v(33.43, -111.63) * mm});
            skLineSegment(sketch, "E5816", {"start": v(33.43, -111.63) * mm, "end": v(34.4, -111.52) * mm});
            skLineSegment(sketch, "E5817", {"start": v(34.4, -111.52) * mm, "end": v(34.46, -111.6) * mm});
            skLineSegment(sketch, "E5818", {"start": v(34.46, -111.6) * mm, "end": v(34.52, -111.7) * mm});
            skLineSegment(sketch, "E5819", {"start": v(34.52, -111.7) * mm, "end": v(34.58, -111.8) * mm});
            skLineSegment(sketch, "E5820", {"start": v(34.58, -111.8) * mm, "end": v(34.64, -111.88) * mm});
            skLineSegment(sketch, "E5821", {"start": v(34.64, -111.88) * mm, "end": v(34.7, -111.98) * mm});
            skLineSegment(sketch, "E5822", {"start": v(34.7, -111.98) * mm, "end": v(34.77, -112.07) * mm});
            skLineSegment(sketch, "E5823", {"start": v(34.77, -112.07) * mm, "end": v(34.83, -112.16) * mm});
            skLineSegment(sketch, "E5824", {"start": v(34.83, -112.16) * mm, "end": v(34.9, -112.26) * mm});
            skLineSegment(sketch, "E5825", {"start": v(34.9, -112.26) * mm, "end": v(35.04, -112.45) * mm});
            skLineSegment(sketch, "E5826", {"start": v(35.04, -112.45) * mm, "end": v(35.18, -112.65) * mm});
            skLineSegment(sketch, "E5827", {"start": v(35.18, -112.65) * mm, "end": v(35.25, -112.74) * mm});
            skLineSegment(sketch, "E5828", {"start": v(35.25, -112.74) * mm, "end": v(35.32, -112.84) * mm});
            skLineSegment(sketch, "E5829", {"start": v(35.32, -112.84) * mm, "end": v(35.4, -112.94) * mm});
            skLineSegment(sketch, "E5830", {"start": v(35.4, -112.94) * mm, "end": v(35.47, -113.04) * mm});
            skLineSegment(sketch, "E5831", {"start": v(35.47, -113.04) * mm, "end": v(35.55, -113.15) * mm});
            skLineSegment(sketch, "E5832", {"start": v(35.55, -113.15) * mm, "end": v(35.62, -113.25) * mm});
            skLineSegment(sketch, "E5833", {"start": v(35.62, -113.25) * mm, "end": v(35.7, -113.35) * mm});
            skLineSegment(sketch, "E5834", {"start": v(35.7, -113.35) * mm, "end": v(35.78, -113.45) * mm});
            skLineSegment(sketch, "E5835", {"start": v(35.78, -113.45) * mm, "end": v(35.94, -113.66) * mm});
            skLineSegment(sketch, "E5836", {"start": v(35.94, -113.66) * mm, "end": v(36.1, -113.88) * mm});
            skLineSegment(sketch, "E5837", {"start": v(36.1, -113.88) * mm, "end": v(36.19, -113.98) * mm});
            skLineSegment(sketch, "E5838", {"start": v(36.19, -113.98) * mm, "end": v(36.27, -114.09) * mm});
            skLineSegment(sketch, "E5839", {"start": v(36.27, -114.09) * mm, "end": v(36.36, -114.2) * mm});
            skLineSegment(sketch, "E5840", {"start": v(36.36, -114.2) * mm, "end": v(36.54, -114.42) * mm});
            skLineSegment(sketch, "E5841", {"start": v(36.54, -114.42) * mm, "end": v(36.71, -114.64) * mm});
            skLineSegment(sketch, "E5842", {"start": v(36.71, -114.64) * mm, "end": v(36.9, -114.86) * mm});
            skLineSegment(sketch, "E5843", {"start": v(36.9, -114.86) * mm, "end": v(37, -114.97) * mm});
            skLineSegment(sketch, "E5844", {"start": v(37, -114.97) * mm, "end": v(37.09, -115.08) * mm});
            skLineSegment(sketch, "E5845", {"start": v(37.09, -115.08) * mm, "end": v(37.18, -115.2) * mm});
            skLineSegment(sketch, "E5846", {"start": v(37.18, -115.2) * mm, "end": v(37.28, -115.31) * mm});
            skLineSegment(sketch, "E5847", {"start": v(37.28, -115.31) * mm, "end": v(37.36, -115.37) * mm});
            skLineSegment(sketch, "E5848", {"start": v(37.36, -115.37) * mm, "end": v(38.94, -114.85) * mm});
            skLineSegment(sketch, "E5849", {"start": v(38.94, -114.85) * mm, "end": v(38.97, -114.75) * mm});
            skLineSegment(sketch, "E5850", {"start": v(38.97, -114.75) * mm, "end": v(38.98, -114.6) * mm});
            skLineSegment(sketch, "E5851", {"start": v(38.98, -114.6) * mm, "end": v(38.99, -114.46) * mm});
            skLineSegment(sketch, "E5852", {"start": v(38.99, -114.46) * mm, "end": v(39, -114.3) * mm});
            skLineSegment(sketch, "E5853", {"start": v(39, -114.3) * mm, "end": v(39, -114.16) * mm});
            skLineSegment(sketch, "E5854", {"start": v(39, -114.16) * mm, "end": v(39.02, -113.87) * mm});
            skLineSegment(sketch, "E5855", {"start": v(39.02, -113.87) * mm, "end": v(39.02, -113.73) * mm});
            skLineSegment(sketch, "E5856", {"start": v(39.02, -113.73) * mm, "end": v(39.03, -113.59) * mm});
            skLineSegment(sketch, "E5857", {"start": v(39.03, -113.59) * mm, "end": v(39.04, -113.45) * mm});
            skLineSegment(sketch, "E5858", {"start": v(39.04, -113.45) * mm, "end": v(39.04, -113.3) * mm});
            skLineSegment(sketch, "E5859", {"start": v(39.04, -113.3) * mm, "end": v(39.05, -113.03) * mm});
            skLineSegment(sketch, "E5860", {"start": v(39.05, -113.03) * mm, "end": v(39.05, -112.9) * mm});
            skLineSegment(sketch, "E5861", {"start": v(39.05, -112.9) * mm, "end": v(39.06, -112.76) * mm});
            skLineSegment(sketch, "E5862", {"start": v(39.06, -112.76) * mm, "end": v(39.06, -112.63) * mm});
            skLineSegment(sketch, "E5863", {"start": v(39.06, -112.63) * mm, "end": v(39.06, -112.5) * mm});
            skLineSegment(sketch, "E5864", {"start": v(39.06, -112.5) * mm, "end": v(39.06, -112.37) * mm});
            skLineSegment(sketch, "E5865", {"start": v(39.06, -112.37) * mm, "end": v(39.06, -112.24) * mm});
            skLineSegment(sketch, "E5866", {"start": v(39.06, -112.24) * mm, "end": v(39.07, -112.1) * mm});
            skLineSegment(sketch, "E5867", {"start": v(39.07, -112.1) * mm, "end": v(39.07, -111.6) * mm});
            skLineSegment(sketch, "E5868", {"start": v(39.07, -111.6) * mm, "end": v(39.06, -111.36) * mm});
            skLineSegment(sketch, "E5869", {"start": v(39.06, -111.36) * mm, "end": v(39.06, -111.24) * mm});
            skLineSegment(sketch, "E5870", {"start": v(39.06, -111.24) * mm, "end": v(39.06, -111.12) * mm});
            skLineSegment(sketch, "E5871", {"start": v(39.06, -111.12) * mm, "end": v(39.06, -111) * mm});
            skLineSegment(sketch, "E5872", {"start": v(39.06, -111) * mm, "end": v(39.05, -110.88) * mm});
            skLineSegment(sketch, "E5873", {"start": v(39.05, -110.88) * mm, "end": v(39.05, -110.77) * mm});
            skLineSegment(sketch, "E5874", {"start": v(39.05, -110.77) * mm, "end": v(39.05, -110.65) * mm});
            skLineSegment(sketch, "E5875", {"start": v(39.05, -110.65) * mm, "end": v(39.04, -110.42) * mm});
            skLineSegment(sketch, "E5876", {"start": v(39.04, -110.42) * mm, "end": v(39.03, -110.31) * mm});
            skLineSegment(sketch, "E5877", {"start": v(39.03, -110.31) * mm, "end": v(39.03, -110.2) * mm});
            skLineSegment(sketch, "E5878", {"start": v(39.03, -110.2) * mm, "end": v(39.02, -110.1) * mm});
            skLineSegment(sketch, "E5879", {"start": v(39.02, -110.1) * mm, "end": v(39.02, -109.99) * mm});
            skLineSegment(sketch, "E5880", {"start": v(39.02, -109.99) * mm, "end": v(39.86, -109.5) * mm});
            skLineSegment(sketch, "E5881", {"start": v(39.86, -109.5) * mm, "end": v(40.82, -109.33) * mm});
            skLineSegment(sketch, "E5882", {"start": v(40.82, -109.33) * mm, "end": v(41.02, -109.6) * mm});
            skLineSegment(sketch, "E5883", {"start": v(41.02, -109.6) * mm, "end": v(41.09, -109.68) * mm});
            skLineSegment(sketch, "E5884", {"start": v(41.09, -109.68) * mm, "end": v(41.23, -109.86) * mm});
            skLineSegment(sketch, "E5885", {"start": v(41.23, -109.86) * mm, "end": v(41.3, -109.95) * mm});
            skLineSegment(sketch, "E5886", {"start": v(41.3, -109.95) * mm, "end": v(41.37, -110.04) * mm});
            skLineSegment(sketch, "E5887", {"start": v(41.37, -110.04) * mm, "end": v(41.44, -110.13) * mm});
            skLineSegment(sketch, "E5888", {"start": v(41.44, -110.13) * mm, "end": v(41.52, -110.22) * mm});
            skLineSegment(sketch, "E5889", {"start": v(41.52, -110.22) * mm, "end": v(41.6, -110.32) * mm});
            skLineSegment(sketch, "E5890", {"start": v(41.6, -110.32) * mm, "end": v(41.67, -110.4) * mm});
            skLineSegment(sketch, "E5891", {"start": v(41.67, -110.4) * mm, "end": v(41.74, -110.5) * mm});
            skLineSegment(sketch, "E5892", {"start": v(41.74, -110.5) * mm, "end": v(41.82, -110.6) * mm});
            skLineSegment(sketch, "E5893", {"start": v(41.82, -110.6) * mm, "end": v(41.9, -110.7) * mm});
            skLineSegment(sketch, "E5894", {"start": v(41.9, -110.7) * mm, "end": v(42.06, -110.89) * mm});
            skLineSegment(sketch, "E5895", {"start": v(42.06, -110.89) * mm, "end": v(42.23, -111.08) * mm});
            skLineSegment(sketch, "E5896", {"start": v(42.23, -111.08) * mm, "end": v(42.4, -111.28) * mm});
            skLineSegment(sketch, "E5897", {"start": v(42.4, -111.28) * mm, "end": v(42.49, -111.38) * mm});
            skLineSegment(sketch, "E5898", {"start": v(42.49, -111.38) * mm, "end": v(42.58, -111.48) * mm});
            skLineSegment(sketch, "E5899", {"start": v(42.58, -111.48) * mm, "end": v(42.67, -111.58) * mm});
            skLineSegment(sketch, "E5900", {"start": v(42.67, -111.58) * mm, "end": v(42.75, -111.68) * mm});
            skLineSegment(sketch, "E5901", {"start": v(42.75, -111.68) * mm, "end": v(42.85, -111.79) * mm});
            skLineSegment(sketch, "E5902", {"start": v(42.85, -111.79) * mm, "end": v(42.94, -111.89) * mm});
            skLineSegment(sketch, "E5903", {"start": v(42.94, -111.89) * mm, "end": v(43.03, -112) * mm});
            skLineSegment(sketch, "E5904", {"start": v(43.03, -112) * mm, "end": v(43.22, -112.2) * mm});
            skLineSegment(sketch, "E5905", {"start": v(43.22, -112.2) * mm, "end": v(43.32, -112.3) * mm});
            skLineSegment(sketch, "E5906", {"start": v(43.32, -112.3) * mm, "end": v(43.42, -112.41) * mm});
            skLineSegment(sketch, "E5907", {"start": v(43.42, -112.41) * mm, "end": v(43.52, -112.52) * mm});
            skLineSegment(sketch, "E5908", {"start": v(43.52, -112.52) * mm, "end": v(43.62, -112.63) * mm});
            skLineSegment(sketch, "E5909", {"start": v(43.62, -112.63) * mm, "end": v(43.82, -112.84) * mm});
            skLineSegment(sketch, "E5910", {"start": v(43.82, -112.84) * mm, "end": v(43.92, -112.95) * mm});
            skLineSegment(sketch, "E5911", {"start": v(43.92, -112.95) * mm, "end": v(44, -113) * mm});
            skLineSegment(sketch, "E5912", {"start": v(44, -113) * mm, "end": v(45.55, -112.39) * mm});
            skLineSegment(sketch, "E5913", {"start": v(45.55, -112.39) * mm, "end": v(45.57, -112.3) * mm});
            skLineSegment(sketch, "E5914", {"start": v(45.57, -112.3) * mm, "end": v(45.58, -112) * mm});
            skLineSegment(sketch, "E5915", {"start": v(45.58, -112) * mm, "end": v(45.58, -111.7) * mm});
            skLineSegment(sketch, "E5916", {"start": v(45.58, -111.7) * mm, "end": v(45.57, -111.41) * mm});
            skLineSegment(sketch, "E5917", {"start": v(45.57, -111.41) * mm, "end": v(45.57, -111.27) * mm});
            skLineSegment(sketch, "E5918", {"start": v(45.57, -111.27) * mm, "end": v(45.56, -110.85) * mm});
            skLineSegment(sketch, "E5919", {"start": v(45.56, -110.85) * mm, "end": v(45.56, -110.7) * mm});
            skLineSegment(sketch, "E5920", {"start": v(45.56, -110.7) * mm, "end": v(45.55, -110.44) * mm});
            skLineSegment(sketch, "E5921", {"start": v(45.55, -110.44) * mm, "end": v(45.55, -110.3) * mm});
            skLineSegment(sketch, "E5922", {"start": v(45.55, -110.3) * mm, "end": v(45.54, -110.17) * mm});
            skLineSegment(sketch, "E5923", {"start": v(45.54, -110.17) * mm, "end": v(45.54, -110.03) * mm});
            skLineSegment(sketch, "E5924", {"start": v(45.54, -110.03) * mm, "end": v(45.53, -109.9) * mm});
            skLineSegment(sketch, "E5925", {"start": v(45.53, -109.9) * mm, "end": v(45.52, -109.77) * mm});
            skLineSegment(sketch, "E5926", {"start": v(45.52, -109.77) * mm, "end": v(45.51, -109.52) * mm});
            skLineSegment(sketch, "E5927", {"start": v(45.51, -109.52) * mm, "end": v(45.5, -109.4) * mm});
            skLineSegment(sketch, "E5928", {"start": v(45.5, -109.4) * mm, "end": v(45.5, -109.27) * mm});
            skLineSegment(sketch, "E5929", {"start": v(45.5, -109.27) * mm, "end": v(45.49, -109.14) * mm});
            skLineSegment(sketch, "E5930", {"start": v(45.49, -109.14) * mm, "end": v(45.48, -109.02) * mm});
            skLineSegment(sketch, "E5931", {"start": v(45.48, -109.02) * mm, "end": v(45.47, -108.9) * mm});
            skLineSegment(sketch, "E5932", {"start": v(45.47, -108.9) * mm, "end": v(45.45, -108.66) * mm});
            skLineSegment(sketch, "E5933", {"start": v(45.45, -108.66) * mm, "end": v(45.44, -108.54) * mm});
            skLineSegment(sketch, "E5934", {"start": v(45.44, -108.54) * mm, "end": v(45.43, -108.42) * mm});
            skLineSegment(sketch, "E5935", {"start": v(45.43, -108.42) * mm, "end": v(45.42, -108.3) * mm});
            skLineSegment(sketch, "E5936", {"start": v(45.42, -108.3) * mm, "end": v(45.41, -108.2) * mm});
            skLineSegment(sketch, "E5937", {"start": v(45.41, -108.2) * mm, "end": v(45.4, -107.97) * mm});
            skLineSegment(sketch, "E5938", {"start": v(45.4, -107.97) * mm, "end": v(45.37, -107.75) * mm});
            skLineSegment(sketch, "E5939", {"start": v(45.37, -107.75) * mm, "end": v(45.36, -107.64) * mm});
            skLineSegment(sketch, "E5940", {"start": v(45.36, -107.64) * mm, "end": v(45.35, -107.53) * mm});
            skLineSegment(sketch, "E5941", {"start": v(45.35, -107.53) * mm, "end": v(46.16, -107) * mm});
            skLineSegment(sketch, "E5942", {"start": v(46.16, -107) * mm, "end": v(47.1, -106.77) * mm});
            skLineSegment(sketch, "E5943", {"start": v(47.1, -106.77) * mm, "end": v(47.18, -106.85) * mm});
            skLineSegment(sketch, "E5944", {"start": v(47.18, -106.85) * mm, "end": v(47.25, -106.94) * mm});
            skLineSegment(sketch, "E5945", {"start": v(47.25, -106.94) * mm, "end": v(47.32, -107.02) * mm});
            skLineSegment(sketch, "E5946", {"start": v(47.32, -107.02) * mm, "end": v(47.4, -107.1) * mm});
            skLineSegment(sketch, "E5947", {"start": v(47.4, -107.1) * mm, "end": v(47.47, -107.19) * mm});
            skLineSegment(sketch, "E5948", {"start": v(47.47, -107.19) * mm, "end": v(47.54, -107.27) * mm});
            skLineSegment(sketch, "E5949", {"start": v(47.54, -107.27) * mm, "end": v(47.62, -107.36) * mm});
            skLineSegment(sketch, "E5950", {"start": v(47.62, -107.36) * mm, "end": v(47.7, -107.45) * mm});
            skLineSegment(sketch, "E5951", {"start": v(47.7, -107.45) * mm, "end": v(47.78, -107.54) * mm});
            skLineSegment(sketch, "E5952", {"start": v(47.78, -107.54) * mm, "end": v(47.94, -107.71) * mm});
            skLineSegment(sketch, "E5953", {"start": v(47.94, -107.71) * mm, "end": v(48.02, -107.8) * mm});
            skLineSegment(sketch, "E5954", {"start": v(48.02, -107.8) * mm, "end": v(48.1, -107.89) * mm});
            skLineSegment(sketch, "E5955", {"start": v(48.1, -107.89) * mm, "end": v(48.18, -107.98) * mm});
            skLineSegment(sketch, "E5956", {"start": v(48.18, -107.98) * mm, "end": v(48.35, -108.16) * mm});
            skLineSegment(sketch, "E5957", {"start": v(48.35, -108.16) * mm, "end": v(48.44, -108.25) * mm});
            skLineSegment(sketch, "E5958", {"start": v(48.44, -108.25) * mm, "end": v(48.53, -108.35) * mm});
            skLineSegment(sketch, "E5959", {"start": v(48.53, -108.35) * mm, "end": v(48.7, -108.53) * mm});
            skLineSegment(sketch, "E5960", {"start": v(48.7, -108.53) * mm, "end": v(48.8, -108.63) * mm});
            skLineSegment(sketch, "E5961", {"start": v(48.8, -108.63) * mm, "end": v(49.08, -108.91) * mm});
            skLineSegment(sketch, "E5962", {"start": v(49.08, -108.91) * mm, "end": v(49.18, -109) * mm});
            skLineSegment(sketch, "E5963", {"start": v(49.18, -109) * mm, "end": v(49.27, -109.1) * mm});
            skLineSegment(sketch, "E5964", {"start": v(49.27, -109.1) * mm, "end": v(49.37, -109.2) * mm});
            skLineSegment(sketch, "E5965", {"start": v(49.37, -109.2) * mm, "end": v(49.47, -109.3) * mm});
            skLineSegment(sketch, "E5966", {"start": v(49.47, -109.3) * mm, "end": v(49.57, -109.4) * mm});
            skLineSegment(sketch, "E5967", {"start": v(49.57, -109.4) * mm, "end": v(49.67, -109.5) * mm});
            skLineSegment(sketch, "E5968", {"start": v(49.67, -109.5) * mm, "end": v(49.78, -109.6) * mm});
            skLineSegment(sketch, "E5969", {"start": v(49.78, -109.6) * mm, "end": v(49.88, -109.7) * mm});
            skLineSegment(sketch, "E5970", {"start": v(49.88, -109.7) * mm, "end": v(50.1, -109.9) * mm});
            skLineSegment(sketch, "E5971", {"start": v(50.1, -109.9) * mm, "end": v(50.2, -110) * mm});
            skLineSegment(sketch, "E5972", {"start": v(50.2, -110) * mm, "end": v(50.42, -110.2) * mm});
            skLineSegment(sketch, "E5973", {"start": v(50.42, -110.2) * mm, "end": v(50.5, -110.25) * mm});
            skLineSegment(sketch, "E5974", {"start": v(50.5, -110.25) * mm, "end": v(52, -109.55) * mm});
            skLineSegment(sketch, "E5975", {"start": v(52, -109.55) * mm, "end": v(52.03, -109.45) * mm});
            skLineSegment(sketch, "E5976", {"start": v(52.03, -109.45) * mm, "end": v(52.02, -109.3) * mm});
            skLineSegment(sketch, "E5977", {"start": v(52.02, -109.3) * mm, "end": v(52.01, -109.16) * mm});
            skLineSegment(sketch, "E5978", {"start": v(52.01, -109.16) * mm, "end": v(52, -109) * mm});
            skLineSegment(sketch, "E5979", {"start": v(52, -109) * mm, "end": v(52, -108.86) * mm});
            skLineSegment(sketch, "E5980", {"start": v(52, -108.86) * mm, "end": v(51.97, -108.57) * mm});
            skLineSegment(sketch, "E5981", {"start": v(51.97, -108.57) * mm, "end": v(51.96, -108.43) * mm});
            skLineSegment(sketch, "E5982", {"start": v(51.96, -108.43) * mm, "end": v(51.95, -108.29) * mm});
            skLineSegment(sketch, "E5983", {"start": v(51.95, -108.29) * mm, "end": v(51.93, -108.01) * mm});
            skLineSegment(sketch, "E5984", {"start": v(51.93, -108.01) * mm, "end": v(51.92, -107.87) * mm});
            skLineSegment(sketch, "E5985", {"start": v(51.92, -107.87) * mm, "end": v(51.9, -107.74) * mm});
            skLineSegment(sketch, "E5986", {"start": v(51.9, -107.74) * mm, "end": v(51.9, -107.6) * mm});
            skLineSegment(sketch, "E5987", {"start": v(51.9, -107.6) * mm, "end": v(51.88, -107.47) * mm});
            skLineSegment(sketch, "E5988", {"start": v(51.88, -107.47) * mm, "end": v(51.86, -107.2) * mm});
            skLineSegment(sketch, "E5989", {"start": v(51.86, -107.2) * mm, "end": v(51.84, -107.07) * mm});
            skLineSegment(sketch, "E5990", {"start": v(51.84, -107.07) * mm, "end": v(51.83, -106.94) * mm});
            skLineSegment(sketch, "E5991", {"start": v(51.83, -106.94) * mm, "end": v(51.82, -106.81) * mm});
            skLineSegment(sketch, "E5992", {"start": v(51.82, -106.81) * mm, "end": v(51.8, -106.69) * mm});
            skLineSegment(sketch, "E5993", {"start": v(51.8, -106.69) * mm, "end": v(51.79, -106.56) * mm});
            skLineSegment(sketch, "E5994", {"start": v(51.79, -106.56) * mm, "end": v(51.76, -106.31) * mm});
            skLineSegment(sketch, "E5995", {"start": v(51.76, -106.31) * mm, "end": v(51.73, -106.07) * mm});
            skLineSegment(sketch, "E5996", {"start": v(51.73, -106.07) * mm, "end": v(51.71, -105.95) * mm});
            skLineSegment(sketch, "E5997", {"start": v(51.71, -105.95) * mm, "end": v(51.7, -105.83) * mm});
            skLineSegment(sketch, "E5998", {"start": v(51.7, -105.83) * mm, "end": v(51.68, -105.71) * mm});
            skLineSegment(sketch, "E5999", {"start": v(51.68, -105.71) * mm, "end": v(51.66, -105.6) * mm});
            skLineSegment(sketch, "E6000", {"start": v(51.66, -105.6) * mm, "end": v(51.64, -105.48) * mm});
            skLineSegment(sketch, "E6001", {"start": v(51.64, -105.48) * mm, "end": v(51.61, -105.26) * mm});
            skLineSegment(sketch, "E6002", {"start": v(51.61, -105.26) * mm, "end": v(51.58, -105.04) * mm});
            skLineSegment(sketch, "E6003", {"start": v(51.58, -105.04) * mm, "end": v(51.56, -104.93) * mm});
            skLineSegment(sketch, "E6004", {"start": v(51.56, -104.93) * mm, "end": v(51.54, -104.82) * mm});
            skLineSegment(sketch, "E6005", {"start": v(51.54, -104.82) * mm, "end": v(51.52, -104.71) * mm});
            skLineSegment(sketch, "E6006", {"start": v(51.52, -104.71) * mm, "end": v(52.3, -104.13) * mm});
            skLineSegment(sketch, "E6007", {"start": v(52.3, -104.13) * mm, "end": v(53.24, -103.85) * mm});
            skLineSegment(sketch, "E6008", {"start": v(53.24, -103.85) * mm, "end": v(53.31, -103.93) * mm});
            skLineSegment(sketch, "E6009", {"start": v(53.31, -103.93) * mm, "end": v(53.39, -104) * mm});
            skLineSegment(sketch, "E6010", {"start": v(53.39, -104) * mm, "end": v(53.46, -104.09) * mm});
            skLineSegment(sketch, "E6011", {"start": v(53.46, -104.09) * mm, "end": v(53.54, -104.17) * mm});
            skLineSegment(sketch, "E6012", {"start": v(53.54, -104.17) * mm, "end": v(53.62, -104.25) * mm});
            skLineSegment(sketch, "E6013", {"start": v(53.62, -104.25) * mm, "end": v(53.7, -104.33) * mm});
            skLineSegment(sketch, "E6014", {"start": v(53.7, -104.33) * mm, "end": v(53.78, -104.41) * mm});
            skLineSegment(sketch, "E6015", {"start": v(53.78, -104.41) * mm, "end": v(53.87, -104.5) * mm});
            skLineSegment(sketch, "E6016", {"start": v(53.87, -104.5) * mm, "end": v(53.95, -104.58) * mm});
            skLineSegment(sketch, "E6017", {"start": v(53.95, -104.58) * mm, "end": v(54.03, -104.66) * mm});
            skLineSegment(sketch, "E6018", {"start": v(54.03, -104.66) * mm, "end": v(54.12, -104.74) * mm});
            skLineSegment(sketch, "E6019", {"start": v(54.12, -104.74) * mm, "end": v(54.2, -104.83) * mm});
            skLineSegment(sketch, "E6020", {"start": v(54.2, -104.83) * mm, "end": v(54.3, -104.91) * mm});
            skLineSegment(sketch, "E6021", {"start": v(54.3, -104.91) * mm, "end": v(54.38, -105) * mm});
            skLineSegment(sketch, "E6022", {"start": v(54.38, -105) * mm, "end": v(54.47, -105.08) * mm});
            skLineSegment(sketch, "E6023", {"start": v(54.47, -105.08) * mm, "end": v(54.56, -105.17) * mm});
            skLineSegment(sketch, "E6024", {"start": v(54.56, -105.17) * mm, "end": v(54.65, -105.25) * mm});
            skLineSegment(sketch, "E6025", {"start": v(54.65, -105.25) * mm, "end": v(54.75, -105.34) * mm});
            skLineSegment(sketch, "E6026", {"start": v(54.75, -105.34) * mm, "end": v(54.84, -105.43) * mm});
            skLineSegment(sketch, "E6027", {"start": v(54.84, -105.43) * mm, "end": v(54.94, -105.52) * mm});
            skLineSegment(sketch, "E6028", {"start": v(54.94, -105.52) * mm, "end": v(55.03, -105.6) * mm});
            skLineSegment(sketch, "E6029", {"start": v(55.03, -105.6) * mm, "end": v(55.13, -105.7) * mm});
            skLineSegment(sketch, "E6030", {"start": v(55.13, -105.7) * mm, "end": v(55.23, -105.79) * mm});
            skLineSegment(sketch, "E6031", {"start": v(55.23, -105.79) * mm, "end": v(55.33, -105.88) * mm});
            skLineSegment(sketch, "E6032", {"start": v(55.33, -105.88) * mm, "end": v(55.43, -105.97) * mm});
            skLineSegment(sketch, "E6033", {"start": v(55.43, -105.97) * mm, "end": v(55.53, -106.06) * mm});
            skLineSegment(sketch, "E6034", {"start": v(55.53, -106.06) * mm, "end": v(55.64, -106.15) * mm});
            skLineSegment(sketch, "E6035", {"start": v(55.64, -106.15) * mm, "end": v(55.74, -106.24) * mm});
            skLineSegment(sketch, "E6036", {"start": v(55.74, -106.24) * mm, "end": v(55.85, -106.33) * mm});
            skLineSegment(sketch, "E6037", {"start": v(55.85, -106.33) * mm, "end": v(55.96, -106.43) * mm});
            skLineSegment(sketch, "E6038", {"start": v(55.96, -106.43) * mm, "end": v(56.06, -106.52) * mm});
            skLineSegment(sketch, "E6039", {"start": v(56.06, -106.52) * mm, "end": v(56.28, -106.7) * mm});
            skLineSegment(sketch, "E6040", {"start": v(56.28, -106.7) * mm, "end": v(56.4, -106.8) * mm});
            skLineSegment(sketch, "E6041", {"start": v(56.4, -106.8) * mm, "end": v(56.5, -106.9) * mm});
            skLineSegment(sketch, "E6042", {"start": v(56.5, -106.9) * mm, "end": v(56.62, -107) * mm});
            skLineSegment(sketch, "E6043", {"start": v(56.62, -107) * mm, "end": v(56.74, -107.09) * mm});
            skLineSegment(sketch, "E6044", {"start": v(56.74, -107.09) * mm, "end": v(56.83, -107.13) * mm});
            skLineSegment(sketch, "E6045", {"start": v(56.83, -107.13) * mm, "end": v(58.29, -106.34) * mm});
            skLineSegment(sketch, "E6046", {"start": v(58.29, -106.34) * mm, "end": v(58.3, -106.24) * mm});
            skLineSegment(sketch, "E6047", {"start": v(58.3, -106.24) * mm, "end": v(58.29, -106.1) * mm});
            skLineSegment(sketch, "E6048", {"start": v(58.29, -106.1) * mm, "end": v(58.25, -105.8) * mm});
            skLineSegment(sketch, "E6049", {"start": v(58.25, -105.8) * mm, "end": v(58.22, -105.51) * mm});
            skLineSegment(sketch, "E6050", {"start": v(58.22, -105.51) * mm, "end": v(58.2, -105.37) * mm});
            skLineSegment(sketch, "E6051", {"start": v(58.2, -105.37) * mm, "end": v(58.18, -105.23) * mm});
            skLineSegment(sketch, "E6052", {"start": v(58.18, -105.23) * mm, "end": v(58.16, -105.09) * mm});
            skLineSegment(sketch, "E6053", {"start": v(58.16, -105.09) * mm, "end": v(58.14, -104.95) * mm});
            skLineSegment(sketch, "E6054", {"start": v(58.14, -104.95) * mm, "end": v(58.12, -104.8) * mm});
            skLineSegment(sketch, "E6055", {"start": v(58.12, -104.8) * mm, "end": v(58.1, -104.67) * mm});
            skLineSegment(sketch, "E6056", {"start": v(58.1, -104.67) * mm, "end": v(58.08, -104.54) * mm});
            skLineSegment(sketch, "E6057", {"start": v(58.08, -104.54) * mm, "end": v(58.07, -104.4) * mm});
            skLineSegment(sketch, "E6058", {"start": v(58.07, -104.4) * mm, "end": v(58.04, -104.27) * mm});
            skLineSegment(sketch, "E6059", {"start": v(58.04, -104.27) * mm, "end": v(58.02, -104.14) * mm});
            skLineSegment(sketch, "E6060", {"start": v(58.02, -104.14) * mm, "end": v(58, -104) * mm});
            skLineSegment(sketch, "E6061", {"start": v(58, -104) * mm, "end": v(57.98, -103.88) * mm});
            skLineSegment(sketch, "E6062", {"start": v(57.98, -103.88) * mm, "end": v(57.96, -103.75) * mm});
            skLineSegment(sketch, "E6063", {"start": v(57.96, -103.75) * mm, "end": v(57.94, -103.62) * mm});
            skLineSegment(sketch, "E6064", {"start": v(57.94, -103.62) * mm, "end": v(57.9, -103.37) * mm});
            skLineSegment(sketch, "E6065", {"start": v(57.9, -103.37) * mm, "end": v(57.87, -103.25) * mm});
            skLineSegment(sketch, "E6066", {"start": v(57.87, -103.25) * mm, "end": v(57.83, -103) * mm});
            skLineSegment(sketch, "E6067", {"start": v(57.83, -103) * mm, "end": v(57.8, -102.88) * mm});
            skLineSegment(sketch, "E6068", {"start": v(57.8, -102.88) * mm, "end": v(57.78, -102.76) * mm});
            skLineSegment(sketch, "E6069", {"start": v(57.78, -102.76) * mm, "end": v(57.76, -102.65) * mm});
            skLineSegment(sketch, "E6070", {"start": v(57.76, -102.65) * mm, "end": v(57.74, -102.53) * mm});
            skLineSegment(sketch, "E6071", {"start": v(57.74, -102.53) * mm, "end": v(57.72, -102.42) * mm});
            skLineSegment(sketch, "E6072", {"start": v(57.72, -102.42) * mm, "end": v(57.67, -102.19) * mm});
            skLineSegment(sketch, "E6073", {"start": v(57.67, -102.19) * mm, "end": v(57.64, -102.08) * mm});
            skLineSegment(sketch, "E6074", {"start": v(57.64, -102.08) * mm, "end": v(57.62, -101.97) * mm});
            skLineSegment(sketch, "E6075", {"start": v(57.62, -101.97) * mm, "end": v(57.6, -101.86) * mm});
            skLineSegment(sketch, "E6076", {"start": v(57.6, -101.86) * mm, "end": v(57.57, -101.75) * mm});
            skLineSegment(sketch, "E6077", {"start": v(57.57, -101.75) * mm, "end": v(57.55, -101.65) * mm});
            skLineSegment(sketch, "E6078", {"start": v(57.55, -101.65) * mm, "end": v(57.52, -101.54) * mm});
            skLineSegment(sketch, "E6079", {"start": v(57.52, -101.54) * mm, "end": v(58.27, -100.91) * mm});
            skLineSegment(sketch, "E6080", {"start": v(58.27, -100.91) * mm, "end": v(59.19, -100.58) * mm});
            skLineSegment(sketch, "E6081", {"start": v(59.19, -100.58) * mm, "end": v(59.27, -100.65) * mm});
            skLineSegment(sketch, "E6082", {"start": v(59.27, -100.65) * mm, "end": v(59.35, -100.73) * mm});
            skLineSegment(sketch, "E6083", {"start": v(59.35, -100.73) * mm, "end": v(59.5, -100.88) * mm});
            skLineSegment(sketch, "E6084", {"start": v(59.5, -100.88) * mm, "end": v(59.68, -101.03) * mm});
            skLineSegment(sketch, "E6085", {"start": v(59.68, -101.03) * mm, "end": v(59.76, -101.1) * mm});
            skLineSegment(sketch, "E6086", {"start": v(59.76, -101.1) * mm, "end": v(59.85, -101.18) * mm});
            skLineSegment(sketch, "E6087", {"start": v(59.85, -101.18) * mm, "end": v(59.94, -101.26) * mm});
            skLineSegment(sketch, "E6088", {"start": v(59.94, -101.26) * mm, "end": v(60.12, -101.42) * mm});
            skLineSegment(sketch, "E6089", {"start": v(60.12, -101.42) * mm, "end": v(60.2, -101.5) * mm});
            skLineSegment(sketch, "E6090", {"start": v(60.2, -101.5) * mm, "end": v(60.3, -101.58) * mm});
            skLineSegment(sketch, "E6091", {"start": v(60.3, -101.58) * mm, "end": v(60.4, -101.66) * mm});
            skLineSegment(sketch, "E6092", {"start": v(60.4, -101.66) * mm, "end": v(60.49, -101.74) * mm});
            skLineSegment(sketch, "E6093", {"start": v(60.49, -101.74) * mm, "end": v(60.68, -101.9) * mm});
            skLineSegment(sketch, "E6094", {"start": v(60.68, -101.9) * mm, "end": v(60.78, -101.98) * mm});
            skLineSegment(sketch, "E6095", {"start": v(60.78, -101.98) * mm, "end": v(61.08, -102.23) * mm});
            skLineSegment(sketch, "E6096", {"start": v(61.08, -102.23) * mm, "end": v(61.18, -102.31) * mm});
            skLineSegment(sketch, "E6097", {"start": v(61.18, -102.31) * mm, "end": v(61.4, -102.48) * mm});
            skLineSegment(sketch, "E6098", {"start": v(61.4, -102.48) * mm, "end": v(61.5, -102.56) * mm});
            skLineSegment(sketch, "E6099", {"start": v(61.5, -102.56) * mm, "end": v(61.6, -102.65) * mm});
            skLineSegment(sketch, "E6100", {"start": v(61.6, -102.65) * mm, "end": v(61.72, -102.73) * mm});
            skLineSegment(sketch, "E6101", {"start": v(61.72, -102.73) * mm, "end": v(61.83, -102.82) * mm});
            skLineSegment(sketch, "E6102", {"start": v(61.83, -102.82) * mm, "end": v(61.94, -102.9) * mm});
            skLineSegment(sketch, "E6103", {"start": v(61.94, -102.9) * mm, "end": v(62.05, -103) * mm});
            skLineSegment(sketch, "E6104", {"start": v(62.05, -103) * mm, "end": v(62.28, -103.17) * mm});
            skLineSegment(sketch, "E6105", {"start": v(62.28, -103.17) * mm, "end": v(62.4, -103.25) * mm});
            skLineSegment(sketch, "E6106", {"start": v(62.4, -103.25) * mm, "end": v(62.51, -103.34) * mm});
            skLineSegment(sketch, "E6107", {"start": v(62.51, -103.34) * mm, "end": v(62.63, -103.43) * mm});
            skLineSegment(sketch, "E6108", {"start": v(62.63, -103.43) * mm, "end": v(62.75, -103.52) * mm});
            skLineSegment(sketch, "E6109", {"start": v(62.75, -103.52) * mm, "end": v(62.87, -103.6) * mm});
            skLineSegment(sketch, "E6110", {"start": v(62.87, -103.6) * mm, "end": v(62.96, -103.64) * mm});
            skLineSegment(sketch, "E6111", {"start": v(62.96, -103.64) * mm, "end": v(64.37, -102.77) * mm});
            skLineSegment(sketch, "E6112", {"start": v(64.37, -102.77) * mm, "end": v(64.38, -102.67) * mm});
            skLineSegment(sketch, "E6113", {"start": v(64.38, -102.67) * mm, "end": v(64.36, -102.53) * mm});
            skLineSegment(sketch, "E6114", {"start": v(64.36, -102.53) * mm, "end": v(64.33, -102.38) * mm});
            skLineSegment(sketch, "E6115", {"start": v(64.33, -102.38) * mm, "end": v(64.3, -102.23) * mm});
            skLineSegment(sketch, "E6116", {"start": v(64.3, -102.23) * mm, "end": v(64.28, -102.1) * mm});
            skLineSegment(sketch, "E6117", {"start": v(64.28, -102.1) * mm, "end": v(64.25, -101.95) * mm});
            skLineSegment(sketch, "E6118", {"start": v(64.25, -101.95) * mm, "end": v(64.23, -101.8) * mm});
            skLineSegment(sketch, "E6119", {"start": v(64.23, -101.8) * mm, "end": v(64.2, -101.66) * mm});
            skLineSegment(sketch, "E6120", {"start": v(64.2, -101.66) * mm, "end": v(64.17, -101.53) * mm});
            skLineSegment(sketch, "E6121", {"start": v(64.17, -101.53) * mm, "end": v(64.15, -101.39) * mm});
            skLineSegment(sketch, "E6122", {"start": v(64.15, -101.39) * mm, "end": v(64.12, -101.25) * mm});
            skLineSegment(sketch, "E6123", {"start": v(64.12, -101.25) * mm, "end": v(64.07, -100.98) * mm});
            skLineSegment(sketch, "E6124", {"start": v(64.07, -100.98) * mm, "end": v(64.04, -100.85) * mm});
            skLineSegment(sketch, "E6125", {"start": v(64.04, -100.85) * mm, "end": v(64, -100.72) * mm});
            skLineSegment(sketch, "E6126", {"start": v(64, -100.72) * mm, "end": v(63.98, -100.59) * mm});
            skLineSegment(sketch, "E6127", {"start": v(63.98, -100.59) * mm, "end": v(63.95, -100.46) * mm});
            skLineSegment(sketch, "E6128", {"start": v(63.95, -100.46) * mm, "end": v(63.92, -100.33) * mm});
            skLineSegment(sketch, "E6129", {"start": v(63.92, -100.33) * mm, "end": v(63.9, -100.2) * mm});
            skLineSegment(sketch, "E6130", {"start": v(63.9, -100.2) * mm, "end": v(63.87, -100.08) * mm});
            skLineSegment(sketch, "E6131", {"start": v(63.87, -100.08) * mm, "end": v(63.8, -99.83) * mm});
            skLineSegment(sketch, "E6132", {"start": v(63.8, -99.83) * mm, "end": v(63.78, -99.7) * mm});
            skLineSegment(sketch, "E6133", {"start": v(63.78, -99.7) * mm, "end": v(63.75, -99.59) * mm});
            skLineSegment(sketch, "E6134", {"start": v(63.75, -99.59) * mm, "end": v(63.72, -99.47) * mm});
            skLineSegment(sketch, "E6135", {"start": v(63.72, -99.47) * mm, "end": v(63.7, -99.35) * mm});
            skLineSegment(sketch, "E6136", {"start": v(63.7, -99.35) * mm, "end": v(63.66, -99.23) * mm});
            skLineSegment(sketch, "E6137", {"start": v(63.66, -99.23) * mm, "end": v(63.63, -99.12) * mm});
            skLineSegment(sketch, "E6138", {"start": v(63.63, -99.12) * mm, "end": v(63.57, -98.89) * mm});
            skLineSegment(sketch, "E6139", {"start": v(63.57, -98.89) * mm, "end": v(63.54, -98.78) * mm});
            skLineSegment(sketch, "E6140", {"start": v(63.54, -98.78) * mm, "end": v(63.51, -98.66) * mm});
            skLineSegment(sketch, "E6141", {"start": v(63.51, -98.66) * mm, "end": v(63.45, -98.45) * mm});
            skLineSegment(sketch, "E6142", {"start": v(63.45, -98.45) * mm, "end": v(63.42, -98.34) * mm});
            skLineSegment(sketch, "E6143", {"start": v(63.42, -98.34) * mm, "end": v(63.4, -98.23) * mm});
            skLineSegment(sketch, "E6144", {"start": v(63.4, -98.23) * mm, "end": v(63.36, -98.13) * mm});
            skLineSegment(sketch, "E6145", {"start": v(63.36, -98.13) * mm, "end": v(63.33, -98.02) * mm});
            skLineSegment(sketch, "E6146", {"start": v(63.33, -98.02) * mm, "end": v(64.04, -97.35) * mm});
            skLineSegment(sketch, "E6147", {"start": v(64.04, -97.35) * mm, "end": v(64.93, -96.97) * mm});
            skLineSegment(sketch, "E6148", {"start": v(64.93, -96.97) * mm, "end": v(65.02, -97.04) * mm});
            skLineSegment(sketch, "E6149", {"start": v(65.02, -97.04) * mm, "end": v(65.1, -97.1) * mm});
            skLineSegment(sketch, "E6150", {"start": v(65.1, -97.1) * mm, "end": v(65.19, -97.18) * mm});
            skLineSegment(sketch, "E6151", {"start": v(65.19, -97.18) * mm, "end": v(65.36, -97.32) * mm});
            skLineSegment(sketch, "E6152", {"start": v(65.36, -97.32) * mm, "end": v(65.45, -97.39) * mm});
            skLineSegment(sketch, "E6153", {"start": v(65.45, -97.39) * mm, "end": v(65.54, -97.46) * mm});
            skLineSegment(sketch, "E6154", {"start": v(65.54, -97.46) * mm, "end": v(65.63, -97.53) * mm});
            skLineSegment(sketch, "E6155", {"start": v(65.63, -97.53) * mm, "end": v(65.72, -97.6) * mm});
            skLineSegment(sketch, "E6156", {"start": v(65.72, -97.6) * mm, "end": v(65.82, -97.68) * mm});
            skLineSegment(sketch, "E6157", {"start": v(65.82, -97.68) * mm, "end": v(66, -97.82) * mm});
            skLineSegment(sketch, "E6158", {"start": v(66, -97.82) * mm, "end": v(66.1, -97.9) * mm});
            skLineSegment(sketch, "E6159", {"start": v(66.1, -97.9) * mm, "end": v(66.3, -98.05) * mm});
            skLineSegment(sketch, "E6160", {"start": v(66.3, -98.05) * mm, "end": v(66.4, -98.12) * mm});
            skLineSegment(sketch, "E6161", {"start": v(66.4, -98.12) * mm, "end": v(66.5, -98.2) * mm});
            skLineSegment(sketch, "E6162", {"start": v(66.5, -98.2) * mm, "end": v(66.6, -98.27) * mm});
            skLineSegment(sketch, "E6163", {"start": v(66.6, -98.27) * mm, "end": v(66.7, -98.35) * mm});
            skLineSegment(sketch, "E6164", {"start": v(66.7, -98.35) * mm, "end": v(66.82, -98.43) * mm});
            skLineSegment(sketch, "E6165", {"start": v(66.82, -98.43) * mm, "end": v(66.92, -98.5) * mm});
            skLineSegment(sketch, "E6166", {"start": v(66.92, -98.5) * mm, "end": v(67.03, -98.58) * mm});
            skLineSegment(sketch, "E6167", {"start": v(67.03, -98.58) * mm, "end": v(67.14, -98.66) * mm});
            skLineSegment(sketch, "E6168", {"start": v(67.14, -98.66) * mm, "end": v(67.36, -98.81) * mm});
            skLineSegment(sketch, "E6169", {"start": v(67.36, -98.81) * mm, "end": v(67.58, -98.97) * mm});
            skLineSegment(sketch, "E6170", {"start": v(67.58, -98.97) * mm, "end": v(67.7, -99.05) * mm});
            skLineSegment(sketch, "E6171", {"start": v(67.7, -99.05) * mm, "end": v(67.82, -99.13) * mm});
            skLineSegment(sketch, "E6172", {"start": v(67.82, -99.13) * mm, "end": v(67.93, -99.21) * mm});
            skLineSegment(sketch, "E6173", {"start": v(67.93, -99.21) * mm, "end": v(68.05, -99.3) * mm});
            skLineSegment(sketch, "E6174", {"start": v(68.05, -99.3) * mm, "end": v(68.3, -99.45) * mm});
            skLineSegment(sketch, "E6175", {"start": v(68.3, -99.45) * mm, "end": v(68.41, -99.53) * mm});
            skLineSegment(sketch, "E6176", {"start": v(68.41, -99.53) * mm, "end": v(68.66, -99.7) * mm});
            skLineSegment(sketch, "E6177", {"start": v(68.66, -99.7) * mm, "end": v(68.79, -99.78) * mm});
            skLineSegment(sketch, "E6178", {"start": v(68.79, -99.78) * mm, "end": v(68.88, -99.8) * mm});
            skLineSegment(sketch, "E6179", {"start": v(68.88, -99.8) * mm, "end": v(70.24, -98.85) * mm});
            skLineSegment(sketch, "E6180", {"start": v(70.24, -98.85) * mm, "end": v(70.24, -98.76) * mm});
            skLineSegment(sketch, "E6181", {"start": v(70.24, -98.76) * mm, "end": v(70.2, -98.61) * mm});
            skLineSegment(sketch, "E6182", {"start": v(70.2, -98.61) * mm, "end": v(70.18, -98.47) * mm});
            skLineSegment(sketch, "E6183", {"start": v(70.18, -98.47) * mm, "end": v(70.1, -98.18) * mm});
            skLineSegment(sketch, "E6184", {"start": v(70.1, -98.18) * mm, "end": v(70.07, -98.04) * mm});
            skLineSegment(sketch, "E6185", {"start": v(70.07, -98.04) * mm, "end": v(70.04, -97.9) * mm});
            skLineSegment(sketch, "E6186", {"start": v(70.04, -97.9) * mm, "end": v(69.97, -97.62) * mm});
            skLineSegment(sketch, "E6187", {"start": v(69.97, -97.62) * mm, "end": v(69.93, -97.49) * mm});
            skLineSegment(sketch, "E6188", {"start": v(69.93, -97.49) * mm, "end": v(69.9, -97.35) * mm});
            skLineSegment(sketch, "E6189", {"start": v(69.9, -97.35) * mm, "end": v(69.86, -97.22) * mm});
            skLineSegment(sketch, "E6190", {"start": v(69.86, -97.22) * mm, "end": v(69.83, -97.09) * mm});
            skLineSegment(sketch, "E6191", {"start": v(69.83, -97.09) * mm, "end": v(69.76, -96.82) * mm});
            skLineSegment(sketch, "E6192", {"start": v(69.76, -96.82) * mm, "end": v(69.72, -96.7) * mm});
            skLineSegment(sketch, "E6193", {"start": v(69.72, -96.7) * mm, "end": v(69.69, -96.57) * mm});
            skLineSegment(sketch, "E6194", {"start": v(69.69, -96.57) * mm, "end": v(69.65, -96.44) * mm});
            skLineSegment(sketch, "E6195", {"start": v(69.65, -96.44) * mm, "end": v(69.61, -96.32) * mm});
            skLineSegment(sketch, "E6196", {"start": v(69.61, -96.32) * mm, "end": v(69.58, -96.2) * mm});
            skLineSegment(sketch, "E6197", {"start": v(69.58, -96.2) * mm, "end": v(69.54, -96.07) * mm});
            skLineSegment(sketch, "E6198", {"start": v(69.54, -96.07) * mm, "end": v(69.5, -95.95) * mm});
            skLineSegment(sketch, "E6199", {"start": v(69.5, -95.95) * mm, "end": v(69.47, -95.83) * mm});
            skLineSegment(sketch, "E6200", {"start": v(69.47, -95.83) * mm, "end": v(69.43, -95.71) * mm});
            skLineSegment(sketch, "E6201", {"start": v(69.43, -95.71) * mm, "end": v(69.4, -95.6) * mm});
            skLineSegment(sketch, "E6202", {"start": v(69.4, -95.6) * mm, "end": v(69.36, -95.48) * mm});
            skLineSegment(sketch, "E6203", {"start": v(69.36, -95.48) * mm, "end": v(69.32, -95.36) * mm});
            skLineSegment(sketch, "E6204", {"start": v(69.32, -95.36) * mm, "end": v(69.29, -95.25) * mm});
            skLineSegment(sketch, "E6205", {"start": v(69.29, -95.25) * mm, "end": v(69.25, -95.13) * mm});
            skLineSegment(sketch, "E6206", {"start": v(69.25, -95.13) * mm, "end": v(69.21, -95.02) * mm});
            skLineSegment(sketch, "E6207", {"start": v(69.21, -95.02) * mm, "end": v(69.18, -94.91) * mm});
            skLineSegment(sketch, "E6208", {"start": v(69.18, -94.91) * mm, "end": v(69.14, -94.8) * mm});
            skLineSegment(sketch, "E6209", {"start": v(69.14, -94.8) * mm, "end": v(69.1, -94.7) * mm});
            skLineSegment(sketch, "E6210", {"start": v(69.1, -94.7) * mm, "end": v(69.07, -94.59) * mm});
            skLineSegment(sketch, "E6211", {"start": v(69.07, -94.59) * mm, "end": v(69.03, -94.49) * mm});
            skLineSegment(sketch, "E6212", {"start": v(69.03, -94.49) * mm, "end": v(69, -94.38) * mm});
            skLineSegment(sketch, "E6213", {"start": v(69, -94.38) * mm, "end": v(68.96, -94.28) * mm});
            skLineSegment(sketch, "E6214", {"start": v(68.96, -94.28) * mm, "end": v(68.92, -94.18) * mm});
            skLineSegment(sketch, "E6215", {"start": v(68.92, -94.18) * mm, "end": v(69.59, -93.47) * mm});
            skLineSegment(sketch, "E6216", {"start": v(69.59, -93.47) * mm, "end": v(70.46, -93.03) * mm});
            skLineSegment(sketch, "E6217", {"start": v(70.46, -93.03) * mm, "end": v(70.55, -93.1) * mm});
            skLineSegment(sketch, "E6218", {"start": v(70.55, -93.1) * mm, "end": v(70.64, -93.16) * mm});
            skLineSegment(sketch, "E6219", {"start": v(70.64, -93.16) * mm, "end": v(70.73, -93.22) * mm});
            skLineSegment(sketch, "E6220", {"start": v(70.73, -93.22) * mm, "end": v(70.82, -93.29) * mm});
            skLineSegment(sketch, "E6221", {"start": v(70.82, -93.29) * mm, "end": v(70.9, -93.35) * mm});
            skLineSegment(sketch, "E6222", {"start": v(70.9, -93.35) * mm, "end": v(71, -93.42) * mm});
            skLineSegment(sketch, "E6223", {"start": v(71, -93.42) * mm, "end": v(71.1, -93.48) * mm});
            skLineSegment(sketch, "E6224", {"start": v(71.1, -93.48) * mm, "end": v(71.2, -93.55) * mm});
            skLineSegment(sketch, "E6225", {"start": v(71.2, -93.55) * mm, "end": v(71.29, -93.62) * mm});
            skLineSegment(sketch, "E6226", {"start": v(71.29, -93.62) * mm, "end": v(71.48, -93.75) * mm});
            skLineSegment(sketch, "E6227", {"start": v(71.48, -93.75) * mm, "end": v(71.58, -93.82) * mm});
            skLineSegment(sketch, "E6228", {"start": v(71.58, -93.82) * mm, "end": v(71.68, -93.89) * mm});
            skLineSegment(sketch, "E6229", {"start": v(71.68, -93.89) * mm, "end": v(71.79, -93.96) * mm});
            skLineSegment(sketch, "E6230", {"start": v(71.79, -93.96) * mm, "end": v(71.89, -94.03) * mm});
            skLineSegment(sketch, "E6231", {"start": v(71.89, -94.03) * mm, "end": v(72, -94.1) * mm});
            skLineSegment(sketch, "E6232", {"start": v(72, -94.1) * mm, "end": v(72.1, -94.17) * mm});
            skLineSegment(sketch, "E6233", {"start": v(72.1, -94.17) * mm, "end": v(72.2, -94.23) * mm});
            skLineSegment(sketch, "E6234", {"start": v(72.2, -94.23) * mm, "end": v(72.32, -94.3) * mm});
            skLineSegment(sketch, "E6235", {"start": v(72.32, -94.3) * mm, "end": v(72.54, -94.45) * mm});
            skLineSegment(sketch, "E6236", {"start": v(72.54, -94.45) * mm, "end": v(72.65, -94.52) * mm});
            skLineSegment(sketch, "E6237", {"start": v(72.65, -94.52) * mm, "end": v(72.76, -94.59) * mm});
            skLineSegment(sketch, "E6238", {"start": v(72.76, -94.59) * mm, "end": v(72.87, -94.66) * mm});
            skLineSegment(sketch, "E6239", {"start": v(72.87, -94.66) * mm, "end": v(73, -94.73) * mm});
            skLineSegment(sketch, "E6240", {"start": v(73, -94.73) * mm, "end": v(73.1, -94.8) * mm});
            skLineSegment(sketch, "E6241", {"start": v(73.1, -94.8) * mm, "end": v(73.22, -94.88) * mm});
            skLineSegment(sketch, "E6242", {"start": v(73.22, -94.88) * mm, "end": v(73.34, -94.95) * mm});
            skLineSegment(sketch, "E6243", {"start": v(73.34, -94.95) * mm, "end": v(73.46, -95.02) * mm});
            skLineSegment(sketch, "E6244", {"start": v(73.46, -95.02) * mm, "end": v(73.59, -95.1) * mm});
            skLineSegment(sketch, "E6245", {"start": v(73.59, -95.1) * mm, "end": v(73.83, -95.24) * mm});
            skLineSegment(sketch, "E6246", {"start": v(73.83, -95.24) * mm, "end": v(73.96, -95.31) * mm});
            skLineSegment(sketch, "E6247", {"start": v(73.96, -95.31) * mm, "end": v(74.09, -95.39) * mm});
            skLineSegment(sketch, "E6248", {"start": v(74.09, -95.39) * mm, "end": v(74.21, -95.46) * mm});
            skLineSegment(sketch, "E6249", {"start": v(74.21, -95.46) * mm, "end": v(74.34, -95.53) * mm});
            skLineSegment(sketch, "E6250", {"start": v(74.34, -95.53) * mm, "end": v(74.47, -95.6) * mm});
            skLineSegment(sketch, "E6251", {"start": v(74.47, -95.6) * mm, "end": v(74.57, -95.63) * mm});
            skLineSegment(sketch, "E6252", {"start": v(74.57, -95.63) * mm, "end": v(75.87, -94.6) * mm});
            skLineSegment(sketch, "E6253", {"start": v(75.87, -94.6) * mm, "end": v(75.87, -94.5) * mm});
            skLineSegment(sketch, "E6254", {"start": v(75.87, -94.5) * mm, "end": v(75.82, -94.36) * mm});
            skLineSegment(sketch, "E6255", {"start": v(75.82, -94.36) * mm, "end": v(75.78, -94.22) * mm});
            skLineSegment(sketch, "E6256", {"start": v(75.78, -94.22) * mm, "end": v(75.74, -94.08) * mm});
            skLineSegment(sketch, "E6257", {"start": v(75.74, -94.08) * mm, "end": v(75.65, -93.8) * mm});
            skLineSegment(sketch, "E6258", {"start": v(75.65, -93.8) * mm, "end": v(75.61, -93.66) * mm});
            skLineSegment(sketch, "E6259", {"start": v(75.61, -93.66) * mm, "end": v(75.57, -93.52) * mm});
            skLineSegment(sketch, "E6260", {"start": v(75.57, -93.52) * mm, "end": v(75.53, -93.39) * mm});
            skLineSegment(sketch, "E6261", {"start": v(75.53, -93.39) * mm, "end": v(75.44, -93.12) * mm});
            skLineSegment(sketch, "E6262", {"start": v(75.44, -93.12) * mm, "end": v(75.36, -92.86) * mm});
            skLineSegment(sketch, "E6263", {"start": v(75.36, -92.86) * mm, "end": v(75.31, -92.73) * mm});
            skLineSegment(sketch, "E6264", {"start": v(75.31, -92.73) * mm, "end": v(75.27, -92.6) * mm});
            skLineSegment(sketch, "E6265", {"start": v(75.27, -92.6) * mm, "end": v(75.23, -92.48) * mm});
            skLineSegment(sketch, "E6266", {"start": v(75.23, -92.48) * mm, "end": v(75.18, -92.35) * mm});
            skLineSegment(sketch, "E6267", {"start": v(75.18, -92.35) * mm, "end": v(75.14, -92.23) * mm});
            skLineSegment(sketch, "E6268", {"start": v(75.14, -92.23) * mm, "end": v(75.05, -91.98) * mm});
            skLineSegment(sketch, "E6269", {"start": v(75.05, -91.98) * mm, "end": v(75, -91.86) * mm});
            skLineSegment(sketch, "E6270", {"start": v(75, -91.86) * mm, "end": v(74.92, -91.63) * mm});
            skLineSegment(sketch, "E6271", {"start": v(74.92, -91.63) * mm, "end": v(74.88, -91.51) * mm});
            skLineSegment(sketch, "E6272", {"start": v(74.88, -91.51) * mm, "end": v(74.84, -91.4) * mm});
            skLineSegment(sketch, "E6273", {"start": v(74.84, -91.4) * mm, "end": v(74.8, -91.28) * mm});
            skLineSegment(sketch, "E6274", {"start": v(74.8, -91.28) * mm, "end": v(74.75, -91.17) * mm});
            skLineSegment(sketch, "E6275", {"start": v(74.75, -91.17) * mm, "end": v(74.7, -91.06) * mm});
            skLineSegment(sketch, "E6276", {"start": v(74.7, -91.06) * mm, "end": v(74.62, -90.84) * mm});
            skLineSegment(sketch, "E6277", {"start": v(74.62, -90.84) * mm, "end": v(74.58, -90.73) * mm});
            skLineSegment(sketch, "E6278", {"start": v(74.58, -90.73) * mm, "end": v(74.5, -90.52) * mm});
            skLineSegment(sketch, "E6279", {"start": v(74.5, -90.52) * mm, "end": v(74.45, -90.41) * mm});
            skLineSegment(sketch, "E6280", {"start": v(74.45, -90.41) * mm, "end": v(74.41, -90.31) * mm});
            skLineSegment(sketch, "E6281", {"start": v(74.41, -90.31) * mm, "end": v(74.37, -90.2) * mm});
            skLineSegment(sketch, "E6282", {"start": v(74.37, -90.2) * mm, "end": v(74.32, -90.1) * mm});
            skLineSegment(sketch, "E6283", {"start": v(74.32, -90.1) * mm, "end": v(74.28, -90) * mm});
            skLineSegment(sketch, "E6284", {"start": v(74.28, -90) * mm, "end": v(74.9, -89.26) * mm});
            skLineSegment(sketch, "E6285", {"start": v(74.9, -89.26) * mm, "end": v(75.75, -88.78) * mm});
            skLineSegment(sketch, "E6286", {"start": v(75.75, -88.78) * mm, "end": v(75.84, -88.84) * mm});
            skLineSegment(sketch, "E6287", {"start": v(75.84, -88.84) * mm, "end": v(75.93, -88.9) * mm});
            skLineSegment(sketch, "E6288", {"start": v(75.93, -88.9) * mm, "end": v(76.03, -88.95) * mm});
            skLineSegment(sketch, "E6289", {"start": v(76.03, -88.95) * mm, "end": v(76.12, -89.01) * mm});
            skLineSegment(sketch, "E6290", {"start": v(76.12, -89.01) * mm, "end": v(76.22, -89.07) * mm});
            skLineSegment(sketch, "E6291", {"start": v(76.22, -89.07) * mm, "end": v(76.31, -89.13) * mm});
            skLineSegment(sketch, "E6292", {"start": v(76.31, -89.13) * mm, "end": v(76.41, -89.2) * mm});
            skLineSegment(sketch, "E6293", {"start": v(76.41, -89.2) * mm, "end": v(76.6, -89.31) * mm});
            skLineSegment(sketch, "E6294", {"start": v(76.6, -89.31) * mm, "end": v(76.81, -89.44) * mm});
            skLineSegment(sketch, "E6295", {"start": v(76.81, -89.44) * mm, "end": v(76.92, -89.5) * mm});
            skLineSegment(sketch, "E6296", {"start": v(76.92, -89.5) * mm, "end": v(77.02, -89.56) * mm});
            skLineSegment(sketch, "E6297", {"start": v(77.02, -89.56) * mm, "end": v(77.13, -89.62) * mm});
            skLineSegment(sketch, "E6298", {"start": v(77.13, -89.62) * mm, "end": v(77.24, -89.69) * mm});
            skLineSegment(sketch, "E6299", {"start": v(77.24, -89.69) * mm, "end": v(77.34, -89.75) * mm});
            skLineSegment(sketch, "E6300", {"start": v(77.34, -89.75) * mm, "end": v(77.56, -89.88) * mm});
            skLineSegment(sketch, "E6301", {"start": v(77.56, -89.88) * mm, "end": v(77.68, -89.94) * mm});
            skLineSegment(sketch, "E6302", {"start": v(77.68, -89.94) * mm, "end": v(77.8, -90) * mm});
            skLineSegment(sketch, "E6303", {"start": v(77.8, -90) * mm, "end": v(77.9, -90.07) * mm});
            skLineSegment(sketch, "E6304", {"start": v(77.9, -90.07) * mm, "end": v(78.02, -90.13) * mm});
            skLineSegment(sketch, "E6305", {"start": v(78.02, -90.13) * mm, "end": v(78.14, -90.2) * mm});
            skLineSegment(sketch, "E6306", {"start": v(78.14, -90.2) * mm, "end": v(78.37, -90.33) * mm});
            skLineSegment(sketch, "E6307", {"start": v(78.37, -90.33) * mm, "end": v(78.5, -90.4) * mm});
            skLineSegment(sketch, "E6308", {"start": v(78.5, -90.4) * mm, "end": v(78.62, -90.46) * mm});
            skLineSegment(sketch, "E6309", {"start": v(78.62, -90.46) * mm, "end": v(78.87, -90.59) * mm});
            skLineSegment(sketch, "E6310", {"start": v(78.87, -90.59) * mm, "end": v(79, -90.65) * mm});
            skLineSegment(sketch, "E6311", {"start": v(79, -90.65) * mm, "end": v(79.12, -90.72) * mm});
            skLineSegment(sketch, "E6312", {"start": v(79.12, -90.72) * mm, "end": v(79.25, -90.78) * mm});
            skLineSegment(sketch, "E6313", {"start": v(79.25, -90.78) * mm, "end": v(79.5, -90.92) * mm});
            skLineSegment(sketch, "E6314", {"start": v(79.5, -90.92) * mm, "end": v(79.64, -90.98) * mm});
            skLineSegment(sketch, "E6315", {"start": v(79.64, -90.98) * mm, "end": v(79.9, -91.11) * mm});
            skLineSegment(sketch, "E6316", {"start": v(79.9, -91.11) * mm, "end": v(80, -91.14) * mm});
            skLineSegment(sketch, "E6317", {"start": v(80, -91.14) * mm, "end": v(81.24, -90.03) * mm});
            skLineSegment(sketch, "E6318", {"start": v(81.24, -90.03) * mm, "end": v(81.23, -89.93) * mm});
            skLineSegment(sketch, "E6319", {"start": v(81.23, -89.93) * mm, "end": v(81.18, -89.8) * mm});
            skLineSegment(sketch, "E6320", {"start": v(81.18, -89.8) * mm, "end": v(81.13, -89.65) * mm});
            skLineSegment(sketch, "E6321", {"start": v(81.13, -89.65) * mm, "end": v(81.08, -89.51) * mm});
            skLineSegment(sketch, "E6322", {"start": v(81.08, -89.51) * mm, "end": v(81.03, -89.38) * mm});
            skLineSegment(sketch, "E6323", {"start": v(81.03, -89.38) * mm, "end": v(80.98, -89.24) * mm});
            skLineSegment(sketch, "E6324", {"start": v(80.98, -89.24) * mm, "end": v(80.93, -89.1) * mm});
            skLineSegment(sketch, "E6325", {"start": v(80.93, -89.1) * mm, "end": v(80.88, -88.97) * mm});
            skLineSegment(sketch, "E6326", {"start": v(80.88, -88.97) * mm, "end": v(80.83, -88.84) * mm});
            skLineSegment(sketch, "E6327", {"start": v(80.83, -88.84) * mm, "end": v(80.78, -88.7) * mm});
            skLineSegment(sketch, "E6328", {"start": v(80.78, -88.7) * mm, "end": v(80.73, -88.58) * mm});
            skLineSegment(sketch, "E6329", {"start": v(80.73, -88.58) * mm, "end": v(80.68, -88.45) * mm});
            skLineSegment(sketch, "E6330", {"start": v(80.68, -88.45) * mm, "end": v(80.63, -88.32) * mm});
            skLineSegment(sketch, "E6331", {"start": v(80.63, -88.32) * mm, "end": v(80.58, -88.2) * mm});
            skLineSegment(sketch, "E6332", {"start": v(80.58, -88.2) * mm, "end": v(80.53, -88.07) * mm});
            skLineSegment(sketch, "E6333", {"start": v(80.53, -88.07) * mm, "end": v(80.48, -87.95) * mm});
            skLineSegment(sketch, "E6334", {"start": v(80.48, -87.95) * mm, "end": v(80.43, -87.83) * mm});
            skLineSegment(sketch, "E6335", {"start": v(80.43, -87.83) * mm, "end": v(80.37, -87.7) * mm});
            skLineSegment(sketch, "E6336", {"start": v(80.37, -87.7) * mm, "end": v(80.32, -87.58) * mm});
            skLineSegment(sketch, "E6337", {"start": v(80.32, -87.58) * mm, "end": v(80.27, -87.47) * mm});
            skLineSegment(sketch, "E6338", {"start": v(80.27, -87.47) * mm, "end": v(80.22, -87.35) * mm});
            skLineSegment(sketch, "E6339", {"start": v(80.22, -87.35) * mm, "end": v(80.17, -87.23) * mm});
            skLineSegment(sketch, "E6340", {"start": v(80.17, -87.23) * mm, "end": v(80.12, -87.12) * mm});
            skLineSegment(sketch, "E6341", {"start": v(80.12, -87.12) * mm, "end": v(80.07, -87) * mm});
            skLineSegment(sketch, "E6342", {"start": v(80.07, -87) * mm, "end": v(80.02, -86.89) * mm});
            skLineSegment(sketch, "E6343", {"start": v(80.02, -86.89) * mm, "end": v(79.92, -86.67) * mm});
            skLineSegment(sketch, "E6344", {"start": v(79.92, -86.67) * mm, "end": v(79.88, -86.56) * mm});
            skLineSegment(sketch, "E6345", {"start": v(79.88, -86.56) * mm, "end": v(79.78, -86.34) * mm});
            skLineSegment(sketch, "E6346", {"start": v(79.78, -86.34) * mm, "end": v(79.73, -86.24) * mm});
            skLineSegment(sketch, "E6347", {"start": v(79.73, -86.24) * mm, "end": v(79.68, -86.14) * mm});
            skLineSegment(sketch, "E6348", {"start": v(79.68, -86.14) * mm, "end": v(79.58, -85.93) * mm});
            skLineSegment(sketch, "E6349", {"start": v(79.58, -85.93) * mm, "end": v(79.53, -85.83) * mm});
            skLineSegment(sketch, "E6350", {"start": v(79.53, -85.83) * mm, "end": v(79.49, -85.73) * mm});
            skLineSegment(sketch, "E6351", {"start": v(79.49, -85.73) * mm, "end": v(79.44, -85.63) * mm});
            skLineSegment(sketch, "E6352", {"start": v(79.44, -85.63) * mm, "end": v(79.4, -85.54) * mm});
            skLineSegment(sketch, "E6353", {"start": v(79.4, -85.54) * mm, "end": v(79.97, -84.75) * mm});
            skLineSegment(sketch, "E6354", {"start": v(79.97, -84.75) * mm, "end": v(80.79, -84.22) * mm});
            skLineSegment(sketch, "E6355", {"start": v(80.79, -84.22) * mm, "end": v(80.88, -84.27) * mm});
            skLineSegment(sketch, "E6356", {"start": v(80.88, -84.27) * mm, "end": v(80.97, -84.33) * mm});
            skLineSegment(sketch, "E6357", {"start": v(80.97, -84.33) * mm, "end": v(81.07, -84.38) * mm});
            skLineSegment(sketch, "E6358", {"start": v(81.07, -84.38) * mm, "end": v(81.17, -84.44) * mm});
            skLineSegment(sketch, "E6359", {"start": v(81.17, -84.44) * mm, "end": v(81.27, -84.5) * mm});
            skLineSegment(sketch, "E6360", {"start": v(81.27, -84.5) * mm, "end": v(81.37, -84.54) * mm});
            skLineSegment(sketch, "E6361", {"start": v(81.37, -84.54) * mm, "end": v(81.57, -84.65) * mm});
            skLineSegment(sketch, "E6362", {"start": v(81.57, -84.65) * mm, "end": v(81.67, -84.7) * mm});
            skLineSegment(sketch, "E6363", {"start": v(81.67, -84.7) * mm, "end": v(81.78, -84.76) * mm});
            skLineSegment(sketch, "E6364", {"start": v(81.78, -84.76) * mm, "end": v(81.88, -84.82) * mm});
            skLineSegment(sketch, "E6365", {"start": v(81.88, -84.82) * mm, "end": v(82, -84.88) * mm});
            skLineSegment(sketch, "E6366", {"start": v(82, -84.88) * mm, "end": v(82.2, -84.99) * mm});
            skLineSegment(sketch, "E6367", {"start": v(82.2, -84.99) * mm, "end": v(82.32, -85.04) * mm});
            skLineSegment(sketch, "E6368", {"start": v(82.32, -85.04) * mm, "end": v(82.43, -85.1) * mm});
            skLineSegment(sketch, "E6369", {"start": v(82.43, -85.1) * mm, "end": v(82.54, -85.16) * mm});
            skLineSegment(sketch, "E6370", {"start": v(82.54, -85.16) * mm, "end": v(82.66, -85.22) * mm});
            skLineSegment(sketch, "E6371", {"start": v(82.66, -85.22) * mm, "end": v(82.77, -85.27) * mm});
            skLineSegment(sketch, "E6372", {"start": v(82.77, -85.27) * mm, "end": v(82.9, -85.33) * mm});
            skLineSegment(sketch, "E6373", {"start": v(82.9, -85.33) * mm, "end": v(83.01, -85.39) * mm});
            skLineSegment(sketch, "E6374", {"start": v(83.01, -85.39) * mm, "end": v(83.13, -85.44) * mm});
            skLineSegment(sketch, "E6375", {"start": v(83.13, -85.44) * mm, "end": v(83.25, -85.5) * mm});
            skLineSegment(sketch, "E6376", {"start": v(83.25, -85.5) * mm, "end": v(83.37, -85.56) * mm});
            skLineSegment(sketch, "E6377", {"start": v(83.37, -85.56) * mm, "end": v(83.5, -85.62) * mm});
            skLineSegment(sketch, "E6378", {"start": v(83.5, -85.62) * mm, "end": v(83.74, -85.73) * mm});
            skLineSegment(sketch, "E6379", {"start": v(83.74, -85.73) * mm, "end": v(83.87, -85.79) * mm});
            skLineSegment(sketch, "E6380", {"start": v(83.87, -85.79) * mm, "end": v(84, -85.85) * mm});
            skLineSegment(sketch, "E6381", {"start": v(84, -85.85) * mm, "end": v(84.13, -85.9) * mm});
            skLineSegment(sketch, "E6382", {"start": v(84.13, -85.9) * mm, "end": v(84.26, -85.96) * mm});
            skLineSegment(sketch, "E6383", {"start": v(84.26, -85.96) * mm, "end": v(84.52, -86.08) * mm});
            skLineSegment(sketch, "E6384", {"start": v(84.52, -86.08) * mm, "end": v(84.66, -86.14) * mm});
            skLineSegment(sketch, "E6385", {"start": v(84.66, -86.14) * mm, "end": v(84.8, -86.2) * mm});
            skLineSegment(sketch, "E6386", {"start": v(84.8, -86.2) * mm, "end": v(84.93, -86.26) * mm});
            skLineSegment(sketch, "E6387", {"start": v(84.93, -86.26) * mm, "end": v(85.07, -86.31) * mm});
            skLineSegment(sketch, "E6388", {"start": v(85.07, -86.31) * mm, "end": v(85.17, -86.33) * mm});
            skLineSegment(sketch, "E6389", {"start": v(85.17, -86.33) * mm, "end": v(86.34, -85.16) * mm});
            skLineSegment(sketch, "E6390", {"start": v(86.34, -85.16) * mm, "end": v(86.32, -85.06) * mm});
            skLineSegment(sketch, "E6391", {"start": v(86.32, -85.06) * mm, "end": v(86.27, -84.92) * mm});
            skLineSegment(sketch, "E6392", {"start": v(86.27, -84.92) * mm, "end": v(86.2, -84.78) * mm});
            skLineSegment(sketch, "E6393", {"start": v(86.2, -84.78) * mm, "end": v(86.15, -84.65) * mm});
            skLineSegment(sketch, "E6394", {"start": v(86.15, -84.65) * mm, "end": v(86.1, -84.51) * mm});
            skLineSegment(sketch, "E6395", {"start": v(86.1, -84.51) * mm, "end": v(86.03, -84.38) * mm});
            skLineSegment(sketch, "E6396", {"start": v(86.03, -84.38) * mm, "end": v(85.97, -84.25) * mm});
            skLineSegment(sketch, "E6397", {"start": v(85.97, -84.25) * mm, "end": v(85.92, -84.12) * mm});
            skLineSegment(sketch, "E6398", {"start": v(85.92, -84.12) * mm, "end": v(85.86, -83.99) * mm});
            skLineSegment(sketch, "E6399", {"start": v(85.86, -83.99) * mm, "end": v(85.8, -83.86) * mm});
            skLineSegment(sketch, "E6400", {"start": v(85.8, -83.86) * mm, "end": v(85.74, -83.73) * mm});
            skLineSegment(sketch, "E6401", {"start": v(85.74, -83.73) * mm, "end": v(85.68, -83.6) * mm});
            skLineSegment(sketch, "E6402", {"start": v(85.68, -83.6) * mm, "end": v(85.57, -83.36) * mm});
            skLineSegment(sketch, "E6403", {"start": v(85.57, -83.36) * mm, "end": v(85.51, -83.24) * mm});
            skLineSegment(sketch, "E6404", {"start": v(85.51, -83.24) * mm, "end": v(85.45, -83.12) * mm});
            skLineSegment(sketch, "E6405", {"start": v(85.45, -83.12) * mm, "end": v(85.34, -82.88) * mm});
            skLineSegment(sketch, "E6406", {"start": v(85.34, -82.88) * mm, "end": v(85.28, -82.76) * mm});
            skLineSegment(sketch, "E6407", {"start": v(85.28, -82.76) * mm, "end": v(85.22, -82.65) * mm});
            skLineSegment(sketch, "E6408", {"start": v(85.22, -82.65) * mm, "end": v(85.17, -82.53) * mm});
            skLineSegment(sketch, "E6409", {"start": v(85.17, -82.53) * mm, "end": v(85.11, -82.42) * mm});
            skLineSegment(sketch, "E6410", {"start": v(85.11, -82.42) * mm, "end": v(85.05, -82.31) * mm});
            skLineSegment(sketch, "E6411", {"start": v(85.05, -82.31) * mm, "end": v(84.94, -82.09) * mm});
            skLineSegment(sketch, "E6412", {"start": v(84.94, -82.09) * mm, "end": v(84.89, -81.98) * mm});
            skLineSegment(sketch, "E6413", {"start": v(84.89, -81.98) * mm, "end": v(84.83, -81.87) * mm});
            skLineSegment(sketch, "E6414", {"start": v(84.83, -81.87) * mm, "end": v(84.77, -81.77) * mm});
            skLineSegment(sketch, "E6415", {"start": v(84.77, -81.77) * mm, "end": v(84.72, -81.66) * mm});
            skLineSegment(sketch, "E6416", {"start": v(84.72, -81.66) * mm, "end": v(84.66, -81.56) * mm});
            skLineSegment(sketch, "E6417", {"start": v(84.66, -81.56) * mm, "end": v(84.6, -81.46) * mm});
            skLineSegment(sketch, "E6418", {"start": v(84.6, -81.46) * mm, "end": v(84.5, -81.26) * mm});
            skLineSegment(sketch, "E6419", {"start": v(84.5, -81.26) * mm, "end": v(84.4, -81.06) * mm});
            skLineSegment(sketch, "E6420", {"start": v(84.4, -81.06) * mm, "end": v(84.34, -80.97) * mm});
            skLineSegment(sketch, "E6421", {"start": v(84.34, -80.97) * mm, "end": v(84.28, -80.87) * mm});
            skLineSegment(sketch, "E6422", {"start": v(84.28, -80.87) * mm, "end": v(84.23, -80.78) * mm});
            skLineSegment(sketch, "E6423", {"start": v(84.23, -80.78) * mm, "end": v(84.76, -79.96) * mm});
            skLineSegment(sketch, "E6424", {"start": v(84.76, -79.96) * mm, "end": v(85.55, -79.38) * mm});
            skLineSegment(sketch, "E6425", {"start": v(85.55, -79.38) * mm, "end": v(85.64, -79.43) * mm});
            skLineSegment(sketch, "E6426", {"start": v(85.64, -79.43) * mm, "end": v(85.74, -79.48) * mm});
            skLineSegment(sketch, "E6427", {"start": v(85.74, -79.48) * mm, "end": v(85.84, -79.53) * mm});
            skLineSegment(sketch, "E6428", {"start": v(85.84, -79.53) * mm, "end": v(86.04, -79.62) * mm});
            skLineSegment(sketch, "E6429", {"start": v(86.04, -79.62) * mm, "end": v(86.15, -79.67) * mm});
            skLineSegment(sketch, "E6430", {"start": v(86.15, -79.67) * mm, "end": v(86.25, -79.72) * mm});
            skLineSegment(sketch, "E6431", {"start": v(86.25, -79.72) * mm, "end": v(86.35, -79.77) * mm});
            skLineSegment(sketch, "E6432", {"start": v(86.35, -79.77) * mm, "end": v(86.46, -79.82) * mm});
            skLineSegment(sketch, "E6433", {"start": v(86.46, -79.82) * mm, "end": v(86.57, -79.87) * mm});
            skLineSegment(sketch, "E6434", {"start": v(86.57, -79.87) * mm, "end": v(86.68, -79.92) * mm});
            skLineSegment(sketch, "E6435", {"start": v(86.68, -79.92) * mm, "end": v(86.79, -79.96) * mm});
            skLineSegment(sketch, "E6436", {"start": v(86.79, -79.96) * mm, "end": v(86.9, -80.01) * mm});
            skLineSegment(sketch, "E6437", {"start": v(86.9, -80.01) * mm, "end": v(87.01, -80.07) * mm});
            skLineSegment(sketch, "E6438", {"start": v(87.01, -80.07) * mm, "end": v(87.13, -80.12) * mm});
            skLineSegment(sketch, "E6439", {"start": v(87.13, -80.12) * mm, "end": v(87.36, -80.21) * mm});
            skLineSegment(sketch, "E6440", {"start": v(87.36, -80.21) * mm, "end": v(87.47, -80.26) * mm});
            skLineSegment(sketch, "E6441", {"start": v(87.47, -80.26) * mm, "end": v(87.6, -80.31) * mm});
            skLineSegment(sketch, "E6442", {"start": v(87.6, -80.31) * mm, "end": v(87.71, -80.36) * mm});
            skLineSegment(sketch, "E6443", {"start": v(87.71, -80.36) * mm, "end": v(87.83, -80.42) * mm});
            skLineSegment(sketch, "E6444", {"start": v(87.83, -80.42) * mm, "end": v(87.96, -80.47) * mm});
            skLineSegment(sketch, "E6445", {"start": v(87.96, -80.47) * mm, "end": v(88.08, -80.52) * mm});
            skLineSegment(sketch, "E6446", {"start": v(88.08, -80.52) * mm, "end": v(88.2, -80.57) * mm});
            skLineSegment(sketch, "E6447", {"start": v(88.2, -80.57) * mm, "end": v(88.33, -80.62) * mm});
            skLineSegment(sketch, "E6448", {"start": v(88.33, -80.62) * mm, "end": v(88.59, -80.72) * mm});
            skLineSegment(sketch, "E6449", {"start": v(88.59, -80.72) * mm, "end": v(88.72, -80.77) * mm});
            skLineSegment(sketch, "E6450", {"start": v(88.72, -80.77) * mm, "end": v(88.85, -80.82) * mm});
            skLineSegment(sketch, "E6451", {"start": v(88.85, -80.82) * mm, "end": v(88.98, -80.87) * mm});
            skLineSegment(sketch, "E6452", {"start": v(88.98, -80.87) * mm, "end": v(89.11, -80.92) * mm});
            skLineSegment(sketch, "E6453", {"start": v(89.11, -80.92) * mm, "end": v(89.25, -80.97) * mm});
            skLineSegment(sketch, "E6454", {"start": v(89.25, -80.97) * mm, "end": v(89.39, -81.02) * mm});
            skLineSegment(sketch, "E6455", {"start": v(89.39, -81.02) * mm, "end": v(89.66, -81.12) * mm});
            skLineSegment(sketch, "E6456", {"start": v(89.66, -81.12) * mm, "end": v(89.94, -81.22) * mm});
            skLineSegment(sketch, "E6457", {"start": v(89.94, -81.22) * mm, "end": v(90.04, -81.23) * mm});
            skLineSegment(sketch, "E6458", {"start": v(90.04, -81.23) * mm, "end": v(91.14, -80) * mm});
            skLineSegment(sketch, "E6459", {"start": v(91.14, -80) * mm, "end": v(91.12, -79.9) * mm});
            skLineSegment(sketch, "E6460", {"start": v(91.12, -79.9) * mm, "end": v(91.06, -79.76) * mm});
            skLineSegment(sketch, "E6461", {"start": v(91.06, -79.76) * mm, "end": v(91, -79.63) * mm});
            skLineSegment(sketch, "E6462", {"start": v(91, -79.63) * mm, "end": v(90.92, -79.5) * mm});
            skLineSegment(sketch, "E6463", {"start": v(90.92, -79.5) * mm, "end": v(90.86, -79.37) * mm});
            skLineSegment(sketch, "E6464", {"start": v(90.86, -79.37) * mm, "end": v(90.8, -79.24) * mm});
            skLineSegment(sketch, "E6465", {"start": v(90.8, -79.24) * mm, "end": v(90.73, -79.1) * mm});
            skLineSegment(sketch, "E6466", {"start": v(90.73, -79.1) * mm, "end": v(90.66, -78.98) * mm});
            skLineSegment(sketch, "E6467", {"start": v(90.66, -78.98) * mm, "end": v(90.6, -78.86) * mm});
            skLineSegment(sketch, "E6468", {"start": v(90.6, -78.86) * mm, "end": v(90.53, -78.73) * mm});
            skLineSegment(sketch, "E6469", {"start": v(90.53, -78.73) * mm, "end": v(90.47, -78.6) * mm});
            skLineSegment(sketch, "E6470", {"start": v(90.47, -78.6) * mm, "end": v(90.4, -78.49) * mm});
            skLineSegment(sketch, "E6471", {"start": v(90.4, -78.49) * mm, "end": v(90.33, -78.37) * mm});
            skLineSegment(sketch, "E6472", {"start": v(90.33, -78.37) * mm, "end": v(90.27, -78.24) * mm});
            skLineSegment(sketch, "E6473", {"start": v(90.27, -78.24) * mm, "end": v(90.2, -78.13) * mm});
            skLineSegment(sketch, "E6474", {"start": v(90.2, -78.13) * mm, "end": v(90.14, -78.01) * mm});
            skLineSegment(sketch, "E6475", {"start": v(90.14, -78.01) * mm, "end": v(90.08, -77.9) * mm});
            skLineSegment(sketch, "E6476", {"start": v(90.08, -77.9) * mm, "end": v(90.01, -77.78) * mm});
            skLineSegment(sketch, "E6477", {"start": v(90.01, -77.78) * mm, "end": v(89.95, -77.67) * mm});
            skLineSegment(sketch, "E6478", {"start": v(89.95, -77.67) * mm, "end": v(89.82, -77.44) * mm});
            skLineSegment(sketch, "E6479", {"start": v(89.82, -77.44) * mm, "end": v(89.76, -77.33) * mm});
            skLineSegment(sketch, "E6480", {"start": v(89.76, -77.33) * mm, "end": v(89.7, -77.23) * mm});
            skLineSegment(sketch, "E6481", {"start": v(89.7, -77.23) * mm, "end": v(89.63, -77.12) * mm});
            skLineSegment(sketch, "E6482", {"start": v(89.63, -77.12) * mm, "end": v(89.57, -77.01) * mm});
            skLineSegment(sketch, "E6483", {"start": v(89.57, -77.01) * mm, "end": v(89.5, -76.9) * mm});
            skLineSegment(sketch, "E6484", {"start": v(89.5, -76.9) * mm, "end": v(89.45, -76.8) * mm});
            skLineSegment(sketch, "E6485", {"start": v(89.45, -76.8) * mm, "end": v(89.32, -76.6) * mm});
            skLineSegment(sketch, "E6486", {"start": v(89.32, -76.6) * mm, "end": v(89.2, -76.4) * mm});
            skLineSegment(sketch, "E6487", {"start": v(89.2, -76.4) * mm, "end": v(89.14, -76.3) * mm});
            skLineSegment(sketch, "E6488", {"start": v(89.14, -76.3) * mm, "end": v(89.08, -76.2) * mm});
            skLineSegment(sketch, "E6489", {"start": v(89.08, -76.2) * mm, "end": v(89.02, -76.11) * mm});
            skLineSegment(sketch, "E6490", {"start": v(89.02, -76.11) * mm, "end": v(88.96, -76.02) * mm});
            skLineSegment(sketch, "E6491", {"start": v(88.96, -76.02) * mm, "end": v(88.9, -75.92) * mm});
            skLineSegment(sketch, "E6492", {"start": v(88.9, -75.92) * mm, "end": v(88.84, -75.83) * mm});
            skLineSegment(sketch, "E6493", {"start": v(88.84, -75.83) * mm, "end": v(88.78, -75.74) * mm});
            skLineSegment(sketch, "E6494", {"start": v(88.78, -75.74) * mm, "end": v(89.27, -74.9) * mm});
            skLineSegment(sketch, "E6495", {"start": v(89.27, -74.9) * mm, "end": v(90.02, -74.27) * mm});
            skLineSegment(sketch, "E6496", {"start": v(90.02, -74.27) * mm, "end": v(90.12, -74.31) * mm});
            skLineSegment(sketch, "E6497", {"start": v(90.12, -74.31) * mm, "end": v(90.22, -74.36) * mm});
            skLineSegment(sketch, "E6498", {"start": v(90.22, -74.36) * mm, "end": v(90.32, -74.4) * mm});
            skLineSegment(sketch, "E6499", {"start": v(90.32, -74.4) * mm, "end": v(90.53, -74.48) * mm});
            skLineSegment(sketch, "E6500", {"start": v(90.53, -74.48) * mm, "end": v(90.74, -74.57) * mm});
            skLineSegment(sketch, "E6501", {"start": v(90.74, -74.57) * mm, "end": v(90.85, -74.61) * mm});
            skLineSegment(sketch, "E6502", {"start": v(90.85, -74.61) * mm, "end": v(91.07, -74.7) * mm});
            skLineSegment(sketch, "E6503", {"start": v(91.07, -74.7) * mm, "end": v(91.18, -74.74) * mm});
            skLineSegment(sketch, "E6504", {"start": v(91.18, -74.74) * mm, "end": v(91.3, -74.78) * mm});
            skLineSegment(sketch, "E6505", {"start": v(91.3, -74.78) * mm, "end": v(91.4, -74.83) * mm});
            skLineSegment(sketch, "E6506", {"start": v(91.4, -74.83) * mm, "end": v(91.64, -74.91) * mm});
            skLineSegment(sketch, "E6507", {"start": v(91.64, -74.91) * mm, "end": v(91.75, -74.96) * mm});
            skLineSegment(sketch, "E6508", {"start": v(91.75, -74.96) * mm, "end": v(91.87, -75) * mm});
            skLineSegment(sketch, "E6509", {"start": v(91.87, -75) * mm, "end": v(92, -75.04) * mm});
            skLineSegment(sketch, "E6510", {"start": v(92, -75.04) * mm, "end": v(92.11, -75.09) * mm});
            skLineSegment(sketch, "E6511", {"start": v(92.11, -75.09) * mm, "end": v(92.24, -75.13) * mm});
            skLineSegment(sketch, "E6512", {"start": v(92.24, -75.13) * mm, "end": v(92.49, -75.21) * mm});
            skLineSegment(sketch, "E6513", {"start": v(92.49, -75.21) * mm, "end": v(92.61, -75.26) * mm});
            skLineSegment(sketch, "E6514", {"start": v(92.61, -75.26) * mm, "end": v(92.87, -75.34) * mm});
            skLineSegment(sketch, "E6515", {"start": v(92.87, -75.34) * mm, "end": v(93, -75.39) * mm});
            skLineSegment(sketch, "E6516", {"start": v(93, -75.39) * mm, "end": v(93.13, -75.43) * mm});
            skLineSegment(sketch, "E6517", {"start": v(93.13, -75.43) * mm, "end": v(93.4, -75.52) * mm});
            skLineSegment(sketch, "E6518", {"start": v(93.4, -75.52) * mm, "end": v(93.53, -75.56) * mm});
            skLineSegment(sketch, "E6519", {"start": v(93.53, -75.56) * mm, "end": v(93.67, -75.6) * mm});
            skLineSegment(sketch, "E6520", {"start": v(93.67, -75.6) * mm, "end": v(93.8, -75.64) * mm});
            skLineSegment(sketch, "E6521", {"start": v(93.8, -75.64) * mm, "end": v(93.95, -75.69) * mm});
            skLineSegment(sketch, "E6522", {"start": v(93.95, -75.69) * mm, "end": v(94.09, -75.73) * mm});
            skLineSegment(sketch, "E6523", {"start": v(94.09, -75.73) * mm, "end": v(94.23, -75.77) * mm});
            skLineSegment(sketch, "E6524", {"start": v(94.23, -75.77) * mm, "end": v(94.37, -75.81) * mm});
            skLineSegment(sketch, "E6525", {"start": v(94.37, -75.81) * mm, "end": v(94.51, -75.86) * mm});
            skLineSegment(sketch, "E6526", {"start": v(94.51, -75.86) * mm, "end": v(94.61, -75.86) * mm});
            skLineSegment(sketch, "E6527", {"start": v(94.61, -75.86) * mm, "end": v(95.64, -74.56) * mm});
            skLineSegment(sketch, "E6528", {"start": v(95.64, -74.56) * mm, "end": v(95.62, -74.46) * mm});
            skLineSegment(sketch, "E6529", {"start": v(95.62, -74.46) * mm, "end": v(95.54, -74.33) * mm});
            skLineSegment(sketch, "E6530", {"start": v(95.54, -74.33) * mm, "end": v(95.47, -74.2) * mm});
            skLineSegment(sketch, "E6531", {"start": v(95.47, -74.2) * mm, "end": v(95.4, -74.08) * mm});
            skLineSegment(sketch, "E6532", {"start": v(95.4, -74.08) * mm, "end": v(95.32, -73.95) * mm});
            skLineSegment(sketch, "E6533", {"start": v(95.32, -73.95) * mm, "end": v(95.25, -73.82) * mm});
            skLineSegment(sketch, "E6534", {"start": v(95.25, -73.82) * mm, "end": v(95.17, -73.7) * mm});
            skLineSegment(sketch, "E6535", {"start": v(95.17, -73.7) * mm, "end": v(95.1, -73.58) * mm});
            skLineSegment(sketch, "E6536", {"start": v(95.1, -73.58) * mm, "end": v(94.96, -73.33) * mm});
            skLineSegment(sketch, "E6537", {"start": v(94.96, -73.33) * mm, "end": v(94.88, -73.22) * mm});
            skLineSegment(sketch, "E6538", {"start": v(94.88, -73.22) * mm, "end": v(94.81, -73.1) * mm});
            skLineSegment(sketch, "E6539", {"start": v(94.81, -73.1) * mm, "end": v(94.74, -72.98) * mm});
            skLineSegment(sketch, "E6540", {"start": v(94.74, -72.98) * mm, "end": v(94.67, -72.86) * mm});
            skLineSegment(sketch, "E6541", {"start": v(94.67, -72.86) * mm, "end": v(94.6, -72.75) * mm});
            skLineSegment(sketch, "E6542", {"start": v(94.6, -72.75) * mm, "end": v(94.53, -72.64) * mm});
            skLineSegment(sketch, "E6543", {"start": v(94.53, -72.64) * mm, "end": v(94.45, -72.52) * mm});
            skLineSegment(sketch, "E6544", {"start": v(94.45, -72.52) * mm, "end": v(94.38, -72.41) * mm});
            skLineSegment(sketch, "E6545", {"start": v(94.38, -72.41) * mm, "end": v(94.24, -72.2) * mm});
            skLineSegment(sketch, "E6546", {"start": v(94.24, -72.2) * mm, "end": v(94.17, -72.09) * mm});
            skLineSegment(sketch, "E6547", {"start": v(94.17, -72.09) * mm, "end": v(94.1, -71.98) * mm});
            skLineSegment(sketch, "E6548", {"start": v(94.1, -71.98) * mm, "end": v(94.03, -71.88) * mm});
            skLineSegment(sketch, "E6549", {"start": v(94.03, -71.88) * mm, "end": v(93.9, -71.67) * mm});
            skLineSegment(sketch, "E6550", {"start": v(93.9, -71.67) * mm, "end": v(93.83, -71.57) * mm});
            skLineSegment(sketch, "E6551", {"start": v(93.83, -71.57) * mm, "end": v(93.76, -71.47) * mm});
            skLineSegment(sketch, "E6552", {"start": v(93.76, -71.47) * mm, "end": v(93.7, -71.37) * mm});
            skLineSegment(sketch, "E6553", {"start": v(93.7, -71.37) * mm, "end": v(93.63, -71.28) * mm});
            skLineSegment(sketch, "E6554", {"start": v(93.63, -71.28) * mm, "end": v(93.56, -71.18) * mm});
            skLineSegment(sketch, "E6555", {"start": v(93.56, -71.18) * mm, "end": v(93.5, -71.08) * mm});
            skLineSegment(sketch, "E6556", {"start": v(93.5, -71.08) * mm, "end": v(93.43, -71) * mm});
            skLineSegment(sketch, "E6557", {"start": v(93.43, -71) * mm, "end": v(93.36, -70.9) * mm});
            skLineSegment(sketch, "E6558", {"start": v(93.36, -70.9) * mm, "end": v(93.3, -70.8) * mm});
            skLineSegment(sketch, "E6559", {"start": v(93.3, -70.8) * mm, "end": v(93.17, -70.63) * mm});
            skLineSegment(sketch, "E6560", {"start": v(93.17, -70.63) * mm, "end": v(93.1, -70.54) * mm});
            skLineSegment(sketch, "E6561", {"start": v(93.1, -70.54) * mm, "end": v(93.04, -70.45) * mm});
            skLineSegment(sketch, "E6562", {"start": v(93.04, -70.45) * mm, "end": v(93.47, -69.58) * mm});
            skLineSegment(sketch, "E6563", {"start": v(93.47, -69.58) * mm, "end": v(94.18, -68.91) * mm});
            skLineSegment(sketch, "E6564", {"start": v(94.18, -68.91) * mm, "end": v(94.29, -68.95) * mm});
            skLineSegment(sketch, "E6565", {"start": v(94.29, -68.95) * mm, "end": v(94.5, -69.02) * mm});
            skLineSegment(sketch, "E6566", {"start": v(94.5, -69.02) * mm, "end": v(94.6, -69.06) * mm});
            skLineSegment(sketch, "E6567", {"start": v(94.6, -69.06) * mm, "end": v(94.7, -69.1) * mm});
            skLineSegment(sketch, "E6568", {"start": v(94.7, -69.1) * mm, "end": v(94.81, -69.13) * mm});
            skLineSegment(sketch, "E6569", {"start": v(94.81, -69.13) * mm, "end": v(94.92, -69.17) * mm});
            skLineSegment(sketch, "E6570", {"start": v(94.92, -69.17) * mm, "end": v(95.03, -69.2) * mm});
            skLineSegment(sketch, "E6571", {"start": v(95.03, -69.2) * mm, "end": v(95.14, -69.24) * mm});
            skLineSegment(sketch, "E6572", {"start": v(95.14, -69.24) * mm, "end": v(95.26, -69.28) * mm});
            skLineSegment(sketch, "E6573", {"start": v(95.26, -69.28) * mm, "end": v(95.37, -69.31) * mm});
            skLineSegment(sketch, "E6574", {"start": v(95.37, -69.31) * mm, "end": v(95.48, -69.35) * mm});
            skLineSegment(sketch, "E6575", {"start": v(95.48, -69.35) * mm, "end": v(95.6, -69.39) * mm});
            skLineSegment(sketch, "E6576", {"start": v(95.6, -69.39) * mm, "end": v(95.72, -69.42) * mm});
            skLineSegment(sketch, "E6577", {"start": v(95.72, -69.42) * mm, "end": v(95.84, -69.46) * mm});
            skLineSegment(sketch, "E6578", {"start": v(95.84, -69.46) * mm, "end": v(95.96, -69.5) * mm});
            skLineSegment(sketch, "E6579", {"start": v(95.96, -69.5) * mm, "end": v(96.08, -69.53) * mm});
            skLineSegment(sketch, "E6580", {"start": v(96.08, -69.53) * mm, "end": v(96.2, -69.57) * mm});
            skLineSegment(sketch, "E6581", {"start": v(96.2, -69.57) * mm, "end": v(96.32, -69.6) * mm});
            skLineSegment(sketch, "E6582", {"start": v(96.32, -69.6) * mm, "end": v(96.45, -69.64) * mm});
            skLineSegment(sketch, "E6583", {"start": v(96.45, -69.64) * mm, "end": v(96.58, -69.67) * mm});
            skLineSegment(sketch, "E6584", {"start": v(96.58, -69.67) * mm, "end": v(96.83, -69.75) * mm});
            skLineSegment(sketch, "E6585", {"start": v(96.83, -69.75) * mm, "end": v(96.96, -69.78) * mm});
            skLineSegment(sketch, "E6586", {"start": v(96.96, -69.78) * mm, "end": v(97.1, -69.82) * mm});
            skLineSegment(sketch, "E6587", {"start": v(97.1, -69.82) * mm, "end": v(97.23, -69.85) * mm});
            skLineSegment(sketch, "E6588", {"start": v(97.23, -69.85) * mm, "end": v(97.36, -69.89) * mm});
            skLineSegment(sketch, "E6589", {"start": v(97.36, -69.89) * mm, "end": v(97.5, -69.92) * mm});
            skLineSegment(sketch, "E6590", {"start": v(97.5, -69.92) * mm, "end": v(97.63, -69.96) * mm});
            skLineSegment(sketch, "E6591", {"start": v(97.63, -69.96) * mm, "end": v(97.77, -70) * mm});
            skLineSegment(sketch, "E6592", {"start": v(97.77, -70) * mm, "end": v(98.05, -70.06) * mm});
            skLineSegment(sketch, "E6593", {"start": v(98.05, -70.06) * mm, "end": v(98.19, -70.1) * mm});
            skLineSegment(sketch, "E6594", {"start": v(98.19, -70.1) * mm, "end": v(98.33, -70.13) * mm});
            skLineSegment(sketch, "E6595", {"start": v(98.33, -70.13) * mm, "end": v(98.47, -70.16) * mm});
            skLineSegment(sketch, "E6596", {"start": v(98.47, -70.16) * mm, "end": v(98.62, -70.2) * mm});
            skLineSegment(sketch, "E6597", {"start": v(98.62, -70.2) * mm, "end": v(98.77, -70.23) * mm});
            skLineSegment(sketch, "E6598", {"start": v(98.77, -70.23) * mm, "end": v(98.86, -70.23) * mm});
            skLineSegment(sketch, "E6599", {"start": v(98.86, -70.23) * mm, "end": v(99.81, -68.87) * mm});
            skLineSegment(sketch, "E6600", {"start": v(99.81, -68.87) * mm, "end": v(99.78, -68.78) * mm});
            skLineSegment(sketch, "E6601", {"start": v(99.78, -68.78) * mm, "end": v(99.7, -68.65) * mm});
            skLineSegment(sketch, "E6602", {"start": v(99.7, -68.65) * mm, "end": v(99.62, -68.53) * mm});
            skLineSegment(sketch, "E6603", {"start": v(99.62, -68.53) * mm, "end": v(99.54, -68.4) * mm});
            skLineSegment(sketch, "E6604", {"start": v(99.54, -68.4) * mm, "end": v(99.46, -68.28) * mm});
            skLineSegment(sketch, "E6605", {"start": v(99.46, -68.28) * mm, "end": v(99.38, -68.16) * mm});
            skLineSegment(sketch, "E6606", {"start": v(99.38, -68.16) * mm, "end": v(99.3, -68.04) * mm});
            skLineSegment(sketch, "E6607", {"start": v(99.3, -68.04) * mm, "end": v(99.22, -67.92) * mm});
            skLineSegment(sketch, "E6608", {"start": v(99.22, -67.92) * mm, "end": v(99.14, -67.8) * mm});
            skLineSegment(sketch, "E6609", {"start": v(99.14, -67.8) * mm, "end": v(99.06, -67.69) * mm});
            skLineSegment(sketch, "E6610", {"start": v(99.06, -67.69) * mm, "end": v(98.98, -67.57) * mm});
            skLineSegment(sketch, "E6611", {"start": v(98.98, -67.57) * mm, "end": v(98.82, -67.35) * mm});
            skLineSegment(sketch, "E6612", {"start": v(98.82, -67.35) * mm, "end": v(98.74, -67.24) * mm});
            skLineSegment(sketch, "E6613", {"start": v(98.74, -67.24) * mm, "end": v(98.67, -67.13) * mm});
            skLineSegment(sketch, "E6614", {"start": v(98.67, -67.13) * mm, "end": v(98.59, -67.02) * mm});
            skLineSegment(sketch, "E6615", {"start": v(98.59, -67.02) * mm, "end": v(98.51, -66.91) * mm});
            skLineSegment(sketch, "E6616", {"start": v(98.51, -66.91) * mm, "end": v(98.43, -66.8) * mm});
            skLineSegment(sketch, "E6617", {"start": v(98.43, -66.8) * mm, "end": v(98.36, -66.7) * mm});
            skLineSegment(sketch, "E6618", {"start": v(98.36, -66.7) * mm, "end": v(98.2, -66.5) * mm});
            skLineSegment(sketch, "E6619", {"start": v(98.2, -66.5) * mm, "end": v(98.05, -66.3) * mm});
            skLineSegment(sketch, "E6620", {"start": v(98.05, -66.3) * mm, "end": v(97.98, -66.2) * mm});
            skLineSegment(sketch, "E6621", {"start": v(97.98, -66.2) * mm, "end": v(97.83, -66) * mm});
            skLineSegment(sketch, "E6622", {"start": v(97.83, -66) * mm, "end": v(97.68, -65.8) * mm});
            skLineSegment(sketch, "E6623", {"start": v(97.68, -65.8) * mm, "end": v(97.61, -65.71) * mm});
            skLineSegment(sketch, "E6624", {"start": v(97.61, -65.71) * mm, "end": v(97.54, -65.62) * mm});
            skLineSegment(sketch, "E6625", {"start": v(97.54, -65.62) * mm, "end": v(97.47, -65.53) * mm});
            skLineSegment(sketch, "E6626", {"start": v(97.47, -65.53) * mm, "end": v(97.4, -65.44) * mm});
            skLineSegment(sketch, "E6627", {"start": v(97.4, -65.44) * mm, "end": v(97.33, -65.35) * mm});
            skLineSegment(sketch, "E6628", {"start": v(97.33, -65.35) * mm, "end": v(97.26, -65.26) * mm});
            skLineSegment(sketch, "E6629", {"start": v(97.26, -65.26) * mm, "end": v(97.18, -65.18) * mm});
            skLineSegment(sketch, "E6630", {"start": v(97.18, -65.18) * mm, "end": v(97.11, -65.1) * mm});
            skLineSegment(sketch, "E6631", {"start": v(97.11, -65.1) * mm, "end": v(97.05, -65) * mm});
            skLineSegment(sketch, "E6632", {"start": v(97.05, -65) * mm, "end": v(96.98, -64.92) * mm});
            skLineSegment(sketch, "E6633", {"start": v(96.98, -64.92) * mm, "end": v(97.36, -64.03) * mm});
            skLineSegment(sketch, "E6634", {"start": v(97.36, -64.03) * mm, "end": v(98.03, -63.32) * mm});
            skLineSegment(sketch, "E6635", {"start": v(98.03, -63.32) * mm, "end": v(98.13, -63.35) * mm});
            skLineSegment(sketch, "E6636", {"start": v(98.13, -63.35) * mm, "end": v(98.24, -63.38) * mm});
            skLineSegment(sketch, "E6637", {"start": v(98.24, -63.38) * mm, "end": v(98.35, -63.41) * mm});
            skLineSegment(sketch, "E6638", {"start": v(98.35, -63.41) * mm, "end": v(98.45, -63.44) * mm});
            skLineSegment(sketch, "E6639", {"start": v(98.45, -63.44) * mm, "end": v(98.56, -63.47) * mm});
            skLineSegment(sketch, "E6640", {"start": v(98.56, -63.47) * mm, "end": v(98.78, -63.53) * mm});
            skLineSegment(sketch, "E6641", {"start": v(98.78, -63.53) * mm, "end": v(98.9, -63.56) * mm});
            skLineSegment(sketch, "E6642", {"start": v(98.9, -63.56) * mm, "end": v(99.12, -63.62) * mm});
            skLineSegment(sketch, "E6643", {"start": v(99.12, -63.62) * mm, "end": v(99.24, -63.65) * mm});
            skLineSegment(sketch, "E6644", {"start": v(99.24, -63.65) * mm, "end": v(99.36, -63.68) * mm});
            skLineSegment(sketch, "E6645", {"start": v(99.36, -63.68) * mm, "end": v(99.6, -63.74) * mm});
            skLineSegment(sketch, "E6646", {"start": v(99.6, -63.74) * mm, "end": v(99.71, -63.77) * mm});
            skLineSegment(sketch, "E6647", {"start": v(99.71, -63.77) * mm, "end": v(99.83, -63.8) * mm});
            skLineSegment(sketch, "E6648", {"start": v(99.83, -63.8) * mm, "end": v(100.08, -63.86) * mm});
            skLineSegment(sketch, "E6649", {"start": v(100.08, -63.86) * mm, "end": v(100.2, -63.88) * mm});
            skLineSegment(sketch, "E6650", {"start": v(100.2, -63.88) * mm, "end": v(100.33, -63.91) * mm});
            skLineSegment(sketch, "E6651", {"start": v(100.33, -63.91) * mm, "end": v(100.46, -63.94) * mm});
            skLineSegment(sketch, "E6652", {"start": v(100.46, -63.94) * mm, "end": v(100.6, -63.97) * mm});
            skLineSegment(sketch, "E6653", {"start": v(100.6, -63.97) * mm, "end": v(100.72, -64) * mm});
            skLineSegment(sketch, "E6654", {"start": v(100.72, -64) * mm, "end": v(100.86, -64.03) * mm});
            skLineSegment(sketch, "E6655", {"start": v(100.86, -64.03) * mm, "end": v(100.99, -64.05) * mm});
            skLineSegment(sketch, "E6656", {"start": v(100.99, -64.05) * mm, "end": v(101.26, -64.1) * mm});
            skLineSegment(sketch, "E6657", {"start": v(101.26, -64.1) * mm, "end": v(101.4, -64.14) * mm});
            skLineSegment(sketch, "E6658", {"start": v(101.4, -64.14) * mm, "end": v(101.53, -64.16) * mm});
            skLineSegment(sketch, "E6659", {"start": v(101.53, -64.16) * mm, "end": v(101.67, -64.19) * mm});
            skLineSegment(sketch, "E6660", {"start": v(101.67, -64.19) * mm, "end": v(101.81, -64.22) * mm});
            skLineSegment(sketch, "E6661", {"start": v(101.81, -64.22) * mm, "end": v(101.95, -64.24) * mm});
            skLineSegment(sketch, "E6662", {"start": v(101.95, -64.24) * mm, "end": v(102.1, -64.27) * mm});
            skLineSegment(sketch, "E6663", {"start": v(102.1, -64.27) * mm, "end": v(102.24, -64.3) * mm});
            skLineSegment(sketch, "E6664", {"start": v(102.24, -64.3) * mm, "end": v(102.39, -64.32) * mm});
            skLineSegment(sketch, "E6665", {"start": v(102.39, -64.32) * mm, "end": v(102.53, -64.34) * mm});
            skLineSegment(sketch, "E6666", {"start": v(102.53, -64.34) * mm, "end": v(102.68, -64.37) * mm});
            skLineSegment(sketch, "E6667", {"start": v(102.68, -64.37) * mm, "end": v(102.78, -64.36) * mm});
            skLineSegment(sketch, "E6668", {"start": v(102.78, -64.36) * mm, "end": v(103.65, -62.95) * mm});
            skLineSegment(sketch, "E6669", {"start": v(103.65, -62.95) * mm, "end": v(103.61, -62.86) * mm});
            skLineSegment(sketch, "E6670", {"start": v(103.61, -62.86) * mm, "end": v(103.53, -62.74) * mm});
            skLineSegment(sketch, "E6671", {"start": v(103.53, -62.74) * mm, "end": v(103.44, -62.62) * mm});
            skLineSegment(sketch, "E6672", {"start": v(103.44, -62.62) * mm, "end": v(103.35, -62.5) * mm});
            skLineSegment(sketch, "E6673", {"start": v(103.35, -62.5) * mm, "end": v(103.26, -62.38) * mm});
            skLineSegment(sketch, "E6674", {"start": v(103.26, -62.38) * mm, "end": v(103.17, -62.27) * mm});
            skLineSegment(sketch, "E6675", {"start": v(103.17, -62.27) * mm, "end": v(103, -62.04) * mm});
            skLineSegment(sketch, "E6676", {"start": v(103, -62.04) * mm, "end": v(102.91, -61.93) * mm});
            skLineSegment(sketch, "E6677", {"start": v(102.91, -61.93) * mm, "end": v(102.83, -61.81) * mm});
            skLineSegment(sketch, "E6678", {"start": v(102.83, -61.81) * mm, "end": v(102.74, -61.7) * mm});
            skLineSegment(sketch, "E6679", {"start": v(102.74, -61.7) * mm, "end": v(102.66, -61.6) * mm});
            skLineSegment(sketch, "E6680", {"start": v(102.66, -61.6) * mm, "end": v(102.57, -61.49) * mm});
            skLineSegment(sketch, "E6681", {"start": v(102.57, -61.49) * mm, "end": v(102.4, -61.28) * mm});
            skLineSegment(sketch, "E6682", {"start": v(102.4, -61.28) * mm, "end": v(102.32, -61.17) * mm});
            skLineSegment(sketch, "E6683", {"start": v(102.32, -61.17) * mm, "end": v(102.24, -61.07) * mm});
            skLineSegment(sketch, "E6684", {"start": v(102.24, -61.07) * mm, "end": v(102.15, -60.97) * mm});
            skLineSegment(sketch, "E6685", {"start": v(102.15, -60.97) * mm, "end": v(102.07, -60.87) * mm});
            skLineSegment(sketch, "E6686", {"start": v(102.07, -60.87) * mm, "end": v(101.99, -60.77) * mm});
            skLineSegment(sketch, "E6687", {"start": v(101.99, -60.77) * mm, "end": v(101.9, -60.67) * mm});
            skLineSegment(sketch, "E6688", {"start": v(101.9, -60.67) * mm, "end": v(101.74, -60.48) * mm});
            skLineSegment(sketch, "E6689", {"start": v(101.74, -60.48) * mm, "end": v(101.66, -60.38) * mm});
            skLineSegment(sketch, "E6690", {"start": v(101.66, -60.38) * mm, "end": v(101.58, -60.29) * mm});
            skLineSegment(sketch, "E6691", {"start": v(101.58, -60.29) * mm, "end": v(101.5, -60.2) * mm});
            skLineSegment(sketch, "E6692", {"start": v(101.5, -60.2) * mm, "end": v(101.43, -60.1) * mm});
            skLineSegment(sketch, "E6693", {"start": v(101.43, -60.1) * mm, "end": v(101.27, -59.93) * mm});
            skLineSegment(sketch, "E6694", {"start": v(101.27, -59.93) * mm, "end": v(101.2, -59.84) * mm});
            skLineSegment(sketch, "E6695", {"start": v(101.2, -59.84) * mm, "end": v(101.11, -59.75) * mm});
            skLineSegment(sketch, "E6696", {"start": v(101.11, -59.75) * mm, "end": v(101.04, -59.66) * mm});
            skLineSegment(sketch, "E6697", {"start": v(101.04, -59.66) * mm, "end": v(100.89, -59.5) * mm});
            skLineSegment(sketch, "E6698", {"start": v(100.89, -59.5) * mm, "end": v(100.74, -59.33) * mm});
            skLineSegment(sketch, "E6699", {"start": v(100.74, -59.33) * mm, "end": v(100.66, -59.25) * mm});
            skLineSegment(sketch, "E6700", {"start": v(100.66, -59.25) * mm, "end": v(100.59, -59.17) * mm});
            skLineSegment(sketch, "E6701", {"start": v(100.59, -59.17) * mm, "end": v(100.92, -58.26) * mm});
            skLineSegment(sketch, "E6702", {"start": v(100.92, -58.26) * mm, "end": v(101.55, -57.51) * mm});
            skLineSegment(sketch, "E6703", {"start": v(101.55, -57.51) * mm, "end": v(101.65, -57.54) * mm});
            skLineSegment(sketch, "E6704", {"start": v(101.65, -57.54) * mm, "end": v(101.76, -57.56) * mm});
            skLineSegment(sketch, "E6705", {"start": v(101.76, -57.56) * mm, "end": v(101.87, -57.59) * mm});
            skLineSegment(sketch, "E6706", {"start": v(101.87, -57.59) * mm, "end": v(101.97, -57.6) * mm});
            skLineSegment(sketch, "E6707", {"start": v(101.97, -57.6) * mm, "end": v(102.09, -57.63) * mm});
            skLineSegment(sketch, "E6708", {"start": v(102.09, -57.63) * mm, "end": v(102.2, -57.66) * mm});
            skLineSegment(sketch, "E6709", {"start": v(102.2, -57.66) * mm, "end": v(102.3, -57.68) * mm});
            skLineSegment(sketch, "E6710", {"start": v(102.3, -57.68) * mm, "end": v(102.42, -57.7) * mm});
            skLineSegment(sketch, "E6711", {"start": v(102.42, -57.7) * mm, "end": v(102.54, -57.73) * mm});
            skLineSegment(sketch, "E6712", {"start": v(102.54, -57.73) * mm, "end": v(102.65, -57.75) * mm});
            skLineSegment(sketch, "E6713", {"start": v(102.65, -57.75) * mm, "end": v(102.77, -57.77) * mm});
            skLineSegment(sketch, "E6714", {"start": v(102.77, -57.77) * mm, "end": v(102.89, -57.8) * mm});
            skLineSegment(sketch, "E6715", {"start": v(102.89, -57.8) * mm, "end": v(103, -57.82) * mm});
            skLineSegment(sketch, "E6716", {"start": v(103, -57.82) * mm, "end": v(103.13, -57.84) * mm});
            skLineSegment(sketch, "E6717", {"start": v(103.13, -57.84) * mm, "end": v(103.25, -57.86) * mm});
            skLineSegment(sketch, "E6718", {"start": v(103.25, -57.86) * mm, "end": v(103.5, -57.9) * mm});
            skLineSegment(sketch, "E6719", {"start": v(103.5, -57.9) * mm, "end": v(103.63, -57.93) * mm});
            skLineSegment(sketch, "E6720", {"start": v(103.63, -57.93) * mm, "end": v(103.75, -57.95) * mm});
            skLineSegment(sketch, "E6721", {"start": v(103.75, -57.95) * mm, "end": v(103.88, -57.97) * mm});
            skLineSegment(sketch, "E6722", {"start": v(103.88, -57.97) * mm, "end": v(104.01, -58) * mm});
            skLineSegment(sketch, "E6723", {"start": v(104.01, -58) * mm, "end": v(104.14, -58.01) * mm});
            skLineSegment(sketch, "E6724", {"start": v(104.14, -58.01) * mm, "end": v(104.4, -58.05) * mm});
            skLineSegment(sketch, "E6725", {"start": v(104.4, -58.05) * mm, "end": v(104.68, -58.1) * mm});
            skLineSegment(sketch, "E6726", {"start": v(104.68, -58.1) * mm, "end": v(104.81, -58.11) * mm});
            skLineSegment(sketch, "E6727", {"start": v(104.81, -58.11) * mm, "end": v(104.95, -58.13) * mm});
            skLineSegment(sketch, "E6728", {"start": v(104.95, -58.13) * mm, "end": v(105.1, -58.15) * mm});
            skLineSegment(sketch, "E6729", {"start": v(105.1, -58.15) * mm, "end": v(105.23, -58.17) * mm});
            skLineSegment(sketch, "E6730", {"start": v(105.23, -58.17) * mm, "end": v(105.37, -58.19) * mm});
            skLineSegment(sketch, "E6731", {"start": v(105.37, -58.19) * mm, "end": v(105.66, -58.22) * mm});
            skLineSegment(sketch, "E6732", {"start": v(105.66, -58.22) * mm, "end": v(105.8, -58.24) * mm});
            skLineSegment(sketch, "E6733", {"start": v(105.8, -58.24) * mm, "end": v(105.95, -58.26) * mm});
            skLineSegment(sketch, "E6734", {"start": v(105.95, -58.26) * mm, "end": v(106.1, -58.27) * mm});
            skLineSegment(sketch, "E6735", {"start": v(106.1, -58.27) * mm, "end": v(106.25, -58.3) * mm});
            skLineSegment(sketch, "E6736", {"start": v(106.25, -58.3) * mm, "end": v(106.35, -58.28) * mm});
            skLineSegment(sketch, "E6737", {"start": v(106.35, -58.28) * mm, "end": v(107.13, -56.82) * mm});
            skLineSegment(sketch, "E6738", {"start": v(107.13, -56.82) * mm, "end": v(107.1, -56.73) * mm});
            skLineSegment(sketch, "E6739", {"start": v(107.1, -56.73) * mm, "end": v(107, -56.61) * mm});
            skLineSegment(sketch, "E6740", {"start": v(107, -56.61) * mm, "end": v(106.9, -56.5) * mm});
            skLineSegment(sketch, "E6741", {"start": v(106.9, -56.5) * mm, "end": v(106.8, -56.39) * mm});
            skLineSegment(sketch, "E6742", {"start": v(106.8, -56.39) * mm, "end": v(106.71, -56.27) * mm});
            skLineSegment(sketch, "E6743", {"start": v(106.71, -56.27) * mm, "end": v(106.62, -56.16) * mm});
            skLineSegment(sketch, "E6744", {"start": v(106.62, -56.16) * mm, "end": v(106.43, -55.94) * mm});
            skLineSegment(sketch, "E6745", {"start": v(106.43, -55.94) * mm, "end": v(106.34, -55.84) * mm});
            skLineSegment(sketch, "E6746", {"start": v(106.34, -55.84) * mm, "end": v(106.25, -55.73) * mm});
            skLineSegment(sketch, "E6747", {"start": v(106.25, -55.73) * mm, "end": v(106.15, -55.63) * mm});
            skLineSegment(sketch, "E6748", {"start": v(106.15, -55.63) * mm, "end": v(106.06, -55.52) * mm});
            skLineSegment(sketch, "E6749", {"start": v(106.06, -55.52) * mm, "end": v(105.88, -55.32) * mm});
            skLineSegment(sketch, "E6750", {"start": v(105.88, -55.32) * mm, "end": v(105.8, -55.22) * mm});
            skLineSegment(sketch, "E6751", {"start": v(105.8, -55.22) * mm, "end": v(105.61, -55.02) * mm});
            skLineSegment(sketch, "E6752", {"start": v(105.61, -55.02) * mm, "end": v(105.52, -54.92) * mm});
            skLineSegment(sketch, "E6753", {"start": v(105.52, -54.92) * mm, "end": v(105.35, -54.73) * mm});
            skLineSegment(sketch, "E6754", {"start": v(105.35, -54.73) * mm, "end": v(105.26, -54.64) * mm});
            skLineSegment(sketch, "E6755", {"start": v(105.26, -54.64) * mm, "end": v(105.17, -54.55) * mm});
            skLineSegment(sketch, "E6756", {"start": v(105.17, -54.55) * mm, "end": v(105.09, -54.46) * mm});
            skLineSegment(sketch, "E6757", {"start": v(105.09, -54.46) * mm, "end": v(104.92, -54.28) * mm});
            skLineSegment(sketch, "E6758", {"start": v(104.92, -54.28) * mm, "end": v(104.83, -54.2) * mm});
            skLineSegment(sketch, "E6759", {"start": v(104.83, -54.2) * mm, "end": v(104.75, -54.1) * mm});
            skLineSegment(sketch, "E6760", {"start": v(104.75, -54.1) * mm, "end": v(104.67, -54.02) * mm});
            skLineSegment(sketch, "E6761", {"start": v(104.67, -54.02) * mm, "end": v(104.58, -53.94) * mm});
            skLineSegment(sketch, "E6762", {"start": v(104.58, -53.94) * mm, "end": v(104.5, -53.85) * mm});
            skLineSegment(sketch, "E6763", {"start": v(104.5, -53.85) * mm, "end": v(104.34, -53.69) * mm});
            skLineSegment(sketch, "E6764", {"start": v(104.34, -53.69) * mm, "end": v(104.25, -53.6) * mm});
            skLineSegment(sketch, "E6765", {"start": v(104.25, -53.6) * mm, "end": v(104.1, -53.45) * mm});
            skLineSegment(sketch, "E6766", {"start": v(104.1, -53.45) * mm, "end": v(104.02, -53.38) * mm});
            skLineSegment(sketch, "E6767", {"start": v(104.02, -53.38) * mm, "end": v(103.94, -53.3) * mm});
            skLineSegment(sketch, "E6768", {"start": v(103.94, -53.3) * mm, "end": v(103.86, -53.23) * mm});
            skLineSegment(sketch, "E6769", {"start": v(103.86, -53.23) * mm, "end": v(104.14, -52.3) * mm});
            skLineSegment(sketch, "E6770", {"start": v(104.14, -52.3) * mm, "end": v(104.72, -51.51) * mm});
            skLineSegment(sketch, "E6771", {"start": v(104.72, -51.51) * mm, "end": v(104.83, -51.53) * mm});
            skLineSegment(sketch, "E6772", {"start": v(104.83, -51.53) * mm, "end": v(104.93, -51.55) * mm});
            skLineSegment(sketch, "E6773", {"start": v(104.93, -51.55) * mm, "end": v(105.04, -51.56) * mm});
            skLineSegment(sketch, "E6774", {"start": v(105.04, -51.56) * mm, "end": v(105.15, -51.58) * mm});
            skLineSegment(sketch, "E6775", {"start": v(105.15, -51.58) * mm, "end": v(105.26, -51.6) * mm});
            skLineSegment(sketch, "E6776", {"start": v(105.26, -51.6) * mm, "end": v(105.38, -51.62) * mm});
            skLineSegment(sketch, "E6777", {"start": v(105.38, -51.62) * mm, "end": v(105.49, -51.63) * mm});
            skLineSegment(sketch, "E6778", {"start": v(105.49, -51.63) * mm, "end": v(105.72, -51.67) * mm});
            skLineSegment(sketch, "E6779", {"start": v(105.72, -51.67) * mm, "end": v(105.84, -51.68) * mm});
            skLineSegment(sketch, "E6780", {"start": v(105.84, -51.68) * mm, "end": v(105.96, -51.7) * mm});
            skLineSegment(sketch, "E6781", {"start": v(105.96, -51.7) * mm, "end": v(106.08, -51.72) * mm});
            skLineSegment(sketch, "E6782", {"start": v(106.08, -51.72) * mm, "end": v(106.32, -51.75) * mm});
            skLineSegment(sketch, "E6783", {"start": v(106.32, -51.75) * mm, "end": v(106.57, -51.78) * mm});
            skLineSegment(sketch, "E6784", {"start": v(106.57, -51.78) * mm, "end": v(106.7, -51.8) * mm});
            skLineSegment(sketch, "E6785", {"start": v(106.7, -51.8) * mm, "end": v(107.08, -51.83) * mm});
            skLineSegment(sketch, "E6786", {"start": v(107.08, -51.83) * mm, "end": v(107.2, -51.85) * mm});
            skLineSegment(sketch, "E6787", {"start": v(107.2, -51.85) * mm, "end": v(107.34, -51.86) * mm});
            skLineSegment(sketch, "E6788", {"start": v(107.34, -51.86) * mm, "end": v(107.47, -51.87) * mm});
            skLineSegment(sketch, "E6789", {"start": v(107.47, -51.87) * mm, "end": v(107.74, -51.9) * mm});
            skLineSegment(sketch, "E6790", {"start": v(107.74, -51.9) * mm, "end": v(107.88, -51.9) * mm});
            skLineSegment(sketch, "E6791", {"start": v(107.88, -51.9) * mm, "end": v(108.02, -51.92) * mm});
            skLineSegment(sketch, "E6792", {"start": v(108.02, -51.92) * mm, "end": v(108.16, -51.93) * mm});
            skLineSegment(sketch, "E6793", {"start": v(108.16, -51.93) * mm, "end": v(108.3, -51.94) * mm});
            skLineSegment(sketch, "E6794", {"start": v(108.3, -51.94) * mm, "end": v(108.44, -51.95) * mm});
            skLineSegment(sketch, "E6795", {"start": v(108.44, -51.95) * mm, "end": v(108.72, -51.97) * mm});
            skLineSegment(sketch, "E6796", {"start": v(108.72, -51.97) * mm, "end": v(108.87, -51.98) * mm});
            skLineSegment(sketch, "E6797", {"start": v(108.87, -51.98) * mm, "end": v(109.01, -51.99) * mm});
            skLineSegment(sketch, "E6798", {"start": v(109.01, -51.99) * mm, "end": v(109.16, -52) * mm});
            skLineSegment(sketch, "E6799", {"start": v(109.16, -52) * mm, "end": v(109.3, -52) * mm});
            skLineSegment(sketch, "E6800", {"start": v(109.3, -52) * mm, "end": v(109.46, -52.01) * mm});
            skLineSegment(sketch, "E6801", {"start": v(109.46, -52.01) * mm, "end": v(109.56, -52) * mm});
            skLineSegment(sketch, "E6802", {"start": v(109.56, -52) * mm, "end": v(110.26, -50.49) * mm});
            skLineSegment(sketch, "E6803", {"start": v(110.26, -50.49) * mm, "end": v(110.2, -50.4) * mm});
            skLineSegment(sketch, "E6804", {"start": v(110.2, -50.4) * mm, "end": v(110, -50.19) * mm});
            skLineSegment(sketch, "E6805", {"start": v(110, -50.19) * mm, "end": v(109.9, -50.08) * mm});
            skLineSegment(sketch, "E6806", {"start": v(109.9, -50.08) * mm, "end": v(109.8, -49.97) * mm});
            skLineSegment(sketch, "E6807", {"start": v(109.8, -49.97) * mm, "end": v(109.6, -49.76) * mm});
            skLineSegment(sketch, "E6808", {"start": v(109.6, -49.76) * mm, "end": v(109.5, -49.66) * mm});
            skLineSegment(sketch, "E6809", {"start": v(109.5, -49.66) * mm, "end": v(109.4, -49.56) * mm});
            skLineSegment(sketch, "E6810", {"start": v(109.4, -49.56) * mm, "end": v(109.3, -49.46) * mm});
            skLineSegment(sketch, "E6811", {"start": v(109.3, -49.46) * mm, "end": v(109.2, -49.36) * mm});
            skLineSegment(sketch, "E6812", {"start": v(109.2, -49.36) * mm, "end": v(109.11, -49.26) * mm});
            skLineSegment(sketch, "E6813", {"start": v(109.11, -49.26) * mm, "end": v(109.02, -49.16) * mm});
            skLineSegment(sketch, "E6814", {"start": v(109.02, -49.16) * mm, "end": v(108.92, -49.07) * mm});
            skLineSegment(sketch, "E6815", {"start": v(108.92, -49.07) * mm, "end": v(108.82, -48.97) * mm});
            skLineSegment(sketch, "E6816", {"start": v(108.82, -48.97) * mm, "end": v(108.73, -48.88) * mm});
            skLineSegment(sketch, "E6817", {"start": v(108.73, -48.88) * mm, "end": v(108.54, -48.7) * mm});
            skLineSegment(sketch, "E6818", {"start": v(108.54, -48.7) * mm, "end": v(108.45, -48.6) * mm});
            skLineSegment(sketch, "E6819", {"start": v(108.45, -48.6) * mm, "end": v(108.35, -48.52) * mm});
            skLineSegment(sketch, "E6820", {"start": v(108.35, -48.52) * mm, "end": v(108.26, -48.43) * mm});
            skLineSegment(sketch, "E6821", {"start": v(108.26, -48.43) * mm, "end": v(108.17, -48.34) * mm});
            skLineSegment(sketch, "E6822", {"start": v(108.17, -48.34) * mm, "end": v(107.99, -48.17) * mm});
            skLineSegment(sketch, "E6823", {"start": v(107.99, -48.17) * mm, "end": v(107.9, -48.09) * mm});
            skLineSegment(sketch, "E6824", {"start": v(107.9, -48.09) * mm, "end": v(107.8, -48) * mm});
            skLineSegment(sketch, "E6825", {"start": v(107.8, -48) * mm, "end": v(107.72, -47.92) * mm});
            skLineSegment(sketch, "E6826", {"start": v(107.72, -47.92) * mm, "end": v(107.63, -47.84) * mm});
            skLineSegment(sketch, "E6827", {"start": v(107.63, -47.84) * mm, "end": v(107.54, -47.76) * mm});
            skLineSegment(sketch, "E6828", {"start": v(107.54, -47.76) * mm, "end": v(107.45, -47.69) * mm});
            skLineSegment(sketch, "E6829", {"start": v(107.45, -47.69) * mm, "end": v(107.37, -47.6) * mm});
            skLineSegment(sketch, "E6830", {"start": v(107.37, -47.6) * mm, "end": v(107.2, -47.46) * mm});
            skLineSegment(sketch, "E6831", {"start": v(107.2, -47.46) * mm, "end": v(107.11, -47.38) * mm});
            skLineSegment(sketch, "E6832", {"start": v(107.11, -47.38) * mm, "end": v(107.03, -47.3) * mm});
            skLineSegment(sketch, "E6833", {"start": v(107.03, -47.3) * mm, "end": v(106.94, -47.24) * mm});
            skLineSegment(sketch, "E6834", {"start": v(106.94, -47.24) * mm, "end": v(106.78, -47.1) * mm});
            skLineSegment(sketch, "E6835", {"start": v(106.78, -47.1) * mm, "end": v(107, -46.15) * mm});
            skLineSegment(sketch, "E6836", {"start": v(107, -46.15) * mm, "end": v(107.54, -45.34) * mm});
            skLineSegment(sketch, "E6837", {"start": v(107.54, -45.34) * mm, "end": v(107.64, -45.35) * mm});
            skLineSegment(sketch, "E6838", {"start": v(107.64, -45.35) * mm, "end": v(107.75, -45.36) * mm});
            skLineSegment(sketch, "E6839", {"start": v(107.75, -45.36) * mm, "end": v(107.86, -45.37) * mm});
            skLineSegment(sketch, "E6840", {"start": v(107.86, -45.37) * mm, "end": v(107.97, -45.38) * mm});
            skLineSegment(sketch, "E6841", {"start": v(107.97, -45.38) * mm, "end": v(108.09, -45.4) * mm});
            skLineSegment(sketch, "E6842", {"start": v(108.09, -45.4) * mm, "end": v(108.31, -45.41) * mm});
            skLineSegment(sketch, "E6843", {"start": v(108.31, -45.41) * mm, "end": v(108.43, -45.42) * mm});
            skLineSegment(sketch, "E6844", {"start": v(108.43, -45.42) * mm, "end": v(108.55, -45.43) * mm});
            skLineSegment(sketch, "E6845", {"start": v(108.55, -45.43) * mm, "end": v(108.66, -45.44) * mm});
            skLineSegment(sketch, "E6846", {"start": v(108.66, -45.44) * mm, "end": v(108.78, -45.45) * mm});
            skLineSegment(sketch, "E6847", {"start": v(108.78, -45.45) * mm, "end": v(108.9, -45.46) * mm});
            skLineSegment(sketch, "E6848", {"start": v(108.9, -45.46) * mm, "end": v(109.02, -45.47) * mm});
            skLineSegment(sketch, "E6849", {"start": v(109.02, -45.47) * mm, "end": v(109.15, -45.48) * mm});
            skLineSegment(sketch, "E6850", {"start": v(109.15, -45.48) * mm, "end": v(109.27, -45.49) * mm});
            skLineSegment(sketch, "E6851", {"start": v(109.27, -45.49) * mm, "end": v(109.4, -45.5) * mm});
            skLineSegment(sketch, "E6852", {"start": v(109.4, -45.5) * mm, "end": v(109.65, -45.5) * mm});
            skLineSegment(sketch, "E6853", {"start": v(109.65, -45.5) * mm, "end": v(109.9, -45.52) * mm});
            skLineSegment(sketch, "E6854", {"start": v(109.9, -45.52) * mm, "end": v(110.04, -45.52) * mm});
            skLineSegment(sketch, "E6855", {"start": v(110.04, -45.52) * mm, "end": v(110.17, -45.53) * mm});
            skLineSegment(sketch, "E6856", {"start": v(110.17, -45.53) * mm, "end": v(110.3, -45.53) * mm});
            skLineSegment(sketch, "E6857", {"start": v(110.3, -45.53) * mm, "end": v(110.44, -45.54) * mm});
            skLineSegment(sketch, "E6858", {"start": v(110.44, -45.54) * mm, "end": v(110.58, -45.54) * mm});
            skLineSegment(sketch, "E6859", {"start": v(110.58, -45.54) * mm, "end": v(110.71, -45.55) * mm});
            skLineSegment(sketch, "E6860", {"start": v(110.71, -45.55) * mm, "end": v(110.85, -45.55) * mm});
            skLineSegment(sketch, "E6861", {"start": v(110.85, -45.55) * mm, "end": v(111, -45.55) * mm});
            skLineSegment(sketch, "E6862", {"start": v(111, -45.55) * mm, "end": v(111.13, -45.56) * mm});
            skLineSegment(sketch, "E6863", {"start": v(111.13, -45.56) * mm, "end": v(111.27, -45.56) * mm});
            skLineSegment(sketch, "E6864", {"start": v(111.27, -45.56) * mm, "end": v(111.56, -45.56) * mm});
            skLineSegment(sketch, "E6865", {"start": v(111.56, -45.56) * mm, "end": v(111.7, -45.56) * mm});
            skLineSegment(sketch, "E6866", {"start": v(111.7, -45.56) * mm, "end": v(112, -45.56) * mm});
            skLineSegment(sketch, "E6867", {"start": v(112, -45.56) * mm, "end": v(112.15, -45.56) * mm});
            skLineSegment(sketch, "E6868", {"start": v(112.15, -45.56) * mm, "end": v(112.3, -45.56) * mm});
            skLineSegment(sketch, "E6869", {"start": v(112.3, -45.56) * mm, "end": v(112.4, -45.54) * mm});
            skLineSegment(sketch, "E6870", {"start": v(112.4, -45.54) * mm, "end": v(113, -44) * mm});
            skLineSegment(sketch, "E6871", {"start": v(113, -44) * mm, "end": v(112.96, -43.91) * mm});
            skLineSegment(sketch, "E6872", {"start": v(112.96, -43.91) * mm, "end": v(112.85, -43.8) * mm});
            skLineSegment(sketch, "E6873", {"start": v(112.85, -43.8) * mm, "end": v(112.63, -43.6) * mm});
            skLineSegment(sketch, "E6874", {"start": v(112.63, -43.6) * mm, "end": v(112.52, -43.5) * mm});
            skLineSegment(sketch, "E6875", {"start": v(112.52, -43.5) * mm, "end": v(112.42, -43.4) * mm});
            skLineSegment(sketch, "E6876", {"start": v(112.42, -43.4) * mm, "end": v(112.31, -43.3) * mm});
            skLineSegment(sketch, "E6877", {"start": v(112.31, -43.3) * mm, "end": v(112.2, -43.2) * mm});
            skLineSegment(sketch, "E6878", {"start": v(112.2, -43.2) * mm, "end": v(112.1, -43.11) * mm});
            skLineSegment(sketch, "E6879", {"start": v(112.1, -43.11) * mm, "end": v(112, -43.02) * mm});
            skLineSegment(sketch, "E6880", {"start": v(112, -43.02) * mm, "end": v(111.9, -42.93) * mm});
            skLineSegment(sketch, "E6881", {"start": v(111.9, -42.93) * mm, "end": v(111.8, -42.83) * mm});
            skLineSegment(sketch, "E6882", {"start": v(111.8, -42.83) * mm, "end": v(111.7, -42.74) * mm});
            skLineSegment(sketch, "E6883", {"start": v(111.7, -42.74) * mm, "end": v(111.59, -42.65) * mm});
            skLineSegment(sketch, "E6884", {"start": v(111.59, -42.65) * mm, "end": v(111.49, -42.56) * mm});
            skLineSegment(sketch, "E6885", {"start": v(111.49, -42.56) * mm, "end": v(111.39, -42.48) * mm});
            skLineSegment(sketch, "E6886", {"start": v(111.39, -42.48) * mm, "end": v(111.29, -42.39) * mm});
            skLineSegment(sketch, "E6887", {"start": v(111.29, -42.39) * mm, "end": v(111.19, -42.3) * mm});
            skLineSegment(sketch, "E6888", {"start": v(111.19, -42.3) * mm, "end": v(111.09, -42.22) * mm});
            skLineSegment(sketch, "E6889", {"start": v(111.09, -42.22) * mm, "end": v(110.99, -42.13) * mm});
            skLineSegment(sketch, "E6890", {"start": v(110.99, -42.13) * mm, "end": v(110.9, -42.05) * mm});
            skLineSegment(sketch, "E6891", {"start": v(110.9, -42.05) * mm, "end": v(110.8, -41.97) * mm});
            skLineSegment(sketch, "E6892", {"start": v(110.8, -41.97) * mm, "end": v(110.7, -41.9) * mm});
            skLineSegment(sketch, "E6893", {"start": v(110.7, -41.9) * mm, "end": v(110.6, -41.81) * mm});
            skLineSegment(sketch, "E6894", {"start": v(110.6, -41.81) * mm, "end": v(110.5, -41.73) * mm});
            skLineSegment(sketch, "E6895", {"start": v(110.5, -41.73) * mm, "end": v(110.41, -41.66) * mm});
            skLineSegment(sketch, "E6896", {"start": v(110.41, -41.66) * mm, "end": v(110.32, -41.58) * mm});
            skLineSegment(sketch, "E6897", {"start": v(110.32, -41.58) * mm, "end": v(110.23, -41.5) * mm});
            skLineSegment(sketch, "E6898", {"start": v(110.23, -41.5) * mm, "end": v(110.04, -41.36) * mm});
            skLineSegment(sketch, "E6899", {"start": v(110.04, -41.36) * mm, "end": v(109.95, -41.28) * mm});
            skLineSegment(sketch, "E6900", {"start": v(109.95, -41.28) * mm, "end": v(109.77, -41.14) * mm});
            skLineSegment(sketch, "E6901", {"start": v(109.77, -41.14) * mm, "end": v(109.68, -41.08) * mm});
            skLineSegment(sketch, "E6902", {"start": v(109.68, -41.08) * mm, "end": v(109.6, -41) * mm});
            skLineSegment(sketch, "E6903", {"start": v(109.6, -41) * mm, "end": v(109.42, -40.87) * mm});
            skLineSegment(sketch, "E6904", {"start": v(109.42, -40.87) * mm, "end": v(109.34, -40.8) * mm});
            skLineSegment(sketch, "E6905", {"start": v(109.34, -40.8) * mm, "end": v(109.5, -39.85) * mm});
            skLineSegment(sketch, "E6906", {"start": v(109.5, -39.85) * mm, "end": v(110, -39) * mm});
            skLineSegment(sketch, "E6907", {"start": v(110, -39) * mm, "end": v(110.1, -39.01) * mm});
            skLineSegment(sketch, "E6908", {"start": v(110.1, -39.01) * mm, "end": v(110.2, -39.02) * mm});
            skLineSegment(sketch, "E6909", {"start": v(110.2, -39.02) * mm, "end": v(110.32, -39.02) * mm});
            skLineSegment(sketch, "E6910", {"start": v(110.32, -39.02) * mm, "end": v(110.43, -39.03) * mm});
            skLineSegment(sketch, "E6911", {"start": v(110.43, -39.03) * mm, "end": v(110.66, -39.03) * mm});
            skLineSegment(sketch, "E6912", {"start": v(110.66, -39.03) * mm, "end": v(110.77, -39.04) * mm});
            skLineSegment(sketch, "E6913", {"start": v(110.77, -39.04) * mm, "end": v(110.89, -39.04) * mm});
            skLineSegment(sketch, "E6914", {"start": v(110.89, -39.04) * mm, "end": v(111, -39.04) * mm});
            skLineSegment(sketch, "E6915", {"start": v(111, -39.04) * mm, "end": v(111.12, -39.05) * mm});
            skLineSegment(sketch, "E6916", {"start": v(111.12, -39.05) * mm, "end": v(111.24, -39.05) * mm});
            skLineSegment(sketch, "E6917", {"start": v(111.24, -39.05) * mm, "end": v(111.36, -39.05) * mm});
            skLineSegment(sketch, "E6918", {"start": v(111.36, -39.05) * mm, "end": v(111.6, -39.05) * mm});
            skLineSegment(sketch, "E6919", {"start": v(111.6, -39.05) * mm, "end": v(112.11, -39.05) * mm});
            skLineSegment(sketch, "E6920", {"start": v(112.11, -39.05) * mm, "end": v(112.24, -39.05) * mm});
            skLineSegment(sketch, "E6921", {"start": v(112.24, -39.05) * mm, "end": v(112.5, -39.05) * mm});
            skLineSegment(sketch, "E6922", {"start": v(112.5, -39.05) * mm, "end": v(112.63, -39.05) * mm});
            skLineSegment(sketch, "E6923", {"start": v(112.63, -39.05) * mm, "end": v(112.77, -39.04) * mm});
            skLineSegment(sketch, "E6924", {"start": v(112.77, -39.04) * mm, "end": v(112.9, -39.04) * mm});
            skLineSegment(sketch, "E6925", {"start": v(112.9, -39.04) * mm, "end": v(113.04, -39.04) * mm});
            skLineSegment(sketch, "E6926", {"start": v(113.04, -39.04) * mm, "end": v(113.31, -39.03) * mm});
            skLineSegment(sketch, "E6927", {"start": v(113.31, -39.03) * mm, "end": v(113.45, -39.02) * mm});
            skLineSegment(sketch, "E6928", {"start": v(113.45, -39.02) * mm, "end": v(113.6, -39.02) * mm});
            skLineSegment(sketch, "E6929", {"start": v(113.6, -39.02) * mm, "end": v(113.73, -39.01) * mm});
            skLineSegment(sketch, "E6930", {"start": v(113.73, -39.01) * mm, "end": v(113.88, -39) * mm});
            skLineSegment(sketch, "E6931", {"start": v(113.88, -39) * mm, "end": v(114.02, -39) * mm});
            skLineSegment(sketch, "E6932", {"start": v(114.02, -39) * mm, "end": v(114.17, -38.99) * mm});
            skLineSegment(sketch, "E6933", {"start": v(114.17, -38.99) * mm, "end": v(114.31, -38.98) * mm});
            skLineSegment(sketch, "E6934", {"start": v(114.31, -38.98) * mm, "end": v(114.46, -38.97) * mm});
            skLineSegment(sketch, "E6935", {"start": v(114.46, -38.97) * mm, "end": v(114.6, -38.96) * mm});
            skLineSegment(sketch, "E6936", {"start": v(114.6, -38.96) * mm, "end": v(114.76, -38.95) * mm});
            skLineSegment(sketch, "E6937", {"start": v(114.76, -38.95) * mm, "end": v(114.85, -38.92) * mm});
            skLineSegment(sketch, "E6938", {"start": v(114.85, -38.92) * mm, "end": v(115.37, -37.35) * mm});
            skLineSegment(sketch, "E6939", {"start": v(115.37, -37.35) * mm, "end": v(115.32, -37.27) * mm});
            skLineSegment(sketch, "E6940", {"start": v(115.32, -37.27) * mm, "end": v(115.09, -37.08) * mm});
            skLineSegment(sketch, "E6941", {"start": v(115.09, -37.08) * mm, "end": v(114.98, -36.98) * mm});
            skLineSegment(sketch, "E6942", {"start": v(114.98, -36.98) * mm, "end": v(114.86, -36.89) * mm});
            skLineSegment(sketch, "E6943", {"start": v(114.86, -36.89) * mm, "end": v(114.64, -36.7) * mm});
            skLineSegment(sketch, "E6944", {"start": v(114.64, -36.7) * mm, "end": v(114.42, -36.52) * mm});
            skLineSegment(sketch, "E6945", {"start": v(114.42, -36.52) * mm, "end": v(114.2, -36.35) * mm});
            skLineSegment(sketch, "E6946", {"start": v(114.2, -36.35) * mm, "end": v(114.1, -36.26) * mm});
            skLineSegment(sketch, "E6947", {"start": v(114.1, -36.26) * mm, "end": v(113.99, -36.18) * mm});
            skLineSegment(sketch, "E6948", {"start": v(113.99, -36.18) * mm, "end": v(113.88, -36.1) * mm});
            skLineSegment(sketch, "E6949", {"start": v(113.88, -36.1) * mm, "end": v(113.67, -35.93) * mm});
            skLineSegment(sketch, "E6950", {"start": v(113.67, -35.93) * mm, "end": v(113.46, -35.77) * mm});
            skLineSegment(sketch, "E6951", {"start": v(113.46, -35.77) * mm, "end": v(113.35, -35.69) * mm});
            skLineSegment(sketch, "E6952", {"start": v(113.35, -35.69) * mm, "end": v(113.25, -35.6) * mm});
            skLineSegment(sketch, "E6953", {"start": v(113.25, -35.6) * mm, "end": v(113.15, -35.53) * mm});
            skLineSegment(sketch, "E6954", {"start": v(113.15, -35.53) * mm, "end": v(113.05, -35.46) * mm});
            skLineSegment(sketch, "E6955", {"start": v(113.05, -35.46) * mm, "end": v(112.95, -35.38) * mm});
            skLineSegment(sketch, "E6956", {"start": v(112.95, -35.38) * mm, "end": v(112.85, -35.3) * mm});
            skLineSegment(sketch, "E6957", {"start": v(112.85, -35.3) * mm, "end": v(112.75, -35.24) * mm});
            skLineSegment(sketch, "E6958", {"start": v(112.75, -35.24) * mm, "end": v(112.65, -35.16) * mm});
            skLineSegment(sketch, "E6959", {"start": v(112.65, -35.16) * mm, "end": v(112.55, -35.1) * mm});
            skLineSegment(sketch, "E6960", {"start": v(112.55, -35.1) * mm, "end": v(112.45, -35.02) * mm});
            skLineSegment(sketch, "E6961", {"start": v(112.45, -35.02) * mm, "end": v(112.26, -34.89) * mm});
            skLineSegment(sketch, "E6962", {"start": v(112.26, -34.89) * mm, "end": v(112.17, -34.82) * mm});
            skLineSegment(sketch, "E6963", {"start": v(112.17, -34.82) * mm, "end": v(111.98, -34.7) * mm});
            skLineSegment(sketch, "E6964", {"start": v(111.98, -34.7) * mm, "end": v(111.89, -34.63) * mm});
            skLineSegment(sketch, "E6965", {"start": v(111.89, -34.63) * mm, "end": v(111.8, -34.57) * mm});
            skLineSegment(sketch, "E6966", {"start": v(111.8, -34.57) * mm, "end": v(111.7, -34.5) * mm});
            skLineSegment(sketch, "E6967", {"start": v(111.7, -34.5) * mm, "end": v(111.61, -34.44) * mm});
            skLineSegment(sketch, "E6968", {"start": v(111.61, -34.44) * mm, "end": v(111.52, -34.38) * mm});
            skLineSegment(sketch, "E6969", {"start": v(111.52, -34.38) * mm, "end": v(111.63, -33.41) * mm});
            skLineSegment(sketch, "E6970", {"start": v(111.63, -33.41) * mm, "end": v(112.07, -32.55) * mm});
            skLineSegment(sketch, "E6971", {"start": v(112.07, -32.55) * mm, "end": v(112.3, -32.54) * mm});
            skLineSegment(sketch, "E6972", {"start": v(112.3, -32.54) * mm, "end": v(112.51, -32.54) * mm});
            skLineSegment(sketch, "E6973", {"start": v(112.51, -32.54) * mm, "end": v(112.62, -32.54) * mm});
            skLineSegment(sketch, "E6974", {"start": v(112.62, -32.54) * mm, "end": v(112.85, -32.53) * mm});
            skLineSegment(sketch, "E6975", {"start": v(112.85, -32.53) * mm, "end": v(112.97, -32.53) * mm});
            skLineSegment(sketch, "E6976", {"start": v(112.97, -32.53) * mm, "end": v(113.09, -32.52) * mm});
            skLineSegment(sketch, "E6977", {"start": v(113.09, -32.52) * mm, "end": v(113.2, -32.52) * mm});
            skLineSegment(sketch, "E6978", {"start": v(113.2, -32.52) * mm, "end": v(113.32, -32.51) * mm});
            skLineSegment(sketch, "E6979", {"start": v(113.32, -32.51) * mm, "end": v(113.44, -32.5) * mm});
            skLineSegment(sketch, "E6980", {"start": v(113.44, -32.5) * mm, "end": v(113.69, -32.5) * mm});
            skLineSegment(sketch, "E6981", {"start": v(113.69, -32.5) * mm, "end": v(113.81, -32.5) * mm});
            skLineSegment(sketch, "E6982", {"start": v(113.81, -32.5) * mm, "end": v(113.94, -32.48) * mm});
            skLineSegment(sketch, "E6983", {"start": v(113.94, -32.48) * mm, "end": v(114.06, -32.48) * mm});
            skLineSegment(sketch, "E6984", {"start": v(114.06, -32.48) * mm, "end": v(114.2, -32.47) * mm});
            skLineSegment(sketch, "E6985", {"start": v(114.2, -32.47) * mm, "end": v(114.32, -32.46) * mm});
            skLineSegment(sketch, "E6986", {"start": v(114.32, -32.46) * mm, "end": v(114.45, -32.45) * mm});
            skLineSegment(sketch, "E6987", {"start": v(114.45, -32.45) * mm, "end": v(114.58, -32.44) * mm});
            skLineSegment(sketch, "E6988", {"start": v(114.58, -32.44) * mm, "end": v(114.71, -32.43) * mm});
            skLineSegment(sketch, "E6989", {"start": v(114.71, -32.43) * mm, "end": v(114.98, -32.41) * mm});
            skLineSegment(sketch, "E6990", {"start": v(114.98, -32.41) * mm, "end": v(115.12, -32.4) * mm});
            skLineSegment(sketch, "E6991", {"start": v(115.12, -32.4) * mm, "end": v(115.25, -32.39) * mm});
            skLineSegment(sketch, "E6992", {"start": v(115.25, -32.39) * mm, "end": v(115.4, -32.37) * mm});
            skLineSegment(sketch, "E6993", {"start": v(115.4, -32.37) * mm, "end": v(115.53, -32.36) * mm});
            skLineSegment(sketch, "E6994", {"start": v(115.53, -32.36) * mm, "end": v(115.81, -32.33) * mm});
            skLineSegment(sketch, "E6995", {"start": v(115.81, -32.33) * mm, "end": v(115.95, -32.32) * mm});
            skLineSegment(sketch, "E6996", {"start": v(115.95, -32.32) * mm, "end": v(116.1, -32.3) * mm});
            skLineSegment(sketch, "E6997", {"start": v(116.1, -32.3) * mm, "end": v(116.24, -32.29) * mm});
            skLineSegment(sketch, "E6998", {"start": v(116.24, -32.29) * mm, "end": v(116.53, -32.25) * mm});
            skLineSegment(sketch, "E6999", {"start": v(116.53, -32.25) * mm, "end": v(116.68, -32.24) * mm});
            skLineSegment(sketch, "E7000", {"start": v(116.68, -32.24) * mm, "end": v(116.83, -32.22) * mm});
            skLineSegment(sketch, "E7001", {"start": v(116.83, -32.22) * mm, "end": v(116.92, -32.18) * mm});
            skLineSegment(sketch, "E7002", {"start": v(116.92, -32.18) * mm, "end": v(117.35, -30.58) * mm});
            skLineSegment(sketch, "E7003", {"start": v(117.35, -30.58) * mm, "end": v(117.29, -30.5) * mm});
            skLineSegment(sketch, "E7004", {"start": v(117.29, -30.5) * mm, "end": v(117.17, -30.41) * mm});
            skLineSegment(sketch, "E7005", {"start": v(117.17, -30.41) * mm, "end": v(117.05, -30.32) * mm});
            skLineSegment(sketch, "E7006", {"start": v(117.05, -30.32) * mm, "end": v(116.93, -30.23) * mm});
            skLineSegment(sketch, "E7007", {"start": v(116.93, -30.23) * mm, "end": v(116.81, -30.15) * mm});
            skLineSegment(sketch, "E7008", {"start": v(116.81, -30.15) * mm, "end": v(116.7, -30.06) * mm});
            skLineSegment(sketch, "E7009", {"start": v(116.7, -30.06) * mm, "end": v(116.58, -29.98) * mm});
            skLineSegment(sketch, "E7010", {"start": v(116.58, -29.98) * mm, "end": v(116.47, -29.9) * mm});
            skLineSegment(sketch, "E7011", {"start": v(116.47, -29.9) * mm, "end": v(116.35, -29.8) * mm});
            skLineSegment(sketch, "E7012", {"start": v(116.35, -29.8) * mm, "end": v(116.23, -29.73) * mm});
            skLineSegment(sketch, "E7013", {"start": v(116.23, -29.73) * mm, "end": v(116.12, -29.65) * mm});
            skLineSegment(sketch, "E7014", {"start": v(116.12, -29.65) * mm, "end": v(116, -29.57) * mm});
            skLineSegment(sketch, "E7015", {"start": v(116, -29.57) * mm, "end": v(115.9, -29.49) * mm});
            skLineSegment(sketch, "E7016", {"start": v(115.9, -29.49) * mm, "end": v(115.67, -29.33) * mm});
            skLineSegment(sketch, "E7017", {"start": v(115.67, -29.33) * mm, "end": v(115.56, -29.26) * mm});
            skLineSegment(sketch, "E7018", {"start": v(115.56, -29.26) * mm, "end": v(115.35, -29.1) * mm});
            skLineSegment(sketch, "E7019", {"start": v(115.35, -29.1) * mm, "end": v(115.13, -28.96) * mm});
            skLineSegment(sketch, "E7020", {"start": v(115.13, -28.96) * mm, "end": v(114.92, -28.82) * mm});
            skLineSegment(sketch, "E7021", {"start": v(114.92, -28.82) * mm, "end": v(114.81, -28.76) * mm});
            skLineSegment(sketch, "E7022", {"start": v(114.81, -28.76) * mm, "end": v(114.7, -28.69) * mm});
            skLineSegment(sketch, "E7023", {"start": v(114.7, -28.69) * mm, "end": v(114.6, -28.62) * mm});
            skLineSegment(sketch, "E7024", {"start": v(114.6, -28.62) * mm, "end": v(114.5, -28.56) * mm});
            skLineSegment(sketch, "E7025", {"start": v(114.5, -28.56) * mm, "end": v(114.4, -28.5) * mm});
            skLineSegment(sketch, "E7026", {"start": v(114.4, -28.5) * mm, "end": v(114.2, -28.36) * mm});
            skLineSegment(sketch, "E7027", {"start": v(114.2, -28.36) * mm, "end": v(114.1, -28.3) * mm});
            skLineSegment(sketch, "E7028", {"start": v(114.1, -28.3) * mm, "end": v(114, -28.24) * mm});
            skLineSegment(sketch, "E7029", {"start": v(114, -28.24) * mm, "end": v(113.9, -28.18) * mm});
            skLineSegment(sketch, "E7030", {"start": v(113.9, -28.18) * mm, "end": v(113.8, -28.12) * mm});
            skLineSegment(sketch, "E7031", {"start": v(113.8, -28.12) * mm, "end": v(113.71, -28.06) * mm});
            skLineSegment(sketch, "E7032", {"start": v(113.71, -28.06) * mm, "end": v(113.62, -28) * mm});
            skLineSegment(sketch, "E7033", {"start": v(113.62, -28) * mm, "end": v(113.52, -27.95) * mm});
            skLineSegment(sketch, "E7034", {"start": v(113.52, -27.95) * mm, "end": v(113.43, -27.9) * mm});
            skLineSegment(sketch, "E7035", {"start": v(113.43, -27.9) * mm, "end": v(113.33, -27.84) * mm});
            skLineSegment(sketch, "E7036", {"start": v(113.33, -27.84) * mm, "end": v(113.39, -26.87) * mm});
            skLineSegment(sketch, "E7037", {"start": v(113.39, -26.87) * mm, "end": v(113.78, -25.97) * mm});
            skLineSegment(sketch, "E7038", {"start": v(113.78, -25.97) * mm, "end": v(113.88, -25.97) * mm});
            skLineSegment(sketch, "E7039", {"start": v(113.88, -25.97) * mm, "end": v(114, -25.96) * mm});
            skLineSegment(sketch, "E7040", {"start": v(114, -25.96) * mm, "end": v(114.1, -25.95) * mm});
            skLineSegment(sketch, "E7041", {"start": v(114.1, -25.95) * mm, "end": v(114.21, -25.94) * mm});
            skLineSegment(sketch, "E7042", {"start": v(114.21, -25.94) * mm, "end": v(114.33, -25.93) * mm});
            skLineSegment(sketch, "E7043", {"start": v(114.33, -25.93) * mm, "end": v(114.44, -25.92) * mm});
            skLineSegment(sketch, "E7044", {"start": v(114.44, -25.92) * mm, "end": v(114.55, -25.91) * mm});
            skLineSegment(sketch, "E7045", {"start": v(114.55, -25.91) * mm, "end": v(114.67, -25.9) * mm});
            skLineSegment(sketch, "E7046", {"start": v(114.67, -25.9) * mm, "end": v(114.9, -25.88) * mm});
            skLineSegment(sketch, "E7047", {"start": v(114.9, -25.88) * mm, "end": v(115.02, -25.87) * mm});
            skLineSegment(sketch, "E7048", {"start": v(115.02, -25.87) * mm, "end": v(115.14, -25.86) * mm});
            skLineSegment(sketch, "E7049", {"start": v(115.14, -25.86) * mm, "end": v(115.26, -25.85) * mm});
            skLineSegment(sketch, "E7050", {"start": v(115.26, -25.85) * mm, "end": v(115.39, -25.83) * mm});
            skLineSegment(sketch, "E7051", {"start": v(115.39, -25.83) * mm, "end": v(115.51, -25.82) * mm});
            skLineSegment(sketch, "E7052", {"start": v(115.51, -25.82) * mm, "end": v(115.63, -25.8) * mm});
            skLineSegment(sketch, "E7053", {"start": v(115.63, -25.8) * mm, "end": v(115.76, -25.79) * mm});
            skLineSegment(sketch, "E7054", {"start": v(115.76, -25.79) * mm, "end": v(115.89, -25.77) * mm});
            skLineSegment(sketch, "E7055", {"start": v(115.89, -25.77) * mm, "end": v(116.14, -25.74) * mm});
            skLineSegment(sketch, "E7056", {"start": v(116.14, -25.74) * mm, "end": v(116.27, -25.73) * mm});
            skLineSegment(sketch, "E7057", {"start": v(116.27, -25.73) * mm, "end": v(116.4, -25.7) * mm});
            skLineSegment(sketch, "E7058", {"start": v(116.4, -25.7) * mm, "end": v(116.54, -25.69) * mm});
            skLineSegment(sketch, "E7059", {"start": v(116.54, -25.69) * mm, "end": v(116.8, -25.65) * mm});
            skLineSegment(sketch, "E7060", {"start": v(116.8, -25.65) * mm, "end": v(117.08, -25.6) * mm});
            skLineSegment(sketch, "E7061", {"start": v(117.08, -25.6) * mm, "end": v(117.22, -25.59) * mm});
            skLineSegment(sketch, "E7062", {"start": v(117.22, -25.59) * mm, "end": v(117.5, -25.54) * mm});
            skLineSegment(sketch, "E7063", {"start": v(117.5, -25.54) * mm, "end": v(117.78, -25.5) * mm});
            skLineSegment(sketch, "E7064", {"start": v(117.78, -25.5) * mm, "end": v(118.06, -25.45) * mm});
            skLineSegment(sketch, "E7065", {"start": v(118.06, -25.45) * mm, "end": v(118.36, -25.4) * mm});
            skLineSegment(sketch, "E7066", {"start": v(118.36, -25.4) * mm, "end": v(118.5, -25.37) * mm});
            skLineSegment(sketch, "E7067", {"start": v(118.5, -25.37) * mm, "end": v(118.6, -25.33) * mm});
            skLineSegment(sketch, "E7068", {"start": v(118.6, -25.33) * mm, "end": v(118.93, -23.7) * mm});
            skLineSegment(sketch, "E7069", {"start": v(118.93, -23.7) * mm, "end": v(118.86, -23.63) * mm});
            skLineSegment(sketch, "E7070", {"start": v(118.86, -23.63) * mm, "end": v(118.74, -23.55) * mm});
            skLineSegment(sketch, "E7071", {"start": v(118.74, -23.55) * mm, "end": v(118.61, -23.47) * mm});
            skLineSegment(sketch, "E7072", {"start": v(118.61, -23.47) * mm, "end": v(118.37, -23.3) * mm});
            skLineSegment(sketch, "E7073", {"start": v(118.37, -23.3) * mm, "end": v(118.25, -23.22) * mm});
            skLineSegment(sketch, "E7074", {"start": v(118.25, -23.22) * mm, "end": v(118.13, -23.15) * mm});
            skLineSegment(sketch, "E7075", {"start": v(118.13, -23.15) * mm, "end": v(118, -23.07) * mm});
            skLineSegment(sketch, "E7076", {"start": v(118, -23.07) * mm, "end": v(117.89, -23) * mm});
            skLineSegment(sketch, "E7077", {"start": v(117.89, -23) * mm, "end": v(117.65, -22.84) * mm});
            skLineSegment(sketch, "E7078", {"start": v(117.65, -22.84) * mm, "end": v(117.53, -22.77) * mm});
            skLineSegment(sketch, "E7079", {"start": v(117.53, -22.77) * mm, "end": v(117.42, -22.7) * mm});
            skLineSegment(sketch, "E7080", {"start": v(117.42, -22.7) * mm, "end": v(117.3, -22.63) * mm});
            skLineSegment(sketch, "E7081", {"start": v(117.3, -22.63) * mm, "end": v(117.18, -22.56) * mm});
            skLineSegment(sketch, "E7082", {"start": v(117.18, -22.56) * mm, "end": v(117.07, -22.49) * mm});
            skLineSegment(sketch, "E7083", {"start": v(117.07, -22.49) * mm, "end": v(116.84, -22.35) * mm});
            skLineSegment(sketch, "E7084", {"start": v(116.84, -22.35) * mm, "end": v(116.62, -22.22) * mm});
            skLineSegment(sketch, "E7085", {"start": v(116.62, -22.22) * mm, "end": v(116.4, -22.1) * mm});
            skLineSegment(sketch, "E7086", {"start": v(116.4, -22.1) * mm, "end": v(116.3, -22.03) * mm});
            skLineSegment(sketch, "E7087", {"start": v(116.3, -22.03) * mm, "end": v(116.08, -21.9) * mm});
            skLineSegment(sketch, "E7088", {"start": v(116.08, -21.9) * mm, "end": v(115.97, -21.85) * mm});
            skLineSegment(sketch, "E7089", {"start": v(115.97, -21.85) * mm, "end": v(115.76, -21.73) * mm});
            skLineSegment(sketch, "E7090", {"start": v(115.76, -21.73) * mm, "end": v(115.66, -21.68) * mm});
            skLineSegment(sketch, "E7091", {"start": v(115.66, -21.68) * mm, "end": v(115.55, -21.62) * mm});
            skLineSegment(sketch, "E7092", {"start": v(115.55, -21.62) * mm, "end": v(115.35, -21.5) * mm});
            skLineSegment(sketch, "E7093", {"start": v(115.35, -21.5) * mm, "end": v(115.25, -21.46) * mm});
            skLineSegment(sketch, "E7094", {"start": v(115.25, -21.46) * mm, "end": v(115.05, -21.35) * mm});
            skLineSegment(sketch, "E7095", {"start": v(115.05, -21.35) * mm, "end": v(114.95, -21.3) * mm});
            skLineSegment(sketch, "E7096", {"start": v(114.95, -21.3) * mm, "end": v(114.76, -21.2) * mm});
            skLineSegment(sketch, "E7097", {"start": v(114.76, -21.2) * mm, "end": v(114.76, -20.23) * mm});
            skLineSegment(sketch, "E7098", {"start": v(114.76, -20.23) * mm, "end": v(115.1, -19.31) * mm});
            skLineSegment(sketch, "E7099", {"start": v(115.1, -19.31) * mm, "end": v(115.2, -19.3) * mm});
            skLineSegment(sketch, "E7100", {"start": v(115.2, -19.3) * mm, "end": v(115.3, -19.29) * mm});
            skLineSegment(sketch, "E7101", {"start": v(115.3, -19.29) * mm, "end": v(115.53, -19.26) * mm});
            skLineSegment(sketch, "E7102", {"start": v(115.53, -19.26) * mm, "end": v(115.75, -19.23) * mm});
            skLineSegment(sketch, "E7103", {"start": v(115.75, -19.23) * mm, "end": v(115.98, -19.2) * mm});
            skLineSegment(sketch, "E7104", {"start": v(115.98, -19.2) * mm, "end": v(116.1, -19.18) * mm});
            skLineSegment(sketch, "E7105", {"start": v(116.1, -19.18) * mm, "end": v(116.21, -19.16) * mm});
            skLineSegment(sketch, "E7106", {"start": v(116.21, -19.16) * mm, "end": v(116.33, -19.14) * mm});
            skLineSegment(sketch, "E7107", {"start": v(116.33, -19.14) * mm, "end": v(116.45, -19.12) * mm});
            skLineSegment(sketch, "E7108", {"start": v(116.45, -19.12) * mm, "end": v(116.7, -19.08) * mm});
            skLineSegment(sketch, "E7109", {"start": v(116.7, -19.08) * mm, "end": v(116.94, -19.04) * mm});
            skLineSegment(sketch, "E7110", {"start": v(116.94, -19.04) * mm, "end": v(117.06, -19.02) * mm});
            skLineSegment(sketch, "E7111", {"start": v(117.06, -19.02) * mm, "end": v(117.19, -19) * mm});
            skLineSegment(sketch, "E7112", {"start": v(117.19, -19) * mm, "end": v(117.32, -18.97) * mm});
            skLineSegment(sketch, "E7113", {"start": v(117.32, -18.97) * mm, "end": v(117.44, -18.95) * mm});
            skLineSegment(sketch, "E7114", {"start": v(117.44, -18.95) * mm, "end": v(117.57, -18.92) * mm});
            skLineSegment(sketch, "E7115", {"start": v(117.57, -18.92) * mm, "end": v(117.7, -18.9) * mm});
            skLineSegment(sketch, "E7116", {"start": v(117.7, -18.9) * mm, "end": v(117.83, -18.87) * mm});
            skLineSegment(sketch, "E7117", {"start": v(117.83, -18.87) * mm, "end": v(117.97, -18.84) * mm});
            skLineSegment(sketch, "E7118", {"start": v(117.97, -18.84) * mm, "end": v(118.1, -18.82) * mm});
            skLineSegment(sketch, "E7119", {"start": v(118.1, -18.82) * mm, "end": v(118.23, -18.79) * mm});
            skLineSegment(sketch, "E7120", {"start": v(118.23, -18.79) * mm, "end": v(118.37, -18.76) * mm});
            skLineSegment(sketch, "E7121", {"start": v(118.37, -18.76) * mm, "end": v(118.5, -18.73) * mm});
            skLineSegment(sketch, "E7122", {"start": v(118.5, -18.73) * mm, "end": v(118.64, -18.7) * mm});
            skLineSegment(sketch, "E7123", {"start": v(118.64, -18.7) * mm, "end": v(118.78, -18.67) * mm});
            skLineSegment(sketch, "E7124", {"start": v(118.78, -18.67) * mm, "end": v(118.92, -18.64) * mm});
            skLineSegment(sketch, "E7125", {"start": v(118.92, -18.64) * mm, "end": v(119.06, -18.6) * mm});
            skLineSegment(sketch, "E7126", {"start": v(119.06, -18.6) * mm, "end": v(119.35, -18.54) * mm});
            skLineSegment(sketch, "E7127", {"start": v(119.35, -18.54) * mm, "end": v(119.49, -18.5) * mm});
            skLineSegment(sketch, "E7128", {"start": v(119.49, -18.5) * mm, "end": v(119.63, -18.47) * mm});
            skLineSegment(sketch, "E7129", {"start": v(119.63, -18.47) * mm, "end": v(119.78, -18.44) * mm});
            skLineSegment(sketch, "E7130", {"start": v(119.78, -18.44) * mm, "end": v(119.86, -18.39) * mm});
            skLineSegment(sketch, "E7131", {"start": v(119.86, -18.39) * mm, "end": v(120.1, -16.75) * mm});
            skLineSegment(sketch, "E7132", {"start": v(120.1, -16.75) * mm, "end": v(120.04, -16.68) * mm});
            skLineSegment(sketch, "E7133", {"start": v(120.04, -16.68) * mm, "end": v(119.9, -16.6) * mm});
            skLineSegment(sketch, "E7134", {"start": v(119.9, -16.6) * mm, "end": v(119.65, -16.45) * mm});
            skLineSegment(sketch, "E7135", {"start": v(119.65, -16.45) * mm, "end": v(119.52, -16.38) * mm});
            skLineSegment(sketch, "E7136", {"start": v(119.52, -16.38) * mm, "end": v(119.4, -16.3) * mm});
            skLineSegment(sketch, "E7137", {"start": v(119.4, -16.3) * mm, "end": v(119.27, -16.24) * mm});
            skLineSegment(sketch, "E7138", {"start": v(119.27, -16.24) * mm, "end": v(119.15, -16.17) * mm});
            skLineSegment(sketch, "E7139", {"start": v(119.15, -16.17) * mm, "end": v(118.9, -16.03) * mm});
            skLineSegment(sketch, "E7140", {"start": v(118.9, -16.03) * mm, "end": v(118.66, -15.9) * mm});
            skLineSegment(sketch, "E7141", {"start": v(118.66, -15.9) * mm, "end": v(118.54, -15.83) * mm});
            skLineSegment(sketch, "E7142", {"start": v(118.54, -15.83) * mm, "end": v(118.42, -15.77) * mm});
            skLineSegment(sketch, "E7143", {"start": v(118.42, -15.77) * mm, "end": v(118.3, -15.7) * mm});
            skLineSegment(sketch, "E7144", {"start": v(118.3, -15.7) * mm, "end": v(118.18, -15.64) * mm});
            skLineSegment(sketch, "E7145", {"start": v(118.18, -15.64) * mm, "end": v(118.06, -15.58) * mm});
            skLineSegment(sketch, "E7146", {"start": v(118.06, -15.58) * mm, "end": v(117.94, -15.52) * mm});
            skLineSegment(sketch, "E7147", {"start": v(117.94, -15.52) * mm, "end": v(117.83, -15.46) * mm});
            skLineSegment(sketch, "E7148", {"start": v(117.83, -15.46) * mm, "end": v(117.71, -15.4) * mm});
            skLineSegment(sketch, "E7149", {"start": v(117.71, -15.4) * mm, "end": v(117.6, -15.34) * mm});
            skLineSegment(sketch, "E7150", {"start": v(117.6, -15.34) * mm, "end": v(117.49, -15.29) * mm});
            skLineSegment(sketch, "E7151", {"start": v(117.49, -15.29) * mm, "end": v(117.38, -15.23) * mm});
            skLineSegment(sketch, "E7152", {"start": v(117.38, -15.23) * mm, "end": v(117.26, -15.18) * mm});
            skLineSegment(sketch, "E7153", {"start": v(117.26, -15.18) * mm, "end": v(117.15, -15.12) * mm});
            skLineSegment(sketch, "E7154", {"start": v(117.15, -15.12) * mm, "end": v(117.05, -15.07) * mm});
            skLineSegment(sketch, "E7155", {"start": v(117.05, -15.07) * mm, "end": v(116.94, -15.02) * mm});
            skLineSegment(sketch, "E7156", {"start": v(116.94, -15.02) * mm, "end": v(116.72, -14.91) * mm});
            skLineSegment(sketch, "E7157", {"start": v(116.72, -14.91) * mm, "end": v(116.62, -14.87) * mm});
            skLineSegment(sketch, "E7158", {"start": v(116.62, -14.87) * mm, "end": v(116.51, -14.82) * mm});
            skLineSegment(sketch, "E7159", {"start": v(116.51, -14.82) * mm, "end": v(116.4, -14.77) * mm});
            skLineSegment(sketch, "E7160", {"start": v(116.4, -14.77) * mm, "end": v(116.3, -14.72) * mm});
            skLineSegment(sketch, "E7161", {"start": v(116.3, -14.72) * mm, "end": v(116.2, -14.67) * mm});
            skLineSegment(sketch, "E7162", {"start": v(116.2, -14.67) * mm, "end": v(116.1, -14.63) * mm});
            skLineSegment(sketch, "E7163", {"start": v(116.1, -14.63) * mm, "end": v(116, -14.58) * mm});
            skLineSegment(sketch, "E7164", {"start": v(116, -14.58) * mm, "end": v(115.8, -14.5) * mm});
            skLineSegment(sketch, "E7165", {"start": v(115.8, -14.5) * mm, "end": v(115.74, -13.52) * mm});
            skLineSegment(sketch, "E7166", {"start": v(115.74, -13.52) * mm, "end": v(116.02, -12.59) * mm});
            skLineSegment(sketch, "E7167", {"start": v(116.02, -12.59) * mm, "end": v(116.23, -12.55) * mm});
            skLineSegment(sketch, "E7168", {"start": v(116.23, -12.55) * mm, "end": v(116.34, -12.53) * mm});
            skLineSegment(sketch, "E7169", {"start": v(116.34, -12.53) * mm, "end": v(116.45, -12.5) * mm});
            skLineSegment(sketch, "E7170", {"start": v(116.45, -12.5) * mm, "end": v(116.56, -12.49) * mm});
            skLineSegment(sketch, "E7171", {"start": v(116.56, -12.49) * mm, "end": v(116.67, -12.46) * mm});
            skLineSegment(sketch, "E7172", {"start": v(116.67, -12.46) * mm, "end": v(116.79, -12.44) * mm});
            skLineSegment(sketch, "E7173", {"start": v(116.79, -12.44) * mm, "end": v(116.9, -12.42) * mm});
            skLineSegment(sketch, "E7174", {"start": v(116.9, -12.42) * mm, "end": v(117.02, -12.4) * mm});
            skLineSegment(sketch, "E7175", {"start": v(117.02, -12.4) * mm, "end": v(117.13, -12.37) * mm});
            skLineSegment(sketch, "E7176", {"start": v(117.13, -12.37) * mm, "end": v(117.37, -12.32) * mm});
            skLineSegment(sketch, "E7177", {"start": v(117.37, -12.32) * mm, "end": v(117.48, -12.29) * mm});
            skLineSegment(sketch, "E7178", {"start": v(117.48, -12.29) * mm, "end": v(117.6, -12.26) * mm});
            skLineSegment(sketch, "E7179", {"start": v(117.6, -12.26) * mm, "end": v(117.73, -12.23) * mm});
            skLineSegment(sketch, "E7180", {"start": v(117.73, -12.23) * mm, "end": v(117.97, -12.18) * mm});
            skLineSegment(sketch, "E7181", {"start": v(117.97, -12.18) * mm, "end": v(118.1, -12.15) * mm});
            skLineSegment(sketch, "E7182", {"start": v(118.1, -12.15) * mm, "end": v(118.22, -12.12) * mm});
            skLineSegment(sketch, "E7183", {"start": v(118.22, -12.12) * mm, "end": v(118.47, -12.05) * mm});
            skLineSegment(sketch, "E7184", {"start": v(118.47, -12.05) * mm, "end": v(118.6, -12.02) * mm});
            skLineSegment(sketch, "E7185", {"start": v(118.6, -12.02) * mm, "end": v(118.73, -11.99) * mm});
            skLineSegment(sketch, "E7186", {"start": v(118.73, -11.99) * mm, "end": v(119, -11.92) * mm});
            skLineSegment(sketch, "E7187", {"start": v(119, -11.92) * mm, "end": v(119.13, -11.88) * mm});
            skLineSegment(sketch, "E7188", {"start": v(119.13, -11.88) * mm, "end": v(119.26, -11.85) * mm});
            skLineSegment(sketch, "E7189", {"start": v(119.26, -11.85) * mm, "end": v(119.4, -11.8) * mm});
            skLineSegment(sketch, "E7190", {"start": v(119.4, -11.8) * mm, "end": v(119.53, -11.77) * mm});
            skLineSegment(sketch, "E7191", {"start": v(119.53, -11.77) * mm, "end": v(119.67, -11.73) * mm});
            skLineSegment(sketch, "E7192", {"start": v(119.67, -11.73) * mm, "end": v(119.8, -11.7) * mm});
            skLineSegment(sketch, "E7193", {"start": v(119.8, -11.7) * mm, "end": v(119.94, -11.65) * mm});
            skLineSegment(sketch, "E7194", {"start": v(119.94, -11.65) * mm, "end": v(120.08, -11.61) * mm});
            skLineSegment(sketch, "E7195", {"start": v(120.08, -11.61) * mm, "end": v(120.22, -11.57) * mm});
            skLineSegment(sketch, "E7196", {"start": v(120.22, -11.57) * mm, "end": v(120.36, -11.53) * mm});
            skLineSegment(sketch, "E7197", {"start": v(120.36, -11.53) * mm, "end": v(120.5, -11.48) * mm});
            skLineSegment(sketch, "E7198", {"start": v(120.5, -11.48) * mm, "end": v(120.65, -11.44) * mm});
            skLineSegment(sketch, "E7199", {"start": v(120.65, -11.44) * mm, "end": v(120.73, -11.39) * mm});
            skLineSegment(sketch, "E7200", {"start": v(120.73, -11.39) * mm, "end": v(120.88, -9.74) * mm});
            skLineSegment(sketch, "E7201", {"start": v(120.88, -9.74) * mm, "end": v(120.8, -9.67) * mm});
            skLineSegment(sketch, "E7202", {"start": v(120.8, -9.67) * mm, "end": v(120.67, -9.6) * mm});
            skLineSegment(sketch, "E7203", {"start": v(120.67, -9.6) * mm, "end": v(120.54, -9.54) * mm});
            skLineSegment(sketch, "E7204", {"start": v(120.54, -9.54) * mm, "end": v(120.4, -9.47) * mm});
            skLineSegment(sketch, "E7205", {"start": v(120.4, -9.47) * mm, "end": v(120.27, -9.4) * mm});
            skLineSegment(sketch, "E7206", {"start": v(120.27, -9.4) * mm, "end": v(120.14, -9.34) * mm});
            skLineSegment(sketch, "E7207", {"start": v(120.14, -9.34) * mm, "end": v(120.01, -9.28) * mm});
            skLineSegment(sketch, "E7208", {"start": v(120.01, -9.28) * mm, "end": v(119.76, -9.15) * mm});
            skLineSegment(sketch, "E7209", {"start": v(119.76, -9.15) * mm, "end": v(119.63, -9.1) * mm});
            skLineSegment(sketch, "E7210", {"start": v(119.63, -9.1) * mm, "end": v(119.5, -9.03) * mm});
            skLineSegment(sketch, "E7211", {"start": v(119.5, -9.03) * mm, "end": v(119.38, -8.97) * mm});
            skLineSegment(sketch, "E7212", {"start": v(119.38, -8.97) * mm, "end": v(119.13, -8.86) * mm});
            skLineSegment(sketch, "E7213", {"start": v(119.13, -8.86) * mm, "end": v(119.01, -8.8) * mm});
            skLineSegment(sketch, "E7214", {"start": v(119.01, -8.8) * mm, "end": v(118.89, -8.74) * mm});
            skLineSegment(sketch, "E7215", {"start": v(118.89, -8.74) * mm, "end": v(118.53, -8.58) * mm});
            skLineSegment(sketch, "E7216", {"start": v(118.53, -8.58) * mm, "end": v(118.18, -8.43) * mm});
            skLineSegment(sketch, "E7217", {"start": v(118.18, -8.43) * mm, "end": v(118.06, -8.38) * mm});
            skLineSegment(sketch, "E7218", {"start": v(118.06, -8.38) * mm, "end": v(117.83, -8.28) * mm});
            skLineSegment(sketch, "E7219", {"start": v(117.83, -8.28) * mm, "end": v(117.72, -8.24) * mm});
            skLineSegment(sketch, "E7220", {"start": v(117.72, -8.24) * mm, "end": v(117.61, -8.2) * mm});
            skLineSegment(sketch, "E7221", {"start": v(117.61, -8.2) * mm, "end": v(117.5, -8.15) * mm});
            skLineSegment(sketch, "E7222", {"start": v(117.5, -8.15) * mm, "end": v(117.4, -8.1) * mm});
            skLineSegment(sketch, "E7223", {"start": v(117.4, -8.1) * mm, "end": v(117.28, -8.06) * mm});
            skLineSegment(sketch, "E7224", {"start": v(117.28, -8.06) * mm, "end": v(117.07, -7.97) * mm});
            skLineSegment(sketch, "E7225", {"start": v(117.07, -7.97) * mm, "end": v(116.96, -7.93) * mm});
            skLineSegment(sketch, "E7226", {"start": v(116.96, -7.93) * mm, "end": v(116.86, -7.9) * mm});
            skLineSegment(sketch, "E7227", {"start": v(116.86, -7.9) * mm, "end": v(116.65, -7.81) * mm});
            skLineSegment(sketch, "E7228", {"start": v(116.65, -7.81) * mm, "end": v(116.55, -7.77) * mm});
            skLineSegment(sketch, "E7229", {"start": v(116.55, -7.77) * mm, "end": v(116.45, -7.74) * mm});
            skLineSegment(sketch, "E7230", {"start": v(116.45, -7.74) * mm, "end": v(116.33, -6.77) * mm});
            skLineSegment(sketch, "E7231", {"start": v(116.33, -6.77) * mm, "end": v(116.56, -5.82) * mm});
            skLineSegment(sketch, "E7232", {"start": v(116.56, -5.82) * mm, "end": v(116.66, -5.8) * mm});
            skLineSegment(sketch, "E7233", {"start": v(116.66, -5.8) * mm, "end": v(116.77, -5.77) * mm});
            skLineSegment(sketch, "E7234", {"start": v(116.77, -5.77) * mm, "end": v(116.98, -5.71) * mm});
            skLineSegment(sketch, "E7235", {"start": v(116.98, -5.71) * mm, "end": v(117.1, -5.69) * mm});
            skLineSegment(sketch, "E7236", {"start": v(117.1, -5.69) * mm, "end": v(117.2, -5.66) * mm});
            skLineSegment(sketch, "E7237", {"start": v(117.2, -5.66) * mm, "end": v(117.31, -5.63) * mm});
            skLineSegment(sketch, "E7238", {"start": v(117.31, -5.63) * mm, "end": v(117.43, -5.6) * mm});
            skLineSegment(sketch, "E7239", {"start": v(117.43, -5.6) * mm, "end": v(117.54, -5.57) * mm});
            skLineSegment(sketch, "E7240", {"start": v(117.54, -5.57) * mm, "end": v(117.77, -5.5) * mm});
            skLineSegment(sketch, "E7241", {"start": v(117.77, -5.5) * mm, "end": v(118, -5.44) * mm});
            skLineSegment(sketch, "E7242", {"start": v(118, -5.44) * mm, "end": v(118.12, -5.4) * mm});
            skLineSegment(sketch, "E7243", {"start": v(118.12, -5.4) * mm, "end": v(118.24, -5.37) * mm});
            skLineSegment(sketch, "E7244", {"start": v(118.24, -5.37) * mm, "end": v(118.36, -5.33) * mm});
            skLineSegment(sketch, "E7245", {"start": v(118.36, -5.33) * mm, "end": v(118.48, -5.3) * mm});
            skLineSegment(sketch, "E7246", {"start": v(118.48, -5.3) * mm, "end": v(118.72, -5.22) * mm});
            skLineSegment(sketch, "E7247", {"start": v(118.72, -5.22) * mm, "end": v(118.85, -5.18) * mm});
            skLineSegment(sketch, "E7248", {"start": v(118.85, -5.18) * mm, "end": v(118.97, -5.14) * mm});
            skLineSegment(sketch, "E7249", {"start": v(118.97, -5.14) * mm, "end": v(119.1, -5.1) * mm});
            skLineSegment(sketch, "E7250", {"start": v(119.1, -5.1) * mm, "end": v(119.23, -5.06) * mm});
            skLineSegment(sketch, "E7251", {"start": v(119.23, -5.06) * mm, "end": v(119.36, -5.02) * mm});
            skLineSegment(sketch, "E7252", {"start": v(119.36, -5.02) * mm, "end": v(119.61, -4.93) * mm});
            skLineSegment(sketch, "E7253", {"start": v(119.61, -4.93) * mm, "end": v(119.75, -4.9) * mm});
            skLineSegment(sketch, "E7254", {"start": v(119.75, -4.9) * mm, "end": v(119.88, -4.85) * mm});
            skLineSegment(sketch, "E7255", {"start": v(119.88, -4.85) * mm, "end": v(120.15, -4.75) * mm});
            skLineSegment(sketch, "E7256", {"start": v(120.15, -4.75) * mm, "end": v(120.42, -4.66) * mm});
            skLineSegment(sketch, "E7257", {"start": v(120.42, -4.66) * mm, "end": v(120.55, -4.6) * mm});
            skLineSegment(sketch, "E7258", {"start": v(120.55, -4.6) * mm, "end": v(120.7, -4.56) * mm});
            skLineSegment(sketch, "E7259", {"start": v(120.7, -4.56) * mm, "end": v(120.83, -4.5) * mm});
            skLineSegment(sketch, "E7260", {"start": v(120.83, -4.5) * mm, "end": v(120.97, -4.46) * mm});
            skLineSegment(sketch, "E7261", {"start": v(120.97, -4.46) * mm, "end": v(121.1, -4.4) * mm});
            skLineSegment(sketch, "E7262", {"start": v(121.1, -4.4) * mm, "end": v(121.19, -4.35) * mm});
            skLineSegment(sketch, "E7263", {"start": v(121.19, -4.35) * mm, "end": v(121.24, -2.7) * mm});
            skLineSegment(sketch, "E7264", {"start": v(121.24, -2.7) * mm, "end": v(121.16, -2.63) * mm});
            skLineSegment(sketch, "E7265", {"start": v(121.16, -2.63) * mm, "end": v(121.02, -2.57) * mm});
            skLineSegment(sketch, "E7266", {"start": v(121.02, -2.57) * mm, "end": v(120.89, -2.51) * mm});
            skLineSegment(sketch, "E7267", {"start": v(120.89, -2.51) * mm, "end": v(120.62, -2.4) * mm});
            skLineSegment(sketch, "E7268", {"start": v(120.62, -2.4) * mm, "end": v(120.48, -2.34) * mm});
            skLineSegment(sketch, "E7269", {"start": v(120.48, -2.34) * mm, "end": v(120.35, -2.28) * mm});
            skLineSegment(sketch, "E7270", {"start": v(120.35, -2.28) * mm, "end": v(120.22, -2.23) * mm});
            skLineSegment(sketch, "E7271", {"start": v(120.22, -2.23) * mm, "end": v(120.09, -2.17) * mm});
            skLineSegment(sketch, "E7272", {"start": v(120.09, -2.17) * mm, "end": v(119.96, -2.12) * mm});
            skLineSegment(sketch, "E7273", {"start": v(119.96, -2.12) * mm, "end": v(119.83, -2.07) * mm});
            skLineSegment(sketch, "E7274", {"start": v(119.83, -2.07) * mm, "end": v(119.57, -1.96) * mm});
            skLineSegment(sketch, "E7275", {"start": v(119.57, -1.96) * mm, "end": v(119.32, -1.87) * mm});
            skLineSegment(sketch, "E7276", {"start": v(119.32, -1.87) * mm, "end": v(119.2, -1.82) * mm});
            skLineSegment(sketch, "E7277", {"start": v(119.2, -1.82) * mm, "end": v(119.07, -1.77) * mm});
            skLineSegment(sketch, "E7278", {"start": v(119.07, -1.77) * mm, "end": v(118.95, -1.72) * mm});
            skLineSegment(sketch, "E7279", {"start": v(118.95, -1.72) * mm, "end": v(118.7, -1.63) * mm});
            skLineSegment(sketch, "E7280", {"start": v(118.7, -1.63) * mm, "end": v(118.59, -1.59) * mm});
            skLineSegment(sketch, "E7281", {"start": v(118.59, -1.59) * mm, "end": v(118.47, -1.54) * mm});
            skLineSegment(sketch, "E7282", {"start": v(118.47, -1.54) * mm, "end": v(118.35, -1.5) * mm});
            skLineSegment(sketch, "E7283", {"start": v(118.35, -1.5) * mm, "end": v(118.23, -1.46) * mm});
            skLineSegment(sketch, "E7284", {"start": v(118.23, -1.46) * mm, "end": v(118.12, -1.42) * mm});
            skLineSegment(sketch, "E7285", {"start": v(118.12, -1.42) * mm, "end": v(117.89, -1.34) * mm});
            skLineSegment(sketch, "E7286", {"start": v(117.89, -1.34) * mm, "end": v(117.78, -1.3) * mm});
            skLineSegment(sketch, "E7287", {"start": v(117.78, -1.3) * mm, "end": v(117.66, -1.26) * mm});
            skLineSegment(sketch, "E7288", {"start": v(117.66, -1.26) * mm, "end": v(117.55, -1.23) * mm});
            skLineSegment(sketch, "E7289", {"start": v(117.55, -1.23) * mm, "end": v(117.44, -1.19) * mm});
            skLineSegment(sketch, "E7290", {"start": v(117.44, -1.19) * mm, "end": v(117.22, -1.12) * mm});
            skLineSegment(sketch, "E7291", {"start": v(117.22, -1.12) * mm, "end": v(117.12, -1.08) * mm});
            skLineSegment(sketch, "E7292", {"start": v(117.12, -1.08) * mm, "end": v(116.9, -1.02) * mm});
            skLineSegment(sketch, "E7293", {"start": v(116.9, -1.02) * mm, "end": v(116.8, -0.98) * mm});
            skLineSegment(sketch, "E7294", {"start": v(116.8, -0.98) * mm, "end": v(116.7, -0.95) * mm});
            skLineSegment(sketch, "E7295", {"start": v(116.7, -0.95) * mm, "end": v(116.53, 0) * mm});
            skLineSegment(sketch, "E7296", {"start": v(2.65, 0) * mm, "end": v(-2.65, 0) * mm});
            skLineSegment(sketch, "E7297", {"start": v(0, -2.65) * mm, "end": v(0, 2.65) * mm});
            skCircle(sketch, "E7298", {"center": v(0, 0) * mm, "radius": 4.33 * mm});
            skSolve(sketch);
        }
        {
            var Q0;
            Q0 = qSketchRegion(id + "F0", true);
            extrude(context, id + "F1", {"entities" : qUnion([Q0]), "depth" : 6.35 * mm, "offsetDistance" : 25.4 * mm});
        }
    });
